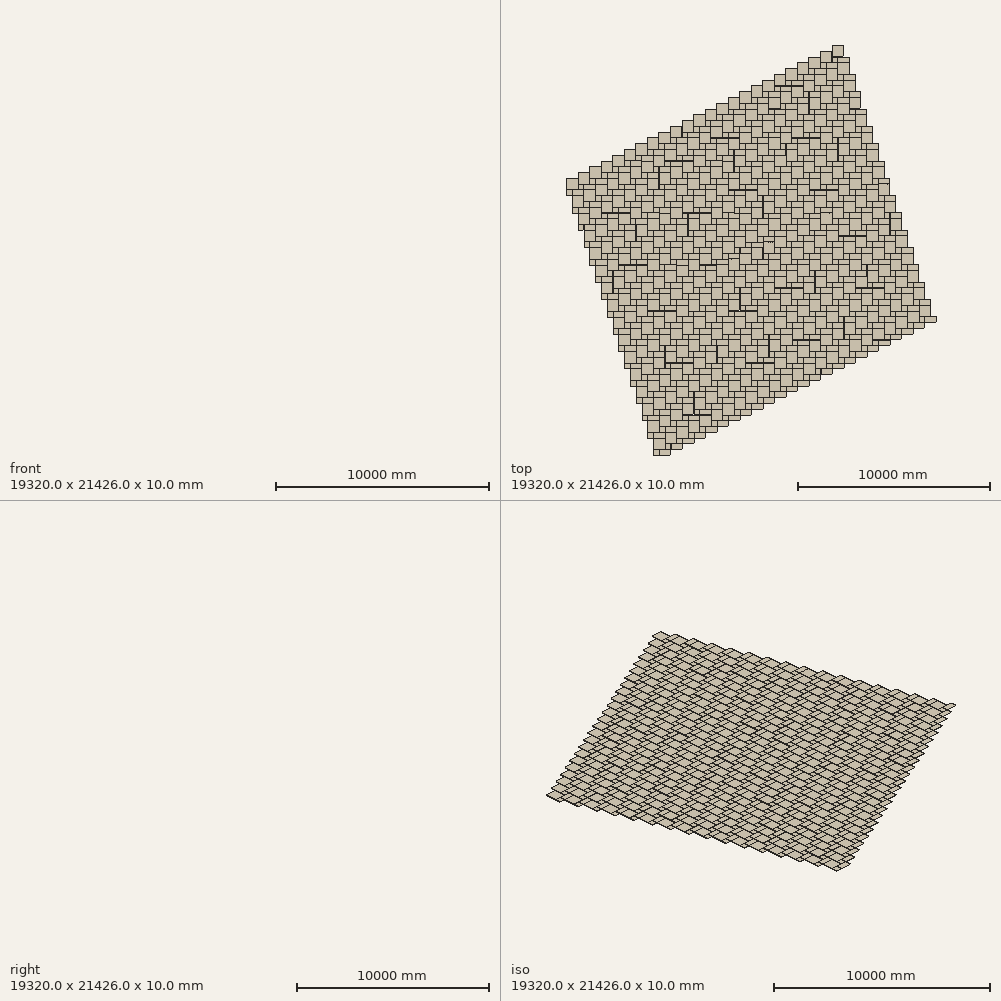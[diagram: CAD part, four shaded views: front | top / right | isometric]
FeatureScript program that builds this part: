
annotation { "Feature Type Name" : "Feature", "Feature Type Description" : "" }
export const myFeature = defineFeature(function(context is Context, id is Id, definition is map)
    precondition{}
    {
        {
            var Q0;
            Q0=qCreatedBy(makeId("Top.planeOp"),FACE);
            var sketch = newSketch(context, id + "F0", { "sketchPlane" : qUnion([Q0])});
            skLineSegment(sketch, "E0.bottom", {"start": v(-467.78, 21.53) * mm, "end": v(132.22, 21.53) * mm});
            skLineSegment(sketch, "E0.top", {"start": v(-467.78, 621.53) * mm, "end": v(132.22, 621.53) * mm});
            skLineSegment(sketch, "E0.left", {"start": v(-467.78, 21.53) * mm, "end": v(-467.78, 621.53) * mm});
            skLineSegment(sketch, "E0.right", {"start": v(132.22, 21.53) * mm, "end": v(132.22, 621.53) * mm});
            skLineSegment(sketch, "E1.bottom", {"start": v(-467.78, 18.53) * mm, "end": v(-167.78, 18.53) * mm});
            skLineSegment(sketch, "E1.top", {"start": v(-467.78, -281.47) * mm, "end": v(-167.78, -281.47) * mm});
            skLineSegment(sketch, "E1.left", {"start": v(-467.78, 18.53) * mm, "end": v(-467.78, -281.47) * mm});
            skLineSegment(sketch, "E1.right", {"start": v(-167.78, 18.53) * mm, "end": v(-167.78, -281.47) * mm});
            skLineSegment(sketch, "E2.bottom", {"start": v(-164.78, 18.53) * mm, "end": v(435.22, 18.53) * mm});
            skLineSegment(sketch, "E2.top", {"start": v(-164.78, -281.47) * mm, "end": v(435.22, -281.47) * mm});
            skLineSegment(sketch, "E2.left", {"start": v(-164.78, 18.53) * mm, "end": v(-164.78, -281.47) * mm});
            skLineSegment(sketch, "E2.right", {"start": v(435.22, 18.53) * mm, "end": v(435.22, -281.47) * mm});
            skSolve(sketch);
        }
        {
            var Q0;
            Q0 = qSketchRegion(id + "F0", true);
            extrude(context, id + "F1", {"entities" : qUnion([Q0]), "depth" : 10 * mm});
        }
        {
            var Q0;
            Q0=makeQuery(id+"F1.opExtrude","SWEPT_BODY",BODY,{"disambiguationData":[OSD([sQuery(id+"F0.wireOp",EDGE,"E0.bottom"),sQuery(id+"F0.wireOp",EDGE,"E0.top"),sQuery(id+"F0.wireOp",EDGE,"E0.left"),sQuery(id+"F0.wireOp",EDGE,"E0.right")])]});
            var Q1;
            Q1=makeQuery(id+"F1.opExtrude","SWEPT_BODY",BODY,{"disambiguationData":[OSD([sQuery(id+"F0.wireOp",EDGE,"E1.bottom"),sQuery(id+"F0.wireOp",EDGE,"E1.top"),sQuery(id+"F0.wireOp",EDGE,"E1.left"),sQuery(id+"F0.wireOp",EDGE,"E1.right")])]});
            var Q2;
            Q2=makeQuery(id+"F1.opExtrude","SWEPT_BODY",BODY,{"disambiguationData":[OSD([sQuery(id+"F0.wireOp",EDGE,"E2.bottom"),sQuery(id+"F0.wireOp",EDGE,"E2.top"),sQuery(id+"F0.wireOp",EDGE,"E2.left"),sQuery(id+"F0.wireOp",EDGE,"E2.right")])]});
            transform(context, id + "F2", {"entities" : qUnion([Q0, Q1, Q2]), "transformType" : TransformType.TRANSLATION_3D, "dx" : 603 * mm, "dy" : 303 * mm, "dz" : 0 * mm, "makeCopy" : true});
        }
        {
            var Q0;
            Q0=makeQuery(id+"F2.opPattern","COPY",BODY,{"derivedFrom":makeQuery(id+"F1.opExtrude","SWEPT_BODY",BODY,{"disambiguationData":[OSD([sQuery(id+"F0.wireOp",EDGE,"E0.bottom"),sQuery(id+"F0.wireOp",EDGE,"E0.top"),sQuery(id+"F0.wireOp",EDGE,"E0.left"),sQuery(id+"F0.wireOp",EDGE,"E0.right")])]}),"instanceName":"1"});
            var Q1;
            Q1=makeQuery(id+"F2.opPattern","COPY",BODY,{"derivedFrom":makeQuery(id+"F1.opExtrude","SWEPT_BODY",BODY,{"disambiguationData":[OSD([sQuery(id+"F0.wireOp",EDGE,"E1.bottom"),sQuery(id+"F0.wireOp",EDGE,"E1.top"),sQuery(id+"F0.wireOp",EDGE,"E1.left"),sQuery(id+"F0.wireOp",EDGE,"E1.right")])]}),"instanceName":"1"});
            var Q2;
            Q2=makeQuery(id+"F2.opPattern","COPY",BODY,{"derivedFrom":makeQuery(id+"F1.opExtrude","SWEPT_BODY",BODY,{"disambiguationData":[OSD([sQuery(id+"F0.wireOp",EDGE,"E2.bottom"),sQuery(id+"F0.wireOp",EDGE,"E2.top"),sQuery(id+"F0.wireOp",EDGE,"E2.left"),sQuery(id+"F0.wireOp",EDGE,"E2.right")])]}),"instanceName":"1"});
            transform(context, id + "F3", {"entities" : qUnion([Q0, Q1, Q2]), "transformType" : TransformType.TRANSLATION_3D, "dx" : 603 * mm, "dy" : 303 * mm, "dz" : 0 * mm, "makeCopy" : true});
        }
        {
            var Q0;
            Q0=makeQuery(id+"F3.opPattern","COPY",BODY,{"derivedFrom":makeQuery(id+"F2.opPattern","COPY",BODY,{"derivedFrom":makeQuery(id+"F1.opExtrude","SWEPT_BODY",BODY,{"disambiguationData":[OSD([sQuery(id+"F0.wireOp",EDGE,"E0.bottom"),sQuery(id+"F0.wireOp",EDGE,"E0.top"),sQuery(id+"F0.wireOp",EDGE,"E0.left"),sQuery(id+"F0.wireOp",EDGE,"E0.right")])]}),"instanceName":"1"}),"instanceName":"1"});
            var Q1;
            Q1=makeQuery(id+"F3.opPattern","COPY",BODY,{"derivedFrom":makeQuery(id+"F2.opPattern","COPY",BODY,{"derivedFrom":makeQuery(id+"F1.opExtrude","SWEPT_BODY",BODY,{"disambiguationData":[OSD([sQuery(id+"F0.wireOp",EDGE,"E1.bottom"),sQuery(id+"F0.wireOp",EDGE,"E1.top"),sQuery(id+"F0.wireOp",EDGE,"E1.left"),sQuery(id+"F0.wireOp",EDGE,"E1.right")])]}),"instanceName":"1"}),"instanceName":"1"});
            var Q2;
            Q2=makeQuery(id+"F3.opPattern","COPY",BODY,{"derivedFrom":makeQuery(id+"F2.opPattern","COPY",BODY,{"derivedFrom":makeQuery(id+"F1.opExtrude","SWEPT_BODY",BODY,{"disambiguationData":[OSD([sQuery(id+"F0.wireOp",EDGE,"E2.bottom"),sQuery(id+"F0.wireOp",EDGE,"E2.top"),sQuery(id+"F0.wireOp",EDGE,"E2.left"),sQuery(id+"F0.wireOp",EDGE,"E2.right")])]}),"instanceName":"1"}),"instanceName":"1"});
            transform(context, id + "F4", {"entities" : qUnion([Q0, Q1, Q2]), "transformType" : TransformType.TRANSLATION_3D, "dx" : 603 * mm, "dy" : 303 * mm, "dz" : 0 * mm, "makeCopy" : true});
        }
        {
            var Q0;
            Q0=makeQuery(id+"F4.opPattern","COPY",BODY,{"derivedFrom":makeQuery(id+"F3.opPattern","COPY",BODY,{"derivedFrom":makeQuery(id+"F2.opPattern","COPY",BODY,{"derivedFrom":makeQuery(id+"F1.opExtrude","SWEPT_BODY",BODY,{"disambiguationData":[OSD([sQuery(id+"F0.wireOp",EDGE,"E0.bottom"),sQuery(id+"F0.wireOp",EDGE,"E0.top"),sQuery(id+"F0.wireOp",EDGE,"E0.left"),sQuery(id+"F0.wireOp",EDGE,"E0.right")])]}),"instanceName":"1"}),"instanceName":"1"}),"instanceName":"1"});
            var Q1;
            Q1=makeQuery(id+"F4.opPattern","COPY",BODY,{"derivedFrom":makeQuery(id+"F3.opPattern","COPY",BODY,{"derivedFrom":makeQuery(id+"F2.opPattern","COPY",BODY,{"derivedFrom":makeQuery(id+"F1.opExtrude","SWEPT_BODY",BODY,{"disambiguationData":[OSD([sQuery(id+"F0.wireOp",EDGE,"E1.bottom"),sQuery(id+"F0.wireOp",EDGE,"E1.top"),sQuery(id+"F0.wireOp",EDGE,"E1.left"),sQuery(id+"F0.wireOp",EDGE,"E1.right")])]}),"instanceName":"1"}),"instanceName":"1"}),"instanceName":"1"});
            var Q2;
            Q2=makeQuery(id+"F4.opPattern","COPY",BODY,{"derivedFrom":makeQuery(id+"F3.opPattern","COPY",BODY,{"derivedFrom":makeQuery(id+"F2.opPattern","COPY",BODY,{"derivedFrom":makeQuery(id+"F1.opExtrude","SWEPT_BODY",BODY,{"disambiguationData":[OSD([sQuery(id+"F0.wireOp",EDGE,"E2.bottom"),sQuery(id+"F0.wireOp",EDGE,"E2.top"),sQuery(id+"F0.wireOp",EDGE,"E2.left"),sQuery(id+"F0.wireOp",EDGE,"E2.right")])]}),"instanceName":"1"}),"instanceName":"1"}),"instanceName":"1"});
            transform(context, id + "F5", {"entities" : qUnion([Q0, Q1, Q2]), "transformType" : TransformType.TRANSLATION_3D, "dx" : 603 * mm, "dy" : 303 * mm, "dz" : 0 * mm, "makeCopy" : true});
        }
        {
            var Q0;
            Q0=makeQuery(id+"F5.opPattern","COPY",BODY,{"derivedFrom":makeQuery(id+"F4.opPattern","COPY",BODY,{"derivedFrom":makeQuery(id+"F3.opPattern","COPY",BODY,{"derivedFrom":makeQuery(id+"F2.opPattern","COPY",BODY,{"derivedFrom":makeQuery(id+"F1.opExtrude","SWEPT_BODY",BODY,{"disambiguationData":[OSD([sQuery(id+"F0.wireOp",EDGE,"E0.bottom"),sQuery(id+"F0.wireOp",EDGE,"E0.top"),sQuery(id+"F0.wireOp",EDGE,"E0.left"),sQuery(id+"F0.wireOp",EDGE,"E0.right")])]}),"instanceName":"1"}),"instanceName":"1"}),"instanceName":"1"}),"instanceName":"1"});
            var Q1;
            Q1=makeQuery(id+"F5.opPattern","COPY",BODY,{"derivedFrom":makeQuery(id+"F4.opPattern","COPY",BODY,{"derivedFrom":makeQuery(id+"F3.opPattern","COPY",BODY,{"derivedFrom":makeQuery(id+"F2.opPattern","COPY",BODY,{"derivedFrom":makeQuery(id+"F1.opExtrude","SWEPT_BODY",BODY,{"disambiguationData":[OSD([sQuery(id+"F0.wireOp",EDGE,"E1.bottom"),sQuery(id+"F0.wireOp",EDGE,"E1.top"),sQuery(id+"F0.wireOp",EDGE,"E1.left"),sQuery(id+"F0.wireOp",EDGE,"E1.right")])]}),"instanceName":"1"}),"instanceName":"1"}),"instanceName":"1"}),"instanceName":"1"});
            var Q2;
            Q2=makeQuery(id+"F5.opPattern","COPY",BODY,{"derivedFrom":makeQuery(id+"F4.opPattern","COPY",BODY,{"derivedFrom":makeQuery(id+"F3.opPattern","COPY",BODY,{"derivedFrom":makeQuery(id+"F2.opPattern","COPY",BODY,{"derivedFrom":makeQuery(id+"F1.opExtrude","SWEPT_BODY",BODY,{"disambiguationData":[OSD([sQuery(id+"F0.wireOp",EDGE,"E2.bottom"),sQuery(id+"F0.wireOp",EDGE,"E2.top"),sQuery(id+"F0.wireOp",EDGE,"E2.left"),sQuery(id+"F0.wireOp",EDGE,"E2.right")])]}),"instanceName":"1"}),"instanceName":"1"}),"instanceName":"1"}),"instanceName":"1"});
            transform(context, id + "F6", {"entities" : qUnion([Q0, Q1, Q2]), "transformType" : TransformType.TRANSLATION_3D, "dx" : 603 * mm, "dy" : 303 * mm, "dz" : 0 * mm, "makeCopy" : true});
        }
        {
            var Q0;
            Q0=makeQuery(id+"F1.opExtrude","SWEPT_BODY",BODY,{"disambiguationData":[OSD([sQuery(id+"F0.wireOp",EDGE,"E1.bottom"),sQuery(id+"F0.wireOp",EDGE,"E1.top"),sQuery(id+"F0.wireOp",EDGE,"E1.left"),sQuery(id+"F0.wireOp",EDGE,"E1.right")])]});
            var Q1;
            Q1=makeQuery(id+"F1.opExtrude","SWEPT_BODY",BODY,{"disambiguationData":[OSD([sQuery(id+"F0.wireOp",EDGE,"E2.bottom"),sQuery(id+"F0.wireOp",EDGE,"E2.top"),sQuery(id+"F0.wireOp",EDGE,"E2.left"),sQuery(id+"F0.wireOp",EDGE,"E2.right")])]});
            var Q2;
            Q2=makeQuery(id+"F1.opExtrude","SWEPT_BODY",BODY,{"disambiguationData":[OSD([sQuery(id+"F0.wireOp",EDGE,"E0.bottom"),sQuery(id+"F0.wireOp",EDGE,"E0.top"),sQuery(id+"F0.wireOp",EDGE,"E0.left"),sQuery(id+"F0.wireOp",EDGE,"E0.right")])]});
            var Q3;
            Q3=makeQuery(id+"F2.opPattern","COPY",BODY,{"derivedFrom":makeQuery(id+"F1.opExtrude","SWEPT_BODY",BODY,{"disambiguationData":[OSD([sQuery(id+"F0.wireOp",EDGE,"E1.bottom"),sQuery(id+"F0.wireOp",EDGE,"E1.top"),sQuery(id+"F0.wireOp",EDGE,"E1.left"),sQuery(id+"F0.wireOp",EDGE,"E1.right")])]}),"instanceName":"1"});
            var Q4;
            Q4=makeQuery(id+"F2.opPattern","COPY",BODY,{"derivedFrom":makeQuery(id+"F1.opExtrude","SWEPT_BODY",BODY,{"disambiguationData":[OSD([sQuery(id+"F0.wireOp",EDGE,"E0.bottom"),sQuery(id+"F0.wireOp",EDGE,"E0.top"),sQuery(id+"F0.wireOp",EDGE,"E0.left"),sQuery(id+"F0.wireOp",EDGE,"E0.right")])]}),"instanceName":"1"});
            var Q5;
            Q5=makeQuery(id+"F2.opPattern","COPY",BODY,{"derivedFrom":makeQuery(id+"F1.opExtrude","SWEPT_BODY",BODY,{"disambiguationData":[OSD([sQuery(id+"F0.wireOp",EDGE,"E2.bottom"),sQuery(id+"F0.wireOp",EDGE,"E2.top"),sQuery(id+"F0.wireOp",EDGE,"E2.left"),sQuery(id+"F0.wireOp",EDGE,"E2.right")])]}),"instanceName":"1"});
            var Q6;
            Q6=makeQuery(id+"F3.opPattern","COPY",BODY,{"derivedFrom":makeQuery(id+"F2.opPattern","COPY",BODY,{"derivedFrom":makeQuery(id+"F1.opExtrude","SWEPT_BODY",BODY,{"disambiguationData":[OSD([sQuery(id+"F0.wireOp",EDGE,"E1.bottom"),sQuery(id+"F0.wireOp",EDGE,"E1.top"),sQuery(id+"F0.wireOp",EDGE,"E1.left"),sQuery(id+"F0.wireOp",EDGE,"E1.right")])]}),"instanceName":"1"}),"instanceName":"1"});
            var Q7;
            Q7=makeQuery(id+"F3.opPattern","COPY",BODY,{"derivedFrom":makeQuery(id+"F2.opPattern","COPY",BODY,{"derivedFrom":makeQuery(id+"F1.opExtrude","SWEPT_BODY",BODY,{"disambiguationData":[OSD([sQuery(id+"F0.wireOp",EDGE,"E2.bottom"),sQuery(id+"F0.wireOp",EDGE,"E2.top"),sQuery(id+"F0.wireOp",EDGE,"E2.left"),sQuery(id+"F0.wireOp",EDGE,"E2.right")])]}),"instanceName":"1"}),"instanceName":"1"});
            var Q8;
            Q8=makeQuery(id+"F3.opPattern","COPY",BODY,{"derivedFrom":makeQuery(id+"F2.opPattern","COPY",BODY,{"derivedFrom":makeQuery(id+"F1.opExtrude","SWEPT_BODY",BODY,{"disambiguationData":[OSD([sQuery(id+"F0.wireOp",EDGE,"E0.bottom"),sQuery(id+"F0.wireOp",EDGE,"E0.top"),sQuery(id+"F0.wireOp",EDGE,"E0.left"),sQuery(id+"F0.wireOp",EDGE,"E0.right")])]}),"instanceName":"1"}),"instanceName":"1"});
            var Q9;
            Q9=makeQuery(id+"F4.opPattern","COPY",BODY,{"derivedFrom":makeQuery(id+"F3.opPattern","COPY",BODY,{"derivedFrom":makeQuery(id+"F2.opPattern","COPY",BODY,{"derivedFrom":makeQuery(id+"F1.opExtrude","SWEPT_BODY",BODY,{"disambiguationData":[OSD([sQuery(id+"F0.wireOp",EDGE,"E1.bottom"),sQuery(id+"F0.wireOp",EDGE,"E1.top"),sQuery(id+"F0.wireOp",EDGE,"E1.left"),sQuery(id+"F0.wireOp",EDGE,"E1.right")])]}),"instanceName":"1"}),"instanceName":"1"}),"instanceName":"1"});
            var Q10;
            Q10=makeQuery(id+"F4.opPattern","COPY",BODY,{"derivedFrom":makeQuery(id+"F3.opPattern","COPY",BODY,{"derivedFrom":makeQuery(id+"F2.opPattern","COPY",BODY,{"derivedFrom":makeQuery(id+"F1.opExtrude","SWEPT_BODY",BODY,{"disambiguationData":[OSD([sQuery(id+"F0.wireOp",EDGE,"E2.bottom"),sQuery(id+"F0.wireOp",EDGE,"E2.top"),sQuery(id+"F0.wireOp",EDGE,"E2.left"),sQuery(id+"F0.wireOp",EDGE,"E2.right")])]}),"instanceName":"1"}),"instanceName":"1"}),"instanceName":"1"});
            var Q11;
            Q11=makeQuery(id+"F4.opPattern","COPY",BODY,{"derivedFrom":makeQuery(id+"F3.opPattern","COPY",BODY,{"derivedFrom":makeQuery(id+"F2.opPattern","COPY",BODY,{"derivedFrom":makeQuery(id+"F1.opExtrude","SWEPT_BODY",BODY,{"disambiguationData":[OSD([sQuery(id+"F0.wireOp",EDGE,"E0.bottom"),sQuery(id+"F0.wireOp",EDGE,"E0.top"),sQuery(id+"F0.wireOp",EDGE,"E0.left"),sQuery(id+"F0.wireOp",EDGE,"E0.right")])]}),"instanceName":"1"}),"instanceName":"1"}),"instanceName":"1"});
            var Q12;
            Q12=makeQuery(id+"F5.opPattern","COPY",BODY,{"derivedFrom":makeQuery(id+"F4.opPattern","COPY",BODY,{"derivedFrom":makeQuery(id+"F3.opPattern","COPY",BODY,{"derivedFrom":makeQuery(id+"F2.opPattern","COPY",BODY,{"derivedFrom":makeQuery(id+"F1.opExtrude","SWEPT_BODY",BODY,{"disambiguationData":[OSD([sQuery(id+"F0.wireOp",EDGE,"E1.bottom"),sQuery(id+"F0.wireOp",EDGE,"E1.top"),sQuery(id+"F0.wireOp",EDGE,"E1.left"),sQuery(id+"F0.wireOp",EDGE,"E1.right")])]}),"instanceName":"1"}),"instanceName":"1"}),"instanceName":"1"}),"instanceName":"1"});
            var Q13;
            Q13=makeQuery(id+"F5.opPattern","COPY",BODY,{"derivedFrom":makeQuery(id+"F4.opPattern","COPY",BODY,{"derivedFrom":makeQuery(id+"F3.opPattern","COPY",BODY,{"derivedFrom":makeQuery(id+"F2.opPattern","COPY",BODY,{"derivedFrom":makeQuery(id+"F1.opExtrude","SWEPT_BODY",BODY,{"disambiguationData":[OSD([sQuery(id+"F0.wireOp",EDGE,"E2.bottom"),sQuery(id+"F0.wireOp",EDGE,"E2.top"),sQuery(id+"F0.wireOp",EDGE,"E2.left"),sQuery(id+"F0.wireOp",EDGE,"E2.right")])]}),"instanceName":"1"}),"instanceName":"1"}),"instanceName":"1"}),"instanceName":"1"});
            var Q14;
            Q14=makeQuery(id+"F5.opPattern","COPY",BODY,{"derivedFrom":makeQuery(id+"F4.opPattern","COPY",BODY,{"derivedFrom":makeQuery(id+"F3.opPattern","COPY",BODY,{"derivedFrom":makeQuery(id+"F2.opPattern","COPY",BODY,{"derivedFrom":makeQuery(id+"F1.opExtrude","SWEPT_BODY",BODY,{"disambiguationData":[OSD([sQuery(id+"F0.wireOp",EDGE,"E0.bottom"),sQuery(id+"F0.wireOp",EDGE,"E0.top"),sQuery(id+"F0.wireOp",EDGE,"E0.left"),sQuery(id+"F0.wireOp",EDGE,"E0.right")])]}),"instanceName":"1"}),"instanceName":"1"}),"instanceName":"1"}),"instanceName":"1"});
            var Q15;
            Q15=makeQuery(id+"F6.opPattern","COPY",BODY,{"derivedFrom":makeQuery(id+"F5.opPattern","COPY",BODY,{"derivedFrom":makeQuery(id+"F4.opPattern","COPY",BODY,{"derivedFrom":makeQuery(id+"F3.opPattern","COPY",BODY,{"derivedFrom":makeQuery(id+"F2.opPattern","COPY",BODY,{"derivedFrom":makeQuery(id+"F1.opExtrude","SWEPT_BODY",BODY,{"disambiguationData":[OSD([sQuery(id+"F0.wireOp",EDGE,"E1.bottom"),sQuery(id+"F0.wireOp",EDGE,"E1.top"),sQuery(id+"F0.wireOp",EDGE,"E1.left"),sQuery(id+"F0.wireOp",EDGE,"E1.right")])]}),"instanceName":"1"}),"instanceName":"1"}),"instanceName":"1"}),"instanceName":"1"}),"instanceName":"1"});
            var Q16;
            Q16=makeQuery(id+"F6.opPattern","COPY",BODY,{"derivedFrom":makeQuery(id+"F5.opPattern","COPY",BODY,{"derivedFrom":makeQuery(id+"F4.opPattern","COPY",BODY,{"derivedFrom":makeQuery(id+"F3.opPattern","COPY",BODY,{"derivedFrom":makeQuery(id+"F2.opPattern","COPY",BODY,{"derivedFrom":makeQuery(id+"F1.opExtrude","SWEPT_BODY",BODY,{"disambiguationData":[OSD([sQuery(id+"F0.wireOp",EDGE,"E0.bottom"),sQuery(id+"F0.wireOp",EDGE,"E0.top"),sQuery(id+"F0.wireOp",EDGE,"E0.left"),sQuery(id+"F0.wireOp",EDGE,"E0.right")])]}),"instanceName":"1"}),"instanceName":"1"}),"instanceName":"1"}),"instanceName":"1"}),"instanceName":"1"});
            var Q17;
            Q17=makeQuery(id+"F6.opPattern","COPY",BODY,{"derivedFrom":makeQuery(id+"F5.opPattern","COPY",BODY,{"derivedFrom":makeQuery(id+"F4.opPattern","COPY",BODY,{"derivedFrom":makeQuery(id+"F3.opPattern","COPY",BODY,{"derivedFrom":makeQuery(id+"F2.opPattern","COPY",BODY,{"derivedFrom":makeQuery(id+"F1.opExtrude","SWEPT_BODY",BODY,{"disambiguationData":[OSD([sQuery(id+"F0.wireOp",EDGE,"E2.bottom"),sQuery(id+"F0.wireOp",EDGE,"E2.top"),sQuery(id+"F0.wireOp",EDGE,"E2.left"),sQuery(id+"F0.wireOp",EDGE,"E2.right")])]}),"instanceName":"1"}),"instanceName":"1"}),"instanceName":"1"}),"instanceName":"1"}),"instanceName":"1"});
            transform(context, id + "F7", {"entities" : qUnion([Q0, Q1, Q2, Q3, Q4, Q5, Q6, Q7, Q8, Q9, Q10, Q11, Q12, Q13, Q14, Q15, Q16, Q17]), "transformType" : TransformType.TRANSLATION_3D, "dx" : -303 * mm, "dy" : 906 * mm, "dz" : 0 * mm, "makeCopy" : true});
        }
        {
            var Q0;
            Q0=makeQuery(id+"F1.opExtrude","SWEPT_BODY",BODY,{"disambiguationData":[OSD([sQuery(id+"F0.wireOp",EDGE,"E1.bottom"),sQuery(id+"F0.wireOp",EDGE,"E1.top"),sQuery(id+"F0.wireOp",EDGE,"E1.left"),sQuery(id+"F0.wireOp",EDGE,"E1.right")])]});
            var Q1;
            Q1=makeQuery(id+"F1.opExtrude","SWEPT_BODY",BODY,{"disambiguationData":[OSD([sQuery(id+"F0.wireOp",EDGE,"E2.bottom"),sQuery(id+"F0.wireOp",EDGE,"E2.top"),sQuery(id+"F0.wireOp",EDGE,"E2.left"),sQuery(id+"F0.wireOp",EDGE,"E2.right")])]});
            var Q2;
            Q2=makeQuery(id+"F1.opExtrude","SWEPT_BODY",BODY,{"disambiguationData":[OSD([sQuery(id+"F0.wireOp",EDGE,"E0.bottom"),sQuery(id+"F0.wireOp",EDGE,"E0.top"),sQuery(id+"F0.wireOp",EDGE,"E0.left"),sQuery(id+"F0.wireOp",EDGE,"E0.right")])]});
            var Q3;
            Q3=makeQuery(id+"F2.opPattern","COPY",BODY,{"derivedFrom":makeQuery(id+"F1.opExtrude","SWEPT_BODY",BODY,{"disambiguationData":[OSD([sQuery(id+"F0.wireOp",EDGE,"E1.bottom"),sQuery(id+"F0.wireOp",EDGE,"E1.top"),sQuery(id+"F0.wireOp",EDGE,"E1.left"),sQuery(id+"F0.wireOp",EDGE,"E1.right")])]}),"instanceName":"1"});
            var Q4;
            Q4=makeQuery(id+"F2.opPattern","COPY",BODY,{"derivedFrom":makeQuery(id+"F1.opExtrude","SWEPT_BODY",BODY,{"disambiguationData":[OSD([sQuery(id+"F0.wireOp",EDGE,"E2.bottom"),sQuery(id+"F0.wireOp",EDGE,"E2.top"),sQuery(id+"F0.wireOp",EDGE,"E2.left"),sQuery(id+"F0.wireOp",EDGE,"E2.right")])]}),"instanceName":"1"});
            var Q5;
            Q5=makeQuery(id+"F2.opPattern","COPY",BODY,{"derivedFrom":makeQuery(id+"F1.opExtrude","SWEPT_BODY",BODY,{"disambiguationData":[OSD([sQuery(id+"F0.wireOp",EDGE,"E0.bottom"),sQuery(id+"F0.wireOp",EDGE,"E0.top"),sQuery(id+"F0.wireOp",EDGE,"E0.left"),sQuery(id+"F0.wireOp",EDGE,"E0.right")])]}),"instanceName":"1"});
            var Q6;
            Q6=makeQuery(id+"F3.opPattern","COPY",BODY,{"derivedFrom":makeQuery(id+"F2.opPattern","COPY",BODY,{"derivedFrom":makeQuery(id+"F1.opExtrude","SWEPT_BODY",BODY,{"disambiguationData":[OSD([sQuery(id+"F0.wireOp",EDGE,"E1.bottom"),sQuery(id+"F0.wireOp",EDGE,"E1.top"),sQuery(id+"F0.wireOp",EDGE,"E1.left"),sQuery(id+"F0.wireOp",EDGE,"E1.right")])]}),"instanceName":"1"}),"instanceName":"1"});
            var Q7;
            Q7=makeQuery(id+"F3.opPattern","COPY",BODY,{"derivedFrom":makeQuery(id+"F2.opPattern","COPY",BODY,{"derivedFrom":makeQuery(id+"F1.opExtrude","SWEPT_BODY",BODY,{"disambiguationData":[OSD([sQuery(id+"F0.wireOp",EDGE,"E2.bottom"),sQuery(id+"F0.wireOp",EDGE,"E2.top"),sQuery(id+"F0.wireOp",EDGE,"E2.left"),sQuery(id+"F0.wireOp",EDGE,"E2.right")])]}),"instanceName":"1"}),"instanceName":"1"});
            var Q8;
            Q8=makeQuery(id+"F3.opPattern","COPY",BODY,{"derivedFrom":makeQuery(id+"F2.opPattern","COPY",BODY,{"derivedFrom":makeQuery(id+"F1.opExtrude","SWEPT_BODY",BODY,{"disambiguationData":[OSD([sQuery(id+"F0.wireOp",EDGE,"E0.bottom"),sQuery(id+"F0.wireOp",EDGE,"E0.top"),sQuery(id+"F0.wireOp",EDGE,"E0.left"),sQuery(id+"F0.wireOp",EDGE,"E0.right")])]}),"instanceName":"1"}),"instanceName":"1"});
            var Q9;
            Q9=makeQuery(id+"F4.opPattern","COPY",BODY,{"derivedFrom":makeQuery(id+"F3.opPattern","COPY",BODY,{"derivedFrom":makeQuery(id+"F2.opPattern","COPY",BODY,{"derivedFrom":makeQuery(id+"F1.opExtrude","SWEPT_BODY",BODY,{"disambiguationData":[OSD([sQuery(id+"F0.wireOp",EDGE,"E1.bottom"),sQuery(id+"F0.wireOp",EDGE,"E1.top"),sQuery(id+"F0.wireOp",EDGE,"E1.left"),sQuery(id+"F0.wireOp",EDGE,"E1.right")])]}),"instanceName":"1"}),"instanceName":"1"}),"instanceName":"1"});
            var Q10;
            Q10=makeQuery(id+"F4.opPattern","COPY",BODY,{"derivedFrom":makeQuery(id+"F3.opPattern","COPY",BODY,{"derivedFrom":makeQuery(id+"F2.opPattern","COPY",BODY,{"derivedFrom":makeQuery(id+"F1.opExtrude","SWEPT_BODY",BODY,{"disambiguationData":[OSD([sQuery(id+"F0.wireOp",EDGE,"E2.bottom"),sQuery(id+"F0.wireOp",EDGE,"E2.top"),sQuery(id+"F0.wireOp",EDGE,"E2.left"),sQuery(id+"F0.wireOp",EDGE,"E2.right")])]}),"instanceName":"1"}),"instanceName":"1"}),"instanceName":"1"});
            var Q11;
            Q11=makeQuery(id+"F4.opPattern","COPY",BODY,{"derivedFrom":makeQuery(id+"F3.opPattern","COPY",BODY,{"derivedFrom":makeQuery(id+"F2.opPattern","COPY",BODY,{"derivedFrom":makeQuery(id+"F1.opExtrude","SWEPT_BODY",BODY,{"disambiguationData":[OSD([sQuery(id+"F0.wireOp",EDGE,"E0.bottom"),sQuery(id+"F0.wireOp",EDGE,"E0.top"),sQuery(id+"F0.wireOp",EDGE,"E0.left"),sQuery(id+"F0.wireOp",EDGE,"E0.right")])]}),"instanceName":"1"}),"instanceName":"1"}),"instanceName":"1"});
            var Q12;
            Q12=makeQuery(id+"F5.opPattern","COPY",BODY,{"derivedFrom":makeQuery(id+"F4.opPattern","COPY",BODY,{"derivedFrom":makeQuery(id+"F3.opPattern","COPY",BODY,{"derivedFrom":makeQuery(id+"F2.opPattern","COPY",BODY,{"derivedFrom":makeQuery(id+"F1.opExtrude","SWEPT_BODY",BODY,{"disambiguationData":[OSD([sQuery(id+"F0.wireOp",EDGE,"E1.bottom"),sQuery(id+"F0.wireOp",EDGE,"E1.top"),sQuery(id+"F0.wireOp",EDGE,"E1.left"),sQuery(id+"F0.wireOp",EDGE,"E1.right")])]}),"instanceName":"1"}),"instanceName":"1"}),"instanceName":"1"}),"instanceName":"1"});
            var Q13;
            Q13=makeQuery(id+"F5.opPattern","COPY",BODY,{"derivedFrom":makeQuery(id+"F4.opPattern","COPY",BODY,{"derivedFrom":makeQuery(id+"F3.opPattern","COPY",BODY,{"derivedFrom":makeQuery(id+"F2.opPattern","COPY",BODY,{"derivedFrom":makeQuery(id+"F1.opExtrude","SWEPT_BODY",BODY,{"disambiguationData":[OSD([sQuery(id+"F0.wireOp",EDGE,"E2.bottom"),sQuery(id+"F0.wireOp",EDGE,"E2.top"),sQuery(id+"F0.wireOp",EDGE,"E2.left"),sQuery(id+"F0.wireOp",EDGE,"E2.right")])]}),"instanceName":"1"}),"instanceName":"1"}),"instanceName":"1"}),"instanceName":"1"});
            var Q14;
            Q14=makeQuery(id+"F5.opPattern","COPY",BODY,{"derivedFrom":makeQuery(id+"F4.opPattern","COPY",BODY,{"derivedFrom":makeQuery(id+"F3.opPattern","COPY",BODY,{"derivedFrom":makeQuery(id+"F2.opPattern","COPY",BODY,{"derivedFrom":makeQuery(id+"F1.opExtrude","SWEPT_BODY",BODY,{"disambiguationData":[OSD([sQuery(id+"F0.wireOp",EDGE,"E0.bottom"),sQuery(id+"F0.wireOp",EDGE,"E0.top"),sQuery(id+"F0.wireOp",EDGE,"E0.left"),sQuery(id+"F0.wireOp",EDGE,"E0.right")])]}),"instanceName":"1"}),"instanceName":"1"}),"instanceName":"1"}),"instanceName":"1"});
            var Q15;
            Q15=makeQuery(id+"F6.opPattern","COPY",BODY,{"derivedFrom":makeQuery(id+"F5.opPattern","COPY",BODY,{"derivedFrom":makeQuery(id+"F4.opPattern","COPY",BODY,{"derivedFrom":makeQuery(id+"F3.opPattern","COPY",BODY,{"derivedFrom":makeQuery(id+"F2.opPattern","COPY",BODY,{"derivedFrom":makeQuery(id+"F1.opExtrude","SWEPT_BODY",BODY,{"disambiguationData":[OSD([sQuery(id+"F0.wireOp",EDGE,"E1.bottom"),sQuery(id+"F0.wireOp",EDGE,"E1.top"),sQuery(id+"F0.wireOp",EDGE,"E1.left"),sQuery(id+"F0.wireOp",EDGE,"E1.right")])]}),"instanceName":"1"}),"instanceName":"1"}),"instanceName":"1"}),"instanceName":"1"}),"instanceName":"1"});
            var Q16;
            Q16=makeQuery(id+"F6.opPattern","COPY",BODY,{"derivedFrom":makeQuery(id+"F5.opPattern","COPY",BODY,{"derivedFrom":makeQuery(id+"F4.opPattern","COPY",BODY,{"derivedFrom":makeQuery(id+"F3.opPattern","COPY",BODY,{"derivedFrom":makeQuery(id+"F2.opPattern","COPY",BODY,{"derivedFrom":makeQuery(id+"F1.opExtrude","SWEPT_BODY",BODY,{"disambiguationData":[OSD([sQuery(id+"F0.wireOp",EDGE,"E2.bottom"),sQuery(id+"F0.wireOp",EDGE,"E2.top"),sQuery(id+"F0.wireOp",EDGE,"E2.left"),sQuery(id+"F0.wireOp",EDGE,"E2.right")])]}),"instanceName":"1"}),"instanceName":"1"}),"instanceName":"1"}),"instanceName":"1"}),"instanceName":"1"});
            var Q17;
            Q17=makeQuery(id+"F6.opPattern","COPY",BODY,{"derivedFrom":makeQuery(id+"F5.opPattern","COPY",BODY,{"derivedFrom":makeQuery(id+"F4.opPattern","COPY",BODY,{"derivedFrom":makeQuery(id+"F3.opPattern","COPY",BODY,{"derivedFrom":makeQuery(id+"F2.opPattern","COPY",BODY,{"derivedFrom":makeQuery(id+"F1.opExtrude","SWEPT_BODY",BODY,{"disambiguationData":[OSD([sQuery(id+"F0.wireOp",EDGE,"E0.bottom"),sQuery(id+"F0.wireOp",EDGE,"E0.top"),sQuery(id+"F0.wireOp",EDGE,"E0.left"),sQuery(id+"F0.wireOp",EDGE,"E0.right")])]}),"instanceName":"1"}),"instanceName":"1"}),"instanceName":"1"}),"instanceName":"1"}),"instanceName":"1"});
            var Q18;
            Q18=makeQuery(id+"F7.opPattern","COPY",BODY,{"derivedFrom":makeQuery(id+"F6.opPattern","COPY",BODY,{"derivedFrom":makeQuery(id+"F5.opPattern","COPY",BODY,{"derivedFrom":makeQuery(id+"F4.opPattern","COPY",BODY,{"derivedFrom":makeQuery(id+"F3.opPattern","COPY",BODY,{"derivedFrom":makeQuery(id+"F2.opPattern","COPY",BODY,{"derivedFrom":makeQuery(id+"F1.opExtrude","SWEPT_BODY",BODY,{"disambiguationData":[OSD([sQuery(id+"F0.wireOp",EDGE,"E0.bottom"),sQuery(id+"F0.wireOp",EDGE,"E0.top"),sQuery(id+"F0.wireOp",EDGE,"E0.left"),sQuery(id+"F0.wireOp",EDGE,"E0.right")])]}),"instanceName":"1"}),"instanceName":"1"}),"instanceName":"1"}),"instanceName":"1"}),"instanceName":"1"}),"instanceName":"1"});
            var Q19;
            Q19=makeQuery(id+"F7.opPattern","COPY",BODY,{"derivedFrom":makeQuery(id+"F6.opPattern","COPY",BODY,{"derivedFrom":makeQuery(id+"F5.opPattern","COPY",BODY,{"derivedFrom":makeQuery(id+"F4.opPattern","COPY",BODY,{"derivedFrom":makeQuery(id+"F3.opPattern","COPY",BODY,{"derivedFrom":makeQuery(id+"F2.opPattern","COPY",BODY,{"derivedFrom":makeQuery(id+"F1.opExtrude","SWEPT_BODY",BODY,{"disambiguationData":[OSD([sQuery(id+"F0.wireOp",EDGE,"E1.bottom"),sQuery(id+"F0.wireOp",EDGE,"E1.top"),sQuery(id+"F0.wireOp",EDGE,"E1.left"),sQuery(id+"F0.wireOp",EDGE,"E1.right")])]}),"instanceName":"1"}),"instanceName":"1"}),"instanceName":"1"}),"instanceName":"1"}),"instanceName":"1"}),"instanceName":"1"});
            var Q20;
            Q20=makeQuery(id+"F7.opPattern","COPY",BODY,{"derivedFrom":makeQuery(id+"F5.opPattern","COPY",BODY,{"derivedFrom":makeQuery(id+"F4.opPattern","COPY",BODY,{"derivedFrom":makeQuery(id+"F3.opPattern","COPY",BODY,{"derivedFrom":makeQuery(id+"F2.opPattern","COPY",BODY,{"derivedFrom":makeQuery(id+"F1.opExtrude","SWEPT_BODY",BODY,{"disambiguationData":[OSD([sQuery(id+"F0.wireOp",EDGE,"E2.bottom"),sQuery(id+"F0.wireOp",EDGE,"E2.top"),sQuery(id+"F0.wireOp",EDGE,"E2.left"),sQuery(id+"F0.wireOp",EDGE,"E2.right")])]}),"instanceName":"1"}),"instanceName":"1"}),"instanceName":"1"}),"instanceName":"1"}),"instanceName":"1"});
            var Q21;
            Q21=makeQuery(id+"F7.opPattern","COPY",BODY,{"derivedFrom":makeQuery(id+"F5.opPattern","COPY",BODY,{"derivedFrom":makeQuery(id+"F4.opPattern","COPY",BODY,{"derivedFrom":makeQuery(id+"F3.opPattern","COPY",BODY,{"derivedFrom":makeQuery(id+"F2.opPattern","COPY",BODY,{"derivedFrom":makeQuery(id+"F1.opExtrude","SWEPT_BODY",BODY,{"disambiguationData":[OSD([sQuery(id+"F0.wireOp",EDGE,"E0.bottom"),sQuery(id+"F0.wireOp",EDGE,"E0.top"),sQuery(id+"F0.wireOp",EDGE,"E0.left"),sQuery(id+"F0.wireOp",EDGE,"E0.right")])]}),"instanceName":"1"}),"instanceName":"1"}),"instanceName":"1"}),"instanceName":"1"}),"instanceName":"1"});
            var Q22;
            Q22=makeQuery(id+"F7.opPattern","COPY",BODY,{"derivedFrom":makeQuery(id+"F5.opPattern","COPY",BODY,{"derivedFrom":makeQuery(id+"F4.opPattern","COPY",BODY,{"derivedFrom":makeQuery(id+"F3.opPattern","COPY",BODY,{"derivedFrom":makeQuery(id+"F2.opPattern","COPY",BODY,{"derivedFrom":makeQuery(id+"F1.opExtrude","SWEPT_BODY",BODY,{"disambiguationData":[OSD([sQuery(id+"F0.wireOp",EDGE,"E1.bottom"),sQuery(id+"F0.wireOp",EDGE,"E1.top"),sQuery(id+"F0.wireOp",EDGE,"E1.left"),sQuery(id+"F0.wireOp",EDGE,"E1.right")])]}),"instanceName":"1"}),"instanceName":"1"}),"instanceName":"1"}),"instanceName":"1"}),"instanceName":"1"});
            var Q23;
            Q23=makeQuery(id+"F7.opPattern","COPY",BODY,{"derivedFrom":makeQuery(id+"F4.opPattern","COPY",BODY,{"derivedFrom":makeQuery(id+"F3.opPattern","COPY",BODY,{"derivedFrom":makeQuery(id+"F2.opPattern","COPY",BODY,{"derivedFrom":makeQuery(id+"F1.opExtrude","SWEPT_BODY",BODY,{"disambiguationData":[OSD([sQuery(id+"F0.wireOp",EDGE,"E2.bottom"),sQuery(id+"F0.wireOp",EDGE,"E2.top"),sQuery(id+"F0.wireOp",EDGE,"E2.left"),sQuery(id+"F0.wireOp",EDGE,"E2.right")])]}),"instanceName":"1"}),"instanceName":"1"}),"instanceName":"1"}),"instanceName":"1"});
            var Q24;
            Q24=makeQuery(id+"F7.opPattern","COPY",BODY,{"derivedFrom":makeQuery(id+"F4.opPattern","COPY",BODY,{"derivedFrom":makeQuery(id+"F3.opPattern","COPY",BODY,{"derivedFrom":makeQuery(id+"F2.opPattern","COPY",BODY,{"derivedFrom":makeQuery(id+"F1.opExtrude","SWEPT_BODY",BODY,{"disambiguationData":[OSD([sQuery(id+"F0.wireOp",EDGE,"E0.bottom"),sQuery(id+"F0.wireOp",EDGE,"E0.top"),sQuery(id+"F0.wireOp",EDGE,"E0.left"),sQuery(id+"F0.wireOp",EDGE,"E0.right")])]}),"instanceName":"1"}),"instanceName":"1"}),"instanceName":"1"}),"instanceName":"1"});
            var Q25;
            Q25=makeQuery(id+"F7.opPattern","COPY",BODY,{"derivedFrom":makeQuery(id+"F4.opPattern","COPY",BODY,{"derivedFrom":makeQuery(id+"F3.opPattern","COPY",BODY,{"derivedFrom":makeQuery(id+"F2.opPattern","COPY",BODY,{"derivedFrom":makeQuery(id+"F1.opExtrude","SWEPT_BODY",BODY,{"disambiguationData":[OSD([sQuery(id+"F0.wireOp",EDGE,"E1.bottom"),sQuery(id+"F0.wireOp",EDGE,"E1.top"),sQuery(id+"F0.wireOp",EDGE,"E1.left"),sQuery(id+"F0.wireOp",EDGE,"E1.right")])]}),"instanceName":"1"}),"instanceName":"1"}),"instanceName":"1"}),"instanceName":"1"});
            var Q26;
            Q26=makeQuery(id+"F7.opPattern","COPY",BODY,{"derivedFrom":makeQuery(id+"F3.opPattern","COPY",BODY,{"derivedFrom":makeQuery(id+"F2.opPattern","COPY",BODY,{"derivedFrom":makeQuery(id+"F1.opExtrude","SWEPT_BODY",BODY,{"disambiguationData":[OSD([sQuery(id+"F0.wireOp",EDGE,"E2.bottom"),sQuery(id+"F0.wireOp",EDGE,"E2.top"),sQuery(id+"F0.wireOp",EDGE,"E2.left"),sQuery(id+"F0.wireOp",EDGE,"E2.right")])]}),"instanceName":"1"}),"instanceName":"1"}),"instanceName":"1"});
            var Q27;
            Q27=makeQuery(id+"F7.opPattern","COPY",BODY,{"derivedFrom":makeQuery(id+"F3.opPattern","COPY",BODY,{"derivedFrom":makeQuery(id+"F2.opPattern","COPY",BODY,{"derivedFrom":makeQuery(id+"F1.opExtrude","SWEPT_BODY",BODY,{"disambiguationData":[OSD([sQuery(id+"F0.wireOp",EDGE,"E1.bottom"),sQuery(id+"F0.wireOp",EDGE,"E1.top"),sQuery(id+"F0.wireOp",EDGE,"E1.left"),sQuery(id+"F0.wireOp",EDGE,"E1.right")])]}),"instanceName":"1"}),"instanceName":"1"}),"instanceName":"1"});
            var Q28;
            Q28=makeQuery(id+"F7.opPattern","COPY",BODY,{"derivedFrom":makeQuery(id+"F3.opPattern","COPY",BODY,{"derivedFrom":makeQuery(id+"F2.opPattern","COPY",BODY,{"derivedFrom":makeQuery(id+"F1.opExtrude","SWEPT_BODY",BODY,{"disambiguationData":[OSD([sQuery(id+"F0.wireOp",EDGE,"E0.bottom"),sQuery(id+"F0.wireOp",EDGE,"E0.top"),sQuery(id+"F0.wireOp",EDGE,"E0.left"),sQuery(id+"F0.wireOp",EDGE,"E0.right")])]}),"instanceName":"1"}),"instanceName":"1"}),"instanceName":"1"});
            var Q29;
            Q29=makeQuery(id+"F7.opPattern","COPY",BODY,{"derivedFrom":makeQuery(id+"F2.opPattern","COPY",BODY,{"derivedFrom":makeQuery(id+"F1.opExtrude","SWEPT_BODY",BODY,{"disambiguationData":[OSD([sQuery(id+"F0.wireOp",EDGE,"E0.bottom"),sQuery(id+"F0.wireOp",EDGE,"E0.top"),sQuery(id+"F0.wireOp",EDGE,"E0.left"),sQuery(id+"F0.wireOp",EDGE,"E0.right")])]}),"instanceName":"1"}),"instanceName":"1"});
            var Q30;
            Q30=makeQuery(id+"F7.opPattern","COPY",BODY,{"derivedFrom":makeQuery(id+"F2.opPattern","COPY",BODY,{"derivedFrom":makeQuery(id+"F1.opExtrude","SWEPT_BODY",BODY,{"disambiguationData":[OSD([sQuery(id+"F0.wireOp",EDGE,"E2.bottom"),sQuery(id+"F0.wireOp",EDGE,"E2.top"),sQuery(id+"F0.wireOp",EDGE,"E2.left"),sQuery(id+"F0.wireOp",EDGE,"E2.right")])]}),"instanceName":"1"}),"instanceName":"1"});
            var Q31;
            Q31=makeQuery(id+"F7.opPattern","COPY",BODY,{"derivedFrom":makeQuery(id+"F2.opPattern","COPY",BODY,{"derivedFrom":makeQuery(id+"F1.opExtrude","SWEPT_BODY",BODY,{"disambiguationData":[OSD([sQuery(id+"F0.wireOp",EDGE,"E1.bottom"),sQuery(id+"F0.wireOp",EDGE,"E1.top"),sQuery(id+"F0.wireOp",EDGE,"E1.left"),sQuery(id+"F0.wireOp",EDGE,"E1.right")])]}),"instanceName":"1"}),"instanceName":"1"});
            var Q32;
            Q32=makeQuery(id+"F7.opPattern","COPY",BODY,{"derivedFrom":makeQuery(id+"F1.opExtrude","SWEPT_BODY",BODY,{"disambiguationData":[OSD([sQuery(id+"F0.wireOp",EDGE,"E2.bottom"),sQuery(id+"F0.wireOp",EDGE,"E2.top"),sQuery(id+"F0.wireOp",EDGE,"E2.left"),sQuery(id+"F0.wireOp",EDGE,"E2.right")])]}),"instanceName":"1"});
            var Q33;
            Q33=makeQuery(id+"F7.opPattern","COPY",BODY,{"derivedFrom":makeQuery(id+"F1.opExtrude","SWEPT_BODY",BODY,{"disambiguationData":[OSD([sQuery(id+"F0.wireOp",EDGE,"E0.bottom"),sQuery(id+"F0.wireOp",EDGE,"E0.top"),sQuery(id+"F0.wireOp",EDGE,"E0.left"),sQuery(id+"F0.wireOp",EDGE,"E0.right")])]}),"instanceName":"1"});
            var Q34;
            Q34=makeQuery(id+"F7.opPattern","COPY",BODY,{"derivedFrom":makeQuery(id+"F1.opExtrude","SWEPT_BODY",BODY,{"disambiguationData":[OSD([sQuery(id+"F0.wireOp",EDGE,"E1.bottom"),sQuery(id+"F0.wireOp",EDGE,"E1.top"),sQuery(id+"F0.wireOp",EDGE,"E1.left"),sQuery(id+"F0.wireOp",EDGE,"E1.right")])]}),"instanceName":"1"});
            var Q35;
            Q35=makeQuery(id+"F7.opPattern","COPY",BODY,{"derivedFrom":makeQuery(id+"F6.opPattern","COPY",BODY,{"derivedFrom":makeQuery(id+"F5.opPattern","COPY",BODY,{"derivedFrom":makeQuery(id+"F4.opPattern","COPY",BODY,{"derivedFrom":makeQuery(id+"F3.opPattern","COPY",BODY,{"derivedFrom":makeQuery(id+"F2.opPattern","COPY",BODY,{"derivedFrom":makeQuery(id+"F1.opExtrude","SWEPT_BODY",BODY,{"disambiguationData":[OSD([sQuery(id+"F0.wireOp",EDGE,"E2.bottom"),sQuery(id+"F0.wireOp",EDGE,"E2.top"),sQuery(id+"F0.wireOp",EDGE,"E2.left"),sQuery(id+"F0.wireOp",EDGE,"E2.right")])]}),"instanceName":"1"}),"instanceName":"1"}),"instanceName":"1"}),"instanceName":"1"}),"instanceName":"1"}),"instanceName":"1"});
            transform(context, id + "F8", {"entities" : qUnion([Q0, Q1, Q2, Q3, Q4, Q5, Q6, Q7, Q8, Q9, Q10, Q11, Q12, Q13, Q14, Q15, Q16, Q17, Q18, Q19, Q20, Q21, Q22, Q23, Q24, Q25, Q26, Q27, Q28, Q29, Q30, Q31, Q32, Q33, Q34, Q35]), "transformType" : TransformType.TRANSLATION_3D, "dx" : -606 * mm, "dy" : 1812 * mm, "dz" : 0 * mm, "makeCopy" : true});
        }
        {
            var Q0;
            Q0=makeQuery(id+"F8.opPattern","COPY",BODY,{"derivedFrom":makeQuery(id+"F7.opPattern","COPY",BODY,{"derivedFrom":makeQuery(id+"F1.opExtrude","SWEPT_BODY",BODY,{"disambiguationData":[OSD([sQuery(id+"F0.wireOp",EDGE,"E0.bottom"),sQuery(id+"F0.wireOp",EDGE,"E0.top"),sQuery(id+"F0.wireOp",EDGE,"E0.left"),sQuery(id+"F0.wireOp",EDGE,"E0.right")])]}),"instanceName":"1"}),"instanceName":"1"});
            var Q1;
            Q1=makeQuery(id+"F8.opPattern","COPY",BODY,{"derivedFrom":makeQuery(id+"F7.opPattern","COPY",BODY,{"derivedFrom":makeQuery(id+"F1.opExtrude","SWEPT_BODY",BODY,{"disambiguationData":[OSD([sQuery(id+"F0.wireOp",EDGE,"E1.bottom"),sQuery(id+"F0.wireOp",EDGE,"E1.top"),sQuery(id+"F0.wireOp",EDGE,"E1.left"),sQuery(id+"F0.wireOp",EDGE,"E1.right")])]}),"instanceName":"1"}),"instanceName":"1"});
            var Q2;
            Q2=makeQuery(id+"F8.opPattern","COPY",BODY,{"derivedFrom":makeQuery(id+"F7.opPattern","COPY",BODY,{"derivedFrom":makeQuery(id+"F1.opExtrude","SWEPT_BODY",BODY,{"disambiguationData":[OSD([sQuery(id+"F0.wireOp",EDGE,"E2.bottom"),sQuery(id+"F0.wireOp",EDGE,"E2.top"),sQuery(id+"F0.wireOp",EDGE,"E2.left"),sQuery(id+"F0.wireOp",EDGE,"E2.right")])]}),"instanceName":"1"}),"instanceName":"1"});
            var Q3;
            Q3=makeQuery(id+"F8.opPattern","COPY",BODY,{"derivedFrom":makeQuery(id+"F7.opPattern","COPY",BODY,{"derivedFrom":makeQuery(id+"F2.opPattern","COPY",BODY,{"derivedFrom":makeQuery(id+"F1.opExtrude","SWEPT_BODY",BODY,{"disambiguationData":[OSD([sQuery(id+"F0.wireOp",EDGE,"E1.bottom"),sQuery(id+"F0.wireOp",EDGE,"E1.top"),sQuery(id+"F0.wireOp",EDGE,"E1.left"),sQuery(id+"F0.wireOp",EDGE,"E1.right")])]}),"instanceName":"1"}),"instanceName":"1"}),"instanceName":"1"});
            var Q4;
            Q4=makeQuery(id+"F8.opPattern","COPY",BODY,{"derivedFrom":makeQuery(id+"F7.opPattern","COPY",BODY,{"derivedFrom":makeQuery(id+"F2.opPattern","COPY",BODY,{"derivedFrom":makeQuery(id+"F1.opExtrude","SWEPT_BODY",BODY,{"disambiguationData":[OSD([sQuery(id+"F0.wireOp",EDGE,"E0.bottom"),sQuery(id+"F0.wireOp",EDGE,"E0.top"),sQuery(id+"F0.wireOp",EDGE,"E0.left"),sQuery(id+"F0.wireOp",EDGE,"E0.right")])]}),"instanceName":"1"}),"instanceName":"1"}),"instanceName":"1"});
            var Q5;
            Q5=makeQuery(id+"F8.opPattern","COPY",BODY,{"derivedFrom":makeQuery(id+"F7.opPattern","COPY",BODY,{"derivedFrom":makeQuery(id+"F2.opPattern","COPY",BODY,{"derivedFrom":makeQuery(id+"F1.opExtrude","SWEPT_BODY",BODY,{"disambiguationData":[OSD([sQuery(id+"F0.wireOp",EDGE,"E2.bottom"),sQuery(id+"F0.wireOp",EDGE,"E2.top"),sQuery(id+"F0.wireOp",EDGE,"E2.left"),sQuery(id+"F0.wireOp",EDGE,"E2.right")])]}),"instanceName":"1"}),"instanceName":"1"}),"instanceName":"1"});
            var Q6;
            Q6=makeQuery(id+"F8.opPattern","COPY",BODY,{"derivedFrom":makeQuery(id+"F7.opPattern","COPY",BODY,{"derivedFrom":makeQuery(id+"F3.opPattern","COPY",BODY,{"derivedFrom":makeQuery(id+"F2.opPattern","COPY",BODY,{"derivedFrom":makeQuery(id+"F1.opExtrude","SWEPT_BODY",BODY,{"disambiguationData":[OSD([sQuery(id+"F0.wireOp",EDGE,"E1.bottom"),sQuery(id+"F0.wireOp",EDGE,"E1.top"),sQuery(id+"F0.wireOp",EDGE,"E1.left"),sQuery(id+"F0.wireOp",EDGE,"E1.right")])]}),"instanceName":"1"}),"instanceName":"1"}),"instanceName":"1"}),"instanceName":"1"});
            var Q7;
            Q7=makeQuery(id+"F8.opPattern","COPY",BODY,{"derivedFrom":makeQuery(id+"F7.opPattern","COPY",BODY,{"derivedFrom":makeQuery(id+"F3.opPattern","COPY",BODY,{"derivedFrom":makeQuery(id+"F2.opPattern","COPY",BODY,{"derivedFrom":makeQuery(id+"F1.opExtrude","SWEPT_BODY",BODY,{"disambiguationData":[OSD([sQuery(id+"F0.wireOp",EDGE,"E0.bottom"),sQuery(id+"F0.wireOp",EDGE,"E0.top"),sQuery(id+"F0.wireOp",EDGE,"E0.left"),sQuery(id+"F0.wireOp",EDGE,"E0.right")])]}),"instanceName":"1"}),"instanceName":"1"}),"instanceName":"1"}),"instanceName":"1"});
            var Q8;
            Q8=makeQuery(id+"F8.opPattern","COPY",BODY,{"derivedFrom":makeQuery(id+"F7.opPattern","COPY",BODY,{"derivedFrom":makeQuery(id+"F3.opPattern","COPY",BODY,{"derivedFrom":makeQuery(id+"F2.opPattern","COPY",BODY,{"derivedFrom":makeQuery(id+"F1.opExtrude","SWEPT_BODY",BODY,{"disambiguationData":[OSD([sQuery(id+"F0.wireOp",EDGE,"E2.bottom"),sQuery(id+"F0.wireOp",EDGE,"E2.top"),sQuery(id+"F0.wireOp",EDGE,"E2.left"),sQuery(id+"F0.wireOp",EDGE,"E2.right")])]}),"instanceName":"1"}),"instanceName":"1"}),"instanceName":"1"}),"instanceName":"1"});
            var Q9;
            Q9=makeQuery(id+"F8.opPattern","COPY",BODY,{"derivedFrom":makeQuery(id+"F7.opPattern","COPY",BODY,{"derivedFrom":makeQuery(id+"F4.opPattern","COPY",BODY,{"derivedFrom":makeQuery(id+"F3.opPattern","COPY",BODY,{"derivedFrom":makeQuery(id+"F2.opPattern","COPY",BODY,{"derivedFrom":makeQuery(id+"F1.opExtrude","SWEPT_BODY",BODY,{"disambiguationData":[OSD([sQuery(id+"F0.wireOp",EDGE,"E1.bottom"),sQuery(id+"F0.wireOp",EDGE,"E1.top"),sQuery(id+"F0.wireOp",EDGE,"E1.left"),sQuery(id+"F0.wireOp",EDGE,"E1.right")])]}),"instanceName":"1"}),"instanceName":"1"}),"instanceName":"1"}),"instanceName":"1"}),"instanceName":"1"});
            var Q10;
            Q10=makeQuery(id+"F8.opPattern","COPY",BODY,{"derivedFrom":makeQuery(id+"F7.opPattern","COPY",BODY,{"derivedFrom":makeQuery(id+"F4.opPattern","COPY",BODY,{"derivedFrom":makeQuery(id+"F3.opPattern","COPY",BODY,{"derivedFrom":makeQuery(id+"F2.opPattern","COPY",BODY,{"derivedFrom":makeQuery(id+"F1.opExtrude","SWEPT_BODY",BODY,{"disambiguationData":[OSD([sQuery(id+"F0.wireOp",EDGE,"E0.bottom"),sQuery(id+"F0.wireOp",EDGE,"E0.top"),sQuery(id+"F0.wireOp",EDGE,"E0.left"),sQuery(id+"F0.wireOp",EDGE,"E0.right")])]}),"instanceName":"1"}),"instanceName":"1"}),"instanceName":"1"}),"instanceName":"1"}),"instanceName":"1"});
            var Q11;
            Q11=makeQuery(id+"F8.opPattern","COPY",BODY,{"derivedFrom":makeQuery(id+"F7.opPattern","COPY",BODY,{"derivedFrom":makeQuery(id+"F4.opPattern","COPY",BODY,{"derivedFrom":makeQuery(id+"F3.opPattern","COPY",BODY,{"derivedFrom":makeQuery(id+"F2.opPattern","COPY",BODY,{"derivedFrom":makeQuery(id+"F1.opExtrude","SWEPT_BODY",BODY,{"disambiguationData":[OSD([sQuery(id+"F0.wireOp",EDGE,"E2.bottom"),sQuery(id+"F0.wireOp",EDGE,"E2.top"),sQuery(id+"F0.wireOp",EDGE,"E2.left"),sQuery(id+"F0.wireOp",EDGE,"E2.right")])]}),"instanceName":"1"}),"instanceName":"1"}),"instanceName":"1"}),"instanceName":"1"}),"instanceName":"1"});
            var Q12;
            Q12=makeQuery(id+"F8.opPattern","COPY",BODY,{"derivedFrom":makeQuery(id+"F7.opPattern","COPY",BODY,{"derivedFrom":makeQuery(id+"F5.opPattern","COPY",BODY,{"derivedFrom":makeQuery(id+"F4.opPattern","COPY",BODY,{"derivedFrom":makeQuery(id+"F3.opPattern","COPY",BODY,{"derivedFrom":makeQuery(id+"F2.opPattern","COPY",BODY,{"derivedFrom":makeQuery(id+"F1.opExtrude","SWEPT_BODY",BODY,{"disambiguationData":[OSD([sQuery(id+"F0.wireOp",EDGE,"E1.bottom"),sQuery(id+"F0.wireOp",EDGE,"E1.top"),sQuery(id+"F0.wireOp",EDGE,"E1.left"),sQuery(id+"F0.wireOp",EDGE,"E1.right")])]}),"instanceName":"1"}),"instanceName":"1"}),"instanceName":"1"}),"instanceName":"1"}),"instanceName":"1"}),"instanceName":"1"});
            var Q13;
            Q13=makeQuery(id+"F8.opPattern","COPY",BODY,{"derivedFrom":makeQuery(id+"F7.opPattern","COPY",BODY,{"derivedFrom":makeQuery(id+"F5.opPattern","COPY",BODY,{"derivedFrom":makeQuery(id+"F4.opPattern","COPY",BODY,{"derivedFrom":makeQuery(id+"F3.opPattern","COPY",BODY,{"derivedFrom":makeQuery(id+"F2.opPattern","COPY",BODY,{"derivedFrom":makeQuery(id+"F1.opExtrude","SWEPT_BODY",BODY,{"disambiguationData":[OSD([sQuery(id+"F0.wireOp",EDGE,"E0.bottom"),sQuery(id+"F0.wireOp",EDGE,"E0.top"),sQuery(id+"F0.wireOp",EDGE,"E0.left"),sQuery(id+"F0.wireOp",EDGE,"E0.right")])]}),"instanceName":"1"}),"instanceName":"1"}),"instanceName":"1"}),"instanceName":"1"}),"instanceName":"1"}),"instanceName":"1"});
            var Q14;
            Q14=makeQuery(id+"F8.opPattern","COPY",BODY,{"derivedFrom":makeQuery(id+"F7.opPattern","COPY",BODY,{"derivedFrom":makeQuery(id+"F5.opPattern","COPY",BODY,{"derivedFrom":makeQuery(id+"F4.opPattern","COPY",BODY,{"derivedFrom":makeQuery(id+"F3.opPattern","COPY",BODY,{"derivedFrom":makeQuery(id+"F2.opPattern","COPY",BODY,{"derivedFrom":makeQuery(id+"F1.opExtrude","SWEPT_BODY",BODY,{"disambiguationData":[OSD([sQuery(id+"F0.wireOp",EDGE,"E2.bottom"),sQuery(id+"F0.wireOp",EDGE,"E2.top"),sQuery(id+"F0.wireOp",EDGE,"E2.left"),sQuery(id+"F0.wireOp",EDGE,"E2.right")])]}),"instanceName":"1"}),"instanceName":"1"}),"instanceName":"1"}),"instanceName":"1"}),"instanceName":"1"}),"instanceName":"1"});
            var Q15;
            Q15=makeQuery(id+"F8.opPattern","COPY",BODY,{"derivedFrom":makeQuery(id+"F7.opPattern","COPY",BODY,{"derivedFrom":makeQuery(id+"F6.opPattern","COPY",BODY,{"derivedFrom":makeQuery(id+"F5.opPattern","COPY",BODY,{"derivedFrom":makeQuery(id+"F4.opPattern","COPY",BODY,{"derivedFrom":makeQuery(id+"F3.opPattern","COPY",BODY,{"derivedFrom":makeQuery(id+"F2.opPattern","COPY",BODY,{"derivedFrom":makeQuery(id+"F1.opExtrude","SWEPT_BODY",BODY,{"disambiguationData":[OSD([sQuery(id+"F0.wireOp",EDGE,"E1.bottom"),sQuery(id+"F0.wireOp",EDGE,"E1.top"),sQuery(id+"F0.wireOp",EDGE,"E1.left"),sQuery(id+"F0.wireOp",EDGE,"E1.right")])]}),"instanceName":"1"}),"instanceName":"1"}),"instanceName":"1"}),"instanceName":"1"}),"instanceName":"1"}),"instanceName":"1"}),"instanceName":"1"});
            var Q16;
            Q16=makeQuery(id+"F8.opPattern","COPY",BODY,{"derivedFrom":makeQuery(id+"F7.opPattern","COPY",BODY,{"derivedFrom":makeQuery(id+"F6.opPattern","COPY",BODY,{"derivedFrom":makeQuery(id+"F5.opPattern","COPY",BODY,{"derivedFrom":makeQuery(id+"F4.opPattern","COPY",BODY,{"derivedFrom":makeQuery(id+"F3.opPattern","COPY",BODY,{"derivedFrom":makeQuery(id+"F2.opPattern","COPY",BODY,{"derivedFrom":makeQuery(id+"F1.opExtrude","SWEPT_BODY",BODY,{"disambiguationData":[OSD([sQuery(id+"F0.wireOp",EDGE,"E0.bottom"),sQuery(id+"F0.wireOp",EDGE,"E0.top"),sQuery(id+"F0.wireOp",EDGE,"E0.left"),sQuery(id+"F0.wireOp",EDGE,"E0.right")])]}),"instanceName":"1"}),"instanceName":"1"}),"instanceName":"1"}),"instanceName":"1"}),"instanceName":"1"}),"instanceName":"1"}),"instanceName":"1"});
            var Q17;
            Q17=makeQuery(id+"F8.opPattern","COPY",BODY,{"derivedFrom":makeQuery(id+"F7.opPattern","COPY",BODY,{"derivedFrom":makeQuery(id+"F6.opPattern","COPY",BODY,{"derivedFrom":makeQuery(id+"F5.opPattern","COPY",BODY,{"derivedFrom":makeQuery(id+"F4.opPattern","COPY",BODY,{"derivedFrom":makeQuery(id+"F3.opPattern","COPY",BODY,{"derivedFrom":makeQuery(id+"F2.opPattern","COPY",BODY,{"derivedFrom":makeQuery(id+"F1.opExtrude","SWEPT_BODY",BODY,{"disambiguationData":[OSD([sQuery(id+"F0.wireOp",EDGE,"E2.bottom"),sQuery(id+"F0.wireOp",EDGE,"E2.top"),sQuery(id+"F0.wireOp",EDGE,"E2.left"),sQuery(id+"F0.wireOp",EDGE,"E2.right")])]}),"instanceName":"1"}),"instanceName":"1"}),"instanceName":"1"}),"instanceName":"1"}),"instanceName":"1"}),"instanceName":"1"}),"instanceName":"1"});
            var Q18;
            Q18=makeQuery(id+"F8.opPattern","COPY",BODY,{"derivedFrom":makeQuery(id+"F6.opPattern","COPY",BODY,{"derivedFrom":makeQuery(id+"F5.opPattern","COPY",BODY,{"derivedFrom":makeQuery(id+"F4.opPattern","COPY",BODY,{"derivedFrom":makeQuery(id+"F3.opPattern","COPY",BODY,{"derivedFrom":makeQuery(id+"F2.opPattern","COPY",BODY,{"derivedFrom":makeQuery(id+"F1.opExtrude","SWEPT_BODY",BODY,{"disambiguationData":[OSD([sQuery(id+"F0.wireOp",EDGE,"E0.bottom"),sQuery(id+"F0.wireOp",EDGE,"E0.top"),sQuery(id+"F0.wireOp",EDGE,"E0.left"),sQuery(id+"F0.wireOp",EDGE,"E0.right")])]}),"instanceName":"1"}),"instanceName":"1"}),"instanceName":"1"}),"instanceName":"1"}),"instanceName":"1"}),"instanceName":"1"});
            var Q19;
            Q19=makeQuery(id+"F8.opPattern","COPY",BODY,{"derivedFrom":makeQuery(id+"F5.opPattern","COPY",BODY,{"derivedFrom":makeQuery(id+"F4.opPattern","COPY",BODY,{"derivedFrom":makeQuery(id+"F3.opPattern","COPY",BODY,{"derivedFrom":makeQuery(id+"F2.opPattern","COPY",BODY,{"derivedFrom":makeQuery(id+"F1.opExtrude","SWEPT_BODY",BODY,{"disambiguationData":[OSD([sQuery(id+"F0.wireOp",EDGE,"E0.bottom"),sQuery(id+"F0.wireOp",EDGE,"E0.top"),sQuery(id+"F0.wireOp",EDGE,"E0.left"),sQuery(id+"F0.wireOp",EDGE,"E0.right")])]}),"instanceName":"1"}),"instanceName":"1"}),"instanceName":"1"}),"instanceName":"1"}),"instanceName":"1"});
            var Q20;
            Q20=makeQuery(id+"F8.opPattern","COPY",BODY,{"derivedFrom":makeQuery(id+"F4.opPattern","COPY",BODY,{"derivedFrom":makeQuery(id+"F3.opPattern","COPY",BODY,{"derivedFrom":makeQuery(id+"F2.opPattern","COPY",BODY,{"derivedFrom":makeQuery(id+"F1.opExtrude","SWEPT_BODY",BODY,{"disambiguationData":[OSD([sQuery(id+"F0.wireOp",EDGE,"E0.bottom"),sQuery(id+"F0.wireOp",EDGE,"E0.top"),sQuery(id+"F0.wireOp",EDGE,"E0.left"),sQuery(id+"F0.wireOp",EDGE,"E0.right")])]}),"instanceName":"1"}),"instanceName":"1"}),"instanceName":"1"}),"instanceName":"1"});
            var Q21;
            Q21=makeQuery(id+"F8.opPattern","COPY",BODY,{"derivedFrom":makeQuery(id+"F3.opPattern","COPY",BODY,{"derivedFrom":makeQuery(id+"F2.opPattern","COPY",BODY,{"derivedFrom":makeQuery(id+"F1.opExtrude","SWEPT_BODY",BODY,{"disambiguationData":[OSD([sQuery(id+"F0.wireOp",EDGE,"E0.bottom"),sQuery(id+"F0.wireOp",EDGE,"E0.top"),sQuery(id+"F0.wireOp",EDGE,"E0.left"),sQuery(id+"F0.wireOp",EDGE,"E0.right")])]}),"instanceName":"1"}),"instanceName":"1"}),"instanceName":"1"});
            var Q22;
            Q22=makeQuery(id+"F8.opPattern","COPY",BODY,{"derivedFrom":makeQuery(id+"F2.opPattern","COPY",BODY,{"derivedFrom":makeQuery(id+"F1.opExtrude","SWEPT_BODY",BODY,{"disambiguationData":[OSD([sQuery(id+"F0.wireOp",EDGE,"E0.bottom"),sQuery(id+"F0.wireOp",EDGE,"E0.top"),sQuery(id+"F0.wireOp",EDGE,"E0.left"),sQuery(id+"F0.wireOp",EDGE,"E0.right")])]}),"instanceName":"1"}),"instanceName":"1"});
            var Q23;
            Q23=makeQuery(id+"F8.opPattern","COPY",BODY,{"derivedFrom":makeQuery(id+"F1.opExtrude","SWEPT_BODY",BODY,{"disambiguationData":[OSD([sQuery(id+"F0.wireOp",EDGE,"E0.bottom"),sQuery(id+"F0.wireOp",EDGE,"E0.top"),sQuery(id+"F0.wireOp",EDGE,"E0.left"),sQuery(id+"F0.wireOp",EDGE,"E0.right")])]}),"instanceName":"1"});
            var Q24;
            Q24=makeQuery(id+"F8.opPattern","COPY",BODY,{"derivedFrom":makeQuery(id+"F1.opExtrude","SWEPT_BODY",BODY,{"disambiguationData":[OSD([sQuery(id+"F0.wireOp",EDGE,"E1.bottom"),sQuery(id+"F0.wireOp",EDGE,"E1.top"),sQuery(id+"F0.wireOp",EDGE,"E1.left"),sQuery(id+"F0.wireOp",EDGE,"E1.right")])]}),"instanceName":"1"});
            var Q25;
            Q25=makeQuery(id+"F8.opPattern","COPY",BODY,{"derivedFrom":makeQuery(id+"F1.opExtrude","SWEPT_BODY",BODY,{"disambiguationData":[OSD([sQuery(id+"F0.wireOp",EDGE,"E2.bottom"),sQuery(id+"F0.wireOp",EDGE,"E2.top"),sQuery(id+"F0.wireOp",EDGE,"E2.left"),sQuery(id+"F0.wireOp",EDGE,"E2.right")])]}),"instanceName":"1"});
            var Q26;
            Q26=makeQuery(id+"F8.opPattern","COPY",BODY,{"derivedFrom":makeQuery(id+"F2.opPattern","COPY",BODY,{"derivedFrom":makeQuery(id+"F1.opExtrude","SWEPT_BODY",BODY,{"disambiguationData":[OSD([sQuery(id+"F0.wireOp",EDGE,"E1.bottom"),sQuery(id+"F0.wireOp",EDGE,"E1.top"),sQuery(id+"F0.wireOp",EDGE,"E1.left"),sQuery(id+"F0.wireOp",EDGE,"E1.right")])]}),"instanceName":"1"}),"instanceName":"1"});
            var Q27;
            Q27=makeQuery(id+"F8.opPattern","COPY",BODY,{"derivedFrom":makeQuery(id+"F2.opPattern","COPY",BODY,{"derivedFrom":makeQuery(id+"F1.opExtrude","SWEPT_BODY",BODY,{"disambiguationData":[OSD([sQuery(id+"F0.wireOp",EDGE,"E2.bottom"),sQuery(id+"F0.wireOp",EDGE,"E2.top"),sQuery(id+"F0.wireOp",EDGE,"E2.left"),sQuery(id+"F0.wireOp",EDGE,"E2.right")])]}),"instanceName":"1"}),"instanceName":"1"});
            var Q28;
            Q28=makeQuery(id+"F8.opPattern","COPY",BODY,{"derivedFrom":makeQuery(id+"F3.opPattern","COPY",BODY,{"derivedFrom":makeQuery(id+"F2.opPattern","COPY",BODY,{"derivedFrom":makeQuery(id+"F1.opExtrude","SWEPT_BODY",BODY,{"disambiguationData":[OSD([sQuery(id+"F0.wireOp",EDGE,"E1.bottom"),sQuery(id+"F0.wireOp",EDGE,"E1.top"),sQuery(id+"F0.wireOp",EDGE,"E1.left"),sQuery(id+"F0.wireOp",EDGE,"E1.right")])]}),"instanceName":"1"}),"instanceName":"1"}),"instanceName":"1"});
            var Q29;
            Q29=makeQuery(id+"F8.opPattern","COPY",BODY,{"derivedFrom":makeQuery(id+"F3.opPattern","COPY",BODY,{"derivedFrom":makeQuery(id+"F2.opPattern","COPY",BODY,{"derivedFrom":makeQuery(id+"F1.opExtrude","SWEPT_BODY",BODY,{"disambiguationData":[OSD([sQuery(id+"F0.wireOp",EDGE,"E2.bottom"),sQuery(id+"F0.wireOp",EDGE,"E2.top"),sQuery(id+"F0.wireOp",EDGE,"E2.left"),sQuery(id+"F0.wireOp",EDGE,"E2.right")])]}),"instanceName":"1"}),"instanceName":"1"}),"instanceName":"1"});
            var Q30;
            Q30=makeQuery(id+"F8.opPattern","COPY",BODY,{"derivedFrom":makeQuery(id+"F4.opPattern","COPY",BODY,{"derivedFrom":makeQuery(id+"F3.opPattern","COPY",BODY,{"derivedFrom":makeQuery(id+"F2.opPattern","COPY",BODY,{"derivedFrom":makeQuery(id+"F1.opExtrude","SWEPT_BODY",BODY,{"disambiguationData":[OSD([sQuery(id+"F0.wireOp",EDGE,"E1.bottom"),sQuery(id+"F0.wireOp",EDGE,"E1.top"),sQuery(id+"F0.wireOp",EDGE,"E1.left"),sQuery(id+"F0.wireOp",EDGE,"E1.right")])]}),"instanceName":"1"}),"instanceName":"1"}),"instanceName":"1"}),"instanceName":"1"});
            var Q31;
            Q31=makeQuery(id+"F8.opPattern","COPY",BODY,{"derivedFrom":makeQuery(id+"F4.opPattern","COPY",BODY,{"derivedFrom":makeQuery(id+"F3.opPattern","COPY",BODY,{"derivedFrom":makeQuery(id+"F2.opPattern","COPY",BODY,{"derivedFrom":makeQuery(id+"F1.opExtrude","SWEPT_BODY",BODY,{"disambiguationData":[OSD([sQuery(id+"F0.wireOp",EDGE,"E2.bottom"),sQuery(id+"F0.wireOp",EDGE,"E2.top"),sQuery(id+"F0.wireOp",EDGE,"E2.left"),sQuery(id+"F0.wireOp",EDGE,"E2.right")])]}),"instanceName":"1"}),"instanceName":"1"}),"instanceName":"1"}),"instanceName":"1"});
            var Q32;
            Q32=makeQuery(id+"F8.opPattern","COPY",BODY,{"derivedFrom":makeQuery(id+"F5.opPattern","COPY",BODY,{"derivedFrom":makeQuery(id+"F4.opPattern","COPY",BODY,{"derivedFrom":makeQuery(id+"F3.opPattern","COPY",BODY,{"derivedFrom":makeQuery(id+"F2.opPattern","COPY",BODY,{"derivedFrom":makeQuery(id+"F1.opExtrude","SWEPT_BODY",BODY,{"disambiguationData":[OSD([sQuery(id+"F0.wireOp",EDGE,"E1.bottom"),sQuery(id+"F0.wireOp",EDGE,"E1.top"),sQuery(id+"F0.wireOp",EDGE,"E1.left"),sQuery(id+"F0.wireOp",EDGE,"E1.right")])]}),"instanceName":"1"}),"instanceName":"1"}),"instanceName":"1"}),"instanceName":"1"}),"instanceName":"1"});
            var Q33;
            Q33=makeQuery(id+"F8.opPattern","COPY",BODY,{"derivedFrom":makeQuery(id+"F5.opPattern","COPY",BODY,{"derivedFrom":makeQuery(id+"F4.opPattern","COPY",BODY,{"derivedFrom":makeQuery(id+"F3.opPattern","COPY",BODY,{"derivedFrom":makeQuery(id+"F2.opPattern","COPY",BODY,{"derivedFrom":makeQuery(id+"F1.opExtrude","SWEPT_BODY",BODY,{"disambiguationData":[OSD([sQuery(id+"F0.wireOp",EDGE,"E2.bottom"),sQuery(id+"F0.wireOp",EDGE,"E2.top"),sQuery(id+"F0.wireOp",EDGE,"E2.left"),sQuery(id+"F0.wireOp",EDGE,"E2.right")])]}),"instanceName":"1"}),"instanceName":"1"}),"instanceName":"1"}),"instanceName":"1"}),"instanceName":"1"});
            var Q34;
            Q34=makeQuery(id+"F8.opPattern","COPY",BODY,{"derivedFrom":makeQuery(id+"F6.opPattern","COPY",BODY,{"derivedFrom":makeQuery(id+"F5.opPattern","COPY",BODY,{"derivedFrom":makeQuery(id+"F4.opPattern","COPY",BODY,{"derivedFrom":makeQuery(id+"F3.opPattern","COPY",BODY,{"derivedFrom":makeQuery(id+"F2.opPattern","COPY",BODY,{"derivedFrom":makeQuery(id+"F1.opExtrude","SWEPT_BODY",BODY,{"disambiguationData":[OSD([sQuery(id+"F0.wireOp",EDGE,"E1.bottom"),sQuery(id+"F0.wireOp",EDGE,"E1.top"),sQuery(id+"F0.wireOp",EDGE,"E1.left"),sQuery(id+"F0.wireOp",EDGE,"E1.right")])]}),"instanceName":"1"}),"instanceName":"1"}),"instanceName":"1"}),"instanceName":"1"}),"instanceName":"1"}),"instanceName":"1"});
            var Q35;
            Q35=makeQuery(id+"F8.opPattern","COPY",BODY,{"derivedFrom":makeQuery(id+"F6.opPattern","COPY",BODY,{"derivedFrom":makeQuery(id+"F5.opPattern","COPY",BODY,{"derivedFrom":makeQuery(id+"F4.opPattern","COPY",BODY,{"derivedFrom":makeQuery(id+"F3.opPattern","COPY",BODY,{"derivedFrom":makeQuery(id+"F2.opPattern","COPY",BODY,{"derivedFrom":makeQuery(id+"F1.opExtrude","SWEPT_BODY",BODY,{"disambiguationData":[OSD([sQuery(id+"F0.wireOp",EDGE,"E2.bottom"),sQuery(id+"F0.wireOp",EDGE,"E2.top"),sQuery(id+"F0.wireOp",EDGE,"E2.left"),sQuery(id+"F0.wireOp",EDGE,"E2.right")])]}),"instanceName":"1"}),"instanceName":"1"}),"instanceName":"1"}),"instanceName":"1"}),"instanceName":"1"}),"instanceName":"1"});
            var Q36;
            Q36=makeQuery(id+"F7.opPattern","COPY",BODY,{"derivedFrom":makeQuery(id+"F6.opPattern","COPY",BODY,{"derivedFrom":makeQuery(id+"F5.opPattern","COPY",BODY,{"derivedFrom":makeQuery(id+"F4.opPattern","COPY",BODY,{"derivedFrom":makeQuery(id+"F3.opPattern","COPY",BODY,{"derivedFrom":makeQuery(id+"F2.opPattern","COPY",BODY,{"derivedFrom":makeQuery(id+"F1.opExtrude","SWEPT_BODY",BODY,{"disambiguationData":[OSD([sQuery(id+"F0.wireOp",EDGE,"E0.bottom"),sQuery(id+"F0.wireOp",EDGE,"E0.top"),sQuery(id+"F0.wireOp",EDGE,"E0.left"),sQuery(id+"F0.wireOp",EDGE,"E0.right")])]}),"instanceName":"1"}),"instanceName":"1"}),"instanceName":"1"}),"instanceName":"1"}),"instanceName":"1"}),"instanceName":"1"});
            var Q37;
            Q37=makeQuery(id+"F7.opPattern","COPY",BODY,{"derivedFrom":makeQuery(id+"F5.opPattern","COPY",BODY,{"derivedFrom":makeQuery(id+"F4.opPattern","COPY",BODY,{"derivedFrom":makeQuery(id+"F3.opPattern","COPY",BODY,{"derivedFrom":makeQuery(id+"F2.opPattern","COPY",BODY,{"derivedFrom":makeQuery(id+"F1.opExtrude","SWEPT_BODY",BODY,{"disambiguationData":[OSD([sQuery(id+"F0.wireOp",EDGE,"E0.bottom"),sQuery(id+"F0.wireOp",EDGE,"E0.top"),sQuery(id+"F0.wireOp",EDGE,"E0.left"),sQuery(id+"F0.wireOp",EDGE,"E0.right")])]}),"instanceName":"1"}),"instanceName":"1"}),"instanceName":"1"}),"instanceName":"1"}),"instanceName":"1"});
            var Q38;
            Q38=makeQuery(id+"F7.opPattern","COPY",BODY,{"derivedFrom":makeQuery(id+"F4.opPattern","COPY",BODY,{"derivedFrom":makeQuery(id+"F3.opPattern","COPY",BODY,{"derivedFrom":makeQuery(id+"F2.opPattern","COPY",BODY,{"derivedFrom":makeQuery(id+"F1.opExtrude","SWEPT_BODY",BODY,{"disambiguationData":[OSD([sQuery(id+"F0.wireOp",EDGE,"E0.bottom"),sQuery(id+"F0.wireOp",EDGE,"E0.top"),sQuery(id+"F0.wireOp",EDGE,"E0.left"),sQuery(id+"F0.wireOp",EDGE,"E0.right")])]}),"instanceName":"1"}),"instanceName":"1"}),"instanceName":"1"}),"instanceName":"1"});
            var Q39;
            Q39=makeQuery(id+"F7.opPattern","COPY",BODY,{"derivedFrom":makeQuery(id+"F3.opPattern","COPY",BODY,{"derivedFrom":makeQuery(id+"F2.opPattern","COPY",BODY,{"derivedFrom":makeQuery(id+"F1.opExtrude","SWEPT_BODY",BODY,{"disambiguationData":[OSD([sQuery(id+"F0.wireOp",EDGE,"E0.bottom"),sQuery(id+"F0.wireOp",EDGE,"E0.top"),sQuery(id+"F0.wireOp",EDGE,"E0.left"),sQuery(id+"F0.wireOp",EDGE,"E0.right")])]}),"instanceName":"1"}),"instanceName":"1"}),"instanceName":"1"});
            var Q40;
            Q40=makeQuery(id+"F7.opPattern","COPY",BODY,{"derivedFrom":makeQuery(id+"F2.opPattern","COPY",BODY,{"derivedFrom":makeQuery(id+"F1.opExtrude","SWEPT_BODY",BODY,{"disambiguationData":[OSD([sQuery(id+"F0.wireOp",EDGE,"E0.bottom"),sQuery(id+"F0.wireOp",EDGE,"E0.top"),sQuery(id+"F0.wireOp",EDGE,"E0.left"),sQuery(id+"F0.wireOp",EDGE,"E0.right")])]}),"instanceName":"1"}),"instanceName":"1"});
            var Q41;
            Q41=makeQuery(id+"F7.opPattern","COPY",BODY,{"derivedFrom":makeQuery(id+"F1.opExtrude","SWEPT_BODY",BODY,{"disambiguationData":[OSD([sQuery(id+"F0.wireOp",EDGE,"E0.bottom"),sQuery(id+"F0.wireOp",EDGE,"E0.top"),sQuery(id+"F0.wireOp",EDGE,"E0.left"),sQuery(id+"F0.wireOp",EDGE,"E0.right")])]}),"instanceName":"1"});
            var Q42;
            Q42=makeQuery(id+"F7.opPattern","COPY",BODY,{"derivedFrom":makeQuery(id+"F1.opExtrude","SWEPT_BODY",BODY,{"disambiguationData":[OSD([sQuery(id+"F0.wireOp",EDGE,"E1.bottom"),sQuery(id+"F0.wireOp",EDGE,"E1.top"),sQuery(id+"F0.wireOp",EDGE,"E1.left"),sQuery(id+"F0.wireOp",EDGE,"E1.right")])]}),"instanceName":"1"});
            var Q43;
            Q43=makeQuery(id+"F7.opPattern","COPY",BODY,{"derivedFrom":makeQuery(id+"F1.opExtrude","SWEPT_BODY",BODY,{"disambiguationData":[OSD([sQuery(id+"F0.wireOp",EDGE,"E2.bottom"),sQuery(id+"F0.wireOp",EDGE,"E2.top"),sQuery(id+"F0.wireOp",EDGE,"E2.left"),sQuery(id+"F0.wireOp",EDGE,"E2.right")])]}),"instanceName":"1"});
            var Q44;
            Q44=makeQuery(id+"F7.opPattern","COPY",BODY,{"derivedFrom":makeQuery(id+"F2.opPattern","COPY",BODY,{"derivedFrom":makeQuery(id+"F1.opExtrude","SWEPT_BODY",BODY,{"disambiguationData":[OSD([sQuery(id+"F0.wireOp",EDGE,"E1.bottom"),sQuery(id+"F0.wireOp",EDGE,"E1.top"),sQuery(id+"F0.wireOp",EDGE,"E1.left"),sQuery(id+"F0.wireOp",EDGE,"E1.right")])]}),"instanceName":"1"}),"instanceName":"1"});
            var Q45;
            Q45=makeQuery(id+"F7.opPattern","COPY",BODY,{"derivedFrom":makeQuery(id+"F2.opPattern","COPY",BODY,{"derivedFrom":makeQuery(id+"F1.opExtrude","SWEPT_BODY",BODY,{"disambiguationData":[OSD([sQuery(id+"F0.wireOp",EDGE,"E2.bottom"),sQuery(id+"F0.wireOp",EDGE,"E2.top"),sQuery(id+"F0.wireOp",EDGE,"E2.left"),sQuery(id+"F0.wireOp",EDGE,"E2.right")])]}),"instanceName":"1"}),"instanceName":"1"});
            var Q46;
            Q46=makeQuery(id+"F7.opPattern","COPY",BODY,{"derivedFrom":makeQuery(id+"F3.opPattern","COPY",BODY,{"derivedFrom":makeQuery(id+"F2.opPattern","COPY",BODY,{"derivedFrom":makeQuery(id+"F1.opExtrude","SWEPT_BODY",BODY,{"disambiguationData":[OSD([sQuery(id+"F0.wireOp",EDGE,"E1.bottom"),sQuery(id+"F0.wireOp",EDGE,"E1.top"),sQuery(id+"F0.wireOp",EDGE,"E1.left"),sQuery(id+"F0.wireOp",EDGE,"E1.right")])]}),"instanceName":"1"}),"instanceName":"1"}),"instanceName":"1"});
            var Q47;
            Q47=makeQuery(id+"F7.opPattern","COPY",BODY,{"derivedFrom":makeQuery(id+"F3.opPattern","COPY",BODY,{"derivedFrom":makeQuery(id+"F2.opPattern","COPY",BODY,{"derivedFrom":makeQuery(id+"F1.opExtrude","SWEPT_BODY",BODY,{"disambiguationData":[OSD([sQuery(id+"F0.wireOp",EDGE,"E2.bottom"),sQuery(id+"F0.wireOp",EDGE,"E2.top"),sQuery(id+"F0.wireOp",EDGE,"E2.left"),sQuery(id+"F0.wireOp",EDGE,"E2.right")])]}),"instanceName":"1"}),"instanceName":"1"}),"instanceName":"1"});
            var Q48;
            Q48=makeQuery(id+"F7.opPattern","COPY",BODY,{"derivedFrom":makeQuery(id+"F4.opPattern","COPY",BODY,{"derivedFrom":makeQuery(id+"F3.opPattern","COPY",BODY,{"derivedFrom":makeQuery(id+"F2.opPattern","COPY",BODY,{"derivedFrom":makeQuery(id+"F1.opExtrude","SWEPT_BODY",BODY,{"disambiguationData":[OSD([sQuery(id+"F0.wireOp",EDGE,"E1.bottom"),sQuery(id+"F0.wireOp",EDGE,"E1.top"),sQuery(id+"F0.wireOp",EDGE,"E1.left"),sQuery(id+"F0.wireOp",EDGE,"E1.right")])]}),"instanceName":"1"}),"instanceName":"1"}),"instanceName":"1"}),"instanceName":"1"});
            var Q49;
            Q49=makeQuery(id+"F7.opPattern","COPY",BODY,{"derivedFrom":makeQuery(id+"F4.opPattern","COPY",BODY,{"derivedFrom":makeQuery(id+"F3.opPattern","COPY",BODY,{"derivedFrom":makeQuery(id+"F2.opPattern","COPY",BODY,{"derivedFrom":makeQuery(id+"F1.opExtrude","SWEPT_BODY",BODY,{"disambiguationData":[OSD([sQuery(id+"F0.wireOp",EDGE,"E2.bottom"),sQuery(id+"F0.wireOp",EDGE,"E2.top"),sQuery(id+"F0.wireOp",EDGE,"E2.left"),sQuery(id+"F0.wireOp",EDGE,"E2.right")])]}),"instanceName":"1"}),"instanceName":"1"}),"instanceName":"1"}),"instanceName":"1"});
            var Q50;
            Q50=makeQuery(id+"F7.opPattern","COPY",BODY,{"derivedFrom":makeQuery(id+"F5.opPattern","COPY",BODY,{"derivedFrom":makeQuery(id+"F4.opPattern","COPY",BODY,{"derivedFrom":makeQuery(id+"F3.opPattern","COPY",BODY,{"derivedFrom":makeQuery(id+"F2.opPattern","COPY",BODY,{"derivedFrom":makeQuery(id+"F1.opExtrude","SWEPT_BODY",BODY,{"disambiguationData":[OSD([sQuery(id+"F0.wireOp",EDGE,"E1.bottom"),sQuery(id+"F0.wireOp",EDGE,"E1.top"),sQuery(id+"F0.wireOp",EDGE,"E1.left"),sQuery(id+"F0.wireOp",EDGE,"E1.right")])]}),"instanceName":"1"}),"instanceName":"1"}),"instanceName":"1"}),"instanceName":"1"}),"instanceName":"1"});
            var Q51;
            Q51=makeQuery(id+"F7.opPattern","COPY",BODY,{"derivedFrom":makeQuery(id+"F5.opPattern","COPY",BODY,{"derivedFrom":makeQuery(id+"F4.opPattern","COPY",BODY,{"derivedFrom":makeQuery(id+"F3.opPattern","COPY",BODY,{"derivedFrom":makeQuery(id+"F2.opPattern","COPY",BODY,{"derivedFrom":makeQuery(id+"F1.opExtrude","SWEPT_BODY",BODY,{"disambiguationData":[OSD([sQuery(id+"F0.wireOp",EDGE,"E2.bottom"),sQuery(id+"F0.wireOp",EDGE,"E2.top"),sQuery(id+"F0.wireOp",EDGE,"E2.left"),sQuery(id+"F0.wireOp",EDGE,"E2.right")])]}),"instanceName":"1"}),"instanceName":"1"}),"instanceName":"1"}),"instanceName":"1"}),"instanceName":"1"});
            var Q52;
            Q52=makeQuery(id+"F7.opPattern","COPY",BODY,{"derivedFrom":makeQuery(id+"F6.opPattern","COPY",BODY,{"derivedFrom":makeQuery(id+"F5.opPattern","COPY",BODY,{"derivedFrom":makeQuery(id+"F4.opPattern","COPY",BODY,{"derivedFrom":makeQuery(id+"F3.opPattern","COPY",BODY,{"derivedFrom":makeQuery(id+"F2.opPattern","COPY",BODY,{"derivedFrom":makeQuery(id+"F1.opExtrude","SWEPT_BODY",BODY,{"disambiguationData":[OSD([sQuery(id+"F0.wireOp",EDGE,"E1.bottom"),sQuery(id+"F0.wireOp",EDGE,"E1.top"),sQuery(id+"F0.wireOp",EDGE,"E1.left"),sQuery(id+"F0.wireOp",EDGE,"E1.right")])]}),"instanceName":"1"}),"instanceName":"1"}),"instanceName":"1"}),"instanceName":"1"}),"instanceName":"1"}),"instanceName":"1"});
            var Q53;
            Q53=makeQuery(id+"F7.opPattern","COPY",BODY,{"derivedFrom":makeQuery(id+"F6.opPattern","COPY",BODY,{"derivedFrom":makeQuery(id+"F5.opPattern","COPY",BODY,{"derivedFrom":makeQuery(id+"F4.opPattern","COPY",BODY,{"derivedFrom":makeQuery(id+"F3.opPattern","COPY",BODY,{"derivedFrom":makeQuery(id+"F2.opPattern","COPY",BODY,{"derivedFrom":makeQuery(id+"F1.opExtrude","SWEPT_BODY",BODY,{"disambiguationData":[OSD([sQuery(id+"F0.wireOp",EDGE,"E2.bottom"),sQuery(id+"F0.wireOp",EDGE,"E2.top"),sQuery(id+"F0.wireOp",EDGE,"E2.left"),sQuery(id+"F0.wireOp",EDGE,"E2.right")])]}),"instanceName":"1"}),"instanceName":"1"}),"instanceName":"1"}),"instanceName":"1"}),"instanceName":"1"}),"instanceName":"1"});
            var Q54;
            Q54=makeQuery(id+"F6.opPattern","COPY",BODY,{"derivedFrom":makeQuery(id+"F5.opPattern","COPY",BODY,{"derivedFrom":makeQuery(id+"F4.opPattern","COPY",BODY,{"derivedFrom":makeQuery(id+"F3.opPattern","COPY",BODY,{"derivedFrom":makeQuery(id+"F2.opPattern","COPY",BODY,{"derivedFrom":makeQuery(id+"F1.opExtrude","SWEPT_BODY",BODY,{"disambiguationData":[OSD([sQuery(id+"F0.wireOp",EDGE,"E0.bottom"),sQuery(id+"F0.wireOp",EDGE,"E0.top"),sQuery(id+"F0.wireOp",EDGE,"E0.left"),sQuery(id+"F0.wireOp",EDGE,"E0.right")])]}),"instanceName":"1"}),"instanceName":"1"}),"instanceName":"1"}),"instanceName":"1"}),"instanceName":"1"});
            var Q55;
            Q55=makeQuery(id+"F5.opPattern","COPY",BODY,{"derivedFrom":makeQuery(id+"F4.opPattern","COPY",BODY,{"derivedFrom":makeQuery(id+"F3.opPattern","COPY",BODY,{"derivedFrom":makeQuery(id+"F2.opPattern","COPY",BODY,{"derivedFrom":makeQuery(id+"F1.opExtrude","SWEPT_BODY",BODY,{"disambiguationData":[OSD([sQuery(id+"F0.wireOp",EDGE,"E0.bottom"),sQuery(id+"F0.wireOp",EDGE,"E0.top"),sQuery(id+"F0.wireOp",EDGE,"E0.left"),sQuery(id+"F0.wireOp",EDGE,"E0.right")])]}),"instanceName":"1"}),"instanceName":"1"}),"instanceName":"1"}),"instanceName":"1"});
            var Q56;
            Q56=makeQuery(id+"F4.opPattern","COPY",BODY,{"derivedFrom":makeQuery(id+"F3.opPattern","COPY",BODY,{"derivedFrom":makeQuery(id+"F2.opPattern","COPY",BODY,{"derivedFrom":makeQuery(id+"F1.opExtrude","SWEPT_BODY",BODY,{"disambiguationData":[OSD([sQuery(id+"F0.wireOp",EDGE,"E0.bottom"),sQuery(id+"F0.wireOp",EDGE,"E0.top"),sQuery(id+"F0.wireOp",EDGE,"E0.left"),sQuery(id+"F0.wireOp",EDGE,"E0.right")])]}),"instanceName":"1"}),"instanceName":"1"}),"instanceName":"1"});
            var Q57;
            Q57=makeQuery(id+"F3.opPattern","COPY",BODY,{"derivedFrom":makeQuery(id+"F2.opPattern","COPY",BODY,{"derivedFrom":makeQuery(id+"F1.opExtrude","SWEPT_BODY",BODY,{"disambiguationData":[OSD([sQuery(id+"F0.wireOp",EDGE,"E0.bottom"),sQuery(id+"F0.wireOp",EDGE,"E0.top"),sQuery(id+"F0.wireOp",EDGE,"E0.left"),sQuery(id+"F0.wireOp",EDGE,"E0.right")])]}),"instanceName":"1"}),"instanceName":"1"});
            var Q58;
            Q58=makeQuery(id+"F2.opPattern","COPY",BODY,{"derivedFrom":makeQuery(id+"F1.opExtrude","SWEPT_BODY",BODY,{"disambiguationData":[OSD([sQuery(id+"F0.wireOp",EDGE,"E0.bottom"),sQuery(id+"F0.wireOp",EDGE,"E0.top"),sQuery(id+"F0.wireOp",EDGE,"E0.left"),sQuery(id+"F0.wireOp",EDGE,"E0.right")])]}),"instanceName":"1"});
            var Q59;
            Q59=makeQuery(id+"F1.opExtrude","SWEPT_BODY",BODY,{"disambiguationData":[OSD([sQuery(id+"F0.wireOp",EDGE,"E0.bottom"),sQuery(id+"F0.wireOp",EDGE,"E0.top"),sQuery(id+"F0.wireOp",EDGE,"E0.left"),sQuery(id+"F0.wireOp",EDGE,"E0.right")])]});
            var Q60;
            Q60=makeQuery(id+"F1.opExtrude","SWEPT_BODY",BODY,{"disambiguationData":[OSD([sQuery(id+"F0.wireOp",EDGE,"E1.bottom"),sQuery(id+"F0.wireOp",EDGE,"E1.top"),sQuery(id+"F0.wireOp",EDGE,"E1.left"),sQuery(id+"F0.wireOp",EDGE,"E1.right")])]});
            var Q61;
            Q61=makeQuery(id+"F1.opExtrude","SWEPT_BODY",BODY,{"disambiguationData":[OSD([sQuery(id+"F0.wireOp",EDGE,"E2.bottom"),sQuery(id+"F0.wireOp",EDGE,"E2.top"),sQuery(id+"F0.wireOp",EDGE,"E2.left"),sQuery(id+"F0.wireOp",EDGE,"E2.right")])]});
            var Q62;
            Q62=makeQuery(id+"F2.opPattern","COPY",BODY,{"derivedFrom":makeQuery(id+"F1.opExtrude","SWEPT_BODY",BODY,{"disambiguationData":[OSD([sQuery(id+"F0.wireOp",EDGE,"E1.bottom"),sQuery(id+"F0.wireOp",EDGE,"E1.top"),sQuery(id+"F0.wireOp",EDGE,"E1.left"),sQuery(id+"F0.wireOp",EDGE,"E1.right")])]}),"instanceName":"1"});
            var Q63;
            Q63=makeQuery(id+"F2.opPattern","COPY",BODY,{"derivedFrom":makeQuery(id+"F1.opExtrude","SWEPT_BODY",BODY,{"disambiguationData":[OSD([sQuery(id+"F0.wireOp",EDGE,"E2.bottom"),sQuery(id+"F0.wireOp",EDGE,"E2.top"),sQuery(id+"F0.wireOp",EDGE,"E2.left"),sQuery(id+"F0.wireOp",EDGE,"E2.right")])]}),"instanceName":"1"});
            var Q64;
            Q64=makeQuery(id+"F3.opPattern","COPY",BODY,{"derivedFrom":makeQuery(id+"F2.opPattern","COPY",BODY,{"derivedFrom":makeQuery(id+"F1.opExtrude","SWEPT_BODY",BODY,{"disambiguationData":[OSD([sQuery(id+"F0.wireOp",EDGE,"E1.bottom"),sQuery(id+"F0.wireOp",EDGE,"E1.top"),sQuery(id+"F0.wireOp",EDGE,"E1.left"),sQuery(id+"F0.wireOp",EDGE,"E1.right")])]}),"instanceName":"1"}),"instanceName":"1"});
            var Q65;
            Q65=makeQuery(id+"F3.opPattern","COPY",BODY,{"derivedFrom":makeQuery(id+"F2.opPattern","COPY",BODY,{"derivedFrom":makeQuery(id+"F1.opExtrude","SWEPT_BODY",BODY,{"disambiguationData":[OSD([sQuery(id+"F0.wireOp",EDGE,"E2.bottom"),sQuery(id+"F0.wireOp",EDGE,"E2.top"),sQuery(id+"F0.wireOp",EDGE,"E2.left"),sQuery(id+"F0.wireOp",EDGE,"E2.right")])]}),"instanceName":"1"}),"instanceName":"1"});
            var Q66;
            Q66=makeQuery(id+"F4.opPattern","COPY",BODY,{"derivedFrom":makeQuery(id+"F3.opPattern","COPY",BODY,{"derivedFrom":makeQuery(id+"F2.opPattern","COPY",BODY,{"derivedFrom":makeQuery(id+"F1.opExtrude","SWEPT_BODY",BODY,{"disambiguationData":[OSD([sQuery(id+"F0.wireOp",EDGE,"E1.bottom"),sQuery(id+"F0.wireOp",EDGE,"E1.top"),sQuery(id+"F0.wireOp",EDGE,"E1.left"),sQuery(id+"F0.wireOp",EDGE,"E1.right")])]}),"instanceName":"1"}),"instanceName":"1"}),"instanceName":"1"});
            var Q67;
            Q67=makeQuery(id+"F5.opPattern","COPY",BODY,{"derivedFrom":makeQuery(id+"F4.opPattern","COPY",BODY,{"derivedFrom":makeQuery(id+"F3.opPattern","COPY",BODY,{"derivedFrom":makeQuery(id+"F2.opPattern","COPY",BODY,{"derivedFrom":makeQuery(id+"F1.opExtrude","SWEPT_BODY",BODY,{"disambiguationData":[OSD([sQuery(id+"F0.wireOp",EDGE,"E2.bottom"),sQuery(id+"F0.wireOp",EDGE,"E2.top"),sQuery(id+"F0.wireOp",EDGE,"E2.left"),sQuery(id+"F0.wireOp",EDGE,"E2.right")])]}),"instanceName":"1"}),"instanceName":"1"}),"instanceName":"1"}),"instanceName":"1"});
            var Q68;
            Q68=makeQuery(id+"F5.opPattern","COPY",BODY,{"derivedFrom":makeQuery(id+"F4.opPattern","COPY",BODY,{"derivedFrom":makeQuery(id+"F3.opPattern","COPY",BODY,{"derivedFrom":makeQuery(id+"F2.opPattern","COPY",BODY,{"derivedFrom":makeQuery(id+"F1.opExtrude","SWEPT_BODY",BODY,{"disambiguationData":[OSD([sQuery(id+"F0.wireOp",EDGE,"E1.bottom"),sQuery(id+"F0.wireOp",EDGE,"E1.top"),sQuery(id+"F0.wireOp",EDGE,"E1.left"),sQuery(id+"F0.wireOp",EDGE,"E1.right")])]}),"instanceName":"1"}),"instanceName":"1"}),"instanceName":"1"}),"instanceName":"1"});
            var Q69;
            Q69=makeQuery(id+"F4.opPattern","COPY",BODY,{"derivedFrom":makeQuery(id+"F3.opPattern","COPY",BODY,{"derivedFrom":makeQuery(id+"F2.opPattern","COPY",BODY,{"derivedFrom":makeQuery(id+"F1.opExtrude","SWEPT_BODY",BODY,{"disambiguationData":[OSD([sQuery(id+"F0.wireOp",EDGE,"E2.bottom"),sQuery(id+"F0.wireOp",EDGE,"E2.top"),sQuery(id+"F0.wireOp",EDGE,"E2.left"),sQuery(id+"F0.wireOp",EDGE,"E2.right")])]}),"instanceName":"1"}),"instanceName":"1"}),"instanceName":"1"});
            var Q70;
            Q70=makeQuery(id+"F6.opPattern","COPY",BODY,{"derivedFrom":makeQuery(id+"F5.opPattern","COPY",BODY,{"derivedFrom":makeQuery(id+"F4.opPattern","COPY",BODY,{"derivedFrom":makeQuery(id+"F3.opPattern","COPY",BODY,{"derivedFrom":makeQuery(id+"F2.opPattern","COPY",BODY,{"derivedFrom":makeQuery(id+"F1.opExtrude","SWEPT_BODY",BODY,{"disambiguationData":[OSD([sQuery(id+"F0.wireOp",EDGE,"E1.bottom"),sQuery(id+"F0.wireOp",EDGE,"E1.top"),sQuery(id+"F0.wireOp",EDGE,"E1.left"),sQuery(id+"F0.wireOp",EDGE,"E1.right")])]}),"instanceName":"1"}),"instanceName":"1"}),"instanceName":"1"}),"instanceName":"1"}),"instanceName":"1"});
            var Q71;
            Q71=makeQuery(id+"F6.opPattern","COPY",BODY,{"derivedFrom":makeQuery(id+"F5.opPattern","COPY",BODY,{"derivedFrom":makeQuery(id+"F4.opPattern","COPY",BODY,{"derivedFrom":makeQuery(id+"F3.opPattern","COPY",BODY,{"derivedFrom":makeQuery(id+"F2.opPattern","COPY",BODY,{"derivedFrom":makeQuery(id+"F1.opExtrude","SWEPT_BODY",BODY,{"disambiguationData":[OSD([sQuery(id+"F0.wireOp",EDGE,"E2.bottom"),sQuery(id+"F0.wireOp",EDGE,"E2.top"),sQuery(id+"F0.wireOp",EDGE,"E2.left"),sQuery(id+"F0.wireOp",EDGE,"E2.right")])]}),"instanceName":"1"}),"instanceName":"1"}),"instanceName":"1"}),"instanceName":"1"}),"instanceName":"1"});
            transform(context, id + "F9", {"entities" : qUnion([Q0, Q1, Q2, Q3, Q4, Q5, Q6, Q7, Q8, Q9, Q10, Q11, Q12, Q13, Q14, Q15, Q16, Q17, Q18, Q19, Q20, Q21, Q22, Q23, Q24, Q25, Q26, Q27, Q28, Q29, Q30, Q31, Q32, Q33, Q34, Q35, Q36, Q37, Q38, Q39, Q40, Q41, Q42, Q43, Q44, Q45, Q46, Q47, Q48, Q49, Q50, Q51, Q52, Q53, Q54, Q55, Q56, Q57, Q58, Q59, Q60, Q61, Q62, Q63, Q64, Q65, Q66, Q67, Q68, Q69, Q70, Q71]), "transformType" : TransformType.TRANSLATION_3D, "dx" : 3618 * mm, "dy" : 90.6 * 20 * mm, "dz" : 0 * mm, "makeCopy" : true});
        }
        {
            var Q0;
            Q0=makeQuery(id+"F8.opPattern","COPY",BODY,{"derivedFrom":makeQuery(id+"F7.opPattern","COPY",BODY,{"derivedFrom":makeQuery(id+"F1.opExtrude","SWEPT_BODY",BODY,{"disambiguationData":[OSD([sQuery(id+"F0.wireOp",EDGE,"E0.bottom"),sQuery(id+"F0.wireOp",EDGE,"E0.top"),sQuery(id+"F0.wireOp",EDGE,"E0.left"),sQuery(id+"F0.wireOp",EDGE,"E0.right")])]}),"instanceName":"1"}),"instanceName":"1"});
            var Q1;
            Q1=makeQuery(id+"F8.opPattern","COPY",BODY,{"derivedFrom":makeQuery(id+"F7.opPattern","COPY",BODY,{"derivedFrom":makeQuery(id+"F2.opPattern","COPY",BODY,{"derivedFrom":makeQuery(id+"F1.opExtrude","SWEPT_BODY",BODY,{"disambiguationData":[OSD([sQuery(id+"F0.wireOp",EDGE,"E0.bottom"),sQuery(id+"F0.wireOp",EDGE,"E0.top"),sQuery(id+"F0.wireOp",EDGE,"E0.left"),sQuery(id+"F0.wireOp",EDGE,"E0.right")])]}),"instanceName":"1"}),"instanceName":"1"}),"instanceName":"1"});
            var Q2;
            Q2=makeQuery(id+"F8.opPattern","COPY",BODY,{"derivedFrom":makeQuery(id+"F7.opPattern","COPY",BODY,{"derivedFrom":makeQuery(id+"F3.opPattern","COPY",BODY,{"derivedFrom":makeQuery(id+"F2.opPattern","COPY",BODY,{"derivedFrom":makeQuery(id+"F1.opExtrude","SWEPT_BODY",BODY,{"disambiguationData":[OSD([sQuery(id+"F0.wireOp",EDGE,"E0.bottom"),sQuery(id+"F0.wireOp",EDGE,"E0.top"),sQuery(id+"F0.wireOp",EDGE,"E0.left"),sQuery(id+"F0.wireOp",EDGE,"E0.right")])]}),"instanceName":"1"}),"instanceName":"1"}),"instanceName":"1"}),"instanceName":"1"});
            var Q3;
            Q3=makeQuery(id+"F8.opPattern","COPY",BODY,{"derivedFrom":makeQuery(id+"F7.opPattern","COPY",BODY,{"derivedFrom":makeQuery(id+"F4.opPattern","COPY",BODY,{"derivedFrom":makeQuery(id+"F3.opPattern","COPY",BODY,{"derivedFrom":makeQuery(id+"F2.opPattern","COPY",BODY,{"derivedFrom":makeQuery(id+"F1.opExtrude","SWEPT_BODY",BODY,{"disambiguationData":[OSD([sQuery(id+"F0.wireOp",EDGE,"E0.bottom"),sQuery(id+"F0.wireOp",EDGE,"E0.top"),sQuery(id+"F0.wireOp",EDGE,"E0.left"),sQuery(id+"F0.wireOp",EDGE,"E0.right")])]}),"instanceName":"1"}),"instanceName":"1"}),"instanceName":"1"}),"instanceName":"1"}),"instanceName":"1"});
            var Q4;
            Q4=makeQuery(id+"F8.opPattern","COPY",BODY,{"derivedFrom":makeQuery(id+"F7.opPattern","COPY",BODY,{"derivedFrom":makeQuery(id+"F6.opPattern","COPY",BODY,{"derivedFrom":makeQuery(id+"F5.opPattern","COPY",BODY,{"derivedFrom":makeQuery(id+"F4.opPattern","COPY",BODY,{"derivedFrom":makeQuery(id+"F3.opPattern","COPY",BODY,{"derivedFrom":makeQuery(id+"F2.opPattern","COPY",BODY,{"derivedFrom":makeQuery(id+"F1.opExtrude","SWEPT_BODY",BODY,{"disambiguationData":[OSD([sQuery(id+"F0.wireOp",EDGE,"E2.bottom"),sQuery(id+"F0.wireOp",EDGE,"E2.top"),sQuery(id+"F0.wireOp",EDGE,"E2.left"),sQuery(id+"F0.wireOp",EDGE,"E2.right")])]}),"instanceName":"1"}),"instanceName":"1"}),"instanceName":"1"}),"instanceName":"1"}),"instanceName":"1"}),"instanceName":"1"}),"instanceName":"1"});
            var Q5;
            Q5=makeQuery(id+"F8.opPattern","COPY",BODY,{"derivedFrom":makeQuery(id+"F7.opPattern","COPY",BODY,{"derivedFrom":makeQuery(id+"F6.opPattern","COPY",BODY,{"derivedFrom":makeQuery(id+"F5.opPattern","COPY",BODY,{"derivedFrom":makeQuery(id+"F4.opPattern","COPY",BODY,{"derivedFrom":makeQuery(id+"F3.opPattern","COPY",BODY,{"derivedFrom":makeQuery(id+"F2.opPattern","COPY",BODY,{"derivedFrom":makeQuery(id+"F1.opExtrude","SWEPT_BODY",BODY,{"disambiguationData":[OSD([sQuery(id+"F0.wireOp",EDGE,"E1.bottom"),sQuery(id+"F0.wireOp",EDGE,"E1.top"),sQuery(id+"F0.wireOp",EDGE,"E1.left"),sQuery(id+"F0.wireOp",EDGE,"E1.right")])]}),"instanceName":"1"}),"instanceName":"1"}),"instanceName":"1"}),"instanceName":"1"}),"instanceName":"1"}),"instanceName":"1"}),"instanceName":"1"});
            var Q6;
            Q6=makeQuery(id+"F8.opPattern","COPY",BODY,{"derivedFrom":makeQuery(id+"F7.opPattern","COPY",BODY,{"derivedFrom":makeQuery(id+"F6.opPattern","COPY",BODY,{"derivedFrom":makeQuery(id+"F5.opPattern","COPY",BODY,{"derivedFrom":makeQuery(id+"F4.opPattern","COPY",BODY,{"derivedFrom":makeQuery(id+"F3.opPattern","COPY",BODY,{"derivedFrom":makeQuery(id+"F2.opPattern","COPY",BODY,{"derivedFrom":makeQuery(id+"F1.opExtrude","SWEPT_BODY",BODY,{"disambiguationData":[OSD([sQuery(id+"F0.wireOp",EDGE,"E0.bottom"),sQuery(id+"F0.wireOp",EDGE,"E0.top"),sQuery(id+"F0.wireOp",EDGE,"E0.left"),sQuery(id+"F0.wireOp",EDGE,"E0.right")])]}),"instanceName":"1"}),"instanceName":"1"}),"instanceName":"1"}),"instanceName":"1"}),"instanceName":"1"}),"instanceName":"1"}),"instanceName":"1"});
            var Q7;
            Q7=makeQuery(id+"F8.opPattern","COPY",BODY,{"derivedFrom":makeQuery(id+"F7.opPattern","COPY",BODY,{"derivedFrom":makeQuery(id+"F5.opPattern","COPY",BODY,{"derivedFrom":makeQuery(id+"F4.opPattern","COPY",BODY,{"derivedFrom":makeQuery(id+"F3.opPattern","COPY",BODY,{"derivedFrom":makeQuery(id+"F2.opPattern","COPY",BODY,{"derivedFrom":makeQuery(id+"F1.opExtrude","SWEPT_BODY",BODY,{"disambiguationData":[OSD([sQuery(id+"F0.wireOp",EDGE,"E2.bottom"),sQuery(id+"F0.wireOp",EDGE,"E2.top"),sQuery(id+"F0.wireOp",EDGE,"E2.left"),sQuery(id+"F0.wireOp",EDGE,"E2.right")])]}),"instanceName":"1"}),"instanceName":"1"}),"instanceName":"1"}),"instanceName":"1"}),"instanceName":"1"}),"instanceName":"1"});
            var Q8;
            Q8=makeQuery(id+"F8.opPattern","COPY",BODY,{"derivedFrom":makeQuery(id+"F7.opPattern","COPY",BODY,{"derivedFrom":makeQuery(id+"F5.opPattern","COPY",BODY,{"derivedFrom":makeQuery(id+"F4.opPattern","COPY",BODY,{"derivedFrom":makeQuery(id+"F3.opPattern","COPY",BODY,{"derivedFrom":makeQuery(id+"F2.opPattern","COPY",BODY,{"derivedFrom":makeQuery(id+"F1.opExtrude","SWEPT_BODY",BODY,{"disambiguationData":[OSD([sQuery(id+"F0.wireOp",EDGE,"E1.bottom"),sQuery(id+"F0.wireOp",EDGE,"E1.top"),sQuery(id+"F0.wireOp",EDGE,"E1.left"),sQuery(id+"F0.wireOp",EDGE,"E1.right")])]}),"instanceName":"1"}),"instanceName":"1"}),"instanceName":"1"}),"instanceName":"1"}),"instanceName":"1"}),"instanceName":"1"});
            var Q9;
            Q9=makeQuery(id+"F8.opPattern","COPY",BODY,{"derivedFrom":makeQuery(id+"F7.opPattern","COPY",BODY,{"derivedFrom":makeQuery(id+"F5.opPattern","COPY",BODY,{"derivedFrom":makeQuery(id+"F4.opPattern","COPY",BODY,{"derivedFrom":makeQuery(id+"F3.opPattern","COPY",BODY,{"derivedFrom":makeQuery(id+"F2.opPattern","COPY",BODY,{"derivedFrom":makeQuery(id+"F1.opExtrude","SWEPT_BODY",BODY,{"disambiguationData":[OSD([sQuery(id+"F0.wireOp",EDGE,"E0.bottom"),sQuery(id+"F0.wireOp",EDGE,"E0.top"),sQuery(id+"F0.wireOp",EDGE,"E0.left"),sQuery(id+"F0.wireOp",EDGE,"E0.right")])]}),"instanceName":"1"}),"instanceName":"1"}),"instanceName":"1"}),"instanceName":"1"}),"instanceName":"1"}),"instanceName":"1"});
            var Q10;
            Q10=makeQuery(id+"F8.opPattern","COPY",BODY,{"derivedFrom":makeQuery(id+"F7.opPattern","COPY",BODY,{"derivedFrom":makeQuery(id+"F4.opPattern","COPY",BODY,{"derivedFrom":makeQuery(id+"F3.opPattern","COPY",BODY,{"derivedFrom":makeQuery(id+"F2.opPattern","COPY",BODY,{"derivedFrom":makeQuery(id+"F1.opExtrude","SWEPT_BODY",BODY,{"disambiguationData":[OSD([sQuery(id+"F0.wireOp",EDGE,"E2.bottom"),sQuery(id+"F0.wireOp",EDGE,"E2.top"),sQuery(id+"F0.wireOp",EDGE,"E2.left"),sQuery(id+"F0.wireOp",EDGE,"E2.right")])]}),"instanceName":"1"}),"instanceName":"1"}),"instanceName":"1"}),"instanceName":"1"}),"instanceName":"1"});
            var Q11;
            Q11=makeQuery(id+"F8.opPattern","COPY",BODY,{"derivedFrom":makeQuery(id+"F7.opPattern","COPY",BODY,{"derivedFrom":makeQuery(id+"F4.opPattern","COPY",BODY,{"derivedFrom":makeQuery(id+"F3.opPattern","COPY",BODY,{"derivedFrom":makeQuery(id+"F2.opPattern","COPY",BODY,{"derivedFrom":makeQuery(id+"F1.opExtrude","SWEPT_BODY",BODY,{"disambiguationData":[OSD([sQuery(id+"F0.wireOp",EDGE,"E1.bottom"),sQuery(id+"F0.wireOp",EDGE,"E1.top"),sQuery(id+"F0.wireOp",EDGE,"E1.left"),sQuery(id+"F0.wireOp",EDGE,"E1.right")])]}),"instanceName":"1"}),"instanceName":"1"}),"instanceName":"1"}),"instanceName":"1"}),"instanceName":"1"});
            var Q12;
            Q12=makeQuery(id+"F8.opPattern","COPY",BODY,{"derivedFrom":makeQuery(id+"F7.opPattern","COPY",BODY,{"derivedFrom":makeQuery(id+"F3.opPattern","COPY",BODY,{"derivedFrom":makeQuery(id+"F2.opPattern","COPY",BODY,{"derivedFrom":makeQuery(id+"F1.opExtrude","SWEPT_BODY",BODY,{"disambiguationData":[OSD([sQuery(id+"F0.wireOp",EDGE,"E2.bottom"),sQuery(id+"F0.wireOp",EDGE,"E2.top"),sQuery(id+"F0.wireOp",EDGE,"E2.left"),sQuery(id+"F0.wireOp",EDGE,"E2.right")])]}),"instanceName":"1"}),"instanceName":"1"}),"instanceName":"1"}),"instanceName":"1"});
            var Q13;
            Q13=makeQuery(id+"F8.opPattern","COPY",BODY,{"derivedFrom":makeQuery(id+"F7.opPattern","COPY",BODY,{"derivedFrom":makeQuery(id+"F3.opPattern","COPY",BODY,{"derivedFrom":makeQuery(id+"F2.opPattern","COPY",BODY,{"derivedFrom":makeQuery(id+"F1.opExtrude","SWEPT_BODY",BODY,{"disambiguationData":[OSD([sQuery(id+"F0.wireOp",EDGE,"E1.bottom"),sQuery(id+"F0.wireOp",EDGE,"E1.top"),sQuery(id+"F0.wireOp",EDGE,"E1.left"),sQuery(id+"F0.wireOp",EDGE,"E1.right")])]}),"instanceName":"1"}),"instanceName":"1"}),"instanceName":"1"}),"instanceName":"1"});
            var Q14;
            Q14=makeQuery(id+"F8.opPattern","COPY",BODY,{"derivedFrom":makeQuery(id+"F7.opPattern","COPY",BODY,{"derivedFrom":makeQuery(id+"F2.opPattern","COPY",BODY,{"derivedFrom":makeQuery(id+"F1.opExtrude","SWEPT_BODY",BODY,{"disambiguationData":[OSD([sQuery(id+"F0.wireOp",EDGE,"E2.bottom"),sQuery(id+"F0.wireOp",EDGE,"E2.top"),sQuery(id+"F0.wireOp",EDGE,"E2.left"),sQuery(id+"F0.wireOp",EDGE,"E2.right")])]}),"instanceName":"1"}),"instanceName":"1"}),"instanceName":"1"});
            var Q15;
            Q15=makeQuery(id+"F8.opPattern","COPY",BODY,{"derivedFrom":makeQuery(id+"F7.opPattern","COPY",BODY,{"derivedFrom":makeQuery(id+"F2.opPattern","COPY",BODY,{"derivedFrom":makeQuery(id+"F1.opExtrude","SWEPT_BODY",BODY,{"disambiguationData":[OSD([sQuery(id+"F0.wireOp",EDGE,"E1.bottom"),sQuery(id+"F0.wireOp",EDGE,"E1.top"),sQuery(id+"F0.wireOp",EDGE,"E1.left"),sQuery(id+"F0.wireOp",EDGE,"E1.right")])]}),"instanceName":"1"}),"instanceName":"1"}),"instanceName":"1"});
            var Q16;
            Q16=makeQuery(id+"F8.opPattern","COPY",BODY,{"derivedFrom":makeQuery(id+"F7.opPattern","COPY",BODY,{"derivedFrom":makeQuery(id+"F1.opExtrude","SWEPT_BODY",BODY,{"disambiguationData":[OSD([sQuery(id+"F0.wireOp",EDGE,"E2.bottom"),sQuery(id+"F0.wireOp",EDGE,"E2.top"),sQuery(id+"F0.wireOp",EDGE,"E2.left"),sQuery(id+"F0.wireOp",EDGE,"E2.right")])]}),"instanceName":"1"}),"instanceName":"1"});
            var Q17;
            Q17=makeQuery(id+"F8.opPattern","COPY",BODY,{"derivedFrom":makeQuery(id+"F6.opPattern","COPY",BODY,{"derivedFrom":makeQuery(id+"F5.opPattern","COPY",BODY,{"derivedFrom":makeQuery(id+"F4.opPattern","COPY",BODY,{"derivedFrom":makeQuery(id+"F3.opPattern","COPY",BODY,{"derivedFrom":makeQuery(id+"F2.opPattern","COPY",BODY,{"derivedFrom":makeQuery(id+"F1.opExtrude","SWEPT_BODY",BODY,{"disambiguationData":[OSD([sQuery(id+"F0.wireOp",EDGE,"E2.bottom"),sQuery(id+"F0.wireOp",EDGE,"E2.top"),sQuery(id+"F0.wireOp",EDGE,"E2.left"),sQuery(id+"F0.wireOp",EDGE,"E2.right")])]}),"instanceName":"1"}),"instanceName":"1"}),"instanceName":"1"}),"instanceName":"1"}),"instanceName":"1"}),"instanceName":"1"});
            var Q18;
            Q18=makeQuery(id+"F8.opPattern","COPY",BODY,{"derivedFrom":makeQuery(id+"F6.opPattern","COPY",BODY,{"derivedFrom":makeQuery(id+"F5.opPattern","COPY",BODY,{"derivedFrom":makeQuery(id+"F4.opPattern","COPY",BODY,{"derivedFrom":makeQuery(id+"F3.opPattern","COPY",BODY,{"derivedFrom":makeQuery(id+"F2.opPattern","COPY",BODY,{"derivedFrom":makeQuery(id+"F1.opExtrude","SWEPT_BODY",BODY,{"disambiguationData":[OSD([sQuery(id+"F0.wireOp",EDGE,"E1.bottom"),sQuery(id+"F0.wireOp",EDGE,"E1.top"),sQuery(id+"F0.wireOp",EDGE,"E1.left"),sQuery(id+"F0.wireOp",EDGE,"E1.right")])]}),"instanceName":"1"}),"instanceName":"1"}),"instanceName":"1"}),"instanceName":"1"}),"instanceName":"1"}),"instanceName":"1"});
            var Q19;
            Q19=makeQuery(id+"F8.opPattern","COPY",BODY,{"derivedFrom":makeQuery(id+"F6.opPattern","COPY",BODY,{"derivedFrom":makeQuery(id+"F5.opPattern","COPY",BODY,{"derivedFrom":makeQuery(id+"F4.opPattern","COPY",BODY,{"derivedFrom":makeQuery(id+"F3.opPattern","COPY",BODY,{"derivedFrom":makeQuery(id+"F2.opPattern","COPY",BODY,{"derivedFrom":makeQuery(id+"F1.opExtrude","SWEPT_BODY",BODY,{"disambiguationData":[OSD([sQuery(id+"F0.wireOp",EDGE,"E0.bottom"),sQuery(id+"F0.wireOp",EDGE,"E0.top"),sQuery(id+"F0.wireOp",EDGE,"E0.left"),sQuery(id+"F0.wireOp",EDGE,"E0.right")])]}),"instanceName":"1"}),"instanceName":"1"}),"instanceName":"1"}),"instanceName":"1"}),"instanceName":"1"}),"instanceName":"1"});
            var Q20;
            Q20=makeQuery(id+"F8.opPattern","COPY",BODY,{"derivedFrom":makeQuery(id+"F5.opPattern","COPY",BODY,{"derivedFrom":makeQuery(id+"F4.opPattern","COPY",BODY,{"derivedFrom":makeQuery(id+"F3.opPattern","COPY",BODY,{"derivedFrom":makeQuery(id+"F2.opPattern","COPY",BODY,{"derivedFrom":makeQuery(id+"F1.opExtrude","SWEPT_BODY",BODY,{"disambiguationData":[OSD([sQuery(id+"F0.wireOp",EDGE,"E2.bottom"),sQuery(id+"F0.wireOp",EDGE,"E2.top"),sQuery(id+"F0.wireOp",EDGE,"E2.left"),sQuery(id+"F0.wireOp",EDGE,"E2.right")])]}),"instanceName":"1"}),"instanceName":"1"}),"instanceName":"1"}),"instanceName":"1"}),"instanceName":"1"});
            var Q21;
            Q21=makeQuery(id+"F8.opPattern","COPY",BODY,{"derivedFrom":makeQuery(id+"F5.opPattern","COPY",BODY,{"derivedFrom":makeQuery(id+"F4.opPattern","COPY",BODY,{"derivedFrom":makeQuery(id+"F3.opPattern","COPY",BODY,{"derivedFrom":makeQuery(id+"F2.opPattern","COPY",BODY,{"derivedFrom":makeQuery(id+"F1.opExtrude","SWEPT_BODY",BODY,{"disambiguationData":[OSD([sQuery(id+"F0.wireOp",EDGE,"E1.bottom"),sQuery(id+"F0.wireOp",EDGE,"E1.top"),sQuery(id+"F0.wireOp",EDGE,"E1.left"),sQuery(id+"F0.wireOp",EDGE,"E1.right")])]}),"instanceName":"1"}),"instanceName":"1"}),"instanceName":"1"}),"instanceName":"1"}),"instanceName":"1"});
            var Q22;
            Q22=makeQuery(id+"F8.opPattern","COPY",BODY,{"derivedFrom":makeQuery(id+"F5.opPattern","COPY",BODY,{"derivedFrom":makeQuery(id+"F4.opPattern","COPY",BODY,{"derivedFrom":makeQuery(id+"F3.opPattern","COPY",BODY,{"derivedFrom":makeQuery(id+"F2.opPattern","COPY",BODY,{"derivedFrom":makeQuery(id+"F1.opExtrude","SWEPT_BODY",BODY,{"disambiguationData":[OSD([sQuery(id+"F0.wireOp",EDGE,"E0.bottom"),sQuery(id+"F0.wireOp",EDGE,"E0.top"),sQuery(id+"F0.wireOp",EDGE,"E0.left"),sQuery(id+"F0.wireOp",EDGE,"E0.right")])]}),"instanceName":"1"}),"instanceName":"1"}),"instanceName":"1"}),"instanceName":"1"}),"instanceName":"1"});
            var Q23;
            Q23=makeQuery(id+"F8.opPattern","COPY",BODY,{"derivedFrom":makeQuery(id+"F4.opPattern","COPY",BODY,{"derivedFrom":makeQuery(id+"F3.opPattern","COPY",BODY,{"derivedFrom":makeQuery(id+"F2.opPattern","COPY",BODY,{"derivedFrom":makeQuery(id+"F1.opExtrude","SWEPT_BODY",BODY,{"disambiguationData":[OSD([sQuery(id+"F0.wireOp",EDGE,"E2.bottom"),sQuery(id+"F0.wireOp",EDGE,"E2.top"),sQuery(id+"F0.wireOp",EDGE,"E2.left"),sQuery(id+"F0.wireOp",EDGE,"E2.right")])]}),"instanceName":"1"}),"instanceName":"1"}),"instanceName":"1"}),"instanceName":"1"});
            var Q24;
            Q24=makeQuery(id+"F8.opPattern","COPY",BODY,{"derivedFrom":makeQuery(id+"F4.opPattern","COPY",BODY,{"derivedFrom":makeQuery(id+"F3.opPattern","COPY",BODY,{"derivedFrom":makeQuery(id+"F2.opPattern","COPY",BODY,{"derivedFrom":makeQuery(id+"F1.opExtrude","SWEPT_BODY",BODY,{"disambiguationData":[OSD([sQuery(id+"F0.wireOp",EDGE,"E1.bottom"),sQuery(id+"F0.wireOp",EDGE,"E1.top"),sQuery(id+"F0.wireOp",EDGE,"E1.left"),sQuery(id+"F0.wireOp",EDGE,"E1.right")])]}),"instanceName":"1"}),"instanceName":"1"}),"instanceName":"1"}),"instanceName":"1"});
            var Q25;
            Q25=makeQuery(id+"F8.opPattern","COPY",BODY,{"derivedFrom":makeQuery(id+"F4.opPattern","COPY",BODY,{"derivedFrom":makeQuery(id+"F3.opPattern","COPY",BODY,{"derivedFrom":makeQuery(id+"F2.opPattern","COPY",BODY,{"derivedFrom":makeQuery(id+"F1.opExtrude","SWEPT_BODY",BODY,{"disambiguationData":[OSD([sQuery(id+"F0.wireOp",EDGE,"E0.bottom"),sQuery(id+"F0.wireOp",EDGE,"E0.top"),sQuery(id+"F0.wireOp",EDGE,"E0.left"),sQuery(id+"F0.wireOp",EDGE,"E0.right")])]}),"instanceName":"1"}),"instanceName":"1"}),"instanceName":"1"}),"instanceName":"1"});
            var Q26;
            Q26=makeQuery(id+"F8.opPattern","COPY",BODY,{"derivedFrom":makeQuery(id+"F3.opPattern","COPY",BODY,{"derivedFrom":makeQuery(id+"F2.opPattern","COPY",BODY,{"derivedFrom":makeQuery(id+"F1.opExtrude","SWEPT_BODY",BODY,{"disambiguationData":[OSD([sQuery(id+"F0.wireOp",EDGE,"E2.bottom"),sQuery(id+"F0.wireOp",EDGE,"E2.top"),sQuery(id+"F0.wireOp",EDGE,"E2.left"),sQuery(id+"F0.wireOp",EDGE,"E2.right")])]}),"instanceName":"1"}),"instanceName":"1"}),"instanceName":"1"});
            var Q27;
            Q27=makeQuery(id+"F8.opPattern","COPY",BODY,{"derivedFrom":makeQuery(id+"F3.opPattern","COPY",BODY,{"derivedFrom":makeQuery(id+"F2.opPattern","COPY",BODY,{"derivedFrom":makeQuery(id+"F1.opExtrude","SWEPT_BODY",BODY,{"disambiguationData":[OSD([sQuery(id+"F0.wireOp",EDGE,"E1.bottom"),sQuery(id+"F0.wireOp",EDGE,"E1.top"),sQuery(id+"F0.wireOp",EDGE,"E1.left"),sQuery(id+"F0.wireOp",EDGE,"E1.right")])]}),"instanceName":"1"}),"instanceName":"1"}),"instanceName":"1"});
            var Q28;
            Q28=makeQuery(id+"F8.opPattern","COPY",BODY,{"derivedFrom":makeQuery(id+"F3.opPattern","COPY",BODY,{"derivedFrom":makeQuery(id+"F2.opPattern","COPY",BODY,{"derivedFrom":makeQuery(id+"F1.opExtrude","SWEPT_BODY",BODY,{"disambiguationData":[OSD([sQuery(id+"F0.wireOp",EDGE,"E0.bottom"),sQuery(id+"F0.wireOp",EDGE,"E0.top"),sQuery(id+"F0.wireOp",EDGE,"E0.left"),sQuery(id+"F0.wireOp",EDGE,"E0.right")])]}),"instanceName":"1"}),"instanceName":"1"}),"instanceName":"1"});
            var Q29;
            Q29=makeQuery(id+"F8.opPattern","COPY",BODY,{"derivedFrom":makeQuery(id+"F2.opPattern","COPY",BODY,{"derivedFrom":makeQuery(id+"F1.opExtrude","SWEPT_BODY",BODY,{"disambiguationData":[OSD([sQuery(id+"F0.wireOp",EDGE,"E2.bottom"),sQuery(id+"F0.wireOp",EDGE,"E2.top"),sQuery(id+"F0.wireOp",EDGE,"E2.left"),sQuery(id+"F0.wireOp",EDGE,"E2.right")])]}),"instanceName":"1"}),"instanceName":"1"});
            var Q30;
            Q30=makeQuery(id+"F8.opPattern","COPY",BODY,{"derivedFrom":makeQuery(id+"F2.opPattern","COPY",BODY,{"derivedFrom":makeQuery(id+"F1.opExtrude","SWEPT_BODY",BODY,{"disambiguationData":[OSD([sQuery(id+"F0.wireOp",EDGE,"E1.bottom"),sQuery(id+"F0.wireOp",EDGE,"E1.top"),sQuery(id+"F0.wireOp",EDGE,"E1.left"),sQuery(id+"F0.wireOp",EDGE,"E1.right")])]}),"instanceName":"1"}),"instanceName":"1"});
            var Q31;
            Q31=makeQuery(id+"F8.opPattern","COPY",BODY,{"derivedFrom":makeQuery(id+"F2.opPattern","COPY",BODY,{"derivedFrom":makeQuery(id+"F1.opExtrude","SWEPT_BODY",BODY,{"disambiguationData":[OSD([sQuery(id+"F0.wireOp",EDGE,"E0.bottom"),sQuery(id+"F0.wireOp",EDGE,"E0.top"),sQuery(id+"F0.wireOp",EDGE,"E0.left"),sQuery(id+"F0.wireOp",EDGE,"E0.right")])]}),"instanceName":"1"}),"instanceName":"1"});
            var Q32;
            Q32=makeQuery(id+"F8.opPattern","COPY",BODY,{"derivedFrom":makeQuery(id+"F1.opExtrude","SWEPT_BODY",BODY,{"disambiguationData":[OSD([sQuery(id+"F0.wireOp",EDGE,"E2.bottom"),sQuery(id+"F0.wireOp",EDGE,"E2.top"),sQuery(id+"F0.wireOp",EDGE,"E2.left"),sQuery(id+"F0.wireOp",EDGE,"E2.right")])]}),"instanceName":"1"});
            var Q33;
            Q33=makeQuery(id+"F7.opPattern","COPY",BODY,{"derivedFrom":makeQuery(id+"F6.opPattern","COPY",BODY,{"derivedFrom":makeQuery(id+"F5.opPattern","COPY",BODY,{"derivedFrom":makeQuery(id+"F4.opPattern","COPY",BODY,{"derivedFrom":makeQuery(id+"F3.opPattern","COPY",BODY,{"derivedFrom":makeQuery(id+"F2.opPattern","COPY",BODY,{"derivedFrom":makeQuery(id+"F1.opExtrude","SWEPT_BODY",BODY,{"disambiguationData":[OSD([sQuery(id+"F0.wireOp",EDGE,"E2.bottom"),sQuery(id+"F0.wireOp",EDGE,"E2.top"),sQuery(id+"F0.wireOp",EDGE,"E2.left"),sQuery(id+"F0.wireOp",EDGE,"E2.right")])]}),"instanceName":"1"}),"instanceName":"1"}),"instanceName":"1"}),"instanceName":"1"}),"instanceName":"1"}),"instanceName":"1"});
            var Q34;
            Q34=makeQuery(id+"F7.opPattern","COPY",BODY,{"derivedFrom":makeQuery(id+"F6.opPattern","COPY",BODY,{"derivedFrom":makeQuery(id+"F5.opPattern","COPY",BODY,{"derivedFrom":makeQuery(id+"F4.opPattern","COPY",BODY,{"derivedFrom":makeQuery(id+"F3.opPattern","COPY",BODY,{"derivedFrom":makeQuery(id+"F2.opPattern","COPY",BODY,{"derivedFrom":makeQuery(id+"F1.opExtrude","SWEPT_BODY",BODY,{"disambiguationData":[OSD([sQuery(id+"F0.wireOp",EDGE,"E1.bottom"),sQuery(id+"F0.wireOp",EDGE,"E1.top"),sQuery(id+"F0.wireOp",EDGE,"E1.left"),sQuery(id+"F0.wireOp",EDGE,"E1.right")])]}),"instanceName":"1"}),"instanceName":"1"}),"instanceName":"1"}),"instanceName":"1"}),"instanceName":"1"}),"instanceName":"1"});
            var Q35;
            Q35=makeQuery(id+"F7.opPattern","COPY",BODY,{"derivedFrom":makeQuery(id+"F6.opPattern","COPY",BODY,{"derivedFrom":makeQuery(id+"F5.opPattern","COPY",BODY,{"derivedFrom":makeQuery(id+"F4.opPattern","COPY",BODY,{"derivedFrom":makeQuery(id+"F3.opPattern","COPY",BODY,{"derivedFrom":makeQuery(id+"F2.opPattern","COPY",BODY,{"derivedFrom":makeQuery(id+"F1.opExtrude","SWEPT_BODY",BODY,{"disambiguationData":[OSD([sQuery(id+"F0.wireOp",EDGE,"E0.bottom"),sQuery(id+"F0.wireOp",EDGE,"E0.top"),sQuery(id+"F0.wireOp",EDGE,"E0.left"),sQuery(id+"F0.wireOp",EDGE,"E0.right")])]}),"instanceName":"1"}),"instanceName":"1"}),"instanceName":"1"}),"instanceName":"1"}),"instanceName":"1"}),"instanceName":"1"});
            var Q36;
            Q36=makeQuery(id+"F7.opPattern","COPY",BODY,{"derivedFrom":makeQuery(id+"F5.opPattern","COPY",BODY,{"derivedFrom":makeQuery(id+"F4.opPattern","COPY",BODY,{"derivedFrom":makeQuery(id+"F3.opPattern","COPY",BODY,{"derivedFrom":makeQuery(id+"F2.opPattern","COPY",BODY,{"derivedFrom":makeQuery(id+"F1.opExtrude","SWEPT_BODY",BODY,{"disambiguationData":[OSD([sQuery(id+"F0.wireOp",EDGE,"E2.bottom"),sQuery(id+"F0.wireOp",EDGE,"E2.top"),sQuery(id+"F0.wireOp",EDGE,"E2.left"),sQuery(id+"F0.wireOp",EDGE,"E2.right")])]}),"instanceName":"1"}),"instanceName":"1"}),"instanceName":"1"}),"instanceName":"1"}),"instanceName":"1"});
            var Q37;
            Q37=makeQuery(id+"F7.opPattern","COPY",BODY,{"derivedFrom":makeQuery(id+"F5.opPattern","COPY",BODY,{"derivedFrom":makeQuery(id+"F4.opPattern","COPY",BODY,{"derivedFrom":makeQuery(id+"F3.opPattern","COPY",BODY,{"derivedFrom":makeQuery(id+"F2.opPattern","COPY",BODY,{"derivedFrom":makeQuery(id+"F1.opExtrude","SWEPT_BODY",BODY,{"disambiguationData":[OSD([sQuery(id+"F0.wireOp",EDGE,"E1.bottom"),sQuery(id+"F0.wireOp",EDGE,"E1.top"),sQuery(id+"F0.wireOp",EDGE,"E1.left"),sQuery(id+"F0.wireOp",EDGE,"E1.right")])]}),"instanceName":"1"}),"instanceName":"1"}),"instanceName":"1"}),"instanceName":"1"}),"instanceName":"1"});
            var Q38;
            Q38=makeQuery(id+"F7.opPattern","COPY",BODY,{"derivedFrom":makeQuery(id+"F5.opPattern","COPY",BODY,{"derivedFrom":makeQuery(id+"F4.opPattern","COPY",BODY,{"derivedFrom":makeQuery(id+"F3.opPattern","COPY",BODY,{"derivedFrom":makeQuery(id+"F2.opPattern","COPY",BODY,{"derivedFrom":makeQuery(id+"F1.opExtrude","SWEPT_BODY",BODY,{"disambiguationData":[OSD([sQuery(id+"F0.wireOp",EDGE,"E0.bottom"),sQuery(id+"F0.wireOp",EDGE,"E0.top"),sQuery(id+"F0.wireOp",EDGE,"E0.left"),sQuery(id+"F0.wireOp",EDGE,"E0.right")])]}),"instanceName":"1"}),"instanceName":"1"}),"instanceName":"1"}),"instanceName":"1"}),"instanceName":"1"});
            var Q39;
            Q39=makeQuery(id+"F7.opPattern","COPY",BODY,{"derivedFrom":makeQuery(id+"F4.opPattern","COPY",BODY,{"derivedFrom":makeQuery(id+"F3.opPattern","COPY",BODY,{"derivedFrom":makeQuery(id+"F2.opPattern","COPY",BODY,{"derivedFrom":makeQuery(id+"F1.opExtrude","SWEPT_BODY",BODY,{"disambiguationData":[OSD([sQuery(id+"F0.wireOp",EDGE,"E2.bottom"),sQuery(id+"F0.wireOp",EDGE,"E2.top"),sQuery(id+"F0.wireOp",EDGE,"E2.left"),sQuery(id+"F0.wireOp",EDGE,"E2.right")])]}),"instanceName":"1"}),"instanceName":"1"}),"instanceName":"1"}),"instanceName":"1"});
            var Q40;
            Q40=makeQuery(id+"F7.opPattern","COPY",BODY,{"derivedFrom":makeQuery(id+"F4.opPattern","COPY",BODY,{"derivedFrom":makeQuery(id+"F3.opPattern","COPY",BODY,{"derivedFrom":makeQuery(id+"F2.opPattern","COPY",BODY,{"derivedFrom":makeQuery(id+"F1.opExtrude","SWEPT_BODY",BODY,{"disambiguationData":[OSD([sQuery(id+"F0.wireOp",EDGE,"E1.bottom"),sQuery(id+"F0.wireOp",EDGE,"E1.top"),sQuery(id+"F0.wireOp",EDGE,"E1.left"),sQuery(id+"F0.wireOp",EDGE,"E1.right")])]}),"instanceName":"1"}),"instanceName":"1"}),"instanceName":"1"}),"instanceName":"1"});
            var Q41;
            Q41=makeQuery(id+"F7.opPattern","COPY",BODY,{"derivedFrom":makeQuery(id+"F4.opPattern","COPY",BODY,{"derivedFrom":makeQuery(id+"F3.opPattern","COPY",BODY,{"derivedFrom":makeQuery(id+"F2.opPattern","COPY",BODY,{"derivedFrom":makeQuery(id+"F1.opExtrude","SWEPT_BODY",BODY,{"disambiguationData":[OSD([sQuery(id+"F0.wireOp",EDGE,"E0.bottom"),sQuery(id+"F0.wireOp",EDGE,"E0.top"),sQuery(id+"F0.wireOp",EDGE,"E0.left"),sQuery(id+"F0.wireOp",EDGE,"E0.right")])]}),"instanceName":"1"}),"instanceName":"1"}),"instanceName":"1"}),"instanceName":"1"});
            var Q42;
            Q42=makeQuery(id+"F7.opPattern","COPY",BODY,{"derivedFrom":makeQuery(id+"F3.opPattern","COPY",BODY,{"derivedFrom":makeQuery(id+"F2.opPattern","COPY",BODY,{"derivedFrom":makeQuery(id+"F1.opExtrude","SWEPT_BODY",BODY,{"disambiguationData":[OSD([sQuery(id+"F0.wireOp",EDGE,"E2.bottom"),sQuery(id+"F0.wireOp",EDGE,"E2.top"),sQuery(id+"F0.wireOp",EDGE,"E2.left"),sQuery(id+"F0.wireOp",EDGE,"E2.right")])]}),"instanceName":"1"}),"instanceName":"1"}),"instanceName":"1"});
            var Q43;
            Q43=makeQuery(id+"F7.opPattern","COPY",BODY,{"derivedFrom":makeQuery(id+"F3.opPattern","COPY",BODY,{"derivedFrom":makeQuery(id+"F2.opPattern","COPY",BODY,{"derivedFrom":makeQuery(id+"F1.opExtrude","SWEPT_BODY",BODY,{"disambiguationData":[OSD([sQuery(id+"F0.wireOp",EDGE,"E1.bottom"),sQuery(id+"F0.wireOp",EDGE,"E1.top"),sQuery(id+"F0.wireOp",EDGE,"E1.left"),sQuery(id+"F0.wireOp",EDGE,"E1.right")])]}),"instanceName":"1"}),"instanceName":"1"}),"instanceName":"1"});
            var Q44;
            Q44=makeQuery(id+"F7.opPattern","COPY",BODY,{"derivedFrom":makeQuery(id+"F3.opPattern","COPY",BODY,{"derivedFrom":makeQuery(id+"F2.opPattern","COPY",BODY,{"derivedFrom":makeQuery(id+"F1.opExtrude","SWEPT_BODY",BODY,{"disambiguationData":[OSD([sQuery(id+"F0.wireOp",EDGE,"E0.bottom"),sQuery(id+"F0.wireOp",EDGE,"E0.top"),sQuery(id+"F0.wireOp",EDGE,"E0.left"),sQuery(id+"F0.wireOp",EDGE,"E0.right")])]}),"instanceName":"1"}),"instanceName":"1"}),"instanceName":"1"});
            var Q45;
            Q45=makeQuery(id+"F7.opPattern","COPY",BODY,{"derivedFrom":makeQuery(id+"F2.opPattern","COPY",BODY,{"derivedFrom":makeQuery(id+"F1.opExtrude","SWEPT_BODY",BODY,{"disambiguationData":[OSD([sQuery(id+"F0.wireOp",EDGE,"E2.bottom"),sQuery(id+"F0.wireOp",EDGE,"E2.top"),sQuery(id+"F0.wireOp",EDGE,"E2.left"),sQuery(id+"F0.wireOp",EDGE,"E2.right")])]}),"instanceName":"1"}),"instanceName":"1"});
            var Q46;
            Q46=makeQuery(id+"F7.opPattern","COPY",BODY,{"derivedFrom":makeQuery(id+"F2.opPattern","COPY",BODY,{"derivedFrom":makeQuery(id+"F1.opExtrude","SWEPT_BODY",BODY,{"disambiguationData":[OSD([sQuery(id+"F0.wireOp",EDGE,"E1.bottom"),sQuery(id+"F0.wireOp",EDGE,"E1.top"),sQuery(id+"F0.wireOp",EDGE,"E1.left"),sQuery(id+"F0.wireOp",EDGE,"E1.right")])]}),"instanceName":"1"}),"instanceName":"1"});
            var Q47;
            Q47=makeQuery(id+"F7.opPattern","COPY",BODY,{"derivedFrom":makeQuery(id+"F2.opPattern","COPY",BODY,{"derivedFrom":makeQuery(id+"F1.opExtrude","SWEPT_BODY",BODY,{"disambiguationData":[OSD([sQuery(id+"F0.wireOp",EDGE,"E0.bottom"),sQuery(id+"F0.wireOp",EDGE,"E0.top"),sQuery(id+"F0.wireOp",EDGE,"E0.left"),sQuery(id+"F0.wireOp",EDGE,"E0.right")])]}),"instanceName":"1"}),"instanceName":"1"});
            var Q48;
            Q48=makeQuery(id+"F6.opPattern","COPY",BODY,{"derivedFrom":makeQuery(id+"F5.opPattern","COPY",BODY,{"derivedFrom":makeQuery(id+"F4.opPattern","COPY",BODY,{"derivedFrom":makeQuery(id+"F3.opPattern","COPY",BODY,{"derivedFrom":makeQuery(id+"F2.opPattern","COPY",BODY,{"derivedFrom":makeQuery(id+"F1.opExtrude","SWEPT_BODY",BODY,{"disambiguationData":[OSD([sQuery(id+"F0.wireOp",EDGE,"E2.bottom"),sQuery(id+"F0.wireOp",EDGE,"E2.top"),sQuery(id+"F0.wireOp",EDGE,"E2.left"),sQuery(id+"F0.wireOp",EDGE,"E2.right")])]}),"instanceName":"1"}),"instanceName":"1"}),"instanceName":"1"}),"instanceName":"1"}),"instanceName":"1"});
            var Q49;
            Q49=makeQuery(id+"F6.opPattern","COPY",BODY,{"derivedFrom":makeQuery(id+"F5.opPattern","COPY",BODY,{"derivedFrom":makeQuery(id+"F4.opPattern","COPY",BODY,{"derivedFrom":makeQuery(id+"F3.opPattern","COPY",BODY,{"derivedFrom":makeQuery(id+"F2.opPattern","COPY",BODY,{"derivedFrom":makeQuery(id+"F1.opExtrude","SWEPT_BODY",BODY,{"disambiguationData":[OSD([sQuery(id+"F0.wireOp",EDGE,"E1.bottom"),sQuery(id+"F0.wireOp",EDGE,"E1.top"),sQuery(id+"F0.wireOp",EDGE,"E1.left"),sQuery(id+"F0.wireOp",EDGE,"E1.right")])]}),"instanceName":"1"}),"instanceName":"1"}),"instanceName":"1"}),"instanceName":"1"}),"instanceName":"1"});
            var Q50;
            Q50=makeQuery(id+"F6.opPattern","COPY",BODY,{"derivedFrom":makeQuery(id+"F5.opPattern","COPY",BODY,{"derivedFrom":makeQuery(id+"F4.opPattern","COPY",BODY,{"derivedFrom":makeQuery(id+"F3.opPattern","COPY",BODY,{"derivedFrom":makeQuery(id+"F2.opPattern","COPY",BODY,{"derivedFrom":makeQuery(id+"F1.opExtrude","SWEPT_BODY",BODY,{"disambiguationData":[OSD([sQuery(id+"F0.wireOp",EDGE,"E0.bottom"),sQuery(id+"F0.wireOp",EDGE,"E0.top"),sQuery(id+"F0.wireOp",EDGE,"E0.left"),sQuery(id+"F0.wireOp",EDGE,"E0.right")])]}),"instanceName":"1"}),"instanceName":"1"}),"instanceName":"1"}),"instanceName":"1"}),"instanceName":"1"});
            var Q51;
            Q51=makeQuery(id+"F5.opPattern","COPY",BODY,{"derivedFrom":makeQuery(id+"F4.opPattern","COPY",BODY,{"derivedFrom":makeQuery(id+"F3.opPattern","COPY",BODY,{"derivedFrom":makeQuery(id+"F2.opPattern","COPY",BODY,{"derivedFrom":makeQuery(id+"F1.opExtrude","SWEPT_BODY",BODY,{"disambiguationData":[OSD([sQuery(id+"F0.wireOp",EDGE,"E2.bottom"),sQuery(id+"F0.wireOp",EDGE,"E2.top"),sQuery(id+"F0.wireOp",EDGE,"E2.left"),sQuery(id+"F0.wireOp",EDGE,"E2.right")])]}),"instanceName":"1"}),"instanceName":"1"}),"instanceName":"1"}),"instanceName":"1"});
            var Q52;
            Q52=makeQuery(id+"F5.opPattern","COPY",BODY,{"derivedFrom":makeQuery(id+"F4.opPattern","COPY",BODY,{"derivedFrom":makeQuery(id+"F3.opPattern","COPY",BODY,{"derivedFrom":makeQuery(id+"F2.opPattern","COPY",BODY,{"derivedFrom":makeQuery(id+"F1.opExtrude","SWEPT_BODY",BODY,{"disambiguationData":[OSD([sQuery(id+"F0.wireOp",EDGE,"E1.bottom"),sQuery(id+"F0.wireOp",EDGE,"E1.top"),sQuery(id+"F0.wireOp",EDGE,"E1.left"),sQuery(id+"F0.wireOp",EDGE,"E1.right")])]}),"instanceName":"1"}),"instanceName":"1"}),"instanceName":"1"}),"instanceName":"1"});
            var Q53;
            Q53=makeQuery(id+"F5.opPattern","COPY",BODY,{"derivedFrom":makeQuery(id+"F4.opPattern","COPY",BODY,{"derivedFrom":makeQuery(id+"F3.opPattern","COPY",BODY,{"derivedFrom":makeQuery(id+"F2.opPattern","COPY",BODY,{"derivedFrom":makeQuery(id+"F1.opExtrude","SWEPT_BODY",BODY,{"disambiguationData":[OSD([sQuery(id+"F0.wireOp",EDGE,"E0.bottom"),sQuery(id+"F0.wireOp",EDGE,"E0.top"),sQuery(id+"F0.wireOp",EDGE,"E0.left"),sQuery(id+"F0.wireOp",EDGE,"E0.right")])]}),"instanceName":"1"}),"instanceName":"1"}),"instanceName":"1"}),"instanceName":"1"});
            var Q54;
            Q54=makeQuery(id+"F4.opPattern","COPY",BODY,{"derivedFrom":makeQuery(id+"F3.opPattern","COPY",BODY,{"derivedFrom":makeQuery(id+"F2.opPattern","COPY",BODY,{"derivedFrom":makeQuery(id+"F1.opExtrude","SWEPT_BODY",BODY,{"disambiguationData":[OSD([sQuery(id+"F0.wireOp",EDGE,"E2.bottom"),sQuery(id+"F0.wireOp",EDGE,"E2.top"),sQuery(id+"F0.wireOp",EDGE,"E2.left"),sQuery(id+"F0.wireOp",EDGE,"E2.right")])]}),"instanceName":"1"}),"instanceName":"1"}),"instanceName":"1"});
            var Q55;
            Q55=makeQuery(id+"F4.opPattern","COPY",BODY,{"derivedFrom":makeQuery(id+"F3.opPattern","COPY",BODY,{"derivedFrom":makeQuery(id+"F2.opPattern","COPY",BODY,{"derivedFrom":makeQuery(id+"F1.opExtrude","SWEPT_BODY",BODY,{"disambiguationData":[OSD([sQuery(id+"F0.wireOp",EDGE,"E1.bottom"),sQuery(id+"F0.wireOp",EDGE,"E1.top"),sQuery(id+"F0.wireOp",EDGE,"E1.left"),sQuery(id+"F0.wireOp",EDGE,"E1.right")])]}),"instanceName":"1"}),"instanceName":"1"}),"instanceName":"1"});
            var Q56;
            Q56=makeQuery(id+"F4.opPattern","COPY",BODY,{"derivedFrom":makeQuery(id+"F3.opPattern","COPY",BODY,{"derivedFrom":makeQuery(id+"F2.opPattern","COPY",BODY,{"derivedFrom":makeQuery(id+"F1.opExtrude","SWEPT_BODY",BODY,{"disambiguationData":[OSD([sQuery(id+"F0.wireOp",EDGE,"E0.bottom"),sQuery(id+"F0.wireOp",EDGE,"E0.top"),sQuery(id+"F0.wireOp",EDGE,"E0.left"),sQuery(id+"F0.wireOp",EDGE,"E0.right")])]}),"instanceName":"1"}),"instanceName":"1"}),"instanceName":"1"});
            var Q57;
            Q57=makeQuery(id+"F3.opPattern","COPY",BODY,{"derivedFrom":makeQuery(id+"F2.opPattern","COPY",BODY,{"derivedFrom":makeQuery(id+"F1.opExtrude","SWEPT_BODY",BODY,{"disambiguationData":[OSD([sQuery(id+"F0.wireOp",EDGE,"E2.bottom"),sQuery(id+"F0.wireOp",EDGE,"E2.top"),sQuery(id+"F0.wireOp",EDGE,"E2.left"),sQuery(id+"F0.wireOp",EDGE,"E2.right")])]}),"instanceName":"1"}),"instanceName":"1"});
            var Q58;
            Q58=makeQuery(id+"F3.opPattern","COPY",BODY,{"derivedFrom":makeQuery(id+"F2.opPattern","COPY",BODY,{"derivedFrom":makeQuery(id+"F1.opExtrude","SWEPT_BODY",BODY,{"disambiguationData":[OSD([sQuery(id+"F0.wireOp",EDGE,"E1.bottom"),sQuery(id+"F0.wireOp",EDGE,"E1.top"),sQuery(id+"F0.wireOp",EDGE,"E1.left"),sQuery(id+"F0.wireOp",EDGE,"E1.right")])]}),"instanceName":"1"}),"instanceName":"1"});
            var Q59;
            Q59=makeQuery(id+"F3.opPattern","COPY",BODY,{"derivedFrom":makeQuery(id+"F2.opPattern","COPY",BODY,{"derivedFrom":makeQuery(id+"F1.opExtrude","SWEPT_BODY",BODY,{"disambiguationData":[OSD([sQuery(id+"F0.wireOp",EDGE,"E0.bottom"),sQuery(id+"F0.wireOp",EDGE,"E0.top"),sQuery(id+"F0.wireOp",EDGE,"E0.left"),sQuery(id+"F0.wireOp",EDGE,"E0.right")])]}),"instanceName":"1"}),"instanceName":"1"});
            var Q60;
            Q60=makeQuery(id+"F2.opPattern","COPY",BODY,{"derivedFrom":makeQuery(id+"F1.opExtrude","SWEPT_BODY",BODY,{"disambiguationData":[OSD([sQuery(id+"F0.wireOp",EDGE,"E2.bottom"),sQuery(id+"F0.wireOp",EDGE,"E2.top"),sQuery(id+"F0.wireOp",EDGE,"E2.left"),sQuery(id+"F0.wireOp",EDGE,"E2.right")])]}),"instanceName":"1"});
            var Q61;
            Q61=makeQuery(id+"F2.opPattern","COPY",BODY,{"derivedFrom":makeQuery(id+"F1.opExtrude","SWEPT_BODY",BODY,{"disambiguationData":[OSD([sQuery(id+"F0.wireOp",EDGE,"E1.bottom"),sQuery(id+"F0.wireOp",EDGE,"E1.top"),sQuery(id+"F0.wireOp",EDGE,"E1.left"),sQuery(id+"F0.wireOp",EDGE,"E1.right")])]}),"instanceName":"1"});
            var Q62;
            Q62=makeQuery(id+"F2.opPattern","COPY",BODY,{"derivedFrom":makeQuery(id+"F1.opExtrude","SWEPT_BODY",BODY,{"disambiguationData":[OSD([sQuery(id+"F0.wireOp",EDGE,"E0.bottom"),sQuery(id+"F0.wireOp",EDGE,"E0.top"),sQuery(id+"F0.wireOp",EDGE,"E0.left"),sQuery(id+"F0.wireOp",EDGE,"E0.right")])]}),"instanceName":"1"});
            var Q63;
            Q63=makeQuery(id+"F9.opPattern","COPY",BODY,{"derivedFrom":makeQuery(id+"F1.opExtrude","SWEPT_BODY",BODY,{"disambiguationData":[OSD([sQuery(id+"F0.wireOp",EDGE,"E0.bottom"),sQuery(id+"F0.wireOp",EDGE,"E0.top"),sQuery(id+"F0.wireOp",EDGE,"E0.left"),sQuery(id+"F0.wireOp",EDGE,"E0.right")])]}),"instanceName":"1"});
            var Q64;
            Q64=makeQuery(id+"F9.opPattern","COPY",BODY,{"derivedFrom":makeQuery(id+"F1.opExtrude","SWEPT_BODY",BODY,{"disambiguationData":[OSD([sQuery(id+"F0.wireOp",EDGE,"E1.bottom"),sQuery(id+"F0.wireOp",EDGE,"E1.top"),sQuery(id+"F0.wireOp",EDGE,"E1.left"),sQuery(id+"F0.wireOp",EDGE,"E1.right")])]}),"instanceName":"1"});
            var Q65;
            Q65=makeQuery(id+"F9.opPattern","COPY",BODY,{"derivedFrom":makeQuery(id+"F1.opExtrude","SWEPT_BODY",BODY,{"disambiguationData":[OSD([sQuery(id+"F0.wireOp",EDGE,"E2.bottom"),sQuery(id+"F0.wireOp",EDGE,"E2.top"),sQuery(id+"F0.wireOp",EDGE,"E2.left"),sQuery(id+"F0.wireOp",EDGE,"E2.right")])]}),"instanceName":"1"});
            var Q66;
            Q66=makeQuery(id+"F9.opPattern","COPY",BODY,{"derivedFrom":makeQuery(id+"F2.opPattern","COPY",BODY,{"derivedFrom":makeQuery(id+"F1.opExtrude","SWEPT_BODY",BODY,{"disambiguationData":[OSD([sQuery(id+"F0.wireOp",EDGE,"E0.bottom"),sQuery(id+"F0.wireOp",EDGE,"E0.top"),sQuery(id+"F0.wireOp",EDGE,"E0.left"),sQuery(id+"F0.wireOp",EDGE,"E0.right")])]}),"instanceName":"1"}),"instanceName":"1"});
            var Q67;
            Q67=makeQuery(id+"F9.opPattern","COPY",BODY,{"derivedFrom":makeQuery(id+"F2.opPattern","COPY",BODY,{"derivedFrom":makeQuery(id+"F1.opExtrude","SWEPT_BODY",BODY,{"disambiguationData":[OSD([sQuery(id+"F0.wireOp",EDGE,"E1.bottom"),sQuery(id+"F0.wireOp",EDGE,"E1.top"),sQuery(id+"F0.wireOp",EDGE,"E1.left"),sQuery(id+"F0.wireOp",EDGE,"E1.right")])]}),"instanceName":"1"}),"instanceName":"1"});
            var Q68;
            Q68=makeQuery(id+"F9.opPattern","COPY",BODY,{"derivedFrom":makeQuery(id+"F2.opPattern","COPY",BODY,{"derivedFrom":makeQuery(id+"F1.opExtrude","SWEPT_BODY",BODY,{"disambiguationData":[OSD([sQuery(id+"F0.wireOp",EDGE,"E2.bottom"),sQuery(id+"F0.wireOp",EDGE,"E2.top"),sQuery(id+"F0.wireOp",EDGE,"E2.left"),sQuery(id+"F0.wireOp",EDGE,"E2.right")])]}),"instanceName":"1"}),"instanceName":"1"});
            var Q69;
            Q69=makeQuery(id+"F9.opPattern","COPY",BODY,{"derivedFrom":makeQuery(id+"F3.opPattern","COPY",BODY,{"derivedFrom":makeQuery(id+"F2.opPattern","COPY",BODY,{"derivedFrom":makeQuery(id+"F1.opExtrude","SWEPT_BODY",BODY,{"disambiguationData":[OSD([sQuery(id+"F0.wireOp",EDGE,"E0.bottom"),sQuery(id+"F0.wireOp",EDGE,"E0.top"),sQuery(id+"F0.wireOp",EDGE,"E0.left"),sQuery(id+"F0.wireOp",EDGE,"E0.right")])]}),"instanceName":"1"}),"instanceName":"1"}),"instanceName":"1"});
            var Q70;
            Q70=makeQuery(id+"F9.opPattern","COPY",BODY,{"derivedFrom":makeQuery(id+"F3.opPattern","COPY",BODY,{"derivedFrom":makeQuery(id+"F2.opPattern","COPY",BODY,{"derivedFrom":makeQuery(id+"F1.opExtrude","SWEPT_BODY",BODY,{"disambiguationData":[OSD([sQuery(id+"F0.wireOp",EDGE,"E1.bottom"),sQuery(id+"F0.wireOp",EDGE,"E1.top"),sQuery(id+"F0.wireOp",EDGE,"E1.left"),sQuery(id+"F0.wireOp",EDGE,"E1.right")])]}),"instanceName":"1"}),"instanceName":"1"}),"instanceName":"1"});
            var Q71;
            Q71=makeQuery(id+"F9.opPattern","COPY",BODY,{"derivedFrom":makeQuery(id+"F3.opPattern","COPY",BODY,{"derivedFrom":makeQuery(id+"F2.opPattern","COPY",BODY,{"derivedFrom":makeQuery(id+"F1.opExtrude","SWEPT_BODY",BODY,{"disambiguationData":[OSD([sQuery(id+"F0.wireOp",EDGE,"E2.bottom"),sQuery(id+"F0.wireOp",EDGE,"E2.top"),sQuery(id+"F0.wireOp",EDGE,"E2.left"),sQuery(id+"F0.wireOp",EDGE,"E2.right")])]}),"instanceName":"1"}),"instanceName":"1"}),"instanceName":"1"});
            var Q72;
            Q72=makeQuery(id+"F9.opPattern","COPY",BODY,{"derivedFrom":makeQuery(id+"F4.opPattern","COPY",BODY,{"derivedFrom":makeQuery(id+"F3.opPattern","COPY",BODY,{"derivedFrom":makeQuery(id+"F2.opPattern","COPY",BODY,{"derivedFrom":makeQuery(id+"F1.opExtrude","SWEPT_BODY",BODY,{"disambiguationData":[OSD([sQuery(id+"F0.wireOp",EDGE,"E0.bottom"),sQuery(id+"F0.wireOp",EDGE,"E0.top"),sQuery(id+"F0.wireOp",EDGE,"E0.left"),sQuery(id+"F0.wireOp",EDGE,"E0.right")])]}),"instanceName":"1"}),"instanceName":"1"}),"instanceName":"1"}),"instanceName":"1"});
            var Q73;
            Q73=makeQuery(id+"F9.opPattern","COPY",BODY,{"derivedFrom":makeQuery(id+"F4.opPattern","COPY",BODY,{"derivedFrom":makeQuery(id+"F3.opPattern","COPY",BODY,{"derivedFrom":makeQuery(id+"F2.opPattern","COPY",BODY,{"derivedFrom":makeQuery(id+"F1.opExtrude","SWEPT_BODY",BODY,{"disambiguationData":[OSD([sQuery(id+"F0.wireOp",EDGE,"E1.bottom"),sQuery(id+"F0.wireOp",EDGE,"E1.top"),sQuery(id+"F0.wireOp",EDGE,"E1.left"),sQuery(id+"F0.wireOp",EDGE,"E1.right")])]}),"instanceName":"1"}),"instanceName":"1"}),"instanceName":"1"}),"instanceName":"1"});
            var Q74;
            Q74=makeQuery(id+"F9.opPattern","COPY",BODY,{"derivedFrom":makeQuery(id+"F4.opPattern","COPY",BODY,{"derivedFrom":makeQuery(id+"F3.opPattern","COPY",BODY,{"derivedFrom":makeQuery(id+"F2.opPattern","COPY",BODY,{"derivedFrom":makeQuery(id+"F1.opExtrude","SWEPT_BODY",BODY,{"disambiguationData":[OSD([sQuery(id+"F0.wireOp",EDGE,"E2.bottom"),sQuery(id+"F0.wireOp",EDGE,"E2.top"),sQuery(id+"F0.wireOp",EDGE,"E2.left"),sQuery(id+"F0.wireOp",EDGE,"E2.right")])]}),"instanceName":"1"}),"instanceName":"1"}),"instanceName":"1"}),"instanceName":"1"});
            var Q75;
            Q75=makeQuery(id+"F9.opPattern","COPY",BODY,{"derivedFrom":makeQuery(id+"F5.opPattern","COPY",BODY,{"derivedFrom":makeQuery(id+"F4.opPattern","COPY",BODY,{"derivedFrom":makeQuery(id+"F3.opPattern","COPY",BODY,{"derivedFrom":makeQuery(id+"F2.opPattern","COPY",BODY,{"derivedFrom":makeQuery(id+"F1.opExtrude","SWEPT_BODY",BODY,{"disambiguationData":[OSD([sQuery(id+"F0.wireOp",EDGE,"E0.bottom"),sQuery(id+"F0.wireOp",EDGE,"E0.top"),sQuery(id+"F0.wireOp",EDGE,"E0.left"),sQuery(id+"F0.wireOp",EDGE,"E0.right")])]}),"instanceName":"1"}),"instanceName":"1"}),"instanceName":"1"}),"instanceName":"1"}),"instanceName":"1"});
            var Q76;
            Q76=makeQuery(id+"F9.opPattern","COPY",BODY,{"derivedFrom":makeQuery(id+"F5.opPattern","COPY",BODY,{"derivedFrom":makeQuery(id+"F4.opPattern","COPY",BODY,{"derivedFrom":makeQuery(id+"F3.opPattern","COPY",BODY,{"derivedFrom":makeQuery(id+"F2.opPattern","COPY",BODY,{"derivedFrom":makeQuery(id+"F1.opExtrude","SWEPT_BODY",BODY,{"disambiguationData":[OSD([sQuery(id+"F0.wireOp",EDGE,"E1.bottom"),sQuery(id+"F0.wireOp",EDGE,"E1.top"),sQuery(id+"F0.wireOp",EDGE,"E1.left"),sQuery(id+"F0.wireOp",EDGE,"E1.right")])]}),"instanceName":"1"}),"instanceName":"1"}),"instanceName":"1"}),"instanceName":"1"}),"instanceName":"1"});
            var Q77;
            Q77=makeQuery(id+"F9.opPattern","COPY",BODY,{"derivedFrom":makeQuery(id+"F5.opPattern","COPY",BODY,{"derivedFrom":makeQuery(id+"F4.opPattern","COPY",BODY,{"derivedFrom":makeQuery(id+"F3.opPattern","COPY",BODY,{"derivedFrom":makeQuery(id+"F2.opPattern","COPY",BODY,{"derivedFrom":makeQuery(id+"F1.opExtrude","SWEPT_BODY",BODY,{"disambiguationData":[OSD([sQuery(id+"F0.wireOp",EDGE,"E2.bottom"),sQuery(id+"F0.wireOp",EDGE,"E2.top"),sQuery(id+"F0.wireOp",EDGE,"E2.left"),sQuery(id+"F0.wireOp",EDGE,"E2.right")])]}),"instanceName":"1"}),"instanceName":"1"}),"instanceName":"1"}),"instanceName":"1"}),"instanceName":"1"});
            var Q78;
            Q78=makeQuery(id+"F9.opPattern","COPY",BODY,{"derivedFrom":makeQuery(id+"F6.opPattern","COPY",BODY,{"derivedFrom":makeQuery(id+"F5.opPattern","COPY",BODY,{"derivedFrom":makeQuery(id+"F4.opPattern","COPY",BODY,{"derivedFrom":makeQuery(id+"F3.opPattern","COPY",BODY,{"derivedFrom":makeQuery(id+"F2.opPattern","COPY",BODY,{"derivedFrom":makeQuery(id+"F1.opExtrude","SWEPT_BODY",BODY,{"disambiguationData":[OSD([sQuery(id+"F0.wireOp",EDGE,"E0.bottom"),sQuery(id+"F0.wireOp",EDGE,"E0.top"),sQuery(id+"F0.wireOp",EDGE,"E0.left"),sQuery(id+"F0.wireOp",EDGE,"E0.right")])]}),"instanceName":"1"}),"instanceName":"1"}),"instanceName":"1"}),"instanceName":"1"}),"instanceName":"1"}),"instanceName":"1"});
            var Q79;
            Q79=makeQuery(id+"F9.opPattern","COPY",BODY,{"derivedFrom":makeQuery(id+"F6.opPattern","COPY",BODY,{"derivedFrom":makeQuery(id+"F5.opPattern","COPY",BODY,{"derivedFrom":makeQuery(id+"F4.opPattern","COPY",BODY,{"derivedFrom":makeQuery(id+"F3.opPattern","COPY",BODY,{"derivedFrom":makeQuery(id+"F2.opPattern","COPY",BODY,{"derivedFrom":makeQuery(id+"F1.opExtrude","SWEPT_BODY",BODY,{"disambiguationData":[OSD([sQuery(id+"F0.wireOp",EDGE,"E1.bottom"),sQuery(id+"F0.wireOp",EDGE,"E1.top"),sQuery(id+"F0.wireOp",EDGE,"E1.left"),sQuery(id+"F0.wireOp",EDGE,"E1.right")])]}),"instanceName":"1"}),"instanceName":"1"}),"instanceName":"1"}),"instanceName":"1"}),"instanceName":"1"}),"instanceName":"1"});
            var Q80;
            Q80=makeQuery(id+"F9.opPattern","COPY",BODY,{"derivedFrom":makeQuery(id+"F6.opPattern","COPY",BODY,{"derivedFrom":makeQuery(id+"F5.opPattern","COPY",BODY,{"derivedFrom":makeQuery(id+"F4.opPattern","COPY",BODY,{"derivedFrom":makeQuery(id+"F3.opPattern","COPY",BODY,{"derivedFrom":makeQuery(id+"F2.opPattern","COPY",BODY,{"derivedFrom":makeQuery(id+"F1.opExtrude","SWEPT_BODY",BODY,{"disambiguationData":[OSD([sQuery(id+"F0.wireOp",EDGE,"E2.bottom"),sQuery(id+"F0.wireOp",EDGE,"E2.top"),sQuery(id+"F0.wireOp",EDGE,"E2.left"),sQuery(id+"F0.wireOp",EDGE,"E2.right")])]}),"instanceName":"1"}),"instanceName":"1"}),"instanceName":"1"}),"instanceName":"1"}),"instanceName":"1"}),"instanceName":"1"});
            var Q81;
            Q81=makeQuery(id+"F9.opPattern","COPY",BODY,{"derivedFrom":makeQuery(id+"F7.opPattern","COPY",BODY,{"derivedFrom":makeQuery(id+"F1.opExtrude","SWEPT_BODY",BODY,{"disambiguationData":[OSD([sQuery(id+"F0.wireOp",EDGE,"E0.bottom"),sQuery(id+"F0.wireOp",EDGE,"E0.top"),sQuery(id+"F0.wireOp",EDGE,"E0.left"),sQuery(id+"F0.wireOp",EDGE,"E0.right")])]}),"instanceName":"1"}),"instanceName":"1"});
            var Q82;
            Q82=makeQuery(id+"F9.opPattern","COPY",BODY,{"derivedFrom":makeQuery(id+"F7.opPattern","COPY",BODY,{"derivedFrom":makeQuery(id+"F1.opExtrude","SWEPT_BODY",BODY,{"disambiguationData":[OSD([sQuery(id+"F0.wireOp",EDGE,"E1.bottom"),sQuery(id+"F0.wireOp",EDGE,"E1.top"),sQuery(id+"F0.wireOp",EDGE,"E1.left"),sQuery(id+"F0.wireOp",EDGE,"E1.right")])]}),"instanceName":"1"}),"instanceName":"1"});
            var Q83;
            Q83=makeQuery(id+"F9.opPattern","COPY",BODY,{"derivedFrom":makeQuery(id+"F7.opPattern","COPY",BODY,{"derivedFrom":makeQuery(id+"F1.opExtrude","SWEPT_BODY",BODY,{"disambiguationData":[OSD([sQuery(id+"F0.wireOp",EDGE,"E2.bottom"),sQuery(id+"F0.wireOp",EDGE,"E2.top"),sQuery(id+"F0.wireOp",EDGE,"E2.left"),sQuery(id+"F0.wireOp",EDGE,"E2.right")])]}),"instanceName":"1"}),"instanceName":"1"});
            var Q84;
            Q84=makeQuery(id+"F9.opPattern","COPY",BODY,{"derivedFrom":makeQuery(id+"F7.opPattern","COPY",BODY,{"derivedFrom":makeQuery(id+"F2.opPattern","COPY",BODY,{"derivedFrom":makeQuery(id+"F1.opExtrude","SWEPT_BODY",BODY,{"disambiguationData":[OSD([sQuery(id+"F0.wireOp",EDGE,"E0.bottom"),sQuery(id+"F0.wireOp",EDGE,"E0.top"),sQuery(id+"F0.wireOp",EDGE,"E0.left"),sQuery(id+"F0.wireOp",EDGE,"E0.right")])]}),"instanceName":"1"}),"instanceName":"1"}),"instanceName":"1"});
            var Q85;
            Q85=makeQuery(id+"F9.opPattern","COPY",BODY,{"derivedFrom":makeQuery(id+"F7.opPattern","COPY",BODY,{"derivedFrom":makeQuery(id+"F2.opPattern","COPY",BODY,{"derivedFrom":makeQuery(id+"F1.opExtrude","SWEPT_BODY",BODY,{"disambiguationData":[OSD([sQuery(id+"F0.wireOp",EDGE,"E1.bottom"),sQuery(id+"F0.wireOp",EDGE,"E1.top"),sQuery(id+"F0.wireOp",EDGE,"E1.left"),sQuery(id+"F0.wireOp",EDGE,"E1.right")])]}),"instanceName":"1"}),"instanceName":"1"}),"instanceName":"1"});
            var Q86;
            Q86=makeQuery(id+"F9.opPattern","COPY",BODY,{"derivedFrom":makeQuery(id+"F7.opPattern","COPY",BODY,{"derivedFrom":makeQuery(id+"F2.opPattern","COPY",BODY,{"derivedFrom":makeQuery(id+"F1.opExtrude","SWEPT_BODY",BODY,{"disambiguationData":[OSD([sQuery(id+"F0.wireOp",EDGE,"E2.bottom"),sQuery(id+"F0.wireOp",EDGE,"E2.top"),sQuery(id+"F0.wireOp",EDGE,"E2.left"),sQuery(id+"F0.wireOp",EDGE,"E2.right")])]}),"instanceName":"1"}),"instanceName":"1"}),"instanceName":"1"});
            var Q87;
            Q87=makeQuery(id+"F9.opPattern","COPY",BODY,{"derivedFrom":makeQuery(id+"F7.opPattern","COPY",BODY,{"derivedFrom":makeQuery(id+"F3.opPattern","COPY",BODY,{"derivedFrom":makeQuery(id+"F2.opPattern","COPY",BODY,{"derivedFrom":makeQuery(id+"F1.opExtrude","SWEPT_BODY",BODY,{"disambiguationData":[OSD([sQuery(id+"F0.wireOp",EDGE,"E0.bottom"),sQuery(id+"F0.wireOp",EDGE,"E0.top"),sQuery(id+"F0.wireOp",EDGE,"E0.left"),sQuery(id+"F0.wireOp",EDGE,"E0.right")])]}),"instanceName":"1"}),"instanceName":"1"}),"instanceName":"1"}),"instanceName":"1"});
            var Q88;
            Q88=makeQuery(id+"F9.opPattern","COPY",BODY,{"derivedFrom":makeQuery(id+"F7.opPattern","COPY",BODY,{"derivedFrom":makeQuery(id+"F3.opPattern","COPY",BODY,{"derivedFrom":makeQuery(id+"F2.opPattern","COPY",BODY,{"derivedFrom":makeQuery(id+"F1.opExtrude","SWEPT_BODY",BODY,{"disambiguationData":[OSD([sQuery(id+"F0.wireOp",EDGE,"E1.bottom"),sQuery(id+"F0.wireOp",EDGE,"E1.top"),sQuery(id+"F0.wireOp",EDGE,"E1.left"),sQuery(id+"F0.wireOp",EDGE,"E1.right")])]}),"instanceName":"1"}),"instanceName":"1"}),"instanceName":"1"}),"instanceName":"1"});
            var Q89;
            Q89=makeQuery(id+"F9.opPattern","COPY",BODY,{"derivedFrom":makeQuery(id+"F7.opPattern","COPY",BODY,{"derivedFrom":makeQuery(id+"F3.opPattern","COPY",BODY,{"derivedFrom":makeQuery(id+"F2.opPattern","COPY",BODY,{"derivedFrom":makeQuery(id+"F1.opExtrude","SWEPT_BODY",BODY,{"disambiguationData":[OSD([sQuery(id+"F0.wireOp",EDGE,"E2.bottom"),sQuery(id+"F0.wireOp",EDGE,"E2.top"),sQuery(id+"F0.wireOp",EDGE,"E2.left"),sQuery(id+"F0.wireOp",EDGE,"E2.right")])]}),"instanceName":"1"}),"instanceName":"1"}),"instanceName":"1"}),"instanceName":"1"});
            var Q90;
            Q90=makeQuery(id+"F9.opPattern","COPY",BODY,{"derivedFrom":makeQuery(id+"F7.opPattern","COPY",BODY,{"derivedFrom":makeQuery(id+"F4.opPattern","COPY",BODY,{"derivedFrom":makeQuery(id+"F3.opPattern","COPY",BODY,{"derivedFrom":makeQuery(id+"F2.opPattern","COPY",BODY,{"derivedFrom":makeQuery(id+"F1.opExtrude","SWEPT_BODY",BODY,{"disambiguationData":[OSD([sQuery(id+"F0.wireOp",EDGE,"E0.bottom"),sQuery(id+"F0.wireOp",EDGE,"E0.top"),sQuery(id+"F0.wireOp",EDGE,"E0.left"),sQuery(id+"F0.wireOp",EDGE,"E0.right")])]}),"instanceName":"1"}),"instanceName":"1"}),"instanceName":"1"}),"instanceName":"1"}),"instanceName":"1"});
            var Q91;
            Q91=makeQuery(id+"F9.opPattern","COPY",BODY,{"derivedFrom":makeQuery(id+"F7.opPattern","COPY",BODY,{"derivedFrom":makeQuery(id+"F4.opPattern","COPY",BODY,{"derivedFrom":makeQuery(id+"F3.opPattern","COPY",BODY,{"derivedFrom":makeQuery(id+"F2.opPattern","COPY",BODY,{"derivedFrom":makeQuery(id+"F1.opExtrude","SWEPT_BODY",BODY,{"disambiguationData":[OSD([sQuery(id+"F0.wireOp",EDGE,"E1.bottom"),sQuery(id+"F0.wireOp",EDGE,"E1.top"),sQuery(id+"F0.wireOp",EDGE,"E1.left"),sQuery(id+"F0.wireOp",EDGE,"E1.right")])]}),"instanceName":"1"}),"instanceName":"1"}),"instanceName":"1"}),"instanceName":"1"}),"instanceName":"1"});
            var Q92;
            Q92=makeQuery(id+"F9.opPattern","COPY",BODY,{"derivedFrom":makeQuery(id+"F7.opPattern","COPY",BODY,{"derivedFrom":makeQuery(id+"F4.opPattern","COPY",BODY,{"derivedFrom":makeQuery(id+"F3.opPattern","COPY",BODY,{"derivedFrom":makeQuery(id+"F2.opPattern","COPY",BODY,{"derivedFrom":makeQuery(id+"F1.opExtrude","SWEPT_BODY",BODY,{"disambiguationData":[OSD([sQuery(id+"F0.wireOp",EDGE,"E2.bottom"),sQuery(id+"F0.wireOp",EDGE,"E2.top"),sQuery(id+"F0.wireOp",EDGE,"E2.left"),sQuery(id+"F0.wireOp",EDGE,"E2.right")])]}),"instanceName":"1"}),"instanceName":"1"}),"instanceName":"1"}),"instanceName":"1"}),"instanceName":"1"});
            var Q93;
            Q93=makeQuery(id+"F9.opPattern","COPY",BODY,{"derivedFrom":makeQuery(id+"F7.opPattern","COPY",BODY,{"derivedFrom":makeQuery(id+"F5.opPattern","COPY",BODY,{"derivedFrom":makeQuery(id+"F4.opPattern","COPY",BODY,{"derivedFrom":makeQuery(id+"F3.opPattern","COPY",BODY,{"derivedFrom":makeQuery(id+"F2.opPattern","COPY",BODY,{"derivedFrom":makeQuery(id+"F1.opExtrude","SWEPT_BODY",BODY,{"disambiguationData":[OSD([sQuery(id+"F0.wireOp",EDGE,"E0.bottom"),sQuery(id+"F0.wireOp",EDGE,"E0.top"),sQuery(id+"F0.wireOp",EDGE,"E0.left"),sQuery(id+"F0.wireOp",EDGE,"E0.right")])]}),"instanceName":"1"}),"instanceName":"1"}),"instanceName":"1"}),"instanceName":"1"}),"instanceName":"1"}),"instanceName":"1"});
            var Q94;
            Q94=makeQuery(id+"F9.opPattern","COPY",BODY,{"derivedFrom":makeQuery(id+"F7.opPattern","COPY",BODY,{"derivedFrom":makeQuery(id+"F5.opPattern","COPY",BODY,{"derivedFrom":makeQuery(id+"F4.opPattern","COPY",BODY,{"derivedFrom":makeQuery(id+"F3.opPattern","COPY",BODY,{"derivedFrom":makeQuery(id+"F2.opPattern","COPY",BODY,{"derivedFrom":makeQuery(id+"F1.opExtrude","SWEPT_BODY",BODY,{"disambiguationData":[OSD([sQuery(id+"F0.wireOp",EDGE,"E1.bottom"),sQuery(id+"F0.wireOp",EDGE,"E1.top"),sQuery(id+"F0.wireOp",EDGE,"E1.left"),sQuery(id+"F0.wireOp",EDGE,"E1.right")])]}),"instanceName":"1"}),"instanceName":"1"}),"instanceName":"1"}),"instanceName":"1"}),"instanceName":"1"}),"instanceName":"1"});
            var Q95;
            Q95=makeQuery(id+"F9.opPattern","COPY",BODY,{"derivedFrom":makeQuery(id+"F7.opPattern","COPY",BODY,{"derivedFrom":makeQuery(id+"F5.opPattern","COPY",BODY,{"derivedFrom":makeQuery(id+"F4.opPattern","COPY",BODY,{"derivedFrom":makeQuery(id+"F3.opPattern","COPY",BODY,{"derivedFrom":makeQuery(id+"F2.opPattern","COPY",BODY,{"derivedFrom":makeQuery(id+"F1.opExtrude","SWEPT_BODY",BODY,{"disambiguationData":[OSD([sQuery(id+"F0.wireOp",EDGE,"E2.bottom"),sQuery(id+"F0.wireOp",EDGE,"E2.top"),sQuery(id+"F0.wireOp",EDGE,"E2.left"),sQuery(id+"F0.wireOp",EDGE,"E2.right")])]}),"instanceName":"1"}),"instanceName":"1"}),"instanceName":"1"}),"instanceName":"1"}),"instanceName":"1"}),"instanceName":"1"});
            var Q96;
            Q96=makeQuery(id+"F9.opPattern","COPY",BODY,{"derivedFrom":makeQuery(id+"F7.opPattern","COPY",BODY,{"derivedFrom":makeQuery(id+"F6.opPattern","COPY",BODY,{"derivedFrom":makeQuery(id+"F5.opPattern","COPY",BODY,{"derivedFrom":makeQuery(id+"F4.opPattern","COPY",BODY,{"derivedFrom":makeQuery(id+"F3.opPattern","COPY",BODY,{"derivedFrom":makeQuery(id+"F2.opPattern","COPY",BODY,{"derivedFrom":makeQuery(id+"F1.opExtrude","SWEPT_BODY",BODY,{"disambiguationData":[OSD([sQuery(id+"F0.wireOp",EDGE,"E0.bottom"),sQuery(id+"F0.wireOp",EDGE,"E0.top"),sQuery(id+"F0.wireOp",EDGE,"E0.left"),sQuery(id+"F0.wireOp",EDGE,"E0.right")])]}),"instanceName":"1"}),"instanceName":"1"}),"instanceName":"1"}),"instanceName":"1"}),"instanceName":"1"}),"instanceName":"1"}),"instanceName":"1"});
            var Q97;
            Q97=makeQuery(id+"F9.opPattern","COPY",BODY,{"derivedFrom":makeQuery(id+"F7.opPattern","COPY",BODY,{"derivedFrom":makeQuery(id+"F6.opPattern","COPY",BODY,{"derivedFrom":makeQuery(id+"F5.opPattern","COPY",BODY,{"derivedFrom":makeQuery(id+"F4.opPattern","COPY",BODY,{"derivedFrom":makeQuery(id+"F3.opPattern","COPY",BODY,{"derivedFrom":makeQuery(id+"F2.opPattern","COPY",BODY,{"derivedFrom":makeQuery(id+"F1.opExtrude","SWEPT_BODY",BODY,{"disambiguationData":[OSD([sQuery(id+"F0.wireOp",EDGE,"E1.bottom"),sQuery(id+"F0.wireOp",EDGE,"E1.top"),sQuery(id+"F0.wireOp",EDGE,"E1.left"),sQuery(id+"F0.wireOp",EDGE,"E1.right")])]}),"instanceName":"1"}),"instanceName":"1"}),"instanceName":"1"}),"instanceName":"1"}),"instanceName":"1"}),"instanceName":"1"}),"instanceName":"1"});
            var Q98;
            Q98=makeQuery(id+"F9.opPattern","COPY",BODY,{"derivedFrom":makeQuery(id+"F7.opPattern","COPY",BODY,{"derivedFrom":makeQuery(id+"F6.opPattern","COPY",BODY,{"derivedFrom":makeQuery(id+"F5.opPattern","COPY",BODY,{"derivedFrom":makeQuery(id+"F4.opPattern","COPY",BODY,{"derivedFrom":makeQuery(id+"F3.opPattern","COPY",BODY,{"derivedFrom":makeQuery(id+"F2.opPattern","COPY",BODY,{"derivedFrom":makeQuery(id+"F1.opExtrude","SWEPT_BODY",BODY,{"disambiguationData":[OSD([sQuery(id+"F0.wireOp",EDGE,"E2.bottom"),sQuery(id+"F0.wireOp",EDGE,"E2.top"),sQuery(id+"F0.wireOp",EDGE,"E2.left"),sQuery(id+"F0.wireOp",EDGE,"E2.right")])]}),"instanceName":"1"}),"instanceName":"1"}),"instanceName":"1"}),"instanceName":"1"}),"instanceName":"1"}),"instanceName":"1"}),"instanceName":"1"});
            var Q99;
            Q99=makeQuery(id+"F9.opPattern","COPY",BODY,{"derivedFrom":makeQuery(id+"F8.opPattern","COPY",BODY,{"derivedFrom":makeQuery(id+"F1.opExtrude","SWEPT_BODY",BODY,{"disambiguationData":[OSD([sQuery(id+"F0.wireOp",EDGE,"E0.bottom"),sQuery(id+"F0.wireOp",EDGE,"E0.top"),sQuery(id+"F0.wireOp",EDGE,"E0.left"),sQuery(id+"F0.wireOp",EDGE,"E0.right")])]}),"instanceName":"1"}),"instanceName":"1"});
            var Q100;
            Q100=makeQuery(id+"F9.opPattern","COPY",BODY,{"derivedFrom":makeQuery(id+"F8.opPattern","COPY",BODY,{"derivedFrom":makeQuery(id+"F1.opExtrude","SWEPT_BODY",BODY,{"disambiguationData":[OSD([sQuery(id+"F0.wireOp",EDGE,"E1.bottom"),sQuery(id+"F0.wireOp",EDGE,"E1.top"),sQuery(id+"F0.wireOp",EDGE,"E1.left"),sQuery(id+"F0.wireOp",EDGE,"E1.right")])]}),"instanceName":"1"}),"instanceName":"1"});
            var Q101;
            Q101=makeQuery(id+"F9.opPattern","COPY",BODY,{"derivedFrom":makeQuery(id+"F8.opPattern","COPY",BODY,{"derivedFrom":makeQuery(id+"F1.opExtrude","SWEPT_BODY",BODY,{"disambiguationData":[OSD([sQuery(id+"F0.wireOp",EDGE,"E2.bottom"),sQuery(id+"F0.wireOp",EDGE,"E2.top"),sQuery(id+"F0.wireOp",EDGE,"E2.left"),sQuery(id+"F0.wireOp",EDGE,"E2.right")])]}),"instanceName":"1"}),"instanceName":"1"});
            var Q102;
            Q102=makeQuery(id+"F9.opPattern","COPY",BODY,{"derivedFrom":makeQuery(id+"F8.opPattern","COPY",BODY,{"derivedFrom":makeQuery(id+"F2.opPattern","COPY",BODY,{"derivedFrom":makeQuery(id+"F1.opExtrude","SWEPT_BODY",BODY,{"disambiguationData":[OSD([sQuery(id+"F0.wireOp",EDGE,"E0.bottom"),sQuery(id+"F0.wireOp",EDGE,"E0.top"),sQuery(id+"F0.wireOp",EDGE,"E0.left"),sQuery(id+"F0.wireOp",EDGE,"E0.right")])]}),"instanceName":"1"}),"instanceName":"1"}),"instanceName":"1"});
            var Q103;
            Q103=makeQuery(id+"F9.opPattern","COPY",BODY,{"derivedFrom":makeQuery(id+"F8.opPattern","COPY",BODY,{"derivedFrom":makeQuery(id+"F2.opPattern","COPY",BODY,{"derivedFrom":makeQuery(id+"F1.opExtrude","SWEPT_BODY",BODY,{"disambiguationData":[OSD([sQuery(id+"F0.wireOp",EDGE,"E1.bottom"),sQuery(id+"F0.wireOp",EDGE,"E1.top"),sQuery(id+"F0.wireOp",EDGE,"E1.left"),sQuery(id+"F0.wireOp",EDGE,"E1.right")])]}),"instanceName":"1"}),"instanceName":"1"}),"instanceName":"1"});
            var Q104;
            Q104=makeQuery(id+"F9.opPattern","COPY",BODY,{"derivedFrom":makeQuery(id+"F8.opPattern","COPY",BODY,{"derivedFrom":makeQuery(id+"F2.opPattern","COPY",BODY,{"derivedFrom":makeQuery(id+"F1.opExtrude","SWEPT_BODY",BODY,{"disambiguationData":[OSD([sQuery(id+"F0.wireOp",EDGE,"E2.bottom"),sQuery(id+"F0.wireOp",EDGE,"E2.top"),sQuery(id+"F0.wireOp",EDGE,"E2.left"),sQuery(id+"F0.wireOp",EDGE,"E2.right")])]}),"instanceName":"1"}),"instanceName":"1"}),"instanceName":"1"});
            var Q105;
            Q105=makeQuery(id+"F9.opPattern","COPY",BODY,{"derivedFrom":makeQuery(id+"F8.opPattern","COPY",BODY,{"derivedFrom":makeQuery(id+"F3.opPattern","COPY",BODY,{"derivedFrom":makeQuery(id+"F2.opPattern","COPY",BODY,{"derivedFrom":makeQuery(id+"F1.opExtrude","SWEPT_BODY",BODY,{"disambiguationData":[OSD([sQuery(id+"F0.wireOp",EDGE,"E0.bottom"),sQuery(id+"F0.wireOp",EDGE,"E0.top"),sQuery(id+"F0.wireOp",EDGE,"E0.left"),sQuery(id+"F0.wireOp",EDGE,"E0.right")])]}),"instanceName":"1"}),"instanceName":"1"}),"instanceName":"1"}),"instanceName":"1"});
            var Q106;
            Q106=makeQuery(id+"F9.opPattern","COPY",BODY,{"derivedFrom":makeQuery(id+"F8.opPattern","COPY",BODY,{"derivedFrom":makeQuery(id+"F3.opPattern","COPY",BODY,{"derivedFrom":makeQuery(id+"F2.opPattern","COPY",BODY,{"derivedFrom":makeQuery(id+"F1.opExtrude","SWEPT_BODY",BODY,{"disambiguationData":[OSD([sQuery(id+"F0.wireOp",EDGE,"E1.bottom"),sQuery(id+"F0.wireOp",EDGE,"E1.top"),sQuery(id+"F0.wireOp",EDGE,"E1.left"),sQuery(id+"F0.wireOp",EDGE,"E1.right")])]}),"instanceName":"1"}),"instanceName":"1"}),"instanceName":"1"}),"instanceName":"1"});
            var Q107;
            Q107=makeQuery(id+"F9.opPattern","COPY",BODY,{"derivedFrom":makeQuery(id+"F8.opPattern","COPY",BODY,{"derivedFrom":makeQuery(id+"F3.opPattern","COPY",BODY,{"derivedFrom":makeQuery(id+"F2.opPattern","COPY",BODY,{"derivedFrom":makeQuery(id+"F1.opExtrude","SWEPT_BODY",BODY,{"disambiguationData":[OSD([sQuery(id+"F0.wireOp",EDGE,"E2.bottom"),sQuery(id+"F0.wireOp",EDGE,"E2.top"),sQuery(id+"F0.wireOp",EDGE,"E2.left"),sQuery(id+"F0.wireOp",EDGE,"E2.right")])]}),"instanceName":"1"}),"instanceName":"1"}),"instanceName":"1"}),"instanceName":"1"});
            var Q108;
            Q108=makeQuery(id+"F9.opPattern","COPY",BODY,{"derivedFrom":makeQuery(id+"F8.opPattern","COPY",BODY,{"derivedFrom":makeQuery(id+"F4.opPattern","COPY",BODY,{"derivedFrom":makeQuery(id+"F3.opPattern","COPY",BODY,{"derivedFrom":makeQuery(id+"F2.opPattern","COPY",BODY,{"derivedFrom":makeQuery(id+"F1.opExtrude","SWEPT_BODY",BODY,{"disambiguationData":[OSD([sQuery(id+"F0.wireOp",EDGE,"E0.bottom"),sQuery(id+"F0.wireOp",EDGE,"E0.top"),sQuery(id+"F0.wireOp",EDGE,"E0.left"),sQuery(id+"F0.wireOp",EDGE,"E0.right")])]}),"instanceName":"1"}),"instanceName":"1"}),"instanceName":"1"}),"instanceName":"1"}),"instanceName":"1"});
            var Q109;
            Q109=makeQuery(id+"F9.opPattern","COPY",BODY,{"derivedFrom":makeQuery(id+"F8.opPattern","COPY",BODY,{"derivedFrom":makeQuery(id+"F4.opPattern","COPY",BODY,{"derivedFrom":makeQuery(id+"F3.opPattern","COPY",BODY,{"derivedFrom":makeQuery(id+"F2.opPattern","COPY",BODY,{"derivedFrom":makeQuery(id+"F1.opExtrude","SWEPT_BODY",BODY,{"disambiguationData":[OSD([sQuery(id+"F0.wireOp",EDGE,"E1.bottom"),sQuery(id+"F0.wireOp",EDGE,"E1.top"),sQuery(id+"F0.wireOp",EDGE,"E1.left"),sQuery(id+"F0.wireOp",EDGE,"E1.right")])]}),"instanceName":"1"}),"instanceName":"1"}),"instanceName":"1"}),"instanceName":"1"}),"instanceName":"1"});
            var Q110;
            Q110=makeQuery(id+"F9.opPattern","COPY",BODY,{"derivedFrom":makeQuery(id+"F8.opPattern","COPY",BODY,{"derivedFrom":makeQuery(id+"F4.opPattern","COPY",BODY,{"derivedFrom":makeQuery(id+"F3.opPattern","COPY",BODY,{"derivedFrom":makeQuery(id+"F2.opPattern","COPY",BODY,{"derivedFrom":makeQuery(id+"F1.opExtrude","SWEPT_BODY",BODY,{"disambiguationData":[OSD([sQuery(id+"F0.wireOp",EDGE,"E2.bottom"),sQuery(id+"F0.wireOp",EDGE,"E2.top"),sQuery(id+"F0.wireOp",EDGE,"E2.left"),sQuery(id+"F0.wireOp",EDGE,"E2.right")])]}),"instanceName":"1"}),"instanceName":"1"}),"instanceName":"1"}),"instanceName":"1"}),"instanceName":"1"});
            var Q111;
            Q111=makeQuery(id+"F9.opPattern","COPY",BODY,{"derivedFrom":makeQuery(id+"F8.opPattern","COPY",BODY,{"derivedFrom":makeQuery(id+"F5.opPattern","COPY",BODY,{"derivedFrom":makeQuery(id+"F4.opPattern","COPY",BODY,{"derivedFrom":makeQuery(id+"F3.opPattern","COPY",BODY,{"derivedFrom":makeQuery(id+"F2.opPattern","COPY",BODY,{"derivedFrom":makeQuery(id+"F1.opExtrude","SWEPT_BODY",BODY,{"disambiguationData":[OSD([sQuery(id+"F0.wireOp",EDGE,"E0.bottom"),sQuery(id+"F0.wireOp",EDGE,"E0.top"),sQuery(id+"F0.wireOp",EDGE,"E0.left"),sQuery(id+"F0.wireOp",EDGE,"E0.right")])]}),"instanceName":"1"}),"instanceName":"1"}),"instanceName":"1"}),"instanceName":"1"}),"instanceName":"1"}),"instanceName":"1"});
            var Q112;
            Q112=makeQuery(id+"F9.opPattern","COPY",BODY,{"derivedFrom":makeQuery(id+"F8.opPattern","COPY",BODY,{"derivedFrom":makeQuery(id+"F5.opPattern","COPY",BODY,{"derivedFrom":makeQuery(id+"F4.opPattern","COPY",BODY,{"derivedFrom":makeQuery(id+"F3.opPattern","COPY",BODY,{"derivedFrom":makeQuery(id+"F2.opPattern","COPY",BODY,{"derivedFrom":makeQuery(id+"F1.opExtrude","SWEPT_BODY",BODY,{"disambiguationData":[OSD([sQuery(id+"F0.wireOp",EDGE,"E1.bottom"),sQuery(id+"F0.wireOp",EDGE,"E1.top"),sQuery(id+"F0.wireOp",EDGE,"E1.left"),sQuery(id+"F0.wireOp",EDGE,"E1.right")])]}),"instanceName":"1"}),"instanceName":"1"}),"instanceName":"1"}),"instanceName":"1"}),"instanceName":"1"}),"instanceName":"1"});
            var Q113;
            Q113=makeQuery(id+"F9.opPattern","COPY",BODY,{"derivedFrom":makeQuery(id+"F8.opPattern","COPY",BODY,{"derivedFrom":makeQuery(id+"F5.opPattern","COPY",BODY,{"derivedFrom":makeQuery(id+"F4.opPattern","COPY",BODY,{"derivedFrom":makeQuery(id+"F3.opPattern","COPY",BODY,{"derivedFrom":makeQuery(id+"F2.opPattern","COPY",BODY,{"derivedFrom":makeQuery(id+"F1.opExtrude","SWEPT_BODY",BODY,{"disambiguationData":[OSD([sQuery(id+"F0.wireOp",EDGE,"E2.bottom"),sQuery(id+"F0.wireOp",EDGE,"E2.top"),sQuery(id+"F0.wireOp",EDGE,"E2.left"),sQuery(id+"F0.wireOp",EDGE,"E2.right")])]}),"instanceName":"1"}),"instanceName":"1"}),"instanceName":"1"}),"instanceName":"1"}),"instanceName":"1"}),"instanceName":"1"});
            var Q114;
            Q114=makeQuery(id+"F9.opPattern","COPY",BODY,{"derivedFrom":makeQuery(id+"F8.opPattern","COPY",BODY,{"derivedFrom":makeQuery(id+"F6.opPattern","COPY",BODY,{"derivedFrom":makeQuery(id+"F5.opPattern","COPY",BODY,{"derivedFrom":makeQuery(id+"F4.opPattern","COPY",BODY,{"derivedFrom":makeQuery(id+"F3.opPattern","COPY",BODY,{"derivedFrom":makeQuery(id+"F2.opPattern","COPY",BODY,{"derivedFrom":makeQuery(id+"F1.opExtrude","SWEPT_BODY",BODY,{"disambiguationData":[OSD([sQuery(id+"F0.wireOp",EDGE,"E0.bottom"),sQuery(id+"F0.wireOp",EDGE,"E0.top"),sQuery(id+"F0.wireOp",EDGE,"E0.left"),sQuery(id+"F0.wireOp",EDGE,"E0.right")])]}),"instanceName":"1"}),"instanceName":"1"}),"instanceName":"1"}),"instanceName":"1"}),"instanceName":"1"}),"instanceName":"1"}),"instanceName":"1"});
            var Q115;
            Q115=makeQuery(id+"F9.opPattern","COPY",BODY,{"derivedFrom":makeQuery(id+"F8.opPattern","COPY",BODY,{"derivedFrom":makeQuery(id+"F6.opPattern","COPY",BODY,{"derivedFrom":makeQuery(id+"F5.opPattern","COPY",BODY,{"derivedFrom":makeQuery(id+"F4.opPattern","COPY",BODY,{"derivedFrom":makeQuery(id+"F3.opPattern","COPY",BODY,{"derivedFrom":makeQuery(id+"F2.opPattern","COPY",BODY,{"derivedFrom":makeQuery(id+"F1.opExtrude","SWEPT_BODY",BODY,{"disambiguationData":[OSD([sQuery(id+"F0.wireOp",EDGE,"E1.bottom"),sQuery(id+"F0.wireOp",EDGE,"E1.top"),sQuery(id+"F0.wireOp",EDGE,"E1.left"),sQuery(id+"F0.wireOp",EDGE,"E1.right")])]}),"instanceName":"1"}),"instanceName":"1"}),"instanceName":"1"}),"instanceName":"1"}),"instanceName":"1"}),"instanceName":"1"}),"instanceName":"1"});
            var Q116;
            Q116=makeQuery(id+"F9.opPattern","COPY",BODY,{"derivedFrom":makeQuery(id+"F8.opPattern","COPY",BODY,{"derivedFrom":makeQuery(id+"F6.opPattern","COPY",BODY,{"derivedFrom":makeQuery(id+"F5.opPattern","COPY",BODY,{"derivedFrom":makeQuery(id+"F4.opPattern","COPY",BODY,{"derivedFrom":makeQuery(id+"F3.opPattern","COPY",BODY,{"derivedFrom":makeQuery(id+"F2.opPattern","COPY",BODY,{"derivedFrom":makeQuery(id+"F1.opExtrude","SWEPT_BODY",BODY,{"disambiguationData":[OSD([sQuery(id+"F0.wireOp",EDGE,"E2.bottom"),sQuery(id+"F0.wireOp",EDGE,"E2.top"),sQuery(id+"F0.wireOp",EDGE,"E2.left"),sQuery(id+"F0.wireOp",EDGE,"E2.right")])]}),"instanceName":"1"}),"instanceName":"1"}),"instanceName":"1"}),"instanceName":"1"}),"instanceName":"1"}),"instanceName":"1"}),"instanceName":"1"});
            var Q117;
            Q117=makeQuery(id+"F9.opPattern","COPY",BODY,{"derivedFrom":makeQuery(id+"F8.opPattern","COPY",BODY,{"derivedFrom":makeQuery(id+"F7.opPattern","COPY",BODY,{"derivedFrom":makeQuery(id+"F1.opExtrude","SWEPT_BODY",BODY,{"disambiguationData":[OSD([sQuery(id+"F0.wireOp",EDGE,"E0.bottom"),sQuery(id+"F0.wireOp",EDGE,"E0.top"),sQuery(id+"F0.wireOp",EDGE,"E0.left"),sQuery(id+"F0.wireOp",EDGE,"E0.right")])]}),"instanceName":"1"}),"instanceName":"1"}),"instanceName":"1"});
            var Q118;
            Q118=makeQuery(id+"F9.opPattern","COPY",BODY,{"derivedFrom":makeQuery(id+"F8.opPattern","COPY",BODY,{"derivedFrom":makeQuery(id+"F7.opPattern","COPY",BODY,{"derivedFrom":makeQuery(id+"F1.opExtrude","SWEPT_BODY",BODY,{"disambiguationData":[OSD([sQuery(id+"F0.wireOp",EDGE,"E1.bottom"),sQuery(id+"F0.wireOp",EDGE,"E1.top"),sQuery(id+"F0.wireOp",EDGE,"E1.left"),sQuery(id+"F0.wireOp",EDGE,"E1.right")])]}),"instanceName":"1"}),"instanceName":"1"}),"instanceName":"1"});
            var Q119;
            Q119=makeQuery(id+"F9.opPattern","COPY",BODY,{"derivedFrom":makeQuery(id+"F8.opPattern","COPY",BODY,{"derivedFrom":makeQuery(id+"F7.opPattern","COPY",BODY,{"derivedFrom":makeQuery(id+"F1.opExtrude","SWEPT_BODY",BODY,{"disambiguationData":[OSD([sQuery(id+"F0.wireOp",EDGE,"E2.bottom"),sQuery(id+"F0.wireOp",EDGE,"E2.top"),sQuery(id+"F0.wireOp",EDGE,"E2.left"),sQuery(id+"F0.wireOp",EDGE,"E2.right")])]}),"instanceName":"1"}),"instanceName":"1"}),"instanceName":"1"});
            var Q120;
            Q120=makeQuery(id+"F9.opPattern","COPY",BODY,{"derivedFrom":makeQuery(id+"F8.opPattern","COPY",BODY,{"derivedFrom":makeQuery(id+"F7.opPattern","COPY",BODY,{"derivedFrom":makeQuery(id+"F2.opPattern","COPY",BODY,{"derivedFrom":makeQuery(id+"F1.opExtrude","SWEPT_BODY",BODY,{"disambiguationData":[OSD([sQuery(id+"F0.wireOp",EDGE,"E0.bottom"),sQuery(id+"F0.wireOp",EDGE,"E0.top"),sQuery(id+"F0.wireOp",EDGE,"E0.left"),sQuery(id+"F0.wireOp",EDGE,"E0.right")])]}),"instanceName":"1"}),"instanceName":"1"}),"instanceName":"1"}),"instanceName":"1"});
            var Q121;
            Q121=makeQuery(id+"F9.opPattern","COPY",BODY,{"derivedFrom":makeQuery(id+"F8.opPattern","COPY",BODY,{"derivedFrom":makeQuery(id+"F7.opPattern","COPY",BODY,{"derivedFrom":makeQuery(id+"F2.opPattern","COPY",BODY,{"derivedFrom":makeQuery(id+"F1.opExtrude","SWEPT_BODY",BODY,{"disambiguationData":[OSD([sQuery(id+"F0.wireOp",EDGE,"E1.bottom"),sQuery(id+"F0.wireOp",EDGE,"E1.top"),sQuery(id+"F0.wireOp",EDGE,"E1.left"),sQuery(id+"F0.wireOp",EDGE,"E1.right")])]}),"instanceName":"1"}),"instanceName":"1"}),"instanceName":"1"}),"instanceName":"1"});
            var Q122;
            Q122=makeQuery(id+"F9.opPattern","COPY",BODY,{"derivedFrom":makeQuery(id+"F8.opPattern","COPY",BODY,{"derivedFrom":makeQuery(id+"F7.opPattern","COPY",BODY,{"derivedFrom":makeQuery(id+"F2.opPattern","COPY",BODY,{"derivedFrom":makeQuery(id+"F1.opExtrude","SWEPT_BODY",BODY,{"disambiguationData":[OSD([sQuery(id+"F0.wireOp",EDGE,"E2.bottom"),sQuery(id+"F0.wireOp",EDGE,"E2.top"),sQuery(id+"F0.wireOp",EDGE,"E2.left"),sQuery(id+"F0.wireOp",EDGE,"E2.right")])]}),"instanceName":"1"}),"instanceName":"1"}),"instanceName":"1"}),"instanceName":"1"});
            var Q123;
            Q123=makeQuery(id+"F9.opPattern","COPY",BODY,{"derivedFrom":makeQuery(id+"F8.opPattern","COPY",BODY,{"derivedFrom":makeQuery(id+"F7.opPattern","COPY",BODY,{"derivedFrom":makeQuery(id+"F3.opPattern","COPY",BODY,{"derivedFrom":makeQuery(id+"F2.opPattern","COPY",BODY,{"derivedFrom":makeQuery(id+"F1.opExtrude","SWEPT_BODY",BODY,{"disambiguationData":[OSD([sQuery(id+"F0.wireOp",EDGE,"E0.bottom"),sQuery(id+"F0.wireOp",EDGE,"E0.top"),sQuery(id+"F0.wireOp",EDGE,"E0.left"),sQuery(id+"F0.wireOp",EDGE,"E0.right")])]}),"instanceName":"1"}),"instanceName":"1"}),"instanceName":"1"}),"instanceName":"1"}),"instanceName":"1"});
            var Q124;
            Q124=makeQuery(id+"F9.opPattern","COPY",BODY,{"derivedFrom":makeQuery(id+"F8.opPattern","COPY",BODY,{"derivedFrom":makeQuery(id+"F7.opPattern","COPY",BODY,{"derivedFrom":makeQuery(id+"F3.opPattern","COPY",BODY,{"derivedFrom":makeQuery(id+"F2.opPattern","COPY",BODY,{"derivedFrom":makeQuery(id+"F1.opExtrude","SWEPT_BODY",BODY,{"disambiguationData":[OSD([sQuery(id+"F0.wireOp",EDGE,"E1.bottom"),sQuery(id+"F0.wireOp",EDGE,"E1.top"),sQuery(id+"F0.wireOp",EDGE,"E1.left"),sQuery(id+"F0.wireOp",EDGE,"E1.right")])]}),"instanceName":"1"}),"instanceName":"1"}),"instanceName":"1"}),"instanceName":"1"}),"instanceName":"1"});
            var Q125;
            Q125=makeQuery(id+"F9.opPattern","COPY",BODY,{"derivedFrom":makeQuery(id+"F8.opPattern","COPY",BODY,{"derivedFrom":makeQuery(id+"F7.opPattern","COPY",BODY,{"derivedFrom":makeQuery(id+"F3.opPattern","COPY",BODY,{"derivedFrom":makeQuery(id+"F2.opPattern","COPY",BODY,{"derivedFrom":makeQuery(id+"F1.opExtrude","SWEPT_BODY",BODY,{"disambiguationData":[OSD([sQuery(id+"F0.wireOp",EDGE,"E2.bottom"),sQuery(id+"F0.wireOp",EDGE,"E2.top"),sQuery(id+"F0.wireOp",EDGE,"E2.left"),sQuery(id+"F0.wireOp",EDGE,"E2.right")])]}),"instanceName":"1"}),"instanceName":"1"}),"instanceName":"1"}),"instanceName":"1"}),"instanceName":"1"});
            var Q126;
            Q126=makeQuery(id+"F9.opPattern","COPY",BODY,{"derivedFrom":makeQuery(id+"F8.opPattern","COPY",BODY,{"derivedFrom":makeQuery(id+"F7.opPattern","COPY",BODY,{"derivedFrom":makeQuery(id+"F4.opPattern","COPY",BODY,{"derivedFrom":makeQuery(id+"F3.opPattern","COPY",BODY,{"derivedFrom":makeQuery(id+"F2.opPattern","COPY",BODY,{"derivedFrom":makeQuery(id+"F1.opExtrude","SWEPT_BODY",BODY,{"disambiguationData":[OSD([sQuery(id+"F0.wireOp",EDGE,"E0.bottom"),sQuery(id+"F0.wireOp",EDGE,"E0.top"),sQuery(id+"F0.wireOp",EDGE,"E0.left"),sQuery(id+"F0.wireOp",EDGE,"E0.right")])]}),"instanceName":"1"}),"instanceName":"1"}),"instanceName":"1"}),"instanceName":"1"}),"instanceName":"1"}),"instanceName":"1"});
            var Q127;
            Q127=makeQuery(id+"F9.opPattern","COPY",BODY,{"derivedFrom":makeQuery(id+"F8.opPattern","COPY",BODY,{"derivedFrom":makeQuery(id+"F7.opPattern","COPY",BODY,{"derivedFrom":makeQuery(id+"F4.opPattern","COPY",BODY,{"derivedFrom":makeQuery(id+"F3.opPattern","COPY",BODY,{"derivedFrom":makeQuery(id+"F2.opPattern","COPY",BODY,{"derivedFrom":makeQuery(id+"F1.opExtrude","SWEPT_BODY",BODY,{"disambiguationData":[OSD([sQuery(id+"F0.wireOp",EDGE,"E1.bottom"),sQuery(id+"F0.wireOp",EDGE,"E1.top"),sQuery(id+"F0.wireOp",EDGE,"E1.left"),sQuery(id+"F0.wireOp",EDGE,"E1.right")])]}),"instanceName":"1"}),"instanceName":"1"}),"instanceName":"1"}),"instanceName":"1"}),"instanceName":"1"}),"instanceName":"1"});
            var Q128;
            Q128=makeQuery(id+"F9.opPattern","COPY",BODY,{"derivedFrom":makeQuery(id+"F8.opPattern","COPY",BODY,{"derivedFrom":makeQuery(id+"F7.opPattern","COPY",BODY,{"derivedFrom":makeQuery(id+"F4.opPattern","COPY",BODY,{"derivedFrom":makeQuery(id+"F3.opPattern","COPY",BODY,{"derivedFrom":makeQuery(id+"F2.opPattern","COPY",BODY,{"derivedFrom":makeQuery(id+"F1.opExtrude","SWEPT_BODY",BODY,{"disambiguationData":[OSD([sQuery(id+"F0.wireOp",EDGE,"E2.bottom"),sQuery(id+"F0.wireOp",EDGE,"E2.top"),sQuery(id+"F0.wireOp",EDGE,"E2.left"),sQuery(id+"F0.wireOp",EDGE,"E2.right")])]}),"instanceName":"1"}),"instanceName":"1"}),"instanceName":"1"}),"instanceName":"1"}),"instanceName":"1"}),"instanceName":"1"});
            var Q129;
            Q129=makeQuery(id+"F9.opPattern","COPY",BODY,{"derivedFrom":makeQuery(id+"F8.opPattern","COPY",BODY,{"derivedFrom":makeQuery(id+"F7.opPattern","COPY",BODY,{"derivedFrom":makeQuery(id+"F5.opPattern","COPY",BODY,{"derivedFrom":makeQuery(id+"F4.opPattern","COPY",BODY,{"derivedFrom":makeQuery(id+"F3.opPattern","COPY",BODY,{"derivedFrom":makeQuery(id+"F2.opPattern","COPY",BODY,{"derivedFrom":makeQuery(id+"F1.opExtrude","SWEPT_BODY",BODY,{"disambiguationData":[OSD([sQuery(id+"F0.wireOp",EDGE,"E0.bottom"),sQuery(id+"F0.wireOp",EDGE,"E0.top"),sQuery(id+"F0.wireOp",EDGE,"E0.left"),sQuery(id+"F0.wireOp",EDGE,"E0.right")])]}),"instanceName":"1"}),"instanceName":"1"}),"instanceName":"1"}),"instanceName":"1"}),"instanceName":"1"}),"instanceName":"1"}),"instanceName":"1"});
            var Q130;
            Q130=makeQuery(id+"F9.opPattern","COPY",BODY,{"derivedFrom":makeQuery(id+"F8.opPattern","COPY",BODY,{"derivedFrom":makeQuery(id+"F7.opPattern","COPY",BODY,{"derivedFrom":makeQuery(id+"F5.opPattern","COPY",BODY,{"derivedFrom":makeQuery(id+"F4.opPattern","COPY",BODY,{"derivedFrom":makeQuery(id+"F3.opPattern","COPY",BODY,{"derivedFrom":makeQuery(id+"F2.opPattern","COPY",BODY,{"derivedFrom":makeQuery(id+"F1.opExtrude","SWEPT_BODY",BODY,{"disambiguationData":[OSD([sQuery(id+"F0.wireOp",EDGE,"E1.bottom"),sQuery(id+"F0.wireOp",EDGE,"E1.top"),sQuery(id+"F0.wireOp",EDGE,"E1.left"),sQuery(id+"F0.wireOp",EDGE,"E1.right")])]}),"instanceName":"1"}),"instanceName":"1"}),"instanceName":"1"}),"instanceName":"1"}),"instanceName":"1"}),"instanceName":"1"}),"instanceName":"1"});
            var Q131;
            Q131=makeQuery(id+"F9.opPattern","COPY",BODY,{"derivedFrom":makeQuery(id+"F8.opPattern","COPY",BODY,{"derivedFrom":makeQuery(id+"F7.opPattern","COPY",BODY,{"derivedFrom":makeQuery(id+"F5.opPattern","COPY",BODY,{"derivedFrom":makeQuery(id+"F4.opPattern","COPY",BODY,{"derivedFrom":makeQuery(id+"F3.opPattern","COPY",BODY,{"derivedFrom":makeQuery(id+"F2.opPattern","COPY",BODY,{"derivedFrom":makeQuery(id+"F1.opExtrude","SWEPT_BODY",BODY,{"disambiguationData":[OSD([sQuery(id+"F0.wireOp",EDGE,"E2.bottom"),sQuery(id+"F0.wireOp",EDGE,"E2.top"),sQuery(id+"F0.wireOp",EDGE,"E2.left"),sQuery(id+"F0.wireOp",EDGE,"E2.right")])]}),"instanceName":"1"}),"instanceName":"1"}),"instanceName":"1"}),"instanceName":"1"}),"instanceName":"1"}),"instanceName":"1"}),"instanceName":"1"});
            var Q132;
            Q132=makeQuery(id+"F9.opPattern","COPY",BODY,{"derivedFrom":makeQuery(id+"F8.opPattern","COPY",BODY,{"derivedFrom":makeQuery(id+"F7.opPattern","COPY",BODY,{"derivedFrom":makeQuery(id+"F6.opPattern","COPY",BODY,{"derivedFrom":makeQuery(id+"F5.opPattern","COPY",BODY,{"derivedFrom":makeQuery(id+"F4.opPattern","COPY",BODY,{"derivedFrom":makeQuery(id+"F3.opPattern","COPY",BODY,{"derivedFrom":makeQuery(id+"F2.opPattern","COPY",BODY,{"derivedFrom":makeQuery(id+"F1.opExtrude","SWEPT_BODY",BODY,{"disambiguationData":[OSD([sQuery(id+"F0.wireOp",EDGE,"E0.bottom"),sQuery(id+"F0.wireOp",EDGE,"E0.top"),sQuery(id+"F0.wireOp",EDGE,"E0.left"),sQuery(id+"F0.wireOp",EDGE,"E0.right")])]}),"instanceName":"1"}),"instanceName":"1"}),"instanceName":"1"}),"instanceName":"1"}),"instanceName":"1"}),"instanceName":"1"}),"instanceName":"1"}),"instanceName":"1"});
            var Q133;
            Q133=makeQuery(id+"F9.opPattern","COPY",BODY,{"derivedFrom":makeQuery(id+"F8.opPattern","COPY",BODY,{"derivedFrom":makeQuery(id+"F7.opPattern","COPY",BODY,{"derivedFrom":makeQuery(id+"F6.opPattern","COPY",BODY,{"derivedFrom":makeQuery(id+"F5.opPattern","COPY",BODY,{"derivedFrom":makeQuery(id+"F4.opPattern","COPY",BODY,{"derivedFrom":makeQuery(id+"F3.opPattern","COPY",BODY,{"derivedFrom":makeQuery(id+"F2.opPattern","COPY",BODY,{"derivedFrom":makeQuery(id+"F1.opExtrude","SWEPT_BODY",BODY,{"disambiguationData":[OSD([sQuery(id+"F0.wireOp",EDGE,"E1.bottom"),sQuery(id+"F0.wireOp",EDGE,"E1.top"),sQuery(id+"F0.wireOp",EDGE,"E1.left"),sQuery(id+"F0.wireOp",EDGE,"E1.right")])]}),"instanceName":"1"}),"instanceName":"1"}),"instanceName":"1"}),"instanceName":"1"}),"instanceName":"1"}),"instanceName":"1"}),"instanceName":"1"}),"instanceName":"1"});
            var Q134;
            Q134=makeQuery(id+"F9.opPattern","COPY",BODY,{"derivedFrom":makeQuery(id+"F8.opPattern","COPY",BODY,{"derivedFrom":makeQuery(id+"F7.opPattern","COPY",BODY,{"derivedFrom":makeQuery(id+"F6.opPattern","COPY",BODY,{"derivedFrom":makeQuery(id+"F5.opPattern","COPY",BODY,{"derivedFrom":makeQuery(id+"F4.opPattern","COPY",BODY,{"derivedFrom":makeQuery(id+"F3.opPattern","COPY",BODY,{"derivedFrom":makeQuery(id+"F2.opPattern","COPY",BODY,{"derivedFrom":makeQuery(id+"F1.opExtrude","SWEPT_BODY",BODY,{"disambiguationData":[OSD([sQuery(id+"F0.wireOp",EDGE,"E2.bottom"),sQuery(id+"F0.wireOp",EDGE,"E2.top"),sQuery(id+"F0.wireOp",EDGE,"E2.left"),sQuery(id+"F0.wireOp",EDGE,"E2.right")])]}),"instanceName":"1"}),"instanceName":"1"}),"instanceName":"1"}),"instanceName":"1"}),"instanceName":"1"}),"instanceName":"1"}),"instanceName":"1"}),"instanceName":"1"});
            var Q135;
            Q135=makeQuery(id+"F8.opPattern","COPY",BODY,{"derivedFrom":makeQuery(id+"F7.opPattern","COPY",BODY,{"derivedFrom":makeQuery(id+"F1.opExtrude","SWEPT_BODY",BODY,{"disambiguationData":[OSD([sQuery(id+"F0.wireOp",EDGE,"E1.bottom"),sQuery(id+"F0.wireOp",EDGE,"E1.top"),sQuery(id+"F0.wireOp",EDGE,"E1.left"),sQuery(id+"F0.wireOp",EDGE,"E1.right")])]}),"instanceName":"1"}),"instanceName":"1"});
            var Q136;
            Q136=makeQuery(id+"F8.opPattern","COPY",BODY,{"derivedFrom":makeQuery(id+"F1.opExtrude","SWEPT_BODY",BODY,{"disambiguationData":[OSD([sQuery(id+"F0.wireOp",EDGE,"E1.bottom"),sQuery(id+"F0.wireOp",EDGE,"E1.top"),sQuery(id+"F0.wireOp",EDGE,"E1.left"),sQuery(id+"F0.wireOp",EDGE,"E1.right")])]}),"instanceName":"1"});
            var Q137;
            Q137=makeQuery(id+"F8.opPattern","COPY",BODY,{"derivedFrom":makeQuery(id+"F1.opExtrude","SWEPT_BODY",BODY,{"disambiguationData":[OSD([sQuery(id+"F0.wireOp",EDGE,"E0.bottom"),sQuery(id+"F0.wireOp",EDGE,"E0.top"),sQuery(id+"F0.wireOp",EDGE,"E0.left"),sQuery(id+"F0.wireOp",EDGE,"E0.right")])]}),"instanceName":"1"});
            var Q138;
            Q138=makeQuery(id+"F7.opPattern","COPY",BODY,{"derivedFrom":makeQuery(id+"F1.opExtrude","SWEPT_BODY",BODY,{"disambiguationData":[OSD([sQuery(id+"F0.wireOp",EDGE,"E2.bottom"),sQuery(id+"F0.wireOp",EDGE,"E2.top"),sQuery(id+"F0.wireOp",EDGE,"E2.left"),sQuery(id+"F0.wireOp",EDGE,"E2.right")])]}),"instanceName":"1"});
            var Q139;
            Q139=makeQuery(id+"F7.opPattern","COPY",BODY,{"derivedFrom":makeQuery(id+"F1.opExtrude","SWEPT_BODY",BODY,{"disambiguationData":[OSD([sQuery(id+"F0.wireOp",EDGE,"E1.bottom"),sQuery(id+"F0.wireOp",EDGE,"E1.top"),sQuery(id+"F0.wireOp",EDGE,"E1.left"),sQuery(id+"F0.wireOp",EDGE,"E1.right")])]}),"instanceName":"1"});
            var Q140;
            Q140=makeQuery(id+"F7.opPattern","COPY",BODY,{"derivedFrom":makeQuery(id+"F1.opExtrude","SWEPT_BODY",BODY,{"disambiguationData":[OSD([sQuery(id+"F0.wireOp",EDGE,"E0.bottom"),sQuery(id+"F0.wireOp",EDGE,"E0.top"),sQuery(id+"F0.wireOp",EDGE,"E0.left"),sQuery(id+"F0.wireOp",EDGE,"E0.right")])]}),"instanceName":"1"});
            var Q141;
            Q141=makeQuery(id+"F1.opExtrude","SWEPT_BODY",BODY,{"disambiguationData":[OSD([sQuery(id+"F0.wireOp",EDGE,"E2.bottom"),sQuery(id+"F0.wireOp",EDGE,"E2.top"),sQuery(id+"F0.wireOp",EDGE,"E2.left"),sQuery(id+"F0.wireOp",EDGE,"E2.right")])]});
            var Q142;
            Q142=makeQuery(id+"F1.opExtrude","SWEPT_BODY",BODY,{"disambiguationData":[OSD([sQuery(id+"F0.wireOp",EDGE,"E1.bottom"),sQuery(id+"F0.wireOp",EDGE,"E1.top"),sQuery(id+"F0.wireOp",EDGE,"E1.left"),sQuery(id+"F0.wireOp",EDGE,"E1.right")])]});
            var Q143;
            Q143=makeQuery(id+"F1.opExtrude","SWEPT_BODY",BODY,{"disambiguationData":[OSD([sQuery(id+"F0.wireOp",EDGE,"E0.bottom"),sQuery(id+"F0.wireOp",EDGE,"E0.top"),sQuery(id+"F0.wireOp",EDGE,"E0.left"),sQuery(id+"F0.wireOp",EDGE,"E0.right")])]});
            transform(context, id + "F10", {"entities" : qUnion([Q0, Q1, Q2, Q3, Q4, Q5, Q6, Q7, Q8, Q9, Q10, Q11, Q12, Q13, Q14, Q15, Q16, Q17, Q18, Q19, Q20, Q21, Q22, Q23, Q24, Q25, Q26, Q27, Q28, Q29, Q30, Q31, Q32, Q33, Q34, Q35, Q36, Q37, Q38, Q39, Q40, Q41, Q42, Q43, Q44, Q45, Q46, Q47, Q48, Q49, Q50, Q51, Q52, Q53, Q54, Q55, Q56, Q57, Q58, Q59, Q60, Q61, Q62, Q63, Q64, Q65, Q66, Q67, Q68, Q69, Q70, Q71, Q72, Q73, Q74, Q75, Q76, Q77, Q78, Q79, Q80, Q81, Q82, Q83, Q84, Q85, Q86, Q87, Q88, Q89, Q90, Q91, Q92, Q93, Q94, Q95, Q96, Q97, Q98, Q99, Q100, Q101, Q102, Q103, Q104, Q105, Q106, Q107, Q108, Q109, Q110, Q111, Q112, Q113, Q114, Q115, Q116, Q117, Q118, Q119, Q120, Q121, Q122, Q123, Q124, Q125, Q126, Q127, Q128, Q129, Q130, Q131, Q132, Q133, Q134, Q135, Q136, Q137, Q138, Q139, Q140, Q141, Q142, Q143]), "transformType" : TransformType.TRANSLATION_3D, "dx" : -1215 * mm, "dy" : 3624 * mm, "dz" : 0 * mm, "makeCopy" : true});
        }
        {
            var Q0;
            Q0=makeQuery(id+"F1.opExtrude","SWEPT_BODY",BODY,{"disambiguationData":[OSD([sQuery(id+"F0.wireOp",EDGE,"E0.bottom"),sQuery(id+"F0.wireOp",EDGE,"E0.top"),sQuery(id+"F0.wireOp",EDGE,"E0.left"),sQuery(id+"F0.wireOp",EDGE,"E0.right")])]});
            var Q1;
            Q1=makeQuery(id+"F1.opExtrude","SWEPT_BODY",BODY,{"disambiguationData":[OSD([sQuery(id+"F0.wireOp",EDGE,"E1.bottom"),sQuery(id+"F0.wireOp",EDGE,"E1.top"),sQuery(id+"F0.wireOp",EDGE,"E1.left"),sQuery(id+"F0.wireOp",EDGE,"E1.right")])]});
            var Q2;
            Q2=makeQuery(id+"F1.opExtrude","SWEPT_BODY",BODY,{"disambiguationData":[OSD([sQuery(id+"F0.wireOp",EDGE,"E2.bottom"),sQuery(id+"F0.wireOp",EDGE,"E2.top"),sQuery(id+"F0.wireOp",EDGE,"E2.left"),sQuery(id+"F0.wireOp",EDGE,"E2.right")])]});
            var Q3;
            Q3=makeQuery(id+"F2.opPattern","COPY",BODY,{"derivedFrom":makeQuery(id+"F1.opExtrude","SWEPT_BODY",BODY,{"disambiguationData":[OSD([sQuery(id+"F0.wireOp",EDGE,"E0.bottom"),sQuery(id+"F0.wireOp",EDGE,"E0.top"),sQuery(id+"F0.wireOp",EDGE,"E0.left"),sQuery(id+"F0.wireOp",EDGE,"E0.right")])]}),"instanceName":"1"});
            var Q4;
            Q4=makeQuery(id+"F2.opPattern","COPY",BODY,{"derivedFrom":makeQuery(id+"F1.opExtrude","SWEPT_BODY",BODY,{"disambiguationData":[OSD([sQuery(id+"F0.wireOp",EDGE,"E1.bottom"),sQuery(id+"F0.wireOp",EDGE,"E1.top"),sQuery(id+"F0.wireOp",EDGE,"E1.left"),sQuery(id+"F0.wireOp",EDGE,"E1.right")])]}),"instanceName":"1"});
            var Q5;
            Q5=makeQuery(id+"F2.opPattern","COPY",BODY,{"derivedFrom":makeQuery(id+"F1.opExtrude","SWEPT_BODY",BODY,{"disambiguationData":[OSD([sQuery(id+"F0.wireOp",EDGE,"E2.bottom"),sQuery(id+"F0.wireOp",EDGE,"E2.top"),sQuery(id+"F0.wireOp",EDGE,"E2.left"),sQuery(id+"F0.wireOp",EDGE,"E2.right")])]}),"instanceName":"1"});
            var Q6;
            Q6=makeQuery(id+"F3.opPattern","COPY",BODY,{"derivedFrom":makeQuery(id+"F2.opPattern","COPY",BODY,{"derivedFrom":makeQuery(id+"F1.opExtrude","SWEPT_BODY",BODY,{"disambiguationData":[OSD([sQuery(id+"F0.wireOp",EDGE,"E0.bottom"),sQuery(id+"F0.wireOp",EDGE,"E0.top"),sQuery(id+"F0.wireOp",EDGE,"E0.left"),sQuery(id+"F0.wireOp",EDGE,"E0.right")])]}),"instanceName":"1"}),"instanceName":"1"});
            var Q7;
            Q7=makeQuery(id+"F3.opPattern","COPY",BODY,{"derivedFrom":makeQuery(id+"F2.opPattern","COPY",BODY,{"derivedFrom":makeQuery(id+"F1.opExtrude","SWEPT_BODY",BODY,{"disambiguationData":[OSD([sQuery(id+"F0.wireOp",EDGE,"E1.bottom"),sQuery(id+"F0.wireOp",EDGE,"E1.top"),sQuery(id+"F0.wireOp",EDGE,"E1.left"),sQuery(id+"F0.wireOp",EDGE,"E1.right")])]}),"instanceName":"1"}),"instanceName":"1"});
            var Q8;
            Q8=makeQuery(id+"F3.opPattern","COPY",BODY,{"derivedFrom":makeQuery(id+"F2.opPattern","COPY",BODY,{"derivedFrom":makeQuery(id+"F1.opExtrude","SWEPT_BODY",BODY,{"disambiguationData":[OSD([sQuery(id+"F0.wireOp",EDGE,"E2.bottom"),sQuery(id+"F0.wireOp",EDGE,"E2.top"),sQuery(id+"F0.wireOp",EDGE,"E2.left"),sQuery(id+"F0.wireOp",EDGE,"E2.right")])]}),"instanceName":"1"}),"instanceName":"1"});
            var Q9;
            Q9=makeQuery(id+"F4.opPattern","COPY",BODY,{"derivedFrom":makeQuery(id+"F3.opPattern","COPY",BODY,{"derivedFrom":makeQuery(id+"F2.opPattern","COPY",BODY,{"derivedFrom":makeQuery(id+"F1.opExtrude","SWEPT_BODY",BODY,{"disambiguationData":[OSD([sQuery(id+"F0.wireOp",EDGE,"E0.bottom"),sQuery(id+"F0.wireOp",EDGE,"E0.top"),sQuery(id+"F0.wireOp",EDGE,"E0.left"),sQuery(id+"F0.wireOp",EDGE,"E0.right")])]}),"instanceName":"1"}),"instanceName":"1"}),"instanceName":"1"});
            var Q10;
            Q10=makeQuery(id+"F4.opPattern","COPY",BODY,{"derivedFrom":makeQuery(id+"F3.opPattern","COPY",BODY,{"derivedFrom":makeQuery(id+"F2.opPattern","COPY",BODY,{"derivedFrom":makeQuery(id+"F1.opExtrude","SWEPT_BODY",BODY,{"disambiguationData":[OSD([sQuery(id+"F0.wireOp",EDGE,"E1.bottom"),sQuery(id+"F0.wireOp",EDGE,"E1.top"),sQuery(id+"F0.wireOp",EDGE,"E1.left"),sQuery(id+"F0.wireOp",EDGE,"E1.right")])]}),"instanceName":"1"}),"instanceName":"1"}),"instanceName":"1"});
            var Q11;
            Q11=makeQuery(id+"F4.opPattern","COPY",BODY,{"derivedFrom":makeQuery(id+"F3.opPattern","COPY",BODY,{"derivedFrom":makeQuery(id+"F2.opPattern","COPY",BODY,{"derivedFrom":makeQuery(id+"F1.opExtrude","SWEPT_BODY",BODY,{"disambiguationData":[OSD([sQuery(id+"F0.wireOp",EDGE,"E2.bottom"),sQuery(id+"F0.wireOp",EDGE,"E2.top"),sQuery(id+"F0.wireOp",EDGE,"E2.left"),sQuery(id+"F0.wireOp",EDGE,"E2.right")])]}),"instanceName":"1"}),"instanceName":"1"}),"instanceName":"1"});
            var Q12;
            Q12=makeQuery(id+"F5.opPattern","COPY",BODY,{"derivedFrom":makeQuery(id+"F4.opPattern","COPY",BODY,{"derivedFrom":makeQuery(id+"F3.opPattern","COPY",BODY,{"derivedFrom":makeQuery(id+"F2.opPattern","COPY",BODY,{"derivedFrom":makeQuery(id+"F1.opExtrude","SWEPT_BODY",BODY,{"disambiguationData":[OSD([sQuery(id+"F0.wireOp",EDGE,"E0.bottom"),sQuery(id+"F0.wireOp",EDGE,"E0.top"),sQuery(id+"F0.wireOp",EDGE,"E0.left"),sQuery(id+"F0.wireOp",EDGE,"E0.right")])]}),"instanceName":"1"}),"instanceName":"1"}),"instanceName":"1"}),"instanceName":"1"});
            var Q13;
            Q13=makeQuery(id+"F5.opPattern","COPY",BODY,{"derivedFrom":makeQuery(id+"F4.opPattern","COPY",BODY,{"derivedFrom":makeQuery(id+"F3.opPattern","COPY",BODY,{"derivedFrom":makeQuery(id+"F2.opPattern","COPY",BODY,{"derivedFrom":makeQuery(id+"F1.opExtrude","SWEPT_BODY",BODY,{"disambiguationData":[OSD([sQuery(id+"F0.wireOp",EDGE,"E1.bottom"),sQuery(id+"F0.wireOp",EDGE,"E1.top"),sQuery(id+"F0.wireOp",EDGE,"E1.left"),sQuery(id+"F0.wireOp",EDGE,"E1.right")])]}),"instanceName":"1"}),"instanceName":"1"}),"instanceName":"1"}),"instanceName":"1"});
            var Q14;
            Q14=makeQuery(id+"F5.opPattern","COPY",BODY,{"derivedFrom":makeQuery(id+"F4.opPattern","COPY",BODY,{"derivedFrom":makeQuery(id+"F3.opPattern","COPY",BODY,{"derivedFrom":makeQuery(id+"F2.opPattern","COPY",BODY,{"derivedFrom":makeQuery(id+"F1.opExtrude","SWEPT_BODY",BODY,{"disambiguationData":[OSD([sQuery(id+"F0.wireOp",EDGE,"E2.bottom"),sQuery(id+"F0.wireOp",EDGE,"E2.top"),sQuery(id+"F0.wireOp",EDGE,"E2.left"),sQuery(id+"F0.wireOp",EDGE,"E2.right")])]}),"instanceName":"1"}),"instanceName":"1"}),"instanceName":"1"}),"instanceName":"1"});
            var Q15;
            Q15=makeQuery(id+"F6.opPattern","COPY",BODY,{"derivedFrom":makeQuery(id+"F5.opPattern","COPY",BODY,{"derivedFrom":makeQuery(id+"F4.opPattern","COPY",BODY,{"derivedFrom":makeQuery(id+"F3.opPattern","COPY",BODY,{"derivedFrom":makeQuery(id+"F2.opPattern","COPY",BODY,{"derivedFrom":makeQuery(id+"F1.opExtrude","SWEPT_BODY",BODY,{"disambiguationData":[OSD([sQuery(id+"F0.wireOp",EDGE,"E0.bottom"),sQuery(id+"F0.wireOp",EDGE,"E0.top"),sQuery(id+"F0.wireOp",EDGE,"E0.left"),sQuery(id+"F0.wireOp",EDGE,"E0.right")])]}),"instanceName":"1"}),"instanceName":"1"}),"instanceName":"1"}),"instanceName":"1"}),"instanceName":"1"});
            var Q16;
            Q16=makeQuery(id+"F6.opPattern","COPY",BODY,{"derivedFrom":makeQuery(id+"F5.opPattern","COPY",BODY,{"derivedFrom":makeQuery(id+"F4.opPattern","COPY",BODY,{"derivedFrom":makeQuery(id+"F3.opPattern","COPY",BODY,{"derivedFrom":makeQuery(id+"F2.opPattern","COPY",BODY,{"derivedFrom":makeQuery(id+"F1.opExtrude","SWEPT_BODY",BODY,{"disambiguationData":[OSD([sQuery(id+"F0.wireOp",EDGE,"E1.bottom"),sQuery(id+"F0.wireOp",EDGE,"E1.top"),sQuery(id+"F0.wireOp",EDGE,"E1.left"),sQuery(id+"F0.wireOp",EDGE,"E1.right")])]}),"instanceName":"1"}),"instanceName":"1"}),"instanceName":"1"}),"instanceName":"1"}),"instanceName":"1"});
            var Q17;
            Q17=makeQuery(id+"F6.opPattern","COPY",BODY,{"derivedFrom":makeQuery(id+"F5.opPattern","COPY",BODY,{"derivedFrom":makeQuery(id+"F4.opPattern","COPY",BODY,{"derivedFrom":makeQuery(id+"F3.opPattern","COPY",BODY,{"derivedFrom":makeQuery(id+"F2.opPattern","COPY",BODY,{"derivedFrom":makeQuery(id+"F1.opExtrude","SWEPT_BODY",BODY,{"disambiguationData":[OSD([sQuery(id+"F0.wireOp",EDGE,"E2.bottom"),sQuery(id+"F0.wireOp",EDGE,"E2.top"),sQuery(id+"F0.wireOp",EDGE,"E2.left"),sQuery(id+"F0.wireOp",EDGE,"E2.right")])]}),"instanceName":"1"}),"instanceName":"1"}),"instanceName":"1"}),"instanceName":"1"}),"instanceName":"1"});
            var Q18;
            Q18=makeQuery(id+"F7.opPattern","COPY",BODY,{"derivedFrom":makeQuery(id+"F1.opExtrude","SWEPT_BODY",BODY,{"disambiguationData":[OSD([sQuery(id+"F0.wireOp",EDGE,"E0.bottom"),sQuery(id+"F0.wireOp",EDGE,"E0.top"),sQuery(id+"F0.wireOp",EDGE,"E0.left"),sQuery(id+"F0.wireOp",EDGE,"E0.right")])]}),"instanceName":"1"});
            var Q19;
            Q19=makeQuery(id+"F7.opPattern","COPY",BODY,{"derivedFrom":makeQuery(id+"F1.opExtrude","SWEPT_BODY",BODY,{"disambiguationData":[OSD([sQuery(id+"F0.wireOp",EDGE,"E1.bottom"),sQuery(id+"F0.wireOp",EDGE,"E1.top"),sQuery(id+"F0.wireOp",EDGE,"E1.left"),sQuery(id+"F0.wireOp",EDGE,"E1.right")])]}),"instanceName":"1"});
            var Q20;
            Q20=makeQuery(id+"F7.opPattern","COPY",BODY,{"derivedFrom":makeQuery(id+"F1.opExtrude","SWEPT_BODY",BODY,{"disambiguationData":[OSD([sQuery(id+"F0.wireOp",EDGE,"E2.bottom"),sQuery(id+"F0.wireOp",EDGE,"E2.top"),sQuery(id+"F0.wireOp",EDGE,"E2.left"),sQuery(id+"F0.wireOp",EDGE,"E2.right")])]}),"instanceName":"1"});
            var Q21;
            Q21=makeQuery(id+"F7.opPattern","COPY",BODY,{"derivedFrom":makeQuery(id+"F2.opPattern","COPY",BODY,{"derivedFrom":makeQuery(id+"F1.opExtrude","SWEPT_BODY",BODY,{"disambiguationData":[OSD([sQuery(id+"F0.wireOp",EDGE,"E0.bottom"),sQuery(id+"F0.wireOp",EDGE,"E0.top"),sQuery(id+"F0.wireOp",EDGE,"E0.left"),sQuery(id+"F0.wireOp",EDGE,"E0.right")])]}),"instanceName":"1"}),"instanceName":"1"});
            var Q22;
            Q22=makeQuery(id+"F7.opPattern","COPY",BODY,{"derivedFrom":makeQuery(id+"F2.opPattern","COPY",BODY,{"derivedFrom":makeQuery(id+"F1.opExtrude","SWEPT_BODY",BODY,{"disambiguationData":[OSD([sQuery(id+"F0.wireOp",EDGE,"E1.bottom"),sQuery(id+"F0.wireOp",EDGE,"E1.top"),sQuery(id+"F0.wireOp",EDGE,"E1.left"),sQuery(id+"F0.wireOp",EDGE,"E1.right")])]}),"instanceName":"1"}),"instanceName":"1"});
            var Q23;
            Q23=makeQuery(id+"F7.opPattern","COPY",BODY,{"derivedFrom":makeQuery(id+"F2.opPattern","COPY",BODY,{"derivedFrom":makeQuery(id+"F1.opExtrude","SWEPT_BODY",BODY,{"disambiguationData":[OSD([sQuery(id+"F0.wireOp",EDGE,"E2.bottom"),sQuery(id+"F0.wireOp",EDGE,"E2.top"),sQuery(id+"F0.wireOp",EDGE,"E2.left"),sQuery(id+"F0.wireOp",EDGE,"E2.right")])]}),"instanceName":"1"}),"instanceName":"1"});
            var Q24;
            Q24=makeQuery(id+"F7.opPattern","COPY",BODY,{"derivedFrom":makeQuery(id+"F3.opPattern","COPY",BODY,{"derivedFrom":makeQuery(id+"F2.opPattern","COPY",BODY,{"derivedFrom":makeQuery(id+"F1.opExtrude","SWEPT_BODY",BODY,{"disambiguationData":[OSD([sQuery(id+"F0.wireOp",EDGE,"E0.bottom"),sQuery(id+"F0.wireOp",EDGE,"E0.top"),sQuery(id+"F0.wireOp",EDGE,"E0.left"),sQuery(id+"F0.wireOp",EDGE,"E0.right")])]}),"instanceName":"1"}),"instanceName":"1"}),"instanceName":"1"});
            var Q25;
            Q25=makeQuery(id+"F7.opPattern","COPY",BODY,{"derivedFrom":makeQuery(id+"F3.opPattern","COPY",BODY,{"derivedFrom":makeQuery(id+"F2.opPattern","COPY",BODY,{"derivedFrom":makeQuery(id+"F1.opExtrude","SWEPT_BODY",BODY,{"disambiguationData":[OSD([sQuery(id+"F0.wireOp",EDGE,"E1.bottom"),sQuery(id+"F0.wireOp",EDGE,"E1.top"),sQuery(id+"F0.wireOp",EDGE,"E1.left"),sQuery(id+"F0.wireOp",EDGE,"E1.right")])]}),"instanceName":"1"}),"instanceName":"1"}),"instanceName":"1"});
            var Q26;
            Q26=makeQuery(id+"F7.opPattern","COPY",BODY,{"derivedFrom":makeQuery(id+"F3.opPattern","COPY",BODY,{"derivedFrom":makeQuery(id+"F2.opPattern","COPY",BODY,{"derivedFrom":makeQuery(id+"F1.opExtrude","SWEPT_BODY",BODY,{"disambiguationData":[OSD([sQuery(id+"F0.wireOp",EDGE,"E2.bottom"),sQuery(id+"F0.wireOp",EDGE,"E2.top"),sQuery(id+"F0.wireOp",EDGE,"E2.left"),sQuery(id+"F0.wireOp",EDGE,"E2.right")])]}),"instanceName":"1"}),"instanceName":"1"}),"instanceName":"1"});
            var Q27;
            Q27=makeQuery(id+"F7.opPattern","COPY",BODY,{"derivedFrom":makeQuery(id+"F4.opPattern","COPY",BODY,{"derivedFrom":makeQuery(id+"F3.opPattern","COPY",BODY,{"derivedFrom":makeQuery(id+"F2.opPattern","COPY",BODY,{"derivedFrom":makeQuery(id+"F1.opExtrude","SWEPT_BODY",BODY,{"disambiguationData":[OSD([sQuery(id+"F0.wireOp",EDGE,"E0.bottom"),sQuery(id+"F0.wireOp",EDGE,"E0.top"),sQuery(id+"F0.wireOp",EDGE,"E0.left"),sQuery(id+"F0.wireOp",EDGE,"E0.right")])]}),"instanceName":"1"}),"instanceName":"1"}),"instanceName":"1"}),"instanceName":"1"});
            var Q28;
            Q28=makeQuery(id+"F7.opPattern","COPY",BODY,{"derivedFrom":makeQuery(id+"F4.opPattern","COPY",BODY,{"derivedFrom":makeQuery(id+"F3.opPattern","COPY",BODY,{"derivedFrom":makeQuery(id+"F2.opPattern","COPY",BODY,{"derivedFrom":makeQuery(id+"F1.opExtrude","SWEPT_BODY",BODY,{"disambiguationData":[OSD([sQuery(id+"F0.wireOp",EDGE,"E1.bottom"),sQuery(id+"F0.wireOp",EDGE,"E1.top"),sQuery(id+"F0.wireOp",EDGE,"E1.left"),sQuery(id+"F0.wireOp",EDGE,"E1.right")])]}),"instanceName":"1"}),"instanceName":"1"}),"instanceName":"1"}),"instanceName":"1"});
            var Q29;
            Q29=makeQuery(id+"F7.opPattern","COPY",BODY,{"derivedFrom":makeQuery(id+"F4.opPattern","COPY",BODY,{"derivedFrom":makeQuery(id+"F3.opPattern","COPY",BODY,{"derivedFrom":makeQuery(id+"F2.opPattern","COPY",BODY,{"derivedFrom":makeQuery(id+"F1.opExtrude","SWEPT_BODY",BODY,{"disambiguationData":[OSD([sQuery(id+"F0.wireOp",EDGE,"E2.bottom"),sQuery(id+"F0.wireOp",EDGE,"E2.top"),sQuery(id+"F0.wireOp",EDGE,"E2.left"),sQuery(id+"F0.wireOp",EDGE,"E2.right")])]}),"instanceName":"1"}),"instanceName":"1"}),"instanceName":"1"}),"instanceName":"1"});
            var Q30;
            Q30=makeQuery(id+"F7.opPattern","COPY",BODY,{"derivedFrom":makeQuery(id+"F5.opPattern","COPY",BODY,{"derivedFrom":makeQuery(id+"F4.opPattern","COPY",BODY,{"derivedFrom":makeQuery(id+"F3.opPattern","COPY",BODY,{"derivedFrom":makeQuery(id+"F2.opPattern","COPY",BODY,{"derivedFrom":makeQuery(id+"F1.opExtrude","SWEPT_BODY",BODY,{"disambiguationData":[OSD([sQuery(id+"F0.wireOp",EDGE,"E0.bottom"),sQuery(id+"F0.wireOp",EDGE,"E0.top"),sQuery(id+"F0.wireOp",EDGE,"E0.left"),sQuery(id+"F0.wireOp",EDGE,"E0.right")])]}),"instanceName":"1"}),"instanceName":"1"}),"instanceName":"1"}),"instanceName":"1"}),"instanceName":"1"});
            var Q31;
            Q31=makeQuery(id+"F7.opPattern","COPY",BODY,{"derivedFrom":makeQuery(id+"F5.opPattern","COPY",BODY,{"derivedFrom":makeQuery(id+"F4.opPattern","COPY",BODY,{"derivedFrom":makeQuery(id+"F3.opPattern","COPY",BODY,{"derivedFrom":makeQuery(id+"F2.opPattern","COPY",BODY,{"derivedFrom":makeQuery(id+"F1.opExtrude","SWEPT_BODY",BODY,{"disambiguationData":[OSD([sQuery(id+"F0.wireOp",EDGE,"E1.bottom"),sQuery(id+"F0.wireOp",EDGE,"E1.top"),sQuery(id+"F0.wireOp",EDGE,"E1.left"),sQuery(id+"F0.wireOp",EDGE,"E1.right")])]}),"instanceName":"1"}),"instanceName":"1"}),"instanceName":"1"}),"instanceName":"1"}),"instanceName":"1"});
            var Q32;
            Q32=makeQuery(id+"F7.opPattern","COPY",BODY,{"derivedFrom":makeQuery(id+"F5.opPattern","COPY",BODY,{"derivedFrom":makeQuery(id+"F4.opPattern","COPY",BODY,{"derivedFrom":makeQuery(id+"F3.opPattern","COPY",BODY,{"derivedFrom":makeQuery(id+"F2.opPattern","COPY",BODY,{"derivedFrom":makeQuery(id+"F1.opExtrude","SWEPT_BODY",BODY,{"disambiguationData":[OSD([sQuery(id+"F0.wireOp",EDGE,"E2.bottom"),sQuery(id+"F0.wireOp",EDGE,"E2.top"),sQuery(id+"F0.wireOp",EDGE,"E2.left"),sQuery(id+"F0.wireOp",EDGE,"E2.right")])]}),"instanceName":"1"}),"instanceName":"1"}),"instanceName":"1"}),"instanceName":"1"}),"instanceName":"1"});
            var Q33;
            Q33=makeQuery(id+"F7.opPattern","COPY",BODY,{"derivedFrom":makeQuery(id+"F6.opPattern","COPY",BODY,{"derivedFrom":makeQuery(id+"F5.opPattern","COPY",BODY,{"derivedFrom":makeQuery(id+"F4.opPattern","COPY",BODY,{"derivedFrom":makeQuery(id+"F3.opPattern","COPY",BODY,{"derivedFrom":makeQuery(id+"F2.opPattern","COPY",BODY,{"derivedFrom":makeQuery(id+"F1.opExtrude","SWEPT_BODY",BODY,{"disambiguationData":[OSD([sQuery(id+"F0.wireOp",EDGE,"E0.bottom"),sQuery(id+"F0.wireOp",EDGE,"E0.top"),sQuery(id+"F0.wireOp",EDGE,"E0.left"),sQuery(id+"F0.wireOp",EDGE,"E0.right")])]}),"instanceName":"1"}),"instanceName":"1"}),"instanceName":"1"}),"instanceName":"1"}),"instanceName":"1"}),"instanceName":"1"});
            var Q34;
            Q34=makeQuery(id+"F7.opPattern","COPY",BODY,{"derivedFrom":makeQuery(id+"F6.opPattern","COPY",BODY,{"derivedFrom":makeQuery(id+"F5.opPattern","COPY",BODY,{"derivedFrom":makeQuery(id+"F4.opPattern","COPY",BODY,{"derivedFrom":makeQuery(id+"F3.opPattern","COPY",BODY,{"derivedFrom":makeQuery(id+"F2.opPattern","COPY",BODY,{"derivedFrom":makeQuery(id+"F1.opExtrude","SWEPT_BODY",BODY,{"disambiguationData":[OSD([sQuery(id+"F0.wireOp",EDGE,"E1.bottom"),sQuery(id+"F0.wireOp",EDGE,"E1.top"),sQuery(id+"F0.wireOp",EDGE,"E1.left"),sQuery(id+"F0.wireOp",EDGE,"E1.right")])]}),"instanceName":"1"}),"instanceName":"1"}),"instanceName":"1"}),"instanceName":"1"}),"instanceName":"1"}),"instanceName":"1"});
            var Q35;
            Q35=makeQuery(id+"F7.opPattern","COPY",BODY,{"derivedFrom":makeQuery(id+"F6.opPattern","COPY",BODY,{"derivedFrom":makeQuery(id+"F5.opPattern","COPY",BODY,{"derivedFrom":makeQuery(id+"F4.opPattern","COPY",BODY,{"derivedFrom":makeQuery(id+"F3.opPattern","COPY",BODY,{"derivedFrom":makeQuery(id+"F2.opPattern","COPY",BODY,{"derivedFrom":makeQuery(id+"F1.opExtrude","SWEPT_BODY",BODY,{"disambiguationData":[OSD([sQuery(id+"F0.wireOp",EDGE,"E2.bottom"),sQuery(id+"F0.wireOp",EDGE,"E2.top"),sQuery(id+"F0.wireOp",EDGE,"E2.left"),sQuery(id+"F0.wireOp",EDGE,"E2.right")])]}),"instanceName":"1"}),"instanceName":"1"}),"instanceName":"1"}),"instanceName":"1"}),"instanceName":"1"}),"instanceName":"1"});
            var Q36;
            Q36=makeQuery(id+"F8.opPattern","COPY",BODY,{"derivedFrom":makeQuery(id+"F1.opExtrude","SWEPT_BODY",BODY,{"disambiguationData":[OSD([sQuery(id+"F0.wireOp",EDGE,"E0.bottom"),sQuery(id+"F0.wireOp",EDGE,"E0.top"),sQuery(id+"F0.wireOp",EDGE,"E0.left"),sQuery(id+"F0.wireOp",EDGE,"E0.right")])]}),"instanceName":"1"});
            var Q37;
            Q37=makeQuery(id+"F8.opPattern","COPY",BODY,{"derivedFrom":makeQuery(id+"F1.opExtrude","SWEPT_BODY",BODY,{"disambiguationData":[OSD([sQuery(id+"F0.wireOp",EDGE,"E1.bottom"),sQuery(id+"F0.wireOp",EDGE,"E1.top"),sQuery(id+"F0.wireOp",EDGE,"E1.left"),sQuery(id+"F0.wireOp",EDGE,"E1.right")])]}),"instanceName":"1"});
            var Q38;
            Q38=makeQuery(id+"F8.opPattern","COPY",BODY,{"derivedFrom":makeQuery(id+"F1.opExtrude","SWEPT_BODY",BODY,{"disambiguationData":[OSD([sQuery(id+"F0.wireOp",EDGE,"E2.bottom"),sQuery(id+"F0.wireOp",EDGE,"E2.top"),sQuery(id+"F0.wireOp",EDGE,"E2.left"),sQuery(id+"F0.wireOp",EDGE,"E2.right")])]}),"instanceName":"1"});
            var Q39;
            Q39=makeQuery(id+"F8.opPattern","COPY",BODY,{"derivedFrom":makeQuery(id+"F2.opPattern","COPY",BODY,{"derivedFrom":makeQuery(id+"F1.opExtrude","SWEPT_BODY",BODY,{"disambiguationData":[OSD([sQuery(id+"F0.wireOp",EDGE,"E0.bottom"),sQuery(id+"F0.wireOp",EDGE,"E0.top"),sQuery(id+"F0.wireOp",EDGE,"E0.left"),sQuery(id+"F0.wireOp",EDGE,"E0.right")])]}),"instanceName":"1"}),"instanceName":"1"});
            var Q40;
            Q40=makeQuery(id+"F8.opPattern","COPY",BODY,{"derivedFrom":makeQuery(id+"F2.opPattern","COPY",BODY,{"derivedFrom":makeQuery(id+"F1.opExtrude","SWEPT_BODY",BODY,{"disambiguationData":[OSD([sQuery(id+"F0.wireOp",EDGE,"E1.bottom"),sQuery(id+"F0.wireOp",EDGE,"E1.top"),sQuery(id+"F0.wireOp",EDGE,"E1.left"),sQuery(id+"F0.wireOp",EDGE,"E1.right")])]}),"instanceName":"1"}),"instanceName":"1"});
            var Q41;
            Q41=makeQuery(id+"F8.opPattern","COPY",BODY,{"derivedFrom":makeQuery(id+"F2.opPattern","COPY",BODY,{"derivedFrom":makeQuery(id+"F1.opExtrude","SWEPT_BODY",BODY,{"disambiguationData":[OSD([sQuery(id+"F0.wireOp",EDGE,"E2.bottom"),sQuery(id+"F0.wireOp",EDGE,"E2.top"),sQuery(id+"F0.wireOp",EDGE,"E2.left"),sQuery(id+"F0.wireOp",EDGE,"E2.right")])]}),"instanceName":"1"}),"instanceName":"1"});
            var Q42;
            Q42=makeQuery(id+"F8.opPattern","COPY",BODY,{"derivedFrom":makeQuery(id+"F3.opPattern","COPY",BODY,{"derivedFrom":makeQuery(id+"F2.opPattern","COPY",BODY,{"derivedFrom":makeQuery(id+"F1.opExtrude","SWEPT_BODY",BODY,{"disambiguationData":[OSD([sQuery(id+"F0.wireOp",EDGE,"E0.bottom"),sQuery(id+"F0.wireOp",EDGE,"E0.top"),sQuery(id+"F0.wireOp",EDGE,"E0.left"),sQuery(id+"F0.wireOp",EDGE,"E0.right")])]}),"instanceName":"1"}),"instanceName":"1"}),"instanceName":"1"});
            var Q43;
            Q43=makeQuery(id+"F8.opPattern","COPY",BODY,{"derivedFrom":makeQuery(id+"F3.opPattern","COPY",BODY,{"derivedFrom":makeQuery(id+"F2.opPattern","COPY",BODY,{"derivedFrom":makeQuery(id+"F1.opExtrude","SWEPT_BODY",BODY,{"disambiguationData":[OSD([sQuery(id+"F0.wireOp",EDGE,"E1.bottom"),sQuery(id+"F0.wireOp",EDGE,"E1.top"),sQuery(id+"F0.wireOp",EDGE,"E1.left"),sQuery(id+"F0.wireOp",EDGE,"E1.right")])]}),"instanceName":"1"}),"instanceName":"1"}),"instanceName":"1"});
            var Q44;
            Q44=makeQuery(id+"F8.opPattern","COPY",BODY,{"derivedFrom":makeQuery(id+"F3.opPattern","COPY",BODY,{"derivedFrom":makeQuery(id+"F2.opPattern","COPY",BODY,{"derivedFrom":makeQuery(id+"F1.opExtrude","SWEPT_BODY",BODY,{"disambiguationData":[OSD([sQuery(id+"F0.wireOp",EDGE,"E2.bottom"),sQuery(id+"F0.wireOp",EDGE,"E2.top"),sQuery(id+"F0.wireOp",EDGE,"E2.left"),sQuery(id+"F0.wireOp",EDGE,"E2.right")])]}),"instanceName":"1"}),"instanceName":"1"}),"instanceName":"1"});
            var Q45;
            Q45=makeQuery(id+"F8.opPattern","COPY",BODY,{"derivedFrom":makeQuery(id+"F4.opPattern","COPY",BODY,{"derivedFrom":makeQuery(id+"F3.opPattern","COPY",BODY,{"derivedFrom":makeQuery(id+"F2.opPattern","COPY",BODY,{"derivedFrom":makeQuery(id+"F1.opExtrude","SWEPT_BODY",BODY,{"disambiguationData":[OSD([sQuery(id+"F0.wireOp",EDGE,"E0.bottom"),sQuery(id+"F0.wireOp",EDGE,"E0.top"),sQuery(id+"F0.wireOp",EDGE,"E0.left"),sQuery(id+"F0.wireOp",EDGE,"E0.right")])]}),"instanceName":"1"}),"instanceName":"1"}),"instanceName":"1"}),"instanceName":"1"});
            var Q46;
            Q46=makeQuery(id+"F8.opPattern","COPY",BODY,{"derivedFrom":makeQuery(id+"F4.opPattern","COPY",BODY,{"derivedFrom":makeQuery(id+"F3.opPattern","COPY",BODY,{"derivedFrom":makeQuery(id+"F2.opPattern","COPY",BODY,{"derivedFrom":makeQuery(id+"F1.opExtrude","SWEPT_BODY",BODY,{"disambiguationData":[OSD([sQuery(id+"F0.wireOp",EDGE,"E1.bottom"),sQuery(id+"F0.wireOp",EDGE,"E1.top"),sQuery(id+"F0.wireOp",EDGE,"E1.left"),sQuery(id+"F0.wireOp",EDGE,"E1.right")])]}),"instanceName":"1"}),"instanceName":"1"}),"instanceName":"1"}),"instanceName":"1"});
            var Q47;
            Q47=makeQuery(id+"F8.opPattern","COPY",BODY,{"derivedFrom":makeQuery(id+"F4.opPattern","COPY",BODY,{"derivedFrom":makeQuery(id+"F3.opPattern","COPY",BODY,{"derivedFrom":makeQuery(id+"F2.opPattern","COPY",BODY,{"derivedFrom":makeQuery(id+"F1.opExtrude","SWEPT_BODY",BODY,{"disambiguationData":[OSD([sQuery(id+"F0.wireOp",EDGE,"E2.bottom"),sQuery(id+"F0.wireOp",EDGE,"E2.top"),sQuery(id+"F0.wireOp",EDGE,"E2.left"),sQuery(id+"F0.wireOp",EDGE,"E2.right")])]}),"instanceName":"1"}),"instanceName":"1"}),"instanceName":"1"}),"instanceName":"1"});
            var Q48;
            Q48=makeQuery(id+"F8.opPattern","COPY",BODY,{"derivedFrom":makeQuery(id+"F5.opPattern","COPY",BODY,{"derivedFrom":makeQuery(id+"F4.opPattern","COPY",BODY,{"derivedFrom":makeQuery(id+"F3.opPattern","COPY",BODY,{"derivedFrom":makeQuery(id+"F2.opPattern","COPY",BODY,{"derivedFrom":makeQuery(id+"F1.opExtrude","SWEPT_BODY",BODY,{"disambiguationData":[OSD([sQuery(id+"F0.wireOp",EDGE,"E0.bottom"),sQuery(id+"F0.wireOp",EDGE,"E0.top"),sQuery(id+"F0.wireOp",EDGE,"E0.left"),sQuery(id+"F0.wireOp",EDGE,"E0.right")])]}),"instanceName":"1"}),"instanceName":"1"}),"instanceName":"1"}),"instanceName":"1"}),"instanceName":"1"});
            var Q49;
            Q49=makeQuery(id+"F8.opPattern","COPY",BODY,{"derivedFrom":makeQuery(id+"F5.opPattern","COPY",BODY,{"derivedFrom":makeQuery(id+"F4.opPattern","COPY",BODY,{"derivedFrom":makeQuery(id+"F3.opPattern","COPY",BODY,{"derivedFrom":makeQuery(id+"F2.opPattern","COPY",BODY,{"derivedFrom":makeQuery(id+"F1.opExtrude","SWEPT_BODY",BODY,{"disambiguationData":[OSD([sQuery(id+"F0.wireOp",EDGE,"E1.bottom"),sQuery(id+"F0.wireOp",EDGE,"E1.top"),sQuery(id+"F0.wireOp",EDGE,"E1.left"),sQuery(id+"F0.wireOp",EDGE,"E1.right")])]}),"instanceName":"1"}),"instanceName":"1"}),"instanceName":"1"}),"instanceName":"1"}),"instanceName":"1"});
            var Q50;
            Q50=makeQuery(id+"F8.opPattern","COPY",BODY,{"derivedFrom":makeQuery(id+"F5.opPattern","COPY",BODY,{"derivedFrom":makeQuery(id+"F4.opPattern","COPY",BODY,{"derivedFrom":makeQuery(id+"F3.opPattern","COPY",BODY,{"derivedFrom":makeQuery(id+"F2.opPattern","COPY",BODY,{"derivedFrom":makeQuery(id+"F1.opExtrude","SWEPT_BODY",BODY,{"disambiguationData":[OSD([sQuery(id+"F0.wireOp",EDGE,"E2.bottom"),sQuery(id+"F0.wireOp",EDGE,"E2.top"),sQuery(id+"F0.wireOp",EDGE,"E2.left"),sQuery(id+"F0.wireOp",EDGE,"E2.right")])]}),"instanceName":"1"}),"instanceName":"1"}),"instanceName":"1"}),"instanceName":"1"}),"instanceName":"1"});
            var Q51;
            Q51=makeQuery(id+"F8.opPattern","COPY",BODY,{"derivedFrom":makeQuery(id+"F6.opPattern","COPY",BODY,{"derivedFrom":makeQuery(id+"F5.opPattern","COPY",BODY,{"derivedFrom":makeQuery(id+"F4.opPattern","COPY",BODY,{"derivedFrom":makeQuery(id+"F3.opPattern","COPY",BODY,{"derivedFrom":makeQuery(id+"F2.opPattern","COPY",BODY,{"derivedFrom":makeQuery(id+"F1.opExtrude","SWEPT_BODY",BODY,{"disambiguationData":[OSD([sQuery(id+"F0.wireOp",EDGE,"E0.bottom"),sQuery(id+"F0.wireOp",EDGE,"E0.top"),sQuery(id+"F0.wireOp",EDGE,"E0.left"),sQuery(id+"F0.wireOp",EDGE,"E0.right")])]}),"instanceName":"1"}),"instanceName":"1"}),"instanceName":"1"}),"instanceName":"1"}),"instanceName":"1"}),"instanceName":"1"});
            var Q52;
            Q52=makeQuery(id+"F8.opPattern","COPY",BODY,{"derivedFrom":makeQuery(id+"F6.opPattern","COPY",BODY,{"derivedFrom":makeQuery(id+"F5.opPattern","COPY",BODY,{"derivedFrom":makeQuery(id+"F4.opPattern","COPY",BODY,{"derivedFrom":makeQuery(id+"F3.opPattern","COPY",BODY,{"derivedFrom":makeQuery(id+"F2.opPattern","COPY",BODY,{"derivedFrom":makeQuery(id+"F1.opExtrude","SWEPT_BODY",BODY,{"disambiguationData":[OSD([sQuery(id+"F0.wireOp",EDGE,"E1.bottom"),sQuery(id+"F0.wireOp",EDGE,"E1.top"),sQuery(id+"F0.wireOp",EDGE,"E1.left"),sQuery(id+"F0.wireOp",EDGE,"E1.right")])]}),"instanceName":"1"}),"instanceName":"1"}),"instanceName":"1"}),"instanceName":"1"}),"instanceName":"1"}),"instanceName":"1"});
            var Q53;
            Q53=makeQuery(id+"F8.opPattern","COPY",BODY,{"derivedFrom":makeQuery(id+"F6.opPattern","COPY",BODY,{"derivedFrom":makeQuery(id+"F5.opPattern","COPY",BODY,{"derivedFrom":makeQuery(id+"F4.opPattern","COPY",BODY,{"derivedFrom":makeQuery(id+"F3.opPattern","COPY",BODY,{"derivedFrom":makeQuery(id+"F2.opPattern","COPY",BODY,{"derivedFrom":makeQuery(id+"F1.opExtrude","SWEPT_BODY",BODY,{"disambiguationData":[OSD([sQuery(id+"F0.wireOp",EDGE,"E2.bottom"),sQuery(id+"F0.wireOp",EDGE,"E2.top"),sQuery(id+"F0.wireOp",EDGE,"E2.left"),sQuery(id+"F0.wireOp",EDGE,"E2.right")])]}),"instanceName":"1"}),"instanceName":"1"}),"instanceName":"1"}),"instanceName":"1"}),"instanceName":"1"}),"instanceName":"1"});
            var Q54;
            Q54=makeQuery(id+"F8.opPattern","COPY",BODY,{"derivedFrom":makeQuery(id+"F7.opPattern","COPY",BODY,{"derivedFrom":makeQuery(id+"F1.opExtrude","SWEPT_BODY",BODY,{"disambiguationData":[OSD([sQuery(id+"F0.wireOp",EDGE,"E0.bottom"),sQuery(id+"F0.wireOp",EDGE,"E0.top"),sQuery(id+"F0.wireOp",EDGE,"E0.left"),sQuery(id+"F0.wireOp",EDGE,"E0.right")])]}),"instanceName":"1"}),"instanceName":"1"});
            var Q55;
            Q55=makeQuery(id+"F8.opPattern","COPY",BODY,{"derivedFrom":makeQuery(id+"F7.opPattern","COPY",BODY,{"derivedFrom":makeQuery(id+"F1.opExtrude","SWEPT_BODY",BODY,{"disambiguationData":[OSD([sQuery(id+"F0.wireOp",EDGE,"E1.bottom"),sQuery(id+"F0.wireOp",EDGE,"E1.top"),sQuery(id+"F0.wireOp",EDGE,"E1.left"),sQuery(id+"F0.wireOp",EDGE,"E1.right")])]}),"instanceName":"1"}),"instanceName":"1"});
            var Q56;
            Q56=makeQuery(id+"F8.opPattern","COPY",BODY,{"derivedFrom":makeQuery(id+"F7.opPattern","COPY",BODY,{"derivedFrom":makeQuery(id+"F1.opExtrude","SWEPT_BODY",BODY,{"disambiguationData":[OSD([sQuery(id+"F0.wireOp",EDGE,"E2.bottom"),sQuery(id+"F0.wireOp",EDGE,"E2.top"),sQuery(id+"F0.wireOp",EDGE,"E2.left"),sQuery(id+"F0.wireOp",EDGE,"E2.right")])]}),"instanceName":"1"}),"instanceName":"1"});
            var Q57;
            Q57=makeQuery(id+"F8.opPattern","COPY",BODY,{"derivedFrom":makeQuery(id+"F7.opPattern","COPY",BODY,{"derivedFrom":makeQuery(id+"F2.opPattern","COPY",BODY,{"derivedFrom":makeQuery(id+"F1.opExtrude","SWEPT_BODY",BODY,{"disambiguationData":[OSD([sQuery(id+"F0.wireOp",EDGE,"E0.bottom"),sQuery(id+"F0.wireOp",EDGE,"E0.top"),sQuery(id+"F0.wireOp",EDGE,"E0.left"),sQuery(id+"F0.wireOp",EDGE,"E0.right")])]}),"instanceName":"1"}),"instanceName":"1"}),"instanceName":"1"});
            var Q58;
            Q58=makeQuery(id+"F8.opPattern","COPY",BODY,{"derivedFrom":makeQuery(id+"F7.opPattern","COPY",BODY,{"derivedFrom":makeQuery(id+"F2.opPattern","COPY",BODY,{"derivedFrom":makeQuery(id+"F1.opExtrude","SWEPT_BODY",BODY,{"disambiguationData":[OSD([sQuery(id+"F0.wireOp",EDGE,"E1.bottom"),sQuery(id+"F0.wireOp",EDGE,"E1.top"),sQuery(id+"F0.wireOp",EDGE,"E1.left"),sQuery(id+"F0.wireOp",EDGE,"E1.right")])]}),"instanceName":"1"}),"instanceName":"1"}),"instanceName":"1"});
            var Q59;
            Q59=makeQuery(id+"F8.opPattern","COPY",BODY,{"derivedFrom":makeQuery(id+"F7.opPattern","COPY",BODY,{"derivedFrom":makeQuery(id+"F2.opPattern","COPY",BODY,{"derivedFrom":makeQuery(id+"F1.opExtrude","SWEPT_BODY",BODY,{"disambiguationData":[OSD([sQuery(id+"F0.wireOp",EDGE,"E2.bottom"),sQuery(id+"F0.wireOp",EDGE,"E2.top"),sQuery(id+"F0.wireOp",EDGE,"E2.left"),sQuery(id+"F0.wireOp",EDGE,"E2.right")])]}),"instanceName":"1"}),"instanceName":"1"}),"instanceName":"1"});
            var Q60;
            Q60=makeQuery(id+"F8.opPattern","COPY",BODY,{"derivedFrom":makeQuery(id+"F7.opPattern","COPY",BODY,{"derivedFrom":makeQuery(id+"F3.opPattern","COPY",BODY,{"derivedFrom":makeQuery(id+"F2.opPattern","COPY",BODY,{"derivedFrom":makeQuery(id+"F1.opExtrude","SWEPT_BODY",BODY,{"disambiguationData":[OSD([sQuery(id+"F0.wireOp",EDGE,"E0.bottom"),sQuery(id+"F0.wireOp",EDGE,"E0.top"),sQuery(id+"F0.wireOp",EDGE,"E0.left"),sQuery(id+"F0.wireOp",EDGE,"E0.right")])]}),"instanceName":"1"}),"instanceName":"1"}),"instanceName":"1"}),"instanceName":"1"});
            var Q61;
            Q61=makeQuery(id+"F8.opPattern","COPY",BODY,{"derivedFrom":makeQuery(id+"F7.opPattern","COPY",BODY,{"derivedFrom":makeQuery(id+"F3.opPattern","COPY",BODY,{"derivedFrom":makeQuery(id+"F2.opPattern","COPY",BODY,{"derivedFrom":makeQuery(id+"F1.opExtrude","SWEPT_BODY",BODY,{"disambiguationData":[OSD([sQuery(id+"F0.wireOp",EDGE,"E1.bottom"),sQuery(id+"F0.wireOp",EDGE,"E1.top"),sQuery(id+"F0.wireOp",EDGE,"E1.left"),sQuery(id+"F0.wireOp",EDGE,"E1.right")])]}),"instanceName":"1"}),"instanceName":"1"}),"instanceName":"1"}),"instanceName":"1"});
            var Q62;
            Q62=makeQuery(id+"F8.opPattern","COPY",BODY,{"derivedFrom":makeQuery(id+"F7.opPattern","COPY",BODY,{"derivedFrom":makeQuery(id+"F3.opPattern","COPY",BODY,{"derivedFrom":makeQuery(id+"F2.opPattern","COPY",BODY,{"derivedFrom":makeQuery(id+"F1.opExtrude","SWEPT_BODY",BODY,{"disambiguationData":[OSD([sQuery(id+"F0.wireOp",EDGE,"E2.bottom"),sQuery(id+"F0.wireOp",EDGE,"E2.top"),sQuery(id+"F0.wireOp",EDGE,"E2.left"),sQuery(id+"F0.wireOp",EDGE,"E2.right")])]}),"instanceName":"1"}),"instanceName":"1"}),"instanceName":"1"}),"instanceName":"1"});
            var Q63;
            Q63=makeQuery(id+"F8.opPattern","COPY",BODY,{"derivedFrom":makeQuery(id+"F7.opPattern","COPY",BODY,{"derivedFrom":makeQuery(id+"F4.opPattern","COPY",BODY,{"derivedFrom":makeQuery(id+"F3.opPattern","COPY",BODY,{"derivedFrom":makeQuery(id+"F2.opPattern","COPY",BODY,{"derivedFrom":makeQuery(id+"F1.opExtrude","SWEPT_BODY",BODY,{"disambiguationData":[OSD([sQuery(id+"F0.wireOp",EDGE,"E0.bottom"),sQuery(id+"F0.wireOp",EDGE,"E0.top"),sQuery(id+"F0.wireOp",EDGE,"E0.left"),sQuery(id+"F0.wireOp",EDGE,"E0.right")])]}),"instanceName":"1"}),"instanceName":"1"}),"instanceName":"1"}),"instanceName":"1"}),"instanceName":"1"});
            var Q64;
            Q64=makeQuery(id+"F8.opPattern","COPY",BODY,{"derivedFrom":makeQuery(id+"F7.opPattern","COPY",BODY,{"derivedFrom":makeQuery(id+"F4.opPattern","COPY",BODY,{"derivedFrom":makeQuery(id+"F3.opPattern","COPY",BODY,{"derivedFrom":makeQuery(id+"F2.opPattern","COPY",BODY,{"derivedFrom":makeQuery(id+"F1.opExtrude","SWEPT_BODY",BODY,{"disambiguationData":[OSD([sQuery(id+"F0.wireOp",EDGE,"E1.bottom"),sQuery(id+"F0.wireOp",EDGE,"E1.top"),sQuery(id+"F0.wireOp",EDGE,"E1.left"),sQuery(id+"F0.wireOp",EDGE,"E1.right")])]}),"instanceName":"1"}),"instanceName":"1"}),"instanceName":"1"}),"instanceName":"1"}),"instanceName":"1"});
            var Q65;
            Q65=makeQuery(id+"F8.opPattern","COPY",BODY,{"derivedFrom":makeQuery(id+"F7.opPattern","COPY",BODY,{"derivedFrom":makeQuery(id+"F4.opPattern","COPY",BODY,{"derivedFrom":makeQuery(id+"F3.opPattern","COPY",BODY,{"derivedFrom":makeQuery(id+"F2.opPattern","COPY",BODY,{"derivedFrom":makeQuery(id+"F1.opExtrude","SWEPT_BODY",BODY,{"disambiguationData":[OSD([sQuery(id+"F0.wireOp",EDGE,"E2.bottom"),sQuery(id+"F0.wireOp",EDGE,"E2.top"),sQuery(id+"F0.wireOp",EDGE,"E2.left"),sQuery(id+"F0.wireOp",EDGE,"E2.right")])]}),"instanceName":"1"}),"instanceName":"1"}),"instanceName":"1"}),"instanceName":"1"}),"instanceName":"1"});
            var Q66;
            Q66=makeQuery(id+"F8.opPattern","COPY",BODY,{"derivedFrom":makeQuery(id+"F7.opPattern","COPY",BODY,{"derivedFrom":makeQuery(id+"F5.opPattern","COPY",BODY,{"derivedFrom":makeQuery(id+"F4.opPattern","COPY",BODY,{"derivedFrom":makeQuery(id+"F3.opPattern","COPY",BODY,{"derivedFrom":makeQuery(id+"F2.opPattern","COPY",BODY,{"derivedFrom":makeQuery(id+"F1.opExtrude","SWEPT_BODY",BODY,{"disambiguationData":[OSD([sQuery(id+"F0.wireOp",EDGE,"E0.bottom"),sQuery(id+"F0.wireOp",EDGE,"E0.top"),sQuery(id+"F0.wireOp",EDGE,"E0.left"),sQuery(id+"F0.wireOp",EDGE,"E0.right")])]}),"instanceName":"1"}),"instanceName":"1"}),"instanceName":"1"}),"instanceName":"1"}),"instanceName":"1"}),"instanceName":"1"});
            var Q67;
            Q67=makeQuery(id+"F8.opPattern","COPY",BODY,{"derivedFrom":makeQuery(id+"F7.opPattern","COPY",BODY,{"derivedFrom":makeQuery(id+"F5.opPattern","COPY",BODY,{"derivedFrom":makeQuery(id+"F4.opPattern","COPY",BODY,{"derivedFrom":makeQuery(id+"F3.opPattern","COPY",BODY,{"derivedFrom":makeQuery(id+"F2.opPattern","COPY",BODY,{"derivedFrom":makeQuery(id+"F1.opExtrude","SWEPT_BODY",BODY,{"disambiguationData":[OSD([sQuery(id+"F0.wireOp",EDGE,"E1.bottom"),sQuery(id+"F0.wireOp",EDGE,"E1.top"),sQuery(id+"F0.wireOp",EDGE,"E1.left"),sQuery(id+"F0.wireOp",EDGE,"E1.right")])]}),"instanceName":"1"}),"instanceName":"1"}),"instanceName":"1"}),"instanceName":"1"}),"instanceName":"1"}),"instanceName":"1"});
            var Q68;
            Q68=makeQuery(id+"F8.opPattern","COPY",BODY,{"derivedFrom":makeQuery(id+"F7.opPattern","COPY",BODY,{"derivedFrom":makeQuery(id+"F5.opPattern","COPY",BODY,{"derivedFrom":makeQuery(id+"F4.opPattern","COPY",BODY,{"derivedFrom":makeQuery(id+"F3.opPattern","COPY",BODY,{"derivedFrom":makeQuery(id+"F2.opPattern","COPY",BODY,{"derivedFrom":makeQuery(id+"F1.opExtrude","SWEPT_BODY",BODY,{"disambiguationData":[OSD([sQuery(id+"F0.wireOp",EDGE,"E2.bottom"),sQuery(id+"F0.wireOp",EDGE,"E2.top"),sQuery(id+"F0.wireOp",EDGE,"E2.left"),sQuery(id+"F0.wireOp",EDGE,"E2.right")])]}),"instanceName":"1"}),"instanceName":"1"}),"instanceName":"1"}),"instanceName":"1"}),"instanceName":"1"}),"instanceName":"1"});
            var Q69;
            Q69=makeQuery(id+"F8.opPattern","COPY",BODY,{"derivedFrom":makeQuery(id+"F7.opPattern","COPY",BODY,{"derivedFrom":makeQuery(id+"F6.opPattern","COPY",BODY,{"derivedFrom":makeQuery(id+"F5.opPattern","COPY",BODY,{"derivedFrom":makeQuery(id+"F4.opPattern","COPY",BODY,{"derivedFrom":makeQuery(id+"F3.opPattern","COPY",BODY,{"derivedFrom":makeQuery(id+"F2.opPattern","COPY",BODY,{"derivedFrom":makeQuery(id+"F1.opExtrude","SWEPT_BODY",BODY,{"disambiguationData":[OSD([sQuery(id+"F0.wireOp",EDGE,"E0.bottom"),sQuery(id+"F0.wireOp",EDGE,"E0.top"),sQuery(id+"F0.wireOp",EDGE,"E0.left"),sQuery(id+"F0.wireOp",EDGE,"E0.right")])]}),"instanceName":"1"}),"instanceName":"1"}),"instanceName":"1"}),"instanceName":"1"}),"instanceName":"1"}),"instanceName":"1"}),"instanceName":"1"});
            var Q70;
            Q70=makeQuery(id+"F8.opPattern","COPY",BODY,{"derivedFrom":makeQuery(id+"F7.opPattern","COPY",BODY,{"derivedFrom":makeQuery(id+"F6.opPattern","COPY",BODY,{"derivedFrom":makeQuery(id+"F5.opPattern","COPY",BODY,{"derivedFrom":makeQuery(id+"F4.opPattern","COPY",BODY,{"derivedFrom":makeQuery(id+"F3.opPattern","COPY",BODY,{"derivedFrom":makeQuery(id+"F2.opPattern","COPY",BODY,{"derivedFrom":makeQuery(id+"F1.opExtrude","SWEPT_BODY",BODY,{"disambiguationData":[OSD([sQuery(id+"F0.wireOp",EDGE,"E1.bottom"),sQuery(id+"F0.wireOp",EDGE,"E1.top"),sQuery(id+"F0.wireOp",EDGE,"E1.left"),sQuery(id+"F0.wireOp",EDGE,"E1.right")])]}),"instanceName":"1"}),"instanceName":"1"}),"instanceName":"1"}),"instanceName":"1"}),"instanceName":"1"}),"instanceName":"1"}),"instanceName":"1"});
            var Q71;
            Q71=makeQuery(id+"F8.opPattern","COPY",BODY,{"derivedFrom":makeQuery(id+"F7.opPattern","COPY",BODY,{"derivedFrom":makeQuery(id+"F6.opPattern","COPY",BODY,{"derivedFrom":makeQuery(id+"F5.opPattern","COPY",BODY,{"derivedFrom":makeQuery(id+"F4.opPattern","COPY",BODY,{"derivedFrom":makeQuery(id+"F3.opPattern","COPY",BODY,{"derivedFrom":makeQuery(id+"F2.opPattern","COPY",BODY,{"derivedFrom":makeQuery(id+"F1.opExtrude","SWEPT_BODY",BODY,{"disambiguationData":[OSD([sQuery(id+"F0.wireOp",EDGE,"E2.bottom"),sQuery(id+"F0.wireOp",EDGE,"E2.top"),sQuery(id+"F0.wireOp",EDGE,"E2.left"),sQuery(id+"F0.wireOp",EDGE,"E2.right")])]}),"instanceName":"1"}),"instanceName":"1"}),"instanceName":"1"}),"instanceName":"1"}),"instanceName":"1"}),"instanceName":"1"}),"instanceName":"1"});
            var Q72;
            Q72=makeQuery(id+"F9.opPattern","COPY",BODY,{"derivedFrom":makeQuery(id+"F1.opExtrude","SWEPT_BODY",BODY,{"disambiguationData":[OSD([sQuery(id+"F0.wireOp",EDGE,"E0.bottom"),sQuery(id+"F0.wireOp",EDGE,"E0.top"),sQuery(id+"F0.wireOp",EDGE,"E0.left"),sQuery(id+"F0.wireOp",EDGE,"E0.right")])]}),"instanceName":"1"});
            var Q73;
            Q73=makeQuery(id+"F9.opPattern","COPY",BODY,{"derivedFrom":makeQuery(id+"F1.opExtrude","SWEPT_BODY",BODY,{"disambiguationData":[OSD([sQuery(id+"F0.wireOp",EDGE,"E1.bottom"),sQuery(id+"F0.wireOp",EDGE,"E1.top"),sQuery(id+"F0.wireOp",EDGE,"E1.left"),sQuery(id+"F0.wireOp",EDGE,"E1.right")])]}),"instanceName":"1"});
            var Q74;
            Q74=makeQuery(id+"F9.opPattern","COPY",BODY,{"derivedFrom":makeQuery(id+"F1.opExtrude","SWEPT_BODY",BODY,{"disambiguationData":[OSD([sQuery(id+"F0.wireOp",EDGE,"E2.bottom"),sQuery(id+"F0.wireOp",EDGE,"E2.top"),sQuery(id+"F0.wireOp",EDGE,"E2.left"),sQuery(id+"F0.wireOp",EDGE,"E2.right")])]}),"instanceName":"1"});
            var Q75;
            Q75=makeQuery(id+"F9.opPattern","COPY",BODY,{"derivedFrom":makeQuery(id+"F2.opPattern","COPY",BODY,{"derivedFrom":makeQuery(id+"F1.opExtrude","SWEPT_BODY",BODY,{"disambiguationData":[OSD([sQuery(id+"F0.wireOp",EDGE,"E0.bottom"),sQuery(id+"F0.wireOp",EDGE,"E0.top"),sQuery(id+"F0.wireOp",EDGE,"E0.left"),sQuery(id+"F0.wireOp",EDGE,"E0.right")])]}),"instanceName":"1"}),"instanceName":"1"});
            var Q76;
            Q76=makeQuery(id+"F9.opPattern","COPY",BODY,{"derivedFrom":makeQuery(id+"F2.opPattern","COPY",BODY,{"derivedFrom":makeQuery(id+"F1.opExtrude","SWEPT_BODY",BODY,{"disambiguationData":[OSD([sQuery(id+"F0.wireOp",EDGE,"E1.bottom"),sQuery(id+"F0.wireOp",EDGE,"E1.top"),sQuery(id+"F0.wireOp",EDGE,"E1.left"),sQuery(id+"F0.wireOp",EDGE,"E1.right")])]}),"instanceName":"1"}),"instanceName":"1"});
            var Q77;
            Q77=makeQuery(id+"F9.opPattern","COPY",BODY,{"derivedFrom":makeQuery(id+"F2.opPattern","COPY",BODY,{"derivedFrom":makeQuery(id+"F1.opExtrude","SWEPT_BODY",BODY,{"disambiguationData":[OSD([sQuery(id+"F0.wireOp",EDGE,"E2.bottom"),sQuery(id+"F0.wireOp",EDGE,"E2.top"),sQuery(id+"F0.wireOp",EDGE,"E2.left"),sQuery(id+"F0.wireOp",EDGE,"E2.right")])]}),"instanceName":"1"}),"instanceName":"1"});
            var Q78;
            Q78=makeQuery(id+"F9.opPattern","COPY",BODY,{"derivedFrom":makeQuery(id+"F3.opPattern","COPY",BODY,{"derivedFrom":makeQuery(id+"F2.opPattern","COPY",BODY,{"derivedFrom":makeQuery(id+"F1.opExtrude","SWEPT_BODY",BODY,{"disambiguationData":[OSD([sQuery(id+"F0.wireOp",EDGE,"E0.bottom"),sQuery(id+"F0.wireOp",EDGE,"E0.top"),sQuery(id+"F0.wireOp",EDGE,"E0.left"),sQuery(id+"F0.wireOp",EDGE,"E0.right")])]}),"instanceName":"1"}),"instanceName":"1"}),"instanceName":"1"});
            var Q79;
            Q79=makeQuery(id+"F9.opPattern","COPY",BODY,{"derivedFrom":makeQuery(id+"F3.opPattern","COPY",BODY,{"derivedFrom":makeQuery(id+"F2.opPattern","COPY",BODY,{"derivedFrom":makeQuery(id+"F1.opExtrude","SWEPT_BODY",BODY,{"disambiguationData":[OSD([sQuery(id+"F0.wireOp",EDGE,"E1.bottom"),sQuery(id+"F0.wireOp",EDGE,"E1.top"),sQuery(id+"F0.wireOp",EDGE,"E1.left"),sQuery(id+"F0.wireOp",EDGE,"E1.right")])]}),"instanceName":"1"}),"instanceName":"1"}),"instanceName":"1"});
            var Q80;
            Q80=makeQuery(id+"F9.opPattern","COPY",BODY,{"derivedFrom":makeQuery(id+"F3.opPattern","COPY",BODY,{"derivedFrom":makeQuery(id+"F2.opPattern","COPY",BODY,{"derivedFrom":makeQuery(id+"F1.opExtrude","SWEPT_BODY",BODY,{"disambiguationData":[OSD([sQuery(id+"F0.wireOp",EDGE,"E2.bottom"),sQuery(id+"F0.wireOp",EDGE,"E2.top"),sQuery(id+"F0.wireOp",EDGE,"E2.left"),sQuery(id+"F0.wireOp",EDGE,"E2.right")])]}),"instanceName":"1"}),"instanceName":"1"}),"instanceName":"1"});
            var Q81;
            Q81=makeQuery(id+"F9.opPattern","COPY",BODY,{"derivedFrom":makeQuery(id+"F4.opPattern","COPY",BODY,{"derivedFrom":makeQuery(id+"F3.opPattern","COPY",BODY,{"derivedFrom":makeQuery(id+"F2.opPattern","COPY",BODY,{"derivedFrom":makeQuery(id+"F1.opExtrude","SWEPT_BODY",BODY,{"disambiguationData":[OSD([sQuery(id+"F0.wireOp",EDGE,"E0.bottom"),sQuery(id+"F0.wireOp",EDGE,"E0.top"),sQuery(id+"F0.wireOp",EDGE,"E0.left"),sQuery(id+"F0.wireOp",EDGE,"E0.right")])]}),"instanceName":"1"}),"instanceName":"1"}),"instanceName":"1"}),"instanceName":"1"});
            var Q82;
            Q82=makeQuery(id+"F9.opPattern","COPY",BODY,{"derivedFrom":makeQuery(id+"F4.opPattern","COPY",BODY,{"derivedFrom":makeQuery(id+"F3.opPattern","COPY",BODY,{"derivedFrom":makeQuery(id+"F2.opPattern","COPY",BODY,{"derivedFrom":makeQuery(id+"F1.opExtrude","SWEPT_BODY",BODY,{"disambiguationData":[OSD([sQuery(id+"F0.wireOp",EDGE,"E1.bottom"),sQuery(id+"F0.wireOp",EDGE,"E1.top"),sQuery(id+"F0.wireOp",EDGE,"E1.left"),sQuery(id+"F0.wireOp",EDGE,"E1.right")])]}),"instanceName":"1"}),"instanceName":"1"}),"instanceName":"1"}),"instanceName":"1"});
            var Q83;
            Q83=makeQuery(id+"F9.opPattern","COPY",BODY,{"derivedFrom":makeQuery(id+"F4.opPattern","COPY",BODY,{"derivedFrom":makeQuery(id+"F3.opPattern","COPY",BODY,{"derivedFrom":makeQuery(id+"F2.opPattern","COPY",BODY,{"derivedFrom":makeQuery(id+"F1.opExtrude","SWEPT_BODY",BODY,{"disambiguationData":[OSD([sQuery(id+"F0.wireOp",EDGE,"E2.bottom"),sQuery(id+"F0.wireOp",EDGE,"E2.top"),sQuery(id+"F0.wireOp",EDGE,"E2.left"),sQuery(id+"F0.wireOp",EDGE,"E2.right")])]}),"instanceName":"1"}),"instanceName":"1"}),"instanceName":"1"}),"instanceName":"1"});
            var Q84;
            Q84=makeQuery(id+"F9.opPattern","COPY",BODY,{"derivedFrom":makeQuery(id+"F5.opPattern","COPY",BODY,{"derivedFrom":makeQuery(id+"F4.opPattern","COPY",BODY,{"derivedFrom":makeQuery(id+"F3.opPattern","COPY",BODY,{"derivedFrom":makeQuery(id+"F2.opPattern","COPY",BODY,{"derivedFrom":makeQuery(id+"F1.opExtrude","SWEPT_BODY",BODY,{"disambiguationData":[OSD([sQuery(id+"F0.wireOp",EDGE,"E0.bottom"),sQuery(id+"F0.wireOp",EDGE,"E0.top"),sQuery(id+"F0.wireOp",EDGE,"E0.left"),sQuery(id+"F0.wireOp",EDGE,"E0.right")])]}),"instanceName":"1"}),"instanceName":"1"}),"instanceName":"1"}),"instanceName":"1"}),"instanceName":"1"});
            var Q85;
            Q85=makeQuery(id+"F9.opPattern","COPY",BODY,{"derivedFrom":makeQuery(id+"F5.opPattern","COPY",BODY,{"derivedFrom":makeQuery(id+"F4.opPattern","COPY",BODY,{"derivedFrom":makeQuery(id+"F3.opPattern","COPY",BODY,{"derivedFrom":makeQuery(id+"F2.opPattern","COPY",BODY,{"derivedFrom":makeQuery(id+"F1.opExtrude","SWEPT_BODY",BODY,{"disambiguationData":[OSD([sQuery(id+"F0.wireOp",EDGE,"E1.bottom"),sQuery(id+"F0.wireOp",EDGE,"E1.top"),sQuery(id+"F0.wireOp",EDGE,"E1.left"),sQuery(id+"F0.wireOp",EDGE,"E1.right")])]}),"instanceName":"1"}),"instanceName":"1"}),"instanceName":"1"}),"instanceName":"1"}),"instanceName":"1"});
            var Q86;
            Q86=makeQuery(id+"F9.opPattern","COPY",BODY,{"derivedFrom":makeQuery(id+"F5.opPattern","COPY",BODY,{"derivedFrom":makeQuery(id+"F4.opPattern","COPY",BODY,{"derivedFrom":makeQuery(id+"F3.opPattern","COPY",BODY,{"derivedFrom":makeQuery(id+"F2.opPattern","COPY",BODY,{"derivedFrom":makeQuery(id+"F1.opExtrude","SWEPT_BODY",BODY,{"disambiguationData":[OSD([sQuery(id+"F0.wireOp",EDGE,"E2.bottom"),sQuery(id+"F0.wireOp",EDGE,"E2.top"),sQuery(id+"F0.wireOp",EDGE,"E2.left"),sQuery(id+"F0.wireOp",EDGE,"E2.right")])]}),"instanceName":"1"}),"instanceName":"1"}),"instanceName":"1"}),"instanceName":"1"}),"instanceName":"1"});
            var Q87;
            Q87=makeQuery(id+"F9.opPattern","COPY",BODY,{"derivedFrom":makeQuery(id+"F6.opPattern","COPY",BODY,{"derivedFrom":makeQuery(id+"F5.opPattern","COPY",BODY,{"derivedFrom":makeQuery(id+"F4.opPattern","COPY",BODY,{"derivedFrom":makeQuery(id+"F3.opPattern","COPY",BODY,{"derivedFrom":makeQuery(id+"F2.opPattern","COPY",BODY,{"derivedFrom":makeQuery(id+"F1.opExtrude","SWEPT_BODY",BODY,{"disambiguationData":[OSD([sQuery(id+"F0.wireOp",EDGE,"E0.bottom"),sQuery(id+"F0.wireOp",EDGE,"E0.top"),sQuery(id+"F0.wireOp",EDGE,"E0.left"),sQuery(id+"F0.wireOp",EDGE,"E0.right")])]}),"instanceName":"1"}),"instanceName":"1"}),"instanceName":"1"}),"instanceName":"1"}),"instanceName":"1"}),"instanceName":"1"});
            var Q88;
            Q88=makeQuery(id+"F9.opPattern","COPY",BODY,{"derivedFrom":makeQuery(id+"F6.opPattern","COPY",BODY,{"derivedFrom":makeQuery(id+"F5.opPattern","COPY",BODY,{"derivedFrom":makeQuery(id+"F4.opPattern","COPY",BODY,{"derivedFrom":makeQuery(id+"F3.opPattern","COPY",BODY,{"derivedFrom":makeQuery(id+"F2.opPattern","COPY",BODY,{"derivedFrom":makeQuery(id+"F1.opExtrude","SWEPT_BODY",BODY,{"disambiguationData":[OSD([sQuery(id+"F0.wireOp",EDGE,"E1.bottom"),sQuery(id+"F0.wireOp",EDGE,"E1.top"),sQuery(id+"F0.wireOp",EDGE,"E1.left"),sQuery(id+"F0.wireOp",EDGE,"E1.right")])]}),"instanceName":"1"}),"instanceName":"1"}),"instanceName":"1"}),"instanceName":"1"}),"instanceName":"1"}),"instanceName":"1"});
            var Q89;
            Q89=makeQuery(id+"F9.opPattern","COPY",BODY,{"derivedFrom":makeQuery(id+"F6.opPattern","COPY",BODY,{"derivedFrom":makeQuery(id+"F5.opPattern","COPY",BODY,{"derivedFrom":makeQuery(id+"F4.opPattern","COPY",BODY,{"derivedFrom":makeQuery(id+"F3.opPattern","COPY",BODY,{"derivedFrom":makeQuery(id+"F2.opPattern","COPY",BODY,{"derivedFrom":makeQuery(id+"F1.opExtrude","SWEPT_BODY",BODY,{"disambiguationData":[OSD([sQuery(id+"F0.wireOp",EDGE,"E2.bottom"),sQuery(id+"F0.wireOp",EDGE,"E2.top"),sQuery(id+"F0.wireOp",EDGE,"E2.left"),sQuery(id+"F0.wireOp",EDGE,"E2.right")])]}),"instanceName":"1"}),"instanceName":"1"}),"instanceName":"1"}),"instanceName":"1"}),"instanceName":"1"}),"instanceName":"1"});
            var Q90;
            Q90=makeQuery(id+"F9.opPattern","COPY",BODY,{"derivedFrom":makeQuery(id+"F7.opPattern","COPY",BODY,{"derivedFrom":makeQuery(id+"F1.opExtrude","SWEPT_BODY",BODY,{"disambiguationData":[OSD([sQuery(id+"F0.wireOp",EDGE,"E0.bottom"),sQuery(id+"F0.wireOp",EDGE,"E0.top"),sQuery(id+"F0.wireOp",EDGE,"E0.left"),sQuery(id+"F0.wireOp",EDGE,"E0.right")])]}),"instanceName":"1"}),"instanceName":"1"});
            var Q91;
            Q91=makeQuery(id+"F9.opPattern","COPY",BODY,{"derivedFrom":makeQuery(id+"F7.opPattern","COPY",BODY,{"derivedFrom":makeQuery(id+"F1.opExtrude","SWEPT_BODY",BODY,{"disambiguationData":[OSD([sQuery(id+"F0.wireOp",EDGE,"E1.bottom"),sQuery(id+"F0.wireOp",EDGE,"E1.top"),sQuery(id+"F0.wireOp",EDGE,"E1.left"),sQuery(id+"F0.wireOp",EDGE,"E1.right")])]}),"instanceName":"1"}),"instanceName":"1"});
            var Q92;
            Q92=makeQuery(id+"F9.opPattern","COPY",BODY,{"derivedFrom":makeQuery(id+"F7.opPattern","COPY",BODY,{"derivedFrom":makeQuery(id+"F1.opExtrude","SWEPT_BODY",BODY,{"disambiguationData":[OSD([sQuery(id+"F0.wireOp",EDGE,"E2.bottom"),sQuery(id+"F0.wireOp",EDGE,"E2.top"),sQuery(id+"F0.wireOp",EDGE,"E2.left"),sQuery(id+"F0.wireOp",EDGE,"E2.right")])]}),"instanceName":"1"}),"instanceName":"1"});
            var Q93;
            Q93=makeQuery(id+"F9.opPattern","COPY",BODY,{"derivedFrom":makeQuery(id+"F7.opPattern","COPY",BODY,{"derivedFrom":makeQuery(id+"F2.opPattern","COPY",BODY,{"derivedFrom":makeQuery(id+"F1.opExtrude","SWEPT_BODY",BODY,{"disambiguationData":[OSD([sQuery(id+"F0.wireOp",EDGE,"E0.bottom"),sQuery(id+"F0.wireOp",EDGE,"E0.top"),sQuery(id+"F0.wireOp",EDGE,"E0.left"),sQuery(id+"F0.wireOp",EDGE,"E0.right")])]}),"instanceName":"1"}),"instanceName":"1"}),"instanceName":"1"});
            var Q94;
            Q94=makeQuery(id+"F9.opPattern","COPY",BODY,{"derivedFrom":makeQuery(id+"F7.opPattern","COPY",BODY,{"derivedFrom":makeQuery(id+"F2.opPattern","COPY",BODY,{"derivedFrom":makeQuery(id+"F1.opExtrude","SWEPT_BODY",BODY,{"disambiguationData":[OSD([sQuery(id+"F0.wireOp",EDGE,"E1.bottom"),sQuery(id+"F0.wireOp",EDGE,"E1.top"),sQuery(id+"F0.wireOp",EDGE,"E1.left"),sQuery(id+"F0.wireOp",EDGE,"E1.right")])]}),"instanceName":"1"}),"instanceName":"1"}),"instanceName":"1"});
            var Q95;
            Q95=makeQuery(id+"F9.opPattern","COPY",BODY,{"derivedFrom":makeQuery(id+"F7.opPattern","COPY",BODY,{"derivedFrom":makeQuery(id+"F2.opPattern","COPY",BODY,{"derivedFrom":makeQuery(id+"F1.opExtrude","SWEPT_BODY",BODY,{"disambiguationData":[OSD([sQuery(id+"F0.wireOp",EDGE,"E2.bottom"),sQuery(id+"F0.wireOp",EDGE,"E2.top"),sQuery(id+"F0.wireOp",EDGE,"E2.left"),sQuery(id+"F0.wireOp",EDGE,"E2.right")])]}),"instanceName":"1"}),"instanceName":"1"}),"instanceName":"1"});
            var Q96;
            Q96=makeQuery(id+"F9.opPattern","COPY",BODY,{"derivedFrom":makeQuery(id+"F7.opPattern","COPY",BODY,{"derivedFrom":makeQuery(id+"F3.opPattern","COPY",BODY,{"derivedFrom":makeQuery(id+"F2.opPattern","COPY",BODY,{"derivedFrom":makeQuery(id+"F1.opExtrude","SWEPT_BODY",BODY,{"disambiguationData":[OSD([sQuery(id+"F0.wireOp",EDGE,"E0.bottom"),sQuery(id+"F0.wireOp",EDGE,"E0.top"),sQuery(id+"F0.wireOp",EDGE,"E0.left"),sQuery(id+"F0.wireOp",EDGE,"E0.right")])]}),"instanceName":"1"}),"instanceName":"1"}),"instanceName":"1"}),"instanceName":"1"});
            var Q97;
            Q97=makeQuery(id+"F9.opPattern","COPY",BODY,{"derivedFrom":makeQuery(id+"F7.opPattern","COPY",BODY,{"derivedFrom":makeQuery(id+"F3.opPattern","COPY",BODY,{"derivedFrom":makeQuery(id+"F2.opPattern","COPY",BODY,{"derivedFrom":makeQuery(id+"F1.opExtrude","SWEPT_BODY",BODY,{"disambiguationData":[OSD([sQuery(id+"F0.wireOp",EDGE,"E1.bottom"),sQuery(id+"F0.wireOp",EDGE,"E1.top"),sQuery(id+"F0.wireOp",EDGE,"E1.left"),sQuery(id+"F0.wireOp",EDGE,"E1.right")])]}),"instanceName":"1"}),"instanceName":"1"}),"instanceName":"1"}),"instanceName":"1"});
            var Q98;
            Q98=makeQuery(id+"F9.opPattern","COPY",BODY,{"derivedFrom":makeQuery(id+"F7.opPattern","COPY",BODY,{"derivedFrom":makeQuery(id+"F3.opPattern","COPY",BODY,{"derivedFrom":makeQuery(id+"F2.opPattern","COPY",BODY,{"derivedFrom":makeQuery(id+"F1.opExtrude","SWEPT_BODY",BODY,{"disambiguationData":[OSD([sQuery(id+"F0.wireOp",EDGE,"E2.bottom"),sQuery(id+"F0.wireOp",EDGE,"E2.top"),sQuery(id+"F0.wireOp",EDGE,"E2.left"),sQuery(id+"F0.wireOp",EDGE,"E2.right")])]}),"instanceName":"1"}),"instanceName":"1"}),"instanceName":"1"}),"instanceName":"1"});
            var Q99;
            Q99=makeQuery(id+"F9.opPattern","COPY",BODY,{"derivedFrom":makeQuery(id+"F7.opPattern","COPY",BODY,{"derivedFrom":makeQuery(id+"F4.opPattern","COPY",BODY,{"derivedFrom":makeQuery(id+"F3.opPattern","COPY",BODY,{"derivedFrom":makeQuery(id+"F2.opPattern","COPY",BODY,{"derivedFrom":makeQuery(id+"F1.opExtrude","SWEPT_BODY",BODY,{"disambiguationData":[OSD([sQuery(id+"F0.wireOp",EDGE,"E0.bottom"),sQuery(id+"F0.wireOp",EDGE,"E0.top"),sQuery(id+"F0.wireOp",EDGE,"E0.left"),sQuery(id+"F0.wireOp",EDGE,"E0.right")])]}),"instanceName":"1"}),"instanceName":"1"}),"instanceName":"1"}),"instanceName":"1"}),"instanceName":"1"});
            var Q100;
            Q100=makeQuery(id+"F9.opPattern","COPY",BODY,{"derivedFrom":makeQuery(id+"F7.opPattern","COPY",BODY,{"derivedFrom":makeQuery(id+"F4.opPattern","COPY",BODY,{"derivedFrom":makeQuery(id+"F3.opPattern","COPY",BODY,{"derivedFrom":makeQuery(id+"F2.opPattern","COPY",BODY,{"derivedFrom":makeQuery(id+"F1.opExtrude","SWEPT_BODY",BODY,{"disambiguationData":[OSD([sQuery(id+"F0.wireOp",EDGE,"E1.bottom"),sQuery(id+"F0.wireOp",EDGE,"E1.top"),sQuery(id+"F0.wireOp",EDGE,"E1.left"),sQuery(id+"F0.wireOp",EDGE,"E1.right")])]}),"instanceName":"1"}),"instanceName":"1"}),"instanceName":"1"}),"instanceName":"1"}),"instanceName":"1"});
            var Q101;
            Q101=makeQuery(id+"F9.opPattern","COPY",BODY,{"derivedFrom":makeQuery(id+"F7.opPattern","COPY",BODY,{"derivedFrom":makeQuery(id+"F4.opPattern","COPY",BODY,{"derivedFrom":makeQuery(id+"F3.opPattern","COPY",BODY,{"derivedFrom":makeQuery(id+"F2.opPattern","COPY",BODY,{"derivedFrom":makeQuery(id+"F1.opExtrude","SWEPT_BODY",BODY,{"disambiguationData":[OSD([sQuery(id+"F0.wireOp",EDGE,"E2.bottom"),sQuery(id+"F0.wireOp",EDGE,"E2.top"),sQuery(id+"F0.wireOp",EDGE,"E2.left"),sQuery(id+"F0.wireOp",EDGE,"E2.right")])]}),"instanceName":"1"}),"instanceName":"1"}),"instanceName":"1"}),"instanceName":"1"}),"instanceName":"1"});
            var Q102;
            Q102=makeQuery(id+"F9.opPattern","COPY",BODY,{"derivedFrom":makeQuery(id+"F7.opPattern","COPY",BODY,{"derivedFrom":makeQuery(id+"F5.opPattern","COPY",BODY,{"derivedFrom":makeQuery(id+"F4.opPattern","COPY",BODY,{"derivedFrom":makeQuery(id+"F3.opPattern","COPY",BODY,{"derivedFrom":makeQuery(id+"F2.opPattern","COPY",BODY,{"derivedFrom":makeQuery(id+"F1.opExtrude","SWEPT_BODY",BODY,{"disambiguationData":[OSD([sQuery(id+"F0.wireOp",EDGE,"E0.bottom"),sQuery(id+"F0.wireOp",EDGE,"E0.top"),sQuery(id+"F0.wireOp",EDGE,"E0.left"),sQuery(id+"F0.wireOp",EDGE,"E0.right")])]}),"instanceName":"1"}),"instanceName":"1"}),"instanceName":"1"}),"instanceName":"1"}),"instanceName":"1"}),"instanceName":"1"});
            var Q103;
            Q103=makeQuery(id+"F9.opPattern","COPY",BODY,{"derivedFrom":makeQuery(id+"F7.opPattern","COPY",BODY,{"derivedFrom":makeQuery(id+"F5.opPattern","COPY",BODY,{"derivedFrom":makeQuery(id+"F4.opPattern","COPY",BODY,{"derivedFrom":makeQuery(id+"F3.opPattern","COPY",BODY,{"derivedFrom":makeQuery(id+"F2.opPattern","COPY",BODY,{"derivedFrom":makeQuery(id+"F1.opExtrude","SWEPT_BODY",BODY,{"disambiguationData":[OSD([sQuery(id+"F0.wireOp",EDGE,"E1.bottom"),sQuery(id+"F0.wireOp",EDGE,"E1.top"),sQuery(id+"F0.wireOp",EDGE,"E1.left"),sQuery(id+"F0.wireOp",EDGE,"E1.right")])]}),"instanceName":"1"}),"instanceName":"1"}),"instanceName":"1"}),"instanceName":"1"}),"instanceName":"1"}),"instanceName":"1"});
            var Q104;
            Q104=makeQuery(id+"F9.opPattern","COPY",BODY,{"derivedFrom":makeQuery(id+"F7.opPattern","COPY",BODY,{"derivedFrom":makeQuery(id+"F5.opPattern","COPY",BODY,{"derivedFrom":makeQuery(id+"F4.opPattern","COPY",BODY,{"derivedFrom":makeQuery(id+"F3.opPattern","COPY",BODY,{"derivedFrom":makeQuery(id+"F2.opPattern","COPY",BODY,{"derivedFrom":makeQuery(id+"F1.opExtrude","SWEPT_BODY",BODY,{"disambiguationData":[OSD([sQuery(id+"F0.wireOp",EDGE,"E2.bottom"),sQuery(id+"F0.wireOp",EDGE,"E2.top"),sQuery(id+"F0.wireOp",EDGE,"E2.left"),sQuery(id+"F0.wireOp",EDGE,"E2.right")])]}),"instanceName":"1"}),"instanceName":"1"}),"instanceName":"1"}),"instanceName":"1"}),"instanceName":"1"}),"instanceName":"1"});
            var Q105;
            Q105=makeQuery(id+"F9.opPattern","COPY",BODY,{"derivedFrom":makeQuery(id+"F7.opPattern","COPY",BODY,{"derivedFrom":makeQuery(id+"F6.opPattern","COPY",BODY,{"derivedFrom":makeQuery(id+"F5.opPattern","COPY",BODY,{"derivedFrom":makeQuery(id+"F4.opPattern","COPY",BODY,{"derivedFrom":makeQuery(id+"F3.opPattern","COPY",BODY,{"derivedFrom":makeQuery(id+"F2.opPattern","COPY",BODY,{"derivedFrom":makeQuery(id+"F1.opExtrude","SWEPT_BODY",BODY,{"disambiguationData":[OSD([sQuery(id+"F0.wireOp",EDGE,"E0.bottom"),sQuery(id+"F0.wireOp",EDGE,"E0.top"),sQuery(id+"F0.wireOp",EDGE,"E0.left"),sQuery(id+"F0.wireOp",EDGE,"E0.right")])]}),"instanceName":"1"}),"instanceName":"1"}),"instanceName":"1"}),"instanceName":"1"}),"instanceName":"1"}),"instanceName":"1"}),"instanceName":"1"});
            var Q106;
            Q106=makeQuery(id+"F9.opPattern","COPY",BODY,{"derivedFrom":makeQuery(id+"F7.opPattern","COPY",BODY,{"derivedFrom":makeQuery(id+"F6.opPattern","COPY",BODY,{"derivedFrom":makeQuery(id+"F5.opPattern","COPY",BODY,{"derivedFrom":makeQuery(id+"F4.opPattern","COPY",BODY,{"derivedFrom":makeQuery(id+"F3.opPattern","COPY",BODY,{"derivedFrom":makeQuery(id+"F2.opPattern","COPY",BODY,{"derivedFrom":makeQuery(id+"F1.opExtrude","SWEPT_BODY",BODY,{"disambiguationData":[OSD([sQuery(id+"F0.wireOp",EDGE,"E1.bottom"),sQuery(id+"F0.wireOp",EDGE,"E1.top"),sQuery(id+"F0.wireOp",EDGE,"E1.left"),sQuery(id+"F0.wireOp",EDGE,"E1.right")])]}),"instanceName":"1"}),"instanceName":"1"}),"instanceName":"1"}),"instanceName":"1"}),"instanceName":"1"}),"instanceName":"1"}),"instanceName":"1"});
            var Q107;
            Q107=makeQuery(id+"F9.opPattern","COPY",BODY,{"derivedFrom":makeQuery(id+"F7.opPattern","COPY",BODY,{"derivedFrom":makeQuery(id+"F6.opPattern","COPY",BODY,{"derivedFrom":makeQuery(id+"F5.opPattern","COPY",BODY,{"derivedFrom":makeQuery(id+"F4.opPattern","COPY",BODY,{"derivedFrom":makeQuery(id+"F3.opPattern","COPY",BODY,{"derivedFrom":makeQuery(id+"F2.opPattern","COPY",BODY,{"derivedFrom":makeQuery(id+"F1.opExtrude","SWEPT_BODY",BODY,{"disambiguationData":[OSD([sQuery(id+"F0.wireOp",EDGE,"E2.bottom"),sQuery(id+"F0.wireOp",EDGE,"E2.top"),sQuery(id+"F0.wireOp",EDGE,"E2.left"),sQuery(id+"F0.wireOp",EDGE,"E2.right")])]}),"instanceName":"1"}),"instanceName":"1"}),"instanceName":"1"}),"instanceName":"1"}),"instanceName":"1"}),"instanceName":"1"}),"instanceName":"1"});
            var Q108;
            Q108=makeQuery(id+"F9.opPattern","COPY",BODY,{"derivedFrom":makeQuery(id+"F8.opPattern","COPY",BODY,{"derivedFrom":makeQuery(id+"F1.opExtrude","SWEPT_BODY",BODY,{"disambiguationData":[OSD([sQuery(id+"F0.wireOp",EDGE,"E0.bottom"),sQuery(id+"F0.wireOp",EDGE,"E0.top"),sQuery(id+"F0.wireOp",EDGE,"E0.left"),sQuery(id+"F0.wireOp",EDGE,"E0.right")])]}),"instanceName":"1"}),"instanceName":"1"});
            var Q109;
            Q109=makeQuery(id+"F9.opPattern","COPY",BODY,{"derivedFrom":makeQuery(id+"F8.opPattern","COPY",BODY,{"derivedFrom":makeQuery(id+"F1.opExtrude","SWEPT_BODY",BODY,{"disambiguationData":[OSD([sQuery(id+"F0.wireOp",EDGE,"E1.bottom"),sQuery(id+"F0.wireOp",EDGE,"E1.top"),sQuery(id+"F0.wireOp",EDGE,"E1.left"),sQuery(id+"F0.wireOp",EDGE,"E1.right")])]}),"instanceName":"1"}),"instanceName":"1"});
            var Q110;
            Q110=makeQuery(id+"F9.opPattern","COPY",BODY,{"derivedFrom":makeQuery(id+"F8.opPattern","COPY",BODY,{"derivedFrom":makeQuery(id+"F1.opExtrude","SWEPT_BODY",BODY,{"disambiguationData":[OSD([sQuery(id+"F0.wireOp",EDGE,"E2.bottom"),sQuery(id+"F0.wireOp",EDGE,"E2.top"),sQuery(id+"F0.wireOp",EDGE,"E2.left"),sQuery(id+"F0.wireOp",EDGE,"E2.right")])]}),"instanceName":"1"}),"instanceName":"1"});
            var Q111;
            Q111=makeQuery(id+"F9.opPattern","COPY",BODY,{"derivedFrom":makeQuery(id+"F8.opPattern","COPY",BODY,{"derivedFrom":makeQuery(id+"F2.opPattern","COPY",BODY,{"derivedFrom":makeQuery(id+"F1.opExtrude","SWEPT_BODY",BODY,{"disambiguationData":[OSD([sQuery(id+"F0.wireOp",EDGE,"E0.bottom"),sQuery(id+"F0.wireOp",EDGE,"E0.top"),sQuery(id+"F0.wireOp",EDGE,"E0.left"),sQuery(id+"F0.wireOp",EDGE,"E0.right")])]}),"instanceName":"1"}),"instanceName":"1"}),"instanceName":"1"});
            var Q112;
            Q112=makeQuery(id+"F9.opPattern","COPY",BODY,{"derivedFrom":makeQuery(id+"F8.opPattern","COPY",BODY,{"derivedFrom":makeQuery(id+"F2.opPattern","COPY",BODY,{"derivedFrom":makeQuery(id+"F1.opExtrude","SWEPT_BODY",BODY,{"disambiguationData":[OSD([sQuery(id+"F0.wireOp",EDGE,"E1.bottom"),sQuery(id+"F0.wireOp",EDGE,"E1.top"),sQuery(id+"F0.wireOp",EDGE,"E1.left"),sQuery(id+"F0.wireOp",EDGE,"E1.right")])]}),"instanceName":"1"}),"instanceName":"1"}),"instanceName":"1"});
            var Q113;
            Q113=makeQuery(id+"F9.opPattern","COPY",BODY,{"derivedFrom":makeQuery(id+"F8.opPattern","COPY",BODY,{"derivedFrom":makeQuery(id+"F2.opPattern","COPY",BODY,{"derivedFrom":makeQuery(id+"F1.opExtrude","SWEPT_BODY",BODY,{"disambiguationData":[OSD([sQuery(id+"F0.wireOp",EDGE,"E2.bottom"),sQuery(id+"F0.wireOp",EDGE,"E2.top"),sQuery(id+"F0.wireOp",EDGE,"E2.left"),sQuery(id+"F0.wireOp",EDGE,"E2.right")])]}),"instanceName":"1"}),"instanceName":"1"}),"instanceName":"1"});
            var Q114;
            Q114=makeQuery(id+"F9.opPattern","COPY",BODY,{"derivedFrom":makeQuery(id+"F8.opPattern","COPY",BODY,{"derivedFrom":makeQuery(id+"F3.opPattern","COPY",BODY,{"derivedFrom":makeQuery(id+"F2.opPattern","COPY",BODY,{"derivedFrom":makeQuery(id+"F1.opExtrude","SWEPT_BODY",BODY,{"disambiguationData":[OSD([sQuery(id+"F0.wireOp",EDGE,"E0.bottom"),sQuery(id+"F0.wireOp",EDGE,"E0.top"),sQuery(id+"F0.wireOp",EDGE,"E0.left"),sQuery(id+"F0.wireOp",EDGE,"E0.right")])]}),"instanceName":"1"}),"instanceName":"1"}),"instanceName":"1"}),"instanceName":"1"});
            var Q115;
            Q115=makeQuery(id+"F9.opPattern","COPY",BODY,{"derivedFrom":makeQuery(id+"F8.opPattern","COPY",BODY,{"derivedFrom":makeQuery(id+"F3.opPattern","COPY",BODY,{"derivedFrom":makeQuery(id+"F2.opPattern","COPY",BODY,{"derivedFrom":makeQuery(id+"F1.opExtrude","SWEPT_BODY",BODY,{"disambiguationData":[OSD([sQuery(id+"F0.wireOp",EDGE,"E1.bottom"),sQuery(id+"F0.wireOp",EDGE,"E1.top"),sQuery(id+"F0.wireOp",EDGE,"E1.left"),sQuery(id+"F0.wireOp",EDGE,"E1.right")])]}),"instanceName":"1"}),"instanceName":"1"}),"instanceName":"1"}),"instanceName":"1"});
            var Q116;
            Q116=makeQuery(id+"F9.opPattern","COPY",BODY,{"derivedFrom":makeQuery(id+"F8.opPattern","COPY",BODY,{"derivedFrom":makeQuery(id+"F3.opPattern","COPY",BODY,{"derivedFrom":makeQuery(id+"F2.opPattern","COPY",BODY,{"derivedFrom":makeQuery(id+"F1.opExtrude","SWEPT_BODY",BODY,{"disambiguationData":[OSD([sQuery(id+"F0.wireOp",EDGE,"E2.bottom"),sQuery(id+"F0.wireOp",EDGE,"E2.top"),sQuery(id+"F0.wireOp",EDGE,"E2.left"),sQuery(id+"F0.wireOp",EDGE,"E2.right")])]}),"instanceName":"1"}),"instanceName":"1"}),"instanceName":"1"}),"instanceName":"1"});
            var Q117;
            Q117=makeQuery(id+"F9.opPattern","COPY",BODY,{"derivedFrom":makeQuery(id+"F8.opPattern","COPY",BODY,{"derivedFrom":makeQuery(id+"F4.opPattern","COPY",BODY,{"derivedFrom":makeQuery(id+"F3.opPattern","COPY",BODY,{"derivedFrom":makeQuery(id+"F2.opPattern","COPY",BODY,{"derivedFrom":makeQuery(id+"F1.opExtrude","SWEPT_BODY",BODY,{"disambiguationData":[OSD([sQuery(id+"F0.wireOp",EDGE,"E0.bottom"),sQuery(id+"F0.wireOp",EDGE,"E0.top"),sQuery(id+"F0.wireOp",EDGE,"E0.left"),sQuery(id+"F0.wireOp",EDGE,"E0.right")])]}),"instanceName":"1"}),"instanceName":"1"}),"instanceName":"1"}),"instanceName":"1"}),"instanceName":"1"});
            var Q118;
            Q118=makeQuery(id+"F9.opPattern","COPY",BODY,{"derivedFrom":makeQuery(id+"F8.opPattern","COPY",BODY,{"derivedFrom":makeQuery(id+"F4.opPattern","COPY",BODY,{"derivedFrom":makeQuery(id+"F3.opPattern","COPY",BODY,{"derivedFrom":makeQuery(id+"F2.opPattern","COPY",BODY,{"derivedFrom":makeQuery(id+"F1.opExtrude","SWEPT_BODY",BODY,{"disambiguationData":[OSD([sQuery(id+"F0.wireOp",EDGE,"E1.bottom"),sQuery(id+"F0.wireOp",EDGE,"E1.top"),sQuery(id+"F0.wireOp",EDGE,"E1.left"),sQuery(id+"F0.wireOp",EDGE,"E1.right")])]}),"instanceName":"1"}),"instanceName":"1"}),"instanceName":"1"}),"instanceName":"1"}),"instanceName":"1"});
            var Q119;
            Q119=makeQuery(id+"F9.opPattern","COPY",BODY,{"derivedFrom":makeQuery(id+"F8.opPattern","COPY",BODY,{"derivedFrom":makeQuery(id+"F4.opPattern","COPY",BODY,{"derivedFrom":makeQuery(id+"F3.opPattern","COPY",BODY,{"derivedFrom":makeQuery(id+"F2.opPattern","COPY",BODY,{"derivedFrom":makeQuery(id+"F1.opExtrude","SWEPT_BODY",BODY,{"disambiguationData":[OSD([sQuery(id+"F0.wireOp",EDGE,"E2.bottom"),sQuery(id+"F0.wireOp",EDGE,"E2.top"),sQuery(id+"F0.wireOp",EDGE,"E2.left"),sQuery(id+"F0.wireOp",EDGE,"E2.right")])]}),"instanceName":"1"}),"instanceName":"1"}),"instanceName":"1"}),"instanceName":"1"}),"instanceName":"1"});
            var Q120;
            Q120=makeQuery(id+"F9.opPattern","COPY",BODY,{"derivedFrom":makeQuery(id+"F8.opPattern","COPY",BODY,{"derivedFrom":makeQuery(id+"F5.opPattern","COPY",BODY,{"derivedFrom":makeQuery(id+"F4.opPattern","COPY",BODY,{"derivedFrom":makeQuery(id+"F3.opPattern","COPY",BODY,{"derivedFrom":makeQuery(id+"F2.opPattern","COPY",BODY,{"derivedFrom":makeQuery(id+"F1.opExtrude","SWEPT_BODY",BODY,{"disambiguationData":[OSD([sQuery(id+"F0.wireOp",EDGE,"E0.bottom"),sQuery(id+"F0.wireOp",EDGE,"E0.top"),sQuery(id+"F0.wireOp",EDGE,"E0.left"),sQuery(id+"F0.wireOp",EDGE,"E0.right")])]}),"instanceName":"1"}),"instanceName":"1"}),"instanceName":"1"}),"instanceName":"1"}),"instanceName":"1"}),"instanceName":"1"});
            var Q121;
            Q121=makeQuery(id+"F9.opPattern","COPY",BODY,{"derivedFrom":makeQuery(id+"F8.opPattern","COPY",BODY,{"derivedFrom":makeQuery(id+"F5.opPattern","COPY",BODY,{"derivedFrom":makeQuery(id+"F4.opPattern","COPY",BODY,{"derivedFrom":makeQuery(id+"F3.opPattern","COPY",BODY,{"derivedFrom":makeQuery(id+"F2.opPattern","COPY",BODY,{"derivedFrom":makeQuery(id+"F1.opExtrude","SWEPT_BODY",BODY,{"disambiguationData":[OSD([sQuery(id+"F0.wireOp",EDGE,"E1.bottom"),sQuery(id+"F0.wireOp",EDGE,"E1.top"),sQuery(id+"F0.wireOp",EDGE,"E1.left"),sQuery(id+"F0.wireOp",EDGE,"E1.right")])]}),"instanceName":"1"}),"instanceName":"1"}),"instanceName":"1"}),"instanceName":"1"}),"instanceName":"1"}),"instanceName":"1"});
            var Q122;
            Q122=makeQuery(id+"F9.opPattern","COPY",BODY,{"derivedFrom":makeQuery(id+"F8.opPattern","COPY",BODY,{"derivedFrom":makeQuery(id+"F5.opPattern","COPY",BODY,{"derivedFrom":makeQuery(id+"F4.opPattern","COPY",BODY,{"derivedFrom":makeQuery(id+"F3.opPattern","COPY",BODY,{"derivedFrom":makeQuery(id+"F2.opPattern","COPY",BODY,{"derivedFrom":makeQuery(id+"F1.opExtrude","SWEPT_BODY",BODY,{"disambiguationData":[OSD([sQuery(id+"F0.wireOp",EDGE,"E2.bottom"),sQuery(id+"F0.wireOp",EDGE,"E2.top"),sQuery(id+"F0.wireOp",EDGE,"E2.left"),sQuery(id+"F0.wireOp",EDGE,"E2.right")])]}),"instanceName":"1"}),"instanceName":"1"}),"instanceName":"1"}),"instanceName":"1"}),"instanceName":"1"}),"instanceName":"1"});
            var Q123;
            Q123=makeQuery(id+"F9.opPattern","COPY",BODY,{"derivedFrom":makeQuery(id+"F8.opPattern","COPY",BODY,{"derivedFrom":makeQuery(id+"F6.opPattern","COPY",BODY,{"derivedFrom":makeQuery(id+"F5.opPattern","COPY",BODY,{"derivedFrom":makeQuery(id+"F4.opPattern","COPY",BODY,{"derivedFrom":makeQuery(id+"F3.opPattern","COPY",BODY,{"derivedFrom":makeQuery(id+"F2.opPattern","COPY",BODY,{"derivedFrom":makeQuery(id+"F1.opExtrude","SWEPT_BODY",BODY,{"disambiguationData":[OSD([sQuery(id+"F0.wireOp",EDGE,"E0.bottom"),sQuery(id+"F0.wireOp",EDGE,"E0.top"),sQuery(id+"F0.wireOp",EDGE,"E0.left"),sQuery(id+"F0.wireOp",EDGE,"E0.right")])]}),"instanceName":"1"}),"instanceName":"1"}),"instanceName":"1"}),"instanceName":"1"}),"instanceName":"1"}),"instanceName":"1"}),"instanceName":"1"});
            var Q124;
            Q124=makeQuery(id+"F9.opPattern","COPY",BODY,{"derivedFrom":makeQuery(id+"F8.opPattern","COPY",BODY,{"derivedFrom":makeQuery(id+"F6.opPattern","COPY",BODY,{"derivedFrom":makeQuery(id+"F5.opPattern","COPY",BODY,{"derivedFrom":makeQuery(id+"F4.opPattern","COPY",BODY,{"derivedFrom":makeQuery(id+"F3.opPattern","COPY",BODY,{"derivedFrom":makeQuery(id+"F2.opPattern","COPY",BODY,{"derivedFrom":makeQuery(id+"F1.opExtrude","SWEPT_BODY",BODY,{"disambiguationData":[OSD([sQuery(id+"F0.wireOp",EDGE,"E1.bottom"),sQuery(id+"F0.wireOp",EDGE,"E1.top"),sQuery(id+"F0.wireOp",EDGE,"E1.left"),sQuery(id+"F0.wireOp",EDGE,"E1.right")])]}),"instanceName":"1"}),"instanceName":"1"}),"instanceName":"1"}),"instanceName":"1"}),"instanceName":"1"}),"instanceName":"1"}),"instanceName":"1"});
            var Q125;
            Q125=makeQuery(id+"F9.opPattern","COPY",BODY,{"derivedFrom":makeQuery(id+"F8.opPattern","COPY",BODY,{"derivedFrom":makeQuery(id+"F6.opPattern","COPY",BODY,{"derivedFrom":makeQuery(id+"F5.opPattern","COPY",BODY,{"derivedFrom":makeQuery(id+"F4.opPattern","COPY",BODY,{"derivedFrom":makeQuery(id+"F3.opPattern","COPY",BODY,{"derivedFrom":makeQuery(id+"F2.opPattern","COPY",BODY,{"derivedFrom":makeQuery(id+"F1.opExtrude","SWEPT_BODY",BODY,{"disambiguationData":[OSD([sQuery(id+"F0.wireOp",EDGE,"E2.bottom"),sQuery(id+"F0.wireOp",EDGE,"E2.top"),sQuery(id+"F0.wireOp",EDGE,"E2.left"),sQuery(id+"F0.wireOp",EDGE,"E2.right")])]}),"instanceName":"1"}),"instanceName":"1"}),"instanceName":"1"}),"instanceName":"1"}),"instanceName":"1"}),"instanceName":"1"}),"instanceName":"1"});
            var Q126;
            Q126=makeQuery(id+"F9.opPattern","COPY",BODY,{"derivedFrom":makeQuery(id+"F8.opPattern","COPY",BODY,{"derivedFrom":makeQuery(id+"F7.opPattern","COPY",BODY,{"derivedFrom":makeQuery(id+"F1.opExtrude","SWEPT_BODY",BODY,{"disambiguationData":[OSD([sQuery(id+"F0.wireOp",EDGE,"E0.bottom"),sQuery(id+"F0.wireOp",EDGE,"E0.top"),sQuery(id+"F0.wireOp",EDGE,"E0.left"),sQuery(id+"F0.wireOp",EDGE,"E0.right")])]}),"instanceName":"1"}),"instanceName":"1"}),"instanceName":"1"});
            var Q127;
            Q127=makeQuery(id+"F9.opPattern","COPY",BODY,{"derivedFrom":makeQuery(id+"F8.opPattern","COPY",BODY,{"derivedFrom":makeQuery(id+"F7.opPattern","COPY",BODY,{"derivedFrom":makeQuery(id+"F1.opExtrude","SWEPT_BODY",BODY,{"disambiguationData":[OSD([sQuery(id+"F0.wireOp",EDGE,"E1.bottom"),sQuery(id+"F0.wireOp",EDGE,"E1.top"),sQuery(id+"F0.wireOp",EDGE,"E1.left"),sQuery(id+"F0.wireOp",EDGE,"E1.right")])]}),"instanceName":"1"}),"instanceName":"1"}),"instanceName":"1"});
            var Q128;
            Q128=makeQuery(id+"F9.opPattern","COPY",BODY,{"derivedFrom":makeQuery(id+"F8.opPattern","COPY",BODY,{"derivedFrom":makeQuery(id+"F7.opPattern","COPY",BODY,{"derivedFrom":makeQuery(id+"F1.opExtrude","SWEPT_BODY",BODY,{"disambiguationData":[OSD([sQuery(id+"F0.wireOp",EDGE,"E2.bottom"),sQuery(id+"F0.wireOp",EDGE,"E2.top"),sQuery(id+"F0.wireOp",EDGE,"E2.left"),sQuery(id+"F0.wireOp",EDGE,"E2.right")])]}),"instanceName":"1"}),"instanceName":"1"}),"instanceName":"1"});
            var Q129;
            Q129=makeQuery(id+"F9.opPattern","COPY",BODY,{"derivedFrom":makeQuery(id+"F8.opPattern","COPY",BODY,{"derivedFrom":makeQuery(id+"F7.opPattern","COPY",BODY,{"derivedFrom":makeQuery(id+"F2.opPattern","COPY",BODY,{"derivedFrom":makeQuery(id+"F1.opExtrude","SWEPT_BODY",BODY,{"disambiguationData":[OSD([sQuery(id+"F0.wireOp",EDGE,"E0.bottom"),sQuery(id+"F0.wireOp",EDGE,"E0.top"),sQuery(id+"F0.wireOp",EDGE,"E0.left"),sQuery(id+"F0.wireOp",EDGE,"E0.right")])]}),"instanceName":"1"}),"instanceName":"1"}),"instanceName":"1"}),"instanceName":"1"});
            var Q130;
            Q130=makeQuery(id+"F9.opPattern","COPY",BODY,{"derivedFrom":makeQuery(id+"F8.opPattern","COPY",BODY,{"derivedFrom":makeQuery(id+"F7.opPattern","COPY",BODY,{"derivedFrom":makeQuery(id+"F2.opPattern","COPY",BODY,{"derivedFrom":makeQuery(id+"F1.opExtrude","SWEPT_BODY",BODY,{"disambiguationData":[OSD([sQuery(id+"F0.wireOp",EDGE,"E1.bottom"),sQuery(id+"F0.wireOp",EDGE,"E1.top"),sQuery(id+"F0.wireOp",EDGE,"E1.left"),sQuery(id+"F0.wireOp",EDGE,"E1.right")])]}),"instanceName":"1"}),"instanceName":"1"}),"instanceName":"1"}),"instanceName":"1"});
            var Q131;
            Q131=makeQuery(id+"F9.opPattern","COPY",BODY,{"derivedFrom":makeQuery(id+"F8.opPattern","COPY",BODY,{"derivedFrom":makeQuery(id+"F7.opPattern","COPY",BODY,{"derivedFrom":makeQuery(id+"F2.opPattern","COPY",BODY,{"derivedFrom":makeQuery(id+"F1.opExtrude","SWEPT_BODY",BODY,{"disambiguationData":[OSD([sQuery(id+"F0.wireOp",EDGE,"E2.bottom"),sQuery(id+"F0.wireOp",EDGE,"E2.top"),sQuery(id+"F0.wireOp",EDGE,"E2.left"),sQuery(id+"F0.wireOp",EDGE,"E2.right")])]}),"instanceName":"1"}),"instanceName":"1"}),"instanceName":"1"}),"instanceName":"1"});
            var Q132;
            Q132=makeQuery(id+"F9.opPattern","COPY",BODY,{"derivedFrom":makeQuery(id+"F8.opPattern","COPY",BODY,{"derivedFrom":makeQuery(id+"F7.opPattern","COPY",BODY,{"derivedFrom":makeQuery(id+"F3.opPattern","COPY",BODY,{"derivedFrom":makeQuery(id+"F2.opPattern","COPY",BODY,{"derivedFrom":makeQuery(id+"F1.opExtrude","SWEPT_BODY",BODY,{"disambiguationData":[OSD([sQuery(id+"F0.wireOp",EDGE,"E0.bottom"),sQuery(id+"F0.wireOp",EDGE,"E0.top"),sQuery(id+"F0.wireOp",EDGE,"E0.left"),sQuery(id+"F0.wireOp",EDGE,"E0.right")])]}),"instanceName":"1"}),"instanceName":"1"}),"instanceName":"1"}),"instanceName":"1"}),"instanceName":"1"});
            var Q133;
            Q133=makeQuery(id+"F9.opPattern","COPY",BODY,{"derivedFrom":makeQuery(id+"F8.opPattern","COPY",BODY,{"derivedFrom":makeQuery(id+"F7.opPattern","COPY",BODY,{"derivedFrom":makeQuery(id+"F3.opPattern","COPY",BODY,{"derivedFrom":makeQuery(id+"F2.opPattern","COPY",BODY,{"derivedFrom":makeQuery(id+"F1.opExtrude","SWEPT_BODY",BODY,{"disambiguationData":[OSD([sQuery(id+"F0.wireOp",EDGE,"E1.bottom"),sQuery(id+"F0.wireOp",EDGE,"E1.top"),sQuery(id+"F0.wireOp",EDGE,"E1.left"),sQuery(id+"F0.wireOp",EDGE,"E1.right")])]}),"instanceName":"1"}),"instanceName":"1"}),"instanceName":"1"}),"instanceName":"1"}),"instanceName":"1"});
            var Q134;
            Q134=makeQuery(id+"F9.opPattern","COPY",BODY,{"derivedFrom":makeQuery(id+"F8.opPattern","COPY",BODY,{"derivedFrom":makeQuery(id+"F7.opPattern","COPY",BODY,{"derivedFrom":makeQuery(id+"F3.opPattern","COPY",BODY,{"derivedFrom":makeQuery(id+"F2.opPattern","COPY",BODY,{"derivedFrom":makeQuery(id+"F1.opExtrude","SWEPT_BODY",BODY,{"disambiguationData":[OSD([sQuery(id+"F0.wireOp",EDGE,"E2.bottom"),sQuery(id+"F0.wireOp",EDGE,"E2.top"),sQuery(id+"F0.wireOp",EDGE,"E2.left"),sQuery(id+"F0.wireOp",EDGE,"E2.right")])]}),"instanceName":"1"}),"instanceName":"1"}),"instanceName":"1"}),"instanceName":"1"}),"instanceName":"1"});
            var Q135;
            Q135=makeQuery(id+"F9.opPattern","COPY",BODY,{"derivedFrom":makeQuery(id+"F8.opPattern","COPY",BODY,{"derivedFrom":makeQuery(id+"F7.opPattern","COPY",BODY,{"derivedFrom":makeQuery(id+"F4.opPattern","COPY",BODY,{"derivedFrom":makeQuery(id+"F3.opPattern","COPY",BODY,{"derivedFrom":makeQuery(id+"F2.opPattern","COPY",BODY,{"derivedFrom":makeQuery(id+"F1.opExtrude","SWEPT_BODY",BODY,{"disambiguationData":[OSD([sQuery(id+"F0.wireOp",EDGE,"E0.bottom"),sQuery(id+"F0.wireOp",EDGE,"E0.top"),sQuery(id+"F0.wireOp",EDGE,"E0.left"),sQuery(id+"F0.wireOp",EDGE,"E0.right")])]}),"instanceName":"1"}),"instanceName":"1"}),"instanceName":"1"}),"instanceName":"1"}),"instanceName":"1"}),"instanceName":"1"});
            var Q136;
            Q136=makeQuery(id+"F9.opPattern","COPY",BODY,{"derivedFrom":makeQuery(id+"F8.opPattern","COPY",BODY,{"derivedFrom":makeQuery(id+"F7.opPattern","COPY",BODY,{"derivedFrom":makeQuery(id+"F4.opPattern","COPY",BODY,{"derivedFrom":makeQuery(id+"F3.opPattern","COPY",BODY,{"derivedFrom":makeQuery(id+"F2.opPattern","COPY",BODY,{"derivedFrom":makeQuery(id+"F1.opExtrude","SWEPT_BODY",BODY,{"disambiguationData":[OSD([sQuery(id+"F0.wireOp",EDGE,"E1.bottom"),sQuery(id+"F0.wireOp",EDGE,"E1.top"),sQuery(id+"F0.wireOp",EDGE,"E1.left"),sQuery(id+"F0.wireOp",EDGE,"E1.right")])]}),"instanceName":"1"}),"instanceName":"1"}),"instanceName":"1"}),"instanceName":"1"}),"instanceName":"1"}),"instanceName":"1"});
            var Q137;
            Q137=makeQuery(id+"F9.opPattern","COPY",BODY,{"derivedFrom":makeQuery(id+"F8.opPattern","COPY",BODY,{"derivedFrom":makeQuery(id+"F7.opPattern","COPY",BODY,{"derivedFrom":makeQuery(id+"F4.opPattern","COPY",BODY,{"derivedFrom":makeQuery(id+"F3.opPattern","COPY",BODY,{"derivedFrom":makeQuery(id+"F2.opPattern","COPY",BODY,{"derivedFrom":makeQuery(id+"F1.opExtrude","SWEPT_BODY",BODY,{"disambiguationData":[OSD([sQuery(id+"F0.wireOp",EDGE,"E2.bottom"),sQuery(id+"F0.wireOp",EDGE,"E2.top"),sQuery(id+"F0.wireOp",EDGE,"E2.left"),sQuery(id+"F0.wireOp",EDGE,"E2.right")])]}),"instanceName":"1"}),"instanceName":"1"}),"instanceName":"1"}),"instanceName":"1"}),"instanceName":"1"}),"instanceName":"1"});
            var Q138;
            Q138=makeQuery(id+"F9.opPattern","COPY",BODY,{"derivedFrom":makeQuery(id+"F8.opPattern","COPY",BODY,{"derivedFrom":makeQuery(id+"F7.opPattern","COPY",BODY,{"derivedFrom":makeQuery(id+"F5.opPattern","COPY",BODY,{"derivedFrom":makeQuery(id+"F4.opPattern","COPY",BODY,{"derivedFrom":makeQuery(id+"F3.opPattern","COPY",BODY,{"derivedFrom":makeQuery(id+"F2.opPattern","COPY",BODY,{"derivedFrom":makeQuery(id+"F1.opExtrude","SWEPT_BODY",BODY,{"disambiguationData":[OSD([sQuery(id+"F0.wireOp",EDGE,"E0.bottom"),sQuery(id+"F0.wireOp",EDGE,"E0.top"),sQuery(id+"F0.wireOp",EDGE,"E0.left"),sQuery(id+"F0.wireOp",EDGE,"E0.right")])]}),"instanceName":"1"}),"instanceName":"1"}),"instanceName":"1"}),"instanceName":"1"}),"instanceName":"1"}),"instanceName":"1"}),"instanceName":"1"});
            var Q139;
            Q139=makeQuery(id+"F9.opPattern","COPY",BODY,{"derivedFrom":makeQuery(id+"F8.opPattern","COPY",BODY,{"derivedFrom":makeQuery(id+"F7.opPattern","COPY",BODY,{"derivedFrom":makeQuery(id+"F5.opPattern","COPY",BODY,{"derivedFrom":makeQuery(id+"F4.opPattern","COPY",BODY,{"derivedFrom":makeQuery(id+"F3.opPattern","COPY",BODY,{"derivedFrom":makeQuery(id+"F2.opPattern","COPY",BODY,{"derivedFrom":makeQuery(id+"F1.opExtrude","SWEPT_BODY",BODY,{"disambiguationData":[OSD([sQuery(id+"F0.wireOp",EDGE,"E1.bottom"),sQuery(id+"F0.wireOp",EDGE,"E1.top"),sQuery(id+"F0.wireOp",EDGE,"E1.left"),sQuery(id+"F0.wireOp",EDGE,"E1.right")])]}),"instanceName":"1"}),"instanceName":"1"}),"instanceName":"1"}),"instanceName":"1"}),"instanceName":"1"}),"instanceName":"1"}),"instanceName":"1"});
            var Q140;
            Q140=makeQuery(id+"F9.opPattern","COPY",BODY,{"derivedFrom":makeQuery(id+"F8.opPattern","COPY",BODY,{"derivedFrom":makeQuery(id+"F7.opPattern","COPY",BODY,{"derivedFrom":makeQuery(id+"F5.opPattern","COPY",BODY,{"derivedFrom":makeQuery(id+"F4.opPattern","COPY",BODY,{"derivedFrom":makeQuery(id+"F3.opPattern","COPY",BODY,{"derivedFrom":makeQuery(id+"F2.opPattern","COPY",BODY,{"derivedFrom":makeQuery(id+"F1.opExtrude","SWEPT_BODY",BODY,{"disambiguationData":[OSD([sQuery(id+"F0.wireOp",EDGE,"E2.bottom"),sQuery(id+"F0.wireOp",EDGE,"E2.top"),sQuery(id+"F0.wireOp",EDGE,"E2.left"),sQuery(id+"F0.wireOp",EDGE,"E2.right")])]}),"instanceName":"1"}),"instanceName":"1"}),"instanceName":"1"}),"instanceName":"1"}),"instanceName":"1"}),"instanceName":"1"}),"instanceName":"1"});
            var Q141;
            Q141=makeQuery(id+"F9.opPattern","COPY",BODY,{"derivedFrom":makeQuery(id+"F8.opPattern","COPY",BODY,{"derivedFrom":makeQuery(id+"F7.opPattern","COPY",BODY,{"derivedFrom":makeQuery(id+"F6.opPattern","COPY",BODY,{"derivedFrom":makeQuery(id+"F5.opPattern","COPY",BODY,{"derivedFrom":makeQuery(id+"F4.opPattern","COPY",BODY,{"derivedFrom":makeQuery(id+"F3.opPattern","COPY",BODY,{"derivedFrom":makeQuery(id+"F2.opPattern","COPY",BODY,{"derivedFrom":makeQuery(id+"F1.opExtrude","SWEPT_BODY",BODY,{"disambiguationData":[OSD([sQuery(id+"F0.wireOp",EDGE,"E0.bottom"),sQuery(id+"F0.wireOp",EDGE,"E0.top"),sQuery(id+"F0.wireOp",EDGE,"E0.left"),sQuery(id+"F0.wireOp",EDGE,"E0.right")])]}),"instanceName":"1"}),"instanceName":"1"}),"instanceName":"1"}),"instanceName":"1"}),"instanceName":"1"}),"instanceName":"1"}),"instanceName":"1"}),"instanceName":"1"});
            var Q142;
            Q142=makeQuery(id+"F9.opPattern","COPY",BODY,{"derivedFrom":makeQuery(id+"F8.opPattern","COPY",BODY,{"derivedFrom":makeQuery(id+"F7.opPattern","COPY",BODY,{"derivedFrom":makeQuery(id+"F6.opPattern","COPY",BODY,{"derivedFrom":makeQuery(id+"F5.opPattern","COPY",BODY,{"derivedFrom":makeQuery(id+"F4.opPattern","COPY",BODY,{"derivedFrom":makeQuery(id+"F3.opPattern","COPY",BODY,{"derivedFrom":makeQuery(id+"F2.opPattern","COPY",BODY,{"derivedFrom":makeQuery(id+"F1.opExtrude","SWEPT_BODY",BODY,{"disambiguationData":[OSD([sQuery(id+"F0.wireOp",EDGE,"E1.bottom"),sQuery(id+"F0.wireOp",EDGE,"E1.top"),sQuery(id+"F0.wireOp",EDGE,"E1.left"),sQuery(id+"F0.wireOp",EDGE,"E1.right")])]}),"instanceName":"1"}),"instanceName":"1"}),"instanceName":"1"}),"instanceName":"1"}),"instanceName":"1"}),"instanceName":"1"}),"instanceName":"1"}),"instanceName":"1"});
            var Q143;
            Q143=makeQuery(id+"F9.opPattern","COPY",BODY,{"derivedFrom":makeQuery(id+"F8.opPattern","COPY",BODY,{"derivedFrom":makeQuery(id+"F7.opPattern","COPY",BODY,{"derivedFrom":makeQuery(id+"F6.opPattern","COPY",BODY,{"derivedFrom":makeQuery(id+"F5.opPattern","COPY",BODY,{"derivedFrom":makeQuery(id+"F4.opPattern","COPY",BODY,{"derivedFrom":makeQuery(id+"F3.opPattern","COPY",BODY,{"derivedFrom":makeQuery(id+"F2.opPattern","COPY",BODY,{"derivedFrom":makeQuery(id+"F1.opExtrude","SWEPT_BODY",BODY,{"disambiguationData":[OSD([sQuery(id+"F0.wireOp",EDGE,"E2.bottom"),sQuery(id+"F0.wireOp",EDGE,"E2.top"),sQuery(id+"F0.wireOp",EDGE,"E2.left"),sQuery(id+"F0.wireOp",EDGE,"E2.right")])]}),"instanceName":"1"}),"instanceName":"1"}),"instanceName":"1"}),"instanceName":"1"}),"instanceName":"1"}),"instanceName":"1"}),"instanceName":"1"}),"instanceName":"1"});
            var Q144;
            Q144=makeQuery(id+"F10.opPattern","COPY",BODY,{"derivedFrom":makeQuery(id+"F1.opExtrude","SWEPT_BODY",BODY,{"disambiguationData":[OSD([sQuery(id+"F0.wireOp",EDGE,"E0.bottom"),sQuery(id+"F0.wireOp",EDGE,"E0.top"),sQuery(id+"F0.wireOp",EDGE,"E0.left"),sQuery(id+"F0.wireOp",EDGE,"E0.right")])]}),"instanceName":"1"});
            var Q145;
            Q145=makeQuery(id+"F10.opPattern","COPY",BODY,{"derivedFrom":makeQuery(id+"F1.opExtrude","SWEPT_BODY",BODY,{"disambiguationData":[OSD([sQuery(id+"F0.wireOp",EDGE,"E1.bottom"),sQuery(id+"F0.wireOp",EDGE,"E1.top"),sQuery(id+"F0.wireOp",EDGE,"E1.left"),sQuery(id+"F0.wireOp",EDGE,"E1.right")])]}),"instanceName":"1"});
            var Q146;
            Q146=makeQuery(id+"F10.opPattern","COPY",BODY,{"derivedFrom":makeQuery(id+"F1.opExtrude","SWEPT_BODY",BODY,{"disambiguationData":[OSD([sQuery(id+"F0.wireOp",EDGE,"E2.bottom"),sQuery(id+"F0.wireOp",EDGE,"E2.top"),sQuery(id+"F0.wireOp",EDGE,"E2.left"),sQuery(id+"F0.wireOp",EDGE,"E2.right")])]}),"instanceName":"1"});
            var Q147;
            Q147=makeQuery(id+"F10.opPattern","COPY",BODY,{"derivedFrom":makeQuery(id+"F2.opPattern","COPY",BODY,{"derivedFrom":makeQuery(id+"F1.opExtrude","SWEPT_BODY",BODY,{"disambiguationData":[OSD([sQuery(id+"F0.wireOp",EDGE,"E0.bottom"),sQuery(id+"F0.wireOp",EDGE,"E0.top"),sQuery(id+"F0.wireOp",EDGE,"E0.left"),sQuery(id+"F0.wireOp",EDGE,"E0.right")])]}),"instanceName":"1"}),"instanceName":"1"});
            var Q148;
            Q148=makeQuery(id+"F10.opPattern","COPY",BODY,{"derivedFrom":makeQuery(id+"F2.opPattern","COPY",BODY,{"derivedFrom":makeQuery(id+"F1.opExtrude","SWEPT_BODY",BODY,{"disambiguationData":[OSD([sQuery(id+"F0.wireOp",EDGE,"E1.bottom"),sQuery(id+"F0.wireOp",EDGE,"E1.top"),sQuery(id+"F0.wireOp",EDGE,"E1.left"),sQuery(id+"F0.wireOp",EDGE,"E1.right")])]}),"instanceName":"1"}),"instanceName":"1"});
            var Q149;
            Q149=makeQuery(id+"F10.opPattern","COPY",BODY,{"derivedFrom":makeQuery(id+"F2.opPattern","COPY",BODY,{"derivedFrom":makeQuery(id+"F1.opExtrude","SWEPT_BODY",BODY,{"disambiguationData":[OSD([sQuery(id+"F0.wireOp",EDGE,"E2.bottom"),sQuery(id+"F0.wireOp",EDGE,"E2.top"),sQuery(id+"F0.wireOp",EDGE,"E2.left"),sQuery(id+"F0.wireOp",EDGE,"E2.right")])]}),"instanceName":"1"}),"instanceName":"1"});
            var Q150;
            Q150=makeQuery(id+"F10.opPattern","COPY",BODY,{"derivedFrom":makeQuery(id+"F3.opPattern","COPY",BODY,{"derivedFrom":makeQuery(id+"F2.opPattern","COPY",BODY,{"derivedFrom":makeQuery(id+"F1.opExtrude","SWEPT_BODY",BODY,{"disambiguationData":[OSD([sQuery(id+"F0.wireOp",EDGE,"E0.bottom"),sQuery(id+"F0.wireOp",EDGE,"E0.top"),sQuery(id+"F0.wireOp",EDGE,"E0.left"),sQuery(id+"F0.wireOp",EDGE,"E0.right")])]}),"instanceName":"1"}),"instanceName":"1"}),"instanceName":"1"});
            var Q151;
            Q151=makeQuery(id+"F10.opPattern","COPY",BODY,{"derivedFrom":makeQuery(id+"F3.opPattern","COPY",BODY,{"derivedFrom":makeQuery(id+"F2.opPattern","COPY",BODY,{"derivedFrom":makeQuery(id+"F1.opExtrude","SWEPT_BODY",BODY,{"disambiguationData":[OSD([sQuery(id+"F0.wireOp",EDGE,"E1.bottom"),sQuery(id+"F0.wireOp",EDGE,"E1.top"),sQuery(id+"F0.wireOp",EDGE,"E1.left"),sQuery(id+"F0.wireOp",EDGE,"E1.right")])]}),"instanceName":"1"}),"instanceName":"1"}),"instanceName":"1"});
            var Q152;
            Q152=makeQuery(id+"F10.opPattern","COPY",BODY,{"derivedFrom":makeQuery(id+"F3.opPattern","COPY",BODY,{"derivedFrom":makeQuery(id+"F2.opPattern","COPY",BODY,{"derivedFrom":makeQuery(id+"F1.opExtrude","SWEPT_BODY",BODY,{"disambiguationData":[OSD([sQuery(id+"F0.wireOp",EDGE,"E2.bottom"),sQuery(id+"F0.wireOp",EDGE,"E2.top"),sQuery(id+"F0.wireOp",EDGE,"E2.left"),sQuery(id+"F0.wireOp",EDGE,"E2.right")])]}),"instanceName":"1"}),"instanceName":"1"}),"instanceName":"1"});
            var Q153;
            Q153=makeQuery(id+"F10.opPattern","COPY",BODY,{"derivedFrom":makeQuery(id+"F4.opPattern","COPY",BODY,{"derivedFrom":makeQuery(id+"F3.opPattern","COPY",BODY,{"derivedFrom":makeQuery(id+"F2.opPattern","COPY",BODY,{"derivedFrom":makeQuery(id+"F1.opExtrude","SWEPT_BODY",BODY,{"disambiguationData":[OSD([sQuery(id+"F0.wireOp",EDGE,"E0.bottom"),sQuery(id+"F0.wireOp",EDGE,"E0.top"),sQuery(id+"F0.wireOp",EDGE,"E0.left"),sQuery(id+"F0.wireOp",EDGE,"E0.right")])]}),"instanceName":"1"}),"instanceName":"1"}),"instanceName":"1"}),"instanceName":"1"});
            var Q154;
            Q154=makeQuery(id+"F10.opPattern","COPY",BODY,{"derivedFrom":makeQuery(id+"F4.opPattern","COPY",BODY,{"derivedFrom":makeQuery(id+"F3.opPattern","COPY",BODY,{"derivedFrom":makeQuery(id+"F2.opPattern","COPY",BODY,{"derivedFrom":makeQuery(id+"F1.opExtrude","SWEPT_BODY",BODY,{"disambiguationData":[OSD([sQuery(id+"F0.wireOp",EDGE,"E1.bottom"),sQuery(id+"F0.wireOp",EDGE,"E1.top"),sQuery(id+"F0.wireOp",EDGE,"E1.left"),sQuery(id+"F0.wireOp",EDGE,"E1.right")])]}),"instanceName":"1"}),"instanceName":"1"}),"instanceName":"1"}),"instanceName":"1"});
            var Q155;
            Q155=makeQuery(id+"F10.opPattern","COPY",BODY,{"derivedFrom":makeQuery(id+"F4.opPattern","COPY",BODY,{"derivedFrom":makeQuery(id+"F3.opPattern","COPY",BODY,{"derivedFrom":makeQuery(id+"F2.opPattern","COPY",BODY,{"derivedFrom":makeQuery(id+"F1.opExtrude","SWEPT_BODY",BODY,{"disambiguationData":[OSD([sQuery(id+"F0.wireOp",EDGE,"E2.bottom"),sQuery(id+"F0.wireOp",EDGE,"E2.top"),sQuery(id+"F0.wireOp",EDGE,"E2.left"),sQuery(id+"F0.wireOp",EDGE,"E2.right")])]}),"instanceName":"1"}),"instanceName":"1"}),"instanceName":"1"}),"instanceName":"1"});
            var Q156;
            Q156=makeQuery(id+"F10.opPattern","COPY",BODY,{"derivedFrom":makeQuery(id+"F5.opPattern","COPY",BODY,{"derivedFrom":makeQuery(id+"F4.opPattern","COPY",BODY,{"derivedFrom":makeQuery(id+"F3.opPattern","COPY",BODY,{"derivedFrom":makeQuery(id+"F2.opPattern","COPY",BODY,{"derivedFrom":makeQuery(id+"F1.opExtrude","SWEPT_BODY",BODY,{"disambiguationData":[OSD([sQuery(id+"F0.wireOp",EDGE,"E0.bottom"),sQuery(id+"F0.wireOp",EDGE,"E0.top"),sQuery(id+"F0.wireOp",EDGE,"E0.left"),sQuery(id+"F0.wireOp",EDGE,"E0.right")])]}),"instanceName":"1"}),"instanceName":"1"}),"instanceName":"1"}),"instanceName":"1"}),"instanceName":"1"});
            var Q157;
            Q157=makeQuery(id+"F10.opPattern","COPY",BODY,{"derivedFrom":makeQuery(id+"F5.opPattern","COPY",BODY,{"derivedFrom":makeQuery(id+"F4.opPattern","COPY",BODY,{"derivedFrom":makeQuery(id+"F3.opPattern","COPY",BODY,{"derivedFrom":makeQuery(id+"F2.opPattern","COPY",BODY,{"derivedFrom":makeQuery(id+"F1.opExtrude","SWEPT_BODY",BODY,{"disambiguationData":[OSD([sQuery(id+"F0.wireOp",EDGE,"E1.bottom"),sQuery(id+"F0.wireOp",EDGE,"E1.top"),sQuery(id+"F0.wireOp",EDGE,"E1.left"),sQuery(id+"F0.wireOp",EDGE,"E1.right")])]}),"instanceName":"1"}),"instanceName":"1"}),"instanceName":"1"}),"instanceName":"1"}),"instanceName":"1"});
            var Q158;
            Q158=makeQuery(id+"F10.opPattern","COPY",BODY,{"derivedFrom":makeQuery(id+"F5.opPattern","COPY",BODY,{"derivedFrom":makeQuery(id+"F4.opPattern","COPY",BODY,{"derivedFrom":makeQuery(id+"F3.opPattern","COPY",BODY,{"derivedFrom":makeQuery(id+"F2.opPattern","COPY",BODY,{"derivedFrom":makeQuery(id+"F1.opExtrude","SWEPT_BODY",BODY,{"disambiguationData":[OSD([sQuery(id+"F0.wireOp",EDGE,"E2.bottom"),sQuery(id+"F0.wireOp",EDGE,"E2.top"),sQuery(id+"F0.wireOp",EDGE,"E2.left"),sQuery(id+"F0.wireOp",EDGE,"E2.right")])]}),"instanceName":"1"}),"instanceName":"1"}),"instanceName":"1"}),"instanceName":"1"}),"instanceName":"1"});
            var Q159;
            Q159=makeQuery(id+"F10.opPattern","COPY",BODY,{"derivedFrom":makeQuery(id+"F6.opPattern","COPY",BODY,{"derivedFrom":makeQuery(id+"F5.opPattern","COPY",BODY,{"derivedFrom":makeQuery(id+"F4.opPattern","COPY",BODY,{"derivedFrom":makeQuery(id+"F3.opPattern","COPY",BODY,{"derivedFrom":makeQuery(id+"F2.opPattern","COPY",BODY,{"derivedFrom":makeQuery(id+"F1.opExtrude","SWEPT_BODY",BODY,{"disambiguationData":[OSD([sQuery(id+"F0.wireOp",EDGE,"E0.bottom"),sQuery(id+"F0.wireOp",EDGE,"E0.top"),sQuery(id+"F0.wireOp",EDGE,"E0.left"),sQuery(id+"F0.wireOp",EDGE,"E0.right")])]}),"instanceName":"1"}),"instanceName":"1"}),"instanceName":"1"}),"instanceName":"1"}),"instanceName":"1"}),"instanceName":"1"});
            var Q160;
            Q160=makeQuery(id+"F10.opPattern","COPY",BODY,{"derivedFrom":makeQuery(id+"F6.opPattern","COPY",BODY,{"derivedFrom":makeQuery(id+"F5.opPattern","COPY",BODY,{"derivedFrom":makeQuery(id+"F4.opPattern","COPY",BODY,{"derivedFrom":makeQuery(id+"F3.opPattern","COPY",BODY,{"derivedFrom":makeQuery(id+"F2.opPattern","COPY",BODY,{"derivedFrom":makeQuery(id+"F1.opExtrude","SWEPT_BODY",BODY,{"disambiguationData":[OSD([sQuery(id+"F0.wireOp",EDGE,"E1.bottom"),sQuery(id+"F0.wireOp",EDGE,"E1.top"),sQuery(id+"F0.wireOp",EDGE,"E1.left"),sQuery(id+"F0.wireOp",EDGE,"E1.right")])]}),"instanceName":"1"}),"instanceName":"1"}),"instanceName":"1"}),"instanceName":"1"}),"instanceName":"1"}),"instanceName":"1"});
            var Q161;
            Q161=makeQuery(id+"F10.opPattern","COPY",BODY,{"derivedFrom":makeQuery(id+"F6.opPattern","COPY",BODY,{"derivedFrom":makeQuery(id+"F5.opPattern","COPY",BODY,{"derivedFrom":makeQuery(id+"F4.opPattern","COPY",BODY,{"derivedFrom":makeQuery(id+"F3.opPattern","COPY",BODY,{"derivedFrom":makeQuery(id+"F2.opPattern","COPY",BODY,{"derivedFrom":makeQuery(id+"F1.opExtrude","SWEPT_BODY",BODY,{"disambiguationData":[OSD([sQuery(id+"F0.wireOp",EDGE,"E2.bottom"),sQuery(id+"F0.wireOp",EDGE,"E2.top"),sQuery(id+"F0.wireOp",EDGE,"E2.left"),sQuery(id+"F0.wireOp",EDGE,"E2.right")])]}),"instanceName":"1"}),"instanceName":"1"}),"instanceName":"1"}),"instanceName":"1"}),"instanceName":"1"}),"instanceName":"1"});
            var Q162;
            Q162=makeQuery(id+"F10.opPattern","COPY",BODY,{"derivedFrom":makeQuery(id+"F7.opPattern","COPY",BODY,{"derivedFrom":makeQuery(id+"F1.opExtrude","SWEPT_BODY",BODY,{"disambiguationData":[OSD([sQuery(id+"F0.wireOp",EDGE,"E0.bottom"),sQuery(id+"F0.wireOp",EDGE,"E0.top"),sQuery(id+"F0.wireOp",EDGE,"E0.left"),sQuery(id+"F0.wireOp",EDGE,"E0.right")])]}),"instanceName":"1"}),"instanceName":"1"});
            var Q163;
            Q163=makeQuery(id+"F10.opPattern","COPY",BODY,{"derivedFrom":makeQuery(id+"F7.opPattern","COPY",BODY,{"derivedFrom":makeQuery(id+"F1.opExtrude","SWEPT_BODY",BODY,{"disambiguationData":[OSD([sQuery(id+"F0.wireOp",EDGE,"E1.bottom"),sQuery(id+"F0.wireOp",EDGE,"E1.top"),sQuery(id+"F0.wireOp",EDGE,"E1.left"),sQuery(id+"F0.wireOp",EDGE,"E1.right")])]}),"instanceName":"1"}),"instanceName":"1"});
            var Q164;
            Q164=makeQuery(id+"F10.opPattern","COPY",BODY,{"derivedFrom":makeQuery(id+"F7.opPattern","COPY",BODY,{"derivedFrom":makeQuery(id+"F1.opExtrude","SWEPT_BODY",BODY,{"disambiguationData":[OSD([sQuery(id+"F0.wireOp",EDGE,"E2.bottom"),sQuery(id+"F0.wireOp",EDGE,"E2.top"),sQuery(id+"F0.wireOp",EDGE,"E2.left"),sQuery(id+"F0.wireOp",EDGE,"E2.right")])]}),"instanceName":"1"}),"instanceName":"1"});
            var Q165;
            Q165=makeQuery(id+"F10.opPattern","COPY",BODY,{"derivedFrom":makeQuery(id+"F7.opPattern","COPY",BODY,{"derivedFrom":makeQuery(id+"F2.opPattern","COPY",BODY,{"derivedFrom":makeQuery(id+"F1.opExtrude","SWEPT_BODY",BODY,{"disambiguationData":[OSD([sQuery(id+"F0.wireOp",EDGE,"E0.bottom"),sQuery(id+"F0.wireOp",EDGE,"E0.top"),sQuery(id+"F0.wireOp",EDGE,"E0.left"),sQuery(id+"F0.wireOp",EDGE,"E0.right")])]}),"instanceName":"1"}),"instanceName":"1"}),"instanceName":"1"});
            var Q166;
            Q166=makeQuery(id+"F10.opPattern","COPY",BODY,{"derivedFrom":makeQuery(id+"F7.opPattern","COPY",BODY,{"derivedFrom":makeQuery(id+"F2.opPattern","COPY",BODY,{"derivedFrom":makeQuery(id+"F1.opExtrude","SWEPT_BODY",BODY,{"disambiguationData":[OSD([sQuery(id+"F0.wireOp",EDGE,"E1.bottom"),sQuery(id+"F0.wireOp",EDGE,"E1.top"),sQuery(id+"F0.wireOp",EDGE,"E1.left"),sQuery(id+"F0.wireOp",EDGE,"E1.right")])]}),"instanceName":"1"}),"instanceName":"1"}),"instanceName":"1"});
            var Q167;
            Q167=makeQuery(id+"F10.opPattern","COPY",BODY,{"derivedFrom":makeQuery(id+"F7.opPattern","COPY",BODY,{"derivedFrom":makeQuery(id+"F2.opPattern","COPY",BODY,{"derivedFrom":makeQuery(id+"F1.opExtrude","SWEPT_BODY",BODY,{"disambiguationData":[OSD([sQuery(id+"F0.wireOp",EDGE,"E2.bottom"),sQuery(id+"F0.wireOp",EDGE,"E2.top"),sQuery(id+"F0.wireOp",EDGE,"E2.left"),sQuery(id+"F0.wireOp",EDGE,"E2.right")])]}),"instanceName":"1"}),"instanceName":"1"}),"instanceName":"1"});
            var Q168;
            Q168=makeQuery(id+"F10.opPattern","COPY",BODY,{"derivedFrom":makeQuery(id+"F7.opPattern","COPY",BODY,{"derivedFrom":makeQuery(id+"F3.opPattern","COPY",BODY,{"derivedFrom":makeQuery(id+"F2.opPattern","COPY",BODY,{"derivedFrom":makeQuery(id+"F1.opExtrude","SWEPT_BODY",BODY,{"disambiguationData":[OSD([sQuery(id+"F0.wireOp",EDGE,"E0.bottom"),sQuery(id+"F0.wireOp",EDGE,"E0.top"),sQuery(id+"F0.wireOp",EDGE,"E0.left"),sQuery(id+"F0.wireOp",EDGE,"E0.right")])]}),"instanceName":"1"}),"instanceName":"1"}),"instanceName":"1"}),"instanceName":"1"});
            var Q169;
            Q169=makeQuery(id+"F10.opPattern","COPY",BODY,{"derivedFrom":makeQuery(id+"F7.opPattern","COPY",BODY,{"derivedFrom":makeQuery(id+"F3.opPattern","COPY",BODY,{"derivedFrom":makeQuery(id+"F2.opPattern","COPY",BODY,{"derivedFrom":makeQuery(id+"F1.opExtrude","SWEPT_BODY",BODY,{"disambiguationData":[OSD([sQuery(id+"F0.wireOp",EDGE,"E1.bottom"),sQuery(id+"F0.wireOp",EDGE,"E1.top"),sQuery(id+"F0.wireOp",EDGE,"E1.left"),sQuery(id+"F0.wireOp",EDGE,"E1.right")])]}),"instanceName":"1"}),"instanceName":"1"}),"instanceName":"1"}),"instanceName":"1"});
            var Q170;
            Q170=makeQuery(id+"F10.opPattern","COPY",BODY,{"derivedFrom":makeQuery(id+"F7.opPattern","COPY",BODY,{"derivedFrom":makeQuery(id+"F3.opPattern","COPY",BODY,{"derivedFrom":makeQuery(id+"F2.opPattern","COPY",BODY,{"derivedFrom":makeQuery(id+"F1.opExtrude","SWEPT_BODY",BODY,{"disambiguationData":[OSD([sQuery(id+"F0.wireOp",EDGE,"E2.bottom"),sQuery(id+"F0.wireOp",EDGE,"E2.top"),sQuery(id+"F0.wireOp",EDGE,"E2.left"),sQuery(id+"F0.wireOp",EDGE,"E2.right")])]}),"instanceName":"1"}),"instanceName":"1"}),"instanceName":"1"}),"instanceName":"1"});
            var Q171;
            Q171=makeQuery(id+"F10.opPattern","COPY",BODY,{"derivedFrom":makeQuery(id+"F7.opPattern","COPY",BODY,{"derivedFrom":makeQuery(id+"F4.opPattern","COPY",BODY,{"derivedFrom":makeQuery(id+"F3.opPattern","COPY",BODY,{"derivedFrom":makeQuery(id+"F2.opPattern","COPY",BODY,{"derivedFrom":makeQuery(id+"F1.opExtrude","SWEPT_BODY",BODY,{"disambiguationData":[OSD([sQuery(id+"F0.wireOp",EDGE,"E0.bottom"),sQuery(id+"F0.wireOp",EDGE,"E0.top"),sQuery(id+"F0.wireOp",EDGE,"E0.left"),sQuery(id+"F0.wireOp",EDGE,"E0.right")])]}),"instanceName":"1"}),"instanceName":"1"}),"instanceName":"1"}),"instanceName":"1"}),"instanceName":"1"});
            var Q172;
            Q172=makeQuery(id+"F10.opPattern","COPY",BODY,{"derivedFrom":makeQuery(id+"F7.opPattern","COPY",BODY,{"derivedFrom":makeQuery(id+"F4.opPattern","COPY",BODY,{"derivedFrom":makeQuery(id+"F3.opPattern","COPY",BODY,{"derivedFrom":makeQuery(id+"F2.opPattern","COPY",BODY,{"derivedFrom":makeQuery(id+"F1.opExtrude","SWEPT_BODY",BODY,{"disambiguationData":[OSD([sQuery(id+"F0.wireOp",EDGE,"E1.bottom"),sQuery(id+"F0.wireOp",EDGE,"E1.top"),sQuery(id+"F0.wireOp",EDGE,"E1.left"),sQuery(id+"F0.wireOp",EDGE,"E1.right")])]}),"instanceName":"1"}),"instanceName":"1"}),"instanceName":"1"}),"instanceName":"1"}),"instanceName":"1"});
            var Q173;
            Q173=makeQuery(id+"F10.opPattern","COPY",BODY,{"derivedFrom":makeQuery(id+"F7.opPattern","COPY",BODY,{"derivedFrom":makeQuery(id+"F4.opPattern","COPY",BODY,{"derivedFrom":makeQuery(id+"F3.opPattern","COPY",BODY,{"derivedFrom":makeQuery(id+"F2.opPattern","COPY",BODY,{"derivedFrom":makeQuery(id+"F1.opExtrude","SWEPT_BODY",BODY,{"disambiguationData":[OSD([sQuery(id+"F0.wireOp",EDGE,"E2.bottom"),sQuery(id+"F0.wireOp",EDGE,"E2.top"),sQuery(id+"F0.wireOp",EDGE,"E2.left"),sQuery(id+"F0.wireOp",EDGE,"E2.right")])]}),"instanceName":"1"}),"instanceName":"1"}),"instanceName":"1"}),"instanceName":"1"}),"instanceName":"1"});
            var Q174;
            Q174=makeQuery(id+"F10.opPattern","COPY",BODY,{"derivedFrom":makeQuery(id+"F7.opPattern","COPY",BODY,{"derivedFrom":makeQuery(id+"F5.opPattern","COPY",BODY,{"derivedFrom":makeQuery(id+"F4.opPattern","COPY",BODY,{"derivedFrom":makeQuery(id+"F3.opPattern","COPY",BODY,{"derivedFrom":makeQuery(id+"F2.opPattern","COPY",BODY,{"derivedFrom":makeQuery(id+"F1.opExtrude","SWEPT_BODY",BODY,{"disambiguationData":[OSD([sQuery(id+"F0.wireOp",EDGE,"E0.bottom"),sQuery(id+"F0.wireOp",EDGE,"E0.top"),sQuery(id+"F0.wireOp",EDGE,"E0.left"),sQuery(id+"F0.wireOp",EDGE,"E0.right")])]}),"instanceName":"1"}),"instanceName":"1"}),"instanceName":"1"}),"instanceName":"1"}),"instanceName":"1"}),"instanceName":"1"});
            var Q175;
            Q175=makeQuery(id+"F10.opPattern","COPY",BODY,{"derivedFrom":makeQuery(id+"F7.opPattern","COPY",BODY,{"derivedFrom":makeQuery(id+"F5.opPattern","COPY",BODY,{"derivedFrom":makeQuery(id+"F4.opPattern","COPY",BODY,{"derivedFrom":makeQuery(id+"F3.opPattern","COPY",BODY,{"derivedFrom":makeQuery(id+"F2.opPattern","COPY",BODY,{"derivedFrom":makeQuery(id+"F1.opExtrude","SWEPT_BODY",BODY,{"disambiguationData":[OSD([sQuery(id+"F0.wireOp",EDGE,"E1.bottom"),sQuery(id+"F0.wireOp",EDGE,"E1.top"),sQuery(id+"F0.wireOp",EDGE,"E1.left"),sQuery(id+"F0.wireOp",EDGE,"E1.right")])]}),"instanceName":"1"}),"instanceName":"1"}),"instanceName":"1"}),"instanceName":"1"}),"instanceName":"1"}),"instanceName":"1"});
            var Q176;
            Q176=makeQuery(id+"F10.opPattern","COPY",BODY,{"derivedFrom":makeQuery(id+"F7.opPattern","COPY",BODY,{"derivedFrom":makeQuery(id+"F5.opPattern","COPY",BODY,{"derivedFrom":makeQuery(id+"F4.opPattern","COPY",BODY,{"derivedFrom":makeQuery(id+"F3.opPattern","COPY",BODY,{"derivedFrom":makeQuery(id+"F2.opPattern","COPY",BODY,{"derivedFrom":makeQuery(id+"F1.opExtrude","SWEPT_BODY",BODY,{"disambiguationData":[OSD([sQuery(id+"F0.wireOp",EDGE,"E2.bottom"),sQuery(id+"F0.wireOp",EDGE,"E2.top"),sQuery(id+"F0.wireOp",EDGE,"E2.left"),sQuery(id+"F0.wireOp",EDGE,"E2.right")])]}),"instanceName":"1"}),"instanceName":"1"}),"instanceName":"1"}),"instanceName":"1"}),"instanceName":"1"}),"instanceName":"1"});
            var Q177;
            Q177=makeQuery(id+"F10.opPattern","COPY",BODY,{"derivedFrom":makeQuery(id+"F7.opPattern","COPY",BODY,{"derivedFrom":makeQuery(id+"F6.opPattern","COPY",BODY,{"derivedFrom":makeQuery(id+"F5.opPattern","COPY",BODY,{"derivedFrom":makeQuery(id+"F4.opPattern","COPY",BODY,{"derivedFrom":makeQuery(id+"F3.opPattern","COPY",BODY,{"derivedFrom":makeQuery(id+"F2.opPattern","COPY",BODY,{"derivedFrom":makeQuery(id+"F1.opExtrude","SWEPT_BODY",BODY,{"disambiguationData":[OSD([sQuery(id+"F0.wireOp",EDGE,"E0.bottom"),sQuery(id+"F0.wireOp",EDGE,"E0.top"),sQuery(id+"F0.wireOp",EDGE,"E0.left"),sQuery(id+"F0.wireOp",EDGE,"E0.right")])]}),"instanceName":"1"}),"instanceName":"1"}),"instanceName":"1"}),"instanceName":"1"}),"instanceName":"1"}),"instanceName":"1"}),"instanceName":"1"});
            var Q178;
            Q178=makeQuery(id+"F10.opPattern","COPY",BODY,{"derivedFrom":makeQuery(id+"F7.opPattern","COPY",BODY,{"derivedFrom":makeQuery(id+"F6.opPattern","COPY",BODY,{"derivedFrom":makeQuery(id+"F5.opPattern","COPY",BODY,{"derivedFrom":makeQuery(id+"F4.opPattern","COPY",BODY,{"derivedFrom":makeQuery(id+"F3.opPattern","COPY",BODY,{"derivedFrom":makeQuery(id+"F2.opPattern","COPY",BODY,{"derivedFrom":makeQuery(id+"F1.opExtrude","SWEPT_BODY",BODY,{"disambiguationData":[OSD([sQuery(id+"F0.wireOp",EDGE,"E1.bottom"),sQuery(id+"F0.wireOp",EDGE,"E1.top"),sQuery(id+"F0.wireOp",EDGE,"E1.left"),sQuery(id+"F0.wireOp",EDGE,"E1.right")])]}),"instanceName":"1"}),"instanceName":"1"}),"instanceName":"1"}),"instanceName":"1"}),"instanceName":"1"}),"instanceName":"1"}),"instanceName":"1"});
            var Q179;
            Q179=makeQuery(id+"F10.opPattern","COPY",BODY,{"derivedFrom":makeQuery(id+"F7.opPattern","COPY",BODY,{"derivedFrom":makeQuery(id+"F6.opPattern","COPY",BODY,{"derivedFrom":makeQuery(id+"F5.opPattern","COPY",BODY,{"derivedFrom":makeQuery(id+"F4.opPattern","COPY",BODY,{"derivedFrom":makeQuery(id+"F3.opPattern","COPY",BODY,{"derivedFrom":makeQuery(id+"F2.opPattern","COPY",BODY,{"derivedFrom":makeQuery(id+"F1.opExtrude","SWEPT_BODY",BODY,{"disambiguationData":[OSD([sQuery(id+"F0.wireOp",EDGE,"E2.bottom"),sQuery(id+"F0.wireOp",EDGE,"E2.top"),sQuery(id+"F0.wireOp",EDGE,"E2.left"),sQuery(id+"F0.wireOp",EDGE,"E2.right")])]}),"instanceName":"1"}),"instanceName":"1"}),"instanceName":"1"}),"instanceName":"1"}),"instanceName":"1"}),"instanceName":"1"}),"instanceName":"1"});
            var Q180;
            Q180=makeQuery(id+"F10.opPattern","COPY",BODY,{"derivedFrom":makeQuery(id+"F8.opPattern","COPY",BODY,{"derivedFrom":makeQuery(id+"F1.opExtrude","SWEPT_BODY",BODY,{"disambiguationData":[OSD([sQuery(id+"F0.wireOp",EDGE,"E0.bottom"),sQuery(id+"F0.wireOp",EDGE,"E0.top"),sQuery(id+"F0.wireOp",EDGE,"E0.left"),sQuery(id+"F0.wireOp",EDGE,"E0.right")])]}),"instanceName":"1"}),"instanceName":"1"});
            var Q181;
            Q181=makeQuery(id+"F10.opPattern","COPY",BODY,{"derivedFrom":makeQuery(id+"F8.opPattern","COPY",BODY,{"derivedFrom":makeQuery(id+"F1.opExtrude","SWEPT_BODY",BODY,{"disambiguationData":[OSD([sQuery(id+"F0.wireOp",EDGE,"E1.bottom"),sQuery(id+"F0.wireOp",EDGE,"E1.top"),sQuery(id+"F0.wireOp",EDGE,"E1.left"),sQuery(id+"F0.wireOp",EDGE,"E1.right")])]}),"instanceName":"1"}),"instanceName":"1"});
            var Q182;
            Q182=makeQuery(id+"F10.opPattern","COPY",BODY,{"derivedFrom":makeQuery(id+"F8.opPattern","COPY",BODY,{"derivedFrom":makeQuery(id+"F1.opExtrude","SWEPT_BODY",BODY,{"disambiguationData":[OSD([sQuery(id+"F0.wireOp",EDGE,"E2.bottom"),sQuery(id+"F0.wireOp",EDGE,"E2.top"),sQuery(id+"F0.wireOp",EDGE,"E2.left"),sQuery(id+"F0.wireOp",EDGE,"E2.right")])]}),"instanceName":"1"}),"instanceName":"1"});
            var Q183;
            Q183=makeQuery(id+"F10.opPattern","COPY",BODY,{"derivedFrom":makeQuery(id+"F8.opPattern","COPY",BODY,{"derivedFrom":makeQuery(id+"F2.opPattern","COPY",BODY,{"derivedFrom":makeQuery(id+"F1.opExtrude","SWEPT_BODY",BODY,{"disambiguationData":[OSD([sQuery(id+"F0.wireOp",EDGE,"E0.bottom"),sQuery(id+"F0.wireOp",EDGE,"E0.top"),sQuery(id+"F0.wireOp",EDGE,"E0.left"),sQuery(id+"F0.wireOp",EDGE,"E0.right")])]}),"instanceName":"1"}),"instanceName":"1"}),"instanceName":"1"});
            var Q184;
            Q184=makeQuery(id+"F10.opPattern","COPY",BODY,{"derivedFrom":makeQuery(id+"F8.opPattern","COPY",BODY,{"derivedFrom":makeQuery(id+"F2.opPattern","COPY",BODY,{"derivedFrom":makeQuery(id+"F1.opExtrude","SWEPT_BODY",BODY,{"disambiguationData":[OSD([sQuery(id+"F0.wireOp",EDGE,"E1.bottom"),sQuery(id+"F0.wireOp",EDGE,"E1.top"),sQuery(id+"F0.wireOp",EDGE,"E1.left"),sQuery(id+"F0.wireOp",EDGE,"E1.right")])]}),"instanceName":"1"}),"instanceName":"1"}),"instanceName":"1"});
            var Q185;
            Q185=makeQuery(id+"F10.opPattern","COPY",BODY,{"derivedFrom":makeQuery(id+"F8.opPattern","COPY",BODY,{"derivedFrom":makeQuery(id+"F2.opPattern","COPY",BODY,{"derivedFrom":makeQuery(id+"F1.opExtrude","SWEPT_BODY",BODY,{"disambiguationData":[OSD([sQuery(id+"F0.wireOp",EDGE,"E2.bottom"),sQuery(id+"F0.wireOp",EDGE,"E2.top"),sQuery(id+"F0.wireOp",EDGE,"E2.left"),sQuery(id+"F0.wireOp",EDGE,"E2.right")])]}),"instanceName":"1"}),"instanceName":"1"}),"instanceName":"1"});
            var Q186;
            Q186=makeQuery(id+"F10.opPattern","COPY",BODY,{"derivedFrom":makeQuery(id+"F8.opPattern","COPY",BODY,{"derivedFrom":makeQuery(id+"F3.opPattern","COPY",BODY,{"derivedFrom":makeQuery(id+"F2.opPattern","COPY",BODY,{"derivedFrom":makeQuery(id+"F1.opExtrude","SWEPT_BODY",BODY,{"disambiguationData":[OSD([sQuery(id+"F0.wireOp",EDGE,"E0.bottom"),sQuery(id+"F0.wireOp",EDGE,"E0.top"),sQuery(id+"F0.wireOp",EDGE,"E0.left"),sQuery(id+"F0.wireOp",EDGE,"E0.right")])]}),"instanceName":"1"}),"instanceName":"1"}),"instanceName":"1"}),"instanceName":"1"});
            var Q187;
            Q187=makeQuery(id+"F10.opPattern","COPY",BODY,{"derivedFrom":makeQuery(id+"F8.opPattern","COPY",BODY,{"derivedFrom":makeQuery(id+"F3.opPattern","COPY",BODY,{"derivedFrom":makeQuery(id+"F2.opPattern","COPY",BODY,{"derivedFrom":makeQuery(id+"F1.opExtrude","SWEPT_BODY",BODY,{"disambiguationData":[OSD([sQuery(id+"F0.wireOp",EDGE,"E1.bottom"),sQuery(id+"F0.wireOp",EDGE,"E1.top"),sQuery(id+"F0.wireOp",EDGE,"E1.left"),sQuery(id+"F0.wireOp",EDGE,"E1.right")])]}),"instanceName":"1"}),"instanceName":"1"}),"instanceName":"1"}),"instanceName":"1"});
            var Q188;
            Q188=makeQuery(id+"F10.opPattern","COPY",BODY,{"derivedFrom":makeQuery(id+"F8.opPattern","COPY",BODY,{"derivedFrom":makeQuery(id+"F3.opPattern","COPY",BODY,{"derivedFrom":makeQuery(id+"F2.opPattern","COPY",BODY,{"derivedFrom":makeQuery(id+"F1.opExtrude","SWEPT_BODY",BODY,{"disambiguationData":[OSD([sQuery(id+"F0.wireOp",EDGE,"E2.bottom"),sQuery(id+"F0.wireOp",EDGE,"E2.top"),sQuery(id+"F0.wireOp",EDGE,"E2.left"),sQuery(id+"F0.wireOp",EDGE,"E2.right")])]}),"instanceName":"1"}),"instanceName":"1"}),"instanceName":"1"}),"instanceName":"1"});
            var Q189;
            Q189=makeQuery(id+"F10.opPattern","COPY",BODY,{"derivedFrom":makeQuery(id+"F8.opPattern","COPY",BODY,{"derivedFrom":makeQuery(id+"F4.opPattern","COPY",BODY,{"derivedFrom":makeQuery(id+"F3.opPattern","COPY",BODY,{"derivedFrom":makeQuery(id+"F2.opPattern","COPY",BODY,{"derivedFrom":makeQuery(id+"F1.opExtrude","SWEPT_BODY",BODY,{"disambiguationData":[OSD([sQuery(id+"F0.wireOp",EDGE,"E0.bottom"),sQuery(id+"F0.wireOp",EDGE,"E0.top"),sQuery(id+"F0.wireOp",EDGE,"E0.left"),sQuery(id+"F0.wireOp",EDGE,"E0.right")])]}),"instanceName":"1"}),"instanceName":"1"}),"instanceName":"1"}),"instanceName":"1"}),"instanceName":"1"});
            var Q190;
            Q190=makeQuery(id+"F10.opPattern","COPY",BODY,{"derivedFrom":makeQuery(id+"F8.opPattern","COPY",BODY,{"derivedFrom":makeQuery(id+"F4.opPattern","COPY",BODY,{"derivedFrom":makeQuery(id+"F3.opPattern","COPY",BODY,{"derivedFrom":makeQuery(id+"F2.opPattern","COPY",BODY,{"derivedFrom":makeQuery(id+"F1.opExtrude","SWEPT_BODY",BODY,{"disambiguationData":[OSD([sQuery(id+"F0.wireOp",EDGE,"E1.bottom"),sQuery(id+"F0.wireOp",EDGE,"E1.top"),sQuery(id+"F0.wireOp",EDGE,"E1.left"),sQuery(id+"F0.wireOp",EDGE,"E1.right")])]}),"instanceName":"1"}),"instanceName":"1"}),"instanceName":"1"}),"instanceName":"1"}),"instanceName":"1"});
            var Q191;
            Q191=makeQuery(id+"F10.opPattern","COPY",BODY,{"derivedFrom":makeQuery(id+"F8.opPattern","COPY",BODY,{"derivedFrom":makeQuery(id+"F4.opPattern","COPY",BODY,{"derivedFrom":makeQuery(id+"F3.opPattern","COPY",BODY,{"derivedFrom":makeQuery(id+"F2.opPattern","COPY",BODY,{"derivedFrom":makeQuery(id+"F1.opExtrude","SWEPT_BODY",BODY,{"disambiguationData":[OSD([sQuery(id+"F0.wireOp",EDGE,"E2.bottom"),sQuery(id+"F0.wireOp",EDGE,"E2.top"),sQuery(id+"F0.wireOp",EDGE,"E2.left"),sQuery(id+"F0.wireOp",EDGE,"E2.right")])]}),"instanceName":"1"}),"instanceName":"1"}),"instanceName":"1"}),"instanceName":"1"}),"instanceName":"1"});
            var Q192;
            Q192=makeQuery(id+"F10.opPattern","COPY",BODY,{"derivedFrom":makeQuery(id+"F8.opPattern","COPY",BODY,{"derivedFrom":makeQuery(id+"F5.opPattern","COPY",BODY,{"derivedFrom":makeQuery(id+"F4.opPattern","COPY",BODY,{"derivedFrom":makeQuery(id+"F3.opPattern","COPY",BODY,{"derivedFrom":makeQuery(id+"F2.opPattern","COPY",BODY,{"derivedFrom":makeQuery(id+"F1.opExtrude","SWEPT_BODY",BODY,{"disambiguationData":[OSD([sQuery(id+"F0.wireOp",EDGE,"E0.bottom"),sQuery(id+"F0.wireOp",EDGE,"E0.top"),sQuery(id+"F0.wireOp",EDGE,"E0.left"),sQuery(id+"F0.wireOp",EDGE,"E0.right")])]}),"instanceName":"1"}),"instanceName":"1"}),"instanceName":"1"}),"instanceName":"1"}),"instanceName":"1"}),"instanceName":"1"});
            var Q193;
            Q193=makeQuery(id+"F10.opPattern","COPY",BODY,{"derivedFrom":makeQuery(id+"F8.opPattern","COPY",BODY,{"derivedFrom":makeQuery(id+"F5.opPattern","COPY",BODY,{"derivedFrom":makeQuery(id+"F4.opPattern","COPY",BODY,{"derivedFrom":makeQuery(id+"F3.opPattern","COPY",BODY,{"derivedFrom":makeQuery(id+"F2.opPattern","COPY",BODY,{"derivedFrom":makeQuery(id+"F1.opExtrude","SWEPT_BODY",BODY,{"disambiguationData":[OSD([sQuery(id+"F0.wireOp",EDGE,"E1.bottom"),sQuery(id+"F0.wireOp",EDGE,"E1.top"),sQuery(id+"F0.wireOp",EDGE,"E1.left"),sQuery(id+"F0.wireOp",EDGE,"E1.right")])]}),"instanceName":"1"}),"instanceName":"1"}),"instanceName":"1"}),"instanceName":"1"}),"instanceName":"1"}),"instanceName":"1"});
            var Q194;
            Q194=makeQuery(id+"F10.opPattern","COPY",BODY,{"derivedFrom":makeQuery(id+"F8.opPattern","COPY",BODY,{"derivedFrom":makeQuery(id+"F5.opPattern","COPY",BODY,{"derivedFrom":makeQuery(id+"F4.opPattern","COPY",BODY,{"derivedFrom":makeQuery(id+"F3.opPattern","COPY",BODY,{"derivedFrom":makeQuery(id+"F2.opPattern","COPY",BODY,{"derivedFrom":makeQuery(id+"F1.opExtrude","SWEPT_BODY",BODY,{"disambiguationData":[OSD([sQuery(id+"F0.wireOp",EDGE,"E2.bottom"),sQuery(id+"F0.wireOp",EDGE,"E2.top"),sQuery(id+"F0.wireOp",EDGE,"E2.left"),sQuery(id+"F0.wireOp",EDGE,"E2.right")])]}),"instanceName":"1"}),"instanceName":"1"}),"instanceName":"1"}),"instanceName":"1"}),"instanceName":"1"}),"instanceName":"1"});
            var Q195;
            Q195=makeQuery(id+"F10.opPattern","COPY",BODY,{"derivedFrom":makeQuery(id+"F8.opPattern","COPY",BODY,{"derivedFrom":makeQuery(id+"F6.opPattern","COPY",BODY,{"derivedFrom":makeQuery(id+"F5.opPattern","COPY",BODY,{"derivedFrom":makeQuery(id+"F4.opPattern","COPY",BODY,{"derivedFrom":makeQuery(id+"F3.opPattern","COPY",BODY,{"derivedFrom":makeQuery(id+"F2.opPattern","COPY",BODY,{"derivedFrom":makeQuery(id+"F1.opExtrude","SWEPT_BODY",BODY,{"disambiguationData":[OSD([sQuery(id+"F0.wireOp",EDGE,"E0.bottom"),sQuery(id+"F0.wireOp",EDGE,"E0.top"),sQuery(id+"F0.wireOp",EDGE,"E0.left"),sQuery(id+"F0.wireOp",EDGE,"E0.right")])]}),"instanceName":"1"}),"instanceName":"1"}),"instanceName":"1"}),"instanceName":"1"}),"instanceName":"1"}),"instanceName":"1"}),"instanceName":"1"});
            var Q196;
            Q196=makeQuery(id+"F10.opPattern","COPY",BODY,{"derivedFrom":makeQuery(id+"F8.opPattern","COPY",BODY,{"derivedFrom":makeQuery(id+"F6.opPattern","COPY",BODY,{"derivedFrom":makeQuery(id+"F5.opPattern","COPY",BODY,{"derivedFrom":makeQuery(id+"F4.opPattern","COPY",BODY,{"derivedFrom":makeQuery(id+"F3.opPattern","COPY",BODY,{"derivedFrom":makeQuery(id+"F2.opPattern","COPY",BODY,{"derivedFrom":makeQuery(id+"F1.opExtrude","SWEPT_BODY",BODY,{"disambiguationData":[OSD([sQuery(id+"F0.wireOp",EDGE,"E1.bottom"),sQuery(id+"F0.wireOp",EDGE,"E1.top"),sQuery(id+"F0.wireOp",EDGE,"E1.left"),sQuery(id+"F0.wireOp",EDGE,"E1.right")])]}),"instanceName":"1"}),"instanceName":"1"}),"instanceName":"1"}),"instanceName":"1"}),"instanceName":"1"}),"instanceName":"1"}),"instanceName":"1"});
            var Q197;
            Q197=makeQuery(id+"F10.opPattern","COPY",BODY,{"derivedFrom":makeQuery(id+"F8.opPattern","COPY",BODY,{"derivedFrom":makeQuery(id+"F6.opPattern","COPY",BODY,{"derivedFrom":makeQuery(id+"F5.opPattern","COPY",BODY,{"derivedFrom":makeQuery(id+"F4.opPattern","COPY",BODY,{"derivedFrom":makeQuery(id+"F3.opPattern","COPY",BODY,{"derivedFrom":makeQuery(id+"F2.opPattern","COPY",BODY,{"derivedFrom":makeQuery(id+"F1.opExtrude","SWEPT_BODY",BODY,{"disambiguationData":[OSD([sQuery(id+"F0.wireOp",EDGE,"E2.bottom"),sQuery(id+"F0.wireOp",EDGE,"E2.top"),sQuery(id+"F0.wireOp",EDGE,"E2.left"),sQuery(id+"F0.wireOp",EDGE,"E2.right")])]}),"instanceName":"1"}),"instanceName":"1"}),"instanceName":"1"}),"instanceName":"1"}),"instanceName":"1"}),"instanceName":"1"}),"instanceName":"1"});
            var Q198;
            Q198=makeQuery(id+"F10.opPattern","COPY",BODY,{"derivedFrom":makeQuery(id+"F8.opPattern","COPY",BODY,{"derivedFrom":makeQuery(id+"F7.opPattern","COPY",BODY,{"derivedFrom":makeQuery(id+"F1.opExtrude","SWEPT_BODY",BODY,{"disambiguationData":[OSD([sQuery(id+"F0.wireOp",EDGE,"E0.bottom"),sQuery(id+"F0.wireOp",EDGE,"E0.top"),sQuery(id+"F0.wireOp",EDGE,"E0.left"),sQuery(id+"F0.wireOp",EDGE,"E0.right")])]}),"instanceName":"1"}),"instanceName":"1"}),"instanceName":"1"});
            var Q199;
            Q199=makeQuery(id+"F10.opPattern","COPY",BODY,{"derivedFrom":makeQuery(id+"F8.opPattern","COPY",BODY,{"derivedFrom":makeQuery(id+"F7.opPattern","COPY",BODY,{"derivedFrom":makeQuery(id+"F1.opExtrude","SWEPT_BODY",BODY,{"disambiguationData":[OSD([sQuery(id+"F0.wireOp",EDGE,"E1.bottom"),sQuery(id+"F0.wireOp",EDGE,"E1.top"),sQuery(id+"F0.wireOp",EDGE,"E1.left"),sQuery(id+"F0.wireOp",EDGE,"E1.right")])]}),"instanceName":"1"}),"instanceName":"1"}),"instanceName":"1"});
            var Q200;
            Q200=makeQuery(id+"F10.opPattern","COPY",BODY,{"derivedFrom":makeQuery(id+"F8.opPattern","COPY",BODY,{"derivedFrom":makeQuery(id+"F7.opPattern","COPY",BODY,{"derivedFrom":makeQuery(id+"F1.opExtrude","SWEPT_BODY",BODY,{"disambiguationData":[OSD([sQuery(id+"F0.wireOp",EDGE,"E2.bottom"),sQuery(id+"F0.wireOp",EDGE,"E2.top"),sQuery(id+"F0.wireOp",EDGE,"E2.left"),sQuery(id+"F0.wireOp",EDGE,"E2.right")])]}),"instanceName":"1"}),"instanceName":"1"}),"instanceName":"1"});
            var Q201;
            Q201=makeQuery(id+"F10.opPattern","COPY",BODY,{"derivedFrom":makeQuery(id+"F8.opPattern","COPY",BODY,{"derivedFrom":makeQuery(id+"F7.opPattern","COPY",BODY,{"derivedFrom":makeQuery(id+"F2.opPattern","COPY",BODY,{"derivedFrom":makeQuery(id+"F1.opExtrude","SWEPT_BODY",BODY,{"disambiguationData":[OSD([sQuery(id+"F0.wireOp",EDGE,"E0.bottom"),sQuery(id+"F0.wireOp",EDGE,"E0.top"),sQuery(id+"F0.wireOp",EDGE,"E0.left"),sQuery(id+"F0.wireOp",EDGE,"E0.right")])]}),"instanceName":"1"}),"instanceName":"1"}),"instanceName":"1"}),"instanceName":"1"});
            var Q202;
            Q202=makeQuery(id+"F10.opPattern","COPY",BODY,{"derivedFrom":makeQuery(id+"F8.opPattern","COPY",BODY,{"derivedFrom":makeQuery(id+"F7.opPattern","COPY",BODY,{"derivedFrom":makeQuery(id+"F2.opPattern","COPY",BODY,{"derivedFrom":makeQuery(id+"F1.opExtrude","SWEPT_BODY",BODY,{"disambiguationData":[OSD([sQuery(id+"F0.wireOp",EDGE,"E1.bottom"),sQuery(id+"F0.wireOp",EDGE,"E1.top"),sQuery(id+"F0.wireOp",EDGE,"E1.left"),sQuery(id+"F0.wireOp",EDGE,"E1.right")])]}),"instanceName":"1"}),"instanceName":"1"}),"instanceName":"1"}),"instanceName":"1"});
            var Q203;
            Q203=makeQuery(id+"F10.opPattern","COPY",BODY,{"derivedFrom":makeQuery(id+"F8.opPattern","COPY",BODY,{"derivedFrom":makeQuery(id+"F7.opPattern","COPY",BODY,{"derivedFrom":makeQuery(id+"F2.opPattern","COPY",BODY,{"derivedFrom":makeQuery(id+"F1.opExtrude","SWEPT_BODY",BODY,{"disambiguationData":[OSD([sQuery(id+"F0.wireOp",EDGE,"E2.bottom"),sQuery(id+"F0.wireOp",EDGE,"E2.top"),sQuery(id+"F0.wireOp",EDGE,"E2.left"),sQuery(id+"F0.wireOp",EDGE,"E2.right")])]}),"instanceName":"1"}),"instanceName":"1"}),"instanceName":"1"}),"instanceName":"1"});
            var Q204;
            Q204=makeQuery(id+"F10.opPattern","COPY",BODY,{"derivedFrom":makeQuery(id+"F8.opPattern","COPY",BODY,{"derivedFrom":makeQuery(id+"F7.opPattern","COPY",BODY,{"derivedFrom":makeQuery(id+"F3.opPattern","COPY",BODY,{"derivedFrom":makeQuery(id+"F2.opPattern","COPY",BODY,{"derivedFrom":makeQuery(id+"F1.opExtrude","SWEPT_BODY",BODY,{"disambiguationData":[OSD([sQuery(id+"F0.wireOp",EDGE,"E0.bottom"),sQuery(id+"F0.wireOp",EDGE,"E0.top"),sQuery(id+"F0.wireOp",EDGE,"E0.left"),sQuery(id+"F0.wireOp",EDGE,"E0.right")])]}),"instanceName":"1"}),"instanceName":"1"}),"instanceName":"1"}),"instanceName":"1"}),"instanceName":"1"});
            var Q205;
            Q205=makeQuery(id+"F10.opPattern","COPY",BODY,{"derivedFrom":makeQuery(id+"F8.opPattern","COPY",BODY,{"derivedFrom":makeQuery(id+"F7.opPattern","COPY",BODY,{"derivedFrom":makeQuery(id+"F3.opPattern","COPY",BODY,{"derivedFrom":makeQuery(id+"F2.opPattern","COPY",BODY,{"derivedFrom":makeQuery(id+"F1.opExtrude","SWEPT_BODY",BODY,{"disambiguationData":[OSD([sQuery(id+"F0.wireOp",EDGE,"E1.bottom"),sQuery(id+"F0.wireOp",EDGE,"E1.top"),sQuery(id+"F0.wireOp",EDGE,"E1.left"),sQuery(id+"F0.wireOp",EDGE,"E1.right")])]}),"instanceName":"1"}),"instanceName":"1"}),"instanceName":"1"}),"instanceName":"1"}),"instanceName":"1"});
            var Q206;
            Q206=makeQuery(id+"F10.opPattern","COPY",BODY,{"derivedFrom":makeQuery(id+"F8.opPattern","COPY",BODY,{"derivedFrom":makeQuery(id+"F7.opPattern","COPY",BODY,{"derivedFrom":makeQuery(id+"F3.opPattern","COPY",BODY,{"derivedFrom":makeQuery(id+"F2.opPattern","COPY",BODY,{"derivedFrom":makeQuery(id+"F1.opExtrude","SWEPT_BODY",BODY,{"disambiguationData":[OSD([sQuery(id+"F0.wireOp",EDGE,"E2.bottom"),sQuery(id+"F0.wireOp",EDGE,"E2.top"),sQuery(id+"F0.wireOp",EDGE,"E2.left"),sQuery(id+"F0.wireOp",EDGE,"E2.right")])]}),"instanceName":"1"}),"instanceName":"1"}),"instanceName":"1"}),"instanceName":"1"}),"instanceName":"1"});
            var Q207;
            Q207=makeQuery(id+"F10.opPattern","COPY",BODY,{"derivedFrom":makeQuery(id+"F8.opPattern","COPY",BODY,{"derivedFrom":makeQuery(id+"F7.opPattern","COPY",BODY,{"derivedFrom":makeQuery(id+"F4.opPattern","COPY",BODY,{"derivedFrom":makeQuery(id+"F3.opPattern","COPY",BODY,{"derivedFrom":makeQuery(id+"F2.opPattern","COPY",BODY,{"derivedFrom":makeQuery(id+"F1.opExtrude","SWEPT_BODY",BODY,{"disambiguationData":[OSD([sQuery(id+"F0.wireOp",EDGE,"E0.bottom"),sQuery(id+"F0.wireOp",EDGE,"E0.top"),sQuery(id+"F0.wireOp",EDGE,"E0.left"),sQuery(id+"F0.wireOp",EDGE,"E0.right")])]}),"instanceName":"1"}),"instanceName":"1"}),"instanceName":"1"}),"instanceName":"1"}),"instanceName":"1"}),"instanceName":"1"});
            var Q208;
            Q208=makeQuery(id+"F10.opPattern","COPY",BODY,{"derivedFrom":makeQuery(id+"F8.opPattern","COPY",BODY,{"derivedFrom":makeQuery(id+"F7.opPattern","COPY",BODY,{"derivedFrom":makeQuery(id+"F4.opPattern","COPY",BODY,{"derivedFrom":makeQuery(id+"F3.opPattern","COPY",BODY,{"derivedFrom":makeQuery(id+"F2.opPattern","COPY",BODY,{"derivedFrom":makeQuery(id+"F1.opExtrude","SWEPT_BODY",BODY,{"disambiguationData":[OSD([sQuery(id+"F0.wireOp",EDGE,"E1.bottom"),sQuery(id+"F0.wireOp",EDGE,"E1.top"),sQuery(id+"F0.wireOp",EDGE,"E1.left"),sQuery(id+"F0.wireOp",EDGE,"E1.right")])]}),"instanceName":"1"}),"instanceName":"1"}),"instanceName":"1"}),"instanceName":"1"}),"instanceName":"1"}),"instanceName":"1"});
            var Q209;
            Q209=makeQuery(id+"F10.opPattern","COPY",BODY,{"derivedFrom":makeQuery(id+"F8.opPattern","COPY",BODY,{"derivedFrom":makeQuery(id+"F7.opPattern","COPY",BODY,{"derivedFrom":makeQuery(id+"F4.opPattern","COPY",BODY,{"derivedFrom":makeQuery(id+"F3.opPattern","COPY",BODY,{"derivedFrom":makeQuery(id+"F2.opPattern","COPY",BODY,{"derivedFrom":makeQuery(id+"F1.opExtrude","SWEPT_BODY",BODY,{"disambiguationData":[OSD([sQuery(id+"F0.wireOp",EDGE,"E2.bottom"),sQuery(id+"F0.wireOp",EDGE,"E2.top"),sQuery(id+"F0.wireOp",EDGE,"E2.left"),sQuery(id+"F0.wireOp",EDGE,"E2.right")])]}),"instanceName":"1"}),"instanceName":"1"}),"instanceName":"1"}),"instanceName":"1"}),"instanceName":"1"}),"instanceName":"1"});
            var Q210;
            Q210=makeQuery(id+"F10.opPattern","COPY",BODY,{"derivedFrom":makeQuery(id+"F8.opPattern","COPY",BODY,{"derivedFrom":makeQuery(id+"F7.opPattern","COPY",BODY,{"derivedFrom":makeQuery(id+"F5.opPattern","COPY",BODY,{"derivedFrom":makeQuery(id+"F4.opPattern","COPY",BODY,{"derivedFrom":makeQuery(id+"F3.opPattern","COPY",BODY,{"derivedFrom":makeQuery(id+"F2.opPattern","COPY",BODY,{"derivedFrom":makeQuery(id+"F1.opExtrude","SWEPT_BODY",BODY,{"disambiguationData":[OSD([sQuery(id+"F0.wireOp",EDGE,"E0.bottom"),sQuery(id+"F0.wireOp",EDGE,"E0.top"),sQuery(id+"F0.wireOp",EDGE,"E0.left"),sQuery(id+"F0.wireOp",EDGE,"E0.right")])]}),"instanceName":"1"}),"instanceName":"1"}),"instanceName":"1"}),"instanceName":"1"}),"instanceName":"1"}),"instanceName":"1"}),"instanceName":"1"});
            var Q211;
            Q211=makeQuery(id+"F10.opPattern","COPY",BODY,{"derivedFrom":makeQuery(id+"F8.opPattern","COPY",BODY,{"derivedFrom":makeQuery(id+"F7.opPattern","COPY",BODY,{"derivedFrom":makeQuery(id+"F5.opPattern","COPY",BODY,{"derivedFrom":makeQuery(id+"F4.opPattern","COPY",BODY,{"derivedFrom":makeQuery(id+"F3.opPattern","COPY",BODY,{"derivedFrom":makeQuery(id+"F2.opPattern","COPY",BODY,{"derivedFrom":makeQuery(id+"F1.opExtrude","SWEPT_BODY",BODY,{"disambiguationData":[OSD([sQuery(id+"F0.wireOp",EDGE,"E1.bottom"),sQuery(id+"F0.wireOp",EDGE,"E1.top"),sQuery(id+"F0.wireOp",EDGE,"E1.left"),sQuery(id+"F0.wireOp",EDGE,"E1.right")])]}),"instanceName":"1"}),"instanceName":"1"}),"instanceName":"1"}),"instanceName":"1"}),"instanceName":"1"}),"instanceName":"1"}),"instanceName":"1"});
            var Q212;
            Q212=makeQuery(id+"F10.opPattern","COPY",BODY,{"derivedFrom":makeQuery(id+"F8.opPattern","COPY",BODY,{"derivedFrom":makeQuery(id+"F7.opPattern","COPY",BODY,{"derivedFrom":makeQuery(id+"F5.opPattern","COPY",BODY,{"derivedFrom":makeQuery(id+"F4.opPattern","COPY",BODY,{"derivedFrom":makeQuery(id+"F3.opPattern","COPY",BODY,{"derivedFrom":makeQuery(id+"F2.opPattern","COPY",BODY,{"derivedFrom":makeQuery(id+"F1.opExtrude","SWEPT_BODY",BODY,{"disambiguationData":[OSD([sQuery(id+"F0.wireOp",EDGE,"E2.bottom"),sQuery(id+"F0.wireOp",EDGE,"E2.top"),sQuery(id+"F0.wireOp",EDGE,"E2.left"),sQuery(id+"F0.wireOp",EDGE,"E2.right")])]}),"instanceName":"1"}),"instanceName":"1"}),"instanceName":"1"}),"instanceName":"1"}),"instanceName":"1"}),"instanceName":"1"}),"instanceName":"1"});
            var Q213;
            Q213=makeQuery(id+"F10.opPattern","COPY",BODY,{"derivedFrom":makeQuery(id+"F8.opPattern","COPY",BODY,{"derivedFrom":makeQuery(id+"F7.opPattern","COPY",BODY,{"derivedFrom":makeQuery(id+"F6.opPattern","COPY",BODY,{"derivedFrom":makeQuery(id+"F5.opPattern","COPY",BODY,{"derivedFrom":makeQuery(id+"F4.opPattern","COPY",BODY,{"derivedFrom":makeQuery(id+"F3.opPattern","COPY",BODY,{"derivedFrom":makeQuery(id+"F2.opPattern","COPY",BODY,{"derivedFrom":makeQuery(id+"F1.opExtrude","SWEPT_BODY",BODY,{"disambiguationData":[OSD([sQuery(id+"F0.wireOp",EDGE,"E0.bottom"),sQuery(id+"F0.wireOp",EDGE,"E0.top"),sQuery(id+"F0.wireOp",EDGE,"E0.left"),sQuery(id+"F0.wireOp",EDGE,"E0.right")])]}),"instanceName":"1"}),"instanceName":"1"}),"instanceName":"1"}),"instanceName":"1"}),"instanceName":"1"}),"instanceName":"1"}),"instanceName":"1"}),"instanceName":"1"});
            var Q214;
            Q214=makeQuery(id+"F10.opPattern","COPY",BODY,{"derivedFrom":makeQuery(id+"F8.opPattern","COPY",BODY,{"derivedFrom":makeQuery(id+"F7.opPattern","COPY",BODY,{"derivedFrom":makeQuery(id+"F6.opPattern","COPY",BODY,{"derivedFrom":makeQuery(id+"F5.opPattern","COPY",BODY,{"derivedFrom":makeQuery(id+"F4.opPattern","COPY",BODY,{"derivedFrom":makeQuery(id+"F3.opPattern","COPY",BODY,{"derivedFrom":makeQuery(id+"F2.opPattern","COPY",BODY,{"derivedFrom":makeQuery(id+"F1.opExtrude","SWEPT_BODY",BODY,{"disambiguationData":[OSD([sQuery(id+"F0.wireOp",EDGE,"E1.bottom"),sQuery(id+"F0.wireOp",EDGE,"E1.top"),sQuery(id+"F0.wireOp",EDGE,"E1.left"),sQuery(id+"F0.wireOp",EDGE,"E1.right")])]}),"instanceName":"1"}),"instanceName":"1"}),"instanceName":"1"}),"instanceName":"1"}),"instanceName":"1"}),"instanceName":"1"}),"instanceName":"1"}),"instanceName":"1"});
            var Q215;
            Q215=makeQuery(id+"F10.opPattern","COPY",BODY,{"derivedFrom":makeQuery(id+"F8.opPattern","COPY",BODY,{"derivedFrom":makeQuery(id+"F7.opPattern","COPY",BODY,{"derivedFrom":makeQuery(id+"F6.opPattern","COPY",BODY,{"derivedFrom":makeQuery(id+"F5.opPattern","COPY",BODY,{"derivedFrom":makeQuery(id+"F4.opPattern","COPY",BODY,{"derivedFrom":makeQuery(id+"F3.opPattern","COPY",BODY,{"derivedFrom":makeQuery(id+"F2.opPattern","COPY",BODY,{"derivedFrom":makeQuery(id+"F1.opExtrude","SWEPT_BODY",BODY,{"disambiguationData":[OSD([sQuery(id+"F0.wireOp",EDGE,"E2.bottom"),sQuery(id+"F0.wireOp",EDGE,"E2.top"),sQuery(id+"F0.wireOp",EDGE,"E2.left"),sQuery(id+"F0.wireOp",EDGE,"E2.right")])]}),"instanceName":"1"}),"instanceName":"1"}),"instanceName":"1"}),"instanceName":"1"}),"instanceName":"1"}),"instanceName":"1"}),"instanceName":"1"}),"instanceName":"1"});
            var Q216;
            Q216=makeQuery(id+"F10.opPattern","COPY",BODY,{"derivedFrom":makeQuery(id+"F9.opPattern","COPY",BODY,{"derivedFrom":makeQuery(id+"F1.opExtrude","SWEPT_BODY",BODY,{"disambiguationData":[OSD([sQuery(id+"F0.wireOp",EDGE,"E0.bottom"),sQuery(id+"F0.wireOp",EDGE,"E0.top"),sQuery(id+"F0.wireOp",EDGE,"E0.left"),sQuery(id+"F0.wireOp",EDGE,"E0.right")])]}),"instanceName":"1"}),"instanceName":"1"});
            var Q217;
            Q217=makeQuery(id+"F10.opPattern","COPY",BODY,{"derivedFrom":makeQuery(id+"F9.opPattern","COPY",BODY,{"derivedFrom":makeQuery(id+"F1.opExtrude","SWEPT_BODY",BODY,{"disambiguationData":[OSD([sQuery(id+"F0.wireOp",EDGE,"E1.bottom"),sQuery(id+"F0.wireOp",EDGE,"E1.top"),sQuery(id+"F0.wireOp",EDGE,"E1.left"),sQuery(id+"F0.wireOp",EDGE,"E1.right")])]}),"instanceName":"1"}),"instanceName":"1"});
            var Q218;
            Q218=makeQuery(id+"F10.opPattern","COPY",BODY,{"derivedFrom":makeQuery(id+"F9.opPattern","COPY",BODY,{"derivedFrom":makeQuery(id+"F1.opExtrude","SWEPT_BODY",BODY,{"disambiguationData":[OSD([sQuery(id+"F0.wireOp",EDGE,"E2.bottom"),sQuery(id+"F0.wireOp",EDGE,"E2.top"),sQuery(id+"F0.wireOp",EDGE,"E2.left"),sQuery(id+"F0.wireOp",EDGE,"E2.right")])]}),"instanceName":"1"}),"instanceName":"1"});
            var Q219;
            Q219=makeQuery(id+"F10.opPattern","COPY",BODY,{"derivedFrom":makeQuery(id+"F9.opPattern","COPY",BODY,{"derivedFrom":makeQuery(id+"F2.opPattern","COPY",BODY,{"derivedFrom":makeQuery(id+"F1.opExtrude","SWEPT_BODY",BODY,{"disambiguationData":[OSD([sQuery(id+"F0.wireOp",EDGE,"E0.bottom"),sQuery(id+"F0.wireOp",EDGE,"E0.top"),sQuery(id+"F0.wireOp",EDGE,"E0.left"),sQuery(id+"F0.wireOp",EDGE,"E0.right")])]}),"instanceName":"1"}),"instanceName":"1"}),"instanceName":"1"});
            var Q220;
            Q220=makeQuery(id+"F10.opPattern","COPY",BODY,{"derivedFrom":makeQuery(id+"F9.opPattern","COPY",BODY,{"derivedFrom":makeQuery(id+"F2.opPattern","COPY",BODY,{"derivedFrom":makeQuery(id+"F1.opExtrude","SWEPT_BODY",BODY,{"disambiguationData":[OSD([sQuery(id+"F0.wireOp",EDGE,"E1.bottom"),sQuery(id+"F0.wireOp",EDGE,"E1.top"),sQuery(id+"F0.wireOp",EDGE,"E1.left"),sQuery(id+"F0.wireOp",EDGE,"E1.right")])]}),"instanceName":"1"}),"instanceName":"1"}),"instanceName":"1"});
            var Q221;
            Q221=makeQuery(id+"F10.opPattern","COPY",BODY,{"derivedFrom":makeQuery(id+"F9.opPattern","COPY",BODY,{"derivedFrom":makeQuery(id+"F2.opPattern","COPY",BODY,{"derivedFrom":makeQuery(id+"F1.opExtrude","SWEPT_BODY",BODY,{"disambiguationData":[OSD([sQuery(id+"F0.wireOp",EDGE,"E2.bottom"),sQuery(id+"F0.wireOp",EDGE,"E2.top"),sQuery(id+"F0.wireOp",EDGE,"E2.left"),sQuery(id+"F0.wireOp",EDGE,"E2.right")])]}),"instanceName":"1"}),"instanceName":"1"}),"instanceName":"1"});
            var Q222;
            Q222=makeQuery(id+"F10.opPattern","COPY",BODY,{"derivedFrom":makeQuery(id+"F9.opPattern","COPY",BODY,{"derivedFrom":makeQuery(id+"F3.opPattern","COPY",BODY,{"derivedFrom":makeQuery(id+"F2.opPattern","COPY",BODY,{"derivedFrom":makeQuery(id+"F1.opExtrude","SWEPT_BODY",BODY,{"disambiguationData":[OSD([sQuery(id+"F0.wireOp",EDGE,"E0.bottom"),sQuery(id+"F0.wireOp",EDGE,"E0.top"),sQuery(id+"F0.wireOp",EDGE,"E0.left"),sQuery(id+"F0.wireOp",EDGE,"E0.right")])]}),"instanceName":"1"}),"instanceName":"1"}),"instanceName":"1"}),"instanceName":"1"});
            var Q223;
            Q223=makeQuery(id+"F10.opPattern","COPY",BODY,{"derivedFrom":makeQuery(id+"F9.opPattern","COPY",BODY,{"derivedFrom":makeQuery(id+"F3.opPattern","COPY",BODY,{"derivedFrom":makeQuery(id+"F2.opPattern","COPY",BODY,{"derivedFrom":makeQuery(id+"F1.opExtrude","SWEPT_BODY",BODY,{"disambiguationData":[OSD([sQuery(id+"F0.wireOp",EDGE,"E1.bottom"),sQuery(id+"F0.wireOp",EDGE,"E1.top"),sQuery(id+"F0.wireOp",EDGE,"E1.left"),sQuery(id+"F0.wireOp",EDGE,"E1.right")])]}),"instanceName":"1"}),"instanceName":"1"}),"instanceName":"1"}),"instanceName":"1"});
            var Q224;
            Q224=makeQuery(id+"F10.opPattern","COPY",BODY,{"derivedFrom":makeQuery(id+"F9.opPattern","COPY",BODY,{"derivedFrom":makeQuery(id+"F3.opPattern","COPY",BODY,{"derivedFrom":makeQuery(id+"F2.opPattern","COPY",BODY,{"derivedFrom":makeQuery(id+"F1.opExtrude","SWEPT_BODY",BODY,{"disambiguationData":[OSD([sQuery(id+"F0.wireOp",EDGE,"E2.bottom"),sQuery(id+"F0.wireOp",EDGE,"E2.top"),sQuery(id+"F0.wireOp",EDGE,"E2.left"),sQuery(id+"F0.wireOp",EDGE,"E2.right")])]}),"instanceName":"1"}),"instanceName":"1"}),"instanceName":"1"}),"instanceName":"1"});
            var Q225;
            Q225=makeQuery(id+"F10.opPattern","COPY",BODY,{"derivedFrom":makeQuery(id+"F9.opPattern","COPY",BODY,{"derivedFrom":makeQuery(id+"F4.opPattern","COPY",BODY,{"derivedFrom":makeQuery(id+"F3.opPattern","COPY",BODY,{"derivedFrom":makeQuery(id+"F2.opPattern","COPY",BODY,{"derivedFrom":makeQuery(id+"F1.opExtrude","SWEPT_BODY",BODY,{"disambiguationData":[OSD([sQuery(id+"F0.wireOp",EDGE,"E0.bottom"),sQuery(id+"F0.wireOp",EDGE,"E0.top"),sQuery(id+"F0.wireOp",EDGE,"E0.left"),sQuery(id+"F0.wireOp",EDGE,"E0.right")])]}),"instanceName":"1"}),"instanceName":"1"}),"instanceName":"1"}),"instanceName":"1"}),"instanceName":"1"});
            var Q226;
            Q226=makeQuery(id+"F10.opPattern","COPY",BODY,{"derivedFrom":makeQuery(id+"F9.opPattern","COPY",BODY,{"derivedFrom":makeQuery(id+"F4.opPattern","COPY",BODY,{"derivedFrom":makeQuery(id+"F3.opPattern","COPY",BODY,{"derivedFrom":makeQuery(id+"F2.opPattern","COPY",BODY,{"derivedFrom":makeQuery(id+"F1.opExtrude","SWEPT_BODY",BODY,{"disambiguationData":[OSD([sQuery(id+"F0.wireOp",EDGE,"E1.bottom"),sQuery(id+"F0.wireOp",EDGE,"E1.top"),sQuery(id+"F0.wireOp",EDGE,"E1.left"),sQuery(id+"F0.wireOp",EDGE,"E1.right")])]}),"instanceName":"1"}),"instanceName":"1"}),"instanceName":"1"}),"instanceName":"1"}),"instanceName":"1"});
            var Q227;
            Q227=makeQuery(id+"F10.opPattern","COPY",BODY,{"derivedFrom":makeQuery(id+"F9.opPattern","COPY",BODY,{"derivedFrom":makeQuery(id+"F4.opPattern","COPY",BODY,{"derivedFrom":makeQuery(id+"F3.opPattern","COPY",BODY,{"derivedFrom":makeQuery(id+"F2.opPattern","COPY",BODY,{"derivedFrom":makeQuery(id+"F1.opExtrude","SWEPT_BODY",BODY,{"disambiguationData":[OSD([sQuery(id+"F0.wireOp",EDGE,"E2.bottom"),sQuery(id+"F0.wireOp",EDGE,"E2.top"),sQuery(id+"F0.wireOp",EDGE,"E2.left"),sQuery(id+"F0.wireOp",EDGE,"E2.right")])]}),"instanceName":"1"}),"instanceName":"1"}),"instanceName":"1"}),"instanceName":"1"}),"instanceName":"1"});
            var Q228;
            Q228=makeQuery(id+"F10.opPattern","COPY",BODY,{"derivedFrom":makeQuery(id+"F9.opPattern","COPY",BODY,{"derivedFrom":makeQuery(id+"F5.opPattern","COPY",BODY,{"derivedFrom":makeQuery(id+"F4.opPattern","COPY",BODY,{"derivedFrom":makeQuery(id+"F3.opPattern","COPY",BODY,{"derivedFrom":makeQuery(id+"F2.opPattern","COPY",BODY,{"derivedFrom":makeQuery(id+"F1.opExtrude","SWEPT_BODY",BODY,{"disambiguationData":[OSD([sQuery(id+"F0.wireOp",EDGE,"E0.bottom"),sQuery(id+"F0.wireOp",EDGE,"E0.top"),sQuery(id+"F0.wireOp",EDGE,"E0.left"),sQuery(id+"F0.wireOp",EDGE,"E0.right")])]}),"instanceName":"1"}),"instanceName":"1"}),"instanceName":"1"}),"instanceName":"1"}),"instanceName":"1"}),"instanceName":"1"});
            var Q229;
            Q229=makeQuery(id+"F10.opPattern","COPY",BODY,{"derivedFrom":makeQuery(id+"F9.opPattern","COPY",BODY,{"derivedFrom":makeQuery(id+"F5.opPattern","COPY",BODY,{"derivedFrom":makeQuery(id+"F4.opPattern","COPY",BODY,{"derivedFrom":makeQuery(id+"F3.opPattern","COPY",BODY,{"derivedFrom":makeQuery(id+"F2.opPattern","COPY",BODY,{"derivedFrom":makeQuery(id+"F1.opExtrude","SWEPT_BODY",BODY,{"disambiguationData":[OSD([sQuery(id+"F0.wireOp",EDGE,"E1.bottom"),sQuery(id+"F0.wireOp",EDGE,"E1.top"),sQuery(id+"F0.wireOp",EDGE,"E1.left"),sQuery(id+"F0.wireOp",EDGE,"E1.right")])]}),"instanceName":"1"}),"instanceName":"1"}),"instanceName":"1"}),"instanceName":"1"}),"instanceName":"1"}),"instanceName":"1"});
            var Q230;
            Q230=makeQuery(id+"F10.opPattern","COPY",BODY,{"derivedFrom":makeQuery(id+"F9.opPattern","COPY",BODY,{"derivedFrom":makeQuery(id+"F5.opPattern","COPY",BODY,{"derivedFrom":makeQuery(id+"F4.opPattern","COPY",BODY,{"derivedFrom":makeQuery(id+"F3.opPattern","COPY",BODY,{"derivedFrom":makeQuery(id+"F2.opPattern","COPY",BODY,{"derivedFrom":makeQuery(id+"F1.opExtrude","SWEPT_BODY",BODY,{"disambiguationData":[OSD([sQuery(id+"F0.wireOp",EDGE,"E2.bottom"),sQuery(id+"F0.wireOp",EDGE,"E2.top"),sQuery(id+"F0.wireOp",EDGE,"E2.left"),sQuery(id+"F0.wireOp",EDGE,"E2.right")])]}),"instanceName":"1"}),"instanceName":"1"}),"instanceName":"1"}),"instanceName":"1"}),"instanceName":"1"}),"instanceName":"1"});
            var Q231;
            Q231=makeQuery(id+"F10.opPattern","COPY",BODY,{"derivedFrom":makeQuery(id+"F9.opPattern","COPY",BODY,{"derivedFrom":makeQuery(id+"F6.opPattern","COPY",BODY,{"derivedFrom":makeQuery(id+"F5.opPattern","COPY",BODY,{"derivedFrom":makeQuery(id+"F4.opPattern","COPY",BODY,{"derivedFrom":makeQuery(id+"F3.opPattern","COPY",BODY,{"derivedFrom":makeQuery(id+"F2.opPattern","COPY",BODY,{"derivedFrom":makeQuery(id+"F1.opExtrude","SWEPT_BODY",BODY,{"disambiguationData":[OSD([sQuery(id+"F0.wireOp",EDGE,"E0.bottom"),sQuery(id+"F0.wireOp",EDGE,"E0.top"),sQuery(id+"F0.wireOp",EDGE,"E0.left"),sQuery(id+"F0.wireOp",EDGE,"E0.right")])]}),"instanceName":"1"}),"instanceName":"1"}),"instanceName":"1"}),"instanceName":"1"}),"instanceName":"1"}),"instanceName":"1"}),"instanceName":"1"});
            var Q232;
            Q232=makeQuery(id+"F10.opPattern","COPY",BODY,{"derivedFrom":makeQuery(id+"F9.opPattern","COPY",BODY,{"derivedFrom":makeQuery(id+"F6.opPattern","COPY",BODY,{"derivedFrom":makeQuery(id+"F5.opPattern","COPY",BODY,{"derivedFrom":makeQuery(id+"F4.opPattern","COPY",BODY,{"derivedFrom":makeQuery(id+"F3.opPattern","COPY",BODY,{"derivedFrom":makeQuery(id+"F2.opPattern","COPY",BODY,{"derivedFrom":makeQuery(id+"F1.opExtrude","SWEPT_BODY",BODY,{"disambiguationData":[OSD([sQuery(id+"F0.wireOp",EDGE,"E1.bottom"),sQuery(id+"F0.wireOp",EDGE,"E1.top"),sQuery(id+"F0.wireOp",EDGE,"E1.left"),sQuery(id+"F0.wireOp",EDGE,"E1.right")])]}),"instanceName":"1"}),"instanceName":"1"}),"instanceName":"1"}),"instanceName":"1"}),"instanceName":"1"}),"instanceName":"1"}),"instanceName":"1"});
            var Q233;
            Q233=makeQuery(id+"F10.opPattern","COPY",BODY,{"derivedFrom":makeQuery(id+"F9.opPattern","COPY",BODY,{"derivedFrom":makeQuery(id+"F6.opPattern","COPY",BODY,{"derivedFrom":makeQuery(id+"F5.opPattern","COPY",BODY,{"derivedFrom":makeQuery(id+"F4.opPattern","COPY",BODY,{"derivedFrom":makeQuery(id+"F3.opPattern","COPY",BODY,{"derivedFrom":makeQuery(id+"F2.opPattern","COPY",BODY,{"derivedFrom":makeQuery(id+"F1.opExtrude","SWEPT_BODY",BODY,{"disambiguationData":[OSD([sQuery(id+"F0.wireOp",EDGE,"E2.bottom"),sQuery(id+"F0.wireOp",EDGE,"E2.top"),sQuery(id+"F0.wireOp",EDGE,"E2.left"),sQuery(id+"F0.wireOp",EDGE,"E2.right")])]}),"instanceName":"1"}),"instanceName":"1"}),"instanceName":"1"}),"instanceName":"1"}),"instanceName":"1"}),"instanceName":"1"}),"instanceName":"1"});
            var Q234;
            Q234=makeQuery(id+"F10.opPattern","COPY",BODY,{"derivedFrom":makeQuery(id+"F9.opPattern","COPY",BODY,{"derivedFrom":makeQuery(id+"F7.opPattern","COPY",BODY,{"derivedFrom":makeQuery(id+"F1.opExtrude","SWEPT_BODY",BODY,{"disambiguationData":[OSD([sQuery(id+"F0.wireOp",EDGE,"E0.bottom"),sQuery(id+"F0.wireOp",EDGE,"E0.top"),sQuery(id+"F0.wireOp",EDGE,"E0.left"),sQuery(id+"F0.wireOp",EDGE,"E0.right")])]}),"instanceName":"1"}),"instanceName":"1"}),"instanceName":"1"});
            var Q235;
            Q235=makeQuery(id+"F10.opPattern","COPY",BODY,{"derivedFrom":makeQuery(id+"F9.opPattern","COPY",BODY,{"derivedFrom":makeQuery(id+"F7.opPattern","COPY",BODY,{"derivedFrom":makeQuery(id+"F1.opExtrude","SWEPT_BODY",BODY,{"disambiguationData":[OSD([sQuery(id+"F0.wireOp",EDGE,"E1.bottom"),sQuery(id+"F0.wireOp",EDGE,"E1.top"),sQuery(id+"F0.wireOp",EDGE,"E1.left"),sQuery(id+"F0.wireOp",EDGE,"E1.right")])]}),"instanceName":"1"}),"instanceName":"1"}),"instanceName":"1"});
            var Q236;
            Q236=makeQuery(id+"F10.opPattern","COPY",BODY,{"derivedFrom":makeQuery(id+"F9.opPattern","COPY",BODY,{"derivedFrom":makeQuery(id+"F7.opPattern","COPY",BODY,{"derivedFrom":makeQuery(id+"F1.opExtrude","SWEPT_BODY",BODY,{"disambiguationData":[OSD([sQuery(id+"F0.wireOp",EDGE,"E2.bottom"),sQuery(id+"F0.wireOp",EDGE,"E2.top"),sQuery(id+"F0.wireOp",EDGE,"E2.left"),sQuery(id+"F0.wireOp",EDGE,"E2.right")])]}),"instanceName":"1"}),"instanceName":"1"}),"instanceName":"1"});
            var Q237;
            Q237=makeQuery(id+"F10.opPattern","COPY",BODY,{"derivedFrom":makeQuery(id+"F9.opPattern","COPY",BODY,{"derivedFrom":makeQuery(id+"F7.opPattern","COPY",BODY,{"derivedFrom":makeQuery(id+"F2.opPattern","COPY",BODY,{"derivedFrom":makeQuery(id+"F1.opExtrude","SWEPT_BODY",BODY,{"disambiguationData":[OSD([sQuery(id+"F0.wireOp",EDGE,"E0.bottom"),sQuery(id+"F0.wireOp",EDGE,"E0.top"),sQuery(id+"F0.wireOp",EDGE,"E0.left"),sQuery(id+"F0.wireOp",EDGE,"E0.right")])]}),"instanceName":"1"}),"instanceName":"1"}),"instanceName":"1"}),"instanceName":"1"});
            var Q238;
            Q238=makeQuery(id+"F10.opPattern","COPY",BODY,{"derivedFrom":makeQuery(id+"F9.opPattern","COPY",BODY,{"derivedFrom":makeQuery(id+"F7.opPattern","COPY",BODY,{"derivedFrom":makeQuery(id+"F2.opPattern","COPY",BODY,{"derivedFrom":makeQuery(id+"F1.opExtrude","SWEPT_BODY",BODY,{"disambiguationData":[OSD([sQuery(id+"F0.wireOp",EDGE,"E1.bottom"),sQuery(id+"F0.wireOp",EDGE,"E1.top"),sQuery(id+"F0.wireOp",EDGE,"E1.left"),sQuery(id+"F0.wireOp",EDGE,"E1.right")])]}),"instanceName":"1"}),"instanceName":"1"}),"instanceName":"1"}),"instanceName":"1"});
            var Q239;
            Q239=makeQuery(id+"F10.opPattern","COPY",BODY,{"derivedFrom":makeQuery(id+"F9.opPattern","COPY",BODY,{"derivedFrom":makeQuery(id+"F7.opPattern","COPY",BODY,{"derivedFrom":makeQuery(id+"F2.opPattern","COPY",BODY,{"derivedFrom":makeQuery(id+"F1.opExtrude","SWEPT_BODY",BODY,{"disambiguationData":[OSD([sQuery(id+"F0.wireOp",EDGE,"E2.bottom"),sQuery(id+"F0.wireOp",EDGE,"E2.top"),sQuery(id+"F0.wireOp",EDGE,"E2.left"),sQuery(id+"F0.wireOp",EDGE,"E2.right")])]}),"instanceName":"1"}),"instanceName":"1"}),"instanceName":"1"}),"instanceName":"1"});
            var Q240;
            Q240=makeQuery(id+"F10.opPattern","COPY",BODY,{"derivedFrom":makeQuery(id+"F9.opPattern","COPY",BODY,{"derivedFrom":makeQuery(id+"F7.opPattern","COPY",BODY,{"derivedFrom":makeQuery(id+"F3.opPattern","COPY",BODY,{"derivedFrom":makeQuery(id+"F2.opPattern","COPY",BODY,{"derivedFrom":makeQuery(id+"F1.opExtrude","SWEPT_BODY",BODY,{"disambiguationData":[OSD([sQuery(id+"F0.wireOp",EDGE,"E0.bottom"),sQuery(id+"F0.wireOp",EDGE,"E0.top"),sQuery(id+"F0.wireOp",EDGE,"E0.left"),sQuery(id+"F0.wireOp",EDGE,"E0.right")])]}),"instanceName":"1"}),"instanceName":"1"}),"instanceName":"1"}),"instanceName":"1"}),"instanceName":"1"});
            var Q241;
            Q241=makeQuery(id+"F10.opPattern","COPY",BODY,{"derivedFrom":makeQuery(id+"F9.opPattern","COPY",BODY,{"derivedFrom":makeQuery(id+"F7.opPattern","COPY",BODY,{"derivedFrom":makeQuery(id+"F3.opPattern","COPY",BODY,{"derivedFrom":makeQuery(id+"F2.opPattern","COPY",BODY,{"derivedFrom":makeQuery(id+"F1.opExtrude","SWEPT_BODY",BODY,{"disambiguationData":[OSD([sQuery(id+"F0.wireOp",EDGE,"E1.bottom"),sQuery(id+"F0.wireOp",EDGE,"E1.top"),sQuery(id+"F0.wireOp",EDGE,"E1.left"),sQuery(id+"F0.wireOp",EDGE,"E1.right")])]}),"instanceName":"1"}),"instanceName":"1"}),"instanceName":"1"}),"instanceName":"1"}),"instanceName":"1"});
            var Q242;
            Q242=makeQuery(id+"F10.opPattern","COPY",BODY,{"derivedFrom":makeQuery(id+"F9.opPattern","COPY",BODY,{"derivedFrom":makeQuery(id+"F7.opPattern","COPY",BODY,{"derivedFrom":makeQuery(id+"F3.opPattern","COPY",BODY,{"derivedFrom":makeQuery(id+"F2.opPattern","COPY",BODY,{"derivedFrom":makeQuery(id+"F1.opExtrude","SWEPT_BODY",BODY,{"disambiguationData":[OSD([sQuery(id+"F0.wireOp",EDGE,"E2.bottom"),sQuery(id+"F0.wireOp",EDGE,"E2.top"),sQuery(id+"F0.wireOp",EDGE,"E2.left"),sQuery(id+"F0.wireOp",EDGE,"E2.right")])]}),"instanceName":"1"}),"instanceName":"1"}),"instanceName":"1"}),"instanceName":"1"}),"instanceName":"1"});
            var Q243;
            Q243=makeQuery(id+"F10.opPattern","COPY",BODY,{"derivedFrom":makeQuery(id+"F9.opPattern","COPY",BODY,{"derivedFrom":makeQuery(id+"F7.opPattern","COPY",BODY,{"derivedFrom":makeQuery(id+"F4.opPattern","COPY",BODY,{"derivedFrom":makeQuery(id+"F3.opPattern","COPY",BODY,{"derivedFrom":makeQuery(id+"F2.opPattern","COPY",BODY,{"derivedFrom":makeQuery(id+"F1.opExtrude","SWEPT_BODY",BODY,{"disambiguationData":[OSD([sQuery(id+"F0.wireOp",EDGE,"E0.bottom"),sQuery(id+"F0.wireOp",EDGE,"E0.top"),sQuery(id+"F0.wireOp",EDGE,"E0.left"),sQuery(id+"F0.wireOp",EDGE,"E0.right")])]}),"instanceName":"1"}),"instanceName":"1"}),"instanceName":"1"}),"instanceName":"1"}),"instanceName":"1"}),"instanceName":"1"});
            var Q244;
            Q244=makeQuery(id+"F10.opPattern","COPY",BODY,{"derivedFrom":makeQuery(id+"F9.opPattern","COPY",BODY,{"derivedFrom":makeQuery(id+"F7.opPattern","COPY",BODY,{"derivedFrom":makeQuery(id+"F4.opPattern","COPY",BODY,{"derivedFrom":makeQuery(id+"F3.opPattern","COPY",BODY,{"derivedFrom":makeQuery(id+"F2.opPattern","COPY",BODY,{"derivedFrom":makeQuery(id+"F1.opExtrude","SWEPT_BODY",BODY,{"disambiguationData":[OSD([sQuery(id+"F0.wireOp",EDGE,"E1.bottom"),sQuery(id+"F0.wireOp",EDGE,"E1.top"),sQuery(id+"F0.wireOp",EDGE,"E1.left"),sQuery(id+"F0.wireOp",EDGE,"E1.right")])]}),"instanceName":"1"}),"instanceName":"1"}),"instanceName":"1"}),"instanceName":"1"}),"instanceName":"1"}),"instanceName":"1"});
            var Q245;
            Q245=makeQuery(id+"F10.opPattern","COPY",BODY,{"derivedFrom":makeQuery(id+"F9.opPattern","COPY",BODY,{"derivedFrom":makeQuery(id+"F7.opPattern","COPY",BODY,{"derivedFrom":makeQuery(id+"F4.opPattern","COPY",BODY,{"derivedFrom":makeQuery(id+"F3.opPattern","COPY",BODY,{"derivedFrom":makeQuery(id+"F2.opPattern","COPY",BODY,{"derivedFrom":makeQuery(id+"F1.opExtrude","SWEPT_BODY",BODY,{"disambiguationData":[OSD([sQuery(id+"F0.wireOp",EDGE,"E2.bottom"),sQuery(id+"F0.wireOp",EDGE,"E2.top"),sQuery(id+"F0.wireOp",EDGE,"E2.left"),sQuery(id+"F0.wireOp",EDGE,"E2.right")])]}),"instanceName":"1"}),"instanceName":"1"}),"instanceName":"1"}),"instanceName":"1"}),"instanceName":"1"}),"instanceName":"1"});
            var Q246;
            Q246=makeQuery(id+"F10.opPattern","COPY",BODY,{"derivedFrom":makeQuery(id+"F9.opPattern","COPY",BODY,{"derivedFrom":makeQuery(id+"F7.opPattern","COPY",BODY,{"derivedFrom":makeQuery(id+"F5.opPattern","COPY",BODY,{"derivedFrom":makeQuery(id+"F4.opPattern","COPY",BODY,{"derivedFrom":makeQuery(id+"F3.opPattern","COPY",BODY,{"derivedFrom":makeQuery(id+"F2.opPattern","COPY",BODY,{"derivedFrom":makeQuery(id+"F1.opExtrude","SWEPT_BODY",BODY,{"disambiguationData":[OSD([sQuery(id+"F0.wireOp",EDGE,"E0.bottom"),sQuery(id+"F0.wireOp",EDGE,"E0.top"),sQuery(id+"F0.wireOp",EDGE,"E0.left"),sQuery(id+"F0.wireOp",EDGE,"E0.right")])]}),"instanceName":"1"}),"instanceName":"1"}),"instanceName":"1"}),"instanceName":"1"}),"instanceName":"1"}),"instanceName":"1"}),"instanceName":"1"});
            var Q247;
            Q247=makeQuery(id+"F10.opPattern","COPY",BODY,{"derivedFrom":makeQuery(id+"F9.opPattern","COPY",BODY,{"derivedFrom":makeQuery(id+"F7.opPattern","COPY",BODY,{"derivedFrom":makeQuery(id+"F5.opPattern","COPY",BODY,{"derivedFrom":makeQuery(id+"F4.opPattern","COPY",BODY,{"derivedFrom":makeQuery(id+"F3.opPattern","COPY",BODY,{"derivedFrom":makeQuery(id+"F2.opPattern","COPY",BODY,{"derivedFrom":makeQuery(id+"F1.opExtrude","SWEPT_BODY",BODY,{"disambiguationData":[OSD([sQuery(id+"F0.wireOp",EDGE,"E1.bottom"),sQuery(id+"F0.wireOp",EDGE,"E1.top"),sQuery(id+"F0.wireOp",EDGE,"E1.left"),sQuery(id+"F0.wireOp",EDGE,"E1.right")])]}),"instanceName":"1"}),"instanceName":"1"}),"instanceName":"1"}),"instanceName":"1"}),"instanceName":"1"}),"instanceName":"1"}),"instanceName":"1"});
            var Q248;
            Q248=makeQuery(id+"F10.opPattern","COPY",BODY,{"derivedFrom":makeQuery(id+"F9.opPattern","COPY",BODY,{"derivedFrom":makeQuery(id+"F7.opPattern","COPY",BODY,{"derivedFrom":makeQuery(id+"F5.opPattern","COPY",BODY,{"derivedFrom":makeQuery(id+"F4.opPattern","COPY",BODY,{"derivedFrom":makeQuery(id+"F3.opPattern","COPY",BODY,{"derivedFrom":makeQuery(id+"F2.opPattern","COPY",BODY,{"derivedFrom":makeQuery(id+"F1.opExtrude","SWEPT_BODY",BODY,{"disambiguationData":[OSD([sQuery(id+"F0.wireOp",EDGE,"E2.bottom"),sQuery(id+"F0.wireOp",EDGE,"E2.top"),sQuery(id+"F0.wireOp",EDGE,"E2.left"),sQuery(id+"F0.wireOp",EDGE,"E2.right")])]}),"instanceName":"1"}),"instanceName":"1"}),"instanceName":"1"}),"instanceName":"1"}),"instanceName":"1"}),"instanceName":"1"}),"instanceName":"1"});
            var Q249;
            Q249=makeQuery(id+"F10.opPattern","COPY",BODY,{"derivedFrom":makeQuery(id+"F9.opPattern","COPY",BODY,{"derivedFrom":makeQuery(id+"F7.opPattern","COPY",BODY,{"derivedFrom":makeQuery(id+"F6.opPattern","COPY",BODY,{"derivedFrom":makeQuery(id+"F5.opPattern","COPY",BODY,{"derivedFrom":makeQuery(id+"F4.opPattern","COPY",BODY,{"derivedFrom":makeQuery(id+"F3.opPattern","COPY",BODY,{"derivedFrom":makeQuery(id+"F2.opPattern","COPY",BODY,{"derivedFrom":makeQuery(id+"F1.opExtrude","SWEPT_BODY",BODY,{"disambiguationData":[OSD([sQuery(id+"F0.wireOp",EDGE,"E0.bottom"),sQuery(id+"F0.wireOp",EDGE,"E0.top"),sQuery(id+"F0.wireOp",EDGE,"E0.left"),sQuery(id+"F0.wireOp",EDGE,"E0.right")])]}),"instanceName":"1"}),"instanceName":"1"}),"instanceName":"1"}),"instanceName":"1"}),"instanceName":"1"}),"instanceName":"1"}),"instanceName":"1"}),"instanceName":"1"});
            var Q250;
            Q250=makeQuery(id+"F10.opPattern","COPY",BODY,{"derivedFrom":makeQuery(id+"F9.opPattern","COPY",BODY,{"derivedFrom":makeQuery(id+"F7.opPattern","COPY",BODY,{"derivedFrom":makeQuery(id+"F6.opPattern","COPY",BODY,{"derivedFrom":makeQuery(id+"F5.opPattern","COPY",BODY,{"derivedFrom":makeQuery(id+"F4.opPattern","COPY",BODY,{"derivedFrom":makeQuery(id+"F3.opPattern","COPY",BODY,{"derivedFrom":makeQuery(id+"F2.opPattern","COPY",BODY,{"derivedFrom":makeQuery(id+"F1.opExtrude","SWEPT_BODY",BODY,{"disambiguationData":[OSD([sQuery(id+"F0.wireOp",EDGE,"E1.bottom"),sQuery(id+"F0.wireOp",EDGE,"E1.top"),sQuery(id+"F0.wireOp",EDGE,"E1.left"),sQuery(id+"F0.wireOp",EDGE,"E1.right")])]}),"instanceName":"1"}),"instanceName":"1"}),"instanceName":"1"}),"instanceName":"1"}),"instanceName":"1"}),"instanceName":"1"}),"instanceName":"1"}),"instanceName":"1"});
            var Q251;
            Q251=makeQuery(id+"F10.opPattern","COPY",BODY,{"derivedFrom":makeQuery(id+"F9.opPattern","COPY",BODY,{"derivedFrom":makeQuery(id+"F7.opPattern","COPY",BODY,{"derivedFrom":makeQuery(id+"F6.opPattern","COPY",BODY,{"derivedFrom":makeQuery(id+"F5.opPattern","COPY",BODY,{"derivedFrom":makeQuery(id+"F4.opPattern","COPY",BODY,{"derivedFrom":makeQuery(id+"F3.opPattern","COPY",BODY,{"derivedFrom":makeQuery(id+"F2.opPattern","COPY",BODY,{"derivedFrom":makeQuery(id+"F1.opExtrude","SWEPT_BODY",BODY,{"disambiguationData":[OSD([sQuery(id+"F0.wireOp",EDGE,"E2.bottom"),sQuery(id+"F0.wireOp",EDGE,"E2.top"),sQuery(id+"F0.wireOp",EDGE,"E2.left"),sQuery(id+"F0.wireOp",EDGE,"E2.right")])]}),"instanceName":"1"}),"instanceName":"1"}),"instanceName":"1"}),"instanceName":"1"}),"instanceName":"1"}),"instanceName":"1"}),"instanceName":"1"}),"instanceName":"1"});
            var Q252;
            Q252=makeQuery(id+"F10.opPattern","COPY",BODY,{"derivedFrom":makeQuery(id+"F9.opPattern","COPY",BODY,{"derivedFrom":makeQuery(id+"F8.opPattern","COPY",BODY,{"derivedFrom":makeQuery(id+"F1.opExtrude","SWEPT_BODY",BODY,{"disambiguationData":[OSD([sQuery(id+"F0.wireOp",EDGE,"E0.bottom"),sQuery(id+"F0.wireOp",EDGE,"E0.top"),sQuery(id+"F0.wireOp",EDGE,"E0.left"),sQuery(id+"F0.wireOp",EDGE,"E0.right")])]}),"instanceName":"1"}),"instanceName":"1"}),"instanceName":"1"});
            var Q253;
            Q253=makeQuery(id+"F10.opPattern","COPY",BODY,{"derivedFrom":makeQuery(id+"F9.opPattern","COPY",BODY,{"derivedFrom":makeQuery(id+"F8.opPattern","COPY",BODY,{"derivedFrom":makeQuery(id+"F1.opExtrude","SWEPT_BODY",BODY,{"disambiguationData":[OSD([sQuery(id+"F0.wireOp",EDGE,"E1.bottom"),sQuery(id+"F0.wireOp",EDGE,"E1.top"),sQuery(id+"F0.wireOp",EDGE,"E1.left"),sQuery(id+"F0.wireOp",EDGE,"E1.right")])]}),"instanceName":"1"}),"instanceName":"1"}),"instanceName":"1"});
            var Q254;
            Q254=makeQuery(id+"F10.opPattern","COPY",BODY,{"derivedFrom":makeQuery(id+"F9.opPattern","COPY",BODY,{"derivedFrom":makeQuery(id+"F8.opPattern","COPY",BODY,{"derivedFrom":makeQuery(id+"F1.opExtrude","SWEPT_BODY",BODY,{"disambiguationData":[OSD([sQuery(id+"F0.wireOp",EDGE,"E2.bottom"),sQuery(id+"F0.wireOp",EDGE,"E2.top"),sQuery(id+"F0.wireOp",EDGE,"E2.left"),sQuery(id+"F0.wireOp",EDGE,"E2.right")])]}),"instanceName":"1"}),"instanceName":"1"}),"instanceName":"1"});
            var Q255;
            Q255=makeQuery(id+"F10.opPattern","COPY",BODY,{"derivedFrom":makeQuery(id+"F9.opPattern","COPY",BODY,{"derivedFrom":makeQuery(id+"F8.opPattern","COPY",BODY,{"derivedFrom":makeQuery(id+"F2.opPattern","COPY",BODY,{"derivedFrom":makeQuery(id+"F1.opExtrude","SWEPT_BODY",BODY,{"disambiguationData":[OSD([sQuery(id+"F0.wireOp",EDGE,"E0.bottom"),sQuery(id+"F0.wireOp",EDGE,"E0.top"),sQuery(id+"F0.wireOp",EDGE,"E0.left"),sQuery(id+"F0.wireOp",EDGE,"E0.right")])]}),"instanceName":"1"}),"instanceName":"1"}),"instanceName":"1"}),"instanceName":"1"});
            var Q256;
            Q256=makeQuery(id+"F10.opPattern","COPY",BODY,{"derivedFrom":makeQuery(id+"F9.opPattern","COPY",BODY,{"derivedFrom":makeQuery(id+"F8.opPattern","COPY",BODY,{"derivedFrom":makeQuery(id+"F2.opPattern","COPY",BODY,{"derivedFrom":makeQuery(id+"F1.opExtrude","SWEPT_BODY",BODY,{"disambiguationData":[OSD([sQuery(id+"F0.wireOp",EDGE,"E1.bottom"),sQuery(id+"F0.wireOp",EDGE,"E1.top"),sQuery(id+"F0.wireOp",EDGE,"E1.left"),sQuery(id+"F0.wireOp",EDGE,"E1.right")])]}),"instanceName":"1"}),"instanceName":"1"}),"instanceName":"1"}),"instanceName":"1"});
            var Q257;
            Q257=makeQuery(id+"F10.opPattern","COPY",BODY,{"derivedFrom":makeQuery(id+"F9.opPattern","COPY",BODY,{"derivedFrom":makeQuery(id+"F8.opPattern","COPY",BODY,{"derivedFrom":makeQuery(id+"F2.opPattern","COPY",BODY,{"derivedFrom":makeQuery(id+"F1.opExtrude","SWEPT_BODY",BODY,{"disambiguationData":[OSD([sQuery(id+"F0.wireOp",EDGE,"E2.bottom"),sQuery(id+"F0.wireOp",EDGE,"E2.top"),sQuery(id+"F0.wireOp",EDGE,"E2.left"),sQuery(id+"F0.wireOp",EDGE,"E2.right")])]}),"instanceName":"1"}),"instanceName":"1"}),"instanceName":"1"}),"instanceName":"1"});
            var Q258;
            Q258=makeQuery(id+"F10.opPattern","COPY",BODY,{"derivedFrom":makeQuery(id+"F9.opPattern","COPY",BODY,{"derivedFrom":makeQuery(id+"F8.opPattern","COPY",BODY,{"derivedFrom":makeQuery(id+"F3.opPattern","COPY",BODY,{"derivedFrom":makeQuery(id+"F2.opPattern","COPY",BODY,{"derivedFrom":makeQuery(id+"F1.opExtrude","SWEPT_BODY",BODY,{"disambiguationData":[OSD([sQuery(id+"F0.wireOp",EDGE,"E0.bottom"),sQuery(id+"F0.wireOp",EDGE,"E0.top"),sQuery(id+"F0.wireOp",EDGE,"E0.left"),sQuery(id+"F0.wireOp",EDGE,"E0.right")])]}),"instanceName":"1"}),"instanceName":"1"}),"instanceName":"1"}),"instanceName":"1"}),"instanceName":"1"});
            var Q259;
            Q259=makeQuery(id+"F10.opPattern","COPY",BODY,{"derivedFrom":makeQuery(id+"F9.opPattern","COPY",BODY,{"derivedFrom":makeQuery(id+"F8.opPattern","COPY",BODY,{"derivedFrom":makeQuery(id+"F3.opPattern","COPY",BODY,{"derivedFrom":makeQuery(id+"F2.opPattern","COPY",BODY,{"derivedFrom":makeQuery(id+"F1.opExtrude","SWEPT_BODY",BODY,{"disambiguationData":[OSD([sQuery(id+"F0.wireOp",EDGE,"E1.bottom"),sQuery(id+"F0.wireOp",EDGE,"E1.top"),sQuery(id+"F0.wireOp",EDGE,"E1.left"),sQuery(id+"F0.wireOp",EDGE,"E1.right")])]}),"instanceName":"1"}),"instanceName":"1"}),"instanceName":"1"}),"instanceName":"1"}),"instanceName":"1"});
            var Q260;
            Q260=makeQuery(id+"F10.opPattern","COPY",BODY,{"derivedFrom":makeQuery(id+"F9.opPattern","COPY",BODY,{"derivedFrom":makeQuery(id+"F8.opPattern","COPY",BODY,{"derivedFrom":makeQuery(id+"F3.opPattern","COPY",BODY,{"derivedFrom":makeQuery(id+"F2.opPattern","COPY",BODY,{"derivedFrom":makeQuery(id+"F1.opExtrude","SWEPT_BODY",BODY,{"disambiguationData":[OSD([sQuery(id+"F0.wireOp",EDGE,"E2.bottom"),sQuery(id+"F0.wireOp",EDGE,"E2.top"),sQuery(id+"F0.wireOp",EDGE,"E2.left"),sQuery(id+"F0.wireOp",EDGE,"E2.right")])]}),"instanceName":"1"}),"instanceName":"1"}),"instanceName":"1"}),"instanceName":"1"}),"instanceName":"1"});
            var Q261;
            Q261=makeQuery(id+"F10.opPattern","COPY",BODY,{"derivedFrom":makeQuery(id+"F9.opPattern","COPY",BODY,{"derivedFrom":makeQuery(id+"F8.opPattern","COPY",BODY,{"derivedFrom":makeQuery(id+"F4.opPattern","COPY",BODY,{"derivedFrom":makeQuery(id+"F3.opPattern","COPY",BODY,{"derivedFrom":makeQuery(id+"F2.opPattern","COPY",BODY,{"derivedFrom":makeQuery(id+"F1.opExtrude","SWEPT_BODY",BODY,{"disambiguationData":[OSD([sQuery(id+"F0.wireOp",EDGE,"E0.bottom"),sQuery(id+"F0.wireOp",EDGE,"E0.top"),sQuery(id+"F0.wireOp",EDGE,"E0.left"),sQuery(id+"F0.wireOp",EDGE,"E0.right")])]}),"instanceName":"1"}),"instanceName":"1"}),"instanceName":"1"}),"instanceName":"1"}),"instanceName":"1"}),"instanceName":"1"});
            var Q262;
            Q262=makeQuery(id+"F10.opPattern","COPY",BODY,{"derivedFrom":makeQuery(id+"F9.opPattern","COPY",BODY,{"derivedFrom":makeQuery(id+"F8.opPattern","COPY",BODY,{"derivedFrom":makeQuery(id+"F4.opPattern","COPY",BODY,{"derivedFrom":makeQuery(id+"F3.opPattern","COPY",BODY,{"derivedFrom":makeQuery(id+"F2.opPattern","COPY",BODY,{"derivedFrom":makeQuery(id+"F1.opExtrude","SWEPT_BODY",BODY,{"disambiguationData":[OSD([sQuery(id+"F0.wireOp",EDGE,"E1.bottom"),sQuery(id+"F0.wireOp",EDGE,"E1.top"),sQuery(id+"F0.wireOp",EDGE,"E1.left"),sQuery(id+"F0.wireOp",EDGE,"E1.right")])]}),"instanceName":"1"}),"instanceName":"1"}),"instanceName":"1"}),"instanceName":"1"}),"instanceName":"1"}),"instanceName":"1"});
            var Q263;
            Q263=makeQuery(id+"F10.opPattern","COPY",BODY,{"derivedFrom":makeQuery(id+"F9.opPattern","COPY",BODY,{"derivedFrom":makeQuery(id+"F8.opPattern","COPY",BODY,{"derivedFrom":makeQuery(id+"F4.opPattern","COPY",BODY,{"derivedFrom":makeQuery(id+"F3.opPattern","COPY",BODY,{"derivedFrom":makeQuery(id+"F2.opPattern","COPY",BODY,{"derivedFrom":makeQuery(id+"F1.opExtrude","SWEPT_BODY",BODY,{"disambiguationData":[OSD([sQuery(id+"F0.wireOp",EDGE,"E2.bottom"),sQuery(id+"F0.wireOp",EDGE,"E2.top"),sQuery(id+"F0.wireOp",EDGE,"E2.left"),sQuery(id+"F0.wireOp",EDGE,"E2.right")])]}),"instanceName":"1"}),"instanceName":"1"}),"instanceName":"1"}),"instanceName":"1"}),"instanceName":"1"}),"instanceName":"1"});
            var Q264;
            Q264=makeQuery(id+"F10.opPattern","COPY",BODY,{"derivedFrom":makeQuery(id+"F9.opPattern","COPY",BODY,{"derivedFrom":makeQuery(id+"F8.opPattern","COPY",BODY,{"derivedFrom":makeQuery(id+"F5.opPattern","COPY",BODY,{"derivedFrom":makeQuery(id+"F4.opPattern","COPY",BODY,{"derivedFrom":makeQuery(id+"F3.opPattern","COPY",BODY,{"derivedFrom":makeQuery(id+"F2.opPattern","COPY",BODY,{"derivedFrom":makeQuery(id+"F1.opExtrude","SWEPT_BODY",BODY,{"disambiguationData":[OSD([sQuery(id+"F0.wireOp",EDGE,"E0.bottom"),sQuery(id+"F0.wireOp",EDGE,"E0.top"),sQuery(id+"F0.wireOp",EDGE,"E0.left"),sQuery(id+"F0.wireOp",EDGE,"E0.right")])]}),"instanceName":"1"}),"instanceName":"1"}),"instanceName":"1"}),"instanceName":"1"}),"instanceName":"1"}),"instanceName":"1"}),"instanceName":"1"});
            var Q265;
            Q265=makeQuery(id+"F10.opPattern","COPY",BODY,{"derivedFrom":makeQuery(id+"F9.opPattern","COPY",BODY,{"derivedFrom":makeQuery(id+"F8.opPattern","COPY",BODY,{"derivedFrom":makeQuery(id+"F5.opPattern","COPY",BODY,{"derivedFrom":makeQuery(id+"F4.opPattern","COPY",BODY,{"derivedFrom":makeQuery(id+"F3.opPattern","COPY",BODY,{"derivedFrom":makeQuery(id+"F2.opPattern","COPY",BODY,{"derivedFrom":makeQuery(id+"F1.opExtrude","SWEPT_BODY",BODY,{"disambiguationData":[OSD([sQuery(id+"F0.wireOp",EDGE,"E1.bottom"),sQuery(id+"F0.wireOp",EDGE,"E1.top"),sQuery(id+"F0.wireOp",EDGE,"E1.left"),sQuery(id+"F0.wireOp",EDGE,"E1.right")])]}),"instanceName":"1"}),"instanceName":"1"}),"instanceName":"1"}),"instanceName":"1"}),"instanceName":"1"}),"instanceName":"1"}),"instanceName":"1"});
            var Q266;
            Q266=makeQuery(id+"F10.opPattern","COPY",BODY,{"derivedFrom":makeQuery(id+"F9.opPattern","COPY",BODY,{"derivedFrom":makeQuery(id+"F8.opPattern","COPY",BODY,{"derivedFrom":makeQuery(id+"F5.opPattern","COPY",BODY,{"derivedFrom":makeQuery(id+"F4.opPattern","COPY",BODY,{"derivedFrom":makeQuery(id+"F3.opPattern","COPY",BODY,{"derivedFrom":makeQuery(id+"F2.opPattern","COPY",BODY,{"derivedFrom":makeQuery(id+"F1.opExtrude","SWEPT_BODY",BODY,{"disambiguationData":[OSD([sQuery(id+"F0.wireOp",EDGE,"E2.bottom"),sQuery(id+"F0.wireOp",EDGE,"E2.top"),sQuery(id+"F0.wireOp",EDGE,"E2.left"),sQuery(id+"F0.wireOp",EDGE,"E2.right")])]}),"instanceName":"1"}),"instanceName":"1"}),"instanceName":"1"}),"instanceName":"1"}),"instanceName":"1"}),"instanceName":"1"}),"instanceName":"1"});
            var Q267;
            Q267=makeQuery(id+"F10.opPattern","COPY",BODY,{"derivedFrom":makeQuery(id+"F9.opPattern","COPY",BODY,{"derivedFrom":makeQuery(id+"F8.opPattern","COPY",BODY,{"derivedFrom":makeQuery(id+"F6.opPattern","COPY",BODY,{"derivedFrom":makeQuery(id+"F5.opPattern","COPY",BODY,{"derivedFrom":makeQuery(id+"F4.opPattern","COPY",BODY,{"derivedFrom":makeQuery(id+"F3.opPattern","COPY",BODY,{"derivedFrom":makeQuery(id+"F2.opPattern","COPY",BODY,{"derivedFrom":makeQuery(id+"F1.opExtrude","SWEPT_BODY",BODY,{"disambiguationData":[OSD([sQuery(id+"F0.wireOp",EDGE,"E0.bottom"),sQuery(id+"F0.wireOp",EDGE,"E0.top"),sQuery(id+"F0.wireOp",EDGE,"E0.left"),sQuery(id+"F0.wireOp",EDGE,"E0.right")])]}),"instanceName":"1"}),"instanceName":"1"}),"instanceName":"1"}),"instanceName":"1"}),"instanceName":"1"}),"instanceName":"1"}),"instanceName":"1"}),"instanceName":"1"});
            var Q268;
            Q268=makeQuery(id+"F10.opPattern","COPY",BODY,{"derivedFrom":makeQuery(id+"F9.opPattern","COPY",BODY,{"derivedFrom":makeQuery(id+"F8.opPattern","COPY",BODY,{"derivedFrom":makeQuery(id+"F6.opPattern","COPY",BODY,{"derivedFrom":makeQuery(id+"F5.opPattern","COPY",BODY,{"derivedFrom":makeQuery(id+"F4.opPattern","COPY",BODY,{"derivedFrom":makeQuery(id+"F3.opPattern","COPY",BODY,{"derivedFrom":makeQuery(id+"F2.opPattern","COPY",BODY,{"derivedFrom":makeQuery(id+"F1.opExtrude","SWEPT_BODY",BODY,{"disambiguationData":[OSD([sQuery(id+"F0.wireOp",EDGE,"E1.bottom"),sQuery(id+"F0.wireOp",EDGE,"E1.top"),sQuery(id+"F0.wireOp",EDGE,"E1.left"),sQuery(id+"F0.wireOp",EDGE,"E1.right")])]}),"instanceName":"1"}),"instanceName":"1"}),"instanceName":"1"}),"instanceName":"1"}),"instanceName":"1"}),"instanceName":"1"}),"instanceName":"1"}),"instanceName":"1"});
            var Q269;
            Q269=makeQuery(id+"F10.opPattern","COPY",BODY,{"derivedFrom":makeQuery(id+"F9.opPattern","COPY",BODY,{"derivedFrom":makeQuery(id+"F8.opPattern","COPY",BODY,{"derivedFrom":makeQuery(id+"F6.opPattern","COPY",BODY,{"derivedFrom":makeQuery(id+"F5.opPattern","COPY",BODY,{"derivedFrom":makeQuery(id+"F4.opPattern","COPY",BODY,{"derivedFrom":makeQuery(id+"F3.opPattern","COPY",BODY,{"derivedFrom":makeQuery(id+"F2.opPattern","COPY",BODY,{"derivedFrom":makeQuery(id+"F1.opExtrude","SWEPT_BODY",BODY,{"disambiguationData":[OSD([sQuery(id+"F0.wireOp",EDGE,"E2.bottom"),sQuery(id+"F0.wireOp",EDGE,"E2.top"),sQuery(id+"F0.wireOp",EDGE,"E2.left"),sQuery(id+"F0.wireOp",EDGE,"E2.right")])]}),"instanceName":"1"}),"instanceName":"1"}),"instanceName":"1"}),"instanceName":"1"}),"instanceName":"1"}),"instanceName":"1"}),"instanceName":"1"}),"instanceName":"1"});
            var Q270;
            Q270=makeQuery(id+"F10.opPattern","COPY",BODY,{"derivedFrom":makeQuery(id+"F9.opPattern","COPY",BODY,{"derivedFrom":makeQuery(id+"F8.opPattern","COPY",BODY,{"derivedFrom":makeQuery(id+"F7.opPattern","COPY",BODY,{"derivedFrom":makeQuery(id+"F1.opExtrude","SWEPT_BODY",BODY,{"disambiguationData":[OSD([sQuery(id+"F0.wireOp",EDGE,"E0.bottom"),sQuery(id+"F0.wireOp",EDGE,"E0.top"),sQuery(id+"F0.wireOp",EDGE,"E0.left"),sQuery(id+"F0.wireOp",EDGE,"E0.right")])]}),"instanceName":"1"}),"instanceName":"1"}),"instanceName":"1"}),"instanceName":"1"});
            var Q271;
            Q271=makeQuery(id+"F10.opPattern","COPY",BODY,{"derivedFrom":makeQuery(id+"F9.opPattern","COPY",BODY,{"derivedFrom":makeQuery(id+"F8.opPattern","COPY",BODY,{"derivedFrom":makeQuery(id+"F7.opPattern","COPY",BODY,{"derivedFrom":makeQuery(id+"F1.opExtrude","SWEPT_BODY",BODY,{"disambiguationData":[OSD([sQuery(id+"F0.wireOp",EDGE,"E1.bottom"),sQuery(id+"F0.wireOp",EDGE,"E1.top"),sQuery(id+"F0.wireOp",EDGE,"E1.left"),sQuery(id+"F0.wireOp",EDGE,"E1.right")])]}),"instanceName":"1"}),"instanceName":"1"}),"instanceName":"1"}),"instanceName":"1"});
            var Q272;
            Q272=makeQuery(id+"F10.opPattern","COPY",BODY,{"derivedFrom":makeQuery(id+"F9.opPattern","COPY",BODY,{"derivedFrom":makeQuery(id+"F8.opPattern","COPY",BODY,{"derivedFrom":makeQuery(id+"F7.opPattern","COPY",BODY,{"derivedFrom":makeQuery(id+"F1.opExtrude","SWEPT_BODY",BODY,{"disambiguationData":[OSD([sQuery(id+"F0.wireOp",EDGE,"E2.bottom"),sQuery(id+"F0.wireOp",EDGE,"E2.top"),sQuery(id+"F0.wireOp",EDGE,"E2.left"),sQuery(id+"F0.wireOp",EDGE,"E2.right")])]}),"instanceName":"1"}),"instanceName":"1"}),"instanceName":"1"}),"instanceName":"1"});
            var Q273;
            Q273=makeQuery(id+"F10.opPattern","COPY",BODY,{"derivedFrom":makeQuery(id+"F9.opPattern","COPY",BODY,{"derivedFrom":makeQuery(id+"F8.opPattern","COPY",BODY,{"derivedFrom":makeQuery(id+"F7.opPattern","COPY",BODY,{"derivedFrom":makeQuery(id+"F2.opPattern","COPY",BODY,{"derivedFrom":makeQuery(id+"F1.opExtrude","SWEPT_BODY",BODY,{"disambiguationData":[OSD([sQuery(id+"F0.wireOp",EDGE,"E0.bottom"),sQuery(id+"F0.wireOp",EDGE,"E0.top"),sQuery(id+"F0.wireOp",EDGE,"E0.left"),sQuery(id+"F0.wireOp",EDGE,"E0.right")])]}),"instanceName":"1"}),"instanceName":"1"}),"instanceName":"1"}),"instanceName":"1"}),"instanceName":"1"});
            var Q274;
            Q274=makeQuery(id+"F10.opPattern","COPY",BODY,{"derivedFrom":makeQuery(id+"F9.opPattern","COPY",BODY,{"derivedFrom":makeQuery(id+"F8.opPattern","COPY",BODY,{"derivedFrom":makeQuery(id+"F7.opPattern","COPY",BODY,{"derivedFrom":makeQuery(id+"F2.opPattern","COPY",BODY,{"derivedFrom":makeQuery(id+"F1.opExtrude","SWEPT_BODY",BODY,{"disambiguationData":[OSD([sQuery(id+"F0.wireOp",EDGE,"E1.bottom"),sQuery(id+"F0.wireOp",EDGE,"E1.top"),sQuery(id+"F0.wireOp",EDGE,"E1.left"),sQuery(id+"F0.wireOp",EDGE,"E1.right")])]}),"instanceName":"1"}),"instanceName":"1"}),"instanceName":"1"}),"instanceName":"1"}),"instanceName":"1"});
            var Q275;
            Q275=makeQuery(id+"F10.opPattern","COPY",BODY,{"derivedFrom":makeQuery(id+"F9.opPattern","COPY",BODY,{"derivedFrom":makeQuery(id+"F8.opPattern","COPY",BODY,{"derivedFrom":makeQuery(id+"F7.opPattern","COPY",BODY,{"derivedFrom":makeQuery(id+"F2.opPattern","COPY",BODY,{"derivedFrom":makeQuery(id+"F1.opExtrude","SWEPT_BODY",BODY,{"disambiguationData":[OSD([sQuery(id+"F0.wireOp",EDGE,"E2.bottom"),sQuery(id+"F0.wireOp",EDGE,"E2.top"),sQuery(id+"F0.wireOp",EDGE,"E2.left"),sQuery(id+"F0.wireOp",EDGE,"E2.right")])]}),"instanceName":"1"}),"instanceName":"1"}),"instanceName":"1"}),"instanceName":"1"}),"instanceName":"1"});
            var Q276;
            Q276=makeQuery(id+"F10.opPattern","COPY",BODY,{"derivedFrom":makeQuery(id+"F9.opPattern","COPY",BODY,{"derivedFrom":makeQuery(id+"F8.opPattern","COPY",BODY,{"derivedFrom":makeQuery(id+"F7.opPattern","COPY",BODY,{"derivedFrom":makeQuery(id+"F3.opPattern","COPY",BODY,{"derivedFrom":makeQuery(id+"F2.opPattern","COPY",BODY,{"derivedFrom":makeQuery(id+"F1.opExtrude","SWEPT_BODY",BODY,{"disambiguationData":[OSD([sQuery(id+"F0.wireOp",EDGE,"E0.bottom"),sQuery(id+"F0.wireOp",EDGE,"E0.top"),sQuery(id+"F0.wireOp",EDGE,"E0.left"),sQuery(id+"F0.wireOp",EDGE,"E0.right")])]}),"instanceName":"1"}),"instanceName":"1"}),"instanceName":"1"}),"instanceName":"1"}),"instanceName":"1"}),"instanceName":"1"});
            var Q277;
            Q277=makeQuery(id+"F10.opPattern","COPY",BODY,{"derivedFrom":makeQuery(id+"F9.opPattern","COPY",BODY,{"derivedFrom":makeQuery(id+"F8.opPattern","COPY",BODY,{"derivedFrom":makeQuery(id+"F7.opPattern","COPY",BODY,{"derivedFrom":makeQuery(id+"F3.opPattern","COPY",BODY,{"derivedFrom":makeQuery(id+"F2.opPattern","COPY",BODY,{"derivedFrom":makeQuery(id+"F1.opExtrude","SWEPT_BODY",BODY,{"disambiguationData":[OSD([sQuery(id+"F0.wireOp",EDGE,"E1.bottom"),sQuery(id+"F0.wireOp",EDGE,"E1.top"),sQuery(id+"F0.wireOp",EDGE,"E1.left"),sQuery(id+"F0.wireOp",EDGE,"E1.right")])]}),"instanceName":"1"}),"instanceName":"1"}),"instanceName":"1"}),"instanceName":"1"}),"instanceName":"1"}),"instanceName":"1"});
            var Q278;
            Q278=makeQuery(id+"F10.opPattern","COPY",BODY,{"derivedFrom":makeQuery(id+"F9.opPattern","COPY",BODY,{"derivedFrom":makeQuery(id+"F8.opPattern","COPY",BODY,{"derivedFrom":makeQuery(id+"F7.opPattern","COPY",BODY,{"derivedFrom":makeQuery(id+"F3.opPattern","COPY",BODY,{"derivedFrom":makeQuery(id+"F2.opPattern","COPY",BODY,{"derivedFrom":makeQuery(id+"F1.opExtrude","SWEPT_BODY",BODY,{"disambiguationData":[OSD([sQuery(id+"F0.wireOp",EDGE,"E2.bottom"),sQuery(id+"F0.wireOp",EDGE,"E2.top"),sQuery(id+"F0.wireOp",EDGE,"E2.left"),sQuery(id+"F0.wireOp",EDGE,"E2.right")])]}),"instanceName":"1"}),"instanceName":"1"}),"instanceName":"1"}),"instanceName":"1"}),"instanceName":"1"}),"instanceName":"1"});
            var Q279;
            Q279=makeQuery(id+"F10.opPattern","COPY",BODY,{"derivedFrom":makeQuery(id+"F9.opPattern","COPY",BODY,{"derivedFrom":makeQuery(id+"F8.opPattern","COPY",BODY,{"derivedFrom":makeQuery(id+"F7.opPattern","COPY",BODY,{"derivedFrom":makeQuery(id+"F4.opPattern","COPY",BODY,{"derivedFrom":makeQuery(id+"F3.opPattern","COPY",BODY,{"derivedFrom":makeQuery(id+"F2.opPattern","COPY",BODY,{"derivedFrom":makeQuery(id+"F1.opExtrude","SWEPT_BODY",BODY,{"disambiguationData":[OSD([sQuery(id+"F0.wireOp",EDGE,"E0.bottom"),sQuery(id+"F0.wireOp",EDGE,"E0.top"),sQuery(id+"F0.wireOp",EDGE,"E0.left"),sQuery(id+"F0.wireOp",EDGE,"E0.right")])]}),"instanceName":"1"}),"instanceName":"1"}),"instanceName":"1"}),"instanceName":"1"}),"instanceName":"1"}),"instanceName":"1"}),"instanceName":"1"});
            var Q280;
            Q280=makeQuery(id+"F10.opPattern","COPY",BODY,{"derivedFrom":makeQuery(id+"F9.opPattern","COPY",BODY,{"derivedFrom":makeQuery(id+"F8.opPattern","COPY",BODY,{"derivedFrom":makeQuery(id+"F7.opPattern","COPY",BODY,{"derivedFrom":makeQuery(id+"F4.opPattern","COPY",BODY,{"derivedFrom":makeQuery(id+"F3.opPattern","COPY",BODY,{"derivedFrom":makeQuery(id+"F2.opPattern","COPY",BODY,{"derivedFrom":makeQuery(id+"F1.opExtrude","SWEPT_BODY",BODY,{"disambiguationData":[OSD([sQuery(id+"F0.wireOp",EDGE,"E1.bottom"),sQuery(id+"F0.wireOp",EDGE,"E1.top"),sQuery(id+"F0.wireOp",EDGE,"E1.left"),sQuery(id+"F0.wireOp",EDGE,"E1.right")])]}),"instanceName":"1"}),"instanceName":"1"}),"instanceName":"1"}),"instanceName":"1"}),"instanceName":"1"}),"instanceName":"1"}),"instanceName":"1"});
            var Q281;
            Q281=makeQuery(id+"F10.opPattern","COPY",BODY,{"derivedFrom":makeQuery(id+"F9.opPattern","COPY",BODY,{"derivedFrom":makeQuery(id+"F8.opPattern","COPY",BODY,{"derivedFrom":makeQuery(id+"F7.opPattern","COPY",BODY,{"derivedFrom":makeQuery(id+"F4.opPattern","COPY",BODY,{"derivedFrom":makeQuery(id+"F3.opPattern","COPY",BODY,{"derivedFrom":makeQuery(id+"F2.opPattern","COPY",BODY,{"derivedFrom":makeQuery(id+"F1.opExtrude","SWEPT_BODY",BODY,{"disambiguationData":[OSD([sQuery(id+"F0.wireOp",EDGE,"E2.bottom"),sQuery(id+"F0.wireOp",EDGE,"E2.top"),sQuery(id+"F0.wireOp",EDGE,"E2.left"),sQuery(id+"F0.wireOp",EDGE,"E2.right")])]}),"instanceName":"1"}),"instanceName":"1"}),"instanceName":"1"}),"instanceName":"1"}),"instanceName":"1"}),"instanceName":"1"}),"instanceName":"1"});
            var Q282;
            Q282=makeQuery(id+"F10.opPattern","COPY",BODY,{"derivedFrom":makeQuery(id+"F9.opPattern","COPY",BODY,{"derivedFrom":makeQuery(id+"F8.opPattern","COPY",BODY,{"derivedFrom":makeQuery(id+"F7.opPattern","COPY",BODY,{"derivedFrom":makeQuery(id+"F5.opPattern","COPY",BODY,{"derivedFrom":makeQuery(id+"F4.opPattern","COPY",BODY,{"derivedFrom":makeQuery(id+"F3.opPattern","COPY",BODY,{"derivedFrom":makeQuery(id+"F2.opPattern","COPY",BODY,{"derivedFrom":makeQuery(id+"F1.opExtrude","SWEPT_BODY",BODY,{"disambiguationData":[OSD([sQuery(id+"F0.wireOp",EDGE,"E0.bottom"),sQuery(id+"F0.wireOp",EDGE,"E0.top"),sQuery(id+"F0.wireOp",EDGE,"E0.left"),sQuery(id+"F0.wireOp",EDGE,"E0.right")])]}),"instanceName":"1"}),"instanceName":"1"}),"instanceName":"1"}),"instanceName":"1"}),"instanceName":"1"}),"instanceName":"1"}),"instanceName":"1"}),"instanceName":"1"});
            var Q283;
            Q283=makeQuery(id+"F10.opPattern","COPY",BODY,{"derivedFrom":makeQuery(id+"F9.opPattern","COPY",BODY,{"derivedFrom":makeQuery(id+"F8.opPattern","COPY",BODY,{"derivedFrom":makeQuery(id+"F7.opPattern","COPY",BODY,{"derivedFrom":makeQuery(id+"F5.opPattern","COPY",BODY,{"derivedFrom":makeQuery(id+"F4.opPattern","COPY",BODY,{"derivedFrom":makeQuery(id+"F3.opPattern","COPY",BODY,{"derivedFrom":makeQuery(id+"F2.opPattern","COPY",BODY,{"derivedFrom":makeQuery(id+"F1.opExtrude","SWEPT_BODY",BODY,{"disambiguationData":[OSD([sQuery(id+"F0.wireOp",EDGE,"E1.bottom"),sQuery(id+"F0.wireOp",EDGE,"E1.top"),sQuery(id+"F0.wireOp",EDGE,"E1.left"),sQuery(id+"F0.wireOp",EDGE,"E1.right")])]}),"instanceName":"1"}),"instanceName":"1"}),"instanceName":"1"}),"instanceName":"1"}),"instanceName":"1"}),"instanceName":"1"}),"instanceName":"1"}),"instanceName":"1"});
            var Q284;
            Q284=makeQuery(id+"F10.opPattern","COPY",BODY,{"derivedFrom":makeQuery(id+"F9.opPattern","COPY",BODY,{"derivedFrom":makeQuery(id+"F8.opPattern","COPY",BODY,{"derivedFrom":makeQuery(id+"F7.opPattern","COPY",BODY,{"derivedFrom":makeQuery(id+"F5.opPattern","COPY",BODY,{"derivedFrom":makeQuery(id+"F4.opPattern","COPY",BODY,{"derivedFrom":makeQuery(id+"F3.opPattern","COPY",BODY,{"derivedFrom":makeQuery(id+"F2.opPattern","COPY",BODY,{"derivedFrom":makeQuery(id+"F1.opExtrude","SWEPT_BODY",BODY,{"disambiguationData":[OSD([sQuery(id+"F0.wireOp",EDGE,"E2.bottom"),sQuery(id+"F0.wireOp",EDGE,"E2.top"),sQuery(id+"F0.wireOp",EDGE,"E2.left"),sQuery(id+"F0.wireOp",EDGE,"E2.right")])]}),"instanceName":"1"}),"instanceName":"1"}),"instanceName":"1"}),"instanceName":"1"}),"instanceName":"1"}),"instanceName":"1"}),"instanceName":"1"}),"instanceName":"1"});
            var Q285;
            Q285=makeQuery(id+"F10.opPattern","COPY",BODY,{"derivedFrom":makeQuery(id+"F9.opPattern","COPY",BODY,{"derivedFrom":makeQuery(id+"F8.opPattern","COPY",BODY,{"derivedFrom":makeQuery(id+"F7.opPattern","COPY",BODY,{"derivedFrom":makeQuery(id+"F6.opPattern","COPY",BODY,{"derivedFrom":makeQuery(id+"F5.opPattern","COPY",BODY,{"derivedFrom":makeQuery(id+"F4.opPattern","COPY",BODY,{"derivedFrom":makeQuery(id+"F3.opPattern","COPY",BODY,{"derivedFrom":makeQuery(id+"F2.opPattern","COPY",BODY,{"derivedFrom":makeQuery(id+"F1.opExtrude","SWEPT_BODY",BODY,{"disambiguationData":[OSD([sQuery(id+"F0.wireOp",EDGE,"E0.bottom"),sQuery(id+"F0.wireOp",EDGE,"E0.top"),sQuery(id+"F0.wireOp",EDGE,"E0.left"),sQuery(id+"F0.wireOp",EDGE,"E0.right")])]}),"instanceName":"1"}),"instanceName":"1"}),"instanceName":"1"}),"instanceName":"1"}),"instanceName":"1"}),"instanceName":"1"}),"instanceName":"1"}),"instanceName":"1"}),"instanceName":"1"});
            var Q286;
            Q286=makeQuery(id+"F10.opPattern","COPY",BODY,{"derivedFrom":makeQuery(id+"F9.opPattern","COPY",BODY,{"derivedFrom":makeQuery(id+"F8.opPattern","COPY",BODY,{"derivedFrom":makeQuery(id+"F7.opPattern","COPY",BODY,{"derivedFrom":makeQuery(id+"F6.opPattern","COPY",BODY,{"derivedFrom":makeQuery(id+"F5.opPattern","COPY",BODY,{"derivedFrom":makeQuery(id+"F4.opPattern","COPY",BODY,{"derivedFrom":makeQuery(id+"F3.opPattern","COPY",BODY,{"derivedFrom":makeQuery(id+"F2.opPattern","COPY",BODY,{"derivedFrom":makeQuery(id+"F1.opExtrude","SWEPT_BODY",BODY,{"disambiguationData":[OSD([sQuery(id+"F0.wireOp",EDGE,"E1.bottom"),sQuery(id+"F0.wireOp",EDGE,"E1.top"),sQuery(id+"F0.wireOp",EDGE,"E1.left"),sQuery(id+"F0.wireOp",EDGE,"E1.right")])]}),"instanceName":"1"}),"instanceName":"1"}),"instanceName":"1"}),"instanceName":"1"}),"instanceName":"1"}),"instanceName":"1"}),"instanceName":"1"}),"instanceName":"1"}),"instanceName":"1"});
            var Q287;
            Q287=makeQuery(id+"F10.opPattern","COPY",BODY,{"derivedFrom":makeQuery(id+"F9.opPattern","COPY",BODY,{"derivedFrom":makeQuery(id+"F8.opPattern","COPY",BODY,{"derivedFrom":makeQuery(id+"F7.opPattern","COPY",BODY,{"derivedFrom":makeQuery(id+"F6.opPattern","COPY",BODY,{"derivedFrom":makeQuery(id+"F5.opPattern","COPY",BODY,{"derivedFrom":makeQuery(id+"F4.opPattern","COPY",BODY,{"derivedFrom":makeQuery(id+"F3.opPattern","COPY",BODY,{"derivedFrom":makeQuery(id+"F2.opPattern","COPY",BODY,{"derivedFrom":makeQuery(id+"F1.opExtrude","SWEPT_BODY",BODY,{"disambiguationData":[OSD([sQuery(id+"F0.wireOp",EDGE,"E2.bottom"),sQuery(id+"F0.wireOp",EDGE,"E2.top"),sQuery(id+"F0.wireOp",EDGE,"E2.left"),sQuery(id+"F0.wireOp",EDGE,"E2.right")])]}),"instanceName":"1"}),"instanceName":"1"}),"instanceName":"1"}),"instanceName":"1"}),"instanceName":"1"}),"instanceName":"1"}),"instanceName":"1"}),"instanceName":"1"}),"instanceName":"1"});
            transform(context, id + "F11", {"entities" : qUnion([Q0, Q1, Q2, Q3, Q4, Q5, Q6, Q7, Q8, Q9, Q10, Q11, Q12, Q13, Q14, Q15, Q16, Q17, Q18, Q19, Q20, Q21, Q22, Q23, Q24, Q25, Q26, Q27, Q28, Q29, Q30, Q31, Q32, Q33, Q34, Q35, Q36, Q37, Q38, Q39, Q40, Q41, Q42, Q43, Q44, Q45, Q46, Q47, Q48, Q49, Q50, Q51, Q52, Q53, Q54, Q55, Q56, Q57, Q58, Q59, Q60, Q61, Q62, Q63, Q64, Q65, Q66, Q67, Q68, Q69, Q70, Q71, Q72, Q73, Q74, Q75, Q76, Q77, Q78, Q79, Q80, Q81, Q82, Q83, Q84, Q85, Q86, Q87, Q88, Q89, Q90, Q91, Q92, Q93, Q94, Q95, Q96, Q97, Q98, Q99, Q100, Q101, Q102, Q103, Q104, Q105, Q106, Q107, Q108, Q109, Q110, Q111, Q112, Q113, Q114, Q115, Q116, Q117, Q118, Q119, Q120, Q121, Q122, Q123, Q124, Q125, Q126, Q127, Q128, Q129, Q130, Q131, Q132, Q133, Q134, Q135, Q136, Q137, Q138, Q139, Q140, Q141, Q142, Q143, Q144, Q145, Q146, Q147, Q148, Q149, Q150, Q151, Q152, Q153, Q154, Q155, Q156, Q157, Q158, Q159, Q160, Q161, Q162, Q163, Q164, Q165, Q166, Q167, Q168, Q169, Q170, Q171, Q172, Q173, Q174, Q175, Q176, Q177, Q178, Q179, Q180, Q181, Q182, Q183, Q184, Q185, Q186, Q187, Q188, Q189, Q190, Q191, Q192, Q193, Q194, Q195, Q196, Q197, Q198, Q199, Q200, Q201, Q202, Q203, Q204, Q205, Q206, Q207, Q208, Q209, Q210, Q211, Q212, Q213, Q214, Q215, Q216, Q217, Q218, Q219, Q220, Q221, Q222, Q223, Q224, Q225, Q226, Q227, Q228, Q229, Q230, Q231, Q232, Q233, Q234, Q235, Q236, Q237, Q238, Q239, Q240, Q241, Q242, Q243, Q244, Q245, Q246, Q247, Q248, Q249, Q250, Q251, Q252, Q253, Q254, Q255, Q256, Q257, Q258, Q259, Q260, Q261, Q262, Q263, Q264, Q265, Q266, Q267, Q268, Q269, Q270, Q271, Q272, Q273, Q274, Q275, Q276, Q277, Q278, Q279, Q280, Q281, Q282, Q283, Q284, Q285, Q286, Q287]), "transformType" : TransformType.TRANSLATION_3D, "dx" : -2424 * mm, "dy" : 7236 * mm, "dz" : 0 * mm, "makeCopy" : true});
        }
        {
            var Q0;
            Q0=makeQuery(id+"F1.opExtrude","SWEPT_BODY",BODY,{"disambiguationData":[OSD([sQuery(id+"F0.wireOp",EDGE,"E0.bottom"),sQuery(id+"F0.wireOp",EDGE,"E0.top"),sQuery(id+"F0.wireOp",EDGE,"E0.left"),sQuery(id+"F0.wireOp",EDGE,"E0.right")])]});
            var Q1;
            Q1=makeQuery(id+"F1.opExtrude","SWEPT_BODY",BODY,{"disambiguationData":[OSD([sQuery(id+"F0.wireOp",EDGE,"E1.bottom"),sQuery(id+"F0.wireOp",EDGE,"E1.top"),sQuery(id+"F0.wireOp",EDGE,"E1.left"),sQuery(id+"F0.wireOp",EDGE,"E1.right")])]});
            var Q2;
            Q2=makeQuery(id+"F2.opPattern","COPY",BODY,{"derivedFrom":makeQuery(id+"F1.opExtrude","SWEPT_BODY",BODY,{"disambiguationData":[OSD([sQuery(id+"F0.wireOp",EDGE,"E0.bottom"),sQuery(id+"F0.wireOp",EDGE,"E0.top"),sQuery(id+"F0.wireOp",EDGE,"E0.left"),sQuery(id+"F0.wireOp",EDGE,"E0.right")])]}),"instanceName":"1"});
            var Q3;
            Q3=makeQuery(id+"F2.opPattern","COPY",BODY,{"derivedFrom":makeQuery(id+"F1.opExtrude","SWEPT_BODY",BODY,{"disambiguationData":[OSD([sQuery(id+"F0.wireOp",EDGE,"E1.bottom"),sQuery(id+"F0.wireOp",EDGE,"E1.top"),sQuery(id+"F0.wireOp",EDGE,"E1.left"),sQuery(id+"F0.wireOp",EDGE,"E1.right")])]}),"instanceName":"1"});
            var Q4;
            Q4=makeQuery(id+"F2.opPattern","COPY",BODY,{"derivedFrom":makeQuery(id+"F1.opExtrude","SWEPT_BODY",BODY,{"disambiguationData":[OSD([sQuery(id+"F0.wireOp",EDGE,"E2.bottom"),sQuery(id+"F0.wireOp",EDGE,"E2.top"),sQuery(id+"F0.wireOp",EDGE,"E2.left"),sQuery(id+"F0.wireOp",EDGE,"E2.right")])]}),"instanceName":"1"});
            var Q5;
            Q5=makeQuery(id+"F3.opPattern","COPY",BODY,{"derivedFrom":makeQuery(id+"F2.opPattern","COPY",BODY,{"derivedFrom":makeQuery(id+"F1.opExtrude","SWEPT_BODY",BODY,{"disambiguationData":[OSD([sQuery(id+"F0.wireOp",EDGE,"E0.bottom"),sQuery(id+"F0.wireOp",EDGE,"E0.top"),sQuery(id+"F0.wireOp",EDGE,"E0.left"),sQuery(id+"F0.wireOp",EDGE,"E0.right")])]}),"instanceName":"1"}),"instanceName":"1"});
            var Q6;
            Q6=makeQuery(id+"F3.opPattern","COPY",BODY,{"derivedFrom":makeQuery(id+"F2.opPattern","COPY",BODY,{"derivedFrom":makeQuery(id+"F1.opExtrude","SWEPT_BODY",BODY,{"disambiguationData":[OSD([sQuery(id+"F0.wireOp",EDGE,"E1.bottom"),sQuery(id+"F0.wireOp",EDGE,"E1.top"),sQuery(id+"F0.wireOp",EDGE,"E1.left"),sQuery(id+"F0.wireOp",EDGE,"E1.right")])]}),"instanceName":"1"}),"instanceName":"1"});
            var Q7;
            Q7=makeQuery(id+"F3.opPattern","COPY",BODY,{"derivedFrom":makeQuery(id+"F2.opPattern","COPY",BODY,{"derivedFrom":makeQuery(id+"F1.opExtrude","SWEPT_BODY",BODY,{"disambiguationData":[OSD([sQuery(id+"F0.wireOp",EDGE,"E2.bottom"),sQuery(id+"F0.wireOp",EDGE,"E2.top"),sQuery(id+"F0.wireOp",EDGE,"E2.left"),sQuery(id+"F0.wireOp",EDGE,"E2.right")])]}),"instanceName":"1"}),"instanceName":"1"});
            var Q8;
            Q8=makeQuery(id+"F4.opPattern","COPY",BODY,{"derivedFrom":makeQuery(id+"F3.opPattern","COPY",BODY,{"derivedFrom":makeQuery(id+"F2.opPattern","COPY",BODY,{"derivedFrom":makeQuery(id+"F1.opExtrude","SWEPT_BODY",BODY,{"disambiguationData":[OSD([sQuery(id+"F0.wireOp",EDGE,"E0.bottom"),sQuery(id+"F0.wireOp",EDGE,"E0.top"),sQuery(id+"F0.wireOp",EDGE,"E0.left"),sQuery(id+"F0.wireOp",EDGE,"E0.right")])]}),"instanceName":"1"}),"instanceName":"1"}),"instanceName":"1"});
            var Q9;
            Q9=makeQuery(id+"F4.opPattern","COPY",BODY,{"derivedFrom":makeQuery(id+"F3.opPattern","COPY",BODY,{"derivedFrom":makeQuery(id+"F2.opPattern","COPY",BODY,{"derivedFrom":makeQuery(id+"F1.opExtrude","SWEPT_BODY",BODY,{"disambiguationData":[OSD([sQuery(id+"F0.wireOp",EDGE,"E1.bottom"),sQuery(id+"F0.wireOp",EDGE,"E1.top"),sQuery(id+"F0.wireOp",EDGE,"E1.left"),sQuery(id+"F0.wireOp",EDGE,"E1.right")])]}),"instanceName":"1"}),"instanceName":"1"}),"instanceName":"1"});
            var Q10;
            Q10=makeQuery(id+"F4.opPattern","COPY",BODY,{"derivedFrom":makeQuery(id+"F3.opPattern","COPY",BODY,{"derivedFrom":makeQuery(id+"F2.opPattern","COPY",BODY,{"derivedFrom":makeQuery(id+"F1.opExtrude","SWEPT_BODY",BODY,{"disambiguationData":[OSD([sQuery(id+"F0.wireOp",EDGE,"E2.bottom"),sQuery(id+"F0.wireOp",EDGE,"E2.top"),sQuery(id+"F0.wireOp",EDGE,"E2.left"),sQuery(id+"F0.wireOp",EDGE,"E2.right")])]}),"instanceName":"1"}),"instanceName":"1"}),"instanceName":"1"});
            var Q11;
            Q11=makeQuery(id+"F5.opPattern","COPY",BODY,{"derivedFrom":makeQuery(id+"F4.opPattern","COPY",BODY,{"derivedFrom":makeQuery(id+"F3.opPattern","COPY",BODY,{"derivedFrom":makeQuery(id+"F2.opPattern","COPY",BODY,{"derivedFrom":makeQuery(id+"F1.opExtrude","SWEPT_BODY",BODY,{"disambiguationData":[OSD([sQuery(id+"F0.wireOp",EDGE,"E0.bottom"),sQuery(id+"F0.wireOp",EDGE,"E0.top"),sQuery(id+"F0.wireOp",EDGE,"E0.left"),sQuery(id+"F0.wireOp",EDGE,"E0.right")])]}),"instanceName":"1"}),"instanceName":"1"}),"instanceName":"1"}),"instanceName":"1"});
            var Q12;
            Q12=makeQuery(id+"F5.opPattern","COPY",BODY,{"derivedFrom":makeQuery(id+"F4.opPattern","COPY",BODY,{"derivedFrom":makeQuery(id+"F3.opPattern","COPY",BODY,{"derivedFrom":makeQuery(id+"F2.opPattern","COPY",BODY,{"derivedFrom":makeQuery(id+"F1.opExtrude","SWEPT_BODY",BODY,{"disambiguationData":[OSD([sQuery(id+"F0.wireOp",EDGE,"E1.bottom"),sQuery(id+"F0.wireOp",EDGE,"E1.top"),sQuery(id+"F0.wireOp",EDGE,"E1.left"),sQuery(id+"F0.wireOp",EDGE,"E1.right")])]}),"instanceName":"1"}),"instanceName":"1"}),"instanceName":"1"}),"instanceName":"1"});
            var Q13;
            Q13=makeQuery(id+"F5.opPattern","COPY",BODY,{"derivedFrom":makeQuery(id+"F4.opPattern","COPY",BODY,{"derivedFrom":makeQuery(id+"F3.opPattern","COPY",BODY,{"derivedFrom":makeQuery(id+"F2.opPattern","COPY",BODY,{"derivedFrom":makeQuery(id+"F1.opExtrude","SWEPT_BODY",BODY,{"disambiguationData":[OSD([sQuery(id+"F0.wireOp",EDGE,"E2.bottom"),sQuery(id+"F0.wireOp",EDGE,"E2.top"),sQuery(id+"F0.wireOp",EDGE,"E2.left"),sQuery(id+"F0.wireOp",EDGE,"E2.right")])]}),"instanceName":"1"}),"instanceName":"1"}),"instanceName":"1"}),"instanceName":"1"});
            var Q14;
            Q14=makeQuery(id+"F6.opPattern","COPY",BODY,{"derivedFrom":makeQuery(id+"F5.opPattern","COPY",BODY,{"derivedFrom":makeQuery(id+"F4.opPattern","COPY",BODY,{"derivedFrom":makeQuery(id+"F3.opPattern","COPY",BODY,{"derivedFrom":makeQuery(id+"F2.opPattern","COPY",BODY,{"derivedFrom":makeQuery(id+"F1.opExtrude","SWEPT_BODY",BODY,{"disambiguationData":[OSD([sQuery(id+"F0.wireOp",EDGE,"E0.bottom"),sQuery(id+"F0.wireOp",EDGE,"E0.top"),sQuery(id+"F0.wireOp",EDGE,"E0.left"),sQuery(id+"F0.wireOp",EDGE,"E0.right")])]}),"instanceName":"1"}),"instanceName":"1"}),"instanceName":"1"}),"instanceName":"1"}),"instanceName":"1"});
            var Q15;
            Q15=makeQuery(id+"F6.opPattern","COPY",BODY,{"derivedFrom":makeQuery(id+"F5.opPattern","COPY",BODY,{"derivedFrom":makeQuery(id+"F4.opPattern","COPY",BODY,{"derivedFrom":makeQuery(id+"F3.opPattern","COPY",BODY,{"derivedFrom":makeQuery(id+"F2.opPattern","COPY",BODY,{"derivedFrom":makeQuery(id+"F1.opExtrude","SWEPT_BODY",BODY,{"disambiguationData":[OSD([sQuery(id+"F0.wireOp",EDGE,"E1.bottom"),sQuery(id+"F0.wireOp",EDGE,"E1.top"),sQuery(id+"F0.wireOp",EDGE,"E1.left"),sQuery(id+"F0.wireOp",EDGE,"E1.right")])]}),"instanceName":"1"}),"instanceName":"1"}),"instanceName":"1"}),"instanceName":"1"}),"instanceName":"1"});
            var Q16;
            Q16=makeQuery(id+"F6.opPattern","COPY",BODY,{"derivedFrom":makeQuery(id+"F5.opPattern","COPY",BODY,{"derivedFrom":makeQuery(id+"F4.opPattern","COPY",BODY,{"derivedFrom":makeQuery(id+"F3.opPattern","COPY",BODY,{"derivedFrom":makeQuery(id+"F2.opPattern","COPY",BODY,{"derivedFrom":makeQuery(id+"F1.opExtrude","SWEPT_BODY",BODY,{"disambiguationData":[OSD([sQuery(id+"F0.wireOp",EDGE,"E2.bottom"),sQuery(id+"F0.wireOp",EDGE,"E2.top"),sQuery(id+"F0.wireOp",EDGE,"E2.left"),sQuery(id+"F0.wireOp",EDGE,"E2.right")])]}),"instanceName":"1"}),"instanceName":"1"}),"instanceName":"1"}),"instanceName":"1"}),"instanceName":"1"});
            var Q17;
            Q17=makeQuery(id+"F7.opPattern","COPY",BODY,{"derivedFrom":makeQuery(id+"F1.opExtrude","SWEPT_BODY",BODY,{"disambiguationData":[OSD([sQuery(id+"F0.wireOp",EDGE,"E0.bottom"),sQuery(id+"F0.wireOp",EDGE,"E0.top"),sQuery(id+"F0.wireOp",EDGE,"E0.left"),sQuery(id+"F0.wireOp",EDGE,"E0.right")])]}),"instanceName":"1"});
            var Q18;
            Q18=makeQuery(id+"F7.opPattern","COPY",BODY,{"derivedFrom":makeQuery(id+"F1.opExtrude","SWEPT_BODY",BODY,{"disambiguationData":[OSD([sQuery(id+"F0.wireOp",EDGE,"E1.bottom"),sQuery(id+"F0.wireOp",EDGE,"E1.top"),sQuery(id+"F0.wireOp",EDGE,"E1.left"),sQuery(id+"F0.wireOp",EDGE,"E1.right")])]}),"instanceName":"1"});
            var Q19;
            Q19=makeQuery(id+"F7.opPattern","COPY",BODY,{"derivedFrom":makeQuery(id+"F1.opExtrude","SWEPT_BODY",BODY,{"disambiguationData":[OSD([sQuery(id+"F0.wireOp",EDGE,"E2.bottom"),sQuery(id+"F0.wireOp",EDGE,"E2.top"),sQuery(id+"F0.wireOp",EDGE,"E2.left"),sQuery(id+"F0.wireOp",EDGE,"E2.right")])]}),"instanceName":"1"});
            var Q20;
            Q20=makeQuery(id+"F7.opPattern","COPY",BODY,{"derivedFrom":makeQuery(id+"F2.opPattern","COPY",BODY,{"derivedFrom":makeQuery(id+"F1.opExtrude","SWEPT_BODY",BODY,{"disambiguationData":[OSD([sQuery(id+"F0.wireOp",EDGE,"E0.bottom"),sQuery(id+"F0.wireOp",EDGE,"E0.top"),sQuery(id+"F0.wireOp",EDGE,"E0.left"),sQuery(id+"F0.wireOp",EDGE,"E0.right")])]}),"instanceName":"1"}),"instanceName":"1"});
            var Q21;
            Q21=makeQuery(id+"F7.opPattern","COPY",BODY,{"derivedFrom":makeQuery(id+"F2.opPattern","COPY",BODY,{"derivedFrom":makeQuery(id+"F1.opExtrude","SWEPT_BODY",BODY,{"disambiguationData":[OSD([sQuery(id+"F0.wireOp",EDGE,"E1.bottom"),sQuery(id+"F0.wireOp",EDGE,"E1.top"),sQuery(id+"F0.wireOp",EDGE,"E1.left"),sQuery(id+"F0.wireOp",EDGE,"E1.right")])]}),"instanceName":"1"}),"instanceName":"1"});
            var Q22;
            Q22=makeQuery(id+"F7.opPattern","COPY",BODY,{"derivedFrom":makeQuery(id+"F2.opPattern","COPY",BODY,{"derivedFrom":makeQuery(id+"F1.opExtrude","SWEPT_BODY",BODY,{"disambiguationData":[OSD([sQuery(id+"F0.wireOp",EDGE,"E2.bottom"),sQuery(id+"F0.wireOp",EDGE,"E2.top"),sQuery(id+"F0.wireOp",EDGE,"E2.left"),sQuery(id+"F0.wireOp",EDGE,"E2.right")])]}),"instanceName":"1"}),"instanceName":"1"});
            var Q23;
            Q23=makeQuery(id+"F7.opPattern","COPY",BODY,{"derivedFrom":makeQuery(id+"F3.opPattern","COPY",BODY,{"derivedFrom":makeQuery(id+"F2.opPattern","COPY",BODY,{"derivedFrom":makeQuery(id+"F1.opExtrude","SWEPT_BODY",BODY,{"disambiguationData":[OSD([sQuery(id+"F0.wireOp",EDGE,"E0.bottom"),sQuery(id+"F0.wireOp",EDGE,"E0.top"),sQuery(id+"F0.wireOp",EDGE,"E0.left"),sQuery(id+"F0.wireOp",EDGE,"E0.right")])]}),"instanceName":"1"}),"instanceName":"1"}),"instanceName":"1"});
            var Q24;
            Q24=makeQuery(id+"F7.opPattern","COPY",BODY,{"derivedFrom":makeQuery(id+"F3.opPattern","COPY",BODY,{"derivedFrom":makeQuery(id+"F2.opPattern","COPY",BODY,{"derivedFrom":makeQuery(id+"F1.opExtrude","SWEPT_BODY",BODY,{"disambiguationData":[OSD([sQuery(id+"F0.wireOp",EDGE,"E1.bottom"),sQuery(id+"F0.wireOp",EDGE,"E1.top"),sQuery(id+"F0.wireOp",EDGE,"E1.left"),sQuery(id+"F0.wireOp",EDGE,"E1.right")])]}),"instanceName":"1"}),"instanceName":"1"}),"instanceName":"1"});
            var Q25;
            Q25=makeQuery(id+"F7.opPattern","COPY",BODY,{"derivedFrom":makeQuery(id+"F3.opPattern","COPY",BODY,{"derivedFrom":makeQuery(id+"F2.opPattern","COPY",BODY,{"derivedFrom":makeQuery(id+"F1.opExtrude","SWEPT_BODY",BODY,{"disambiguationData":[OSD([sQuery(id+"F0.wireOp",EDGE,"E2.bottom"),sQuery(id+"F0.wireOp",EDGE,"E2.top"),sQuery(id+"F0.wireOp",EDGE,"E2.left"),sQuery(id+"F0.wireOp",EDGE,"E2.right")])]}),"instanceName":"1"}),"instanceName":"1"}),"instanceName":"1"});
            var Q26;
            Q26=makeQuery(id+"F7.opPattern","COPY",BODY,{"derivedFrom":makeQuery(id+"F4.opPattern","COPY",BODY,{"derivedFrom":makeQuery(id+"F3.opPattern","COPY",BODY,{"derivedFrom":makeQuery(id+"F2.opPattern","COPY",BODY,{"derivedFrom":makeQuery(id+"F1.opExtrude","SWEPT_BODY",BODY,{"disambiguationData":[OSD([sQuery(id+"F0.wireOp",EDGE,"E0.bottom"),sQuery(id+"F0.wireOp",EDGE,"E0.top"),sQuery(id+"F0.wireOp",EDGE,"E0.left"),sQuery(id+"F0.wireOp",EDGE,"E0.right")])]}),"instanceName":"1"}),"instanceName":"1"}),"instanceName":"1"}),"instanceName":"1"});
            var Q27;
            Q27=makeQuery(id+"F7.opPattern","COPY",BODY,{"derivedFrom":makeQuery(id+"F4.opPattern","COPY",BODY,{"derivedFrom":makeQuery(id+"F3.opPattern","COPY",BODY,{"derivedFrom":makeQuery(id+"F2.opPattern","COPY",BODY,{"derivedFrom":makeQuery(id+"F1.opExtrude","SWEPT_BODY",BODY,{"disambiguationData":[OSD([sQuery(id+"F0.wireOp",EDGE,"E1.bottom"),sQuery(id+"F0.wireOp",EDGE,"E1.top"),sQuery(id+"F0.wireOp",EDGE,"E1.left"),sQuery(id+"F0.wireOp",EDGE,"E1.right")])]}),"instanceName":"1"}),"instanceName":"1"}),"instanceName":"1"}),"instanceName":"1"});
            var Q28;
            Q28=makeQuery(id+"F7.opPattern","COPY",BODY,{"derivedFrom":makeQuery(id+"F4.opPattern","COPY",BODY,{"derivedFrom":makeQuery(id+"F3.opPattern","COPY",BODY,{"derivedFrom":makeQuery(id+"F2.opPattern","COPY",BODY,{"derivedFrom":makeQuery(id+"F1.opExtrude","SWEPT_BODY",BODY,{"disambiguationData":[OSD([sQuery(id+"F0.wireOp",EDGE,"E2.bottom"),sQuery(id+"F0.wireOp",EDGE,"E2.top"),sQuery(id+"F0.wireOp",EDGE,"E2.left"),sQuery(id+"F0.wireOp",EDGE,"E2.right")])]}),"instanceName":"1"}),"instanceName":"1"}),"instanceName":"1"}),"instanceName":"1"});
            var Q29;
            Q29=makeQuery(id+"F7.opPattern","COPY",BODY,{"derivedFrom":makeQuery(id+"F5.opPattern","COPY",BODY,{"derivedFrom":makeQuery(id+"F4.opPattern","COPY",BODY,{"derivedFrom":makeQuery(id+"F3.opPattern","COPY",BODY,{"derivedFrom":makeQuery(id+"F2.opPattern","COPY",BODY,{"derivedFrom":makeQuery(id+"F1.opExtrude","SWEPT_BODY",BODY,{"disambiguationData":[OSD([sQuery(id+"F0.wireOp",EDGE,"E0.bottom"),sQuery(id+"F0.wireOp",EDGE,"E0.top"),sQuery(id+"F0.wireOp",EDGE,"E0.left"),sQuery(id+"F0.wireOp",EDGE,"E0.right")])]}),"instanceName":"1"}),"instanceName":"1"}),"instanceName":"1"}),"instanceName":"1"}),"instanceName":"1"});
            var Q30;
            Q30=makeQuery(id+"F7.opPattern","COPY",BODY,{"derivedFrom":makeQuery(id+"F5.opPattern","COPY",BODY,{"derivedFrom":makeQuery(id+"F4.opPattern","COPY",BODY,{"derivedFrom":makeQuery(id+"F3.opPattern","COPY",BODY,{"derivedFrom":makeQuery(id+"F2.opPattern","COPY",BODY,{"derivedFrom":makeQuery(id+"F1.opExtrude","SWEPT_BODY",BODY,{"disambiguationData":[OSD([sQuery(id+"F0.wireOp",EDGE,"E1.bottom"),sQuery(id+"F0.wireOp",EDGE,"E1.top"),sQuery(id+"F0.wireOp",EDGE,"E1.left"),sQuery(id+"F0.wireOp",EDGE,"E1.right")])]}),"instanceName":"1"}),"instanceName":"1"}),"instanceName":"1"}),"instanceName":"1"}),"instanceName":"1"});
            var Q31;
            Q31=makeQuery(id+"F7.opPattern","COPY",BODY,{"derivedFrom":makeQuery(id+"F5.opPattern","COPY",BODY,{"derivedFrom":makeQuery(id+"F4.opPattern","COPY",BODY,{"derivedFrom":makeQuery(id+"F3.opPattern","COPY",BODY,{"derivedFrom":makeQuery(id+"F2.opPattern","COPY",BODY,{"derivedFrom":makeQuery(id+"F1.opExtrude","SWEPT_BODY",BODY,{"disambiguationData":[OSD([sQuery(id+"F0.wireOp",EDGE,"E2.bottom"),sQuery(id+"F0.wireOp",EDGE,"E2.top"),sQuery(id+"F0.wireOp",EDGE,"E2.left"),sQuery(id+"F0.wireOp",EDGE,"E2.right")])]}),"instanceName":"1"}),"instanceName":"1"}),"instanceName":"1"}),"instanceName":"1"}),"instanceName":"1"});
            var Q32;
            Q32=makeQuery(id+"F7.opPattern","COPY",BODY,{"derivedFrom":makeQuery(id+"F6.opPattern","COPY",BODY,{"derivedFrom":makeQuery(id+"F5.opPattern","COPY",BODY,{"derivedFrom":makeQuery(id+"F4.opPattern","COPY",BODY,{"derivedFrom":makeQuery(id+"F3.opPattern","COPY",BODY,{"derivedFrom":makeQuery(id+"F2.opPattern","COPY",BODY,{"derivedFrom":makeQuery(id+"F1.opExtrude","SWEPT_BODY",BODY,{"disambiguationData":[OSD([sQuery(id+"F0.wireOp",EDGE,"E0.bottom"),sQuery(id+"F0.wireOp",EDGE,"E0.top"),sQuery(id+"F0.wireOp",EDGE,"E0.left"),sQuery(id+"F0.wireOp",EDGE,"E0.right")])]}),"instanceName":"1"}),"instanceName":"1"}),"instanceName":"1"}),"instanceName":"1"}),"instanceName":"1"}),"instanceName":"1"});
            var Q33;
            Q33=makeQuery(id+"F7.opPattern","COPY",BODY,{"derivedFrom":makeQuery(id+"F6.opPattern","COPY",BODY,{"derivedFrom":makeQuery(id+"F5.opPattern","COPY",BODY,{"derivedFrom":makeQuery(id+"F4.opPattern","COPY",BODY,{"derivedFrom":makeQuery(id+"F3.opPattern","COPY",BODY,{"derivedFrom":makeQuery(id+"F2.opPattern","COPY",BODY,{"derivedFrom":makeQuery(id+"F1.opExtrude","SWEPT_BODY",BODY,{"disambiguationData":[OSD([sQuery(id+"F0.wireOp",EDGE,"E1.bottom"),sQuery(id+"F0.wireOp",EDGE,"E1.top"),sQuery(id+"F0.wireOp",EDGE,"E1.left"),sQuery(id+"F0.wireOp",EDGE,"E1.right")])]}),"instanceName":"1"}),"instanceName":"1"}),"instanceName":"1"}),"instanceName":"1"}),"instanceName":"1"}),"instanceName":"1"});
            var Q34;
            Q34=makeQuery(id+"F7.opPattern","COPY",BODY,{"derivedFrom":makeQuery(id+"F6.opPattern","COPY",BODY,{"derivedFrom":makeQuery(id+"F5.opPattern","COPY",BODY,{"derivedFrom":makeQuery(id+"F4.opPattern","COPY",BODY,{"derivedFrom":makeQuery(id+"F3.opPattern","COPY",BODY,{"derivedFrom":makeQuery(id+"F2.opPattern","COPY",BODY,{"derivedFrom":makeQuery(id+"F1.opExtrude","SWEPT_BODY",BODY,{"disambiguationData":[OSD([sQuery(id+"F0.wireOp",EDGE,"E2.bottom"),sQuery(id+"F0.wireOp",EDGE,"E2.top"),sQuery(id+"F0.wireOp",EDGE,"E2.left"),sQuery(id+"F0.wireOp",EDGE,"E2.right")])]}),"instanceName":"1"}),"instanceName":"1"}),"instanceName":"1"}),"instanceName":"1"}),"instanceName":"1"}),"instanceName":"1"});
            var Q35;
            Q35=makeQuery(id+"F8.opPattern","COPY",BODY,{"derivedFrom":makeQuery(id+"F1.opExtrude","SWEPT_BODY",BODY,{"disambiguationData":[OSD([sQuery(id+"F0.wireOp",EDGE,"E0.bottom"),sQuery(id+"F0.wireOp",EDGE,"E0.top"),sQuery(id+"F0.wireOp",EDGE,"E0.left"),sQuery(id+"F0.wireOp",EDGE,"E0.right")])]}),"instanceName":"1"});
            var Q36;
            Q36=makeQuery(id+"F8.opPattern","COPY",BODY,{"derivedFrom":makeQuery(id+"F1.opExtrude","SWEPT_BODY",BODY,{"disambiguationData":[OSD([sQuery(id+"F0.wireOp",EDGE,"E1.bottom"),sQuery(id+"F0.wireOp",EDGE,"E1.top"),sQuery(id+"F0.wireOp",EDGE,"E1.left"),sQuery(id+"F0.wireOp",EDGE,"E1.right")])]}),"instanceName":"1"});
            var Q37;
            Q37=makeQuery(id+"F8.opPattern","COPY",BODY,{"derivedFrom":makeQuery(id+"F1.opExtrude","SWEPT_BODY",BODY,{"disambiguationData":[OSD([sQuery(id+"F0.wireOp",EDGE,"E2.bottom"),sQuery(id+"F0.wireOp",EDGE,"E2.top"),sQuery(id+"F0.wireOp",EDGE,"E2.left"),sQuery(id+"F0.wireOp",EDGE,"E2.right")])]}),"instanceName":"1"});
            var Q38;
            Q38=makeQuery(id+"F8.opPattern","COPY",BODY,{"derivedFrom":makeQuery(id+"F2.opPattern","COPY",BODY,{"derivedFrom":makeQuery(id+"F1.opExtrude","SWEPT_BODY",BODY,{"disambiguationData":[OSD([sQuery(id+"F0.wireOp",EDGE,"E0.bottom"),sQuery(id+"F0.wireOp",EDGE,"E0.top"),sQuery(id+"F0.wireOp",EDGE,"E0.left"),sQuery(id+"F0.wireOp",EDGE,"E0.right")])]}),"instanceName":"1"}),"instanceName":"1"});
            var Q39;
            Q39=makeQuery(id+"F8.opPattern","COPY",BODY,{"derivedFrom":makeQuery(id+"F2.opPattern","COPY",BODY,{"derivedFrom":makeQuery(id+"F1.opExtrude","SWEPT_BODY",BODY,{"disambiguationData":[OSD([sQuery(id+"F0.wireOp",EDGE,"E1.bottom"),sQuery(id+"F0.wireOp",EDGE,"E1.top"),sQuery(id+"F0.wireOp",EDGE,"E1.left"),sQuery(id+"F0.wireOp",EDGE,"E1.right")])]}),"instanceName":"1"}),"instanceName":"1"});
            var Q40;
            Q40=makeQuery(id+"F8.opPattern","COPY",BODY,{"derivedFrom":makeQuery(id+"F2.opPattern","COPY",BODY,{"derivedFrom":makeQuery(id+"F1.opExtrude","SWEPT_BODY",BODY,{"disambiguationData":[OSD([sQuery(id+"F0.wireOp",EDGE,"E2.bottom"),sQuery(id+"F0.wireOp",EDGE,"E2.top"),sQuery(id+"F0.wireOp",EDGE,"E2.left"),sQuery(id+"F0.wireOp",EDGE,"E2.right")])]}),"instanceName":"1"}),"instanceName":"1"});
            var Q41;
            Q41=makeQuery(id+"F8.opPattern","COPY",BODY,{"derivedFrom":makeQuery(id+"F3.opPattern","COPY",BODY,{"derivedFrom":makeQuery(id+"F2.opPattern","COPY",BODY,{"derivedFrom":makeQuery(id+"F1.opExtrude","SWEPT_BODY",BODY,{"disambiguationData":[OSD([sQuery(id+"F0.wireOp",EDGE,"E0.bottom"),sQuery(id+"F0.wireOp",EDGE,"E0.top"),sQuery(id+"F0.wireOp",EDGE,"E0.left"),sQuery(id+"F0.wireOp",EDGE,"E0.right")])]}),"instanceName":"1"}),"instanceName":"1"}),"instanceName":"1"});
            var Q42;
            Q42=makeQuery(id+"F8.opPattern","COPY",BODY,{"derivedFrom":makeQuery(id+"F3.opPattern","COPY",BODY,{"derivedFrom":makeQuery(id+"F2.opPattern","COPY",BODY,{"derivedFrom":makeQuery(id+"F1.opExtrude","SWEPT_BODY",BODY,{"disambiguationData":[OSD([sQuery(id+"F0.wireOp",EDGE,"E1.bottom"),sQuery(id+"F0.wireOp",EDGE,"E1.top"),sQuery(id+"F0.wireOp",EDGE,"E1.left"),sQuery(id+"F0.wireOp",EDGE,"E1.right")])]}),"instanceName":"1"}),"instanceName":"1"}),"instanceName":"1"});
            var Q43;
            Q43=makeQuery(id+"F8.opPattern","COPY",BODY,{"derivedFrom":makeQuery(id+"F3.opPattern","COPY",BODY,{"derivedFrom":makeQuery(id+"F2.opPattern","COPY",BODY,{"derivedFrom":makeQuery(id+"F1.opExtrude","SWEPT_BODY",BODY,{"disambiguationData":[OSD([sQuery(id+"F0.wireOp",EDGE,"E2.bottom"),sQuery(id+"F0.wireOp",EDGE,"E2.top"),sQuery(id+"F0.wireOp",EDGE,"E2.left"),sQuery(id+"F0.wireOp",EDGE,"E2.right")])]}),"instanceName":"1"}),"instanceName":"1"}),"instanceName":"1"});
            var Q44;
            Q44=makeQuery(id+"F8.opPattern","COPY",BODY,{"derivedFrom":makeQuery(id+"F4.opPattern","COPY",BODY,{"derivedFrom":makeQuery(id+"F3.opPattern","COPY",BODY,{"derivedFrom":makeQuery(id+"F2.opPattern","COPY",BODY,{"derivedFrom":makeQuery(id+"F1.opExtrude","SWEPT_BODY",BODY,{"disambiguationData":[OSD([sQuery(id+"F0.wireOp",EDGE,"E0.bottom"),sQuery(id+"F0.wireOp",EDGE,"E0.top"),sQuery(id+"F0.wireOp",EDGE,"E0.left"),sQuery(id+"F0.wireOp",EDGE,"E0.right")])]}),"instanceName":"1"}),"instanceName":"1"}),"instanceName":"1"}),"instanceName":"1"});
            var Q45;
            Q45=makeQuery(id+"F8.opPattern","COPY",BODY,{"derivedFrom":makeQuery(id+"F4.opPattern","COPY",BODY,{"derivedFrom":makeQuery(id+"F3.opPattern","COPY",BODY,{"derivedFrom":makeQuery(id+"F2.opPattern","COPY",BODY,{"derivedFrom":makeQuery(id+"F1.opExtrude","SWEPT_BODY",BODY,{"disambiguationData":[OSD([sQuery(id+"F0.wireOp",EDGE,"E1.bottom"),sQuery(id+"F0.wireOp",EDGE,"E1.top"),sQuery(id+"F0.wireOp",EDGE,"E1.left"),sQuery(id+"F0.wireOp",EDGE,"E1.right")])]}),"instanceName":"1"}),"instanceName":"1"}),"instanceName":"1"}),"instanceName":"1"});
            var Q46;
            Q46=makeQuery(id+"F8.opPattern","COPY",BODY,{"derivedFrom":makeQuery(id+"F4.opPattern","COPY",BODY,{"derivedFrom":makeQuery(id+"F3.opPattern","COPY",BODY,{"derivedFrom":makeQuery(id+"F2.opPattern","COPY",BODY,{"derivedFrom":makeQuery(id+"F1.opExtrude","SWEPT_BODY",BODY,{"disambiguationData":[OSD([sQuery(id+"F0.wireOp",EDGE,"E2.bottom"),sQuery(id+"F0.wireOp",EDGE,"E2.top"),sQuery(id+"F0.wireOp",EDGE,"E2.left"),sQuery(id+"F0.wireOp",EDGE,"E2.right")])]}),"instanceName":"1"}),"instanceName":"1"}),"instanceName":"1"}),"instanceName":"1"});
            var Q47;
            Q47=makeQuery(id+"F8.opPattern","COPY",BODY,{"derivedFrom":makeQuery(id+"F5.opPattern","COPY",BODY,{"derivedFrom":makeQuery(id+"F4.opPattern","COPY",BODY,{"derivedFrom":makeQuery(id+"F3.opPattern","COPY",BODY,{"derivedFrom":makeQuery(id+"F2.opPattern","COPY",BODY,{"derivedFrom":makeQuery(id+"F1.opExtrude","SWEPT_BODY",BODY,{"disambiguationData":[OSD([sQuery(id+"F0.wireOp",EDGE,"E0.bottom"),sQuery(id+"F0.wireOp",EDGE,"E0.top"),sQuery(id+"F0.wireOp",EDGE,"E0.left"),sQuery(id+"F0.wireOp",EDGE,"E0.right")])]}),"instanceName":"1"}),"instanceName":"1"}),"instanceName":"1"}),"instanceName":"1"}),"instanceName":"1"});
            var Q48;
            Q48=makeQuery(id+"F8.opPattern","COPY",BODY,{"derivedFrom":makeQuery(id+"F5.opPattern","COPY",BODY,{"derivedFrom":makeQuery(id+"F4.opPattern","COPY",BODY,{"derivedFrom":makeQuery(id+"F3.opPattern","COPY",BODY,{"derivedFrom":makeQuery(id+"F2.opPattern","COPY",BODY,{"derivedFrom":makeQuery(id+"F1.opExtrude","SWEPT_BODY",BODY,{"disambiguationData":[OSD([sQuery(id+"F0.wireOp",EDGE,"E1.bottom"),sQuery(id+"F0.wireOp",EDGE,"E1.top"),sQuery(id+"F0.wireOp",EDGE,"E1.left"),sQuery(id+"F0.wireOp",EDGE,"E1.right")])]}),"instanceName":"1"}),"instanceName":"1"}),"instanceName":"1"}),"instanceName":"1"}),"instanceName":"1"});
            var Q49;
            Q49=makeQuery(id+"F8.opPattern","COPY",BODY,{"derivedFrom":makeQuery(id+"F5.opPattern","COPY",BODY,{"derivedFrom":makeQuery(id+"F4.opPattern","COPY",BODY,{"derivedFrom":makeQuery(id+"F3.opPattern","COPY",BODY,{"derivedFrom":makeQuery(id+"F2.opPattern","COPY",BODY,{"derivedFrom":makeQuery(id+"F1.opExtrude","SWEPT_BODY",BODY,{"disambiguationData":[OSD([sQuery(id+"F0.wireOp",EDGE,"E2.bottom"),sQuery(id+"F0.wireOp",EDGE,"E2.top"),sQuery(id+"F0.wireOp",EDGE,"E2.left"),sQuery(id+"F0.wireOp",EDGE,"E2.right")])]}),"instanceName":"1"}),"instanceName":"1"}),"instanceName":"1"}),"instanceName":"1"}),"instanceName":"1"});
            var Q50;
            Q50=makeQuery(id+"F8.opPattern","COPY",BODY,{"derivedFrom":makeQuery(id+"F6.opPattern","COPY",BODY,{"derivedFrom":makeQuery(id+"F5.opPattern","COPY",BODY,{"derivedFrom":makeQuery(id+"F4.opPattern","COPY",BODY,{"derivedFrom":makeQuery(id+"F3.opPattern","COPY",BODY,{"derivedFrom":makeQuery(id+"F2.opPattern","COPY",BODY,{"derivedFrom":makeQuery(id+"F1.opExtrude","SWEPT_BODY",BODY,{"disambiguationData":[OSD([sQuery(id+"F0.wireOp",EDGE,"E0.bottom"),sQuery(id+"F0.wireOp",EDGE,"E0.top"),sQuery(id+"F0.wireOp",EDGE,"E0.left"),sQuery(id+"F0.wireOp",EDGE,"E0.right")])]}),"instanceName":"1"}),"instanceName":"1"}),"instanceName":"1"}),"instanceName":"1"}),"instanceName":"1"}),"instanceName":"1"});
            var Q51;
            Q51=makeQuery(id+"F8.opPattern","COPY",BODY,{"derivedFrom":makeQuery(id+"F6.opPattern","COPY",BODY,{"derivedFrom":makeQuery(id+"F5.opPattern","COPY",BODY,{"derivedFrom":makeQuery(id+"F4.opPattern","COPY",BODY,{"derivedFrom":makeQuery(id+"F3.opPattern","COPY",BODY,{"derivedFrom":makeQuery(id+"F2.opPattern","COPY",BODY,{"derivedFrom":makeQuery(id+"F1.opExtrude","SWEPT_BODY",BODY,{"disambiguationData":[OSD([sQuery(id+"F0.wireOp",EDGE,"E1.bottom"),sQuery(id+"F0.wireOp",EDGE,"E1.top"),sQuery(id+"F0.wireOp",EDGE,"E1.left"),sQuery(id+"F0.wireOp",EDGE,"E1.right")])]}),"instanceName":"1"}),"instanceName":"1"}),"instanceName":"1"}),"instanceName":"1"}),"instanceName":"1"}),"instanceName":"1"});
            var Q52;
            Q52=makeQuery(id+"F8.opPattern","COPY",BODY,{"derivedFrom":makeQuery(id+"F6.opPattern","COPY",BODY,{"derivedFrom":makeQuery(id+"F5.opPattern","COPY",BODY,{"derivedFrom":makeQuery(id+"F4.opPattern","COPY",BODY,{"derivedFrom":makeQuery(id+"F3.opPattern","COPY",BODY,{"derivedFrom":makeQuery(id+"F2.opPattern","COPY",BODY,{"derivedFrom":makeQuery(id+"F1.opExtrude","SWEPT_BODY",BODY,{"disambiguationData":[OSD([sQuery(id+"F0.wireOp",EDGE,"E2.bottom"),sQuery(id+"F0.wireOp",EDGE,"E2.top"),sQuery(id+"F0.wireOp",EDGE,"E2.left"),sQuery(id+"F0.wireOp",EDGE,"E2.right")])]}),"instanceName":"1"}),"instanceName":"1"}),"instanceName":"1"}),"instanceName":"1"}),"instanceName":"1"}),"instanceName":"1"});
            var Q53;
            Q53=makeQuery(id+"F8.opPattern","COPY",BODY,{"derivedFrom":makeQuery(id+"F7.opPattern","COPY",BODY,{"derivedFrom":makeQuery(id+"F1.opExtrude","SWEPT_BODY",BODY,{"disambiguationData":[OSD([sQuery(id+"F0.wireOp",EDGE,"E0.bottom"),sQuery(id+"F0.wireOp",EDGE,"E0.top"),sQuery(id+"F0.wireOp",EDGE,"E0.left"),sQuery(id+"F0.wireOp",EDGE,"E0.right")])]}),"instanceName":"1"}),"instanceName":"1"});
            var Q54;
            Q54=makeQuery(id+"F8.opPattern","COPY",BODY,{"derivedFrom":makeQuery(id+"F7.opPattern","COPY",BODY,{"derivedFrom":makeQuery(id+"F1.opExtrude","SWEPT_BODY",BODY,{"disambiguationData":[OSD([sQuery(id+"F0.wireOp",EDGE,"E1.bottom"),sQuery(id+"F0.wireOp",EDGE,"E1.top"),sQuery(id+"F0.wireOp",EDGE,"E1.left"),sQuery(id+"F0.wireOp",EDGE,"E1.right")])]}),"instanceName":"1"}),"instanceName":"1"});
            var Q55;
            Q55=makeQuery(id+"F8.opPattern","COPY",BODY,{"derivedFrom":makeQuery(id+"F7.opPattern","COPY",BODY,{"derivedFrom":makeQuery(id+"F1.opExtrude","SWEPT_BODY",BODY,{"disambiguationData":[OSD([sQuery(id+"F0.wireOp",EDGE,"E2.bottom"),sQuery(id+"F0.wireOp",EDGE,"E2.top"),sQuery(id+"F0.wireOp",EDGE,"E2.left"),sQuery(id+"F0.wireOp",EDGE,"E2.right")])]}),"instanceName":"1"}),"instanceName":"1"});
            var Q56;
            Q56=makeQuery(id+"F8.opPattern","COPY",BODY,{"derivedFrom":makeQuery(id+"F7.opPattern","COPY",BODY,{"derivedFrom":makeQuery(id+"F2.opPattern","COPY",BODY,{"derivedFrom":makeQuery(id+"F1.opExtrude","SWEPT_BODY",BODY,{"disambiguationData":[OSD([sQuery(id+"F0.wireOp",EDGE,"E0.bottom"),sQuery(id+"F0.wireOp",EDGE,"E0.top"),sQuery(id+"F0.wireOp",EDGE,"E0.left"),sQuery(id+"F0.wireOp",EDGE,"E0.right")])]}),"instanceName":"1"}),"instanceName":"1"}),"instanceName":"1"});
            var Q57;
            Q57=makeQuery(id+"F8.opPattern","COPY",BODY,{"derivedFrom":makeQuery(id+"F7.opPattern","COPY",BODY,{"derivedFrom":makeQuery(id+"F2.opPattern","COPY",BODY,{"derivedFrom":makeQuery(id+"F1.opExtrude","SWEPT_BODY",BODY,{"disambiguationData":[OSD([sQuery(id+"F0.wireOp",EDGE,"E1.bottom"),sQuery(id+"F0.wireOp",EDGE,"E1.top"),sQuery(id+"F0.wireOp",EDGE,"E1.left"),sQuery(id+"F0.wireOp",EDGE,"E1.right")])]}),"instanceName":"1"}),"instanceName":"1"}),"instanceName":"1"});
            var Q58;
            Q58=makeQuery(id+"F8.opPattern","COPY",BODY,{"derivedFrom":makeQuery(id+"F7.opPattern","COPY",BODY,{"derivedFrom":makeQuery(id+"F2.opPattern","COPY",BODY,{"derivedFrom":makeQuery(id+"F1.opExtrude","SWEPT_BODY",BODY,{"disambiguationData":[OSD([sQuery(id+"F0.wireOp",EDGE,"E2.bottom"),sQuery(id+"F0.wireOp",EDGE,"E2.top"),sQuery(id+"F0.wireOp",EDGE,"E2.left"),sQuery(id+"F0.wireOp",EDGE,"E2.right")])]}),"instanceName":"1"}),"instanceName":"1"}),"instanceName":"1"});
            var Q59;
            Q59=makeQuery(id+"F8.opPattern","COPY",BODY,{"derivedFrom":makeQuery(id+"F7.opPattern","COPY",BODY,{"derivedFrom":makeQuery(id+"F3.opPattern","COPY",BODY,{"derivedFrom":makeQuery(id+"F2.opPattern","COPY",BODY,{"derivedFrom":makeQuery(id+"F1.opExtrude","SWEPT_BODY",BODY,{"disambiguationData":[OSD([sQuery(id+"F0.wireOp",EDGE,"E0.bottom"),sQuery(id+"F0.wireOp",EDGE,"E0.top"),sQuery(id+"F0.wireOp",EDGE,"E0.left"),sQuery(id+"F0.wireOp",EDGE,"E0.right")])]}),"instanceName":"1"}),"instanceName":"1"}),"instanceName":"1"}),"instanceName":"1"});
            var Q60;
            Q60=makeQuery(id+"F8.opPattern","COPY",BODY,{"derivedFrom":makeQuery(id+"F7.opPattern","COPY",BODY,{"derivedFrom":makeQuery(id+"F3.opPattern","COPY",BODY,{"derivedFrom":makeQuery(id+"F2.opPattern","COPY",BODY,{"derivedFrom":makeQuery(id+"F1.opExtrude","SWEPT_BODY",BODY,{"disambiguationData":[OSD([sQuery(id+"F0.wireOp",EDGE,"E1.bottom"),sQuery(id+"F0.wireOp",EDGE,"E1.top"),sQuery(id+"F0.wireOp",EDGE,"E1.left"),sQuery(id+"F0.wireOp",EDGE,"E1.right")])]}),"instanceName":"1"}),"instanceName":"1"}),"instanceName":"1"}),"instanceName":"1"});
            var Q61;
            Q61=makeQuery(id+"F8.opPattern","COPY",BODY,{"derivedFrom":makeQuery(id+"F7.opPattern","COPY",BODY,{"derivedFrom":makeQuery(id+"F3.opPattern","COPY",BODY,{"derivedFrom":makeQuery(id+"F2.opPattern","COPY",BODY,{"derivedFrom":makeQuery(id+"F1.opExtrude","SWEPT_BODY",BODY,{"disambiguationData":[OSD([sQuery(id+"F0.wireOp",EDGE,"E2.bottom"),sQuery(id+"F0.wireOp",EDGE,"E2.top"),sQuery(id+"F0.wireOp",EDGE,"E2.left"),sQuery(id+"F0.wireOp",EDGE,"E2.right")])]}),"instanceName":"1"}),"instanceName":"1"}),"instanceName":"1"}),"instanceName":"1"});
            var Q62;
            Q62=makeQuery(id+"F8.opPattern","COPY",BODY,{"derivedFrom":makeQuery(id+"F7.opPattern","COPY",BODY,{"derivedFrom":makeQuery(id+"F4.opPattern","COPY",BODY,{"derivedFrom":makeQuery(id+"F3.opPattern","COPY",BODY,{"derivedFrom":makeQuery(id+"F2.opPattern","COPY",BODY,{"derivedFrom":makeQuery(id+"F1.opExtrude","SWEPT_BODY",BODY,{"disambiguationData":[OSD([sQuery(id+"F0.wireOp",EDGE,"E0.bottom"),sQuery(id+"F0.wireOp",EDGE,"E0.top"),sQuery(id+"F0.wireOp",EDGE,"E0.left"),sQuery(id+"F0.wireOp",EDGE,"E0.right")])]}),"instanceName":"1"}),"instanceName":"1"}),"instanceName":"1"}),"instanceName":"1"}),"instanceName":"1"});
            var Q63;
            Q63=makeQuery(id+"F8.opPattern","COPY",BODY,{"derivedFrom":makeQuery(id+"F7.opPattern","COPY",BODY,{"derivedFrom":makeQuery(id+"F4.opPattern","COPY",BODY,{"derivedFrom":makeQuery(id+"F3.opPattern","COPY",BODY,{"derivedFrom":makeQuery(id+"F2.opPattern","COPY",BODY,{"derivedFrom":makeQuery(id+"F1.opExtrude","SWEPT_BODY",BODY,{"disambiguationData":[OSD([sQuery(id+"F0.wireOp",EDGE,"E1.bottom"),sQuery(id+"F0.wireOp",EDGE,"E1.top"),sQuery(id+"F0.wireOp",EDGE,"E1.left"),sQuery(id+"F0.wireOp",EDGE,"E1.right")])]}),"instanceName":"1"}),"instanceName":"1"}),"instanceName":"1"}),"instanceName":"1"}),"instanceName":"1"});
            var Q64;
            Q64=makeQuery(id+"F8.opPattern","COPY",BODY,{"derivedFrom":makeQuery(id+"F7.opPattern","COPY",BODY,{"derivedFrom":makeQuery(id+"F4.opPattern","COPY",BODY,{"derivedFrom":makeQuery(id+"F3.opPattern","COPY",BODY,{"derivedFrom":makeQuery(id+"F2.opPattern","COPY",BODY,{"derivedFrom":makeQuery(id+"F1.opExtrude","SWEPT_BODY",BODY,{"disambiguationData":[OSD([sQuery(id+"F0.wireOp",EDGE,"E2.bottom"),sQuery(id+"F0.wireOp",EDGE,"E2.top"),sQuery(id+"F0.wireOp",EDGE,"E2.left"),sQuery(id+"F0.wireOp",EDGE,"E2.right")])]}),"instanceName":"1"}),"instanceName":"1"}),"instanceName":"1"}),"instanceName":"1"}),"instanceName":"1"});
            var Q65;
            Q65=makeQuery(id+"F8.opPattern","COPY",BODY,{"derivedFrom":makeQuery(id+"F7.opPattern","COPY",BODY,{"derivedFrom":makeQuery(id+"F5.opPattern","COPY",BODY,{"derivedFrom":makeQuery(id+"F4.opPattern","COPY",BODY,{"derivedFrom":makeQuery(id+"F3.opPattern","COPY",BODY,{"derivedFrom":makeQuery(id+"F2.opPattern","COPY",BODY,{"derivedFrom":makeQuery(id+"F1.opExtrude","SWEPT_BODY",BODY,{"disambiguationData":[OSD([sQuery(id+"F0.wireOp",EDGE,"E0.bottom"),sQuery(id+"F0.wireOp",EDGE,"E0.top"),sQuery(id+"F0.wireOp",EDGE,"E0.left"),sQuery(id+"F0.wireOp",EDGE,"E0.right")])]}),"instanceName":"1"}),"instanceName":"1"}),"instanceName":"1"}),"instanceName":"1"}),"instanceName":"1"}),"instanceName":"1"});
            var Q66;
            Q66=makeQuery(id+"F8.opPattern","COPY",BODY,{"derivedFrom":makeQuery(id+"F7.opPattern","COPY",BODY,{"derivedFrom":makeQuery(id+"F5.opPattern","COPY",BODY,{"derivedFrom":makeQuery(id+"F4.opPattern","COPY",BODY,{"derivedFrom":makeQuery(id+"F3.opPattern","COPY",BODY,{"derivedFrom":makeQuery(id+"F2.opPattern","COPY",BODY,{"derivedFrom":makeQuery(id+"F1.opExtrude","SWEPT_BODY",BODY,{"disambiguationData":[OSD([sQuery(id+"F0.wireOp",EDGE,"E1.bottom"),sQuery(id+"F0.wireOp",EDGE,"E1.top"),sQuery(id+"F0.wireOp",EDGE,"E1.left"),sQuery(id+"F0.wireOp",EDGE,"E1.right")])]}),"instanceName":"1"}),"instanceName":"1"}),"instanceName":"1"}),"instanceName":"1"}),"instanceName":"1"}),"instanceName":"1"});
            var Q67;
            Q67=makeQuery(id+"F8.opPattern","COPY",BODY,{"derivedFrom":makeQuery(id+"F7.opPattern","COPY",BODY,{"derivedFrom":makeQuery(id+"F5.opPattern","COPY",BODY,{"derivedFrom":makeQuery(id+"F4.opPattern","COPY",BODY,{"derivedFrom":makeQuery(id+"F3.opPattern","COPY",BODY,{"derivedFrom":makeQuery(id+"F2.opPattern","COPY",BODY,{"derivedFrom":makeQuery(id+"F1.opExtrude","SWEPT_BODY",BODY,{"disambiguationData":[OSD([sQuery(id+"F0.wireOp",EDGE,"E2.bottom"),sQuery(id+"F0.wireOp",EDGE,"E2.top"),sQuery(id+"F0.wireOp",EDGE,"E2.left"),sQuery(id+"F0.wireOp",EDGE,"E2.right")])]}),"instanceName":"1"}),"instanceName":"1"}),"instanceName":"1"}),"instanceName":"1"}),"instanceName":"1"}),"instanceName":"1"});
            var Q68;
            Q68=makeQuery(id+"F8.opPattern","COPY",BODY,{"derivedFrom":makeQuery(id+"F7.opPattern","COPY",BODY,{"derivedFrom":makeQuery(id+"F6.opPattern","COPY",BODY,{"derivedFrom":makeQuery(id+"F5.opPattern","COPY",BODY,{"derivedFrom":makeQuery(id+"F4.opPattern","COPY",BODY,{"derivedFrom":makeQuery(id+"F3.opPattern","COPY",BODY,{"derivedFrom":makeQuery(id+"F2.opPattern","COPY",BODY,{"derivedFrom":makeQuery(id+"F1.opExtrude","SWEPT_BODY",BODY,{"disambiguationData":[OSD([sQuery(id+"F0.wireOp",EDGE,"E0.bottom"),sQuery(id+"F0.wireOp",EDGE,"E0.top"),sQuery(id+"F0.wireOp",EDGE,"E0.left"),sQuery(id+"F0.wireOp",EDGE,"E0.right")])]}),"instanceName":"1"}),"instanceName":"1"}),"instanceName":"1"}),"instanceName":"1"}),"instanceName":"1"}),"instanceName":"1"}),"instanceName":"1"});
            var Q69;
            Q69=makeQuery(id+"F8.opPattern","COPY",BODY,{"derivedFrom":makeQuery(id+"F7.opPattern","COPY",BODY,{"derivedFrom":makeQuery(id+"F6.opPattern","COPY",BODY,{"derivedFrom":makeQuery(id+"F5.opPattern","COPY",BODY,{"derivedFrom":makeQuery(id+"F4.opPattern","COPY",BODY,{"derivedFrom":makeQuery(id+"F3.opPattern","COPY",BODY,{"derivedFrom":makeQuery(id+"F2.opPattern","COPY",BODY,{"derivedFrom":makeQuery(id+"F1.opExtrude","SWEPT_BODY",BODY,{"disambiguationData":[OSD([sQuery(id+"F0.wireOp",EDGE,"E1.bottom"),sQuery(id+"F0.wireOp",EDGE,"E1.top"),sQuery(id+"F0.wireOp",EDGE,"E1.left"),sQuery(id+"F0.wireOp",EDGE,"E1.right")])]}),"instanceName":"1"}),"instanceName":"1"}),"instanceName":"1"}),"instanceName":"1"}),"instanceName":"1"}),"instanceName":"1"}),"instanceName":"1"});
            var Q70;
            Q70=makeQuery(id+"F8.opPattern","COPY",BODY,{"derivedFrom":makeQuery(id+"F7.opPattern","COPY",BODY,{"derivedFrom":makeQuery(id+"F6.opPattern","COPY",BODY,{"derivedFrom":makeQuery(id+"F5.opPattern","COPY",BODY,{"derivedFrom":makeQuery(id+"F4.opPattern","COPY",BODY,{"derivedFrom":makeQuery(id+"F3.opPattern","COPY",BODY,{"derivedFrom":makeQuery(id+"F2.opPattern","COPY",BODY,{"derivedFrom":makeQuery(id+"F1.opExtrude","SWEPT_BODY",BODY,{"disambiguationData":[OSD([sQuery(id+"F0.wireOp",EDGE,"E2.bottom"),sQuery(id+"F0.wireOp",EDGE,"E2.top"),sQuery(id+"F0.wireOp",EDGE,"E2.left"),sQuery(id+"F0.wireOp",EDGE,"E2.right")])]}),"instanceName":"1"}),"instanceName":"1"}),"instanceName":"1"}),"instanceName":"1"}),"instanceName":"1"}),"instanceName":"1"}),"instanceName":"1"});
            var Q71;
            Q71=makeQuery(id+"F9.opPattern","COPY",BODY,{"derivedFrom":makeQuery(id+"F1.opExtrude","SWEPT_BODY",BODY,{"disambiguationData":[OSD([sQuery(id+"F0.wireOp",EDGE,"E0.bottom"),sQuery(id+"F0.wireOp",EDGE,"E0.top"),sQuery(id+"F0.wireOp",EDGE,"E0.left"),sQuery(id+"F0.wireOp",EDGE,"E0.right")])]}),"instanceName":"1"});
            var Q72;
            Q72=makeQuery(id+"F9.opPattern","COPY",BODY,{"derivedFrom":makeQuery(id+"F1.opExtrude","SWEPT_BODY",BODY,{"disambiguationData":[OSD([sQuery(id+"F0.wireOp",EDGE,"E1.bottom"),sQuery(id+"F0.wireOp",EDGE,"E1.top"),sQuery(id+"F0.wireOp",EDGE,"E1.left"),sQuery(id+"F0.wireOp",EDGE,"E1.right")])]}),"instanceName":"1"});
            var Q73;
            Q73=makeQuery(id+"F9.opPattern","COPY",BODY,{"derivedFrom":makeQuery(id+"F1.opExtrude","SWEPT_BODY",BODY,{"disambiguationData":[OSD([sQuery(id+"F0.wireOp",EDGE,"E2.bottom"),sQuery(id+"F0.wireOp",EDGE,"E2.top"),sQuery(id+"F0.wireOp",EDGE,"E2.left"),sQuery(id+"F0.wireOp",EDGE,"E2.right")])]}),"instanceName":"1"});
            var Q74;
            Q74=makeQuery(id+"F9.opPattern","COPY",BODY,{"derivedFrom":makeQuery(id+"F2.opPattern","COPY",BODY,{"derivedFrom":makeQuery(id+"F1.opExtrude","SWEPT_BODY",BODY,{"disambiguationData":[OSD([sQuery(id+"F0.wireOp",EDGE,"E0.bottom"),sQuery(id+"F0.wireOp",EDGE,"E0.top"),sQuery(id+"F0.wireOp",EDGE,"E0.left"),sQuery(id+"F0.wireOp",EDGE,"E0.right")])]}),"instanceName":"1"}),"instanceName":"1"});
            var Q75;
            Q75=makeQuery(id+"F9.opPattern","COPY",BODY,{"derivedFrom":makeQuery(id+"F2.opPattern","COPY",BODY,{"derivedFrom":makeQuery(id+"F1.opExtrude","SWEPT_BODY",BODY,{"disambiguationData":[OSD([sQuery(id+"F0.wireOp",EDGE,"E1.bottom"),sQuery(id+"F0.wireOp",EDGE,"E1.top"),sQuery(id+"F0.wireOp",EDGE,"E1.left"),sQuery(id+"F0.wireOp",EDGE,"E1.right")])]}),"instanceName":"1"}),"instanceName":"1"});
            var Q76;
            Q76=makeQuery(id+"F9.opPattern","COPY",BODY,{"derivedFrom":makeQuery(id+"F2.opPattern","COPY",BODY,{"derivedFrom":makeQuery(id+"F1.opExtrude","SWEPT_BODY",BODY,{"disambiguationData":[OSD([sQuery(id+"F0.wireOp",EDGE,"E2.bottom"),sQuery(id+"F0.wireOp",EDGE,"E2.top"),sQuery(id+"F0.wireOp",EDGE,"E2.left"),sQuery(id+"F0.wireOp",EDGE,"E2.right")])]}),"instanceName":"1"}),"instanceName":"1"});
            var Q77;
            Q77=makeQuery(id+"F9.opPattern","COPY",BODY,{"derivedFrom":makeQuery(id+"F3.opPattern","COPY",BODY,{"derivedFrom":makeQuery(id+"F2.opPattern","COPY",BODY,{"derivedFrom":makeQuery(id+"F1.opExtrude","SWEPT_BODY",BODY,{"disambiguationData":[OSD([sQuery(id+"F0.wireOp",EDGE,"E0.bottom"),sQuery(id+"F0.wireOp",EDGE,"E0.top"),sQuery(id+"F0.wireOp",EDGE,"E0.left"),sQuery(id+"F0.wireOp",EDGE,"E0.right")])]}),"instanceName":"1"}),"instanceName":"1"}),"instanceName":"1"});
            var Q78;
            Q78=makeQuery(id+"F9.opPattern","COPY",BODY,{"derivedFrom":makeQuery(id+"F3.opPattern","COPY",BODY,{"derivedFrom":makeQuery(id+"F2.opPattern","COPY",BODY,{"derivedFrom":makeQuery(id+"F1.opExtrude","SWEPT_BODY",BODY,{"disambiguationData":[OSD([sQuery(id+"F0.wireOp",EDGE,"E1.bottom"),sQuery(id+"F0.wireOp",EDGE,"E1.top"),sQuery(id+"F0.wireOp",EDGE,"E1.left"),sQuery(id+"F0.wireOp",EDGE,"E1.right")])]}),"instanceName":"1"}),"instanceName":"1"}),"instanceName":"1"});
            var Q79;
            Q79=makeQuery(id+"F9.opPattern","COPY",BODY,{"derivedFrom":makeQuery(id+"F3.opPattern","COPY",BODY,{"derivedFrom":makeQuery(id+"F2.opPattern","COPY",BODY,{"derivedFrom":makeQuery(id+"F1.opExtrude","SWEPT_BODY",BODY,{"disambiguationData":[OSD([sQuery(id+"F0.wireOp",EDGE,"E2.bottom"),sQuery(id+"F0.wireOp",EDGE,"E2.top"),sQuery(id+"F0.wireOp",EDGE,"E2.left"),sQuery(id+"F0.wireOp",EDGE,"E2.right")])]}),"instanceName":"1"}),"instanceName":"1"}),"instanceName":"1"});
            var Q80;
            Q80=makeQuery(id+"F9.opPattern","COPY",BODY,{"derivedFrom":makeQuery(id+"F4.opPattern","COPY",BODY,{"derivedFrom":makeQuery(id+"F3.opPattern","COPY",BODY,{"derivedFrom":makeQuery(id+"F2.opPattern","COPY",BODY,{"derivedFrom":makeQuery(id+"F1.opExtrude","SWEPT_BODY",BODY,{"disambiguationData":[OSD([sQuery(id+"F0.wireOp",EDGE,"E0.bottom"),sQuery(id+"F0.wireOp",EDGE,"E0.top"),sQuery(id+"F0.wireOp",EDGE,"E0.left"),sQuery(id+"F0.wireOp",EDGE,"E0.right")])]}),"instanceName":"1"}),"instanceName":"1"}),"instanceName":"1"}),"instanceName":"1"});
            var Q81;
            Q81=makeQuery(id+"F9.opPattern","COPY",BODY,{"derivedFrom":makeQuery(id+"F4.opPattern","COPY",BODY,{"derivedFrom":makeQuery(id+"F3.opPattern","COPY",BODY,{"derivedFrom":makeQuery(id+"F2.opPattern","COPY",BODY,{"derivedFrom":makeQuery(id+"F1.opExtrude","SWEPT_BODY",BODY,{"disambiguationData":[OSD([sQuery(id+"F0.wireOp",EDGE,"E1.bottom"),sQuery(id+"F0.wireOp",EDGE,"E1.top"),sQuery(id+"F0.wireOp",EDGE,"E1.left"),sQuery(id+"F0.wireOp",EDGE,"E1.right")])]}),"instanceName":"1"}),"instanceName":"1"}),"instanceName":"1"}),"instanceName":"1"});
            var Q82;
            Q82=makeQuery(id+"F9.opPattern","COPY",BODY,{"derivedFrom":makeQuery(id+"F4.opPattern","COPY",BODY,{"derivedFrom":makeQuery(id+"F3.opPattern","COPY",BODY,{"derivedFrom":makeQuery(id+"F2.opPattern","COPY",BODY,{"derivedFrom":makeQuery(id+"F1.opExtrude","SWEPT_BODY",BODY,{"disambiguationData":[OSD([sQuery(id+"F0.wireOp",EDGE,"E2.bottom"),sQuery(id+"F0.wireOp",EDGE,"E2.top"),sQuery(id+"F0.wireOp",EDGE,"E2.left"),sQuery(id+"F0.wireOp",EDGE,"E2.right")])]}),"instanceName":"1"}),"instanceName":"1"}),"instanceName":"1"}),"instanceName":"1"});
            var Q83;
            Q83=makeQuery(id+"F9.opPattern","COPY",BODY,{"derivedFrom":makeQuery(id+"F5.opPattern","COPY",BODY,{"derivedFrom":makeQuery(id+"F4.opPattern","COPY",BODY,{"derivedFrom":makeQuery(id+"F3.opPattern","COPY",BODY,{"derivedFrom":makeQuery(id+"F2.opPattern","COPY",BODY,{"derivedFrom":makeQuery(id+"F1.opExtrude","SWEPT_BODY",BODY,{"disambiguationData":[OSD([sQuery(id+"F0.wireOp",EDGE,"E0.bottom"),sQuery(id+"F0.wireOp",EDGE,"E0.top"),sQuery(id+"F0.wireOp",EDGE,"E0.left"),sQuery(id+"F0.wireOp",EDGE,"E0.right")])]}),"instanceName":"1"}),"instanceName":"1"}),"instanceName":"1"}),"instanceName":"1"}),"instanceName":"1"});
            var Q84;
            Q84=makeQuery(id+"F9.opPattern","COPY",BODY,{"derivedFrom":makeQuery(id+"F5.opPattern","COPY",BODY,{"derivedFrom":makeQuery(id+"F4.opPattern","COPY",BODY,{"derivedFrom":makeQuery(id+"F3.opPattern","COPY",BODY,{"derivedFrom":makeQuery(id+"F2.opPattern","COPY",BODY,{"derivedFrom":makeQuery(id+"F1.opExtrude","SWEPT_BODY",BODY,{"disambiguationData":[OSD([sQuery(id+"F0.wireOp",EDGE,"E1.bottom"),sQuery(id+"F0.wireOp",EDGE,"E1.top"),sQuery(id+"F0.wireOp",EDGE,"E1.left"),sQuery(id+"F0.wireOp",EDGE,"E1.right")])]}),"instanceName":"1"}),"instanceName":"1"}),"instanceName":"1"}),"instanceName":"1"}),"instanceName":"1"});
            var Q85;
            Q85=makeQuery(id+"F9.opPattern","COPY",BODY,{"derivedFrom":makeQuery(id+"F5.opPattern","COPY",BODY,{"derivedFrom":makeQuery(id+"F4.opPattern","COPY",BODY,{"derivedFrom":makeQuery(id+"F3.opPattern","COPY",BODY,{"derivedFrom":makeQuery(id+"F2.opPattern","COPY",BODY,{"derivedFrom":makeQuery(id+"F1.opExtrude","SWEPT_BODY",BODY,{"disambiguationData":[OSD([sQuery(id+"F0.wireOp",EDGE,"E2.bottom"),sQuery(id+"F0.wireOp",EDGE,"E2.top"),sQuery(id+"F0.wireOp",EDGE,"E2.left"),sQuery(id+"F0.wireOp",EDGE,"E2.right")])]}),"instanceName":"1"}),"instanceName":"1"}),"instanceName":"1"}),"instanceName":"1"}),"instanceName":"1"});
            var Q86;
            Q86=makeQuery(id+"F9.opPattern","COPY",BODY,{"derivedFrom":makeQuery(id+"F6.opPattern","COPY",BODY,{"derivedFrom":makeQuery(id+"F5.opPattern","COPY",BODY,{"derivedFrom":makeQuery(id+"F4.opPattern","COPY",BODY,{"derivedFrom":makeQuery(id+"F3.opPattern","COPY",BODY,{"derivedFrom":makeQuery(id+"F2.opPattern","COPY",BODY,{"derivedFrom":makeQuery(id+"F1.opExtrude","SWEPT_BODY",BODY,{"disambiguationData":[OSD([sQuery(id+"F0.wireOp",EDGE,"E0.bottom"),sQuery(id+"F0.wireOp",EDGE,"E0.top"),sQuery(id+"F0.wireOp",EDGE,"E0.left"),sQuery(id+"F0.wireOp",EDGE,"E0.right")])]}),"instanceName":"1"}),"instanceName":"1"}),"instanceName":"1"}),"instanceName":"1"}),"instanceName":"1"}),"instanceName":"1"});
            var Q87;
            Q87=makeQuery(id+"F9.opPattern","COPY",BODY,{"derivedFrom":makeQuery(id+"F6.opPattern","COPY",BODY,{"derivedFrom":makeQuery(id+"F5.opPattern","COPY",BODY,{"derivedFrom":makeQuery(id+"F4.opPattern","COPY",BODY,{"derivedFrom":makeQuery(id+"F3.opPattern","COPY",BODY,{"derivedFrom":makeQuery(id+"F2.opPattern","COPY",BODY,{"derivedFrom":makeQuery(id+"F1.opExtrude","SWEPT_BODY",BODY,{"disambiguationData":[OSD([sQuery(id+"F0.wireOp",EDGE,"E1.bottom"),sQuery(id+"F0.wireOp",EDGE,"E1.top"),sQuery(id+"F0.wireOp",EDGE,"E1.left"),sQuery(id+"F0.wireOp",EDGE,"E1.right")])]}),"instanceName":"1"}),"instanceName":"1"}),"instanceName":"1"}),"instanceName":"1"}),"instanceName":"1"}),"instanceName":"1"});
            var Q88;
            Q88=makeQuery(id+"F9.opPattern","COPY",BODY,{"derivedFrom":makeQuery(id+"F6.opPattern","COPY",BODY,{"derivedFrom":makeQuery(id+"F5.opPattern","COPY",BODY,{"derivedFrom":makeQuery(id+"F4.opPattern","COPY",BODY,{"derivedFrom":makeQuery(id+"F3.opPattern","COPY",BODY,{"derivedFrom":makeQuery(id+"F2.opPattern","COPY",BODY,{"derivedFrom":makeQuery(id+"F1.opExtrude","SWEPT_BODY",BODY,{"disambiguationData":[OSD([sQuery(id+"F0.wireOp",EDGE,"E2.bottom"),sQuery(id+"F0.wireOp",EDGE,"E2.top"),sQuery(id+"F0.wireOp",EDGE,"E2.left"),sQuery(id+"F0.wireOp",EDGE,"E2.right")])]}),"instanceName":"1"}),"instanceName":"1"}),"instanceName":"1"}),"instanceName":"1"}),"instanceName":"1"}),"instanceName":"1"});
            var Q89;
            Q89=makeQuery(id+"F9.opPattern","COPY",BODY,{"derivedFrom":makeQuery(id+"F7.opPattern","COPY",BODY,{"derivedFrom":makeQuery(id+"F1.opExtrude","SWEPT_BODY",BODY,{"disambiguationData":[OSD([sQuery(id+"F0.wireOp",EDGE,"E0.bottom"),sQuery(id+"F0.wireOp",EDGE,"E0.top"),sQuery(id+"F0.wireOp",EDGE,"E0.left"),sQuery(id+"F0.wireOp",EDGE,"E0.right")])]}),"instanceName":"1"}),"instanceName":"1"});
            var Q90;
            Q90=makeQuery(id+"F9.opPattern","COPY",BODY,{"derivedFrom":makeQuery(id+"F7.opPattern","COPY",BODY,{"derivedFrom":makeQuery(id+"F1.opExtrude","SWEPT_BODY",BODY,{"disambiguationData":[OSD([sQuery(id+"F0.wireOp",EDGE,"E1.bottom"),sQuery(id+"F0.wireOp",EDGE,"E1.top"),sQuery(id+"F0.wireOp",EDGE,"E1.left"),sQuery(id+"F0.wireOp",EDGE,"E1.right")])]}),"instanceName":"1"}),"instanceName":"1"});
            var Q91;
            Q91=makeQuery(id+"F9.opPattern","COPY",BODY,{"derivedFrom":makeQuery(id+"F7.opPattern","COPY",BODY,{"derivedFrom":makeQuery(id+"F1.opExtrude","SWEPT_BODY",BODY,{"disambiguationData":[OSD([sQuery(id+"F0.wireOp",EDGE,"E2.bottom"),sQuery(id+"F0.wireOp",EDGE,"E2.top"),sQuery(id+"F0.wireOp",EDGE,"E2.left"),sQuery(id+"F0.wireOp",EDGE,"E2.right")])]}),"instanceName":"1"}),"instanceName":"1"});
            var Q92;
            Q92=makeQuery(id+"F9.opPattern","COPY",BODY,{"derivedFrom":makeQuery(id+"F7.opPattern","COPY",BODY,{"derivedFrom":makeQuery(id+"F2.opPattern","COPY",BODY,{"derivedFrom":makeQuery(id+"F1.opExtrude","SWEPT_BODY",BODY,{"disambiguationData":[OSD([sQuery(id+"F0.wireOp",EDGE,"E0.bottom"),sQuery(id+"F0.wireOp",EDGE,"E0.top"),sQuery(id+"F0.wireOp",EDGE,"E0.left"),sQuery(id+"F0.wireOp",EDGE,"E0.right")])]}),"instanceName":"1"}),"instanceName":"1"}),"instanceName":"1"});
            var Q93;
            Q93=makeQuery(id+"F9.opPattern","COPY",BODY,{"derivedFrom":makeQuery(id+"F7.opPattern","COPY",BODY,{"derivedFrom":makeQuery(id+"F2.opPattern","COPY",BODY,{"derivedFrom":makeQuery(id+"F1.opExtrude","SWEPT_BODY",BODY,{"disambiguationData":[OSD([sQuery(id+"F0.wireOp",EDGE,"E1.bottom"),sQuery(id+"F0.wireOp",EDGE,"E1.top"),sQuery(id+"F0.wireOp",EDGE,"E1.left"),sQuery(id+"F0.wireOp",EDGE,"E1.right")])]}),"instanceName":"1"}),"instanceName":"1"}),"instanceName":"1"});
            var Q94;
            Q94=makeQuery(id+"F9.opPattern","COPY",BODY,{"derivedFrom":makeQuery(id+"F7.opPattern","COPY",BODY,{"derivedFrom":makeQuery(id+"F2.opPattern","COPY",BODY,{"derivedFrom":makeQuery(id+"F1.opExtrude","SWEPT_BODY",BODY,{"disambiguationData":[OSD([sQuery(id+"F0.wireOp",EDGE,"E2.bottom"),sQuery(id+"F0.wireOp",EDGE,"E2.top"),sQuery(id+"F0.wireOp",EDGE,"E2.left"),sQuery(id+"F0.wireOp",EDGE,"E2.right")])]}),"instanceName":"1"}),"instanceName":"1"}),"instanceName":"1"});
            var Q95;
            Q95=makeQuery(id+"F9.opPattern","COPY",BODY,{"derivedFrom":makeQuery(id+"F7.opPattern","COPY",BODY,{"derivedFrom":makeQuery(id+"F3.opPattern","COPY",BODY,{"derivedFrom":makeQuery(id+"F2.opPattern","COPY",BODY,{"derivedFrom":makeQuery(id+"F1.opExtrude","SWEPT_BODY",BODY,{"disambiguationData":[OSD([sQuery(id+"F0.wireOp",EDGE,"E0.bottom"),sQuery(id+"F0.wireOp",EDGE,"E0.top"),sQuery(id+"F0.wireOp",EDGE,"E0.left"),sQuery(id+"F0.wireOp",EDGE,"E0.right")])]}),"instanceName":"1"}),"instanceName":"1"}),"instanceName":"1"}),"instanceName":"1"});
            var Q96;
            Q96=makeQuery(id+"F9.opPattern","COPY",BODY,{"derivedFrom":makeQuery(id+"F7.opPattern","COPY",BODY,{"derivedFrom":makeQuery(id+"F3.opPattern","COPY",BODY,{"derivedFrom":makeQuery(id+"F2.opPattern","COPY",BODY,{"derivedFrom":makeQuery(id+"F1.opExtrude","SWEPT_BODY",BODY,{"disambiguationData":[OSD([sQuery(id+"F0.wireOp",EDGE,"E1.bottom"),sQuery(id+"F0.wireOp",EDGE,"E1.top"),sQuery(id+"F0.wireOp",EDGE,"E1.left"),sQuery(id+"F0.wireOp",EDGE,"E1.right")])]}),"instanceName":"1"}),"instanceName":"1"}),"instanceName":"1"}),"instanceName":"1"});
            var Q97;
            Q97=makeQuery(id+"F9.opPattern","COPY",BODY,{"derivedFrom":makeQuery(id+"F7.opPattern","COPY",BODY,{"derivedFrom":makeQuery(id+"F3.opPattern","COPY",BODY,{"derivedFrom":makeQuery(id+"F2.opPattern","COPY",BODY,{"derivedFrom":makeQuery(id+"F1.opExtrude","SWEPT_BODY",BODY,{"disambiguationData":[OSD([sQuery(id+"F0.wireOp",EDGE,"E2.bottom"),sQuery(id+"F0.wireOp",EDGE,"E2.top"),sQuery(id+"F0.wireOp",EDGE,"E2.left"),sQuery(id+"F0.wireOp",EDGE,"E2.right")])]}),"instanceName":"1"}),"instanceName":"1"}),"instanceName":"1"}),"instanceName":"1"});
            var Q98;
            Q98=makeQuery(id+"F9.opPattern","COPY",BODY,{"derivedFrom":makeQuery(id+"F7.opPattern","COPY",BODY,{"derivedFrom":makeQuery(id+"F4.opPattern","COPY",BODY,{"derivedFrom":makeQuery(id+"F3.opPattern","COPY",BODY,{"derivedFrom":makeQuery(id+"F2.opPattern","COPY",BODY,{"derivedFrom":makeQuery(id+"F1.opExtrude","SWEPT_BODY",BODY,{"disambiguationData":[OSD([sQuery(id+"F0.wireOp",EDGE,"E0.bottom"),sQuery(id+"F0.wireOp",EDGE,"E0.top"),sQuery(id+"F0.wireOp",EDGE,"E0.left"),sQuery(id+"F0.wireOp",EDGE,"E0.right")])]}),"instanceName":"1"}),"instanceName":"1"}),"instanceName":"1"}),"instanceName":"1"}),"instanceName":"1"});
            var Q99;
            Q99=makeQuery(id+"F9.opPattern","COPY",BODY,{"derivedFrom":makeQuery(id+"F7.opPattern","COPY",BODY,{"derivedFrom":makeQuery(id+"F4.opPattern","COPY",BODY,{"derivedFrom":makeQuery(id+"F3.opPattern","COPY",BODY,{"derivedFrom":makeQuery(id+"F2.opPattern","COPY",BODY,{"derivedFrom":makeQuery(id+"F1.opExtrude","SWEPT_BODY",BODY,{"disambiguationData":[OSD([sQuery(id+"F0.wireOp",EDGE,"E1.bottom"),sQuery(id+"F0.wireOp",EDGE,"E1.top"),sQuery(id+"F0.wireOp",EDGE,"E1.left"),sQuery(id+"F0.wireOp",EDGE,"E1.right")])]}),"instanceName":"1"}),"instanceName":"1"}),"instanceName":"1"}),"instanceName":"1"}),"instanceName":"1"});
            var Q100;
            Q100=makeQuery(id+"F9.opPattern","COPY",BODY,{"derivedFrom":makeQuery(id+"F7.opPattern","COPY",BODY,{"derivedFrom":makeQuery(id+"F4.opPattern","COPY",BODY,{"derivedFrom":makeQuery(id+"F3.opPattern","COPY",BODY,{"derivedFrom":makeQuery(id+"F2.opPattern","COPY",BODY,{"derivedFrom":makeQuery(id+"F1.opExtrude","SWEPT_BODY",BODY,{"disambiguationData":[OSD([sQuery(id+"F0.wireOp",EDGE,"E2.bottom"),sQuery(id+"F0.wireOp",EDGE,"E2.top"),sQuery(id+"F0.wireOp",EDGE,"E2.left"),sQuery(id+"F0.wireOp",EDGE,"E2.right")])]}),"instanceName":"1"}),"instanceName":"1"}),"instanceName":"1"}),"instanceName":"1"}),"instanceName":"1"});
            var Q101;
            Q101=makeQuery(id+"F9.opPattern","COPY",BODY,{"derivedFrom":makeQuery(id+"F7.opPattern","COPY",BODY,{"derivedFrom":makeQuery(id+"F5.opPattern","COPY",BODY,{"derivedFrom":makeQuery(id+"F4.opPattern","COPY",BODY,{"derivedFrom":makeQuery(id+"F3.opPattern","COPY",BODY,{"derivedFrom":makeQuery(id+"F2.opPattern","COPY",BODY,{"derivedFrom":makeQuery(id+"F1.opExtrude","SWEPT_BODY",BODY,{"disambiguationData":[OSD([sQuery(id+"F0.wireOp",EDGE,"E0.bottom"),sQuery(id+"F0.wireOp",EDGE,"E0.top"),sQuery(id+"F0.wireOp",EDGE,"E0.left"),sQuery(id+"F0.wireOp",EDGE,"E0.right")])]}),"instanceName":"1"}),"instanceName":"1"}),"instanceName":"1"}),"instanceName":"1"}),"instanceName":"1"}),"instanceName":"1"});
            var Q102;
            Q102=makeQuery(id+"F9.opPattern","COPY",BODY,{"derivedFrom":makeQuery(id+"F7.opPattern","COPY",BODY,{"derivedFrom":makeQuery(id+"F5.opPattern","COPY",BODY,{"derivedFrom":makeQuery(id+"F4.opPattern","COPY",BODY,{"derivedFrom":makeQuery(id+"F3.opPattern","COPY",BODY,{"derivedFrom":makeQuery(id+"F2.opPattern","COPY",BODY,{"derivedFrom":makeQuery(id+"F1.opExtrude","SWEPT_BODY",BODY,{"disambiguationData":[OSD([sQuery(id+"F0.wireOp",EDGE,"E1.bottom"),sQuery(id+"F0.wireOp",EDGE,"E1.top"),sQuery(id+"F0.wireOp",EDGE,"E1.left"),sQuery(id+"F0.wireOp",EDGE,"E1.right")])]}),"instanceName":"1"}),"instanceName":"1"}),"instanceName":"1"}),"instanceName":"1"}),"instanceName":"1"}),"instanceName":"1"});
            var Q103;
            Q103=makeQuery(id+"F9.opPattern","COPY",BODY,{"derivedFrom":makeQuery(id+"F7.opPattern","COPY",BODY,{"derivedFrom":makeQuery(id+"F5.opPattern","COPY",BODY,{"derivedFrom":makeQuery(id+"F4.opPattern","COPY",BODY,{"derivedFrom":makeQuery(id+"F3.opPattern","COPY",BODY,{"derivedFrom":makeQuery(id+"F2.opPattern","COPY",BODY,{"derivedFrom":makeQuery(id+"F1.opExtrude","SWEPT_BODY",BODY,{"disambiguationData":[OSD([sQuery(id+"F0.wireOp",EDGE,"E2.bottom"),sQuery(id+"F0.wireOp",EDGE,"E2.top"),sQuery(id+"F0.wireOp",EDGE,"E2.left"),sQuery(id+"F0.wireOp",EDGE,"E2.right")])]}),"instanceName":"1"}),"instanceName":"1"}),"instanceName":"1"}),"instanceName":"1"}),"instanceName":"1"}),"instanceName":"1"});
            var Q104;
            Q104=makeQuery(id+"F9.opPattern","COPY",BODY,{"derivedFrom":makeQuery(id+"F7.opPattern","COPY",BODY,{"derivedFrom":makeQuery(id+"F6.opPattern","COPY",BODY,{"derivedFrom":makeQuery(id+"F5.opPattern","COPY",BODY,{"derivedFrom":makeQuery(id+"F4.opPattern","COPY",BODY,{"derivedFrom":makeQuery(id+"F3.opPattern","COPY",BODY,{"derivedFrom":makeQuery(id+"F2.opPattern","COPY",BODY,{"derivedFrom":makeQuery(id+"F1.opExtrude","SWEPT_BODY",BODY,{"disambiguationData":[OSD([sQuery(id+"F0.wireOp",EDGE,"E0.bottom"),sQuery(id+"F0.wireOp",EDGE,"E0.top"),sQuery(id+"F0.wireOp",EDGE,"E0.left"),sQuery(id+"F0.wireOp",EDGE,"E0.right")])]}),"instanceName":"1"}),"instanceName":"1"}),"instanceName":"1"}),"instanceName":"1"}),"instanceName":"1"}),"instanceName":"1"}),"instanceName":"1"});
            var Q105;
            Q105=makeQuery(id+"F9.opPattern","COPY",BODY,{"derivedFrom":makeQuery(id+"F7.opPattern","COPY",BODY,{"derivedFrom":makeQuery(id+"F6.opPattern","COPY",BODY,{"derivedFrom":makeQuery(id+"F5.opPattern","COPY",BODY,{"derivedFrom":makeQuery(id+"F4.opPattern","COPY",BODY,{"derivedFrom":makeQuery(id+"F3.opPattern","COPY",BODY,{"derivedFrom":makeQuery(id+"F2.opPattern","COPY",BODY,{"derivedFrom":makeQuery(id+"F1.opExtrude","SWEPT_BODY",BODY,{"disambiguationData":[OSD([sQuery(id+"F0.wireOp",EDGE,"E1.bottom"),sQuery(id+"F0.wireOp",EDGE,"E1.top"),sQuery(id+"F0.wireOp",EDGE,"E1.left"),sQuery(id+"F0.wireOp",EDGE,"E1.right")])]}),"instanceName":"1"}),"instanceName":"1"}),"instanceName":"1"}),"instanceName":"1"}),"instanceName":"1"}),"instanceName":"1"}),"instanceName":"1"});
            var Q106;
            Q106=makeQuery(id+"F9.opPattern","COPY",BODY,{"derivedFrom":makeQuery(id+"F7.opPattern","COPY",BODY,{"derivedFrom":makeQuery(id+"F6.opPattern","COPY",BODY,{"derivedFrom":makeQuery(id+"F5.opPattern","COPY",BODY,{"derivedFrom":makeQuery(id+"F4.opPattern","COPY",BODY,{"derivedFrom":makeQuery(id+"F3.opPattern","COPY",BODY,{"derivedFrom":makeQuery(id+"F2.opPattern","COPY",BODY,{"derivedFrom":makeQuery(id+"F1.opExtrude","SWEPT_BODY",BODY,{"disambiguationData":[OSD([sQuery(id+"F0.wireOp",EDGE,"E2.bottom"),sQuery(id+"F0.wireOp",EDGE,"E2.top"),sQuery(id+"F0.wireOp",EDGE,"E2.left"),sQuery(id+"F0.wireOp",EDGE,"E2.right")])]}),"instanceName":"1"}),"instanceName":"1"}),"instanceName":"1"}),"instanceName":"1"}),"instanceName":"1"}),"instanceName":"1"}),"instanceName":"1"});
            var Q107;
            Q107=makeQuery(id+"F9.opPattern","COPY",BODY,{"derivedFrom":makeQuery(id+"F8.opPattern","COPY",BODY,{"derivedFrom":makeQuery(id+"F1.opExtrude","SWEPT_BODY",BODY,{"disambiguationData":[OSD([sQuery(id+"F0.wireOp",EDGE,"E0.bottom"),sQuery(id+"F0.wireOp",EDGE,"E0.top"),sQuery(id+"F0.wireOp",EDGE,"E0.left"),sQuery(id+"F0.wireOp",EDGE,"E0.right")])]}),"instanceName":"1"}),"instanceName":"1"});
            var Q108;
            Q108=makeQuery(id+"F9.opPattern","COPY",BODY,{"derivedFrom":makeQuery(id+"F8.opPattern","COPY",BODY,{"derivedFrom":makeQuery(id+"F1.opExtrude","SWEPT_BODY",BODY,{"disambiguationData":[OSD([sQuery(id+"F0.wireOp",EDGE,"E1.bottom"),sQuery(id+"F0.wireOp",EDGE,"E1.top"),sQuery(id+"F0.wireOp",EDGE,"E1.left"),sQuery(id+"F0.wireOp",EDGE,"E1.right")])]}),"instanceName":"1"}),"instanceName":"1"});
            var Q109;
            Q109=makeQuery(id+"F9.opPattern","COPY",BODY,{"derivedFrom":makeQuery(id+"F8.opPattern","COPY",BODY,{"derivedFrom":makeQuery(id+"F1.opExtrude","SWEPT_BODY",BODY,{"disambiguationData":[OSD([sQuery(id+"F0.wireOp",EDGE,"E2.bottom"),sQuery(id+"F0.wireOp",EDGE,"E2.top"),sQuery(id+"F0.wireOp",EDGE,"E2.left"),sQuery(id+"F0.wireOp",EDGE,"E2.right")])]}),"instanceName":"1"}),"instanceName":"1"});
            var Q110;
            Q110=makeQuery(id+"F9.opPattern","COPY",BODY,{"derivedFrom":makeQuery(id+"F8.opPattern","COPY",BODY,{"derivedFrom":makeQuery(id+"F2.opPattern","COPY",BODY,{"derivedFrom":makeQuery(id+"F1.opExtrude","SWEPT_BODY",BODY,{"disambiguationData":[OSD([sQuery(id+"F0.wireOp",EDGE,"E0.bottom"),sQuery(id+"F0.wireOp",EDGE,"E0.top"),sQuery(id+"F0.wireOp",EDGE,"E0.left"),sQuery(id+"F0.wireOp",EDGE,"E0.right")])]}),"instanceName":"1"}),"instanceName":"1"}),"instanceName":"1"});
            var Q111;
            Q111=makeQuery(id+"F9.opPattern","COPY",BODY,{"derivedFrom":makeQuery(id+"F8.opPattern","COPY",BODY,{"derivedFrom":makeQuery(id+"F2.opPattern","COPY",BODY,{"derivedFrom":makeQuery(id+"F1.opExtrude","SWEPT_BODY",BODY,{"disambiguationData":[OSD([sQuery(id+"F0.wireOp",EDGE,"E1.bottom"),sQuery(id+"F0.wireOp",EDGE,"E1.top"),sQuery(id+"F0.wireOp",EDGE,"E1.left"),sQuery(id+"F0.wireOp",EDGE,"E1.right")])]}),"instanceName":"1"}),"instanceName":"1"}),"instanceName":"1"});
            var Q112;
            Q112=makeQuery(id+"F9.opPattern","COPY",BODY,{"derivedFrom":makeQuery(id+"F8.opPattern","COPY",BODY,{"derivedFrom":makeQuery(id+"F2.opPattern","COPY",BODY,{"derivedFrom":makeQuery(id+"F1.opExtrude","SWEPT_BODY",BODY,{"disambiguationData":[OSD([sQuery(id+"F0.wireOp",EDGE,"E2.bottom"),sQuery(id+"F0.wireOp",EDGE,"E2.top"),sQuery(id+"F0.wireOp",EDGE,"E2.left"),sQuery(id+"F0.wireOp",EDGE,"E2.right")])]}),"instanceName":"1"}),"instanceName":"1"}),"instanceName":"1"});
            var Q113;
            Q113=makeQuery(id+"F9.opPattern","COPY",BODY,{"derivedFrom":makeQuery(id+"F8.opPattern","COPY",BODY,{"derivedFrom":makeQuery(id+"F3.opPattern","COPY",BODY,{"derivedFrom":makeQuery(id+"F2.opPattern","COPY",BODY,{"derivedFrom":makeQuery(id+"F1.opExtrude","SWEPT_BODY",BODY,{"disambiguationData":[OSD([sQuery(id+"F0.wireOp",EDGE,"E0.bottom"),sQuery(id+"F0.wireOp",EDGE,"E0.top"),sQuery(id+"F0.wireOp",EDGE,"E0.left"),sQuery(id+"F0.wireOp",EDGE,"E0.right")])]}),"instanceName":"1"}),"instanceName":"1"}),"instanceName":"1"}),"instanceName":"1"});
            var Q114;
            Q114=makeQuery(id+"F9.opPattern","COPY",BODY,{"derivedFrom":makeQuery(id+"F8.opPattern","COPY",BODY,{"derivedFrom":makeQuery(id+"F3.opPattern","COPY",BODY,{"derivedFrom":makeQuery(id+"F2.opPattern","COPY",BODY,{"derivedFrom":makeQuery(id+"F1.opExtrude","SWEPT_BODY",BODY,{"disambiguationData":[OSD([sQuery(id+"F0.wireOp",EDGE,"E1.bottom"),sQuery(id+"F0.wireOp",EDGE,"E1.top"),sQuery(id+"F0.wireOp",EDGE,"E1.left"),sQuery(id+"F0.wireOp",EDGE,"E1.right")])]}),"instanceName":"1"}),"instanceName":"1"}),"instanceName":"1"}),"instanceName":"1"});
            var Q115;
            Q115=makeQuery(id+"F9.opPattern","COPY",BODY,{"derivedFrom":makeQuery(id+"F8.opPattern","COPY",BODY,{"derivedFrom":makeQuery(id+"F3.opPattern","COPY",BODY,{"derivedFrom":makeQuery(id+"F2.opPattern","COPY",BODY,{"derivedFrom":makeQuery(id+"F1.opExtrude","SWEPT_BODY",BODY,{"disambiguationData":[OSD([sQuery(id+"F0.wireOp",EDGE,"E2.bottom"),sQuery(id+"F0.wireOp",EDGE,"E2.top"),sQuery(id+"F0.wireOp",EDGE,"E2.left"),sQuery(id+"F0.wireOp",EDGE,"E2.right")])]}),"instanceName":"1"}),"instanceName":"1"}),"instanceName":"1"}),"instanceName":"1"});
            var Q116;
            Q116=makeQuery(id+"F9.opPattern","COPY",BODY,{"derivedFrom":makeQuery(id+"F8.opPattern","COPY",BODY,{"derivedFrom":makeQuery(id+"F4.opPattern","COPY",BODY,{"derivedFrom":makeQuery(id+"F3.opPattern","COPY",BODY,{"derivedFrom":makeQuery(id+"F2.opPattern","COPY",BODY,{"derivedFrom":makeQuery(id+"F1.opExtrude","SWEPT_BODY",BODY,{"disambiguationData":[OSD([sQuery(id+"F0.wireOp",EDGE,"E0.bottom"),sQuery(id+"F0.wireOp",EDGE,"E0.top"),sQuery(id+"F0.wireOp",EDGE,"E0.left"),sQuery(id+"F0.wireOp",EDGE,"E0.right")])]}),"instanceName":"1"}),"instanceName":"1"}),"instanceName":"1"}),"instanceName":"1"}),"instanceName":"1"});
            var Q117;
            Q117=makeQuery(id+"F9.opPattern","COPY",BODY,{"derivedFrom":makeQuery(id+"F8.opPattern","COPY",BODY,{"derivedFrom":makeQuery(id+"F4.opPattern","COPY",BODY,{"derivedFrom":makeQuery(id+"F3.opPattern","COPY",BODY,{"derivedFrom":makeQuery(id+"F2.opPattern","COPY",BODY,{"derivedFrom":makeQuery(id+"F1.opExtrude","SWEPT_BODY",BODY,{"disambiguationData":[OSD([sQuery(id+"F0.wireOp",EDGE,"E1.bottom"),sQuery(id+"F0.wireOp",EDGE,"E1.top"),sQuery(id+"F0.wireOp",EDGE,"E1.left"),sQuery(id+"F0.wireOp",EDGE,"E1.right")])]}),"instanceName":"1"}),"instanceName":"1"}),"instanceName":"1"}),"instanceName":"1"}),"instanceName":"1"});
            var Q118;
            Q118=makeQuery(id+"F9.opPattern","COPY",BODY,{"derivedFrom":makeQuery(id+"F8.opPattern","COPY",BODY,{"derivedFrom":makeQuery(id+"F4.opPattern","COPY",BODY,{"derivedFrom":makeQuery(id+"F3.opPattern","COPY",BODY,{"derivedFrom":makeQuery(id+"F2.opPattern","COPY",BODY,{"derivedFrom":makeQuery(id+"F1.opExtrude","SWEPT_BODY",BODY,{"disambiguationData":[OSD([sQuery(id+"F0.wireOp",EDGE,"E2.bottom"),sQuery(id+"F0.wireOp",EDGE,"E2.top"),sQuery(id+"F0.wireOp",EDGE,"E2.left"),sQuery(id+"F0.wireOp",EDGE,"E2.right")])]}),"instanceName":"1"}),"instanceName":"1"}),"instanceName":"1"}),"instanceName":"1"}),"instanceName":"1"});
            var Q119;
            Q119=makeQuery(id+"F9.opPattern","COPY",BODY,{"derivedFrom":makeQuery(id+"F8.opPattern","COPY",BODY,{"derivedFrom":makeQuery(id+"F5.opPattern","COPY",BODY,{"derivedFrom":makeQuery(id+"F4.opPattern","COPY",BODY,{"derivedFrom":makeQuery(id+"F3.opPattern","COPY",BODY,{"derivedFrom":makeQuery(id+"F2.opPattern","COPY",BODY,{"derivedFrom":makeQuery(id+"F1.opExtrude","SWEPT_BODY",BODY,{"disambiguationData":[OSD([sQuery(id+"F0.wireOp",EDGE,"E0.bottom"),sQuery(id+"F0.wireOp",EDGE,"E0.top"),sQuery(id+"F0.wireOp",EDGE,"E0.left"),sQuery(id+"F0.wireOp",EDGE,"E0.right")])]}),"instanceName":"1"}),"instanceName":"1"}),"instanceName":"1"}),"instanceName":"1"}),"instanceName":"1"}),"instanceName":"1"});
            var Q120;
            Q120=makeQuery(id+"F9.opPattern","COPY",BODY,{"derivedFrom":makeQuery(id+"F8.opPattern","COPY",BODY,{"derivedFrom":makeQuery(id+"F5.opPattern","COPY",BODY,{"derivedFrom":makeQuery(id+"F4.opPattern","COPY",BODY,{"derivedFrom":makeQuery(id+"F3.opPattern","COPY",BODY,{"derivedFrom":makeQuery(id+"F2.opPattern","COPY",BODY,{"derivedFrom":makeQuery(id+"F1.opExtrude","SWEPT_BODY",BODY,{"disambiguationData":[OSD([sQuery(id+"F0.wireOp",EDGE,"E1.bottom"),sQuery(id+"F0.wireOp",EDGE,"E1.top"),sQuery(id+"F0.wireOp",EDGE,"E1.left"),sQuery(id+"F0.wireOp",EDGE,"E1.right")])]}),"instanceName":"1"}),"instanceName":"1"}),"instanceName":"1"}),"instanceName":"1"}),"instanceName":"1"}),"instanceName":"1"});
            var Q121;
            Q121=makeQuery(id+"F9.opPattern","COPY",BODY,{"derivedFrom":makeQuery(id+"F8.opPattern","COPY",BODY,{"derivedFrom":makeQuery(id+"F5.opPattern","COPY",BODY,{"derivedFrom":makeQuery(id+"F4.opPattern","COPY",BODY,{"derivedFrom":makeQuery(id+"F3.opPattern","COPY",BODY,{"derivedFrom":makeQuery(id+"F2.opPattern","COPY",BODY,{"derivedFrom":makeQuery(id+"F1.opExtrude","SWEPT_BODY",BODY,{"disambiguationData":[OSD([sQuery(id+"F0.wireOp",EDGE,"E2.bottom"),sQuery(id+"F0.wireOp",EDGE,"E2.top"),sQuery(id+"F0.wireOp",EDGE,"E2.left"),sQuery(id+"F0.wireOp",EDGE,"E2.right")])]}),"instanceName":"1"}),"instanceName":"1"}),"instanceName":"1"}),"instanceName":"1"}),"instanceName":"1"}),"instanceName":"1"});
            var Q122;
            Q122=makeQuery(id+"F9.opPattern","COPY",BODY,{"derivedFrom":makeQuery(id+"F8.opPattern","COPY",BODY,{"derivedFrom":makeQuery(id+"F6.opPattern","COPY",BODY,{"derivedFrom":makeQuery(id+"F5.opPattern","COPY",BODY,{"derivedFrom":makeQuery(id+"F4.opPattern","COPY",BODY,{"derivedFrom":makeQuery(id+"F3.opPattern","COPY",BODY,{"derivedFrom":makeQuery(id+"F2.opPattern","COPY",BODY,{"derivedFrom":makeQuery(id+"F1.opExtrude","SWEPT_BODY",BODY,{"disambiguationData":[OSD([sQuery(id+"F0.wireOp",EDGE,"E0.bottom"),sQuery(id+"F0.wireOp",EDGE,"E0.top"),sQuery(id+"F0.wireOp",EDGE,"E0.left"),sQuery(id+"F0.wireOp",EDGE,"E0.right")])]}),"instanceName":"1"}),"instanceName":"1"}),"instanceName":"1"}),"instanceName":"1"}),"instanceName":"1"}),"instanceName":"1"}),"instanceName":"1"});
            var Q123;
            Q123=makeQuery(id+"F9.opPattern","COPY",BODY,{"derivedFrom":makeQuery(id+"F8.opPattern","COPY",BODY,{"derivedFrom":makeQuery(id+"F6.opPattern","COPY",BODY,{"derivedFrom":makeQuery(id+"F5.opPattern","COPY",BODY,{"derivedFrom":makeQuery(id+"F4.opPattern","COPY",BODY,{"derivedFrom":makeQuery(id+"F3.opPattern","COPY",BODY,{"derivedFrom":makeQuery(id+"F2.opPattern","COPY",BODY,{"derivedFrom":makeQuery(id+"F1.opExtrude","SWEPT_BODY",BODY,{"disambiguationData":[OSD([sQuery(id+"F0.wireOp",EDGE,"E1.bottom"),sQuery(id+"F0.wireOp",EDGE,"E1.top"),sQuery(id+"F0.wireOp",EDGE,"E1.left"),sQuery(id+"F0.wireOp",EDGE,"E1.right")])]}),"instanceName":"1"}),"instanceName":"1"}),"instanceName":"1"}),"instanceName":"1"}),"instanceName":"1"}),"instanceName":"1"}),"instanceName":"1"});
            var Q124;
            Q124=makeQuery(id+"F9.opPattern","COPY",BODY,{"derivedFrom":makeQuery(id+"F8.opPattern","COPY",BODY,{"derivedFrom":makeQuery(id+"F6.opPattern","COPY",BODY,{"derivedFrom":makeQuery(id+"F5.opPattern","COPY",BODY,{"derivedFrom":makeQuery(id+"F4.opPattern","COPY",BODY,{"derivedFrom":makeQuery(id+"F3.opPattern","COPY",BODY,{"derivedFrom":makeQuery(id+"F2.opPattern","COPY",BODY,{"derivedFrom":makeQuery(id+"F1.opExtrude","SWEPT_BODY",BODY,{"disambiguationData":[OSD([sQuery(id+"F0.wireOp",EDGE,"E2.bottom"),sQuery(id+"F0.wireOp",EDGE,"E2.top"),sQuery(id+"F0.wireOp",EDGE,"E2.left"),sQuery(id+"F0.wireOp",EDGE,"E2.right")])]}),"instanceName":"1"}),"instanceName":"1"}),"instanceName":"1"}),"instanceName":"1"}),"instanceName":"1"}),"instanceName":"1"}),"instanceName":"1"});
            var Q125;
            Q125=makeQuery(id+"F9.opPattern","COPY",BODY,{"derivedFrom":makeQuery(id+"F8.opPattern","COPY",BODY,{"derivedFrom":makeQuery(id+"F7.opPattern","COPY",BODY,{"derivedFrom":makeQuery(id+"F1.opExtrude","SWEPT_BODY",BODY,{"disambiguationData":[OSD([sQuery(id+"F0.wireOp",EDGE,"E0.bottom"),sQuery(id+"F0.wireOp",EDGE,"E0.top"),sQuery(id+"F0.wireOp",EDGE,"E0.left"),sQuery(id+"F0.wireOp",EDGE,"E0.right")])]}),"instanceName":"1"}),"instanceName":"1"}),"instanceName":"1"});
            var Q126;
            Q126=makeQuery(id+"F9.opPattern","COPY",BODY,{"derivedFrom":makeQuery(id+"F8.opPattern","COPY",BODY,{"derivedFrom":makeQuery(id+"F7.opPattern","COPY",BODY,{"derivedFrom":makeQuery(id+"F1.opExtrude","SWEPT_BODY",BODY,{"disambiguationData":[OSD([sQuery(id+"F0.wireOp",EDGE,"E1.bottom"),sQuery(id+"F0.wireOp",EDGE,"E1.top"),sQuery(id+"F0.wireOp",EDGE,"E1.left"),sQuery(id+"F0.wireOp",EDGE,"E1.right")])]}),"instanceName":"1"}),"instanceName":"1"}),"instanceName":"1"});
            var Q127;
            Q127=makeQuery(id+"F9.opPattern","COPY",BODY,{"derivedFrom":makeQuery(id+"F8.opPattern","COPY",BODY,{"derivedFrom":makeQuery(id+"F7.opPattern","COPY",BODY,{"derivedFrom":makeQuery(id+"F1.opExtrude","SWEPT_BODY",BODY,{"disambiguationData":[OSD([sQuery(id+"F0.wireOp",EDGE,"E2.bottom"),sQuery(id+"F0.wireOp",EDGE,"E2.top"),sQuery(id+"F0.wireOp",EDGE,"E2.left"),sQuery(id+"F0.wireOp",EDGE,"E2.right")])]}),"instanceName":"1"}),"instanceName":"1"}),"instanceName":"1"});
            var Q128;
            Q128=makeQuery(id+"F9.opPattern","COPY",BODY,{"derivedFrom":makeQuery(id+"F8.opPattern","COPY",BODY,{"derivedFrom":makeQuery(id+"F7.opPattern","COPY",BODY,{"derivedFrom":makeQuery(id+"F2.opPattern","COPY",BODY,{"derivedFrom":makeQuery(id+"F1.opExtrude","SWEPT_BODY",BODY,{"disambiguationData":[OSD([sQuery(id+"F0.wireOp",EDGE,"E0.bottom"),sQuery(id+"F0.wireOp",EDGE,"E0.top"),sQuery(id+"F0.wireOp",EDGE,"E0.left"),sQuery(id+"F0.wireOp",EDGE,"E0.right")])]}),"instanceName":"1"}),"instanceName":"1"}),"instanceName":"1"}),"instanceName":"1"});
            var Q129;
            Q129=makeQuery(id+"F9.opPattern","COPY",BODY,{"derivedFrom":makeQuery(id+"F8.opPattern","COPY",BODY,{"derivedFrom":makeQuery(id+"F7.opPattern","COPY",BODY,{"derivedFrom":makeQuery(id+"F2.opPattern","COPY",BODY,{"derivedFrom":makeQuery(id+"F1.opExtrude","SWEPT_BODY",BODY,{"disambiguationData":[OSD([sQuery(id+"F0.wireOp",EDGE,"E1.bottom"),sQuery(id+"F0.wireOp",EDGE,"E1.top"),sQuery(id+"F0.wireOp",EDGE,"E1.left"),sQuery(id+"F0.wireOp",EDGE,"E1.right")])]}),"instanceName":"1"}),"instanceName":"1"}),"instanceName":"1"}),"instanceName":"1"});
            var Q130;
            Q130=makeQuery(id+"F9.opPattern","COPY",BODY,{"derivedFrom":makeQuery(id+"F8.opPattern","COPY",BODY,{"derivedFrom":makeQuery(id+"F7.opPattern","COPY",BODY,{"derivedFrom":makeQuery(id+"F2.opPattern","COPY",BODY,{"derivedFrom":makeQuery(id+"F1.opExtrude","SWEPT_BODY",BODY,{"disambiguationData":[OSD([sQuery(id+"F0.wireOp",EDGE,"E2.bottom"),sQuery(id+"F0.wireOp",EDGE,"E2.top"),sQuery(id+"F0.wireOp",EDGE,"E2.left"),sQuery(id+"F0.wireOp",EDGE,"E2.right")])]}),"instanceName":"1"}),"instanceName":"1"}),"instanceName":"1"}),"instanceName":"1"});
            var Q131;
            Q131=makeQuery(id+"F9.opPattern","COPY",BODY,{"derivedFrom":makeQuery(id+"F8.opPattern","COPY",BODY,{"derivedFrom":makeQuery(id+"F7.opPattern","COPY",BODY,{"derivedFrom":makeQuery(id+"F3.opPattern","COPY",BODY,{"derivedFrom":makeQuery(id+"F2.opPattern","COPY",BODY,{"derivedFrom":makeQuery(id+"F1.opExtrude","SWEPT_BODY",BODY,{"disambiguationData":[OSD([sQuery(id+"F0.wireOp",EDGE,"E0.bottom"),sQuery(id+"F0.wireOp",EDGE,"E0.top"),sQuery(id+"F0.wireOp",EDGE,"E0.left"),sQuery(id+"F0.wireOp",EDGE,"E0.right")])]}),"instanceName":"1"}),"instanceName":"1"}),"instanceName":"1"}),"instanceName":"1"}),"instanceName":"1"});
            var Q132;
            Q132=makeQuery(id+"F9.opPattern","COPY",BODY,{"derivedFrom":makeQuery(id+"F8.opPattern","COPY",BODY,{"derivedFrom":makeQuery(id+"F7.opPattern","COPY",BODY,{"derivedFrom":makeQuery(id+"F3.opPattern","COPY",BODY,{"derivedFrom":makeQuery(id+"F2.opPattern","COPY",BODY,{"derivedFrom":makeQuery(id+"F1.opExtrude","SWEPT_BODY",BODY,{"disambiguationData":[OSD([sQuery(id+"F0.wireOp",EDGE,"E1.bottom"),sQuery(id+"F0.wireOp",EDGE,"E1.top"),sQuery(id+"F0.wireOp",EDGE,"E1.left"),sQuery(id+"F0.wireOp",EDGE,"E1.right")])]}),"instanceName":"1"}),"instanceName":"1"}),"instanceName":"1"}),"instanceName":"1"}),"instanceName":"1"});
            var Q133;
            Q133=makeQuery(id+"F9.opPattern","COPY",BODY,{"derivedFrom":makeQuery(id+"F8.opPattern","COPY",BODY,{"derivedFrom":makeQuery(id+"F7.opPattern","COPY",BODY,{"derivedFrom":makeQuery(id+"F3.opPattern","COPY",BODY,{"derivedFrom":makeQuery(id+"F2.opPattern","COPY",BODY,{"derivedFrom":makeQuery(id+"F1.opExtrude","SWEPT_BODY",BODY,{"disambiguationData":[OSD([sQuery(id+"F0.wireOp",EDGE,"E2.bottom"),sQuery(id+"F0.wireOp",EDGE,"E2.top"),sQuery(id+"F0.wireOp",EDGE,"E2.left"),sQuery(id+"F0.wireOp",EDGE,"E2.right")])]}),"instanceName":"1"}),"instanceName":"1"}),"instanceName":"1"}),"instanceName":"1"}),"instanceName":"1"});
            var Q134;
            Q134=makeQuery(id+"F9.opPattern","COPY",BODY,{"derivedFrom":makeQuery(id+"F8.opPattern","COPY",BODY,{"derivedFrom":makeQuery(id+"F7.opPattern","COPY",BODY,{"derivedFrom":makeQuery(id+"F4.opPattern","COPY",BODY,{"derivedFrom":makeQuery(id+"F3.opPattern","COPY",BODY,{"derivedFrom":makeQuery(id+"F2.opPattern","COPY",BODY,{"derivedFrom":makeQuery(id+"F1.opExtrude","SWEPT_BODY",BODY,{"disambiguationData":[OSD([sQuery(id+"F0.wireOp",EDGE,"E0.bottom"),sQuery(id+"F0.wireOp",EDGE,"E0.top"),sQuery(id+"F0.wireOp",EDGE,"E0.left"),sQuery(id+"F0.wireOp",EDGE,"E0.right")])]}),"instanceName":"1"}),"instanceName":"1"}),"instanceName":"1"}),"instanceName":"1"}),"instanceName":"1"}),"instanceName":"1"});
            var Q135;
            Q135=makeQuery(id+"F9.opPattern","COPY",BODY,{"derivedFrom":makeQuery(id+"F8.opPattern","COPY",BODY,{"derivedFrom":makeQuery(id+"F7.opPattern","COPY",BODY,{"derivedFrom":makeQuery(id+"F4.opPattern","COPY",BODY,{"derivedFrom":makeQuery(id+"F3.opPattern","COPY",BODY,{"derivedFrom":makeQuery(id+"F2.opPattern","COPY",BODY,{"derivedFrom":makeQuery(id+"F1.opExtrude","SWEPT_BODY",BODY,{"disambiguationData":[OSD([sQuery(id+"F0.wireOp",EDGE,"E1.bottom"),sQuery(id+"F0.wireOp",EDGE,"E1.top"),sQuery(id+"F0.wireOp",EDGE,"E1.left"),sQuery(id+"F0.wireOp",EDGE,"E1.right")])]}),"instanceName":"1"}),"instanceName":"1"}),"instanceName":"1"}),"instanceName":"1"}),"instanceName":"1"}),"instanceName":"1"});
            var Q136;
            Q136=makeQuery(id+"F9.opPattern","COPY",BODY,{"derivedFrom":makeQuery(id+"F8.opPattern","COPY",BODY,{"derivedFrom":makeQuery(id+"F7.opPattern","COPY",BODY,{"derivedFrom":makeQuery(id+"F4.opPattern","COPY",BODY,{"derivedFrom":makeQuery(id+"F3.opPattern","COPY",BODY,{"derivedFrom":makeQuery(id+"F2.opPattern","COPY",BODY,{"derivedFrom":makeQuery(id+"F1.opExtrude","SWEPT_BODY",BODY,{"disambiguationData":[OSD([sQuery(id+"F0.wireOp",EDGE,"E2.bottom"),sQuery(id+"F0.wireOp",EDGE,"E2.top"),sQuery(id+"F0.wireOp",EDGE,"E2.left"),sQuery(id+"F0.wireOp",EDGE,"E2.right")])]}),"instanceName":"1"}),"instanceName":"1"}),"instanceName":"1"}),"instanceName":"1"}),"instanceName":"1"}),"instanceName":"1"});
            var Q137;
            Q137=makeQuery(id+"F9.opPattern","COPY",BODY,{"derivedFrom":makeQuery(id+"F8.opPattern","COPY",BODY,{"derivedFrom":makeQuery(id+"F7.opPattern","COPY",BODY,{"derivedFrom":makeQuery(id+"F5.opPattern","COPY",BODY,{"derivedFrom":makeQuery(id+"F4.opPattern","COPY",BODY,{"derivedFrom":makeQuery(id+"F3.opPattern","COPY",BODY,{"derivedFrom":makeQuery(id+"F2.opPattern","COPY",BODY,{"derivedFrom":makeQuery(id+"F1.opExtrude","SWEPT_BODY",BODY,{"disambiguationData":[OSD([sQuery(id+"F0.wireOp",EDGE,"E0.bottom"),sQuery(id+"F0.wireOp",EDGE,"E0.top"),sQuery(id+"F0.wireOp",EDGE,"E0.left"),sQuery(id+"F0.wireOp",EDGE,"E0.right")])]}),"instanceName":"1"}),"instanceName":"1"}),"instanceName":"1"}),"instanceName":"1"}),"instanceName":"1"}),"instanceName":"1"}),"instanceName":"1"});
            var Q138;
            Q138=makeQuery(id+"F9.opPattern","COPY",BODY,{"derivedFrom":makeQuery(id+"F8.opPattern","COPY",BODY,{"derivedFrom":makeQuery(id+"F7.opPattern","COPY",BODY,{"derivedFrom":makeQuery(id+"F5.opPattern","COPY",BODY,{"derivedFrom":makeQuery(id+"F4.opPattern","COPY",BODY,{"derivedFrom":makeQuery(id+"F3.opPattern","COPY",BODY,{"derivedFrom":makeQuery(id+"F2.opPattern","COPY",BODY,{"derivedFrom":makeQuery(id+"F1.opExtrude","SWEPT_BODY",BODY,{"disambiguationData":[OSD([sQuery(id+"F0.wireOp",EDGE,"E1.bottom"),sQuery(id+"F0.wireOp",EDGE,"E1.top"),sQuery(id+"F0.wireOp",EDGE,"E1.left"),sQuery(id+"F0.wireOp",EDGE,"E1.right")])]}),"instanceName":"1"}),"instanceName":"1"}),"instanceName":"1"}),"instanceName":"1"}),"instanceName":"1"}),"instanceName":"1"}),"instanceName":"1"});
            var Q139;
            Q139=makeQuery(id+"F9.opPattern","COPY",BODY,{"derivedFrom":makeQuery(id+"F8.opPattern","COPY",BODY,{"derivedFrom":makeQuery(id+"F7.opPattern","COPY",BODY,{"derivedFrom":makeQuery(id+"F5.opPattern","COPY",BODY,{"derivedFrom":makeQuery(id+"F4.opPattern","COPY",BODY,{"derivedFrom":makeQuery(id+"F3.opPattern","COPY",BODY,{"derivedFrom":makeQuery(id+"F2.opPattern","COPY",BODY,{"derivedFrom":makeQuery(id+"F1.opExtrude","SWEPT_BODY",BODY,{"disambiguationData":[OSD([sQuery(id+"F0.wireOp",EDGE,"E2.bottom"),sQuery(id+"F0.wireOp",EDGE,"E2.top"),sQuery(id+"F0.wireOp",EDGE,"E2.left"),sQuery(id+"F0.wireOp",EDGE,"E2.right")])]}),"instanceName":"1"}),"instanceName":"1"}),"instanceName":"1"}),"instanceName":"1"}),"instanceName":"1"}),"instanceName":"1"}),"instanceName":"1"});
            var Q140;
            Q140=makeQuery(id+"F9.opPattern","COPY",BODY,{"derivedFrom":makeQuery(id+"F8.opPattern","COPY",BODY,{"derivedFrom":makeQuery(id+"F7.opPattern","COPY",BODY,{"derivedFrom":makeQuery(id+"F6.opPattern","COPY",BODY,{"derivedFrom":makeQuery(id+"F5.opPattern","COPY",BODY,{"derivedFrom":makeQuery(id+"F4.opPattern","COPY",BODY,{"derivedFrom":makeQuery(id+"F3.opPattern","COPY",BODY,{"derivedFrom":makeQuery(id+"F2.opPattern","COPY",BODY,{"derivedFrom":makeQuery(id+"F1.opExtrude","SWEPT_BODY",BODY,{"disambiguationData":[OSD([sQuery(id+"F0.wireOp",EDGE,"E0.bottom"),sQuery(id+"F0.wireOp",EDGE,"E0.top"),sQuery(id+"F0.wireOp",EDGE,"E0.left"),sQuery(id+"F0.wireOp",EDGE,"E0.right")])]}),"instanceName":"1"}),"instanceName":"1"}),"instanceName":"1"}),"instanceName":"1"}),"instanceName":"1"}),"instanceName":"1"}),"instanceName":"1"}),"instanceName":"1"});
            var Q141;
            Q141=makeQuery(id+"F9.opPattern","COPY",BODY,{"derivedFrom":makeQuery(id+"F8.opPattern","COPY",BODY,{"derivedFrom":makeQuery(id+"F7.opPattern","COPY",BODY,{"derivedFrom":makeQuery(id+"F6.opPattern","COPY",BODY,{"derivedFrom":makeQuery(id+"F5.opPattern","COPY",BODY,{"derivedFrom":makeQuery(id+"F4.opPattern","COPY",BODY,{"derivedFrom":makeQuery(id+"F3.opPattern","COPY",BODY,{"derivedFrom":makeQuery(id+"F2.opPattern","COPY",BODY,{"derivedFrom":makeQuery(id+"F1.opExtrude","SWEPT_BODY",BODY,{"disambiguationData":[OSD([sQuery(id+"F0.wireOp",EDGE,"E1.bottom"),sQuery(id+"F0.wireOp",EDGE,"E1.top"),sQuery(id+"F0.wireOp",EDGE,"E1.left"),sQuery(id+"F0.wireOp",EDGE,"E1.right")])]}),"instanceName":"1"}),"instanceName":"1"}),"instanceName":"1"}),"instanceName":"1"}),"instanceName":"1"}),"instanceName":"1"}),"instanceName":"1"}),"instanceName":"1"});
            var Q142;
            Q142=makeQuery(id+"F9.opPattern","COPY",BODY,{"derivedFrom":makeQuery(id+"F8.opPattern","COPY",BODY,{"derivedFrom":makeQuery(id+"F7.opPattern","COPY",BODY,{"derivedFrom":makeQuery(id+"F6.opPattern","COPY",BODY,{"derivedFrom":makeQuery(id+"F5.opPattern","COPY",BODY,{"derivedFrom":makeQuery(id+"F4.opPattern","COPY",BODY,{"derivedFrom":makeQuery(id+"F3.opPattern","COPY",BODY,{"derivedFrom":makeQuery(id+"F2.opPattern","COPY",BODY,{"derivedFrom":makeQuery(id+"F1.opExtrude","SWEPT_BODY",BODY,{"disambiguationData":[OSD([sQuery(id+"F0.wireOp",EDGE,"E2.bottom"),sQuery(id+"F0.wireOp",EDGE,"E2.top"),sQuery(id+"F0.wireOp",EDGE,"E2.left"),sQuery(id+"F0.wireOp",EDGE,"E2.right")])]}),"instanceName":"1"}),"instanceName":"1"}),"instanceName":"1"}),"instanceName":"1"}),"instanceName":"1"}),"instanceName":"1"}),"instanceName":"1"}),"instanceName":"1"});
            var Q143;
            Q143=makeQuery(id+"F10.opPattern","COPY",BODY,{"derivedFrom":makeQuery(id+"F1.opExtrude","SWEPT_BODY",BODY,{"disambiguationData":[OSD([sQuery(id+"F0.wireOp",EDGE,"E0.bottom"),sQuery(id+"F0.wireOp",EDGE,"E0.top"),sQuery(id+"F0.wireOp",EDGE,"E0.left"),sQuery(id+"F0.wireOp",EDGE,"E0.right")])]}),"instanceName":"1"});
            var Q144;
            Q144=makeQuery(id+"F10.opPattern","COPY",BODY,{"derivedFrom":makeQuery(id+"F1.opExtrude","SWEPT_BODY",BODY,{"disambiguationData":[OSD([sQuery(id+"F0.wireOp",EDGE,"E1.bottom"),sQuery(id+"F0.wireOp",EDGE,"E1.top"),sQuery(id+"F0.wireOp",EDGE,"E1.left"),sQuery(id+"F0.wireOp",EDGE,"E1.right")])]}),"instanceName":"1"});
            var Q145;
            Q145=makeQuery(id+"F10.opPattern","COPY",BODY,{"derivedFrom":makeQuery(id+"F1.opExtrude","SWEPT_BODY",BODY,{"disambiguationData":[OSD([sQuery(id+"F0.wireOp",EDGE,"E2.bottom"),sQuery(id+"F0.wireOp",EDGE,"E2.top"),sQuery(id+"F0.wireOp",EDGE,"E2.left"),sQuery(id+"F0.wireOp",EDGE,"E2.right")])]}),"instanceName":"1"});
            var Q146;
            Q146=makeQuery(id+"F10.opPattern","COPY",BODY,{"derivedFrom":makeQuery(id+"F2.opPattern","COPY",BODY,{"derivedFrom":makeQuery(id+"F1.opExtrude","SWEPT_BODY",BODY,{"disambiguationData":[OSD([sQuery(id+"F0.wireOp",EDGE,"E0.bottom"),sQuery(id+"F0.wireOp",EDGE,"E0.top"),sQuery(id+"F0.wireOp",EDGE,"E0.left"),sQuery(id+"F0.wireOp",EDGE,"E0.right")])]}),"instanceName":"1"}),"instanceName":"1"});
            var Q147;
            Q147=makeQuery(id+"F10.opPattern","COPY",BODY,{"derivedFrom":makeQuery(id+"F2.opPattern","COPY",BODY,{"derivedFrom":makeQuery(id+"F1.opExtrude","SWEPT_BODY",BODY,{"disambiguationData":[OSD([sQuery(id+"F0.wireOp",EDGE,"E1.bottom"),sQuery(id+"F0.wireOp",EDGE,"E1.top"),sQuery(id+"F0.wireOp",EDGE,"E1.left"),sQuery(id+"F0.wireOp",EDGE,"E1.right")])]}),"instanceName":"1"}),"instanceName":"1"});
            var Q148;
            Q148=makeQuery(id+"F10.opPattern","COPY",BODY,{"derivedFrom":makeQuery(id+"F2.opPattern","COPY",BODY,{"derivedFrom":makeQuery(id+"F1.opExtrude","SWEPT_BODY",BODY,{"disambiguationData":[OSD([sQuery(id+"F0.wireOp",EDGE,"E2.bottom"),sQuery(id+"F0.wireOp",EDGE,"E2.top"),sQuery(id+"F0.wireOp",EDGE,"E2.left"),sQuery(id+"F0.wireOp",EDGE,"E2.right")])]}),"instanceName":"1"}),"instanceName":"1"});
            var Q149;
            Q149=makeQuery(id+"F10.opPattern","COPY",BODY,{"derivedFrom":makeQuery(id+"F3.opPattern","COPY",BODY,{"derivedFrom":makeQuery(id+"F2.opPattern","COPY",BODY,{"derivedFrom":makeQuery(id+"F1.opExtrude","SWEPT_BODY",BODY,{"disambiguationData":[OSD([sQuery(id+"F0.wireOp",EDGE,"E0.bottom"),sQuery(id+"F0.wireOp",EDGE,"E0.top"),sQuery(id+"F0.wireOp",EDGE,"E0.left"),sQuery(id+"F0.wireOp",EDGE,"E0.right")])]}),"instanceName":"1"}),"instanceName":"1"}),"instanceName":"1"});
            var Q150;
            Q150=makeQuery(id+"F10.opPattern","COPY",BODY,{"derivedFrom":makeQuery(id+"F3.opPattern","COPY",BODY,{"derivedFrom":makeQuery(id+"F2.opPattern","COPY",BODY,{"derivedFrom":makeQuery(id+"F1.opExtrude","SWEPT_BODY",BODY,{"disambiguationData":[OSD([sQuery(id+"F0.wireOp",EDGE,"E1.bottom"),sQuery(id+"F0.wireOp",EDGE,"E1.top"),sQuery(id+"F0.wireOp",EDGE,"E1.left"),sQuery(id+"F0.wireOp",EDGE,"E1.right")])]}),"instanceName":"1"}),"instanceName":"1"}),"instanceName":"1"});
            var Q151;
            Q151=makeQuery(id+"F10.opPattern","COPY",BODY,{"derivedFrom":makeQuery(id+"F3.opPattern","COPY",BODY,{"derivedFrom":makeQuery(id+"F2.opPattern","COPY",BODY,{"derivedFrom":makeQuery(id+"F1.opExtrude","SWEPT_BODY",BODY,{"disambiguationData":[OSD([sQuery(id+"F0.wireOp",EDGE,"E2.bottom"),sQuery(id+"F0.wireOp",EDGE,"E2.top"),sQuery(id+"F0.wireOp",EDGE,"E2.left"),sQuery(id+"F0.wireOp",EDGE,"E2.right")])]}),"instanceName":"1"}),"instanceName":"1"}),"instanceName":"1"});
            var Q152;
            Q152=makeQuery(id+"F10.opPattern","COPY",BODY,{"derivedFrom":makeQuery(id+"F4.opPattern","COPY",BODY,{"derivedFrom":makeQuery(id+"F3.opPattern","COPY",BODY,{"derivedFrom":makeQuery(id+"F2.opPattern","COPY",BODY,{"derivedFrom":makeQuery(id+"F1.opExtrude","SWEPT_BODY",BODY,{"disambiguationData":[OSD([sQuery(id+"F0.wireOp",EDGE,"E0.bottom"),sQuery(id+"F0.wireOp",EDGE,"E0.top"),sQuery(id+"F0.wireOp",EDGE,"E0.left"),sQuery(id+"F0.wireOp",EDGE,"E0.right")])]}),"instanceName":"1"}),"instanceName":"1"}),"instanceName":"1"}),"instanceName":"1"});
            var Q153;
            Q153=makeQuery(id+"F10.opPattern","COPY",BODY,{"derivedFrom":makeQuery(id+"F4.opPattern","COPY",BODY,{"derivedFrom":makeQuery(id+"F3.opPattern","COPY",BODY,{"derivedFrom":makeQuery(id+"F2.opPattern","COPY",BODY,{"derivedFrom":makeQuery(id+"F1.opExtrude","SWEPT_BODY",BODY,{"disambiguationData":[OSD([sQuery(id+"F0.wireOp",EDGE,"E1.bottom"),sQuery(id+"F0.wireOp",EDGE,"E1.top"),sQuery(id+"F0.wireOp",EDGE,"E1.left"),sQuery(id+"F0.wireOp",EDGE,"E1.right")])]}),"instanceName":"1"}),"instanceName":"1"}),"instanceName":"1"}),"instanceName":"1"});
            var Q154;
            Q154=makeQuery(id+"F10.opPattern","COPY",BODY,{"derivedFrom":makeQuery(id+"F4.opPattern","COPY",BODY,{"derivedFrom":makeQuery(id+"F3.opPattern","COPY",BODY,{"derivedFrom":makeQuery(id+"F2.opPattern","COPY",BODY,{"derivedFrom":makeQuery(id+"F1.opExtrude","SWEPT_BODY",BODY,{"disambiguationData":[OSD([sQuery(id+"F0.wireOp",EDGE,"E2.bottom"),sQuery(id+"F0.wireOp",EDGE,"E2.top"),sQuery(id+"F0.wireOp",EDGE,"E2.left"),sQuery(id+"F0.wireOp",EDGE,"E2.right")])]}),"instanceName":"1"}),"instanceName":"1"}),"instanceName":"1"}),"instanceName":"1"});
            var Q155;
            Q155=makeQuery(id+"F10.opPattern","COPY",BODY,{"derivedFrom":makeQuery(id+"F5.opPattern","COPY",BODY,{"derivedFrom":makeQuery(id+"F4.opPattern","COPY",BODY,{"derivedFrom":makeQuery(id+"F3.opPattern","COPY",BODY,{"derivedFrom":makeQuery(id+"F2.opPattern","COPY",BODY,{"derivedFrom":makeQuery(id+"F1.opExtrude","SWEPT_BODY",BODY,{"disambiguationData":[OSD([sQuery(id+"F0.wireOp",EDGE,"E0.bottom"),sQuery(id+"F0.wireOp",EDGE,"E0.top"),sQuery(id+"F0.wireOp",EDGE,"E0.left"),sQuery(id+"F0.wireOp",EDGE,"E0.right")])]}),"instanceName":"1"}),"instanceName":"1"}),"instanceName":"1"}),"instanceName":"1"}),"instanceName":"1"});
            var Q156;
            Q156=makeQuery(id+"F10.opPattern","COPY",BODY,{"derivedFrom":makeQuery(id+"F5.opPattern","COPY",BODY,{"derivedFrom":makeQuery(id+"F4.opPattern","COPY",BODY,{"derivedFrom":makeQuery(id+"F3.opPattern","COPY",BODY,{"derivedFrom":makeQuery(id+"F2.opPattern","COPY",BODY,{"derivedFrom":makeQuery(id+"F1.opExtrude","SWEPT_BODY",BODY,{"disambiguationData":[OSD([sQuery(id+"F0.wireOp",EDGE,"E1.bottom"),sQuery(id+"F0.wireOp",EDGE,"E1.top"),sQuery(id+"F0.wireOp",EDGE,"E1.left"),sQuery(id+"F0.wireOp",EDGE,"E1.right")])]}),"instanceName":"1"}),"instanceName":"1"}),"instanceName":"1"}),"instanceName":"1"}),"instanceName":"1"});
            var Q157;
            Q157=makeQuery(id+"F10.opPattern","COPY",BODY,{"derivedFrom":makeQuery(id+"F5.opPattern","COPY",BODY,{"derivedFrom":makeQuery(id+"F4.opPattern","COPY",BODY,{"derivedFrom":makeQuery(id+"F3.opPattern","COPY",BODY,{"derivedFrom":makeQuery(id+"F2.opPattern","COPY",BODY,{"derivedFrom":makeQuery(id+"F1.opExtrude","SWEPT_BODY",BODY,{"disambiguationData":[OSD([sQuery(id+"F0.wireOp",EDGE,"E2.bottom"),sQuery(id+"F0.wireOp",EDGE,"E2.top"),sQuery(id+"F0.wireOp",EDGE,"E2.left"),sQuery(id+"F0.wireOp",EDGE,"E2.right")])]}),"instanceName":"1"}),"instanceName":"1"}),"instanceName":"1"}),"instanceName":"1"}),"instanceName":"1"});
            var Q158;
            Q158=makeQuery(id+"F10.opPattern","COPY",BODY,{"derivedFrom":makeQuery(id+"F6.opPattern","COPY",BODY,{"derivedFrom":makeQuery(id+"F5.opPattern","COPY",BODY,{"derivedFrom":makeQuery(id+"F4.opPattern","COPY",BODY,{"derivedFrom":makeQuery(id+"F3.opPattern","COPY",BODY,{"derivedFrom":makeQuery(id+"F2.opPattern","COPY",BODY,{"derivedFrom":makeQuery(id+"F1.opExtrude","SWEPT_BODY",BODY,{"disambiguationData":[OSD([sQuery(id+"F0.wireOp",EDGE,"E0.bottom"),sQuery(id+"F0.wireOp",EDGE,"E0.top"),sQuery(id+"F0.wireOp",EDGE,"E0.left"),sQuery(id+"F0.wireOp",EDGE,"E0.right")])]}),"instanceName":"1"}),"instanceName":"1"}),"instanceName":"1"}),"instanceName":"1"}),"instanceName":"1"}),"instanceName":"1"});
            var Q159;
            Q159=makeQuery(id+"F10.opPattern","COPY",BODY,{"derivedFrom":makeQuery(id+"F6.opPattern","COPY",BODY,{"derivedFrom":makeQuery(id+"F5.opPattern","COPY",BODY,{"derivedFrom":makeQuery(id+"F4.opPattern","COPY",BODY,{"derivedFrom":makeQuery(id+"F3.opPattern","COPY",BODY,{"derivedFrom":makeQuery(id+"F2.opPattern","COPY",BODY,{"derivedFrom":makeQuery(id+"F1.opExtrude","SWEPT_BODY",BODY,{"disambiguationData":[OSD([sQuery(id+"F0.wireOp",EDGE,"E1.bottom"),sQuery(id+"F0.wireOp",EDGE,"E1.top"),sQuery(id+"F0.wireOp",EDGE,"E1.left"),sQuery(id+"F0.wireOp",EDGE,"E1.right")])]}),"instanceName":"1"}),"instanceName":"1"}),"instanceName":"1"}),"instanceName":"1"}),"instanceName":"1"}),"instanceName":"1"});
            var Q160;
            Q160=makeQuery(id+"F10.opPattern","COPY",BODY,{"derivedFrom":makeQuery(id+"F6.opPattern","COPY",BODY,{"derivedFrom":makeQuery(id+"F5.opPattern","COPY",BODY,{"derivedFrom":makeQuery(id+"F4.opPattern","COPY",BODY,{"derivedFrom":makeQuery(id+"F3.opPattern","COPY",BODY,{"derivedFrom":makeQuery(id+"F2.opPattern","COPY",BODY,{"derivedFrom":makeQuery(id+"F1.opExtrude","SWEPT_BODY",BODY,{"disambiguationData":[OSD([sQuery(id+"F0.wireOp",EDGE,"E2.bottom"),sQuery(id+"F0.wireOp",EDGE,"E2.top"),sQuery(id+"F0.wireOp",EDGE,"E2.left"),sQuery(id+"F0.wireOp",EDGE,"E2.right")])]}),"instanceName":"1"}),"instanceName":"1"}),"instanceName":"1"}),"instanceName":"1"}),"instanceName":"1"}),"instanceName":"1"});
            var Q161;
            Q161=makeQuery(id+"F10.opPattern","COPY",BODY,{"derivedFrom":makeQuery(id+"F7.opPattern","COPY",BODY,{"derivedFrom":makeQuery(id+"F1.opExtrude","SWEPT_BODY",BODY,{"disambiguationData":[OSD([sQuery(id+"F0.wireOp",EDGE,"E0.bottom"),sQuery(id+"F0.wireOp",EDGE,"E0.top"),sQuery(id+"F0.wireOp",EDGE,"E0.left"),sQuery(id+"F0.wireOp",EDGE,"E0.right")])]}),"instanceName":"1"}),"instanceName":"1"});
            var Q162;
            Q162=makeQuery(id+"F10.opPattern","COPY",BODY,{"derivedFrom":makeQuery(id+"F7.opPattern","COPY",BODY,{"derivedFrom":makeQuery(id+"F1.opExtrude","SWEPT_BODY",BODY,{"disambiguationData":[OSD([sQuery(id+"F0.wireOp",EDGE,"E1.bottom"),sQuery(id+"F0.wireOp",EDGE,"E1.top"),sQuery(id+"F0.wireOp",EDGE,"E1.left"),sQuery(id+"F0.wireOp",EDGE,"E1.right")])]}),"instanceName":"1"}),"instanceName":"1"});
            var Q163;
            Q163=makeQuery(id+"F10.opPattern","COPY",BODY,{"derivedFrom":makeQuery(id+"F7.opPattern","COPY",BODY,{"derivedFrom":makeQuery(id+"F1.opExtrude","SWEPT_BODY",BODY,{"disambiguationData":[OSD([sQuery(id+"F0.wireOp",EDGE,"E2.bottom"),sQuery(id+"F0.wireOp",EDGE,"E2.top"),sQuery(id+"F0.wireOp",EDGE,"E2.left"),sQuery(id+"F0.wireOp",EDGE,"E2.right")])]}),"instanceName":"1"}),"instanceName":"1"});
            var Q164;
            Q164=makeQuery(id+"F10.opPattern","COPY",BODY,{"derivedFrom":makeQuery(id+"F7.opPattern","COPY",BODY,{"derivedFrom":makeQuery(id+"F2.opPattern","COPY",BODY,{"derivedFrom":makeQuery(id+"F1.opExtrude","SWEPT_BODY",BODY,{"disambiguationData":[OSD([sQuery(id+"F0.wireOp",EDGE,"E0.bottom"),sQuery(id+"F0.wireOp",EDGE,"E0.top"),sQuery(id+"F0.wireOp",EDGE,"E0.left"),sQuery(id+"F0.wireOp",EDGE,"E0.right")])]}),"instanceName":"1"}),"instanceName":"1"}),"instanceName":"1"});
            var Q165;
            Q165=makeQuery(id+"F10.opPattern","COPY",BODY,{"derivedFrom":makeQuery(id+"F7.opPattern","COPY",BODY,{"derivedFrom":makeQuery(id+"F2.opPattern","COPY",BODY,{"derivedFrom":makeQuery(id+"F1.opExtrude","SWEPT_BODY",BODY,{"disambiguationData":[OSD([sQuery(id+"F0.wireOp",EDGE,"E1.bottom"),sQuery(id+"F0.wireOp",EDGE,"E1.top"),sQuery(id+"F0.wireOp",EDGE,"E1.left"),sQuery(id+"F0.wireOp",EDGE,"E1.right")])]}),"instanceName":"1"}),"instanceName":"1"}),"instanceName":"1"});
            var Q166;
            Q166=makeQuery(id+"F10.opPattern","COPY",BODY,{"derivedFrom":makeQuery(id+"F7.opPattern","COPY",BODY,{"derivedFrom":makeQuery(id+"F2.opPattern","COPY",BODY,{"derivedFrom":makeQuery(id+"F1.opExtrude","SWEPT_BODY",BODY,{"disambiguationData":[OSD([sQuery(id+"F0.wireOp",EDGE,"E2.bottom"),sQuery(id+"F0.wireOp",EDGE,"E2.top"),sQuery(id+"F0.wireOp",EDGE,"E2.left"),sQuery(id+"F0.wireOp",EDGE,"E2.right")])]}),"instanceName":"1"}),"instanceName":"1"}),"instanceName":"1"});
            var Q167;
            Q167=makeQuery(id+"F10.opPattern","COPY",BODY,{"derivedFrom":makeQuery(id+"F7.opPattern","COPY",BODY,{"derivedFrom":makeQuery(id+"F3.opPattern","COPY",BODY,{"derivedFrom":makeQuery(id+"F2.opPattern","COPY",BODY,{"derivedFrom":makeQuery(id+"F1.opExtrude","SWEPT_BODY",BODY,{"disambiguationData":[OSD([sQuery(id+"F0.wireOp",EDGE,"E0.bottom"),sQuery(id+"F0.wireOp",EDGE,"E0.top"),sQuery(id+"F0.wireOp",EDGE,"E0.left"),sQuery(id+"F0.wireOp",EDGE,"E0.right")])]}),"instanceName":"1"}),"instanceName":"1"}),"instanceName":"1"}),"instanceName":"1"});
            var Q168;
            Q168=makeQuery(id+"F10.opPattern","COPY",BODY,{"derivedFrom":makeQuery(id+"F7.opPattern","COPY",BODY,{"derivedFrom":makeQuery(id+"F3.opPattern","COPY",BODY,{"derivedFrom":makeQuery(id+"F2.opPattern","COPY",BODY,{"derivedFrom":makeQuery(id+"F1.opExtrude","SWEPT_BODY",BODY,{"disambiguationData":[OSD([sQuery(id+"F0.wireOp",EDGE,"E1.bottom"),sQuery(id+"F0.wireOp",EDGE,"E1.top"),sQuery(id+"F0.wireOp",EDGE,"E1.left"),sQuery(id+"F0.wireOp",EDGE,"E1.right")])]}),"instanceName":"1"}),"instanceName":"1"}),"instanceName":"1"}),"instanceName":"1"});
            var Q169;
            Q169=makeQuery(id+"F10.opPattern","COPY",BODY,{"derivedFrom":makeQuery(id+"F7.opPattern","COPY",BODY,{"derivedFrom":makeQuery(id+"F3.opPattern","COPY",BODY,{"derivedFrom":makeQuery(id+"F2.opPattern","COPY",BODY,{"derivedFrom":makeQuery(id+"F1.opExtrude","SWEPT_BODY",BODY,{"disambiguationData":[OSD([sQuery(id+"F0.wireOp",EDGE,"E2.bottom"),sQuery(id+"F0.wireOp",EDGE,"E2.top"),sQuery(id+"F0.wireOp",EDGE,"E2.left"),sQuery(id+"F0.wireOp",EDGE,"E2.right")])]}),"instanceName":"1"}),"instanceName":"1"}),"instanceName":"1"}),"instanceName":"1"});
            var Q170;
            Q170=makeQuery(id+"F10.opPattern","COPY",BODY,{"derivedFrom":makeQuery(id+"F7.opPattern","COPY",BODY,{"derivedFrom":makeQuery(id+"F4.opPattern","COPY",BODY,{"derivedFrom":makeQuery(id+"F3.opPattern","COPY",BODY,{"derivedFrom":makeQuery(id+"F2.opPattern","COPY",BODY,{"derivedFrom":makeQuery(id+"F1.opExtrude","SWEPT_BODY",BODY,{"disambiguationData":[OSD([sQuery(id+"F0.wireOp",EDGE,"E0.bottom"),sQuery(id+"F0.wireOp",EDGE,"E0.top"),sQuery(id+"F0.wireOp",EDGE,"E0.left"),sQuery(id+"F0.wireOp",EDGE,"E0.right")])]}),"instanceName":"1"}),"instanceName":"1"}),"instanceName":"1"}),"instanceName":"1"}),"instanceName":"1"});
            var Q171;
            Q171=makeQuery(id+"F10.opPattern","COPY",BODY,{"derivedFrom":makeQuery(id+"F7.opPattern","COPY",BODY,{"derivedFrom":makeQuery(id+"F4.opPattern","COPY",BODY,{"derivedFrom":makeQuery(id+"F3.opPattern","COPY",BODY,{"derivedFrom":makeQuery(id+"F2.opPattern","COPY",BODY,{"derivedFrom":makeQuery(id+"F1.opExtrude","SWEPT_BODY",BODY,{"disambiguationData":[OSD([sQuery(id+"F0.wireOp",EDGE,"E1.bottom"),sQuery(id+"F0.wireOp",EDGE,"E1.top"),sQuery(id+"F0.wireOp",EDGE,"E1.left"),sQuery(id+"F0.wireOp",EDGE,"E1.right")])]}),"instanceName":"1"}),"instanceName":"1"}),"instanceName":"1"}),"instanceName":"1"}),"instanceName":"1"});
            var Q172;
            Q172=makeQuery(id+"F10.opPattern","COPY",BODY,{"derivedFrom":makeQuery(id+"F7.opPattern","COPY",BODY,{"derivedFrom":makeQuery(id+"F4.opPattern","COPY",BODY,{"derivedFrom":makeQuery(id+"F3.opPattern","COPY",BODY,{"derivedFrom":makeQuery(id+"F2.opPattern","COPY",BODY,{"derivedFrom":makeQuery(id+"F1.opExtrude","SWEPT_BODY",BODY,{"disambiguationData":[OSD([sQuery(id+"F0.wireOp",EDGE,"E2.bottom"),sQuery(id+"F0.wireOp",EDGE,"E2.top"),sQuery(id+"F0.wireOp",EDGE,"E2.left"),sQuery(id+"F0.wireOp",EDGE,"E2.right")])]}),"instanceName":"1"}),"instanceName":"1"}),"instanceName":"1"}),"instanceName":"1"}),"instanceName":"1"});
            var Q173;
            Q173=makeQuery(id+"F10.opPattern","COPY",BODY,{"derivedFrom":makeQuery(id+"F7.opPattern","COPY",BODY,{"derivedFrom":makeQuery(id+"F5.opPattern","COPY",BODY,{"derivedFrom":makeQuery(id+"F4.opPattern","COPY",BODY,{"derivedFrom":makeQuery(id+"F3.opPattern","COPY",BODY,{"derivedFrom":makeQuery(id+"F2.opPattern","COPY",BODY,{"derivedFrom":makeQuery(id+"F1.opExtrude","SWEPT_BODY",BODY,{"disambiguationData":[OSD([sQuery(id+"F0.wireOp",EDGE,"E0.bottom"),sQuery(id+"F0.wireOp",EDGE,"E0.top"),sQuery(id+"F0.wireOp",EDGE,"E0.left"),sQuery(id+"F0.wireOp",EDGE,"E0.right")])]}),"instanceName":"1"}),"instanceName":"1"}),"instanceName":"1"}),"instanceName":"1"}),"instanceName":"1"}),"instanceName":"1"});
            var Q174;
            Q174=makeQuery(id+"F10.opPattern","COPY",BODY,{"derivedFrom":makeQuery(id+"F7.opPattern","COPY",BODY,{"derivedFrom":makeQuery(id+"F5.opPattern","COPY",BODY,{"derivedFrom":makeQuery(id+"F4.opPattern","COPY",BODY,{"derivedFrom":makeQuery(id+"F3.opPattern","COPY",BODY,{"derivedFrom":makeQuery(id+"F2.opPattern","COPY",BODY,{"derivedFrom":makeQuery(id+"F1.opExtrude","SWEPT_BODY",BODY,{"disambiguationData":[OSD([sQuery(id+"F0.wireOp",EDGE,"E1.bottom"),sQuery(id+"F0.wireOp",EDGE,"E1.top"),sQuery(id+"F0.wireOp",EDGE,"E1.left"),sQuery(id+"F0.wireOp",EDGE,"E1.right")])]}),"instanceName":"1"}),"instanceName":"1"}),"instanceName":"1"}),"instanceName":"1"}),"instanceName":"1"}),"instanceName":"1"});
            var Q175;
            Q175=makeQuery(id+"F10.opPattern","COPY",BODY,{"derivedFrom":makeQuery(id+"F7.opPattern","COPY",BODY,{"derivedFrom":makeQuery(id+"F5.opPattern","COPY",BODY,{"derivedFrom":makeQuery(id+"F4.opPattern","COPY",BODY,{"derivedFrom":makeQuery(id+"F3.opPattern","COPY",BODY,{"derivedFrom":makeQuery(id+"F2.opPattern","COPY",BODY,{"derivedFrom":makeQuery(id+"F1.opExtrude","SWEPT_BODY",BODY,{"disambiguationData":[OSD([sQuery(id+"F0.wireOp",EDGE,"E2.bottom"),sQuery(id+"F0.wireOp",EDGE,"E2.top"),sQuery(id+"F0.wireOp",EDGE,"E2.left"),sQuery(id+"F0.wireOp",EDGE,"E2.right")])]}),"instanceName":"1"}),"instanceName":"1"}),"instanceName":"1"}),"instanceName":"1"}),"instanceName":"1"}),"instanceName":"1"});
            var Q176;
            Q176=makeQuery(id+"F10.opPattern","COPY",BODY,{"derivedFrom":makeQuery(id+"F7.opPattern","COPY",BODY,{"derivedFrom":makeQuery(id+"F6.opPattern","COPY",BODY,{"derivedFrom":makeQuery(id+"F5.opPattern","COPY",BODY,{"derivedFrom":makeQuery(id+"F4.opPattern","COPY",BODY,{"derivedFrom":makeQuery(id+"F3.opPattern","COPY",BODY,{"derivedFrom":makeQuery(id+"F2.opPattern","COPY",BODY,{"derivedFrom":makeQuery(id+"F1.opExtrude","SWEPT_BODY",BODY,{"disambiguationData":[OSD([sQuery(id+"F0.wireOp",EDGE,"E0.bottom"),sQuery(id+"F0.wireOp",EDGE,"E0.top"),sQuery(id+"F0.wireOp",EDGE,"E0.left"),sQuery(id+"F0.wireOp",EDGE,"E0.right")])]}),"instanceName":"1"}),"instanceName":"1"}),"instanceName":"1"}),"instanceName":"1"}),"instanceName":"1"}),"instanceName":"1"}),"instanceName":"1"});
            var Q177;
            Q177=makeQuery(id+"F10.opPattern","COPY",BODY,{"derivedFrom":makeQuery(id+"F7.opPattern","COPY",BODY,{"derivedFrom":makeQuery(id+"F6.opPattern","COPY",BODY,{"derivedFrom":makeQuery(id+"F5.opPattern","COPY",BODY,{"derivedFrom":makeQuery(id+"F4.opPattern","COPY",BODY,{"derivedFrom":makeQuery(id+"F3.opPattern","COPY",BODY,{"derivedFrom":makeQuery(id+"F2.opPattern","COPY",BODY,{"derivedFrom":makeQuery(id+"F1.opExtrude","SWEPT_BODY",BODY,{"disambiguationData":[OSD([sQuery(id+"F0.wireOp",EDGE,"E1.bottom"),sQuery(id+"F0.wireOp",EDGE,"E1.top"),sQuery(id+"F0.wireOp",EDGE,"E1.left"),sQuery(id+"F0.wireOp",EDGE,"E1.right")])]}),"instanceName":"1"}),"instanceName":"1"}),"instanceName":"1"}),"instanceName":"1"}),"instanceName":"1"}),"instanceName":"1"}),"instanceName":"1"});
            var Q178;
            Q178=makeQuery(id+"F10.opPattern","COPY",BODY,{"derivedFrom":makeQuery(id+"F7.opPattern","COPY",BODY,{"derivedFrom":makeQuery(id+"F6.opPattern","COPY",BODY,{"derivedFrom":makeQuery(id+"F5.opPattern","COPY",BODY,{"derivedFrom":makeQuery(id+"F4.opPattern","COPY",BODY,{"derivedFrom":makeQuery(id+"F3.opPattern","COPY",BODY,{"derivedFrom":makeQuery(id+"F2.opPattern","COPY",BODY,{"derivedFrom":makeQuery(id+"F1.opExtrude","SWEPT_BODY",BODY,{"disambiguationData":[OSD([sQuery(id+"F0.wireOp",EDGE,"E2.bottom"),sQuery(id+"F0.wireOp",EDGE,"E2.top"),sQuery(id+"F0.wireOp",EDGE,"E2.left"),sQuery(id+"F0.wireOp",EDGE,"E2.right")])]}),"instanceName":"1"}),"instanceName":"1"}),"instanceName":"1"}),"instanceName":"1"}),"instanceName":"1"}),"instanceName":"1"}),"instanceName":"1"});
            var Q179;
            Q179=makeQuery(id+"F10.opPattern","COPY",BODY,{"derivedFrom":makeQuery(id+"F8.opPattern","COPY",BODY,{"derivedFrom":makeQuery(id+"F1.opExtrude","SWEPT_BODY",BODY,{"disambiguationData":[OSD([sQuery(id+"F0.wireOp",EDGE,"E0.bottom"),sQuery(id+"F0.wireOp",EDGE,"E0.top"),sQuery(id+"F0.wireOp",EDGE,"E0.left"),sQuery(id+"F0.wireOp",EDGE,"E0.right")])]}),"instanceName":"1"}),"instanceName":"1"});
            var Q180;
            Q180=makeQuery(id+"F10.opPattern","COPY",BODY,{"derivedFrom":makeQuery(id+"F8.opPattern","COPY",BODY,{"derivedFrom":makeQuery(id+"F1.opExtrude","SWEPT_BODY",BODY,{"disambiguationData":[OSD([sQuery(id+"F0.wireOp",EDGE,"E1.bottom"),sQuery(id+"F0.wireOp",EDGE,"E1.top"),sQuery(id+"F0.wireOp",EDGE,"E1.left"),sQuery(id+"F0.wireOp",EDGE,"E1.right")])]}),"instanceName":"1"}),"instanceName":"1"});
            var Q181;
            Q181=makeQuery(id+"F10.opPattern","COPY",BODY,{"derivedFrom":makeQuery(id+"F8.opPattern","COPY",BODY,{"derivedFrom":makeQuery(id+"F1.opExtrude","SWEPT_BODY",BODY,{"disambiguationData":[OSD([sQuery(id+"F0.wireOp",EDGE,"E2.bottom"),sQuery(id+"F0.wireOp",EDGE,"E2.top"),sQuery(id+"F0.wireOp",EDGE,"E2.left"),sQuery(id+"F0.wireOp",EDGE,"E2.right")])]}),"instanceName":"1"}),"instanceName":"1"});
            var Q182;
            Q182=makeQuery(id+"F10.opPattern","COPY",BODY,{"derivedFrom":makeQuery(id+"F8.opPattern","COPY",BODY,{"derivedFrom":makeQuery(id+"F2.opPattern","COPY",BODY,{"derivedFrom":makeQuery(id+"F1.opExtrude","SWEPT_BODY",BODY,{"disambiguationData":[OSD([sQuery(id+"F0.wireOp",EDGE,"E0.bottom"),sQuery(id+"F0.wireOp",EDGE,"E0.top"),sQuery(id+"F0.wireOp",EDGE,"E0.left"),sQuery(id+"F0.wireOp",EDGE,"E0.right")])]}),"instanceName":"1"}),"instanceName":"1"}),"instanceName":"1"});
            var Q183;
            Q183=makeQuery(id+"F10.opPattern","COPY",BODY,{"derivedFrom":makeQuery(id+"F8.opPattern","COPY",BODY,{"derivedFrom":makeQuery(id+"F2.opPattern","COPY",BODY,{"derivedFrom":makeQuery(id+"F1.opExtrude","SWEPT_BODY",BODY,{"disambiguationData":[OSD([sQuery(id+"F0.wireOp",EDGE,"E1.bottom"),sQuery(id+"F0.wireOp",EDGE,"E1.top"),sQuery(id+"F0.wireOp",EDGE,"E1.left"),sQuery(id+"F0.wireOp",EDGE,"E1.right")])]}),"instanceName":"1"}),"instanceName":"1"}),"instanceName":"1"});
            var Q184;
            Q184=makeQuery(id+"F10.opPattern","COPY",BODY,{"derivedFrom":makeQuery(id+"F8.opPattern","COPY",BODY,{"derivedFrom":makeQuery(id+"F2.opPattern","COPY",BODY,{"derivedFrom":makeQuery(id+"F1.opExtrude","SWEPT_BODY",BODY,{"disambiguationData":[OSD([sQuery(id+"F0.wireOp",EDGE,"E2.bottom"),sQuery(id+"F0.wireOp",EDGE,"E2.top"),sQuery(id+"F0.wireOp",EDGE,"E2.left"),sQuery(id+"F0.wireOp",EDGE,"E2.right")])]}),"instanceName":"1"}),"instanceName":"1"}),"instanceName":"1"});
            var Q185;
            Q185=makeQuery(id+"F10.opPattern","COPY",BODY,{"derivedFrom":makeQuery(id+"F8.opPattern","COPY",BODY,{"derivedFrom":makeQuery(id+"F3.opPattern","COPY",BODY,{"derivedFrom":makeQuery(id+"F2.opPattern","COPY",BODY,{"derivedFrom":makeQuery(id+"F1.opExtrude","SWEPT_BODY",BODY,{"disambiguationData":[OSD([sQuery(id+"F0.wireOp",EDGE,"E0.bottom"),sQuery(id+"F0.wireOp",EDGE,"E0.top"),sQuery(id+"F0.wireOp",EDGE,"E0.left"),sQuery(id+"F0.wireOp",EDGE,"E0.right")])]}),"instanceName":"1"}),"instanceName":"1"}),"instanceName":"1"}),"instanceName":"1"});
            var Q186;
            Q186=makeQuery(id+"F10.opPattern","COPY",BODY,{"derivedFrom":makeQuery(id+"F8.opPattern","COPY",BODY,{"derivedFrom":makeQuery(id+"F3.opPattern","COPY",BODY,{"derivedFrom":makeQuery(id+"F2.opPattern","COPY",BODY,{"derivedFrom":makeQuery(id+"F1.opExtrude","SWEPT_BODY",BODY,{"disambiguationData":[OSD([sQuery(id+"F0.wireOp",EDGE,"E1.bottom"),sQuery(id+"F0.wireOp",EDGE,"E1.top"),sQuery(id+"F0.wireOp",EDGE,"E1.left"),sQuery(id+"F0.wireOp",EDGE,"E1.right")])]}),"instanceName":"1"}),"instanceName":"1"}),"instanceName":"1"}),"instanceName":"1"});
            var Q187;
            Q187=makeQuery(id+"F10.opPattern","COPY",BODY,{"derivedFrom":makeQuery(id+"F8.opPattern","COPY",BODY,{"derivedFrom":makeQuery(id+"F3.opPattern","COPY",BODY,{"derivedFrom":makeQuery(id+"F2.opPattern","COPY",BODY,{"derivedFrom":makeQuery(id+"F1.opExtrude","SWEPT_BODY",BODY,{"disambiguationData":[OSD([sQuery(id+"F0.wireOp",EDGE,"E2.bottom"),sQuery(id+"F0.wireOp",EDGE,"E2.top"),sQuery(id+"F0.wireOp",EDGE,"E2.left"),sQuery(id+"F0.wireOp",EDGE,"E2.right")])]}),"instanceName":"1"}),"instanceName":"1"}),"instanceName":"1"}),"instanceName":"1"});
            var Q188;
            Q188=makeQuery(id+"F10.opPattern","COPY",BODY,{"derivedFrom":makeQuery(id+"F8.opPattern","COPY",BODY,{"derivedFrom":makeQuery(id+"F4.opPattern","COPY",BODY,{"derivedFrom":makeQuery(id+"F3.opPattern","COPY",BODY,{"derivedFrom":makeQuery(id+"F2.opPattern","COPY",BODY,{"derivedFrom":makeQuery(id+"F1.opExtrude","SWEPT_BODY",BODY,{"disambiguationData":[OSD([sQuery(id+"F0.wireOp",EDGE,"E0.bottom"),sQuery(id+"F0.wireOp",EDGE,"E0.top"),sQuery(id+"F0.wireOp",EDGE,"E0.left"),sQuery(id+"F0.wireOp",EDGE,"E0.right")])]}),"instanceName":"1"}),"instanceName":"1"}),"instanceName":"1"}),"instanceName":"1"}),"instanceName":"1"});
            var Q189;
            Q189=makeQuery(id+"F10.opPattern","COPY",BODY,{"derivedFrom":makeQuery(id+"F8.opPattern","COPY",BODY,{"derivedFrom":makeQuery(id+"F4.opPattern","COPY",BODY,{"derivedFrom":makeQuery(id+"F3.opPattern","COPY",BODY,{"derivedFrom":makeQuery(id+"F2.opPattern","COPY",BODY,{"derivedFrom":makeQuery(id+"F1.opExtrude","SWEPT_BODY",BODY,{"disambiguationData":[OSD([sQuery(id+"F0.wireOp",EDGE,"E1.bottom"),sQuery(id+"F0.wireOp",EDGE,"E1.top"),sQuery(id+"F0.wireOp",EDGE,"E1.left"),sQuery(id+"F0.wireOp",EDGE,"E1.right")])]}),"instanceName":"1"}),"instanceName":"1"}),"instanceName":"1"}),"instanceName":"1"}),"instanceName":"1"});
            var Q190;
            Q190=makeQuery(id+"F10.opPattern","COPY",BODY,{"derivedFrom":makeQuery(id+"F8.opPattern","COPY",BODY,{"derivedFrom":makeQuery(id+"F4.opPattern","COPY",BODY,{"derivedFrom":makeQuery(id+"F3.opPattern","COPY",BODY,{"derivedFrom":makeQuery(id+"F2.opPattern","COPY",BODY,{"derivedFrom":makeQuery(id+"F1.opExtrude","SWEPT_BODY",BODY,{"disambiguationData":[OSD([sQuery(id+"F0.wireOp",EDGE,"E2.bottom"),sQuery(id+"F0.wireOp",EDGE,"E2.top"),sQuery(id+"F0.wireOp",EDGE,"E2.left"),sQuery(id+"F0.wireOp",EDGE,"E2.right")])]}),"instanceName":"1"}),"instanceName":"1"}),"instanceName":"1"}),"instanceName":"1"}),"instanceName":"1"});
            var Q191;
            Q191=makeQuery(id+"F10.opPattern","COPY",BODY,{"derivedFrom":makeQuery(id+"F8.opPattern","COPY",BODY,{"derivedFrom":makeQuery(id+"F5.opPattern","COPY",BODY,{"derivedFrom":makeQuery(id+"F4.opPattern","COPY",BODY,{"derivedFrom":makeQuery(id+"F3.opPattern","COPY",BODY,{"derivedFrom":makeQuery(id+"F2.opPattern","COPY",BODY,{"derivedFrom":makeQuery(id+"F1.opExtrude","SWEPT_BODY",BODY,{"disambiguationData":[OSD([sQuery(id+"F0.wireOp",EDGE,"E0.bottom"),sQuery(id+"F0.wireOp",EDGE,"E0.top"),sQuery(id+"F0.wireOp",EDGE,"E0.left"),sQuery(id+"F0.wireOp",EDGE,"E0.right")])]}),"instanceName":"1"}),"instanceName":"1"}),"instanceName":"1"}),"instanceName":"1"}),"instanceName":"1"}),"instanceName":"1"});
            var Q192;
            Q192=makeQuery(id+"F10.opPattern","COPY",BODY,{"derivedFrom":makeQuery(id+"F8.opPattern","COPY",BODY,{"derivedFrom":makeQuery(id+"F5.opPattern","COPY",BODY,{"derivedFrom":makeQuery(id+"F4.opPattern","COPY",BODY,{"derivedFrom":makeQuery(id+"F3.opPattern","COPY",BODY,{"derivedFrom":makeQuery(id+"F2.opPattern","COPY",BODY,{"derivedFrom":makeQuery(id+"F1.opExtrude","SWEPT_BODY",BODY,{"disambiguationData":[OSD([sQuery(id+"F0.wireOp",EDGE,"E1.bottom"),sQuery(id+"F0.wireOp",EDGE,"E1.top"),sQuery(id+"F0.wireOp",EDGE,"E1.left"),sQuery(id+"F0.wireOp",EDGE,"E1.right")])]}),"instanceName":"1"}),"instanceName":"1"}),"instanceName":"1"}),"instanceName":"1"}),"instanceName":"1"}),"instanceName":"1"});
            var Q193;
            Q193=makeQuery(id+"F10.opPattern","COPY",BODY,{"derivedFrom":makeQuery(id+"F8.opPattern","COPY",BODY,{"derivedFrom":makeQuery(id+"F5.opPattern","COPY",BODY,{"derivedFrom":makeQuery(id+"F4.opPattern","COPY",BODY,{"derivedFrom":makeQuery(id+"F3.opPattern","COPY",BODY,{"derivedFrom":makeQuery(id+"F2.opPattern","COPY",BODY,{"derivedFrom":makeQuery(id+"F1.opExtrude","SWEPT_BODY",BODY,{"disambiguationData":[OSD([sQuery(id+"F0.wireOp",EDGE,"E2.bottom"),sQuery(id+"F0.wireOp",EDGE,"E2.top"),sQuery(id+"F0.wireOp",EDGE,"E2.left"),sQuery(id+"F0.wireOp",EDGE,"E2.right")])]}),"instanceName":"1"}),"instanceName":"1"}),"instanceName":"1"}),"instanceName":"1"}),"instanceName":"1"}),"instanceName":"1"});
            var Q194;
            Q194=makeQuery(id+"F10.opPattern","COPY",BODY,{"derivedFrom":makeQuery(id+"F8.opPattern","COPY",BODY,{"derivedFrom":makeQuery(id+"F6.opPattern","COPY",BODY,{"derivedFrom":makeQuery(id+"F5.opPattern","COPY",BODY,{"derivedFrom":makeQuery(id+"F4.opPattern","COPY",BODY,{"derivedFrom":makeQuery(id+"F3.opPattern","COPY",BODY,{"derivedFrom":makeQuery(id+"F2.opPattern","COPY",BODY,{"derivedFrom":makeQuery(id+"F1.opExtrude","SWEPT_BODY",BODY,{"disambiguationData":[OSD([sQuery(id+"F0.wireOp",EDGE,"E0.bottom"),sQuery(id+"F0.wireOp",EDGE,"E0.top"),sQuery(id+"F0.wireOp",EDGE,"E0.left"),sQuery(id+"F0.wireOp",EDGE,"E0.right")])]}),"instanceName":"1"}),"instanceName":"1"}),"instanceName":"1"}),"instanceName":"1"}),"instanceName":"1"}),"instanceName":"1"}),"instanceName":"1"});
            var Q195;
            Q195=makeQuery(id+"F10.opPattern","COPY",BODY,{"derivedFrom":makeQuery(id+"F8.opPattern","COPY",BODY,{"derivedFrom":makeQuery(id+"F6.opPattern","COPY",BODY,{"derivedFrom":makeQuery(id+"F5.opPattern","COPY",BODY,{"derivedFrom":makeQuery(id+"F4.opPattern","COPY",BODY,{"derivedFrom":makeQuery(id+"F3.opPattern","COPY",BODY,{"derivedFrom":makeQuery(id+"F2.opPattern","COPY",BODY,{"derivedFrom":makeQuery(id+"F1.opExtrude","SWEPT_BODY",BODY,{"disambiguationData":[OSD([sQuery(id+"F0.wireOp",EDGE,"E1.bottom"),sQuery(id+"F0.wireOp",EDGE,"E1.top"),sQuery(id+"F0.wireOp",EDGE,"E1.left"),sQuery(id+"F0.wireOp",EDGE,"E1.right")])]}),"instanceName":"1"}),"instanceName":"1"}),"instanceName":"1"}),"instanceName":"1"}),"instanceName":"1"}),"instanceName":"1"}),"instanceName":"1"});
            var Q196;
            Q196=makeQuery(id+"F10.opPattern","COPY",BODY,{"derivedFrom":makeQuery(id+"F8.opPattern","COPY",BODY,{"derivedFrom":makeQuery(id+"F6.opPattern","COPY",BODY,{"derivedFrom":makeQuery(id+"F5.opPattern","COPY",BODY,{"derivedFrom":makeQuery(id+"F4.opPattern","COPY",BODY,{"derivedFrom":makeQuery(id+"F3.opPattern","COPY",BODY,{"derivedFrom":makeQuery(id+"F2.opPattern","COPY",BODY,{"derivedFrom":makeQuery(id+"F1.opExtrude","SWEPT_BODY",BODY,{"disambiguationData":[OSD([sQuery(id+"F0.wireOp",EDGE,"E2.bottom"),sQuery(id+"F0.wireOp",EDGE,"E2.top"),sQuery(id+"F0.wireOp",EDGE,"E2.left"),sQuery(id+"F0.wireOp",EDGE,"E2.right")])]}),"instanceName":"1"}),"instanceName":"1"}),"instanceName":"1"}),"instanceName":"1"}),"instanceName":"1"}),"instanceName":"1"}),"instanceName":"1"});
            var Q197;
            Q197=makeQuery(id+"F10.opPattern","COPY",BODY,{"derivedFrom":makeQuery(id+"F8.opPattern","COPY",BODY,{"derivedFrom":makeQuery(id+"F7.opPattern","COPY",BODY,{"derivedFrom":makeQuery(id+"F1.opExtrude","SWEPT_BODY",BODY,{"disambiguationData":[OSD([sQuery(id+"F0.wireOp",EDGE,"E0.bottom"),sQuery(id+"F0.wireOp",EDGE,"E0.top"),sQuery(id+"F0.wireOp",EDGE,"E0.left"),sQuery(id+"F0.wireOp",EDGE,"E0.right")])]}),"instanceName":"1"}),"instanceName":"1"}),"instanceName":"1"});
            var Q198;
            Q198=makeQuery(id+"F10.opPattern","COPY",BODY,{"derivedFrom":makeQuery(id+"F8.opPattern","COPY",BODY,{"derivedFrom":makeQuery(id+"F7.opPattern","COPY",BODY,{"derivedFrom":makeQuery(id+"F1.opExtrude","SWEPT_BODY",BODY,{"disambiguationData":[OSD([sQuery(id+"F0.wireOp",EDGE,"E1.bottom"),sQuery(id+"F0.wireOp",EDGE,"E1.top"),sQuery(id+"F0.wireOp",EDGE,"E1.left"),sQuery(id+"F0.wireOp",EDGE,"E1.right")])]}),"instanceName":"1"}),"instanceName":"1"}),"instanceName":"1"});
            var Q199;
            Q199=makeQuery(id+"F10.opPattern","COPY",BODY,{"derivedFrom":makeQuery(id+"F8.opPattern","COPY",BODY,{"derivedFrom":makeQuery(id+"F7.opPattern","COPY",BODY,{"derivedFrom":makeQuery(id+"F1.opExtrude","SWEPT_BODY",BODY,{"disambiguationData":[OSD([sQuery(id+"F0.wireOp",EDGE,"E2.bottom"),sQuery(id+"F0.wireOp",EDGE,"E2.top"),sQuery(id+"F0.wireOp",EDGE,"E2.left"),sQuery(id+"F0.wireOp",EDGE,"E2.right")])]}),"instanceName":"1"}),"instanceName":"1"}),"instanceName":"1"});
            var Q200;
            Q200=makeQuery(id+"F10.opPattern","COPY",BODY,{"derivedFrom":makeQuery(id+"F8.opPattern","COPY",BODY,{"derivedFrom":makeQuery(id+"F7.opPattern","COPY",BODY,{"derivedFrom":makeQuery(id+"F2.opPattern","COPY",BODY,{"derivedFrom":makeQuery(id+"F1.opExtrude","SWEPT_BODY",BODY,{"disambiguationData":[OSD([sQuery(id+"F0.wireOp",EDGE,"E0.bottom"),sQuery(id+"F0.wireOp",EDGE,"E0.top"),sQuery(id+"F0.wireOp",EDGE,"E0.left"),sQuery(id+"F0.wireOp",EDGE,"E0.right")])]}),"instanceName":"1"}),"instanceName":"1"}),"instanceName":"1"}),"instanceName":"1"});
            var Q201;
            Q201=makeQuery(id+"F10.opPattern","COPY",BODY,{"derivedFrom":makeQuery(id+"F8.opPattern","COPY",BODY,{"derivedFrom":makeQuery(id+"F7.opPattern","COPY",BODY,{"derivedFrom":makeQuery(id+"F2.opPattern","COPY",BODY,{"derivedFrom":makeQuery(id+"F1.opExtrude","SWEPT_BODY",BODY,{"disambiguationData":[OSD([sQuery(id+"F0.wireOp",EDGE,"E1.bottom"),sQuery(id+"F0.wireOp",EDGE,"E1.top"),sQuery(id+"F0.wireOp",EDGE,"E1.left"),sQuery(id+"F0.wireOp",EDGE,"E1.right")])]}),"instanceName":"1"}),"instanceName":"1"}),"instanceName":"1"}),"instanceName":"1"});
            var Q202;
            Q202=makeQuery(id+"F10.opPattern","COPY",BODY,{"derivedFrom":makeQuery(id+"F8.opPattern","COPY",BODY,{"derivedFrom":makeQuery(id+"F7.opPattern","COPY",BODY,{"derivedFrom":makeQuery(id+"F2.opPattern","COPY",BODY,{"derivedFrom":makeQuery(id+"F1.opExtrude","SWEPT_BODY",BODY,{"disambiguationData":[OSD([sQuery(id+"F0.wireOp",EDGE,"E2.bottom"),sQuery(id+"F0.wireOp",EDGE,"E2.top"),sQuery(id+"F0.wireOp",EDGE,"E2.left"),sQuery(id+"F0.wireOp",EDGE,"E2.right")])]}),"instanceName":"1"}),"instanceName":"1"}),"instanceName":"1"}),"instanceName":"1"});
            var Q203;
            Q203=makeQuery(id+"F10.opPattern","COPY",BODY,{"derivedFrom":makeQuery(id+"F8.opPattern","COPY",BODY,{"derivedFrom":makeQuery(id+"F7.opPattern","COPY",BODY,{"derivedFrom":makeQuery(id+"F3.opPattern","COPY",BODY,{"derivedFrom":makeQuery(id+"F2.opPattern","COPY",BODY,{"derivedFrom":makeQuery(id+"F1.opExtrude","SWEPT_BODY",BODY,{"disambiguationData":[OSD([sQuery(id+"F0.wireOp",EDGE,"E0.bottom"),sQuery(id+"F0.wireOp",EDGE,"E0.top"),sQuery(id+"F0.wireOp",EDGE,"E0.left"),sQuery(id+"F0.wireOp",EDGE,"E0.right")])]}),"instanceName":"1"}),"instanceName":"1"}),"instanceName":"1"}),"instanceName":"1"}),"instanceName":"1"});
            var Q204;
            Q204=makeQuery(id+"F10.opPattern","COPY",BODY,{"derivedFrom":makeQuery(id+"F8.opPattern","COPY",BODY,{"derivedFrom":makeQuery(id+"F7.opPattern","COPY",BODY,{"derivedFrom":makeQuery(id+"F3.opPattern","COPY",BODY,{"derivedFrom":makeQuery(id+"F2.opPattern","COPY",BODY,{"derivedFrom":makeQuery(id+"F1.opExtrude","SWEPT_BODY",BODY,{"disambiguationData":[OSD([sQuery(id+"F0.wireOp",EDGE,"E1.bottom"),sQuery(id+"F0.wireOp",EDGE,"E1.top"),sQuery(id+"F0.wireOp",EDGE,"E1.left"),sQuery(id+"F0.wireOp",EDGE,"E1.right")])]}),"instanceName":"1"}),"instanceName":"1"}),"instanceName":"1"}),"instanceName":"1"}),"instanceName":"1"});
            var Q205;
            Q205=makeQuery(id+"F10.opPattern","COPY",BODY,{"derivedFrom":makeQuery(id+"F8.opPattern","COPY",BODY,{"derivedFrom":makeQuery(id+"F7.opPattern","COPY",BODY,{"derivedFrom":makeQuery(id+"F3.opPattern","COPY",BODY,{"derivedFrom":makeQuery(id+"F2.opPattern","COPY",BODY,{"derivedFrom":makeQuery(id+"F1.opExtrude","SWEPT_BODY",BODY,{"disambiguationData":[OSD([sQuery(id+"F0.wireOp",EDGE,"E2.bottom"),sQuery(id+"F0.wireOp",EDGE,"E2.top"),sQuery(id+"F0.wireOp",EDGE,"E2.left"),sQuery(id+"F0.wireOp",EDGE,"E2.right")])]}),"instanceName":"1"}),"instanceName":"1"}),"instanceName":"1"}),"instanceName":"1"}),"instanceName":"1"});
            var Q206;
            Q206=makeQuery(id+"F10.opPattern","COPY",BODY,{"derivedFrom":makeQuery(id+"F8.opPattern","COPY",BODY,{"derivedFrom":makeQuery(id+"F7.opPattern","COPY",BODY,{"derivedFrom":makeQuery(id+"F4.opPattern","COPY",BODY,{"derivedFrom":makeQuery(id+"F3.opPattern","COPY",BODY,{"derivedFrom":makeQuery(id+"F2.opPattern","COPY",BODY,{"derivedFrom":makeQuery(id+"F1.opExtrude","SWEPT_BODY",BODY,{"disambiguationData":[OSD([sQuery(id+"F0.wireOp",EDGE,"E0.bottom"),sQuery(id+"F0.wireOp",EDGE,"E0.top"),sQuery(id+"F0.wireOp",EDGE,"E0.left"),sQuery(id+"F0.wireOp",EDGE,"E0.right")])]}),"instanceName":"1"}),"instanceName":"1"}),"instanceName":"1"}),"instanceName":"1"}),"instanceName":"1"}),"instanceName":"1"});
            var Q207;
            Q207=makeQuery(id+"F10.opPattern","COPY",BODY,{"derivedFrom":makeQuery(id+"F8.opPattern","COPY",BODY,{"derivedFrom":makeQuery(id+"F7.opPattern","COPY",BODY,{"derivedFrom":makeQuery(id+"F4.opPattern","COPY",BODY,{"derivedFrom":makeQuery(id+"F3.opPattern","COPY",BODY,{"derivedFrom":makeQuery(id+"F2.opPattern","COPY",BODY,{"derivedFrom":makeQuery(id+"F1.opExtrude","SWEPT_BODY",BODY,{"disambiguationData":[OSD([sQuery(id+"F0.wireOp",EDGE,"E1.bottom"),sQuery(id+"F0.wireOp",EDGE,"E1.top"),sQuery(id+"F0.wireOp",EDGE,"E1.left"),sQuery(id+"F0.wireOp",EDGE,"E1.right")])]}),"instanceName":"1"}),"instanceName":"1"}),"instanceName":"1"}),"instanceName":"1"}),"instanceName":"1"}),"instanceName":"1"});
            var Q208;
            Q208=makeQuery(id+"F10.opPattern","COPY",BODY,{"derivedFrom":makeQuery(id+"F8.opPattern","COPY",BODY,{"derivedFrom":makeQuery(id+"F7.opPattern","COPY",BODY,{"derivedFrom":makeQuery(id+"F4.opPattern","COPY",BODY,{"derivedFrom":makeQuery(id+"F3.opPattern","COPY",BODY,{"derivedFrom":makeQuery(id+"F2.opPattern","COPY",BODY,{"derivedFrom":makeQuery(id+"F1.opExtrude","SWEPT_BODY",BODY,{"disambiguationData":[OSD([sQuery(id+"F0.wireOp",EDGE,"E2.bottom"),sQuery(id+"F0.wireOp",EDGE,"E2.top"),sQuery(id+"F0.wireOp",EDGE,"E2.left"),sQuery(id+"F0.wireOp",EDGE,"E2.right")])]}),"instanceName":"1"}),"instanceName":"1"}),"instanceName":"1"}),"instanceName":"1"}),"instanceName":"1"}),"instanceName":"1"});
            var Q209;
            Q209=makeQuery(id+"F10.opPattern","COPY",BODY,{"derivedFrom":makeQuery(id+"F8.opPattern","COPY",BODY,{"derivedFrom":makeQuery(id+"F7.opPattern","COPY",BODY,{"derivedFrom":makeQuery(id+"F5.opPattern","COPY",BODY,{"derivedFrom":makeQuery(id+"F4.opPattern","COPY",BODY,{"derivedFrom":makeQuery(id+"F3.opPattern","COPY",BODY,{"derivedFrom":makeQuery(id+"F2.opPattern","COPY",BODY,{"derivedFrom":makeQuery(id+"F1.opExtrude","SWEPT_BODY",BODY,{"disambiguationData":[OSD([sQuery(id+"F0.wireOp",EDGE,"E0.bottom"),sQuery(id+"F0.wireOp",EDGE,"E0.top"),sQuery(id+"F0.wireOp",EDGE,"E0.left"),sQuery(id+"F0.wireOp",EDGE,"E0.right")])]}),"instanceName":"1"}),"instanceName":"1"}),"instanceName":"1"}),"instanceName":"1"}),"instanceName":"1"}),"instanceName":"1"}),"instanceName":"1"});
            var Q210;
            Q210=makeQuery(id+"F10.opPattern","COPY",BODY,{"derivedFrom":makeQuery(id+"F8.opPattern","COPY",BODY,{"derivedFrom":makeQuery(id+"F7.opPattern","COPY",BODY,{"derivedFrom":makeQuery(id+"F5.opPattern","COPY",BODY,{"derivedFrom":makeQuery(id+"F4.opPattern","COPY",BODY,{"derivedFrom":makeQuery(id+"F3.opPattern","COPY",BODY,{"derivedFrom":makeQuery(id+"F2.opPattern","COPY",BODY,{"derivedFrom":makeQuery(id+"F1.opExtrude","SWEPT_BODY",BODY,{"disambiguationData":[OSD([sQuery(id+"F0.wireOp",EDGE,"E1.bottom"),sQuery(id+"F0.wireOp",EDGE,"E1.top"),sQuery(id+"F0.wireOp",EDGE,"E1.left"),sQuery(id+"F0.wireOp",EDGE,"E1.right")])]}),"instanceName":"1"}),"instanceName":"1"}),"instanceName":"1"}),"instanceName":"1"}),"instanceName":"1"}),"instanceName":"1"}),"instanceName":"1"});
            var Q211;
            Q211=makeQuery(id+"F10.opPattern","COPY",BODY,{"derivedFrom":makeQuery(id+"F8.opPattern","COPY",BODY,{"derivedFrom":makeQuery(id+"F7.opPattern","COPY",BODY,{"derivedFrom":makeQuery(id+"F5.opPattern","COPY",BODY,{"derivedFrom":makeQuery(id+"F4.opPattern","COPY",BODY,{"derivedFrom":makeQuery(id+"F3.opPattern","COPY",BODY,{"derivedFrom":makeQuery(id+"F2.opPattern","COPY",BODY,{"derivedFrom":makeQuery(id+"F1.opExtrude","SWEPT_BODY",BODY,{"disambiguationData":[OSD([sQuery(id+"F0.wireOp",EDGE,"E2.bottom"),sQuery(id+"F0.wireOp",EDGE,"E2.top"),sQuery(id+"F0.wireOp",EDGE,"E2.left"),sQuery(id+"F0.wireOp",EDGE,"E2.right")])]}),"instanceName":"1"}),"instanceName":"1"}),"instanceName":"1"}),"instanceName":"1"}),"instanceName":"1"}),"instanceName":"1"}),"instanceName":"1"});
            var Q212;
            Q212=makeQuery(id+"F10.opPattern","COPY",BODY,{"derivedFrom":makeQuery(id+"F8.opPattern","COPY",BODY,{"derivedFrom":makeQuery(id+"F7.opPattern","COPY",BODY,{"derivedFrom":makeQuery(id+"F6.opPattern","COPY",BODY,{"derivedFrom":makeQuery(id+"F5.opPattern","COPY",BODY,{"derivedFrom":makeQuery(id+"F4.opPattern","COPY",BODY,{"derivedFrom":makeQuery(id+"F3.opPattern","COPY",BODY,{"derivedFrom":makeQuery(id+"F2.opPattern","COPY",BODY,{"derivedFrom":makeQuery(id+"F1.opExtrude","SWEPT_BODY",BODY,{"disambiguationData":[OSD([sQuery(id+"F0.wireOp",EDGE,"E0.bottom"),sQuery(id+"F0.wireOp",EDGE,"E0.top"),sQuery(id+"F0.wireOp",EDGE,"E0.left"),sQuery(id+"F0.wireOp",EDGE,"E0.right")])]}),"instanceName":"1"}),"instanceName":"1"}),"instanceName":"1"}),"instanceName":"1"}),"instanceName":"1"}),"instanceName":"1"}),"instanceName":"1"}),"instanceName":"1"});
            var Q213;
            Q213=makeQuery(id+"F10.opPattern","COPY",BODY,{"derivedFrom":makeQuery(id+"F8.opPattern","COPY",BODY,{"derivedFrom":makeQuery(id+"F7.opPattern","COPY",BODY,{"derivedFrom":makeQuery(id+"F6.opPattern","COPY",BODY,{"derivedFrom":makeQuery(id+"F5.opPattern","COPY",BODY,{"derivedFrom":makeQuery(id+"F4.opPattern","COPY",BODY,{"derivedFrom":makeQuery(id+"F3.opPattern","COPY",BODY,{"derivedFrom":makeQuery(id+"F2.opPattern","COPY",BODY,{"derivedFrom":makeQuery(id+"F1.opExtrude","SWEPT_BODY",BODY,{"disambiguationData":[OSD([sQuery(id+"F0.wireOp",EDGE,"E1.bottom"),sQuery(id+"F0.wireOp",EDGE,"E1.top"),sQuery(id+"F0.wireOp",EDGE,"E1.left"),sQuery(id+"F0.wireOp",EDGE,"E1.right")])]}),"instanceName":"1"}),"instanceName":"1"}),"instanceName":"1"}),"instanceName":"1"}),"instanceName":"1"}),"instanceName":"1"}),"instanceName":"1"}),"instanceName":"1"});
            var Q214;
            Q214=makeQuery(id+"F10.opPattern","COPY",BODY,{"derivedFrom":makeQuery(id+"F8.opPattern","COPY",BODY,{"derivedFrom":makeQuery(id+"F7.opPattern","COPY",BODY,{"derivedFrom":makeQuery(id+"F6.opPattern","COPY",BODY,{"derivedFrom":makeQuery(id+"F5.opPattern","COPY",BODY,{"derivedFrom":makeQuery(id+"F4.opPattern","COPY",BODY,{"derivedFrom":makeQuery(id+"F3.opPattern","COPY",BODY,{"derivedFrom":makeQuery(id+"F2.opPattern","COPY",BODY,{"derivedFrom":makeQuery(id+"F1.opExtrude","SWEPT_BODY",BODY,{"disambiguationData":[OSD([sQuery(id+"F0.wireOp",EDGE,"E2.bottom"),sQuery(id+"F0.wireOp",EDGE,"E2.top"),sQuery(id+"F0.wireOp",EDGE,"E2.left"),sQuery(id+"F0.wireOp",EDGE,"E2.right")])]}),"instanceName":"1"}),"instanceName":"1"}),"instanceName":"1"}),"instanceName":"1"}),"instanceName":"1"}),"instanceName":"1"}),"instanceName":"1"}),"instanceName":"1"});
            var Q215;
            Q215=makeQuery(id+"F10.opPattern","COPY",BODY,{"derivedFrom":makeQuery(id+"F9.opPattern","COPY",BODY,{"derivedFrom":makeQuery(id+"F1.opExtrude","SWEPT_BODY",BODY,{"disambiguationData":[OSD([sQuery(id+"F0.wireOp",EDGE,"E0.bottom"),sQuery(id+"F0.wireOp",EDGE,"E0.top"),sQuery(id+"F0.wireOp",EDGE,"E0.left"),sQuery(id+"F0.wireOp",EDGE,"E0.right")])]}),"instanceName":"1"}),"instanceName":"1"});
            var Q216;
            Q216=makeQuery(id+"F10.opPattern","COPY",BODY,{"derivedFrom":makeQuery(id+"F9.opPattern","COPY",BODY,{"derivedFrom":makeQuery(id+"F1.opExtrude","SWEPT_BODY",BODY,{"disambiguationData":[OSD([sQuery(id+"F0.wireOp",EDGE,"E1.bottom"),sQuery(id+"F0.wireOp",EDGE,"E1.top"),sQuery(id+"F0.wireOp",EDGE,"E1.left"),sQuery(id+"F0.wireOp",EDGE,"E1.right")])]}),"instanceName":"1"}),"instanceName":"1"});
            var Q217;
            Q217=makeQuery(id+"F10.opPattern","COPY",BODY,{"derivedFrom":makeQuery(id+"F9.opPattern","COPY",BODY,{"derivedFrom":makeQuery(id+"F1.opExtrude","SWEPT_BODY",BODY,{"disambiguationData":[OSD([sQuery(id+"F0.wireOp",EDGE,"E2.bottom"),sQuery(id+"F0.wireOp",EDGE,"E2.top"),sQuery(id+"F0.wireOp",EDGE,"E2.left"),sQuery(id+"F0.wireOp",EDGE,"E2.right")])]}),"instanceName":"1"}),"instanceName":"1"});
            var Q218;
            Q218=makeQuery(id+"F10.opPattern","COPY",BODY,{"derivedFrom":makeQuery(id+"F9.opPattern","COPY",BODY,{"derivedFrom":makeQuery(id+"F2.opPattern","COPY",BODY,{"derivedFrom":makeQuery(id+"F1.opExtrude","SWEPT_BODY",BODY,{"disambiguationData":[OSD([sQuery(id+"F0.wireOp",EDGE,"E0.bottom"),sQuery(id+"F0.wireOp",EDGE,"E0.top"),sQuery(id+"F0.wireOp",EDGE,"E0.left"),sQuery(id+"F0.wireOp",EDGE,"E0.right")])]}),"instanceName":"1"}),"instanceName":"1"}),"instanceName":"1"});
            var Q219;
            Q219=makeQuery(id+"F10.opPattern","COPY",BODY,{"derivedFrom":makeQuery(id+"F9.opPattern","COPY",BODY,{"derivedFrom":makeQuery(id+"F2.opPattern","COPY",BODY,{"derivedFrom":makeQuery(id+"F1.opExtrude","SWEPT_BODY",BODY,{"disambiguationData":[OSD([sQuery(id+"F0.wireOp",EDGE,"E1.bottom"),sQuery(id+"F0.wireOp",EDGE,"E1.top"),sQuery(id+"F0.wireOp",EDGE,"E1.left"),sQuery(id+"F0.wireOp",EDGE,"E1.right")])]}),"instanceName":"1"}),"instanceName":"1"}),"instanceName":"1"});
            var Q220;
            Q220=makeQuery(id+"F10.opPattern","COPY",BODY,{"derivedFrom":makeQuery(id+"F9.opPattern","COPY",BODY,{"derivedFrom":makeQuery(id+"F2.opPattern","COPY",BODY,{"derivedFrom":makeQuery(id+"F1.opExtrude","SWEPT_BODY",BODY,{"disambiguationData":[OSD([sQuery(id+"F0.wireOp",EDGE,"E2.bottom"),sQuery(id+"F0.wireOp",EDGE,"E2.top"),sQuery(id+"F0.wireOp",EDGE,"E2.left"),sQuery(id+"F0.wireOp",EDGE,"E2.right")])]}),"instanceName":"1"}),"instanceName":"1"}),"instanceName":"1"});
            var Q221;
            Q221=makeQuery(id+"F10.opPattern","COPY",BODY,{"derivedFrom":makeQuery(id+"F9.opPattern","COPY",BODY,{"derivedFrom":makeQuery(id+"F3.opPattern","COPY",BODY,{"derivedFrom":makeQuery(id+"F2.opPattern","COPY",BODY,{"derivedFrom":makeQuery(id+"F1.opExtrude","SWEPT_BODY",BODY,{"disambiguationData":[OSD([sQuery(id+"F0.wireOp",EDGE,"E0.bottom"),sQuery(id+"F0.wireOp",EDGE,"E0.top"),sQuery(id+"F0.wireOp",EDGE,"E0.left"),sQuery(id+"F0.wireOp",EDGE,"E0.right")])]}),"instanceName":"1"}),"instanceName":"1"}),"instanceName":"1"}),"instanceName":"1"});
            var Q222;
            Q222=makeQuery(id+"F10.opPattern","COPY",BODY,{"derivedFrom":makeQuery(id+"F9.opPattern","COPY",BODY,{"derivedFrom":makeQuery(id+"F3.opPattern","COPY",BODY,{"derivedFrom":makeQuery(id+"F2.opPattern","COPY",BODY,{"derivedFrom":makeQuery(id+"F1.opExtrude","SWEPT_BODY",BODY,{"disambiguationData":[OSD([sQuery(id+"F0.wireOp",EDGE,"E1.bottom"),sQuery(id+"F0.wireOp",EDGE,"E1.top"),sQuery(id+"F0.wireOp",EDGE,"E1.left"),sQuery(id+"F0.wireOp",EDGE,"E1.right")])]}),"instanceName":"1"}),"instanceName":"1"}),"instanceName":"1"}),"instanceName":"1"});
            var Q223;
            Q223=makeQuery(id+"F10.opPattern","COPY",BODY,{"derivedFrom":makeQuery(id+"F9.opPattern","COPY",BODY,{"derivedFrom":makeQuery(id+"F3.opPattern","COPY",BODY,{"derivedFrom":makeQuery(id+"F2.opPattern","COPY",BODY,{"derivedFrom":makeQuery(id+"F1.opExtrude","SWEPT_BODY",BODY,{"disambiguationData":[OSD([sQuery(id+"F0.wireOp",EDGE,"E2.bottom"),sQuery(id+"F0.wireOp",EDGE,"E2.top"),sQuery(id+"F0.wireOp",EDGE,"E2.left"),sQuery(id+"F0.wireOp",EDGE,"E2.right")])]}),"instanceName":"1"}),"instanceName":"1"}),"instanceName":"1"}),"instanceName":"1"});
            var Q224;
            Q224=makeQuery(id+"F10.opPattern","COPY",BODY,{"derivedFrom":makeQuery(id+"F9.opPattern","COPY",BODY,{"derivedFrom":makeQuery(id+"F4.opPattern","COPY",BODY,{"derivedFrom":makeQuery(id+"F3.opPattern","COPY",BODY,{"derivedFrom":makeQuery(id+"F2.opPattern","COPY",BODY,{"derivedFrom":makeQuery(id+"F1.opExtrude","SWEPT_BODY",BODY,{"disambiguationData":[OSD([sQuery(id+"F0.wireOp",EDGE,"E0.bottom"),sQuery(id+"F0.wireOp",EDGE,"E0.top"),sQuery(id+"F0.wireOp",EDGE,"E0.left"),sQuery(id+"F0.wireOp",EDGE,"E0.right")])]}),"instanceName":"1"}),"instanceName":"1"}),"instanceName":"1"}),"instanceName":"1"}),"instanceName":"1"});
            var Q225;
            Q225=makeQuery(id+"F10.opPattern","COPY",BODY,{"derivedFrom":makeQuery(id+"F9.opPattern","COPY",BODY,{"derivedFrom":makeQuery(id+"F4.opPattern","COPY",BODY,{"derivedFrom":makeQuery(id+"F3.opPattern","COPY",BODY,{"derivedFrom":makeQuery(id+"F2.opPattern","COPY",BODY,{"derivedFrom":makeQuery(id+"F1.opExtrude","SWEPT_BODY",BODY,{"disambiguationData":[OSD([sQuery(id+"F0.wireOp",EDGE,"E1.bottom"),sQuery(id+"F0.wireOp",EDGE,"E1.top"),sQuery(id+"F0.wireOp",EDGE,"E1.left"),sQuery(id+"F0.wireOp",EDGE,"E1.right")])]}),"instanceName":"1"}),"instanceName":"1"}),"instanceName":"1"}),"instanceName":"1"}),"instanceName":"1"});
            var Q226;
            Q226=makeQuery(id+"F10.opPattern","COPY",BODY,{"derivedFrom":makeQuery(id+"F9.opPattern","COPY",BODY,{"derivedFrom":makeQuery(id+"F4.opPattern","COPY",BODY,{"derivedFrom":makeQuery(id+"F3.opPattern","COPY",BODY,{"derivedFrom":makeQuery(id+"F2.opPattern","COPY",BODY,{"derivedFrom":makeQuery(id+"F1.opExtrude","SWEPT_BODY",BODY,{"disambiguationData":[OSD([sQuery(id+"F0.wireOp",EDGE,"E2.bottom"),sQuery(id+"F0.wireOp",EDGE,"E2.top"),sQuery(id+"F0.wireOp",EDGE,"E2.left"),sQuery(id+"F0.wireOp",EDGE,"E2.right")])]}),"instanceName":"1"}),"instanceName":"1"}),"instanceName":"1"}),"instanceName":"1"}),"instanceName":"1"});
            var Q227;
            Q227=makeQuery(id+"F10.opPattern","COPY",BODY,{"derivedFrom":makeQuery(id+"F9.opPattern","COPY",BODY,{"derivedFrom":makeQuery(id+"F5.opPattern","COPY",BODY,{"derivedFrom":makeQuery(id+"F4.opPattern","COPY",BODY,{"derivedFrom":makeQuery(id+"F3.opPattern","COPY",BODY,{"derivedFrom":makeQuery(id+"F2.opPattern","COPY",BODY,{"derivedFrom":makeQuery(id+"F1.opExtrude","SWEPT_BODY",BODY,{"disambiguationData":[OSD([sQuery(id+"F0.wireOp",EDGE,"E0.bottom"),sQuery(id+"F0.wireOp",EDGE,"E0.top"),sQuery(id+"F0.wireOp",EDGE,"E0.left"),sQuery(id+"F0.wireOp",EDGE,"E0.right")])]}),"instanceName":"1"}),"instanceName":"1"}),"instanceName":"1"}),"instanceName":"1"}),"instanceName":"1"}),"instanceName":"1"});
            var Q228;
            Q228=makeQuery(id+"F10.opPattern","COPY",BODY,{"derivedFrom":makeQuery(id+"F9.opPattern","COPY",BODY,{"derivedFrom":makeQuery(id+"F5.opPattern","COPY",BODY,{"derivedFrom":makeQuery(id+"F4.opPattern","COPY",BODY,{"derivedFrom":makeQuery(id+"F3.opPattern","COPY",BODY,{"derivedFrom":makeQuery(id+"F2.opPattern","COPY",BODY,{"derivedFrom":makeQuery(id+"F1.opExtrude","SWEPT_BODY",BODY,{"disambiguationData":[OSD([sQuery(id+"F0.wireOp",EDGE,"E1.bottom"),sQuery(id+"F0.wireOp",EDGE,"E1.top"),sQuery(id+"F0.wireOp",EDGE,"E1.left"),sQuery(id+"F0.wireOp",EDGE,"E1.right")])]}),"instanceName":"1"}),"instanceName":"1"}),"instanceName":"1"}),"instanceName":"1"}),"instanceName":"1"}),"instanceName":"1"});
            var Q229;
            Q229=makeQuery(id+"F10.opPattern","COPY",BODY,{"derivedFrom":makeQuery(id+"F9.opPattern","COPY",BODY,{"derivedFrom":makeQuery(id+"F5.opPattern","COPY",BODY,{"derivedFrom":makeQuery(id+"F4.opPattern","COPY",BODY,{"derivedFrom":makeQuery(id+"F3.opPattern","COPY",BODY,{"derivedFrom":makeQuery(id+"F2.opPattern","COPY",BODY,{"derivedFrom":makeQuery(id+"F1.opExtrude","SWEPT_BODY",BODY,{"disambiguationData":[OSD([sQuery(id+"F0.wireOp",EDGE,"E2.bottom"),sQuery(id+"F0.wireOp",EDGE,"E2.top"),sQuery(id+"F0.wireOp",EDGE,"E2.left"),sQuery(id+"F0.wireOp",EDGE,"E2.right")])]}),"instanceName":"1"}),"instanceName":"1"}),"instanceName":"1"}),"instanceName":"1"}),"instanceName":"1"}),"instanceName":"1"});
            var Q230;
            Q230=makeQuery(id+"F10.opPattern","COPY",BODY,{"derivedFrom":makeQuery(id+"F9.opPattern","COPY",BODY,{"derivedFrom":makeQuery(id+"F6.opPattern","COPY",BODY,{"derivedFrom":makeQuery(id+"F5.opPattern","COPY",BODY,{"derivedFrom":makeQuery(id+"F4.opPattern","COPY",BODY,{"derivedFrom":makeQuery(id+"F3.opPattern","COPY",BODY,{"derivedFrom":makeQuery(id+"F2.opPattern","COPY",BODY,{"derivedFrom":makeQuery(id+"F1.opExtrude","SWEPT_BODY",BODY,{"disambiguationData":[OSD([sQuery(id+"F0.wireOp",EDGE,"E0.bottom"),sQuery(id+"F0.wireOp",EDGE,"E0.top"),sQuery(id+"F0.wireOp",EDGE,"E0.left"),sQuery(id+"F0.wireOp",EDGE,"E0.right")])]}),"instanceName":"1"}),"instanceName":"1"}),"instanceName":"1"}),"instanceName":"1"}),"instanceName":"1"}),"instanceName":"1"}),"instanceName":"1"});
            var Q231;
            Q231=makeQuery(id+"F10.opPattern","COPY",BODY,{"derivedFrom":makeQuery(id+"F9.opPattern","COPY",BODY,{"derivedFrom":makeQuery(id+"F6.opPattern","COPY",BODY,{"derivedFrom":makeQuery(id+"F5.opPattern","COPY",BODY,{"derivedFrom":makeQuery(id+"F4.opPattern","COPY",BODY,{"derivedFrom":makeQuery(id+"F3.opPattern","COPY",BODY,{"derivedFrom":makeQuery(id+"F2.opPattern","COPY",BODY,{"derivedFrom":makeQuery(id+"F1.opExtrude","SWEPT_BODY",BODY,{"disambiguationData":[OSD([sQuery(id+"F0.wireOp",EDGE,"E1.bottom"),sQuery(id+"F0.wireOp",EDGE,"E1.top"),sQuery(id+"F0.wireOp",EDGE,"E1.left"),sQuery(id+"F0.wireOp",EDGE,"E1.right")])]}),"instanceName":"1"}),"instanceName":"1"}),"instanceName":"1"}),"instanceName":"1"}),"instanceName":"1"}),"instanceName":"1"}),"instanceName":"1"});
            var Q232;
            Q232=makeQuery(id+"F10.opPattern","COPY",BODY,{"derivedFrom":makeQuery(id+"F9.opPattern","COPY",BODY,{"derivedFrom":makeQuery(id+"F6.opPattern","COPY",BODY,{"derivedFrom":makeQuery(id+"F5.opPattern","COPY",BODY,{"derivedFrom":makeQuery(id+"F4.opPattern","COPY",BODY,{"derivedFrom":makeQuery(id+"F3.opPattern","COPY",BODY,{"derivedFrom":makeQuery(id+"F2.opPattern","COPY",BODY,{"derivedFrom":makeQuery(id+"F1.opExtrude","SWEPT_BODY",BODY,{"disambiguationData":[OSD([sQuery(id+"F0.wireOp",EDGE,"E2.bottom"),sQuery(id+"F0.wireOp",EDGE,"E2.top"),sQuery(id+"F0.wireOp",EDGE,"E2.left"),sQuery(id+"F0.wireOp",EDGE,"E2.right")])]}),"instanceName":"1"}),"instanceName":"1"}),"instanceName":"1"}),"instanceName":"1"}),"instanceName":"1"}),"instanceName":"1"}),"instanceName":"1"});
            var Q233;
            Q233=makeQuery(id+"F10.opPattern","COPY",BODY,{"derivedFrom":makeQuery(id+"F9.opPattern","COPY",BODY,{"derivedFrom":makeQuery(id+"F7.opPattern","COPY",BODY,{"derivedFrom":makeQuery(id+"F1.opExtrude","SWEPT_BODY",BODY,{"disambiguationData":[OSD([sQuery(id+"F0.wireOp",EDGE,"E0.bottom"),sQuery(id+"F0.wireOp",EDGE,"E0.top"),sQuery(id+"F0.wireOp",EDGE,"E0.left"),sQuery(id+"F0.wireOp",EDGE,"E0.right")])]}),"instanceName":"1"}),"instanceName":"1"}),"instanceName":"1"});
            var Q234;
            Q234=makeQuery(id+"F10.opPattern","COPY",BODY,{"derivedFrom":makeQuery(id+"F9.opPattern","COPY",BODY,{"derivedFrom":makeQuery(id+"F7.opPattern","COPY",BODY,{"derivedFrom":makeQuery(id+"F1.opExtrude","SWEPT_BODY",BODY,{"disambiguationData":[OSD([sQuery(id+"F0.wireOp",EDGE,"E1.bottom"),sQuery(id+"F0.wireOp",EDGE,"E1.top"),sQuery(id+"F0.wireOp",EDGE,"E1.left"),sQuery(id+"F0.wireOp",EDGE,"E1.right")])]}),"instanceName":"1"}),"instanceName":"1"}),"instanceName":"1"});
            var Q235;
            Q235=makeQuery(id+"F10.opPattern","COPY",BODY,{"derivedFrom":makeQuery(id+"F9.opPattern","COPY",BODY,{"derivedFrom":makeQuery(id+"F7.opPattern","COPY",BODY,{"derivedFrom":makeQuery(id+"F1.opExtrude","SWEPT_BODY",BODY,{"disambiguationData":[OSD([sQuery(id+"F0.wireOp",EDGE,"E2.bottom"),sQuery(id+"F0.wireOp",EDGE,"E2.top"),sQuery(id+"F0.wireOp",EDGE,"E2.left"),sQuery(id+"F0.wireOp",EDGE,"E2.right")])]}),"instanceName":"1"}),"instanceName":"1"}),"instanceName":"1"});
            var Q236;
            Q236=makeQuery(id+"F10.opPattern","COPY",BODY,{"derivedFrom":makeQuery(id+"F9.opPattern","COPY",BODY,{"derivedFrom":makeQuery(id+"F7.opPattern","COPY",BODY,{"derivedFrom":makeQuery(id+"F2.opPattern","COPY",BODY,{"derivedFrom":makeQuery(id+"F1.opExtrude","SWEPT_BODY",BODY,{"disambiguationData":[OSD([sQuery(id+"F0.wireOp",EDGE,"E0.bottom"),sQuery(id+"F0.wireOp",EDGE,"E0.top"),sQuery(id+"F0.wireOp",EDGE,"E0.left"),sQuery(id+"F0.wireOp",EDGE,"E0.right")])]}),"instanceName":"1"}),"instanceName":"1"}),"instanceName":"1"}),"instanceName":"1"});
            var Q237;
            Q237=makeQuery(id+"F10.opPattern","COPY",BODY,{"derivedFrom":makeQuery(id+"F9.opPattern","COPY",BODY,{"derivedFrom":makeQuery(id+"F7.opPattern","COPY",BODY,{"derivedFrom":makeQuery(id+"F2.opPattern","COPY",BODY,{"derivedFrom":makeQuery(id+"F1.opExtrude","SWEPT_BODY",BODY,{"disambiguationData":[OSD([sQuery(id+"F0.wireOp",EDGE,"E1.bottom"),sQuery(id+"F0.wireOp",EDGE,"E1.top"),sQuery(id+"F0.wireOp",EDGE,"E1.left"),sQuery(id+"F0.wireOp",EDGE,"E1.right")])]}),"instanceName":"1"}),"instanceName":"1"}),"instanceName":"1"}),"instanceName":"1"});
            var Q238;
            Q238=makeQuery(id+"F10.opPattern","COPY",BODY,{"derivedFrom":makeQuery(id+"F9.opPattern","COPY",BODY,{"derivedFrom":makeQuery(id+"F7.opPattern","COPY",BODY,{"derivedFrom":makeQuery(id+"F2.opPattern","COPY",BODY,{"derivedFrom":makeQuery(id+"F1.opExtrude","SWEPT_BODY",BODY,{"disambiguationData":[OSD([sQuery(id+"F0.wireOp",EDGE,"E2.bottom"),sQuery(id+"F0.wireOp",EDGE,"E2.top"),sQuery(id+"F0.wireOp",EDGE,"E2.left"),sQuery(id+"F0.wireOp",EDGE,"E2.right")])]}),"instanceName":"1"}),"instanceName":"1"}),"instanceName":"1"}),"instanceName":"1"});
            var Q239;
            Q239=makeQuery(id+"F10.opPattern","COPY",BODY,{"derivedFrom":makeQuery(id+"F9.opPattern","COPY",BODY,{"derivedFrom":makeQuery(id+"F7.opPattern","COPY",BODY,{"derivedFrom":makeQuery(id+"F3.opPattern","COPY",BODY,{"derivedFrom":makeQuery(id+"F2.opPattern","COPY",BODY,{"derivedFrom":makeQuery(id+"F1.opExtrude","SWEPT_BODY",BODY,{"disambiguationData":[OSD([sQuery(id+"F0.wireOp",EDGE,"E0.bottom"),sQuery(id+"F0.wireOp",EDGE,"E0.top"),sQuery(id+"F0.wireOp",EDGE,"E0.left"),sQuery(id+"F0.wireOp",EDGE,"E0.right")])]}),"instanceName":"1"}),"instanceName":"1"}),"instanceName":"1"}),"instanceName":"1"}),"instanceName":"1"});
            var Q240;
            Q240=makeQuery(id+"F10.opPattern","COPY",BODY,{"derivedFrom":makeQuery(id+"F9.opPattern","COPY",BODY,{"derivedFrom":makeQuery(id+"F7.opPattern","COPY",BODY,{"derivedFrom":makeQuery(id+"F3.opPattern","COPY",BODY,{"derivedFrom":makeQuery(id+"F2.opPattern","COPY",BODY,{"derivedFrom":makeQuery(id+"F1.opExtrude","SWEPT_BODY",BODY,{"disambiguationData":[OSD([sQuery(id+"F0.wireOp",EDGE,"E1.bottom"),sQuery(id+"F0.wireOp",EDGE,"E1.top"),sQuery(id+"F0.wireOp",EDGE,"E1.left"),sQuery(id+"F0.wireOp",EDGE,"E1.right")])]}),"instanceName":"1"}),"instanceName":"1"}),"instanceName":"1"}),"instanceName":"1"}),"instanceName":"1"});
            var Q241;
            Q241=makeQuery(id+"F10.opPattern","COPY",BODY,{"derivedFrom":makeQuery(id+"F9.opPattern","COPY",BODY,{"derivedFrom":makeQuery(id+"F7.opPattern","COPY",BODY,{"derivedFrom":makeQuery(id+"F3.opPattern","COPY",BODY,{"derivedFrom":makeQuery(id+"F2.opPattern","COPY",BODY,{"derivedFrom":makeQuery(id+"F1.opExtrude","SWEPT_BODY",BODY,{"disambiguationData":[OSD([sQuery(id+"F0.wireOp",EDGE,"E2.bottom"),sQuery(id+"F0.wireOp",EDGE,"E2.top"),sQuery(id+"F0.wireOp",EDGE,"E2.left"),sQuery(id+"F0.wireOp",EDGE,"E2.right")])]}),"instanceName":"1"}),"instanceName":"1"}),"instanceName":"1"}),"instanceName":"1"}),"instanceName":"1"});
            var Q242;
            Q242=makeQuery(id+"F10.opPattern","COPY",BODY,{"derivedFrom":makeQuery(id+"F9.opPattern","COPY",BODY,{"derivedFrom":makeQuery(id+"F7.opPattern","COPY",BODY,{"derivedFrom":makeQuery(id+"F4.opPattern","COPY",BODY,{"derivedFrom":makeQuery(id+"F3.opPattern","COPY",BODY,{"derivedFrom":makeQuery(id+"F2.opPattern","COPY",BODY,{"derivedFrom":makeQuery(id+"F1.opExtrude","SWEPT_BODY",BODY,{"disambiguationData":[OSD([sQuery(id+"F0.wireOp",EDGE,"E0.bottom"),sQuery(id+"F0.wireOp",EDGE,"E0.top"),sQuery(id+"F0.wireOp",EDGE,"E0.left"),sQuery(id+"F0.wireOp",EDGE,"E0.right")])]}),"instanceName":"1"}),"instanceName":"1"}),"instanceName":"1"}),"instanceName":"1"}),"instanceName":"1"}),"instanceName":"1"});
            var Q243;
            Q243=makeQuery(id+"F10.opPattern","COPY",BODY,{"derivedFrom":makeQuery(id+"F9.opPattern","COPY",BODY,{"derivedFrom":makeQuery(id+"F7.opPattern","COPY",BODY,{"derivedFrom":makeQuery(id+"F4.opPattern","COPY",BODY,{"derivedFrom":makeQuery(id+"F3.opPattern","COPY",BODY,{"derivedFrom":makeQuery(id+"F2.opPattern","COPY",BODY,{"derivedFrom":makeQuery(id+"F1.opExtrude","SWEPT_BODY",BODY,{"disambiguationData":[OSD([sQuery(id+"F0.wireOp",EDGE,"E1.bottom"),sQuery(id+"F0.wireOp",EDGE,"E1.top"),sQuery(id+"F0.wireOp",EDGE,"E1.left"),sQuery(id+"F0.wireOp",EDGE,"E1.right")])]}),"instanceName":"1"}),"instanceName":"1"}),"instanceName":"1"}),"instanceName":"1"}),"instanceName":"1"}),"instanceName":"1"});
            var Q244;
            Q244=makeQuery(id+"F10.opPattern","COPY",BODY,{"derivedFrom":makeQuery(id+"F9.opPattern","COPY",BODY,{"derivedFrom":makeQuery(id+"F7.opPattern","COPY",BODY,{"derivedFrom":makeQuery(id+"F4.opPattern","COPY",BODY,{"derivedFrom":makeQuery(id+"F3.opPattern","COPY",BODY,{"derivedFrom":makeQuery(id+"F2.opPattern","COPY",BODY,{"derivedFrom":makeQuery(id+"F1.opExtrude","SWEPT_BODY",BODY,{"disambiguationData":[OSD([sQuery(id+"F0.wireOp",EDGE,"E2.bottom"),sQuery(id+"F0.wireOp",EDGE,"E2.top"),sQuery(id+"F0.wireOp",EDGE,"E2.left"),sQuery(id+"F0.wireOp",EDGE,"E2.right")])]}),"instanceName":"1"}),"instanceName":"1"}),"instanceName":"1"}),"instanceName":"1"}),"instanceName":"1"}),"instanceName":"1"});
            var Q245;
            Q245=makeQuery(id+"F10.opPattern","COPY",BODY,{"derivedFrom":makeQuery(id+"F9.opPattern","COPY",BODY,{"derivedFrom":makeQuery(id+"F7.opPattern","COPY",BODY,{"derivedFrom":makeQuery(id+"F5.opPattern","COPY",BODY,{"derivedFrom":makeQuery(id+"F4.opPattern","COPY",BODY,{"derivedFrom":makeQuery(id+"F3.opPattern","COPY",BODY,{"derivedFrom":makeQuery(id+"F2.opPattern","COPY",BODY,{"derivedFrom":makeQuery(id+"F1.opExtrude","SWEPT_BODY",BODY,{"disambiguationData":[OSD([sQuery(id+"F0.wireOp",EDGE,"E0.bottom"),sQuery(id+"F0.wireOp",EDGE,"E0.top"),sQuery(id+"F0.wireOp",EDGE,"E0.left"),sQuery(id+"F0.wireOp",EDGE,"E0.right")])]}),"instanceName":"1"}),"instanceName":"1"}),"instanceName":"1"}),"instanceName":"1"}),"instanceName":"1"}),"instanceName":"1"}),"instanceName":"1"});
            var Q246;
            Q246=makeQuery(id+"F10.opPattern","COPY",BODY,{"derivedFrom":makeQuery(id+"F9.opPattern","COPY",BODY,{"derivedFrom":makeQuery(id+"F7.opPattern","COPY",BODY,{"derivedFrom":makeQuery(id+"F5.opPattern","COPY",BODY,{"derivedFrom":makeQuery(id+"F4.opPattern","COPY",BODY,{"derivedFrom":makeQuery(id+"F3.opPattern","COPY",BODY,{"derivedFrom":makeQuery(id+"F2.opPattern","COPY",BODY,{"derivedFrom":makeQuery(id+"F1.opExtrude","SWEPT_BODY",BODY,{"disambiguationData":[OSD([sQuery(id+"F0.wireOp",EDGE,"E1.bottom"),sQuery(id+"F0.wireOp",EDGE,"E1.top"),sQuery(id+"F0.wireOp",EDGE,"E1.left"),sQuery(id+"F0.wireOp",EDGE,"E1.right")])]}),"instanceName":"1"}),"instanceName":"1"}),"instanceName":"1"}),"instanceName":"1"}),"instanceName":"1"}),"instanceName":"1"}),"instanceName":"1"});
            var Q247;
            Q247=makeQuery(id+"F10.opPattern","COPY",BODY,{"derivedFrom":makeQuery(id+"F9.opPattern","COPY",BODY,{"derivedFrom":makeQuery(id+"F7.opPattern","COPY",BODY,{"derivedFrom":makeQuery(id+"F5.opPattern","COPY",BODY,{"derivedFrom":makeQuery(id+"F4.opPattern","COPY",BODY,{"derivedFrom":makeQuery(id+"F3.opPattern","COPY",BODY,{"derivedFrom":makeQuery(id+"F2.opPattern","COPY",BODY,{"derivedFrom":makeQuery(id+"F1.opExtrude","SWEPT_BODY",BODY,{"disambiguationData":[OSD([sQuery(id+"F0.wireOp",EDGE,"E2.bottom"),sQuery(id+"F0.wireOp",EDGE,"E2.top"),sQuery(id+"F0.wireOp",EDGE,"E2.left"),sQuery(id+"F0.wireOp",EDGE,"E2.right")])]}),"instanceName":"1"}),"instanceName":"1"}),"instanceName":"1"}),"instanceName":"1"}),"instanceName":"1"}),"instanceName":"1"}),"instanceName":"1"});
            var Q248;
            Q248=makeQuery(id+"F10.opPattern","COPY",BODY,{"derivedFrom":makeQuery(id+"F9.opPattern","COPY",BODY,{"derivedFrom":makeQuery(id+"F7.opPattern","COPY",BODY,{"derivedFrom":makeQuery(id+"F6.opPattern","COPY",BODY,{"derivedFrom":makeQuery(id+"F5.opPattern","COPY",BODY,{"derivedFrom":makeQuery(id+"F4.opPattern","COPY",BODY,{"derivedFrom":makeQuery(id+"F3.opPattern","COPY",BODY,{"derivedFrom":makeQuery(id+"F2.opPattern","COPY",BODY,{"derivedFrom":makeQuery(id+"F1.opExtrude","SWEPT_BODY",BODY,{"disambiguationData":[OSD([sQuery(id+"F0.wireOp",EDGE,"E0.bottom"),sQuery(id+"F0.wireOp",EDGE,"E0.top"),sQuery(id+"F0.wireOp",EDGE,"E0.left"),sQuery(id+"F0.wireOp",EDGE,"E0.right")])]}),"instanceName":"1"}),"instanceName":"1"}),"instanceName":"1"}),"instanceName":"1"}),"instanceName":"1"}),"instanceName":"1"}),"instanceName":"1"}),"instanceName":"1"});
            var Q249;
            Q249=makeQuery(id+"F10.opPattern","COPY",BODY,{"derivedFrom":makeQuery(id+"F9.opPattern","COPY",BODY,{"derivedFrom":makeQuery(id+"F7.opPattern","COPY",BODY,{"derivedFrom":makeQuery(id+"F6.opPattern","COPY",BODY,{"derivedFrom":makeQuery(id+"F5.opPattern","COPY",BODY,{"derivedFrom":makeQuery(id+"F4.opPattern","COPY",BODY,{"derivedFrom":makeQuery(id+"F3.opPattern","COPY",BODY,{"derivedFrom":makeQuery(id+"F2.opPattern","COPY",BODY,{"derivedFrom":makeQuery(id+"F1.opExtrude","SWEPT_BODY",BODY,{"disambiguationData":[OSD([sQuery(id+"F0.wireOp",EDGE,"E1.bottom"),sQuery(id+"F0.wireOp",EDGE,"E1.top"),sQuery(id+"F0.wireOp",EDGE,"E1.left"),sQuery(id+"F0.wireOp",EDGE,"E1.right")])]}),"instanceName":"1"}),"instanceName":"1"}),"instanceName":"1"}),"instanceName":"1"}),"instanceName":"1"}),"instanceName":"1"}),"instanceName":"1"}),"instanceName":"1"});
            var Q250;
            Q250=makeQuery(id+"F10.opPattern","COPY",BODY,{"derivedFrom":makeQuery(id+"F9.opPattern","COPY",BODY,{"derivedFrom":makeQuery(id+"F7.opPattern","COPY",BODY,{"derivedFrom":makeQuery(id+"F6.opPattern","COPY",BODY,{"derivedFrom":makeQuery(id+"F5.opPattern","COPY",BODY,{"derivedFrom":makeQuery(id+"F4.opPattern","COPY",BODY,{"derivedFrom":makeQuery(id+"F3.opPattern","COPY",BODY,{"derivedFrom":makeQuery(id+"F2.opPattern","COPY",BODY,{"derivedFrom":makeQuery(id+"F1.opExtrude","SWEPT_BODY",BODY,{"disambiguationData":[OSD([sQuery(id+"F0.wireOp",EDGE,"E2.bottom"),sQuery(id+"F0.wireOp",EDGE,"E2.top"),sQuery(id+"F0.wireOp",EDGE,"E2.left"),sQuery(id+"F0.wireOp",EDGE,"E2.right")])]}),"instanceName":"1"}),"instanceName":"1"}),"instanceName":"1"}),"instanceName":"1"}),"instanceName":"1"}),"instanceName":"1"}),"instanceName":"1"}),"instanceName":"1"});
            var Q251;
            Q251=makeQuery(id+"F10.opPattern","COPY",BODY,{"derivedFrom":makeQuery(id+"F9.opPattern","COPY",BODY,{"derivedFrom":makeQuery(id+"F8.opPattern","COPY",BODY,{"derivedFrom":makeQuery(id+"F1.opExtrude","SWEPT_BODY",BODY,{"disambiguationData":[OSD([sQuery(id+"F0.wireOp",EDGE,"E0.bottom"),sQuery(id+"F0.wireOp",EDGE,"E0.top"),sQuery(id+"F0.wireOp",EDGE,"E0.left"),sQuery(id+"F0.wireOp",EDGE,"E0.right")])]}),"instanceName":"1"}),"instanceName":"1"}),"instanceName":"1"});
            var Q252;
            Q252=makeQuery(id+"F10.opPattern","COPY",BODY,{"derivedFrom":makeQuery(id+"F9.opPattern","COPY",BODY,{"derivedFrom":makeQuery(id+"F8.opPattern","COPY",BODY,{"derivedFrom":makeQuery(id+"F1.opExtrude","SWEPT_BODY",BODY,{"disambiguationData":[OSD([sQuery(id+"F0.wireOp",EDGE,"E1.bottom"),sQuery(id+"F0.wireOp",EDGE,"E1.top"),sQuery(id+"F0.wireOp",EDGE,"E1.left"),sQuery(id+"F0.wireOp",EDGE,"E1.right")])]}),"instanceName":"1"}),"instanceName":"1"}),"instanceName":"1"});
            var Q253;
            Q253=makeQuery(id+"F10.opPattern","COPY",BODY,{"derivedFrom":makeQuery(id+"F9.opPattern","COPY",BODY,{"derivedFrom":makeQuery(id+"F8.opPattern","COPY",BODY,{"derivedFrom":makeQuery(id+"F1.opExtrude","SWEPT_BODY",BODY,{"disambiguationData":[OSD([sQuery(id+"F0.wireOp",EDGE,"E2.bottom"),sQuery(id+"F0.wireOp",EDGE,"E2.top"),sQuery(id+"F0.wireOp",EDGE,"E2.left"),sQuery(id+"F0.wireOp",EDGE,"E2.right")])]}),"instanceName":"1"}),"instanceName":"1"}),"instanceName":"1"});
            var Q254;
            Q254=makeQuery(id+"F10.opPattern","COPY",BODY,{"derivedFrom":makeQuery(id+"F9.opPattern","COPY",BODY,{"derivedFrom":makeQuery(id+"F8.opPattern","COPY",BODY,{"derivedFrom":makeQuery(id+"F2.opPattern","COPY",BODY,{"derivedFrom":makeQuery(id+"F1.opExtrude","SWEPT_BODY",BODY,{"disambiguationData":[OSD([sQuery(id+"F0.wireOp",EDGE,"E0.bottom"),sQuery(id+"F0.wireOp",EDGE,"E0.top"),sQuery(id+"F0.wireOp",EDGE,"E0.left"),sQuery(id+"F0.wireOp",EDGE,"E0.right")])]}),"instanceName":"1"}),"instanceName":"1"}),"instanceName":"1"}),"instanceName":"1"});
            var Q255;
            Q255=makeQuery(id+"F10.opPattern","COPY",BODY,{"derivedFrom":makeQuery(id+"F9.opPattern","COPY",BODY,{"derivedFrom":makeQuery(id+"F8.opPattern","COPY",BODY,{"derivedFrom":makeQuery(id+"F2.opPattern","COPY",BODY,{"derivedFrom":makeQuery(id+"F1.opExtrude","SWEPT_BODY",BODY,{"disambiguationData":[OSD([sQuery(id+"F0.wireOp",EDGE,"E1.bottom"),sQuery(id+"F0.wireOp",EDGE,"E1.top"),sQuery(id+"F0.wireOp",EDGE,"E1.left"),sQuery(id+"F0.wireOp",EDGE,"E1.right")])]}),"instanceName":"1"}),"instanceName":"1"}),"instanceName":"1"}),"instanceName":"1"});
            var Q256;
            Q256=makeQuery(id+"F10.opPattern","COPY",BODY,{"derivedFrom":makeQuery(id+"F9.opPattern","COPY",BODY,{"derivedFrom":makeQuery(id+"F8.opPattern","COPY",BODY,{"derivedFrom":makeQuery(id+"F2.opPattern","COPY",BODY,{"derivedFrom":makeQuery(id+"F1.opExtrude","SWEPT_BODY",BODY,{"disambiguationData":[OSD([sQuery(id+"F0.wireOp",EDGE,"E2.bottom"),sQuery(id+"F0.wireOp",EDGE,"E2.top"),sQuery(id+"F0.wireOp",EDGE,"E2.left"),sQuery(id+"F0.wireOp",EDGE,"E2.right")])]}),"instanceName":"1"}),"instanceName":"1"}),"instanceName":"1"}),"instanceName":"1"});
            var Q257;
            Q257=makeQuery(id+"F10.opPattern","COPY",BODY,{"derivedFrom":makeQuery(id+"F9.opPattern","COPY",BODY,{"derivedFrom":makeQuery(id+"F8.opPattern","COPY",BODY,{"derivedFrom":makeQuery(id+"F3.opPattern","COPY",BODY,{"derivedFrom":makeQuery(id+"F2.opPattern","COPY",BODY,{"derivedFrom":makeQuery(id+"F1.opExtrude","SWEPT_BODY",BODY,{"disambiguationData":[OSD([sQuery(id+"F0.wireOp",EDGE,"E0.bottom"),sQuery(id+"F0.wireOp",EDGE,"E0.top"),sQuery(id+"F0.wireOp",EDGE,"E0.left"),sQuery(id+"F0.wireOp",EDGE,"E0.right")])]}),"instanceName":"1"}),"instanceName":"1"}),"instanceName":"1"}),"instanceName":"1"}),"instanceName":"1"});
            var Q258;
            Q258=makeQuery(id+"F10.opPattern","COPY",BODY,{"derivedFrom":makeQuery(id+"F9.opPattern","COPY",BODY,{"derivedFrom":makeQuery(id+"F8.opPattern","COPY",BODY,{"derivedFrom":makeQuery(id+"F3.opPattern","COPY",BODY,{"derivedFrom":makeQuery(id+"F2.opPattern","COPY",BODY,{"derivedFrom":makeQuery(id+"F1.opExtrude","SWEPT_BODY",BODY,{"disambiguationData":[OSD([sQuery(id+"F0.wireOp",EDGE,"E1.bottom"),sQuery(id+"F0.wireOp",EDGE,"E1.top"),sQuery(id+"F0.wireOp",EDGE,"E1.left"),sQuery(id+"F0.wireOp",EDGE,"E1.right")])]}),"instanceName":"1"}),"instanceName":"1"}),"instanceName":"1"}),"instanceName":"1"}),"instanceName":"1"});
            var Q259;
            Q259=makeQuery(id+"F10.opPattern","COPY",BODY,{"derivedFrom":makeQuery(id+"F9.opPattern","COPY",BODY,{"derivedFrom":makeQuery(id+"F8.opPattern","COPY",BODY,{"derivedFrom":makeQuery(id+"F3.opPattern","COPY",BODY,{"derivedFrom":makeQuery(id+"F2.opPattern","COPY",BODY,{"derivedFrom":makeQuery(id+"F1.opExtrude","SWEPT_BODY",BODY,{"disambiguationData":[OSD([sQuery(id+"F0.wireOp",EDGE,"E2.bottom"),sQuery(id+"F0.wireOp",EDGE,"E2.top"),sQuery(id+"F0.wireOp",EDGE,"E2.left"),sQuery(id+"F0.wireOp",EDGE,"E2.right")])]}),"instanceName":"1"}),"instanceName":"1"}),"instanceName":"1"}),"instanceName":"1"}),"instanceName":"1"});
            var Q260;
            Q260=makeQuery(id+"F10.opPattern","COPY",BODY,{"derivedFrom":makeQuery(id+"F9.opPattern","COPY",BODY,{"derivedFrom":makeQuery(id+"F8.opPattern","COPY",BODY,{"derivedFrom":makeQuery(id+"F4.opPattern","COPY",BODY,{"derivedFrom":makeQuery(id+"F3.opPattern","COPY",BODY,{"derivedFrom":makeQuery(id+"F2.opPattern","COPY",BODY,{"derivedFrom":makeQuery(id+"F1.opExtrude","SWEPT_BODY",BODY,{"disambiguationData":[OSD([sQuery(id+"F0.wireOp",EDGE,"E0.bottom"),sQuery(id+"F0.wireOp",EDGE,"E0.top"),sQuery(id+"F0.wireOp",EDGE,"E0.left"),sQuery(id+"F0.wireOp",EDGE,"E0.right")])]}),"instanceName":"1"}),"instanceName":"1"}),"instanceName":"1"}),"instanceName":"1"}),"instanceName":"1"}),"instanceName":"1"});
            var Q261;
            Q261=makeQuery(id+"F10.opPattern","COPY",BODY,{"derivedFrom":makeQuery(id+"F9.opPattern","COPY",BODY,{"derivedFrom":makeQuery(id+"F8.opPattern","COPY",BODY,{"derivedFrom":makeQuery(id+"F4.opPattern","COPY",BODY,{"derivedFrom":makeQuery(id+"F3.opPattern","COPY",BODY,{"derivedFrom":makeQuery(id+"F2.opPattern","COPY",BODY,{"derivedFrom":makeQuery(id+"F1.opExtrude","SWEPT_BODY",BODY,{"disambiguationData":[OSD([sQuery(id+"F0.wireOp",EDGE,"E1.bottom"),sQuery(id+"F0.wireOp",EDGE,"E1.top"),sQuery(id+"F0.wireOp",EDGE,"E1.left"),sQuery(id+"F0.wireOp",EDGE,"E1.right")])]}),"instanceName":"1"}),"instanceName":"1"}),"instanceName":"1"}),"instanceName":"1"}),"instanceName":"1"}),"instanceName":"1"});
            var Q262;
            Q262=makeQuery(id+"F10.opPattern","COPY",BODY,{"derivedFrom":makeQuery(id+"F9.opPattern","COPY",BODY,{"derivedFrom":makeQuery(id+"F8.opPattern","COPY",BODY,{"derivedFrom":makeQuery(id+"F4.opPattern","COPY",BODY,{"derivedFrom":makeQuery(id+"F3.opPattern","COPY",BODY,{"derivedFrom":makeQuery(id+"F2.opPattern","COPY",BODY,{"derivedFrom":makeQuery(id+"F1.opExtrude","SWEPT_BODY",BODY,{"disambiguationData":[OSD([sQuery(id+"F0.wireOp",EDGE,"E2.bottom"),sQuery(id+"F0.wireOp",EDGE,"E2.top"),sQuery(id+"F0.wireOp",EDGE,"E2.left"),sQuery(id+"F0.wireOp",EDGE,"E2.right")])]}),"instanceName":"1"}),"instanceName":"1"}),"instanceName":"1"}),"instanceName":"1"}),"instanceName":"1"}),"instanceName":"1"});
            var Q263;
            Q263=makeQuery(id+"F10.opPattern","COPY",BODY,{"derivedFrom":makeQuery(id+"F9.opPattern","COPY",BODY,{"derivedFrom":makeQuery(id+"F8.opPattern","COPY",BODY,{"derivedFrom":makeQuery(id+"F5.opPattern","COPY",BODY,{"derivedFrom":makeQuery(id+"F4.opPattern","COPY",BODY,{"derivedFrom":makeQuery(id+"F3.opPattern","COPY",BODY,{"derivedFrom":makeQuery(id+"F2.opPattern","COPY",BODY,{"derivedFrom":makeQuery(id+"F1.opExtrude","SWEPT_BODY",BODY,{"disambiguationData":[OSD([sQuery(id+"F0.wireOp",EDGE,"E0.bottom"),sQuery(id+"F0.wireOp",EDGE,"E0.top"),sQuery(id+"F0.wireOp",EDGE,"E0.left"),sQuery(id+"F0.wireOp",EDGE,"E0.right")])]}),"instanceName":"1"}),"instanceName":"1"}),"instanceName":"1"}),"instanceName":"1"}),"instanceName":"1"}),"instanceName":"1"}),"instanceName":"1"});
            var Q264;
            Q264=makeQuery(id+"F10.opPattern","COPY",BODY,{"derivedFrom":makeQuery(id+"F9.opPattern","COPY",BODY,{"derivedFrom":makeQuery(id+"F8.opPattern","COPY",BODY,{"derivedFrom":makeQuery(id+"F5.opPattern","COPY",BODY,{"derivedFrom":makeQuery(id+"F4.opPattern","COPY",BODY,{"derivedFrom":makeQuery(id+"F3.opPattern","COPY",BODY,{"derivedFrom":makeQuery(id+"F2.opPattern","COPY",BODY,{"derivedFrom":makeQuery(id+"F1.opExtrude","SWEPT_BODY",BODY,{"disambiguationData":[OSD([sQuery(id+"F0.wireOp",EDGE,"E1.bottom"),sQuery(id+"F0.wireOp",EDGE,"E1.top"),sQuery(id+"F0.wireOp",EDGE,"E1.left"),sQuery(id+"F0.wireOp",EDGE,"E1.right")])]}),"instanceName":"1"}),"instanceName":"1"}),"instanceName":"1"}),"instanceName":"1"}),"instanceName":"1"}),"instanceName":"1"}),"instanceName":"1"});
            var Q265;
            Q265=makeQuery(id+"F10.opPattern","COPY",BODY,{"derivedFrom":makeQuery(id+"F9.opPattern","COPY",BODY,{"derivedFrom":makeQuery(id+"F8.opPattern","COPY",BODY,{"derivedFrom":makeQuery(id+"F5.opPattern","COPY",BODY,{"derivedFrom":makeQuery(id+"F4.opPattern","COPY",BODY,{"derivedFrom":makeQuery(id+"F3.opPattern","COPY",BODY,{"derivedFrom":makeQuery(id+"F2.opPattern","COPY",BODY,{"derivedFrom":makeQuery(id+"F1.opExtrude","SWEPT_BODY",BODY,{"disambiguationData":[OSD([sQuery(id+"F0.wireOp",EDGE,"E2.bottom"),sQuery(id+"F0.wireOp",EDGE,"E2.top"),sQuery(id+"F0.wireOp",EDGE,"E2.left"),sQuery(id+"F0.wireOp",EDGE,"E2.right")])]}),"instanceName":"1"}),"instanceName":"1"}),"instanceName":"1"}),"instanceName":"1"}),"instanceName":"1"}),"instanceName":"1"}),"instanceName":"1"});
            var Q266;
            Q266=makeQuery(id+"F10.opPattern","COPY",BODY,{"derivedFrom":makeQuery(id+"F9.opPattern","COPY",BODY,{"derivedFrom":makeQuery(id+"F8.opPattern","COPY",BODY,{"derivedFrom":makeQuery(id+"F6.opPattern","COPY",BODY,{"derivedFrom":makeQuery(id+"F5.opPattern","COPY",BODY,{"derivedFrom":makeQuery(id+"F4.opPattern","COPY",BODY,{"derivedFrom":makeQuery(id+"F3.opPattern","COPY",BODY,{"derivedFrom":makeQuery(id+"F2.opPattern","COPY",BODY,{"derivedFrom":makeQuery(id+"F1.opExtrude","SWEPT_BODY",BODY,{"disambiguationData":[OSD([sQuery(id+"F0.wireOp",EDGE,"E0.bottom"),sQuery(id+"F0.wireOp",EDGE,"E0.top"),sQuery(id+"F0.wireOp",EDGE,"E0.left"),sQuery(id+"F0.wireOp",EDGE,"E0.right")])]}),"instanceName":"1"}),"instanceName":"1"}),"instanceName":"1"}),"instanceName":"1"}),"instanceName":"1"}),"instanceName":"1"}),"instanceName":"1"}),"instanceName":"1"});
            var Q267;
            Q267=makeQuery(id+"F10.opPattern","COPY",BODY,{"derivedFrom":makeQuery(id+"F9.opPattern","COPY",BODY,{"derivedFrom":makeQuery(id+"F8.opPattern","COPY",BODY,{"derivedFrom":makeQuery(id+"F6.opPattern","COPY",BODY,{"derivedFrom":makeQuery(id+"F5.opPattern","COPY",BODY,{"derivedFrom":makeQuery(id+"F4.opPattern","COPY",BODY,{"derivedFrom":makeQuery(id+"F3.opPattern","COPY",BODY,{"derivedFrom":makeQuery(id+"F2.opPattern","COPY",BODY,{"derivedFrom":makeQuery(id+"F1.opExtrude","SWEPT_BODY",BODY,{"disambiguationData":[OSD([sQuery(id+"F0.wireOp",EDGE,"E1.bottom"),sQuery(id+"F0.wireOp",EDGE,"E1.top"),sQuery(id+"F0.wireOp",EDGE,"E1.left"),sQuery(id+"F0.wireOp",EDGE,"E1.right")])]}),"instanceName":"1"}),"instanceName":"1"}),"instanceName":"1"}),"instanceName":"1"}),"instanceName":"1"}),"instanceName":"1"}),"instanceName":"1"}),"instanceName":"1"});
            var Q268;
            Q268=makeQuery(id+"F10.opPattern","COPY",BODY,{"derivedFrom":makeQuery(id+"F9.opPattern","COPY",BODY,{"derivedFrom":makeQuery(id+"F8.opPattern","COPY",BODY,{"derivedFrom":makeQuery(id+"F6.opPattern","COPY",BODY,{"derivedFrom":makeQuery(id+"F5.opPattern","COPY",BODY,{"derivedFrom":makeQuery(id+"F4.opPattern","COPY",BODY,{"derivedFrom":makeQuery(id+"F3.opPattern","COPY",BODY,{"derivedFrom":makeQuery(id+"F2.opPattern","COPY",BODY,{"derivedFrom":makeQuery(id+"F1.opExtrude","SWEPT_BODY",BODY,{"disambiguationData":[OSD([sQuery(id+"F0.wireOp",EDGE,"E2.bottom"),sQuery(id+"F0.wireOp",EDGE,"E2.top"),sQuery(id+"F0.wireOp",EDGE,"E2.left"),sQuery(id+"F0.wireOp",EDGE,"E2.right")])]}),"instanceName":"1"}),"instanceName":"1"}),"instanceName":"1"}),"instanceName":"1"}),"instanceName":"1"}),"instanceName":"1"}),"instanceName":"1"}),"instanceName":"1"});
            var Q269;
            Q269=makeQuery(id+"F10.opPattern","COPY",BODY,{"derivedFrom":makeQuery(id+"F9.opPattern","COPY",BODY,{"derivedFrom":makeQuery(id+"F8.opPattern","COPY",BODY,{"derivedFrom":makeQuery(id+"F7.opPattern","COPY",BODY,{"derivedFrom":makeQuery(id+"F1.opExtrude","SWEPT_BODY",BODY,{"disambiguationData":[OSD([sQuery(id+"F0.wireOp",EDGE,"E0.bottom"),sQuery(id+"F0.wireOp",EDGE,"E0.top"),sQuery(id+"F0.wireOp",EDGE,"E0.left"),sQuery(id+"F0.wireOp",EDGE,"E0.right")])]}),"instanceName":"1"}),"instanceName":"1"}),"instanceName":"1"}),"instanceName":"1"});
            var Q270;
            Q270=makeQuery(id+"F10.opPattern","COPY",BODY,{"derivedFrom":makeQuery(id+"F9.opPattern","COPY",BODY,{"derivedFrom":makeQuery(id+"F8.opPattern","COPY",BODY,{"derivedFrom":makeQuery(id+"F7.opPattern","COPY",BODY,{"derivedFrom":makeQuery(id+"F1.opExtrude","SWEPT_BODY",BODY,{"disambiguationData":[OSD([sQuery(id+"F0.wireOp",EDGE,"E1.bottom"),sQuery(id+"F0.wireOp",EDGE,"E1.top"),sQuery(id+"F0.wireOp",EDGE,"E1.left"),sQuery(id+"F0.wireOp",EDGE,"E1.right")])]}),"instanceName":"1"}),"instanceName":"1"}),"instanceName":"1"}),"instanceName":"1"});
            var Q271;
            Q271=makeQuery(id+"F10.opPattern","COPY",BODY,{"derivedFrom":makeQuery(id+"F9.opPattern","COPY",BODY,{"derivedFrom":makeQuery(id+"F8.opPattern","COPY",BODY,{"derivedFrom":makeQuery(id+"F7.opPattern","COPY",BODY,{"derivedFrom":makeQuery(id+"F1.opExtrude","SWEPT_BODY",BODY,{"disambiguationData":[OSD([sQuery(id+"F0.wireOp",EDGE,"E2.bottom"),sQuery(id+"F0.wireOp",EDGE,"E2.top"),sQuery(id+"F0.wireOp",EDGE,"E2.left"),sQuery(id+"F0.wireOp",EDGE,"E2.right")])]}),"instanceName":"1"}),"instanceName":"1"}),"instanceName":"1"}),"instanceName":"1"});
            var Q272;
            Q272=makeQuery(id+"F10.opPattern","COPY",BODY,{"derivedFrom":makeQuery(id+"F9.opPattern","COPY",BODY,{"derivedFrom":makeQuery(id+"F8.opPattern","COPY",BODY,{"derivedFrom":makeQuery(id+"F7.opPattern","COPY",BODY,{"derivedFrom":makeQuery(id+"F2.opPattern","COPY",BODY,{"derivedFrom":makeQuery(id+"F1.opExtrude","SWEPT_BODY",BODY,{"disambiguationData":[OSD([sQuery(id+"F0.wireOp",EDGE,"E0.bottom"),sQuery(id+"F0.wireOp",EDGE,"E0.top"),sQuery(id+"F0.wireOp",EDGE,"E0.left"),sQuery(id+"F0.wireOp",EDGE,"E0.right")])]}),"instanceName":"1"}),"instanceName":"1"}),"instanceName":"1"}),"instanceName":"1"}),"instanceName":"1"});
            var Q273;
            Q273=makeQuery(id+"F10.opPattern","COPY",BODY,{"derivedFrom":makeQuery(id+"F9.opPattern","COPY",BODY,{"derivedFrom":makeQuery(id+"F8.opPattern","COPY",BODY,{"derivedFrom":makeQuery(id+"F7.opPattern","COPY",BODY,{"derivedFrom":makeQuery(id+"F2.opPattern","COPY",BODY,{"derivedFrom":makeQuery(id+"F1.opExtrude","SWEPT_BODY",BODY,{"disambiguationData":[OSD([sQuery(id+"F0.wireOp",EDGE,"E1.bottom"),sQuery(id+"F0.wireOp",EDGE,"E1.top"),sQuery(id+"F0.wireOp",EDGE,"E1.left"),sQuery(id+"F0.wireOp",EDGE,"E1.right")])]}),"instanceName":"1"}),"instanceName":"1"}),"instanceName":"1"}),"instanceName":"1"}),"instanceName":"1"});
            var Q274;
            Q274=makeQuery(id+"F10.opPattern","COPY",BODY,{"derivedFrom":makeQuery(id+"F9.opPattern","COPY",BODY,{"derivedFrom":makeQuery(id+"F8.opPattern","COPY",BODY,{"derivedFrom":makeQuery(id+"F7.opPattern","COPY",BODY,{"derivedFrom":makeQuery(id+"F2.opPattern","COPY",BODY,{"derivedFrom":makeQuery(id+"F1.opExtrude","SWEPT_BODY",BODY,{"disambiguationData":[OSD([sQuery(id+"F0.wireOp",EDGE,"E2.bottom"),sQuery(id+"F0.wireOp",EDGE,"E2.top"),sQuery(id+"F0.wireOp",EDGE,"E2.left"),sQuery(id+"F0.wireOp",EDGE,"E2.right")])]}),"instanceName":"1"}),"instanceName":"1"}),"instanceName":"1"}),"instanceName":"1"}),"instanceName":"1"});
            var Q275;
            Q275=makeQuery(id+"F10.opPattern","COPY",BODY,{"derivedFrom":makeQuery(id+"F9.opPattern","COPY",BODY,{"derivedFrom":makeQuery(id+"F8.opPattern","COPY",BODY,{"derivedFrom":makeQuery(id+"F7.opPattern","COPY",BODY,{"derivedFrom":makeQuery(id+"F3.opPattern","COPY",BODY,{"derivedFrom":makeQuery(id+"F2.opPattern","COPY",BODY,{"derivedFrom":makeQuery(id+"F1.opExtrude","SWEPT_BODY",BODY,{"disambiguationData":[OSD([sQuery(id+"F0.wireOp",EDGE,"E0.bottom"),sQuery(id+"F0.wireOp",EDGE,"E0.top"),sQuery(id+"F0.wireOp",EDGE,"E0.left"),sQuery(id+"F0.wireOp",EDGE,"E0.right")])]}),"instanceName":"1"}),"instanceName":"1"}),"instanceName":"1"}),"instanceName":"1"}),"instanceName":"1"}),"instanceName":"1"});
            var Q276;
            Q276=makeQuery(id+"F10.opPattern","COPY",BODY,{"derivedFrom":makeQuery(id+"F9.opPattern","COPY",BODY,{"derivedFrom":makeQuery(id+"F8.opPattern","COPY",BODY,{"derivedFrom":makeQuery(id+"F7.opPattern","COPY",BODY,{"derivedFrom":makeQuery(id+"F3.opPattern","COPY",BODY,{"derivedFrom":makeQuery(id+"F2.opPattern","COPY",BODY,{"derivedFrom":makeQuery(id+"F1.opExtrude","SWEPT_BODY",BODY,{"disambiguationData":[OSD([sQuery(id+"F0.wireOp",EDGE,"E1.bottom"),sQuery(id+"F0.wireOp",EDGE,"E1.top"),sQuery(id+"F0.wireOp",EDGE,"E1.left"),sQuery(id+"F0.wireOp",EDGE,"E1.right")])]}),"instanceName":"1"}),"instanceName":"1"}),"instanceName":"1"}),"instanceName":"1"}),"instanceName":"1"}),"instanceName":"1"});
            var Q277;
            Q277=makeQuery(id+"F10.opPattern","COPY",BODY,{"derivedFrom":makeQuery(id+"F9.opPattern","COPY",BODY,{"derivedFrom":makeQuery(id+"F8.opPattern","COPY",BODY,{"derivedFrom":makeQuery(id+"F7.opPattern","COPY",BODY,{"derivedFrom":makeQuery(id+"F3.opPattern","COPY",BODY,{"derivedFrom":makeQuery(id+"F2.opPattern","COPY",BODY,{"derivedFrom":makeQuery(id+"F1.opExtrude","SWEPT_BODY",BODY,{"disambiguationData":[OSD([sQuery(id+"F0.wireOp",EDGE,"E2.bottom"),sQuery(id+"F0.wireOp",EDGE,"E2.top"),sQuery(id+"F0.wireOp",EDGE,"E2.left"),sQuery(id+"F0.wireOp",EDGE,"E2.right")])]}),"instanceName":"1"}),"instanceName":"1"}),"instanceName":"1"}),"instanceName":"1"}),"instanceName":"1"}),"instanceName":"1"});
            var Q278;
            Q278=makeQuery(id+"F10.opPattern","COPY",BODY,{"derivedFrom":makeQuery(id+"F9.opPattern","COPY",BODY,{"derivedFrom":makeQuery(id+"F8.opPattern","COPY",BODY,{"derivedFrom":makeQuery(id+"F7.opPattern","COPY",BODY,{"derivedFrom":makeQuery(id+"F4.opPattern","COPY",BODY,{"derivedFrom":makeQuery(id+"F3.opPattern","COPY",BODY,{"derivedFrom":makeQuery(id+"F2.opPattern","COPY",BODY,{"derivedFrom":makeQuery(id+"F1.opExtrude","SWEPT_BODY",BODY,{"disambiguationData":[OSD([sQuery(id+"F0.wireOp",EDGE,"E0.bottom"),sQuery(id+"F0.wireOp",EDGE,"E0.top"),sQuery(id+"F0.wireOp",EDGE,"E0.left"),sQuery(id+"F0.wireOp",EDGE,"E0.right")])]}),"instanceName":"1"}),"instanceName":"1"}),"instanceName":"1"}),"instanceName":"1"}),"instanceName":"1"}),"instanceName":"1"}),"instanceName":"1"});
            var Q279;
            Q279=makeQuery(id+"F10.opPattern","COPY",BODY,{"derivedFrom":makeQuery(id+"F9.opPattern","COPY",BODY,{"derivedFrom":makeQuery(id+"F8.opPattern","COPY",BODY,{"derivedFrom":makeQuery(id+"F7.opPattern","COPY",BODY,{"derivedFrom":makeQuery(id+"F4.opPattern","COPY",BODY,{"derivedFrom":makeQuery(id+"F3.opPattern","COPY",BODY,{"derivedFrom":makeQuery(id+"F2.opPattern","COPY",BODY,{"derivedFrom":makeQuery(id+"F1.opExtrude","SWEPT_BODY",BODY,{"disambiguationData":[OSD([sQuery(id+"F0.wireOp",EDGE,"E1.bottom"),sQuery(id+"F0.wireOp",EDGE,"E1.top"),sQuery(id+"F0.wireOp",EDGE,"E1.left"),sQuery(id+"F0.wireOp",EDGE,"E1.right")])]}),"instanceName":"1"}),"instanceName":"1"}),"instanceName":"1"}),"instanceName":"1"}),"instanceName":"1"}),"instanceName":"1"}),"instanceName":"1"});
            var Q280;
            Q280=makeQuery(id+"F10.opPattern","COPY",BODY,{"derivedFrom":makeQuery(id+"F9.opPattern","COPY",BODY,{"derivedFrom":makeQuery(id+"F8.opPattern","COPY",BODY,{"derivedFrom":makeQuery(id+"F7.opPattern","COPY",BODY,{"derivedFrom":makeQuery(id+"F4.opPattern","COPY",BODY,{"derivedFrom":makeQuery(id+"F3.opPattern","COPY",BODY,{"derivedFrom":makeQuery(id+"F2.opPattern","COPY",BODY,{"derivedFrom":makeQuery(id+"F1.opExtrude","SWEPT_BODY",BODY,{"disambiguationData":[OSD([sQuery(id+"F0.wireOp",EDGE,"E2.bottom"),sQuery(id+"F0.wireOp",EDGE,"E2.top"),sQuery(id+"F0.wireOp",EDGE,"E2.left"),sQuery(id+"F0.wireOp",EDGE,"E2.right")])]}),"instanceName":"1"}),"instanceName":"1"}),"instanceName":"1"}),"instanceName":"1"}),"instanceName":"1"}),"instanceName":"1"}),"instanceName":"1"});
            var Q281;
            Q281=makeQuery(id+"F10.opPattern","COPY",BODY,{"derivedFrom":makeQuery(id+"F9.opPattern","COPY",BODY,{"derivedFrom":makeQuery(id+"F8.opPattern","COPY",BODY,{"derivedFrom":makeQuery(id+"F7.opPattern","COPY",BODY,{"derivedFrom":makeQuery(id+"F5.opPattern","COPY",BODY,{"derivedFrom":makeQuery(id+"F4.opPattern","COPY",BODY,{"derivedFrom":makeQuery(id+"F3.opPattern","COPY",BODY,{"derivedFrom":makeQuery(id+"F2.opPattern","COPY",BODY,{"derivedFrom":makeQuery(id+"F1.opExtrude","SWEPT_BODY",BODY,{"disambiguationData":[OSD([sQuery(id+"F0.wireOp",EDGE,"E0.bottom"),sQuery(id+"F0.wireOp",EDGE,"E0.top"),sQuery(id+"F0.wireOp",EDGE,"E0.left"),sQuery(id+"F0.wireOp",EDGE,"E0.right")])]}),"instanceName":"1"}),"instanceName":"1"}),"instanceName":"1"}),"instanceName":"1"}),"instanceName":"1"}),"instanceName":"1"}),"instanceName":"1"}),"instanceName":"1"});
            var Q282;
            Q282=makeQuery(id+"F10.opPattern","COPY",BODY,{"derivedFrom":makeQuery(id+"F9.opPattern","COPY",BODY,{"derivedFrom":makeQuery(id+"F8.opPattern","COPY",BODY,{"derivedFrom":makeQuery(id+"F7.opPattern","COPY",BODY,{"derivedFrom":makeQuery(id+"F5.opPattern","COPY",BODY,{"derivedFrom":makeQuery(id+"F4.opPattern","COPY",BODY,{"derivedFrom":makeQuery(id+"F3.opPattern","COPY",BODY,{"derivedFrom":makeQuery(id+"F2.opPattern","COPY",BODY,{"derivedFrom":makeQuery(id+"F1.opExtrude","SWEPT_BODY",BODY,{"disambiguationData":[OSD([sQuery(id+"F0.wireOp",EDGE,"E1.bottom"),sQuery(id+"F0.wireOp",EDGE,"E1.top"),sQuery(id+"F0.wireOp",EDGE,"E1.left"),sQuery(id+"F0.wireOp",EDGE,"E1.right")])]}),"instanceName":"1"}),"instanceName":"1"}),"instanceName":"1"}),"instanceName":"1"}),"instanceName":"1"}),"instanceName":"1"}),"instanceName":"1"}),"instanceName":"1"});
            var Q283;
            Q283=makeQuery(id+"F10.opPattern","COPY",BODY,{"derivedFrom":makeQuery(id+"F9.opPattern","COPY",BODY,{"derivedFrom":makeQuery(id+"F8.opPattern","COPY",BODY,{"derivedFrom":makeQuery(id+"F7.opPattern","COPY",BODY,{"derivedFrom":makeQuery(id+"F5.opPattern","COPY",BODY,{"derivedFrom":makeQuery(id+"F4.opPattern","COPY",BODY,{"derivedFrom":makeQuery(id+"F3.opPattern","COPY",BODY,{"derivedFrom":makeQuery(id+"F2.opPattern","COPY",BODY,{"derivedFrom":makeQuery(id+"F1.opExtrude","SWEPT_BODY",BODY,{"disambiguationData":[OSD([sQuery(id+"F0.wireOp",EDGE,"E2.bottom"),sQuery(id+"F0.wireOp",EDGE,"E2.top"),sQuery(id+"F0.wireOp",EDGE,"E2.left"),sQuery(id+"F0.wireOp",EDGE,"E2.right")])]}),"instanceName":"1"}),"instanceName":"1"}),"instanceName":"1"}),"instanceName":"1"}),"instanceName":"1"}),"instanceName":"1"}),"instanceName":"1"}),"instanceName":"1"});
            var Q284;
            Q284=makeQuery(id+"F10.opPattern","COPY",BODY,{"derivedFrom":makeQuery(id+"F9.opPattern","COPY",BODY,{"derivedFrom":makeQuery(id+"F8.opPattern","COPY",BODY,{"derivedFrom":makeQuery(id+"F7.opPattern","COPY",BODY,{"derivedFrom":makeQuery(id+"F6.opPattern","COPY",BODY,{"derivedFrom":makeQuery(id+"F5.opPattern","COPY",BODY,{"derivedFrom":makeQuery(id+"F4.opPattern","COPY",BODY,{"derivedFrom":makeQuery(id+"F3.opPattern","COPY",BODY,{"derivedFrom":makeQuery(id+"F2.opPattern","COPY",BODY,{"derivedFrom":makeQuery(id+"F1.opExtrude","SWEPT_BODY",BODY,{"disambiguationData":[OSD([sQuery(id+"F0.wireOp",EDGE,"E0.bottom"),sQuery(id+"F0.wireOp",EDGE,"E0.top"),sQuery(id+"F0.wireOp",EDGE,"E0.left"),sQuery(id+"F0.wireOp",EDGE,"E0.right")])]}),"instanceName":"1"}),"instanceName":"1"}),"instanceName":"1"}),"instanceName":"1"}),"instanceName":"1"}),"instanceName":"1"}),"instanceName":"1"}),"instanceName":"1"}),"instanceName":"1"});
            var Q285;
            Q285=makeQuery(id+"F10.opPattern","COPY",BODY,{"derivedFrom":makeQuery(id+"F9.opPattern","COPY",BODY,{"derivedFrom":makeQuery(id+"F8.opPattern","COPY",BODY,{"derivedFrom":makeQuery(id+"F7.opPattern","COPY",BODY,{"derivedFrom":makeQuery(id+"F6.opPattern","COPY",BODY,{"derivedFrom":makeQuery(id+"F5.opPattern","COPY",BODY,{"derivedFrom":makeQuery(id+"F4.opPattern","COPY",BODY,{"derivedFrom":makeQuery(id+"F3.opPattern","COPY",BODY,{"derivedFrom":makeQuery(id+"F2.opPattern","COPY",BODY,{"derivedFrom":makeQuery(id+"F1.opExtrude","SWEPT_BODY",BODY,{"disambiguationData":[OSD([sQuery(id+"F0.wireOp",EDGE,"E1.bottom"),sQuery(id+"F0.wireOp",EDGE,"E1.top"),sQuery(id+"F0.wireOp",EDGE,"E1.left"),sQuery(id+"F0.wireOp",EDGE,"E1.right")])]}),"instanceName":"1"}),"instanceName":"1"}),"instanceName":"1"}),"instanceName":"1"}),"instanceName":"1"}),"instanceName":"1"}),"instanceName":"1"}),"instanceName":"1"}),"instanceName":"1"});
            var Q286;
            Q286=makeQuery(id+"F10.opPattern","COPY",BODY,{"derivedFrom":makeQuery(id+"F9.opPattern","COPY",BODY,{"derivedFrom":makeQuery(id+"F8.opPattern","COPY",BODY,{"derivedFrom":makeQuery(id+"F7.opPattern","COPY",BODY,{"derivedFrom":makeQuery(id+"F6.opPattern","COPY",BODY,{"derivedFrom":makeQuery(id+"F5.opPattern","COPY",BODY,{"derivedFrom":makeQuery(id+"F4.opPattern","COPY",BODY,{"derivedFrom":makeQuery(id+"F3.opPattern","COPY",BODY,{"derivedFrom":makeQuery(id+"F2.opPattern","COPY",BODY,{"derivedFrom":makeQuery(id+"F1.opExtrude","SWEPT_BODY",BODY,{"disambiguationData":[OSD([sQuery(id+"F0.wireOp",EDGE,"E2.bottom"),sQuery(id+"F0.wireOp",EDGE,"E2.top"),sQuery(id+"F0.wireOp",EDGE,"E2.left"),sQuery(id+"F0.wireOp",EDGE,"E2.right")])]}),"instanceName":"1"}),"instanceName":"1"}),"instanceName":"1"}),"instanceName":"1"}),"instanceName":"1"}),"instanceName":"1"}),"instanceName":"1"}),"instanceName":"1"}),"instanceName":"1"});
            var Q287;
            Q287=makeQuery(id+"F11.opPattern","COPY",BODY,{"derivedFrom":makeQuery(id+"F1.opExtrude","SWEPT_BODY",BODY,{"disambiguationData":[OSD([sQuery(id+"F0.wireOp",EDGE,"E0.bottom"),sQuery(id+"F0.wireOp",EDGE,"E0.top"),sQuery(id+"F0.wireOp",EDGE,"E0.left"),sQuery(id+"F0.wireOp",EDGE,"E0.right")])]}),"instanceName":"1"});
            var Q288;
            Q288=makeQuery(id+"F11.opPattern","COPY",BODY,{"derivedFrom":makeQuery(id+"F1.opExtrude","SWEPT_BODY",BODY,{"disambiguationData":[OSD([sQuery(id+"F0.wireOp",EDGE,"E1.bottom"),sQuery(id+"F0.wireOp",EDGE,"E1.top"),sQuery(id+"F0.wireOp",EDGE,"E1.left"),sQuery(id+"F0.wireOp",EDGE,"E1.right")])]}),"instanceName":"1"});
            var Q289;
            Q289=makeQuery(id+"F11.opPattern","COPY",BODY,{"derivedFrom":makeQuery(id+"F1.opExtrude","SWEPT_BODY",BODY,{"disambiguationData":[OSD([sQuery(id+"F0.wireOp",EDGE,"E2.bottom"),sQuery(id+"F0.wireOp",EDGE,"E2.top"),sQuery(id+"F0.wireOp",EDGE,"E2.left"),sQuery(id+"F0.wireOp",EDGE,"E2.right")])]}),"instanceName":"1"});
            var Q290;
            Q290=makeQuery(id+"F11.opPattern","COPY",BODY,{"derivedFrom":makeQuery(id+"F2.opPattern","COPY",BODY,{"derivedFrom":makeQuery(id+"F1.opExtrude","SWEPT_BODY",BODY,{"disambiguationData":[OSD([sQuery(id+"F0.wireOp",EDGE,"E0.bottom"),sQuery(id+"F0.wireOp",EDGE,"E0.top"),sQuery(id+"F0.wireOp",EDGE,"E0.left"),sQuery(id+"F0.wireOp",EDGE,"E0.right")])]}),"instanceName":"1"}),"instanceName":"1"});
            var Q291;
            Q291=makeQuery(id+"F11.opPattern","COPY",BODY,{"derivedFrom":makeQuery(id+"F2.opPattern","COPY",BODY,{"derivedFrom":makeQuery(id+"F1.opExtrude","SWEPT_BODY",BODY,{"disambiguationData":[OSD([sQuery(id+"F0.wireOp",EDGE,"E1.bottom"),sQuery(id+"F0.wireOp",EDGE,"E1.top"),sQuery(id+"F0.wireOp",EDGE,"E1.left"),sQuery(id+"F0.wireOp",EDGE,"E1.right")])]}),"instanceName":"1"}),"instanceName":"1"});
            var Q292;
            Q292=makeQuery(id+"F11.opPattern","COPY",BODY,{"derivedFrom":makeQuery(id+"F2.opPattern","COPY",BODY,{"derivedFrom":makeQuery(id+"F1.opExtrude","SWEPT_BODY",BODY,{"disambiguationData":[OSD([sQuery(id+"F0.wireOp",EDGE,"E2.bottom"),sQuery(id+"F0.wireOp",EDGE,"E2.top"),sQuery(id+"F0.wireOp",EDGE,"E2.left"),sQuery(id+"F0.wireOp",EDGE,"E2.right")])]}),"instanceName":"1"}),"instanceName":"1"});
            var Q293;
            Q293=makeQuery(id+"F11.opPattern","COPY",BODY,{"derivedFrom":makeQuery(id+"F3.opPattern","COPY",BODY,{"derivedFrom":makeQuery(id+"F2.opPattern","COPY",BODY,{"derivedFrom":makeQuery(id+"F1.opExtrude","SWEPT_BODY",BODY,{"disambiguationData":[OSD([sQuery(id+"F0.wireOp",EDGE,"E0.bottom"),sQuery(id+"F0.wireOp",EDGE,"E0.top"),sQuery(id+"F0.wireOp",EDGE,"E0.left"),sQuery(id+"F0.wireOp",EDGE,"E0.right")])]}),"instanceName":"1"}),"instanceName":"1"}),"instanceName":"1"});
            var Q294;
            Q294=makeQuery(id+"F11.opPattern","COPY",BODY,{"derivedFrom":makeQuery(id+"F3.opPattern","COPY",BODY,{"derivedFrom":makeQuery(id+"F2.opPattern","COPY",BODY,{"derivedFrom":makeQuery(id+"F1.opExtrude","SWEPT_BODY",BODY,{"disambiguationData":[OSD([sQuery(id+"F0.wireOp",EDGE,"E1.bottom"),sQuery(id+"F0.wireOp",EDGE,"E1.top"),sQuery(id+"F0.wireOp",EDGE,"E1.left"),sQuery(id+"F0.wireOp",EDGE,"E1.right")])]}),"instanceName":"1"}),"instanceName":"1"}),"instanceName":"1"});
            var Q295;
            Q295=makeQuery(id+"F11.opPattern","COPY",BODY,{"derivedFrom":makeQuery(id+"F3.opPattern","COPY",BODY,{"derivedFrom":makeQuery(id+"F2.opPattern","COPY",BODY,{"derivedFrom":makeQuery(id+"F1.opExtrude","SWEPT_BODY",BODY,{"disambiguationData":[OSD([sQuery(id+"F0.wireOp",EDGE,"E2.bottom"),sQuery(id+"F0.wireOp",EDGE,"E2.top"),sQuery(id+"F0.wireOp",EDGE,"E2.left"),sQuery(id+"F0.wireOp",EDGE,"E2.right")])]}),"instanceName":"1"}),"instanceName":"1"}),"instanceName":"1"});
            var Q296;
            Q296=makeQuery(id+"F11.opPattern","COPY",BODY,{"derivedFrom":makeQuery(id+"F4.opPattern","COPY",BODY,{"derivedFrom":makeQuery(id+"F3.opPattern","COPY",BODY,{"derivedFrom":makeQuery(id+"F2.opPattern","COPY",BODY,{"derivedFrom":makeQuery(id+"F1.opExtrude","SWEPT_BODY",BODY,{"disambiguationData":[OSD([sQuery(id+"F0.wireOp",EDGE,"E0.bottom"),sQuery(id+"F0.wireOp",EDGE,"E0.top"),sQuery(id+"F0.wireOp",EDGE,"E0.left"),sQuery(id+"F0.wireOp",EDGE,"E0.right")])]}),"instanceName":"1"}),"instanceName":"1"}),"instanceName":"1"}),"instanceName":"1"});
            var Q297;
            Q297=makeQuery(id+"F11.opPattern","COPY",BODY,{"derivedFrom":makeQuery(id+"F4.opPattern","COPY",BODY,{"derivedFrom":makeQuery(id+"F3.opPattern","COPY",BODY,{"derivedFrom":makeQuery(id+"F2.opPattern","COPY",BODY,{"derivedFrom":makeQuery(id+"F1.opExtrude","SWEPT_BODY",BODY,{"disambiguationData":[OSD([sQuery(id+"F0.wireOp",EDGE,"E1.bottom"),sQuery(id+"F0.wireOp",EDGE,"E1.top"),sQuery(id+"F0.wireOp",EDGE,"E1.left"),sQuery(id+"F0.wireOp",EDGE,"E1.right")])]}),"instanceName":"1"}),"instanceName":"1"}),"instanceName":"1"}),"instanceName":"1"});
            var Q298;
            Q298=makeQuery(id+"F11.opPattern","COPY",BODY,{"derivedFrom":makeQuery(id+"F4.opPattern","COPY",BODY,{"derivedFrom":makeQuery(id+"F3.opPattern","COPY",BODY,{"derivedFrom":makeQuery(id+"F2.opPattern","COPY",BODY,{"derivedFrom":makeQuery(id+"F1.opExtrude","SWEPT_BODY",BODY,{"disambiguationData":[OSD([sQuery(id+"F0.wireOp",EDGE,"E2.bottom"),sQuery(id+"F0.wireOp",EDGE,"E2.top"),sQuery(id+"F0.wireOp",EDGE,"E2.left"),sQuery(id+"F0.wireOp",EDGE,"E2.right")])]}),"instanceName":"1"}),"instanceName":"1"}),"instanceName":"1"}),"instanceName":"1"});
            var Q299;
            Q299=makeQuery(id+"F11.opPattern","COPY",BODY,{"derivedFrom":makeQuery(id+"F5.opPattern","COPY",BODY,{"derivedFrom":makeQuery(id+"F4.opPattern","COPY",BODY,{"derivedFrom":makeQuery(id+"F3.opPattern","COPY",BODY,{"derivedFrom":makeQuery(id+"F2.opPattern","COPY",BODY,{"derivedFrom":makeQuery(id+"F1.opExtrude","SWEPT_BODY",BODY,{"disambiguationData":[OSD([sQuery(id+"F0.wireOp",EDGE,"E0.bottom"),sQuery(id+"F0.wireOp",EDGE,"E0.top"),sQuery(id+"F0.wireOp",EDGE,"E0.left"),sQuery(id+"F0.wireOp",EDGE,"E0.right")])]}),"instanceName":"1"}),"instanceName":"1"}),"instanceName":"1"}),"instanceName":"1"}),"instanceName":"1"});
            var Q300;
            Q300=makeQuery(id+"F11.opPattern","COPY",BODY,{"derivedFrom":makeQuery(id+"F5.opPattern","COPY",BODY,{"derivedFrom":makeQuery(id+"F4.opPattern","COPY",BODY,{"derivedFrom":makeQuery(id+"F3.opPattern","COPY",BODY,{"derivedFrom":makeQuery(id+"F2.opPattern","COPY",BODY,{"derivedFrom":makeQuery(id+"F1.opExtrude","SWEPT_BODY",BODY,{"disambiguationData":[OSD([sQuery(id+"F0.wireOp",EDGE,"E1.bottom"),sQuery(id+"F0.wireOp",EDGE,"E1.top"),sQuery(id+"F0.wireOp",EDGE,"E1.left"),sQuery(id+"F0.wireOp",EDGE,"E1.right")])]}),"instanceName":"1"}),"instanceName":"1"}),"instanceName":"1"}),"instanceName":"1"}),"instanceName":"1"});
            var Q301;
            Q301=makeQuery(id+"F11.opPattern","COPY",BODY,{"derivedFrom":makeQuery(id+"F5.opPattern","COPY",BODY,{"derivedFrom":makeQuery(id+"F4.opPattern","COPY",BODY,{"derivedFrom":makeQuery(id+"F3.opPattern","COPY",BODY,{"derivedFrom":makeQuery(id+"F2.opPattern","COPY",BODY,{"derivedFrom":makeQuery(id+"F1.opExtrude","SWEPT_BODY",BODY,{"disambiguationData":[OSD([sQuery(id+"F0.wireOp",EDGE,"E2.bottom"),sQuery(id+"F0.wireOp",EDGE,"E2.top"),sQuery(id+"F0.wireOp",EDGE,"E2.left"),sQuery(id+"F0.wireOp",EDGE,"E2.right")])]}),"instanceName":"1"}),"instanceName":"1"}),"instanceName":"1"}),"instanceName":"1"}),"instanceName":"1"});
            var Q302;
            Q302=makeQuery(id+"F11.opPattern","COPY",BODY,{"derivedFrom":makeQuery(id+"F6.opPattern","COPY",BODY,{"derivedFrom":makeQuery(id+"F5.opPattern","COPY",BODY,{"derivedFrom":makeQuery(id+"F4.opPattern","COPY",BODY,{"derivedFrom":makeQuery(id+"F3.opPattern","COPY",BODY,{"derivedFrom":makeQuery(id+"F2.opPattern","COPY",BODY,{"derivedFrom":makeQuery(id+"F1.opExtrude","SWEPT_BODY",BODY,{"disambiguationData":[OSD([sQuery(id+"F0.wireOp",EDGE,"E0.bottom"),sQuery(id+"F0.wireOp",EDGE,"E0.top"),sQuery(id+"F0.wireOp",EDGE,"E0.left"),sQuery(id+"F0.wireOp",EDGE,"E0.right")])]}),"instanceName":"1"}),"instanceName":"1"}),"instanceName":"1"}),"instanceName":"1"}),"instanceName":"1"}),"instanceName":"1"});
            var Q303;
            Q303=makeQuery(id+"F11.opPattern","COPY",BODY,{"derivedFrom":makeQuery(id+"F6.opPattern","COPY",BODY,{"derivedFrom":makeQuery(id+"F5.opPattern","COPY",BODY,{"derivedFrom":makeQuery(id+"F4.opPattern","COPY",BODY,{"derivedFrom":makeQuery(id+"F3.opPattern","COPY",BODY,{"derivedFrom":makeQuery(id+"F2.opPattern","COPY",BODY,{"derivedFrom":makeQuery(id+"F1.opExtrude","SWEPT_BODY",BODY,{"disambiguationData":[OSD([sQuery(id+"F0.wireOp",EDGE,"E1.bottom"),sQuery(id+"F0.wireOp",EDGE,"E1.top"),sQuery(id+"F0.wireOp",EDGE,"E1.left"),sQuery(id+"F0.wireOp",EDGE,"E1.right")])]}),"instanceName":"1"}),"instanceName":"1"}),"instanceName":"1"}),"instanceName":"1"}),"instanceName":"1"}),"instanceName":"1"});
            var Q304;
            Q304=makeQuery(id+"F11.opPattern","COPY",BODY,{"derivedFrom":makeQuery(id+"F6.opPattern","COPY",BODY,{"derivedFrom":makeQuery(id+"F5.opPattern","COPY",BODY,{"derivedFrom":makeQuery(id+"F4.opPattern","COPY",BODY,{"derivedFrom":makeQuery(id+"F3.opPattern","COPY",BODY,{"derivedFrom":makeQuery(id+"F2.opPattern","COPY",BODY,{"derivedFrom":makeQuery(id+"F1.opExtrude","SWEPT_BODY",BODY,{"disambiguationData":[OSD([sQuery(id+"F0.wireOp",EDGE,"E2.bottom"),sQuery(id+"F0.wireOp",EDGE,"E2.top"),sQuery(id+"F0.wireOp",EDGE,"E2.left"),sQuery(id+"F0.wireOp",EDGE,"E2.right")])]}),"instanceName":"1"}),"instanceName":"1"}),"instanceName":"1"}),"instanceName":"1"}),"instanceName":"1"}),"instanceName":"1"});
            var Q305;
            Q305=makeQuery(id+"F11.opPattern","COPY",BODY,{"derivedFrom":makeQuery(id+"F7.opPattern","COPY",BODY,{"derivedFrom":makeQuery(id+"F1.opExtrude","SWEPT_BODY",BODY,{"disambiguationData":[OSD([sQuery(id+"F0.wireOp",EDGE,"E0.bottom"),sQuery(id+"F0.wireOp",EDGE,"E0.top"),sQuery(id+"F0.wireOp",EDGE,"E0.left"),sQuery(id+"F0.wireOp",EDGE,"E0.right")])]}),"instanceName":"1"}),"instanceName":"1"});
            var Q306;
            Q306=makeQuery(id+"F11.opPattern","COPY",BODY,{"derivedFrom":makeQuery(id+"F7.opPattern","COPY",BODY,{"derivedFrom":makeQuery(id+"F1.opExtrude","SWEPT_BODY",BODY,{"disambiguationData":[OSD([sQuery(id+"F0.wireOp",EDGE,"E1.bottom"),sQuery(id+"F0.wireOp",EDGE,"E1.top"),sQuery(id+"F0.wireOp",EDGE,"E1.left"),sQuery(id+"F0.wireOp",EDGE,"E1.right")])]}),"instanceName":"1"}),"instanceName":"1"});
            var Q307;
            Q307=makeQuery(id+"F11.opPattern","COPY",BODY,{"derivedFrom":makeQuery(id+"F7.opPattern","COPY",BODY,{"derivedFrom":makeQuery(id+"F1.opExtrude","SWEPT_BODY",BODY,{"disambiguationData":[OSD([sQuery(id+"F0.wireOp",EDGE,"E2.bottom"),sQuery(id+"F0.wireOp",EDGE,"E2.top"),sQuery(id+"F0.wireOp",EDGE,"E2.left"),sQuery(id+"F0.wireOp",EDGE,"E2.right")])]}),"instanceName":"1"}),"instanceName":"1"});
            var Q308;
            Q308=makeQuery(id+"F11.opPattern","COPY",BODY,{"derivedFrom":makeQuery(id+"F7.opPattern","COPY",BODY,{"derivedFrom":makeQuery(id+"F2.opPattern","COPY",BODY,{"derivedFrom":makeQuery(id+"F1.opExtrude","SWEPT_BODY",BODY,{"disambiguationData":[OSD([sQuery(id+"F0.wireOp",EDGE,"E0.bottom"),sQuery(id+"F0.wireOp",EDGE,"E0.top"),sQuery(id+"F0.wireOp",EDGE,"E0.left"),sQuery(id+"F0.wireOp",EDGE,"E0.right")])]}),"instanceName":"1"}),"instanceName":"1"}),"instanceName":"1"});
            var Q309;
            Q309=makeQuery(id+"F11.opPattern","COPY",BODY,{"derivedFrom":makeQuery(id+"F7.opPattern","COPY",BODY,{"derivedFrom":makeQuery(id+"F2.opPattern","COPY",BODY,{"derivedFrom":makeQuery(id+"F1.opExtrude","SWEPT_BODY",BODY,{"disambiguationData":[OSD([sQuery(id+"F0.wireOp",EDGE,"E1.bottom"),sQuery(id+"F0.wireOp",EDGE,"E1.top"),sQuery(id+"F0.wireOp",EDGE,"E1.left"),sQuery(id+"F0.wireOp",EDGE,"E1.right")])]}),"instanceName":"1"}),"instanceName":"1"}),"instanceName":"1"});
            var Q310;
            Q310=makeQuery(id+"F11.opPattern","COPY",BODY,{"derivedFrom":makeQuery(id+"F7.opPattern","COPY",BODY,{"derivedFrom":makeQuery(id+"F2.opPattern","COPY",BODY,{"derivedFrom":makeQuery(id+"F1.opExtrude","SWEPT_BODY",BODY,{"disambiguationData":[OSD([sQuery(id+"F0.wireOp",EDGE,"E2.bottom"),sQuery(id+"F0.wireOp",EDGE,"E2.top"),sQuery(id+"F0.wireOp",EDGE,"E2.left"),sQuery(id+"F0.wireOp",EDGE,"E2.right")])]}),"instanceName":"1"}),"instanceName":"1"}),"instanceName":"1"});
            var Q311;
            Q311=makeQuery(id+"F11.opPattern","COPY",BODY,{"derivedFrom":makeQuery(id+"F7.opPattern","COPY",BODY,{"derivedFrom":makeQuery(id+"F3.opPattern","COPY",BODY,{"derivedFrom":makeQuery(id+"F2.opPattern","COPY",BODY,{"derivedFrom":makeQuery(id+"F1.opExtrude","SWEPT_BODY",BODY,{"disambiguationData":[OSD([sQuery(id+"F0.wireOp",EDGE,"E0.bottom"),sQuery(id+"F0.wireOp",EDGE,"E0.top"),sQuery(id+"F0.wireOp",EDGE,"E0.left"),sQuery(id+"F0.wireOp",EDGE,"E0.right")])]}),"instanceName":"1"}),"instanceName":"1"}),"instanceName":"1"}),"instanceName":"1"});
            var Q312;
            Q312=makeQuery(id+"F11.opPattern","COPY",BODY,{"derivedFrom":makeQuery(id+"F7.opPattern","COPY",BODY,{"derivedFrom":makeQuery(id+"F3.opPattern","COPY",BODY,{"derivedFrom":makeQuery(id+"F2.opPattern","COPY",BODY,{"derivedFrom":makeQuery(id+"F1.opExtrude","SWEPT_BODY",BODY,{"disambiguationData":[OSD([sQuery(id+"F0.wireOp",EDGE,"E1.bottom"),sQuery(id+"F0.wireOp",EDGE,"E1.top"),sQuery(id+"F0.wireOp",EDGE,"E1.left"),sQuery(id+"F0.wireOp",EDGE,"E1.right")])]}),"instanceName":"1"}),"instanceName":"1"}),"instanceName":"1"}),"instanceName":"1"});
            var Q313;
            Q313=makeQuery(id+"F11.opPattern","COPY",BODY,{"derivedFrom":makeQuery(id+"F7.opPattern","COPY",BODY,{"derivedFrom":makeQuery(id+"F3.opPattern","COPY",BODY,{"derivedFrom":makeQuery(id+"F2.opPattern","COPY",BODY,{"derivedFrom":makeQuery(id+"F1.opExtrude","SWEPT_BODY",BODY,{"disambiguationData":[OSD([sQuery(id+"F0.wireOp",EDGE,"E2.bottom"),sQuery(id+"F0.wireOp",EDGE,"E2.top"),sQuery(id+"F0.wireOp",EDGE,"E2.left"),sQuery(id+"F0.wireOp",EDGE,"E2.right")])]}),"instanceName":"1"}),"instanceName":"1"}),"instanceName":"1"}),"instanceName":"1"});
            var Q314;
            Q314=makeQuery(id+"F11.opPattern","COPY",BODY,{"derivedFrom":makeQuery(id+"F7.opPattern","COPY",BODY,{"derivedFrom":makeQuery(id+"F4.opPattern","COPY",BODY,{"derivedFrom":makeQuery(id+"F3.opPattern","COPY",BODY,{"derivedFrom":makeQuery(id+"F2.opPattern","COPY",BODY,{"derivedFrom":makeQuery(id+"F1.opExtrude","SWEPT_BODY",BODY,{"disambiguationData":[OSD([sQuery(id+"F0.wireOp",EDGE,"E0.bottom"),sQuery(id+"F0.wireOp",EDGE,"E0.top"),sQuery(id+"F0.wireOp",EDGE,"E0.left"),sQuery(id+"F0.wireOp",EDGE,"E0.right")])]}),"instanceName":"1"}),"instanceName":"1"}),"instanceName":"1"}),"instanceName":"1"}),"instanceName":"1"});
            var Q315;
            Q315=makeQuery(id+"F11.opPattern","COPY",BODY,{"derivedFrom":makeQuery(id+"F7.opPattern","COPY",BODY,{"derivedFrom":makeQuery(id+"F4.opPattern","COPY",BODY,{"derivedFrom":makeQuery(id+"F3.opPattern","COPY",BODY,{"derivedFrom":makeQuery(id+"F2.opPattern","COPY",BODY,{"derivedFrom":makeQuery(id+"F1.opExtrude","SWEPT_BODY",BODY,{"disambiguationData":[OSD([sQuery(id+"F0.wireOp",EDGE,"E1.bottom"),sQuery(id+"F0.wireOp",EDGE,"E1.top"),sQuery(id+"F0.wireOp",EDGE,"E1.left"),sQuery(id+"F0.wireOp",EDGE,"E1.right")])]}),"instanceName":"1"}),"instanceName":"1"}),"instanceName":"1"}),"instanceName":"1"}),"instanceName":"1"});
            var Q316;
            Q316=makeQuery(id+"F11.opPattern","COPY",BODY,{"derivedFrom":makeQuery(id+"F7.opPattern","COPY",BODY,{"derivedFrom":makeQuery(id+"F4.opPattern","COPY",BODY,{"derivedFrom":makeQuery(id+"F3.opPattern","COPY",BODY,{"derivedFrom":makeQuery(id+"F2.opPattern","COPY",BODY,{"derivedFrom":makeQuery(id+"F1.opExtrude","SWEPT_BODY",BODY,{"disambiguationData":[OSD([sQuery(id+"F0.wireOp",EDGE,"E2.bottom"),sQuery(id+"F0.wireOp",EDGE,"E2.top"),sQuery(id+"F0.wireOp",EDGE,"E2.left"),sQuery(id+"F0.wireOp",EDGE,"E2.right")])]}),"instanceName":"1"}),"instanceName":"1"}),"instanceName":"1"}),"instanceName":"1"}),"instanceName":"1"});
            var Q317;
            Q317=makeQuery(id+"F11.opPattern","COPY",BODY,{"derivedFrom":makeQuery(id+"F7.opPattern","COPY",BODY,{"derivedFrom":makeQuery(id+"F5.opPattern","COPY",BODY,{"derivedFrom":makeQuery(id+"F4.opPattern","COPY",BODY,{"derivedFrom":makeQuery(id+"F3.opPattern","COPY",BODY,{"derivedFrom":makeQuery(id+"F2.opPattern","COPY",BODY,{"derivedFrom":makeQuery(id+"F1.opExtrude","SWEPT_BODY",BODY,{"disambiguationData":[OSD([sQuery(id+"F0.wireOp",EDGE,"E0.bottom"),sQuery(id+"F0.wireOp",EDGE,"E0.top"),sQuery(id+"F0.wireOp",EDGE,"E0.left"),sQuery(id+"F0.wireOp",EDGE,"E0.right")])]}),"instanceName":"1"}),"instanceName":"1"}),"instanceName":"1"}),"instanceName":"1"}),"instanceName":"1"}),"instanceName":"1"});
            var Q318;
            Q318=makeQuery(id+"F11.opPattern","COPY",BODY,{"derivedFrom":makeQuery(id+"F7.opPattern","COPY",BODY,{"derivedFrom":makeQuery(id+"F5.opPattern","COPY",BODY,{"derivedFrom":makeQuery(id+"F4.opPattern","COPY",BODY,{"derivedFrom":makeQuery(id+"F3.opPattern","COPY",BODY,{"derivedFrom":makeQuery(id+"F2.opPattern","COPY",BODY,{"derivedFrom":makeQuery(id+"F1.opExtrude","SWEPT_BODY",BODY,{"disambiguationData":[OSD([sQuery(id+"F0.wireOp",EDGE,"E1.bottom"),sQuery(id+"F0.wireOp",EDGE,"E1.top"),sQuery(id+"F0.wireOp",EDGE,"E1.left"),sQuery(id+"F0.wireOp",EDGE,"E1.right")])]}),"instanceName":"1"}),"instanceName":"1"}),"instanceName":"1"}),"instanceName":"1"}),"instanceName":"1"}),"instanceName":"1"});
            var Q319;
            Q319=makeQuery(id+"F11.opPattern","COPY",BODY,{"derivedFrom":makeQuery(id+"F7.opPattern","COPY",BODY,{"derivedFrom":makeQuery(id+"F5.opPattern","COPY",BODY,{"derivedFrom":makeQuery(id+"F4.opPattern","COPY",BODY,{"derivedFrom":makeQuery(id+"F3.opPattern","COPY",BODY,{"derivedFrom":makeQuery(id+"F2.opPattern","COPY",BODY,{"derivedFrom":makeQuery(id+"F1.opExtrude","SWEPT_BODY",BODY,{"disambiguationData":[OSD([sQuery(id+"F0.wireOp",EDGE,"E2.bottom"),sQuery(id+"F0.wireOp",EDGE,"E2.top"),sQuery(id+"F0.wireOp",EDGE,"E2.left"),sQuery(id+"F0.wireOp",EDGE,"E2.right")])]}),"instanceName":"1"}),"instanceName":"1"}),"instanceName":"1"}),"instanceName":"1"}),"instanceName":"1"}),"instanceName":"1"});
            var Q320;
            Q320=makeQuery(id+"F11.opPattern","COPY",BODY,{"derivedFrom":makeQuery(id+"F7.opPattern","COPY",BODY,{"derivedFrom":makeQuery(id+"F6.opPattern","COPY",BODY,{"derivedFrom":makeQuery(id+"F5.opPattern","COPY",BODY,{"derivedFrom":makeQuery(id+"F4.opPattern","COPY",BODY,{"derivedFrom":makeQuery(id+"F3.opPattern","COPY",BODY,{"derivedFrom":makeQuery(id+"F2.opPattern","COPY",BODY,{"derivedFrom":makeQuery(id+"F1.opExtrude","SWEPT_BODY",BODY,{"disambiguationData":[OSD([sQuery(id+"F0.wireOp",EDGE,"E0.bottom"),sQuery(id+"F0.wireOp",EDGE,"E0.top"),sQuery(id+"F0.wireOp",EDGE,"E0.left"),sQuery(id+"F0.wireOp",EDGE,"E0.right")])]}),"instanceName":"1"}),"instanceName":"1"}),"instanceName":"1"}),"instanceName":"1"}),"instanceName":"1"}),"instanceName":"1"}),"instanceName":"1"});
            var Q321;
            Q321=makeQuery(id+"F11.opPattern","COPY",BODY,{"derivedFrom":makeQuery(id+"F7.opPattern","COPY",BODY,{"derivedFrom":makeQuery(id+"F6.opPattern","COPY",BODY,{"derivedFrom":makeQuery(id+"F5.opPattern","COPY",BODY,{"derivedFrom":makeQuery(id+"F4.opPattern","COPY",BODY,{"derivedFrom":makeQuery(id+"F3.opPattern","COPY",BODY,{"derivedFrom":makeQuery(id+"F2.opPattern","COPY",BODY,{"derivedFrom":makeQuery(id+"F1.opExtrude","SWEPT_BODY",BODY,{"disambiguationData":[OSD([sQuery(id+"F0.wireOp",EDGE,"E1.bottom"),sQuery(id+"F0.wireOp",EDGE,"E1.top"),sQuery(id+"F0.wireOp",EDGE,"E1.left"),sQuery(id+"F0.wireOp",EDGE,"E1.right")])]}),"instanceName":"1"}),"instanceName":"1"}),"instanceName":"1"}),"instanceName":"1"}),"instanceName":"1"}),"instanceName":"1"}),"instanceName":"1"});
            var Q322;
            Q322=makeQuery(id+"F11.opPattern","COPY",BODY,{"derivedFrom":makeQuery(id+"F7.opPattern","COPY",BODY,{"derivedFrom":makeQuery(id+"F6.opPattern","COPY",BODY,{"derivedFrom":makeQuery(id+"F5.opPattern","COPY",BODY,{"derivedFrom":makeQuery(id+"F4.opPattern","COPY",BODY,{"derivedFrom":makeQuery(id+"F3.opPattern","COPY",BODY,{"derivedFrom":makeQuery(id+"F2.opPattern","COPY",BODY,{"derivedFrom":makeQuery(id+"F1.opExtrude","SWEPT_BODY",BODY,{"disambiguationData":[OSD([sQuery(id+"F0.wireOp",EDGE,"E2.bottom"),sQuery(id+"F0.wireOp",EDGE,"E2.top"),sQuery(id+"F0.wireOp",EDGE,"E2.left"),sQuery(id+"F0.wireOp",EDGE,"E2.right")])]}),"instanceName":"1"}),"instanceName":"1"}),"instanceName":"1"}),"instanceName":"1"}),"instanceName":"1"}),"instanceName":"1"}),"instanceName":"1"});
            var Q323;
            Q323=makeQuery(id+"F11.opPattern","COPY",BODY,{"derivedFrom":makeQuery(id+"F8.opPattern","COPY",BODY,{"derivedFrom":makeQuery(id+"F1.opExtrude","SWEPT_BODY",BODY,{"disambiguationData":[OSD([sQuery(id+"F0.wireOp",EDGE,"E0.bottom"),sQuery(id+"F0.wireOp",EDGE,"E0.top"),sQuery(id+"F0.wireOp",EDGE,"E0.left"),sQuery(id+"F0.wireOp",EDGE,"E0.right")])]}),"instanceName":"1"}),"instanceName":"1"});
            var Q324;
            Q324=makeQuery(id+"F11.opPattern","COPY",BODY,{"derivedFrom":makeQuery(id+"F8.opPattern","COPY",BODY,{"derivedFrom":makeQuery(id+"F1.opExtrude","SWEPT_BODY",BODY,{"disambiguationData":[OSD([sQuery(id+"F0.wireOp",EDGE,"E1.bottom"),sQuery(id+"F0.wireOp",EDGE,"E1.top"),sQuery(id+"F0.wireOp",EDGE,"E1.left"),sQuery(id+"F0.wireOp",EDGE,"E1.right")])]}),"instanceName":"1"}),"instanceName":"1"});
            var Q325;
            Q325=makeQuery(id+"F11.opPattern","COPY",BODY,{"derivedFrom":makeQuery(id+"F8.opPattern","COPY",BODY,{"derivedFrom":makeQuery(id+"F1.opExtrude","SWEPT_BODY",BODY,{"disambiguationData":[OSD([sQuery(id+"F0.wireOp",EDGE,"E2.bottom"),sQuery(id+"F0.wireOp",EDGE,"E2.top"),sQuery(id+"F0.wireOp",EDGE,"E2.left"),sQuery(id+"F0.wireOp",EDGE,"E2.right")])]}),"instanceName":"1"}),"instanceName":"1"});
            var Q326;
            Q326=makeQuery(id+"F11.opPattern","COPY",BODY,{"derivedFrom":makeQuery(id+"F8.opPattern","COPY",BODY,{"derivedFrom":makeQuery(id+"F2.opPattern","COPY",BODY,{"derivedFrom":makeQuery(id+"F1.opExtrude","SWEPT_BODY",BODY,{"disambiguationData":[OSD([sQuery(id+"F0.wireOp",EDGE,"E0.bottom"),sQuery(id+"F0.wireOp",EDGE,"E0.top"),sQuery(id+"F0.wireOp",EDGE,"E0.left"),sQuery(id+"F0.wireOp",EDGE,"E0.right")])]}),"instanceName":"1"}),"instanceName":"1"}),"instanceName":"1"});
            var Q327;
            Q327=makeQuery(id+"F11.opPattern","COPY",BODY,{"derivedFrom":makeQuery(id+"F8.opPattern","COPY",BODY,{"derivedFrom":makeQuery(id+"F2.opPattern","COPY",BODY,{"derivedFrom":makeQuery(id+"F1.opExtrude","SWEPT_BODY",BODY,{"disambiguationData":[OSD([sQuery(id+"F0.wireOp",EDGE,"E1.bottom"),sQuery(id+"F0.wireOp",EDGE,"E1.top"),sQuery(id+"F0.wireOp",EDGE,"E1.left"),sQuery(id+"F0.wireOp",EDGE,"E1.right")])]}),"instanceName":"1"}),"instanceName":"1"}),"instanceName":"1"});
            var Q328;
            Q328=makeQuery(id+"F11.opPattern","COPY",BODY,{"derivedFrom":makeQuery(id+"F8.opPattern","COPY",BODY,{"derivedFrom":makeQuery(id+"F2.opPattern","COPY",BODY,{"derivedFrom":makeQuery(id+"F1.opExtrude","SWEPT_BODY",BODY,{"disambiguationData":[OSD([sQuery(id+"F0.wireOp",EDGE,"E2.bottom"),sQuery(id+"F0.wireOp",EDGE,"E2.top"),sQuery(id+"F0.wireOp",EDGE,"E2.left"),sQuery(id+"F0.wireOp",EDGE,"E2.right")])]}),"instanceName":"1"}),"instanceName":"1"}),"instanceName":"1"});
            var Q329;
            Q329=makeQuery(id+"F11.opPattern","COPY",BODY,{"derivedFrom":makeQuery(id+"F8.opPattern","COPY",BODY,{"derivedFrom":makeQuery(id+"F3.opPattern","COPY",BODY,{"derivedFrom":makeQuery(id+"F2.opPattern","COPY",BODY,{"derivedFrom":makeQuery(id+"F1.opExtrude","SWEPT_BODY",BODY,{"disambiguationData":[OSD([sQuery(id+"F0.wireOp",EDGE,"E0.bottom"),sQuery(id+"F0.wireOp",EDGE,"E0.top"),sQuery(id+"F0.wireOp",EDGE,"E0.left"),sQuery(id+"F0.wireOp",EDGE,"E0.right")])]}),"instanceName":"1"}),"instanceName":"1"}),"instanceName":"1"}),"instanceName":"1"});
            var Q330;
            Q330=makeQuery(id+"F11.opPattern","COPY",BODY,{"derivedFrom":makeQuery(id+"F8.opPattern","COPY",BODY,{"derivedFrom":makeQuery(id+"F3.opPattern","COPY",BODY,{"derivedFrom":makeQuery(id+"F2.opPattern","COPY",BODY,{"derivedFrom":makeQuery(id+"F1.opExtrude","SWEPT_BODY",BODY,{"disambiguationData":[OSD([sQuery(id+"F0.wireOp",EDGE,"E1.bottom"),sQuery(id+"F0.wireOp",EDGE,"E1.top"),sQuery(id+"F0.wireOp",EDGE,"E1.left"),sQuery(id+"F0.wireOp",EDGE,"E1.right")])]}),"instanceName":"1"}),"instanceName":"1"}),"instanceName":"1"}),"instanceName":"1"});
            var Q331;
            Q331=makeQuery(id+"F11.opPattern","COPY",BODY,{"derivedFrom":makeQuery(id+"F8.opPattern","COPY",BODY,{"derivedFrom":makeQuery(id+"F3.opPattern","COPY",BODY,{"derivedFrom":makeQuery(id+"F2.opPattern","COPY",BODY,{"derivedFrom":makeQuery(id+"F1.opExtrude","SWEPT_BODY",BODY,{"disambiguationData":[OSD([sQuery(id+"F0.wireOp",EDGE,"E2.bottom"),sQuery(id+"F0.wireOp",EDGE,"E2.top"),sQuery(id+"F0.wireOp",EDGE,"E2.left"),sQuery(id+"F0.wireOp",EDGE,"E2.right")])]}),"instanceName":"1"}),"instanceName":"1"}),"instanceName":"1"}),"instanceName":"1"});
            var Q332;
            Q332=makeQuery(id+"F11.opPattern","COPY",BODY,{"derivedFrom":makeQuery(id+"F8.opPattern","COPY",BODY,{"derivedFrom":makeQuery(id+"F4.opPattern","COPY",BODY,{"derivedFrom":makeQuery(id+"F3.opPattern","COPY",BODY,{"derivedFrom":makeQuery(id+"F2.opPattern","COPY",BODY,{"derivedFrom":makeQuery(id+"F1.opExtrude","SWEPT_BODY",BODY,{"disambiguationData":[OSD([sQuery(id+"F0.wireOp",EDGE,"E0.bottom"),sQuery(id+"F0.wireOp",EDGE,"E0.top"),sQuery(id+"F0.wireOp",EDGE,"E0.left"),sQuery(id+"F0.wireOp",EDGE,"E0.right")])]}),"instanceName":"1"}),"instanceName":"1"}),"instanceName":"1"}),"instanceName":"1"}),"instanceName":"1"});
            var Q333;
            Q333=makeQuery(id+"F11.opPattern","COPY",BODY,{"derivedFrom":makeQuery(id+"F8.opPattern","COPY",BODY,{"derivedFrom":makeQuery(id+"F4.opPattern","COPY",BODY,{"derivedFrom":makeQuery(id+"F3.opPattern","COPY",BODY,{"derivedFrom":makeQuery(id+"F2.opPattern","COPY",BODY,{"derivedFrom":makeQuery(id+"F1.opExtrude","SWEPT_BODY",BODY,{"disambiguationData":[OSD([sQuery(id+"F0.wireOp",EDGE,"E1.bottom"),sQuery(id+"F0.wireOp",EDGE,"E1.top"),sQuery(id+"F0.wireOp",EDGE,"E1.left"),sQuery(id+"F0.wireOp",EDGE,"E1.right")])]}),"instanceName":"1"}),"instanceName":"1"}),"instanceName":"1"}),"instanceName":"1"}),"instanceName":"1"});
            var Q334;
            Q334=makeQuery(id+"F11.opPattern","COPY",BODY,{"derivedFrom":makeQuery(id+"F8.opPattern","COPY",BODY,{"derivedFrom":makeQuery(id+"F4.opPattern","COPY",BODY,{"derivedFrom":makeQuery(id+"F3.opPattern","COPY",BODY,{"derivedFrom":makeQuery(id+"F2.opPattern","COPY",BODY,{"derivedFrom":makeQuery(id+"F1.opExtrude","SWEPT_BODY",BODY,{"disambiguationData":[OSD([sQuery(id+"F0.wireOp",EDGE,"E2.bottom"),sQuery(id+"F0.wireOp",EDGE,"E2.top"),sQuery(id+"F0.wireOp",EDGE,"E2.left"),sQuery(id+"F0.wireOp",EDGE,"E2.right")])]}),"instanceName":"1"}),"instanceName":"1"}),"instanceName":"1"}),"instanceName":"1"}),"instanceName":"1"});
            var Q335;
            Q335=makeQuery(id+"F11.opPattern","COPY",BODY,{"derivedFrom":makeQuery(id+"F8.opPattern","COPY",BODY,{"derivedFrom":makeQuery(id+"F5.opPattern","COPY",BODY,{"derivedFrom":makeQuery(id+"F4.opPattern","COPY",BODY,{"derivedFrom":makeQuery(id+"F3.opPattern","COPY",BODY,{"derivedFrom":makeQuery(id+"F2.opPattern","COPY",BODY,{"derivedFrom":makeQuery(id+"F1.opExtrude","SWEPT_BODY",BODY,{"disambiguationData":[OSD([sQuery(id+"F0.wireOp",EDGE,"E0.bottom"),sQuery(id+"F0.wireOp",EDGE,"E0.top"),sQuery(id+"F0.wireOp",EDGE,"E0.left"),sQuery(id+"F0.wireOp",EDGE,"E0.right")])]}),"instanceName":"1"}),"instanceName":"1"}),"instanceName":"1"}),"instanceName":"1"}),"instanceName":"1"}),"instanceName":"1"});
            var Q336;
            Q336=makeQuery(id+"F11.opPattern","COPY",BODY,{"derivedFrom":makeQuery(id+"F8.opPattern","COPY",BODY,{"derivedFrom":makeQuery(id+"F5.opPattern","COPY",BODY,{"derivedFrom":makeQuery(id+"F4.opPattern","COPY",BODY,{"derivedFrom":makeQuery(id+"F3.opPattern","COPY",BODY,{"derivedFrom":makeQuery(id+"F2.opPattern","COPY",BODY,{"derivedFrom":makeQuery(id+"F1.opExtrude","SWEPT_BODY",BODY,{"disambiguationData":[OSD([sQuery(id+"F0.wireOp",EDGE,"E1.bottom"),sQuery(id+"F0.wireOp",EDGE,"E1.top"),sQuery(id+"F0.wireOp",EDGE,"E1.left"),sQuery(id+"F0.wireOp",EDGE,"E1.right")])]}),"instanceName":"1"}),"instanceName":"1"}),"instanceName":"1"}),"instanceName":"1"}),"instanceName":"1"}),"instanceName":"1"});
            var Q337;
            Q337=makeQuery(id+"F11.opPattern","COPY",BODY,{"derivedFrom":makeQuery(id+"F8.opPattern","COPY",BODY,{"derivedFrom":makeQuery(id+"F5.opPattern","COPY",BODY,{"derivedFrom":makeQuery(id+"F4.opPattern","COPY",BODY,{"derivedFrom":makeQuery(id+"F3.opPattern","COPY",BODY,{"derivedFrom":makeQuery(id+"F2.opPattern","COPY",BODY,{"derivedFrom":makeQuery(id+"F1.opExtrude","SWEPT_BODY",BODY,{"disambiguationData":[OSD([sQuery(id+"F0.wireOp",EDGE,"E2.bottom"),sQuery(id+"F0.wireOp",EDGE,"E2.top"),sQuery(id+"F0.wireOp",EDGE,"E2.left"),sQuery(id+"F0.wireOp",EDGE,"E2.right")])]}),"instanceName":"1"}),"instanceName":"1"}),"instanceName":"1"}),"instanceName":"1"}),"instanceName":"1"}),"instanceName":"1"});
            var Q338;
            Q338=makeQuery(id+"F11.opPattern","COPY",BODY,{"derivedFrom":makeQuery(id+"F8.opPattern","COPY",BODY,{"derivedFrom":makeQuery(id+"F6.opPattern","COPY",BODY,{"derivedFrom":makeQuery(id+"F5.opPattern","COPY",BODY,{"derivedFrom":makeQuery(id+"F4.opPattern","COPY",BODY,{"derivedFrom":makeQuery(id+"F3.opPattern","COPY",BODY,{"derivedFrom":makeQuery(id+"F2.opPattern","COPY",BODY,{"derivedFrom":makeQuery(id+"F1.opExtrude","SWEPT_BODY",BODY,{"disambiguationData":[OSD([sQuery(id+"F0.wireOp",EDGE,"E0.bottom"),sQuery(id+"F0.wireOp",EDGE,"E0.top"),sQuery(id+"F0.wireOp",EDGE,"E0.left"),sQuery(id+"F0.wireOp",EDGE,"E0.right")])]}),"instanceName":"1"}),"instanceName":"1"}),"instanceName":"1"}),"instanceName":"1"}),"instanceName":"1"}),"instanceName":"1"}),"instanceName":"1"});
            var Q339;
            Q339=makeQuery(id+"F11.opPattern","COPY",BODY,{"derivedFrom":makeQuery(id+"F8.opPattern","COPY",BODY,{"derivedFrom":makeQuery(id+"F6.opPattern","COPY",BODY,{"derivedFrom":makeQuery(id+"F5.opPattern","COPY",BODY,{"derivedFrom":makeQuery(id+"F4.opPattern","COPY",BODY,{"derivedFrom":makeQuery(id+"F3.opPattern","COPY",BODY,{"derivedFrom":makeQuery(id+"F2.opPattern","COPY",BODY,{"derivedFrom":makeQuery(id+"F1.opExtrude","SWEPT_BODY",BODY,{"disambiguationData":[OSD([sQuery(id+"F0.wireOp",EDGE,"E1.bottom"),sQuery(id+"F0.wireOp",EDGE,"E1.top"),sQuery(id+"F0.wireOp",EDGE,"E1.left"),sQuery(id+"F0.wireOp",EDGE,"E1.right")])]}),"instanceName":"1"}),"instanceName":"1"}),"instanceName":"1"}),"instanceName":"1"}),"instanceName":"1"}),"instanceName":"1"}),"instanceName":"1"});
            var Q340;
            Q340=makeQuery(id+"F11.opPattern","COPY",BODY,{"derivedFrom":makeQuery(id+"F8.opPattern","COPY",BODY,{"derivedFrom":makeQuery(id+"F6.opPattern","COPY",BODY,{"derivedFrom":makeQuery(id+"F5.opPattern","COPY",BODY,{"derivedFrom":makeQuery(id+"F4.opPattern","COPY",BODY,{"derivedFrom":makeQuery(id+"F3.opPattern","COPY",BODY,{"derivedFrom":makeQuery(id+"F2.opPattern","COPY",BODY,{"derivedFrom":makeQuery(id+"F1.opExtrude","SWEPT_BODY",BODY,{"disambiguationData":[OSD([sQuery(id+"F0.wireOp",EDGE,"E2.bottom"),sQuery(id+"F0.wireOp",EDGE,"E2.top"),sQuery(id+"F0.wireOp",EDGE,"E2.left"),sQuery(id+"F0.wireOp",EDGE,"E2.right")])]}),"instanceName":"1"}),"instanceName":"1"}),"instanceName":"1"}),"instanceName":"1"}),"instanceName":"1"}),"instanceName":"1"}),"instanceName":"1"});
            var Q341;
            Q341=makeQuery(id+"F11.opPattern","COPY",BODY,{"derivedFrom":makeQuery(id+"F8.opPattern","COPY",BODY,{"derivedFrom":makeQuery(id+"F7.opPattern","COPY",BODY,{"derivedFrom":makeQuery(id+"F1.opExtrude","SWEPT_BODY",BODY,{"disambiguationData":[OSD([sQuery(id+"F0.wireOp",EDGE,"E0.bottom"),sQuery(id+"F0.wireOp",EDGE,"E0.top"),sQuery(id+"F0.wireOp",EDGE,"E0.left"),sQuery(id+"F0.wireOp",EDGE,"E0.right")])]}),"instanceName":"1"}),"instanceName":"1"}),"instanceName":"1"});
            var Q342;
            Q342=makeQuery(id+"F11.opPattern","COPY",BODY,{"derivedFrom":makeQuery(id+"F8.opPattern","COPY",BODY,{"derivedFrom":makeQuery(id+"F7.opPattern","COPY",BODY,{"derivedFrom":makeQuery(id+"F1.opExtrude","SWEPT_BODY",BODY,{"disambiguationData":[OSD([sQuery(id+"F0.wireOp",EDGE,"E1.bottom"),sQuery(id+"F0.wireOp",EDGE,"E1.top"),sQuery(id+"F0.wireOp",EDGE,"E1.left"),sQuery(id+"F0.wireOp",EDGE,"E1.right")])]}),"instanceName":"1"}),"instanceName":"1"}),"instanceName":"1"});
            var Q343;
            Q343=makeQuery(id+"F11.opPattern","COPY",BODY,{"derivedFrom":makeQuery(id+"F8.opPattern","COPY",BODY,{"derivedFrom":makeQuery(id+"F7.opPattern","COPY",BODY,{"derivedFrom":makeQuery(id+"F1.opExtrude","SWEPT_BODY",BODY,{"disambiguationData":[OSD([sQuery(id+"F0.wireOp",EDGE,"E2.bottom"),sQuery(id+"F0.wireOp",EDGE,"E2.top"),sQuery(id+"F0.wireOp",EDGE,"E2.left"),sQuery(id+"F0.wireOp",EDGE,"E2.right")])]}),"instanceName":"1"}),"instanceName":"1"}),"instanceName":"1"});
            var Q344;
            Q344=makeQuery(id+"F11.opPattern","COPY",BODY,{"derivedFrom":makeQuery(id+"F8.opPattern","COPY",BODY,{"derivedFrom":makeQuery(id+"F7.opPattern","COPY",BODY,{"derivedFrom":makeQuery(id+"F2.opPattern","COPY",BODY,{"derivedFrom":makeQuery(id+"F1.opExtrude","SWEPT_BODY",BODY,{"disambiguationData":[OSD([sQuery(id+"F0.wireOp",EDGE,"E0.bottom"),sQuery(id+"F0.wireOp",EDGE,"E0.top"),sQuery(id+"F0.wireOp",EDGE,"E0.left"),sQuery(id+"F0.wireOp",EDGE,"E0.right")])]}),"instanceName":"1"}),"instanceName":"1"}),"instanceName":"1"}),"instanceName":"1"});
            var Q345;
            Q345=makeQuery(id+"F11.opPattern","COPY",BODY,{"derivedFrom":makeQuery(id+"F8.opPattern","COPY",BODY,{"derivedFrom":makeQuery(id+"F7.opPattern","COPY",BODY,{"derivedFrom":makeQuery(id+"F2.opPattern","COPY",BODY,{"derivedFrom":makeQuery(id+"F1.opExtrude","SWEPT_BODY",BODY,{"disambiguationData":[OSD([sQuery(id+"F0.wireOp",EDGE,"E1.bottom"),sQuery(id+"F0.wireOp",EDGE,"E1.top"),sQuery(id+"F0.wireOp",EDGE,"E1.left"),sQuery(id+"F0.wireOp",EDGE,"E1.right")])]}),"instanceName":"1"}),"instanceName":"1"}),"instanceName":"1"}),"instanceName":"1"});
            var Q346;
            Q346=makeQuery(id+"F11.opPattern","COPY",BODY,{"derivedFrom":makeQuery(id+"F8.opPattern","COPY",BODY,{"derivedFrom":makeQuery(id+"F7.opPattern","COPY",BODY,{"derivedFrom":makeQuery(id+"F2.opPattern","COPY",BODY,{"derivedFrom":makeQuery(id+"F1.opExtrude","SWEPT_BODY",BODY,{"disambiguationData":[OSD([sQuery(id+"F0.wireOp",EDGE,"E2.bottom"),sQuery(id+"F0.wireOp",EDGE,"E2.top"),sQuery(id+"F0.wireOp",EDGE,"E2.left"),sQuery(id+"F0.wireOp",EDGE,"E2.right")])]}),"instanceName":"1"}),"instanceName":"1"}),"instanceName":"1"}),"instanceName":"1"});
            var Q347;
            Q347=makeQuery(id+"F11.opPattern","COPY",BODY,{"derivedFrom":makeQuery(id+"F8.opPattern","COPY",BODY,{"derivedFrom":makeQuery(id+"F7.opPattern","COPY",BODY,{"derivedFrom":makeQuery(id+"F3.opPattern","COPY",BODY,{"derivedFrom":makeQuery(id+"F2.opPattern","COPY",BODY,{"derivedFrom":makeQuery(id+"F1.opExtrude","SWEPT_BODY",BODY,{"disambiguationData":[OSD([sQuery(id+"F0.wireOp",EDGE,"E0.bottom"),sQuery(id+"F0.wireOp",EDGE,"E0.top"),sQuery(id+"F0.wireOp",EDGE,"E0.left"),sQuery(id+"F0.wireOp",EDGE,"E0.right")])]}),"instanceName":"1"}),"instanceName":"1"}),"instanceName":"1"}),"instanceName":"1"}),"instanceName":"1"});
            var Q348;
            Q348=makeQuery(id+"F11.opPattern","COPY",BODY,{"derivedFrom":makeQuery(id+"F8.opPattern","COPY",BODY,{"derivedFrom":makeQuery(id+"F7.opPattern","COPY",BODY,{"derivedFrom":makeQuery(id+"F3.opPattern","COPY",BODY,{"derivedFrom":makeQuery(id+"F2.opPattern","COPY",BODY,{"derivedFrom":makeQuery(id+"F1.opExtrude","SWEPT_BODY",BODY,{"disambiguationData":[OSD([sQuery(id+"F0.wireOp",EDGE,"E1.bottom"),sQuery(id+"F0.wireOp",EDGE,"E1.top"),sQuery(id+"F0.wireOp",EDGE,"E1.left"),sQuery(id+"F0.wireOp",EDGE,"E1.right")])]}),"instanceName":"1"}),"instanceName":"1"}),"instanceName":"1"}),"instanceName":"1"}),"instanceName":"1"});
            var Q349;
            Q349=makeQuery(id+"F11.opPattern","COPY",BODY,{"derivedFrom":makeQuery(id+"F8.opPattern","COPY",BODY,{"derivedFrom":makeQuery(id+"F7.opPattern","COPY",BODY,{"derivedFrom":makeQuery(id+"F3.opPattern","COPY",BODY,{"derivedFrom":makeQuery(id+"F2.opPattern","COPY",BODY,{"derivedFrom":makeQuery(id+"F1.opExtrude","SWEPT_BODY",BODY,{"disambiguationData":[OSD([sQuery(id+"F0.wireOp",EDGE,"E2.bottom"),sQuery(id+"F0.wireOp",EDGE,"E2.top"),sQuery(id+"F0.wireOp",EDGE,"E2.left"),sQuery(id+"F0.wireOp",EDGE,"E2.right")])]}),"instanceName":"1"}),"instanceName":"1"}),"instanceName":"1"}),"instanceName":"1"}),"instanceName":"1"});
            var Q350;
            Q350=makeQuery(id+"F11.opPattern","COPY",BODY,{"derivedFrom":makeQuery(id+"F8.opPattern","COPY",BODY,{"derivedFrom":makeQuery(id+"F7.opPattern","COPY",BODY,{"derivedFrom":makeQuery(id+"F4.opPattern","COPY",BODY,{"derivedFrom":makeQuery(id+"F3.opPattern","COPY",BODY,{"derivedFrom":makeQuery(id+"F2.opPattern","COPY",BODY,{"derivedFrom":makeQuery(id+"F1.opExtrude","SWEPT_BODY",BODY,{"disambiguationData":[OSD([sQuery(id+"F0.wireOp",EDGE,"E0.bottom"),sQuery(id+"F0.wireOp",EDGE,"E0.top"),sQuery(id+"F0.wireOp",EDGE,"E0.left"),sQuery(id+"F0.wireOp",EDGE,"E0.right")])]}),"instanceName":"1"}),"instanceName":"1"}),"instanceName":"1"}),"instanceName":"1"}),"instanceName":"1"}),"instanceName":"1"});
            var Q351;
            Q351=makeQuery(id+"F11.opPattern","COPY",BODY,{"derivedFrom":makeQuery(id+"F8.opPattern","COPY",BODY,{"derivedFrom":makeQuery(id+"F7.opPattern","COPY",BODY,{"derivedFrom":makeQuery(id+"F4.opPattern","COPY",BODY,{"derivedFrom":makeQuery(id+"F3.opPattern","COPY",BODY,{"derivedFrom":makeQuery(id+"F2.opPattern","COPY",BODY,{"derivedFrom":makeQuery(id+"F1.opExtrude","SWEPT_BODY",BODY,{"disambiguationData":[OSD([sQuery(id+"F0.wireOp",EDGE,"E1.bottom"),sQuery(id+"F0.wireOp",EDGE,"E1.top"),sQuery(id+"F0.wireOp",EDGE,"E1.left"),sQuery(id+"F0.wireOp",EDGE,"E1.right")])]}),"instanceName":"1"}),"instanceName":"1"}),"instanceName":"1"}),"instanceName":"1"}),"instanceName":"1"}),"instanceName":"1"});
            var Q352;
            Q352=makeQuery(id+"F11.opPattern","COPY",BODY,{"derivedFrom":makeQuery(id+"F8.opPattern","COPY",BODY,{"derivedFrom":makeQuery(id+"F7.opPattern","COPY",BODY,{"derivedFrom":makeQuery(id+"F4.opPattern","COPY",BODY,{"derivedFrom":makeQuery(id+"F3.opPattern","COPY",BODY,{"derivedFrom":makeQuery(id+"F2.opPattern","COPY",BODY,{"derivedFrom":makeQuery(id+"F1.opExtrude","SWEPT_BODY",BODY,{"disambiguationData":[OSD([sQuery(id+"F0.wireOp",EDGE,"E2.bottom"),sQuery(id+"F0.wireOp",EDGE,"E2.top"),sQuery(id+"F0.wireOp",EDGE,"E2.left"),sQuery(id+"F0.wireOp",EDGE,"E2.right")])]}),"instanceName":"1"}),"instanceName":"1"}),"instanceName":"1"}),"instanceName":"1"}),"instanceName":"1"}),"instanceName":"1"});
            var Q353;
            Q353=makeQuery(id+"F11.opPattern","COPY",BODY,{"derivedFrom":makeQuery(id+"F8.opPattern","COPY",BODY,{"derivedFrom":makeQuery(id+"F7.opPattern","COPY",BODY,{"derivedFrom":makeQuery(id+"F5.opPattern","COPY",BODY,{"derivedFrom":makeQuery(id+"F4.opPattern","COPY",BODY,{"derivedFrom":makeQuery(id+"F3.opPattern","COPY",BODY,{"derivedFrom":makeQuery(id+"F2.opPattern","COPY",BODY,{"derivedFrom":makeQuery(id+"F1.opExtrude","SWEPT_BODY",BODY,{"disambiguationData":[OSD([sQuery(id+"F0.wireOp",EDGE,"E0.bottom"),sQuery(id+"F0.wireOp",EDGE,"E0.top"),sQuery(id+"F0.wireOp",EDGE,"E0.left"),sQuery(id+"F0.wireOp",EDGE,"E0.right")])]}),"instanceName":"1"}),"instanceName":"1"}),"instanceName":"1"}),"instanceName":"1"}),"instanceName":"1"}),"instanceName":"1"}),"instanceName":"1"});
            var Q354;
            Q354=makeQuery(id+"F11.opPattern","COPY",BODY,{"derivedFrom":makeQuery(id+"F8.opPattern","COPY",BODY,{"derivedFrom":makeQuery(id+"F7.opPattern","COPY",BODY,{"derivedFrom":makeQuery(id+"F5.opPattern","COPY",BODY,{"derivedFrom":makeQuery(id+"F4.opPattern","COPY",BODY,{"derivedFrom":makeQuery(id+"F3.opPattern","COPY",BODY,{"derivedFrom":makeQuery(id+"F2.opPattern","COPY",BODY,{"derivedFrom":makeQuery(id+"F1.opExtrude","SWEPT_BODY",BODY,{"disambiguationData":[OSD([sQuery(id+"F0.wireOp",EDGE,"E1.bottom"),sQuery(id+"F0.wireOp",EDGE,"E1.top"),sQuery(id+"F0.wireOp",EDGE,"E1.left"),sQuery(id+"F0.wireOp",EDGE,"E1.right")])]}),"instanceName":"1"}),"instanceName":"1"}),"instanceName":"1"}),"instanceName":"1"}),"instanceName":"1"}),"instanceName":"1"}),"instanceName":"1"});
            var Q355;
            Q355=makeQuery(id+"F11.opPattern","COPY",BODY,{"derivedFrom":makeQuery(id+"F8.opPattern","COPY",BODY,{"derivedFrom":makeQuery(id+"F7.opPattern","COPY",BODY,{"derivedFrom":makeQuery(id+"F5.opPattern","COPY",BODY,{"derivedFrom":makeQuery(id+"F4.opPattern","COPY",BODY,{"derivedFrom":makeQuery(id+"F3.opPattern","COPY",BODY,{"derivedFrom":makeQuery(id+"F2.opPattern","COPY",BODY,{"derivedFrom":makeQuery(id+"F1.opExtrude","SWEPT_BODY",BODY,{"disambiguationData":[OSD([sQuery(id+"F0.wireOp",EDGE,"E2.bottom"),sQuery(id+"F0.wireOp",EDGE,"E2.top"),sQuery(id+"F0.wireOp",EDGE,"E2.left"),sQuery(id+"F0.wireOp",EDGE,"E2.right")])]}),"instanceName":"1"}),"instanceName":"1"}),"instanceName":"1"}),"instanceName":"1"}),"instanceName":"1"}),"instanceName":"1"}),"instanceName":"1"});
            var Q356;
            Q356=makeQuery(id+"F11.opPattern","COPY",BODY,{"derivedFrom":makeQuery(id+"F8.opPattern","COPY",BODY,{"derivedFrom":makeQuery(id+"F7.opPattern","COPY",BODY,{"derivedFrom":makeQuery(id+"F6.opPattern","COPY",BODY,{"derivedFrom":makeQuery(id+"F5.opPattern","COPY",BODY,{"derivedFrom":makeQuery(id+"F4.opPattern","COPY",BODY,{"derivedFrom":makeQuery(id+"F3.opPattern","COPY",BODY,{"derivedFrom":makeQuery(id+"F2.opPattern","COPY",BODY,{"derivedFrom":makeQuery(id+"F1.opExtrude","SWEPT_BODY",BODY,{"disambiguationData":[OSD([sQuery(id+"F0.wireOp",EDGE,"E0.bottom"),sQuery(id+"F0.wireOp",EDGE,"E0.top"),sQuery(id+"F0.wireOp",EDGE,"E0.left"),sQuery(id+"F0.wireOp",EDGE,"E0.right")])]}),"instanceName":"1"}),"instanceName":"1"}),"instanceName":"1"}),"instanceName":"1"}),"instanceName":"1"}),"instanceName":"1"}),"instanceName":"1"}),"instanceName":"1"});
            var Q357;
            Q357=makeQuery(id+"F11.opPattern","COPY",BODY,{"derivedFrom":makeQuery(id+"F8.opPattern","COPY",BODY,{"derivedFrom":makeQuery(id+"F7.opPattern","COPY",BODY,{"derivedFrom":makeQuery(id+"F6.opPattern","COPY",BODY,{"derivedFrom":makeQuery(id+"F5.opPattern","COPY",BODY,{"derivedFrom":makeQuery(id+"F4.opPattern","COPY",BODY,{"derivedFrom":makeQuery(id+"F3.opPattern","COPY",BODY,{"derivedFrom":makeQuery(id+"F2.opPattern","COPY",BODY,{"derivedFrom":makeQuery(id+"F1.opExtrude","SWEPT_BODY",BODY,{"disambiguationData":[OSD([sQuery(id+"F0.wireOp",EDGE,"E1.bottom"),sQuery(id+"F0.wireOp",EDGE,"E1.top"),sQuery(id+"F0.wireOp",EDGE,"E1.left"),sQuery(id+"F0.wireOp",EDGE,"E1.right")])]}),"instanceName":"1"}),"instanceName":"1"}),"instanceName":"1"}),"instanceName":"1"}),"instanceName":"1"}),"instanceName":"1"}),"instanceName":"1"}),"instanceName":"1"});
            var Q358;
            Q358=makeQuery(id+"F11.opPattern","COPY",BODY,{"derivedFrom":makeQuery(id+"F8.opPattern","COPY",BODY,{"derivedFrom":makeQuery(id+"F7.opPattern","COPY",BODY,{"derivedFrom":makeQuery(id+"F6.opPattern","COPY",BODY,{"derivedFrom":makeQuery(id+"F5.opPattern","COPY",BODY,{"derivedFrom":makeQuery(id+"F4.opPattern","COPY",BODY,{"derivedFrom":makeQuery(id+"F3.opPattern","COPY",BODY,{"derivedFrom":makeQuery(id+"F2.opPattern","COPY",BODY,{"derivedFrom":makeQuery(id+"F1.opExtrude","SWEPT_BODY",BODY,{"disambiguationData":[OSD([sQuery(id+"F0.wireOp",EDGE,"E2.bottom"),sQuery(id+"F0.wireOp",EDGE,"E2.top"),sQuery(id+"F0.wireOp",EDGE,"E2.left"),sQuery(id+"F0.wireOp",EDGE,"E2.right")])]}),"instanceName":"1"}),"instanceName":"1"}),"instanceName":"1"}),"instanceName":"1"}),"instanceName":"1"}),"instanceName":"1"}),"instanceName":"1"}),"instanceName":"1"});
            var Q359;
            Q359=makeQuery(id+"F11.opPattern","COPY",BODY,{"derivedFrom":makeQuery(id+"F9.opPattern","COPY",BODY,{"derivedFrom":makeQuery(id+"F1.opExtrude","SWEPT_BODY",BODY,{"disambiguationData":[OSD([sQuery(id+"F0.wireOp",EDGE,"E0.bottom"),sQuery(id+"F0.wireOp",EDGE,"E0.top"),sQuery(id+"F0.wireOp",EDGE,"E0.left"),sQuery(id+"F0.wireOp",EDGE,"E0.right")])]}),"instanceName":"1"}),"instanceName":"1"});
            var Q360;
            Q360=makeQuery(id+"F11.opPattern","COPY",BODY,{"derivedFrom":makeQuery(id+"F9.opPattern","COPY",BODY,{"derivedFrom":makeQuery(id+"F1.opExtrude","SWEPT_BODY",BODY,{"disambiguationData":[OSD([sQuery(id+"F0.wireOp",EDGE,"E1.bottom"),sQuery(id+"F0.wireOp",EDGE,"E1.top"),sQuery(id+"F0.wireOp",EDGE,"E1.left"),sQuery(id+"F0.wireOp",EDGE,"E1.right")])]}),"instanceName":"1"}),"instanceName":"1"});
            var Q361;
            Q361=makeQuery(id+"F11.opPattern","COPY",BODY,{"derivedFrom":makeQuery(id+"F9.opPattern","COPY",BODY,{"derivedFrom":makeQuery(id+"F1.opExtrude","SWEPT_BODY",BODY,{"disambiguationData":[OSD([sQuery(id+"F0.wireOp",EDGE,"E2.bottom"),sQuery(id+"F0.wireOp",EDGE,"E2.top"),sQuery(id+"F0.wireOp",EDGE,"E2.left"),sQuery(id+"F0.wireOp",EDGE,"E2.right")])]}),"instanceName":"1"}),"instanceName":"1"});
            var Q362;
            Q362=makeQuery(id+"F11.opPattern","COPY",BODY,{"derivedFrom":makeQuery(id+"F9.opPattern","COPY",BODY,{"derivedFrom":makeQuery(id+"F2.opPattern","COPY",BODY,{"derivedFrom":makeQuery(id+"F1.opExtrude","SWEPT_BODY",BODY,{"disambiguationData":[OSD([sQuery(id+"F0.wireOp",EDGE,"E0.bottom"),sQuery(id+"F0.wireOp",EDGE,"E0.top"),sQuery(id+"F0.wireOp",EDGE,"E0.left"),sQuery(id+"F0.wireOp",EDGE,"E0.right")])]}),"instanceName":"1"}),"instanceName":"1"}),"instanceName":"1"});
            var Q363;
            Q363=makeQuery(id+"F11.opPattern","COPY",BODY,{"derivedFrom":makeQuery(id+"F9.opPattern","COPY",BODY,{"derivedFrom":makeQuery(id+"F2.opPattern","COPY",BODY,{"derivedFrom":makeQuery(id+"F1.opExtrude","SWEPT_BODY",BODY,{"disambiguationData":[OSD([sQuery(id+"F0.wireOp",EDGE,"E1.bottom"),sQuery(id+"F0.wireOp",EDGE,"E1.top"),sQuery(id+"F0.wireOp",EDGE,"E1.left"),sQuery(id+"F0.wireOp",EDGE,"E1.right")])]}),"instanceName":"1"}),"instanceName":"1"}),"instanceName":"1"});
            var Q364;
            Q364=makeQuery(id+"F11.opPattern","COPY",BODY,{"derivedFrom":makeQuery(id+"F9.opPattern","COPY",BODY,{"derivedFrom":makeQuery(id+"F2.opPattern","COPY",BODY,{"derivedFrom":makeQuery(id+"F1.opExtrude","SWEPT_BODY",BODY,{"disambiguationData":[OSD([sQuery(id+"F0.wireOp",EDGE,"E2.bottom"),sQuery(id+"F0.wireOp",EDGE,"E2.top"),sQuery(id+"F0.wireOp",EDGE,"E2.left"),sQuery(id+"F0.wireOp",EDGE,"E2.right")])]}),"instanceName":"1"}),"instanceName":"1"}),"instanceName":"1"});
            var Q365;
            Q365=makeQuery(id+"F11.opPattern","COPY",BODY,{"derivedFrom":makeQuery(id+"F9.opPattern","COPY",BODY,{"derivedFrom":makeQuery(id+"F3.opPattern","COPY",BODY,{"derivedFrom":makeQuery(id+"F2.opPattern","COPY",BODY,{"derivedFrom":makeQuery(id+"F1.opExtrude","SWEPT_BODY",BODY,{"disambiguationData":[OSD([sQuery(id+"F0.wireOp",EDGE,"E0.bottom"),sQuery(id+"F0.wireOp",EDGE,"E0.top"),sQuery(id+"F0.wireOp",EDGE,"E0.left"),sQuery(id+"F0.wireOp",EDGE,"E0.right")])]}),"instanceName":"1"}),"instanceName":"1"}),"instanceName":"1"}),"instanceName":"1"});
            var Q366;
            Q366=makeQuery(id+"F11.opPattern","COPY",BODY,{"derivedFrom":makeQuery(id+"F9.opPattern","COPY",BODY,{"derivedFrom":makeQuery(id+"F3.opPattern","COPY",BODY,{"derivedFrom":makeQuery(id+"F2.opPattern","COPY",BODY,{"derivedFrom":makeQuery(id+"F1.opExtrude","SWEPT_BODY",BODY,{"disambiguationData":[OSD([sQuery(id+"F0.wireOp",EDGE,"E1.bottom"),sQuery(id+"F0.wireOp",EDGE,"E1.top"),sQuery(id+"F0.wireOp",EDGE,"E1.left"),sQuery(id+"F0.wireOp",EDGE,"E1.right")])]}),"instanceName":"1"}),"instanceName":"1"}),"instanceName":"1"}),"instanceName":"1"});
            var Q367;
            Q367=makeQuery(id+"F11.opPattern","COPY",BODY,{"derivedFrom":makeQuery(id+"F9.opPattern","COPY",BODY,{"derivedFrom":makeQuery(id+"F3.opPattern","COPY",BODY,{"derivedFrom":makeQuery(id+"F2.opPattern","COPY",BODY,{"derivedFrom":makeQuery(id+"F1.opExtrude","SWEPT_BODY",BODY,{"disambiguationData":[OSD([sQuery(id+"F0.wireOp",EDGE,"E2.bottom"),sQuery(id+"F0.wireOp",EDGE,"E2.top"),sQuery(id+"F0.wireOp",EDGE,"E2.left"),sQuery(id+"F0.wireOp",EDGE,"E2.right")])]}),"instanceName":"1"}),"instanceName":"1"}),"instanceName":"1"}),"instanceName":"1"});
            var Q368;
            Q368=makeQuery(id+"F11.opPattern","COPY",BODY,{"derivedFrom":makeQuery(id+"F9.opPattern","COPY",BODY,{"derivedFrom":makeQuery(id+"F4.opPattern","COPY",BODY,{"derivedFrom":makeQuery(id+"F3.opPattern","COPY",BODY,{"derivedFrom":makeQuery(id+"F2.opPattern","COPY",BODY,{"derivedFrom":makeQuery(id+"F1.opExtrude","SWEPT_BODY",BODY,{"disambiguationData":[OSD([sQuery(id+"F0.wireOp",EDGE,"E0.bottom"),sQuery(id+"F0.wireOp",EDGE,"E0.top"),sQuery(id+"F0.wireOp",EDGE,"E0.left"),sQuery(id+"F0.wireOp",EDGE,"E0.right")])]}),"instanceName":"1"}),"instanceName":"1"}),"instanceName":"1"}),"instanceName":"1"}),"instanceName":"1"});
            var Q369;
            Q369=makeQuery(id+"F11.opPattern","COPY",BODY,{"derivedFrom":makeQuery(id+"F9.opPattern","COPY",BODY,{"derivedFrom":makeQuery(id+"F4.opPattern","COPY",BODY,{"derivedFrom":makeQuery(id+"F3.opPattern","COPY",BODY,{"derivedFrom":makeQuery(id+"F2.opPattern","COPY",BODY,{"derivedFrom":makeQuery(id+"F1.opExtrude","SWEPT_BODY",BODY,{"disambiguationData":[OSD([sQuery(id+"F0.wireOp",EDGE,"E1.bottom"),sQuery(id+"F0.wireOp",EDGE,"E1.top"),sQuery(id+"F0.wireOp",EDGE,"E1.left"),sQuery(id+"F0.wireOp",EDGE,"E1.right")])]}),"instanceName":"1"}),"instanceName":"1"}),"instanceName":"1"}),"instanceName":"1"}),"instanceName":"1"});
            var Q370;
            Q370=makeQuery(id+"F11.opPattern","COPY",BODY,{"derivedFrom":makeQuery(id+"F9.opPattern","COPY",BODY,{"derivedFrom":makeQuery(id+"F4.opPattern","COPY",BODY,{"derivedFrom":makeQuery(id+"F3.opPattern","COPY",BODY,{"derivedFrom":makeQuery(id+"F2.opPattern","COPY",BODY,{"derivedFrom":makeQuery(id+"F1.opExtrude","SWEPT_BODY",BODY,{"disambiguationData":[OSD([sQuery(id+"F0.wireOp",EDGE,"E2.bottom"),sQuery(id+"F0.wireOp",EDGE,"E2.top"),sQuery(id+"F0.wireOp",EDGE,"E2.left"),sQuery(id+"F0.wireOp",EDGE,"E2.right")])]}),"instanceName":"1"}),"instanceName":"1"}),"instanceName":"1"}),"instanceName":"1"}),"instanceName":"1"});
            var Q371;
            Q371=makeQuery(id+"F11.opPattern","COPY",BODY,{"derivedFrom":makeQuery(id+"F9.opPattern","COPY",BODY,{"derivedFrom":makeQuery(id+"F5.opPattern","COPY",BODY,{"derivedFrom":makeQuery(id+"F4.opPattern","COPY",BODY,{"derivedFrom":makeQuery(id+"F3.opPattern","COPY",BODY,{"derivedFrom":makeQuery(id+"F2.opPattern","COPY",BODY,{"derivedFrom":makeQuery(id+"F1.opExtrude","SWEPT_BODY",BODY,{"disambiguationData":[OSD([sQuery(id+"F0.wireOp",EDGE,"E0.bottom"),sQuery(id+"F0.wireOp",EDGE,"E0.top"),sQuery(id+"F0.wireOp",EDGE,"E0.left"),sQuery(id+"F0.wireOp",EDGE,"E0.right")])]}),"instanceName":"1"}),"instanceName":"1"}),"instanceName":"1"}),"instanceName":"1"}),"instanceName":"1"}),"instanceName":"1"});
            var Q372;
            Q372=makeQuery(id+"F11.opPattern","COPY",BODY,{"derivedFrom":makeQuery(id+"F9.opPattern","COPY",BODY,{"derivedFrom":makeQuery(id+"F5.opPattern","COPY",BODY,{"derivedFrom":makeQuery(id+"F4.opPattern","COPY",BODY,{"derivedFrom":makeQuery(id+"F3.opPattern","COPY",BODY,{"derivedFrom":makeQuery(id+"F2.opPattern","COPY",BODY,{"derivedFrom":makeQuery(id+"F1.opExtrude","SWEPT_BODY",BODY,{"disambiguationData":[OSD([sQuery(id+"F0.wireOp",EDGE,"E1.bottom"),sQuery(id+"F0.wireOp",EDGE,"E1.top"),sQuery(id+"F0.wireOp",EDGE,"E1.left"),sQuery(id+"F0.wireOp",EDGE,"E1.right")])]}),"instanceName":"1"}),"instanceName":"1"}),"instanceName":"1"}),"instanceName":"1"}),"instanceName":"1"}),"instanceName":"1"});
            var Q373;
            Q373=makeQuery(id+"F11.opPattern","COPY",BODY,{"derivedFrom":makeQuery(id+"F9.opPattern","COPY",BODY,{"derivedFrom":makeQuery(id+"F5.opPattern","COPY",BODY,{"derivedFrom":makeQuery(id+"F4.opPattern","COPY",BODY,{"derivedFrom":makeQuery(id+"F3.opPattern","COPY",BODY,{"derivedFrom":makeQuery(id+"F2.opPattern","COPY",BODY,{"derivedFrom":makeQuery(id+"F1.opExtrude","SWEPT_BODY",BODY,{"disambiguationData":[OSD([sQuery(id+"F0.wireOp",EDGE,"E2.bottom"),sQuery(id+"F0.wireOp",EDGE,"E2.top"),sQuery(id+"F0.wireOp",EDGE,"E2.left"),sQuery(id+"F0.wireOp",EDGE,"E2.right")])]}),"instanceName":"1"}),"instanceName":"1"}),"instanceName":"1"}),"instanceName":"1"}),"instanceName":"1"}),"instanceName":"1"});
            var Q374;
            Q374=makeQuery(id+"F11.opPattern","COPY",BODY,{"derivedFrom":makeQuery(id+"F9.opPattern","COPY",BODY,{"derivedFrom":makeQuery(id+"F6.opPattern","COPY",BODY,{"derivedFrom":makeQuery(id+"F5.opPattern","COPY",BODY,{"derivedFrom":makeQuery(id+"F4.opPattern","COPY",BODY,{"derivedFrom":makeQuery(id+"F3.opPattern","COPY",BODY,{"derivedFrom":makeQuery(id+"F2.opPattern","COPY",BODY,{"derivedFrom":makeQuery(id+"F1.opExtrude","SWEPT_BODY",BODY,{"disambiguationData":[OSD([sQuery(id+"F0.wireOp",EDGE,"E0.bottom"),sQuery(id+"F0.wireOp",EDGE,"E0.top"),sQuery(id+"F0.wireOp",EDGE,"E0.left"),sQuery(id+"F0.wireOp",EDGE,"E0.right")])]}),"instanceName":"1"}),"instanceName":"1"}),"instanceName":"1"}),"instanceName":"1"}),"instanceName":"1"}),"instanceName":"1"}),"instanceName":"1"});
            var Q375;
            Q375=makeQuery(id+"F11.opPattern","COPY",BODY,{"derivedFrom":makeQuery(id+"F9.opPattern","COPY",BODY,{"derivedFrom":makeQuery(id+"F6.opPattern","COPY",BODY,{"derivedFrom":makeQuery(id+"F5.opPattern","COPY",BODY,{"derivedFrom":makeQuery(id+"F4.opPattern","COPY",BODY,{"derivedFrom":makeQuery(id+"F3.opPattern","COPY",BODY,{"derivedFrom":makeQuery(id+"F2.opPattern","COPY",BODY,{"derivedFrom":makeQuery(id+"F1.opExtrude","SWEPT_BODY",BODY,{"disambiguationData":[OSD([sQuery(id+"F0.wireOp",EDGE,"E1.bottom"),sQuery(id+"F0.wireOp",EDGE,"E1.top"),sQuery(id+"F0.wireOp",EDGE,"E1.left"),sQuery(id+"F0.wireOp",EDGE,"E1.right")])]}),"instanceName":"1"}),"instanceName":"1"}),"instanceName":"1"}),"instanceName":"1"}),"instanceName":"1"}),"instanceName":"1"}),"instanceName":"1"});
            var Q376;
            Q376=makeQuery(id+"F11.opPattern","COPY",BODY,{"derivedFrom":makeQuery(id+"F9.opPattern","COPY",BODY,{"derivedFrom":makeQuery(id+"F6.opPattern","COPY",BODY,{"derivedFrom":makeQuery(id+"F5.opPattern","COPY",BODY,{"derivedFrom":makeQuery(id+"F4.opPattern","COPY",BODY,{"derivedFrom":makeQuery(id+"F3.opPattern","COPY",BODY,{"derivedFrom":makeQuery(id+"F2.opPattern","COPY",BODY,{"derivedFrom":makeQuery(id+"F1.opExtrude","SWEPT_BODY",BODY,{"disambiguationData":[OSD([sQuery(id+"F0.wireOp",EDGE,"E2.bottom"),sQuery(id+"F0.wireOp",EDGE,"E2.top"),sQuery(id+"F0.wireOp",EDGE,"E2.left"),sQuery(id+"F0.wireOp",EDGE,"E2.right")])]}),"instanceName":"1"}),"instanceName":"1"}),"instanceName":"1"}),"instanceName":"1"}),"instanceName":"1"}),"instanceName":"1"}),"instanceName":"1"});
            var Q377;
            Q377=makeQuery(id+"F11.opPattern","COPY",BODY,{"derivedFrom":makeQuery(id+"F9.opPattern","COPY",BODY,{"derivedFrom":makeQuery(id+"F7.opPattern","COPY",BODY,{"derivedFrom":makeQuery(id+"F1.opExtrude","SWEPT_BODY",BODY,{"disambiguationData":[OSD([sQuery(id+"F0.wireOp",EDGE,"E0.bottom"),sQuery(id+"F0.wireOp",EDGE,"E0.top"),sQuery(id+"F0.wireOp",EDGE,"E0.left"),sQuery(id+"F0.wireOp",EDGE,"E0.right")])]}),"instanceName":"1"}),"instanceName":"1"}),"instanceName":"1"});
            var Q378;
            Q378=makeQuery(id+"F11.opPattern","COPY",BODY,{"derivedFrom":makeQuery(id+"F9.opPattern","COPY",BODY,{"derivedFrom":makeQuery(id+"F7.opPattern","COPY",BODY,{"derivedFrom":makeQuery(id+"F1.opExtrude","SWEPT_BODY",BODY,{"disambiguationData":[OSD([sQuery(id+"F0.wireOp",EDGE,"E1.bottom"),sQuery(id+"F0.wireOp",EDGE,"E1.top"),sQuery(id+"F0.wireOp",EDGE,"E1.left"),sQuery(id+"F0.wireOp",EDGE,"E1.right")])]}),"instanceName":"1"}),"instanceName":"1"}),"instanceName":"1"});
            var Q379;
            Q379=makeQuery(id+"F11.opPattern","COPY",BODY,{"derivedFrom":makeQuery(id+"F9.opPattern","COPY",BODY,{"derivedFrom":makeQuery(id+"F7.opPattern","COPY",BODY,{"derivedFrom":makeQuery(id+"F1.opExtrude","SWEPT_BODY",BODY,{"disambiguationData":[OSD([sQuery(id+"F0.wireOp",EDGE,"E2.bottom"),sQuery(id+"F0.wireOp",EDGE,"E2.top"),sQuery(id+"F0.wireOp",EDGE,"E2.left"),sQuery(id+"F0.wireOp",EDGE,"E2.right")])]}),"instanceName":"1"}),"instanceName":"1"}),"instanceName":"1"});
            var Q380;
            Q380=makeQuery(id+"F11.opPattern","COPY",BODY,{"derivedFrom":makeQuery(id+"F9.opPattern","COPY",BODY,{"derivedFrom":makeQuery(id+"F7.opPattern","COPY",BODY,{"derivedFrom":makeQuery(id+"F2.opPattern","COPY",BODY,{"derivedFrom":makeQuery(id+"F1.opExtrude","SWEPT_BODY",BODY,{"disambiguationData":[OSD([sQuery(id+"F0.wireOp",EDGE,"E0.bottom"),sQuery(id+"F0.wireOp",EDGE,"E0.top"),sQuery(id+"F0.wireOp",EDGE,"E0.left"),sQuery(id+"F0.wireOp",EDGE,"E0.right")])]}),"instanceName":"1"}),"instanceName":"1"}),"instanceName":"1"}),"instanceName":"1"});
            var Q381;
            Q381=makeQuery(id+"F11.opPattern","COPY",BODY,{"derivedFrom":makeQuery(id+"F9.opPattern","COPY",BODY,{"derivedFrom":makeQuery(id+"F7.opPattern","COPY",BODY,{"derivedFrom":makeQuery(id+"F2.opPattern","COPY",BODY,{"derivedFrom":makeQuery(id+"F1.opExtrude","SWEPT_BODY",BODY,{"disambiguationData":[OSD([sQuery(id+"F0.wireOp",EDGE,"E1.bottom"),sQuery(id+"F0.wireOp",EDGE,"E1.top"),sQuery(id+"F0.wireOp",EDGE,"E1.left"),sQuery(id+"F0.wireOp",EDGE,"E1.right")])]}),"instanceName":"1"}),"instanceName":"1"}),"instanceName":"1"}),"instanceName":"1"});
            var Q382;
            Q382=makeQuery(id+"F11.opPattern","COPY",BODY,{"derivedFrom":makeQuery(id+"F9.opPattern","COPY",BODY,{"derivedFrom":makeQuery(id+"F7.opPattern","COPY",BODY,{"derivedFrom":makeQuery(id+"F2.opPattern","COPY",BODY,{"derivedFrom":makeQuery(id+"F1.opExtrude","SWEPT_BODY",BODY,{"disambiguationData":[OSD([sQuery(id+"F0.wireOp",EDGE,"E2.bottom"),sQuery(id+"F0.wireOp",EDGE,"E2.top"),sQuery(id+"F0.wireOp",EDGE,"E2.left"),sQuery(id+"F0.wireOp",EDGE,"E2.right")])]}),"instanceName":"1"}),"instanceName":"1"}),"instanceName":"1"}),"instanceName":"1"});
            var Q383;
            Q383=makeQuery(id+"F11.opPattern","COPY",BODY,{"derivedFrom":makeQuery(id+"F9.opPattern","COPY",BODY,{"derivedFrom":makeQuery(id+"F7.opPattern","COPY",BODY,{"derivedFrom":makeQuery(id+"F3.opPattern","COPY",BODY,{"derivedFrom":makeQuery(id+"F2.opPattern","COPY",BODY,{"derivedFrom":makeQuery(id+"F1.opExtrude","SWEPT_BODY",BODY,{"disambiguationData":[OSD([sQuery(id+"F0.wireOp",EDGE,"E0.bottom"),sQuery(id+"F0.wireOp",EDGE,"E0.top"),sQuery(id+"F0.wireOp",EDGE,"E0.left"),sQuery(id+"F0.wireOp",EDGE,"E0.right")])]}),"instanceName":"1"}),"instanceName":"1"}),"instanceName":"1"}),"instanceName":"1"}),"instanceName":"1"});
            var Q384;
            Q384=makeQuery(id+"F11.opPattern","COPY",BODY,{"derivedFrom":makeQuery(id+"F9.opPattern","COPY",BODY,{"derivedFrom":makeQuery(id+"F7.opPattern","COPY",BODY,{"derivedFrom":makeQuery(id+"F3.opPattern","COPY",BODY,{"derivedFrom":makeQuery(id+"F2.opPattern","COPY",BODY,{"derivedFrom":makeQuery(id+"F1.opExtrude","SWEPT_BODY",BODY,{"disambiguationData":[OSD([sQuery(id+"F0.wireOp",EDGE,"E1.bottom"),sQuery(id+"F0.wireOp",EDGE,"E1.top"),sQuery(id+"F0.wireOp",EDGE,"E1.left"),sQuery(id+"F0.wireOp",EDGE,"E1.right")])]}),"instanceName":"1"}),"instanceName":"1"}),"instanceName":"1"}),"instanceName":"1"}),"instanceName":"1"});
            var Q385;
            Q385=makeQuery(id+"F11.opPattern","COPY",BODY,{"derivedFrom":makeQuery(id+"F9.opPattern","COPY",BODY,{"derivedFrom":makeQuery(id+"F7.opPattern","COPY",BODY,{"derivedFrom":makeQuery(id+"F3.opPattern","COPY",BODY,{"derivedFrom":makeQuery(id+"F2.opPattern","COPY",BODY,{"derivedFrom":makeQuery(id+"F1.opExtrude","SWEPT_BODY",BODY,{"disambiguationData":[OSD([sQuery(id+"F0.wireOp",EDGE,"E2.bottom"),sQuery(id+"F0.wireOp",EDGE,"E2.top"),sQuery(id+"F0.wireOp",EDGE,"E2.left"),sQuery(id+"F0.wireOp",EDGE,"E2.right")])]}),"instanceName":"1"}),"instanceName":"1"}),"instanceName":"1"}),"instanceName":"1"}),"instanceName":"1"});
            var Q386;
            Q386=makeQuery(id+"F11.opPattern","COPY",BODY,{"derivedFrom":makeQuery(id+"F9.opPattern","COPY",BODY,{"derivedFrom":makeQuery(id+"F7.opPattern","COPY",BODY,{"derivedFrom":makeQuery(id+"F4.opPattern","COPY",BODY,{"derivedFrom":makeQuery(id+"F3.opPattern","COPY",BODY,{"derivedFrom":makeQuery(id+"F2.opPattern","COPY",BODY,{"derivedFrom":makeQuery(id+"F1.opExtrude","SWEPT_BODY",BODY,{"disambiguationData":[OSD([sQuery(id+"F0.wireOp",EDGE,"E0.bottom"),sQuery(id+"F0.wireOp",EDGE,"E0.top"),sQuery(id+"F0.wireOp",EDGE,"E0.left"),sQuery(id+"F0.wireOp",EDGE,"E0.right")])]}),"instanceName":"1"}),"instanceName":"1"}),"instanceName":"1"}),"instanceName":"1"}),"instanceName":"1"}),"instanceName":"1"});
            var Q387;
            Q387=makeQuery(id+"F11.opPattern","COPY",BODY,{"derivedFrom":makeQuery(id+"F9.opPattern","COPY",BODY,{"derivedFrom":makeQuery(id+"F7.opPattern","COPY",BODY,{"derivedFrom":makeQuery(id+"F4.opPattern","COPY",BODY,{"derivedFrom":makeQuery(id+"F3.opPattern","COPY",BODY,{"derivedFrom":makeQuery(id+"F2.opPattern","COPY",BODY,{"derivedFrom":makeQuery(id+"F1.opExtrude","SWEPT_BODY",BODY,{"disambiguationData":[OSD([sQuery(id+"F0.wireOp",EDGE,"E1.bottom"),sQuery(id+"F0.wireOp",EDGE,"E1.top"),sQuery(id+"F0.wireOp",EDGE,"E1.left"),sQuery(id+"F0.wireOp",EDGE,"E1.right")])]}),"instanceName":"1"}),"instanceName":"1"}),"instanceName":"1"}),"instanceName":"1"}),"instanceName":"1"}),"instanceName":"1"});
            var Q388;
            Q388=makeQuery(id+"F11.opPattern","COPY",BODY,{"derivedFrom":makeQuery(id+"F9.opPattern","COPY",BODY,{"derivedFrom":makeQuery(id+"F7.opPattern","COPY",BODY,{"derivedFrom":makeQuery(id+"F4.opPattern","COPY",BODY,{"derivedFrom":makeQuery(id+"F3.opPattern","COPY",BODY,{"derivedFrom":makeQuery(id+"F2.opPattern","COPY",BODY,{"derivedFrom":makeQuery(id+"F1.opExtrude","SWEPT_BODY",BODY,{"disambiguationData":[OSD([sQuery(id+"F0.wireOp",EDGE,"E2.bottom"),sQuery(id+"F0.wireOp",EDGE,"E2.top"),sQuery(id+"F0.wireOp",EDGE,"E2.left"),sQuery(id+"F0.wireOp",EDGE,"E2.right")])]}),"instanceName":"1"}),"instanceName":"1"}),"instanceName":"1"}),"instanceName":"1"}),"instanceName":"1"}),"instanceName":"1"});
            var Q389;
            Q389=makeQuery(id+"F11.opPattern","COPY",BODY,{"derivedFrom":makeQuery(id+"F9.opPattern","COPY",BODY,{"derivedFrom":makeQuery(id+"F7.opPattern","COPY",BODY,{"derivedFrom":makeQuery(id+"F5.opPattern","COPY",BODY,{"derivedFrom":makeQuery(id+"F4.opPattern","COPY",BODY,{"derivedFrom":makeQuery(id+"F3.opPattern","COPY",BODY,{"derivedFrom":makeQuery(id+"F2.opPattern","COPY",BODY,{"derivedFrom":makeQuery(id+"F1.opExtrude","SWEPT_BODY",BODY,{"disambiguationData":[OSD([sQuery(id+"F0.wireOp",EDGE,"E0.bottom"),sQuery(id+"F0.wireOp",EDGE,"E0.top"),sQuery(id+"F0.wireOp",EDGE,"E0.left"),sQuery(id+"F0.wireOp",EDGE,"E0.right")])]}),"instanceName":"1"}),"instanceName":"1"}),"instanceName":"1"}),"instanceName":"1"}),"instanceName":"1"}),"instanceName":"1"}),"instanceName":"1"});
            var Q390;
            Q390=makeQuery(id+"F11.opPattern","COPY",BODY,{"derivedFrom":makeQuery(id+"F9.opPattern","COPY",BODY,{"derivedFrom":makeQuery(id+"F7.opPattern","COPY",BODY,{"derivedFrom":makeQuery(id+"F5.opPattern","COPY",BODY,{"derivedFrom":makeQuery(id+"F4.opPattern","COPY",BODY,{"derivedFrom":makeQuery(id+"F3.opPattern","COPY",BODY,{"derivedFrom":makeQuery(id+"F2.opPattern","COPY",BODY,{"derivedFrom":makeQuery(id+"F1.opExtrude","SWEPT_BODY",BODY,{"disambiguationData":[OSD([sQuery(id+"F0.wireOp",EDGE,"E1.bottom"),sQuery(id+"F0.wireOp",EDGE,"E1.top"),sQuery(id+"F0.wireOp",EDGE,"E1.left"),sQuery(id+"F0.wireOp",EDGE,"E1.right")])]}),"instanceName":"1"}),"instanceName":"1"}),"instanceName":"1"}),"instanceName":"1"}),"instanceName":"1"}),"instanceName":"1"}),"instanceName":"1"});
            var Q391;
            Q391=makeQuery(id+"F11.opPattern","COPY",BODY,{"derivedFrom":makeQuery(id+"F9.opPattern","COPY",BODY,{"derivedFrom":makeQuery(id+"F7.opPattern","COPY",BODY,{"derivedFrom":makeQuery(id+"F5.opPattern","COPY",BODY,{"derivedFrom":makeQuery(id+"F4.opPattern","COPY",BODY,{"derivedFrom":makeQuery(id+"F3.opPattern","COPY",BODY,{"derivedFrom":makeQuery(id+"F2.opPattern","COPY",BODY,{"derivedFrom":makeQuery(id+"F1.opExtrude","SWEPT_BODY",BODY,{"disambiguationData":[OSD([sQuery(id+"F0.wireOp",EDGE,"E2.bottom"),sQuery(id+"F0.wireOp",EDGE,"E2.top"),sQuery(id+"F0.wireOp",EDGE,"E2.left"),sQuery(id+"F0.wireOp",EDGE,"E2.right")])]}),"instanceName":"1"}),"instanceName":"1"}),"instanceName":"1"}),"instanceName":"1"}),"instanceName":"1"}),"instanceName":"1"}),"instanceName":"1"});
            var Q392;
            Q392=makeQuery(id+"F11.opPattern","COPY",BODY,{"derivedFrom":makeQuery(id+"F9.opPattern","COPY",BODY,{"derivedFrom":makeQuery(id+"F7.opPattern","COPY",BODY,{"derivedFrom":makeQuery(id+"F6.opPattern","COPY",BODY,{"derivedFrom":makeQuery(id+"F5.opPattern","COPY",BODY,{"derivedFrom":makeQuery(id+"F4.opPattern","COPY",BODY,{"derivedFrom":makeQuery(id+"F3.opPattern","COPY",BODY,{"derivedFrom":makeQuery(id+"F2.opPattern","COPY",BODY,{"derivedFrom":makeQuery(id+"F1.opExtrude","SWEPT_BODY",BODY,{"disambiguationData":[OSD([sQuery(id+"F0.wireOp",EDGE,"E0.bottom"),sQuery(id+"F0.wireOp",EDGE,"E0.top"),sQuery(id+"F0.wireOp",EDGE,"E0.left"),sQuery(id+"F0.wireOp",EDGE,"E0.right")])]}),"instanceName":"1"}),"instanceName":"1"}),"instanceName":"1"}),"instanceName":"1"}),"instanceName":"1"}),"instanceName":"1"}),"instanceName":"1"}),"instanceName":"1"});
            var Q393;
            Q393=makeQuery(id+"F11.opPattern","COPY",BODY,{"derivedFrom":makeQuery(id+"F9.opPattern","COPY",BODY,{"derivedFrom":makeQuery(id+"F7.opPattern","COPY",BODY,{"derivedFrom":makeQuery(id+"F6.opPattern","COPY",BODY,{"derivedFrom":makeQuery(id+"F5.opPattern","COPY",BODY,{"derivedFrom":makeQuery(id+"F4.opPattern","COPY",BODY,{"derivedFrom":makeQuery(id+"F3.opPattern","COPY",BODY,{"derivedFrom":makeQuery(id+"F2.opPattern","COPY",BODY,{"derivedFrom":makeQuery(id+"F1.opExtrude","SWEPT_BODY",BODY,{"disambiguationData":[OSD([sQuery(id+"F0.wireOp",EDGE,"E1.bottom"),sQuery(id+"F0.wireOp",EDGE,"E1.top"),sQuery(id+"F0.wireOp",EDGE,"E1.left"),sQuery(id+"F0.wireOp",EDGE,"E1.right")])]}),"instanceName":"1"}),"instanceName":"1"}),"instanceName":"1"}),"instanceName":"1"}),"instanceName":"1"}),"instanceName":"1"}),"instanceName":"1"}),"instanceName":"1"});
            var Q394;
            Q394=makeQuery(id+"F11.opPattern","COPY",BODY,{"derivedFrom":makeQuery(id+"F9.opPattern","COPY",BODY,{"derivedFrom":makeQuery(id+"F7.opPattern","COPY",BODY,{"derivedFrom":makeQuery(id+"F6.opPattern","COPY",BODY,{"derivedFrom":makeQuery(id+"F5.opPattern","COPY",BODY,{"derivedFrom":makeQuery(id+"F4.opPattern","COPY",BODY,{"derivedFrom":makeQuery(id+"F3.opPattern","COPY",BODY,{"derivedFrom":makeQuery(id+"F2.opPattern","COPY",BODY,{"derivedFrom":makeQuery(id+"F1.opExtrude","SWEPT_BODY",BODY,{"disambiguationData":[OSD([sQuery(id+"F0.wireOp",EDGE,"E2.bottom"),sQuery(id+"F0.wireOp",EDGE,"E2.top"),sQuery(id+"F0.wireOp",EDGE,"E2.left"),sQuery(id+"F0.wireOp",EDGE,"E2.right")])]}),"instanceName":"1"}),"instanceName":"1"}),"instanceName":"1"}),"instanceName":"1"}),"instanceName":"1"}),"instanceName":"1"}),"instanceName":"1"}),"instanceName":"1"});
            var Q395;
            Q395=makeQuery(id+"F11.opPattern","COPY",BODY,{"derivedFrom":makeQuery(id+"F9.opPattern","COPY",BODY,{"derivedFrom":makeQuery(id+"F8.opPattern","COPY",BODY,{"derivedFrom":makeQuery(id+"F1.opExtrude","SWEPT_BODY",BODY,{"disambiguationData":[OSD([sQuery(id+"F0.wireOp",EDGE,"E0.bottom"),sQuery(id+"F0.wireOp",EDGE,"E0.top"),sQuery(id+"F0.wireOp",EDGE,"E0.left"),sQuery(id+"F0.wireOp",EDGE,"E0.right")])]}),"instanceName":"1"}),"instanceName":"1"}),"instanceName":"1"});
            var Q396;
            Q396=makeQuery(id+"F11.opPattern","COPY",BODY,{"derivedFrom":makeQuery(id+"F9.opPattern","COPY",BODY,{"derivedFrom":makeQuery(id+"F8.opPattern","COPY",BODY,{"derivedFrom":makeQuery(id+"F1.opExtrude","SWEPT_BODY",BODY,{"disambiguationData":[OSD([sQuery(id+"F0.wireOp",EDGE,"E1.bottom"),sQuery(id+"F0.wireOp",EDGE,"E1.top"),sQuery(id+"F0.wireOp",EDGE,"E1.left"),sQuery(id+"F0.wireOp",EDGE,"E1.right")])]}),"instanceName":"1"}),"instanceName":"1"}),"instanceName":"1"});
            var Q397;
            Q397=makeQuery(id+"F11.opPattern","COPY",BODY,{"derivedFrom":makeQuery(id+"F9.opPattern","COPY",BODY,{"derivedFrom":makeQuery(id+"F8.opPattern","COPY",BODY,{"derivedFrom":makeQuery(id+"F1.opExtrude","SWEPT_BODY",BODY,{"disambiguationData":[OSD([sQuery(id+"F0.wireOp",EDGE,"E2.bottom"),sQuery(id+"F0.wireOp",EDGE,"E2.top"),sQuery(id+"F0.wireOp",EDGE,"E2.left"),sQuery(id+"F0.wireOp",EDGE,"E2.right")])]}),"instanceName":"1"}),"instanceName":"1"}),"instanceName":"1"});
            var Q398;
            Q398=makeQuery(id+"F11.opPattern","COPY",BODY,{"derivedFrom":makeQuery(id+"F9.opPattern","COPY",BODY,{"derivedFrom":makeQuery(id+"F8.opPattern","COPY",BODY,{"derivedFrom":makeQuery(id+"F2.opPattern","COPY",BODY,{"derivedFrom":makeQuery(id+"F1.opExtrude","SWEPT_BODY",BODY,{"disambiguationData":[OSD([sQuery(id+"F0.wireOp",EDGE,"E0.bottom"),sQuery(id+"F0.wireOp",EDGE,"E0.top"),sQuery(id+"F0.wireOp",EDGE,"E0.left"),sQuery(id+"F0.wireOp",EDGE,"E0.right")])]}),"instanceName":"1"}),"instanceName":"1"}),"instanceName":"1"}),"instanceName":"1"});
            var Q399;
            Q399=makeQuery(id+"F11.opPattern","COPY",BODY,{"derivedFrom":makeQuery(id+"F9.opPattern","COPY",BODY,{"derivedFrom":makeQuery(id+"F8.opPattern","COPY",BODY,{"derivedFrom":makeQuery(id+"F2.opPattern","COPY",BODY,{"derivedFrom":makeQuery(id+"F1.opExtrude","SWEPT_BODY",BODY,{"disambiguationData":[OSD([sQuery(id+"F0.wireOp",EDGE,"E1.bottom"),sQuery(id+"F0.wireOp",EDGE,"E1.top"),sQuery(id+"F0.wireOp",EDGE,"E1.left"),sQuery(id+"F0.wireOp",EDGE,"E1.right")])]}),"instanceName":"1"}),"instanceName":"1"}),"instanceName":"1"}),"instanceName":"1"});
            var Q400;
            Q400=makeQuery(id+"F11.opPattern","COPY",BODY,{"derivedFrom":makeQuery(id+"F9.opPattern","COPY",BODY,{"derivedFrom":makeQuery(id+"F8.opPattern","COPY",BODY,{"derivedFrom":makeQuery(id+"F2.opPattern","COPY",BODY,{"derivedFrom":makeQuery(id+"F1.opExtrude","SWEPT_BODY",BODY,{"disambiguationData":[OSD([sQuery(id+"F0.wireOp",EDGE,"E2.bottom"),sQuery(id+"F0.wireOp",EDGE,"E2.top"),sQuery(id+"F0.wireOp",EDGE,"E2.left"),sQuery(id+"F0.wireOp",EDGE,"E2.right")])]}),"instanceName":"1"}),"instanceName":"1"}),"instanceName":"1"}),"instanceName":"1"});
            var Q401;
            Q401=makeQuery(id+"F11.opPattern","COPY",BODY,{"derivedFrom":makeQuery(id+"F9.opPattern","COPY",BODY,{"derivedFrom":makeQuery(id+"F8.opPattern","COPY",BODY,{"derivedFrom":makeQuery(id+"F3.opPattern","COPY",BODY,{"derivedFrom":makeQuery(id+"F2.opPattern","COPY",BODY,{"derivedFrom":makeQuery(id+"F1.opExtrude","SWEPT_BODY",BODY,{"disambiguationData":[OSD([sQuery(id+"F0.wireOp",EDGE,"E0.bottom"),sQuery(id+"F0.wireOp",EDGE,"E0.top"),sQuery(id+"F0.wireOp",EDGE,"E0.left"),sQuery(id+"F0.wireOp",EDGE,"E0.right")])]}),"instanceName":"1"}),"instanceName":"1"}),"instanceName":"1"}),"instanceName":"1"}),"instanceName":"1"});
            var Q402;
            Q402=makeQuery(id+"F11.opPattern","COPY",BODY,{"derivedFrom":makeQuery(id+"F9.opPattern","COPY",BODY,{"derivedFrom":makeQuery(id+"F8.opPattern","COPY",BODY,{"derivedFrom":makeQuery(id+"F3.opPattern","COPY",BODY,{"derivedFrom":makeQuery(id+"F2.opPattern","COPY",BODY,{"derivedFrom":makeQuery(id+"F1.opExtrude","SWEPT_BODY",BODY,{"disambiguationData":[OSD([sQuery(id+"F0.wireOp",EDGE,"E1.bottom"),sQuery(id+"F0.wireOp",EDGE,"E1.top"),sQuery(id+"F0.wireOp",EDGE,"E1.left"),sQuery(id+"F0.wireOp",EDGE,"E1.right")])]}),"instanceName":"1"}),"instanceName":"1"}),"instanceName":"1"}),"instanceName":"1"}),"instanceName":"1"});
            var Q403;
            Q403=makeQuery(id+"F11.opPattern","COPY",BODY,{"derivedFrom":makeQuery(id+"F9.opPattern","COPY",BODY,{"derivedFrom":makeQuery(id+"F8.opPattern","COPY",BODY,{"derivedFrom":makeQuery(id+"F3.opPattern","COPY",BODY,{"derivedFrom":makeQuery(id+"F2.opPattern","COPY",BODY,{"derivedFrom":makeQuery(id+"F1.opExtrude","SWEPT_BODY",BODY,{"disambiguationData":[OSD([sQuery(id+"F0.wireOp",EDGE,"E2.bottom"),sQuery(id+"F0.wireOp",EDGE,"E2.top"),sQuery(id+"F0.wireOp",EDGE,"E2.left"),sQuery(id+"F0.wireOp",EDGE,"E2.right")])]}),"instanceName":"1"}),"instanceName":"1"}),"instanceName":"1"}),"instanceName":"1"}),"instanceName":"1"});
            var Q404;
            Q404=makeQuery(id+"F11.opPattern","COPY",BODY,{"derivedFrom":makeQuery(id+"F9.opPattern","COPY",BODY,{"derivedFrom":makeQuery(id+"F8.opPattern","COPY",BODY,{"derivedFrom":makeQuery(id+"F4.opPattern","COPY",BODY,{"derivedFrom":makeQuery(id+"F3.opPattern","COPY",BODY,{"derivedFrom":makeQuery(id+"F2.opPattern","COPY",BODY,{"derivedFrom":makeQuery(id+"F1.opExtrude","SWEPT_BODY",BODY,{"disambiguationData":[OSD([sQuery(id+"F0.wireOp",EDGE,"E0.bottom"),sQuery(id+"F0.wireOp",EDGE,"E0.top"),sQuery(id+"F0.wireOp",EDGE,"E0.left"),sQuery(id+"F0.wireOp",EDGE,"E0.right")])]}),"instanceName":"1"}),"instanceName":"1"}),"instanceName":"1"}),"instanceName":"1"}),"instanceName":"1"}),"instanceName":"1"});
            var Q405;
            Q405=makeQuery(id+"F11.opPattern","COPY",BODY,{"derivedFrom":makeQuery(id+"F9.opPattern","COPY",BODY,{"derivedFrom":makeQuery(id+"F8.opPattern","COPY",BODY,{"derivedFrom":makeQuery(id+"F4.opPattern","COPY",BODY,{"derivedFrom":makeQuery(id+"F3.opPattern","COPY",BODY,{"derivedFrom":makeQuery(id+"F2.opPattern","COPY",BODY,{"derivedFrom":makeQuery(id+"F1.opExtrude","SWEPT_BODY",BODY,{"disambiguationData":[OSD([sQuery(id+"F0.wireOp",EDGE,"E1.bottom"),sQuery(id+"F0.wireOp",EDGE,"E1.top"),sQuery(id+"F0.wireOp",EDGE,"E1.left"),sQuery(id+"F0.wireOp",EDGE,"E1.right")])]}),"instanceName":"1"}),"instanceName":"1"}),"instanceName":"1"}),"instanceName":"1"}),"instanceName":"1"}),"instanceName":"1"});
            var Q406;
            Q406=makeQuery(id+"F11.opPattern","COPY",BODY,{"derivedFrom":makeQuery(id+"F9.opPattern","COPY",BODY,{"derivedFrom":makeQuery(id+"F8.opPattern","COPY",BODY,{"derivedFrom":makeQuery(id+"F4.opPattern","COPY",BODY,{"derivedFrom":makeQuery(id+"F3.opPattern","COPY",BODY,{"derivedFrom":makeQuery(id+"F2.opPattern","COPY",BODY,{"derivedFrom":makeQuery(id+"F1.opExtrude","SWEPT_BODY",BODY,{"disambiguationData":[OSD([sQuery(id+"F0.wireOp",EDGE,"E2.bottom"),sQuery(id+"F0.wireOp",EDGE,"E2.top"),sQuery(id+"F0.wireOp",EDGE,"E2.left"),sQuery(id+"F0.wireOp",EDGE,"E2.right")])]}),"instanceName":"1"}),"instanceName":"1"}),"instanceName":"1"}),"instanceName":"1"}),"instanceName":"1"}),"instanceName":"1"});
            var Q407;
            Q407=makeQuery(id+"F11.opPattern","COPY",BODY,{"derivedFrom":makeQuery(id+"F9.opPattern","COPY",BODY,{"derivedFrom":makeQuery(id+"F8.opPattern","COPY",BODY,{"derivedFrom":makeQuery(id+"F5.opPattern","COPY",BODY,{"derivedFrom":makeQuery(id+"F4.opPattern","COPY",BODY,{"derivedFrom":makeQuery(id+"F3.opPattern","COPY",BODY,{"derivedFrom":makeQuery(id+"F2.opPattern","COPY",BODY,{"derivedFrom":makeQuery(id+"F1.opExtrude","SWEPT_BODY",BODY,{"disambiguationData":[OSD([sQuery(id+"F0.wireOp",EDGE,"E0.bottom"),sQuery(id+"F0.wireOp",EDGE,"E0.top"),sQuery(id+"F0.wireOp",EDGE,"E0.left"),sQuery(id+"F0.wireOp",EDGE,"E0.right")])]}),"instanceName":"1"}),"instanceName":"1"}),"instanceName":"1"}),"instanceName":"1"}),"instanceName":"1"}),"instanceName":"1"}),"instanceName":"1"});
            var Q408;
            Q408=makeQuery(id+"F11.opPattern","COPY",BODY,{"derivedFrom":makeQuery(id+"F9.opPattern","COPY",BODY,{"derivedFrom":makeQuery(id+"F8.opPattern","COPY",BODY,{"derivedFrom":makeQuery(id+"F5.opPattern","COPY",BODY,{"derivedFrom":makeQuery(id+"F4.opPattern","COPY",BODY,{"derivedFrom":makeQuery(id+"F3.opPattern","COPY",BODY,{"derivedFrom":makeQuery(id+"F2.opPattern","COPY",BODY,{"derivedFrom":makeQuery(id+"F1.opExtrude","SWEPT_BODY",BODY,{"disambiguationData":[OSD([sQuery(id+"F0.wireOp",EDGE,"E1.bottom"),sQuery(id+"F0.wireOp",EDGE,"E1.top"),sQuery(id+"F0.wireOp",EDGE,"E1.left"),sQuery(id+"F0.wireOp",EDGE,"E1.right")])]}),"instanceName":"1"}),"instanceName":"1"}),"instanceName":"1"}),"instanceName":"1"}),"instanceName":"1"}),"instanceName":"1"}),"instanceName":"1"});
            var Q409;
            Q409=makeQuery(id+"F11.opPattern","COPY",BODY,{"derivedFrom":makeQuery(id+"F9.opPattern","COPY",BODY,{"derivedFrom":makeQuery(id+"F8.opPattern","COPY",BODY,{"derivedFrom":makeQuery(id+"F5.opPattern","COPY",BODY,{"derivedFrom":makeQuery(id+"F4.opPattern","COPY",BODY,{"derivedFrom":makeQuery(id+"F3.opPattern","COPY",BODY,{"derivedFrom":makeQuery(id+"F2.opPattern","COPY",BODY,{"derivedFrom":makeQuery(id+"F1.opExtrude","SWEPT_BODY",BODY,{"disambiguationData":[OSD([sQuery(id+"F0.wireOp",EDGE,"E2.bottom"),sQuery(id+"F0.wireOp",EDGE,"E2.top"),sQuery(id+"F0.wireOp",EDGE,"E2.left"),sQuery(id+"F0.wireOp",EDGE,"E2.right")])]}),"instanceName":"1"}),"instanceName":"1"}),"instanceName":"1"}),"instanceName":"1"}),"instanceName":"1"}),"instanceName":"1"}),"instanceName":"1"});
            var Q410;
            Q410=makeQuery(id+"F11.opPattern","COPY",BODY,{"derivedFrom":makeQuery(id+"F9.opPattern","COPY",BODY,{"derivedFrom":makeQuery(id+"F8.opPattern","COPY",BODY,{"derivedFrom":makeQuery(id+"F6.opPattern","COPY",BODY,{"derivedFrom":makeQuery(id+"F5.opPattern","COPY",BODY,{"derivedFrom":makeQuery(id+"F4.opPattern","COPY",BODY,{"derivedFrom":makeQuery(id+"F3.opPattern","COPY",BODY,{"derivedFrom":makeQuery(id+"F2.opPattern","COPY",BODY,{"derivedFrom":makeQuery(id+"F1.opExtrude","SWEPT_BODY",BODY,{"disambiguationData":[OSD([sQuery(id+"F0.wireOp",EDGE,"E0.bottom"),sQuery(id+"F0.wireOp",EDGE,"E0.top"),sQuery(id+"F0.wireOp",EDGE,"E0.left"),sQuery(id+"F0.wireOp",EDGE,"E0.right")])]}),"instanceName":"1"}),"instanceName":"1"}),"instanceName":"1"}),"instanceName":"1"}),"instanceName":"1"}),"instanceName":"1"}),"instanceName":"1"}),"instanceName":"1"});
            var Q411;
            Q411=makeQuery(id+"F11.opPattern","COPY",BODY,{"derivedFrom":makeQuery(id+"F9.opPattern","COPY",BODY,{"derivedFrom":makeQuery(id+"F8.opPattern","COPY",BODY,{"derivedFrom":makeQuery(id+"F6.opPattern","COPY",BODY,{"derivedFrom":makeQuery(id+"F5.opPattern","COPY",BODY,{"derivedFrom":makeQuery(id+"F4.opPattern","COPY",BODY,{"derivedFrom":makeQuery(id+"F3.opPattern","COPY",BODY,{"derivedFrom":makeQuery(id+"F2.opPattern","COPY",BODY,{"derivedFrom":makeQuery(id+"F1.opExtrude","SWEPT_BODY",BODY,{"disambiguationData":[OSD([sQuery(id+"F0.wireOp",EDGE,"E1.bottom"),sQuery(id+"F0.wireOp",EDGE,"E1.top"),sQuery(id+"F0.wireOp",EDGE,"E1.left"),sQuery(id+"F0.wireOp",EDGE,"E1.right")])]}),"instanceName":"1"}),"instanceName":"1"}),"instanceName":"1"}),"instanceName":"1"}),"instanceName":"1"}),"instanceName":"1"}),"instanceName":"1"}),"instanceName":"1"});
            var Q412;
            Q412=makeQuery(id+"F11.opPattern","COPY",BODY,{"derivedFrom":makeQuery(id+"F9.opPattern","COPY",BODY,{"derivedFrom":makeQuery(id+"F8.opPattern","COPY",BODY,{"derivedFrom":makeQuery(id+"F6.opPattern","COPY",BODY,{"derivedFrom":makeQuery(id+"F5.opPattern","COPY",BODY,{"derivedFrom":makeQuery(id+"F4.opPattern","COPY",BODY,{"derivedFrom":makeQuery(id+"F3.opPattern","COPY",BODY,{"derivedFrom":makeQuery(id+"F2.opPattern","COPY",BODY,{"derivedFrom":makeQuery(id+"F1.opExtrude","SWEPT_BODY",BODY,{"disambiguationData":[OSD([sQuery(id+"F0.wireOp",EDGE,"E2.bottom"),sQuery(id+"F0.wireOp",EDGE,"E2.top"),sQuery(id+"F0.wireOp",EDGE,"E2.left"),sQuery(id+"F0.wireOp",EDGE,"E2.right")])]}),"instanceName":"1"}),"instanceName":"1"}),"instanceName":"1"}),"instanceName":"1"}),"instanceName":"1"}),"instanceName":"1"}),"instanceName":"1"}),"instanceName":"1"});
            var Q413;
            Q413=makeQuery(id+"F11.opPattern","COPY",BODY,{"derivedFrom":makeQuery(id+"F9.opPattern","COPY",BODY,{"derivedFrom":makeQuery(id+"F8.opPattern","COPY",BODY,{"derivedFrom":makeQuery(id+"F7.opPattern","COPY",BODY,{"derivedFrom":makeQuery(id+"F1.opExtrude","SWEPT_BODY",BODY,{"disambiguationData":[OSD([sQuery(id+"F0.wireOp",EDGE,"E0.bottom"),sQuery(id+"F0.wireOp",EDGE,"E0.top"),sQuery(id+"F0.wireOp",EDGE,"E0.left"),sQuery(id+"F0.wireOp",EDGE,"E0.right")])]}),"instanceName":"1"}),"instanceName":"1"}),"instanceName":"1"}),"instanceName":"1"});
            var Q414;
            Q414=makeQuery(id+"F11.opPattern","COPY",BODY,{"derivedFrom":makeQuery(id+"F9.opPattern","COPY",BODY,{"derivedFrom":makeQuery(id+"F8.opPattern","COPY",BODY,{"derivedFrom":makeQuery(id+"F7.opPattern","COPY",BODY,{"derivedFrom":makeQuery(id+"F1.opExtrude","SWEPT_BODY",BODY,{"disambiguationData":[OSD([sQuery(id+"F0.wireOp",EDGE,"E1.bottom"),sQuery(id+"F0.wireOp",EDGE,"E1.top"),sQuery(id+"F0.wireOp",EDGE,"E1.left"),sQuery(id+"F0.wireOp",EDGE,"E1.right")])]}),"instanceName":"1"}),"instanceName":"1"}),"instanceName":"1"}),"instanceName":"1"});
            var Q415;
            Q415=makeQuery(id+"F11.opPattern","COPY",BODY,{"derivedFrom":makeQuery(id+"F9.opPattern","COPY",BODY,{"derivedFrom":makeQuery(id+"F8.opPattern","COPY",BODY,{"derivedFrom":makeQuery(id+"F7.opPattern","COPY",BODY,{"derivedFrom":makeQuery(id+"F1.opExtrude","SWEPT_BODY",BODY,{"disambiguationData":[OSD([sQuery(id+"F0.wireOp",EDGE,"E2.bottom"),sQuery(id+"F0.wireOp",EDGE,"E2.top"),sQuery(id+"F0.wireOp",EDGE,"E2.left"),sQuery(id+"F0.wireOp",EDGE,"E2.right")])]}),"instanceName":"1"}),"instanceName":"1"}),"instanceName":"1"}),"instanceName":"1"});
            var Q416;
            Q416=makeQuery(id+"F11.opPattern","COPY",BODY,{"derivedFrom":makeQuery(id+"F9.opPattern","COPY",BODY,{"derivedFrom":makeQuery(id+"F8.opPattern","COPY",BODY,{"derivedFrom":makeQuery(id+"F7.opPattern","COPY",BODY,{"derivedFrom":makeQuery(id+"F2.opPattern","COPY",BODY,{"derivedFrom":makeQuery(id+"F1.opExtrude","SWEPT_BODY",BODY,{"disambiguationData":[OSD([sQuery(id+"F0.wireOp",EDGE,"E0.bottom"),sQuery(id+"F0.wireOp",EDGE,"E0.top"),sQuery(id+"F0.wireOp",EDGE,"E0.left"),sQuery(id+"F0.wireOp",EDGE,"E0.right")])]}),"instanceName":"1"}),"instanceName":"1"}),"instanceName":"1"}),"instanceName":"1"}),"instanceName":"1"});
            var Q417;
            Q417=makeQuery(id+"F11.opPattern","COPY",BODY,{"derivedFrom":makeQuery(id+"F9.opPattern","COPY",BODY,{"derivedFrom":makeQuery(id+"F8.opPattern","COPY",BODY,{"derivedFrom":makeQuery(id+"F7.opPattern","COPY",BODY,{"derivedFrom":makeQuery(id+"F2.opPattern","COPY",BODY,{"derivedFrom":makeQuery(id+"F1.opExtrude","SWEPT_BODY",BODY,{"disambiguationData":[OSD([sQuery(id+"F0.wireOp",EDGE,"E1.bottom"),sQuery(id+"F0.wireOp",EDGE,"E1.top"),sQuery(id+"F0.wireOp",EDGE,"E1.left"),sQuery(id+"F0.wireOp",EDGE,"E1.right")])]}),"instanceName":"1"}),"instanceName":"1"}),"instanceName":"1"}),"instanceName":"1"}),"instanceName":"1"});
            var Q418;
            Q418=makeQuery(id+"F11.opPattern","COPY",BODY,{"derivedFrom":makeQuery(id+"F9.opPattern","COPY",BODY,{"derivedFrom":makeQuery(id+"F8.opPattern","COPY",BODY,{"derivedFrom":makeQuery(id+"F7.opPattern","COPY",BODY,{"derivedFrom":makeQuery(id+"F2.opPattern","COPY",BODY,{"derivedFrom":makeQuery(id+"F1.opExtrude","SWEPT_BODY",BODY,{"disambiguationData":[OSD([sQuery(id+"F0.wireOp",EDGE,"E2.bottom"),sQuery(id+"F0.wireOp",EDGE,"E2.top"),sQuery(id+"F0.wireOp",EDGE,"E2.left"),sQuery(id+"F0.wireOp",EDGE,"E2.right")])]}),"instanceName":"1"}),"instanceName":"1"}),"instanceName":"1"}),"instanceName":"1"}),"instanceName":"1"});
            var Q419;
            Q419=makeQuery(id+"F11.opPattern","COPY",BODY,{"derivedFrom":makeQuery(id+"F9.opPattern","COPY",BODY,{"derivedFrom":makeQuery(id+"F8.opPattern","COPY",BODY,{"derivedFrom":makeQuery(id+"F7.opPattern","COPY",BODY,{"derivedFrom":makeQuery(id+"F3.opPattern","COPY",BODY,{"derivedFrom":makeQuery(id+"F2.opPattern","COPY",BODY,{"derivedFrom":makeQuery(id+"F1.opExtrude","SWEPT_BODY",BODY,{"disambiguationData":[OSD([sQuery(id+"F0.wireOp",EDGE,"E0.bottom"),sQuery(id+"F0.wireOp",EDGE,"E0.top"),sQuery(id+"F0.wireOp",EDGE,"E0.left"),sQuery(id+"F0.wireOp",EDGE,"E0.right")])]}),"instanceName":"1"}),"instanceName":"1"}),"instanceName":"1"}),"instanceName":"1"}),"instanceName":"1"}),"instanceName":"1"});
            var Q420;
            Q420=makeQuery(id+"F11.opPattern","COPY",BODY,{"derivedFrom":makeQuery(id+"F9.opPattern","COPY",BODY,{"derivedFrom":makeQuery(id+"F8.opPattern","COPY",BODY,{"derivedFrom":makeQuery(id+"F7.opPattern","COPY",BODY,{"derivedFrom":makeQuery(id+"F3.opPattern","COPY",BODY,{"derivedFrom":makeQuery(id+"F2.opPattern","COPY",BODY,{"derivedFrom":makeQuery(id+"F1.opExtrude","SWEPT_BODY",BODY,{"disambiguationData":[OSD([sQuery(id+"F0.wireOp",EDGE,"E1.bottom"),sQuery(id+"F0.wireOp",EDGE,"E1.top"),sQuery(id+"F0.wireOp",EDGE,"E1.left"),sQuery(id+"F0.wireOp",EDGE,"E1.right")])]}),"instanceName":"1"}),"instanceName":"1"}),"instanceName":"1"}),"instanceName":"1"}),"instanceName":"1"}),"instanceName":"1"});
            var Q421;
            Q421=makeQuery(id+"F11.opPattern","COPY",BODY,{"derivedFrom":makeQuery(id+"F9.opPattern","COPY",BODY,{"derivedFrom":makeQuery(id+"F8.opPattern","COPY",BODY,{"derivedFrom":makeQuery(id+"F7.opPattern","COPY",BODY,{"derivedFrom":makeQuery(id+"F3.opPattern","COPY",BODY,{"derivedFrom":makeQuery(id+"F2.opPattern","COPY",BODY,{"derivedFrom":makeQuery(id+"F1.opExtrude","SWEPT_BODY",BODY,{"disambiguationData":[OSD([sQuery(id+"F0.wireOp",EDGE,"E2.bottom"),sQuery(id+"F0.wireOp",EDGE,"E2.top"),sQuery(id+"F0.wireOp",EDGE,"E2.left"),sQuery(id+"F0.wireOp",EDGE,"E2.right")])]}),"instanceName":"1"}),"instanceName":"1"}),"instanceName":"1"}),"instanceName":"1"}),"instanceName":"1"}),"instanceName":"1"});
            var Q422;
            Q422=makeQuery(id+"F11.opPattern","COPY",BODY,{"derivedFrom":makeQuery(id+"F9.opPattern","COPY",BODY,{"derivedFrom":makeQuery(id+"F8.opPattern","COPY",BODY,{"derivedFrom":makeQuery(id+"F7.opPattern","COPY",BODY,{"derivedFrom":makeQuery(id+"F4.opPattern","COPY",BODY,{"derivedFrom":makeQuery(id+"F3.opPattern","COPY",BODY,{"derivedFrom":makeQuery(id+"F2.opPattern","COPY",BODY,{"derivedFrom":makeQuery(id+"F1.opExtrude","SWEPT_BODY",BODY,{"disambiguationData":[OSD([sQuery(id+"F0.wireOp",EDGE,"E0.bottom"),sQuery(id+"F0.wireOp",EDGE,"E0.top"),sQuery(id+"F0.wireOp",EDGE,"E0.left"),sQuery(id+"F0.wireOp",EDGE,"E0.right")])]}),"instanceName":"1"}),"instanceName":"1"}),"instanceName":"1"}),"instanceName":"1"}),"instanceName":"1"}),"instanceName":"1"}),"instanceName":"1"});
            var Q423;
            Q423=makeQuery(id+"F11.opPattern","COPY",BODY,{"derivedFrom":makeQuery(id+"F9.opPattern","COPY",BODY,{"derivedFrom":makeQuery(id+"F8.opPattern","COPY",BODY,{"derivedFrom":makeQuery(id+"F7.opPattern","COPY",BODY,{"derivedFrom":makeQuery(id+"F4.opPattern","COPY",BODY,{"derivedFrom":makeQuery(id+"F3.opPattern","COPY",BODY,{"derivedFrom":makeQuery(id+"F2.opPattern","COPY",BODY,{"derivedFrom":makeQuery(id+"F1.opExtrude","SWEPT_BODY",BODY,{"disambiguationData":[OSD([sQuery(id+"F0.wireOp",EDGE,"E1.bottom"),sQuery(id+"F0.wireOp",EDGE,"E1.top"),sQuery(id+"F0.wireOp",EDGE,"E1.left"),sQuery(id+"F0.wireOp",EDGE,"E1.right")])]}),"instanceName":"1"}),"instanceName":"1"}),"instanceName":"1"}),"instanceName":"1"}),"instanceName":"1"}),"instanceName":"1"}),"instanceName":"1"});
            var Q424;
            Q424=makeQuery(id+"F11.opPattern","COPY",BODY,{"derivedFrom":makeQuery(id+"F9.opPattern","COPY",BODY,{"derivedFrom":makeQuery(id+"F8.opPattern","COPY",BODY,{"derivedFrom":makeQuery(id+"F7.opPattern","COPY",BODY,{"derivedFrom":makeQuery(id+"F4.opPattern","COPY",BODY,{"derivedFrom":makeQuery(id+"F3.opPattern","COPY",BODY,{"derivedFrom":makeQuery(id+"F2.opPattern","COPY",BODY,{"derivedFrom":makeQuery(id+"F1.opExtrude","SWEPT_BODY",BODY,{"disambiguationData":[OSD([sQuery(id+"F0.wireOp",EDGE,"E2.bottom"),sQuery(id+"F0.wireOp",EDGE,"E2.top"),sQuery(id+"F0.wireOp",EDGE,"E2.left"),sQuery(id+"F0.wireOp",EDGE,"E2.right")])]}),"instanceName":"1"}),"instanceName":"1"}),"instanceName":"1"}),"instanceName":"1"}),"instanceName":"1"}),"instanceName":"1"}),"instanceName":"1"});
            var Q425;
            Q425=makeQuery(id+"F11.opPattern","COPY",BODY,{"derivedFrom":makeQuery(id+"F9.opPattern","COPY",BODY,{"derivedFrom":makeQuery(id+"F8.opPattern","COPY",BODY,{"derivedFrom":makeQuery(id+"F7.opPattern","COPY",BODY,{"derivedFrom":makeQuery(id+"F5.opPattern","COPY",BODY,{"derivedFrom":makeQuery(id+"F4.opPattern","COPY",BODY,{"derivedFrom":makeQuery(id+"F3.opPattern","COPY",BODY,{"derivedFrom":makeQuery(id+"F2.opPattern","COPY",BODY,{"derivedFrom":makeQuery(id+"F1.opExtrude","SWEPT_BODY",BODY,{"disambiguationData":[OSD([sQuery(id+"F0.wireOp",EDGE,"E0.bottom"),sQuery(id+"F0.wireOp",EDGE,"E0.top"),sQuery(id+"F0.wireOp",EDGE,"E0.left"),sQuery(id+"F0.wireOp",EDGE,"E0.right")])]}),"instanceName":"1"}),"instanceName":"1"}),"instanceName":"1"}),"instanceName":"1"}),"instanceName":"1"}),"instanceName":"1"}),"instanceName":"1"}),"instanceName":"1"});
            var Q426;
            Q426=makeQuery(id+"F11.opPattern","COPY",BODY,{"derivedFrom":makeQuery(id+"F9.opPattern","COPY",BODY,{"derivedFrom":makeQuery(id+"F8.opPattern","COPY",BODY,{"derivedFrom":makeQuery(id+"F7.opPattern","COPY",BODY,{"derivedFrom":makeQuery(id+"F5.opPattern","COPY",BODY,{"derivedFrom":makeQuery(id+"F4.opPattern","COPY",BODY,{"derivedFrom":makeQuery(id+"F3.opPattern","COPY",BODY,{"derivedFrom":makeQuery(id+"F2.opPattern","COPY",BODY,{"derivedFrom":makeQuery(id+"F1.opExtrude","SWEPT_BODY",BODY,{"disambiguationData":[OSD([sQuery(id+"F0.wireOp",EDGE,"E1.bottom"),sQuery(id+"F0.wireOp",EDGE,"E1.top"),sQuery(id+"F0.wireOp",EDGE,"E1.left"),sQuery(id+"F0.wireOp",EDGE,"E1.right")])]}),"instanceName":"1"}),"instanceName":"1"}),"instanceName":"1"}),"instanceName":"1"}),"instanceName":"1"}),"instanceName":"1"}),"instanceName":"1"}),"instanceName":"1"});
            var Q427;
            Q427=makeQuery(id+"F11.opPattern","COPY",BODY,{"derivedFrom":makeQuery(id+"F9.opPattern","COPY",BODY,{"derivedFrom":makeQuery(id+"F8.opPattern","COPY",BODY,{"derivedFrom":makeQuery(id+"F7.opPattern","COPY",BODY,{"derivedFrom":makeQuery(id+"F5.opPattern","COPY",BODY,{"derivedFrom":makeQuery(id+"F4.opPattern","COPY",BODY,{"derivedFrom":makeQuery(id+"F3.opPattern","COPY",BODY,{"derivedFrom":makeQuery(id+"F2.opPattern","COPY",BODY,{"derivedFrom":makeQuery(id+"F1.opExtrude","SWEPT_BODY",BODY,{"disambiguationData":[OSD([sQuery(id+"F0.wireOp",EDGE,"E2.bottom"),sQuery(id+"F0.wireOp",EDGE,"E2.top"),sQuery(id+"F0.wireOp",EDGE,"E2.left"),sQuery(id+"F0.wireOp",EDGE,"E2.right")])]}),"instanceName":"1"}),"instanceName":"1"}),"instanceName":"1"}),"instanceName":"1"}),"instanceName":"1"}),"instanceName":"1"}),"instanceName":"1"}),"instanceName":"1"});
            var Q428;
            Q428=makeQuery(id+"F11.opPattern","COPY",BODY,{"derivedFrom":makeQuery(id+"F9.opPattern","COPY",BODY,{"derivedFrom":makeQuery(id+"F8.opPattern","COPY",BODY,{"derivedFrom":makeQuery(id+"F7.opPattern","COPY",BODY,{"derivedFrom":makeQuery(id+"F6.opPattern","COPY",BODY,{"derivedFrom":makeQuery(id+"F5.opPattern","COPY",BODY,{"derivedFrom":makeQuery(id+"F4.opPattern","COPY",BODY,{"derivedFrom":makeQuery(id+"F3.opPattern","COPY",BODY,{"derivedFrom":makeQuery(id+"F2.opPattern","COPY",BODY,{"derivedFrom":makeQuery(id+"F1.opExtrude","SWEPT_BODY",BODY,{"disambiguationData":[OSD([sQuery(id+"F0.wireOp",EDGE,"E0.bottom"),sQuery(id+"F0.wireOp",EDGE,"E0.top"),sQuery(id+"F0.wireOp",EDGE,"E0.left"),sQuery(id+"F0.wireOp",EDGE,"E0.right")])]}),"instanceName":"1"}),"instanceName":"1"}),"instanceName":"1"}),"instanceName":"1"}),"instanceName":"1"}),"instanceName":"1"}),"instanceName":"1"}),"instanceName":"1"}),"instanceName":"1"});
            var Q429;
            Q429=makeQuery(id+"F11.opPattern","COPY",BODY,{"derivedFrom":makeQuery(id+"F9.opPattern","COPY",BODY,{"derivedFrom":makeQuery(id+"F8.opPattern","COPY",BODY,{"derivedFrom":makeQuery(id+"F7.opPattern","COPY",BODY,{"derivedFrom":makeQuery(id+"F6.opPattern","COPY",BODY,{"derivedFrom":makeQuery(id+"F5.opPattern","COPY",BODY,{"derivedFrom":makeQuery(id+"F4.opPattern","COPY",BODY,{"derivedFrom":makeQuery(id+"F3.opPattern","COPY",BODY,{"derivedFrom":makeQuery(id+"F2.opPattern","COPY",BODY,{"derivedFrom":makeQuery(id+"F1.opExtrude","SWEPT_BODY",BODY,{"disambiguationData":[OSD([sQuery(id+"F0.wireOp",EDGE,"E1.bottom"),sQuery(id+"F0.wireOp",EDGE,"E1.top"),sQuery(id+"F0.wireOp",EDGE,"E1.left"),sQuery(id+"F0.wireOp",EDGE,"E1.right")])]}),"instanceName":"1"}),"instanceName":"1"}),"instanceName":"1"}),"instanceName":"1"}),"instanceName":"1"}),"instanceName":"1"}),"instanceName":"1"}),"instanceName":"1"}),"instanceName":"1"});
            var Q430;
            Q430=makeQuery(id+"F11.opPattern","COPY",BODY,{"derivedFrom":makeQuery(id+"F9.opPattern","COPY",BODY,{"derivedFrom":makeQuery(id+"F8.opPattern","COPY",BODY,{"derivedFrom":makeQuery(id+"F7.opPattern","COPY",BODY,{"derivedFrom":makeQuery(id+"F6.opPattern","COPY",BODY,{"derivedFrom":makeQuery(id+"F5.opPattern","COPY",BODY,{"derivedFrom":makeQuery(id+"F4.opPattern","COPY",BODY,{"derivedFrom":makeQuery(id+"F3.opPattern","COPY",BODY,{"derivedFrom":makeQuery(id+"F2.opPattern","COPY",BODY,{"derivedFrom":makeQuery(id+"F1.opExtrude","SWEPT_BODY",BODY,{"disambiguationData":[OSD([sQuery(id+"F0.wireOp",EDGE,"E2.bottom"),sQuery(id+"F0.wireOp",EDGE,"E2.top"),sQuery(id+"F0.wireOp",EDGE,"E2.left"),sQuery(id+"F0.wireOp",EDGE,"E2.right")])]}),"instanceName":"1"}),"instanceName":"1"}),"instanceName":"1"}),"instanceName":"1"}),"instanceName":"1"}),"instanceName":"1"}),"instanceName":"1"}),"instanceName":"1"}),"instanceName":"1"});
            var Q431;
            Q431=makeQuery(id+"F11.opPattern","COPY",BODY,{"derivedFrom":makeQuery(id+"F10.opPattern","COPY",BODY,{"derivedFrom":makeQuery(id+"F1.opExtrude","SWEPT_BODY",BODY,{"disambiguationData":[OSD([sQuery(id+"F0.wireOp",EDGE,"E0.bottom"),sQuery(id+"F0.wireOp",EDGE,"E0.top"),sQuery(id+"F0.wireOp",EDGE,"E0.left"),sQuery(id+"F0.wireOp",EDGE,"E0.right")])]}),"instanceName":"1"}),"instanceName":"1"});
            var Q432;
            Q432=makeQuery(id+"F11.opPattern","COPY",BODY,{"derivedFrom":makeQuery(id+"F10.opPattern","COPY",BODY,{"derivedFrom":makeQuery(id+"F1.opExtrude","SWEPT_BODY",BODY,{"disambiguationData":[OSD([sQuery(id+"F0.wireOp",EDGE,"E1.bottom"),sQuery(id+"F0.wireOp",EDGE,"E1.top"),sQuery(id+"F0.wireOp",EDGE,"E1.left"),sQuery(id+"F0.wireOp",EDGE,"E1.right")])]}),"instanceName":"1"}),"instanceName":"1"});
            var Q433;
            Q433=makeQuery(id+"F11.opPattern","COPY",BODY,{"derivedFrom":makeQuery(id+"F10.opPattern","COPY",BODY,{"derivedFrom":makeQuery(id+"F1.opExtrude","SWEPT_BODY",BODY,{"disambiguationData":[OSD([sQuery(id+"F0.wireOp",EDGE,"E2.bottom"),sQuery(id+"F0.wireOp",EDGE,"E2.top"),sQuery(id+"F0.wireOp",EDGE,"E2.left"),sQuery(id+"F0.wireOp",EDGE,"E2.right")])]}),"instanceName":"1"}),"instanceName":"1"});
            var Q434;
            Q434=makeQuery(id+"F11.opPattern","COPY",BODY,{"derivedFrom":makeQuery(id+"F10.opPattern","COPY",BODY,{"derivedFrom":makeQuery(id+"F2.opPattern","COPY",BODY,{"derivedFrom":makeQuery(id+"F1.opExtrude","SWEPT_BODY",BODY,{"disambiguationData":[OSD([sQuery(id+"F0.wireOp",EDGE,"E0.bottom"),sQuery(id+"F0.wireOp",EDGE,"E0.top"),sQuery(id+"F0.wireOp",EDGE,"E0.left"),sQuery(id+"F0.wireOp",EDGE,"E0.right")])]}),"instanceName":"1"}),"instanceName":"1"}),"instanceName":"1"});
            var Q435;
            Q435=makeQuery(id+"F11.opPattern","COPY",BODY,{"derivedFrom":makeQuery(id+"F10.opPattern","COPY",BODY,{"derivedFrom":makeQuery(id+"F2.opPattern","COPY",BODY,{"derivedFrom":makeQuery(id+"F1.opExtrude","SWEPT_BODY",BODY,{"disambiguationData":[OSD([sQuery(id+"F0.wireOp",EDGE,"E1.bottom"),sQuery(id+"F0.wireOp",EDGE,"E1.top"),sQuery(id+"F0.wireOp",EDGE,"E1.left"),sQuery(id+"F0.wireOp",EDGE,"E1.right")])]}),"instanceName":"1"}),"instanceName":"1"}),"instanceName":"1"});
            var Q436;
            Q436=makeQuery(id+"F11.opPattern","COPY",BODY,{"derivedFrom":makeQuery(id+"F10.opPattern","COPY",BODY,{"derivedFrom":makeQuery(id+"F2.opPattern","COPY",BODY,{"derivedFrom":makeQuery(id+"F1.opExtrude","SWEPT_BODY",BODY,{"disambiguationData":[OSD([sQuery(id+"F0.wireOp",EDGE,"E2.bottom"),sQuery(id+"F0.wireOp",EDGE,"E2.top"),sQuery(id+"F0.wireOp",EDGE,"E2.left"),sQuery(id+"F0.wireOp",EDGE,"E2.right")])]}),"instanceName":"1"}),"instanceName":"1"}),"instanceName":"1"});
            var Q437;
            Q437=makeQuery(id+"F11.opPattern","COPY",BODY,{"derivedFrom":makeQuery(id+"F10.opPattern","COPY",BODY,{"derivedFrom":makeQuery(id+"F3.opPattern","COPY",BODY,{"derivedFrom":makeQuery(id+"F2.opPattern","COPY",BODY,{"derivedFrom":makeQuery(id+"F1.opExtrude","SWEPT_BODY",BODY,{"disambiguationData":[OSD([sQuery(id+"F0.wireOp",EDGE,"E0.bottom"),sQuery(id+"F0.wireOp",EDGE,"E0.top"),sQuery(id+"F0.wireOp",EDGE,"E0.left"),sQuery(id+"F0.wireOp",EDGE,"E0.right")])]}),"instanceName":"1"}),"instanceName":"1"}),"instanceName":"1"}),"instanceName":"1"});
            var Q438;
            Q438=makeQuery(id+"F11.opPattern","COPY",BODY,{"derivedFrom":makeQuery(id+"F10.opPattern","COPY",BODY,{"derivedFrom":makeQuery(id+"F3.opPattern","COPY",BODY,{"derivedFrom":makeQuery(id+"F2.opPattern","COPY",BODY,{"derivedFrom":makeQuery(id+"F1.opExtrude","SWEPT_BODY",BODY,{"disambiguationData":[OSD([sQuery(id+"F0.wireOp",EDGE,"E1.bottom"),sQuery(id+"F0.wireOp",EDGE,"E1.top"),sQuery(id+"F0.wireOp",EDGE,"E1.left"),sQuery(id+"F0.wireOp",EDGE,"E1.right")])]}),"instanceName":"1"}),"instanceName":"1"}),"instanceName":"1"}),"instanceName":"1"});
            var Q439;
            Q439=makeQuery(id+"F11.opPattern","COPY",BODY,{"derivedFrom":makeQuery(id+"F10.opPattern","COPY",BODY,{"derivedFrom":makeQuery(id+"F3.opPattern","COPY",BODY,{"derivedFrom":makeQuery(id+"F2.opPattern","COPY",BODY,{"derivedFrom":makeQuery(id+"F1.opExtrude","SWEPT_BODY",BODY,{"disambiguationData":[OSD([sQuery(id+"F0.wireOp",EDGE,"E2.bottom"),sQuery(id+"F0.wireOp",EDGE,"E2.top"),sQuery(id+"F0.wireOp",EDGE,"E2.left"),sQuery(id+"F0.wireOp",EDGE,"E2.right")])]}),"instanceName":"1"}),"instanceName":"1"}),"instanceName":"1"}),"instanceName":"1"});
            var Q440;
            Q440=makeQuery(id+"F11.opPattern","COPY",BODY,{"derivedFrom":makeQuery(id+"F10.opPattern","COPY",BODY,{"derivedFrom":makeQuery(id+"F4.opPattern","COPY",BODY,{"derivedFrom":makeQuery(id+"F3.opPattern","COPY",BODY,{"derivedFrom":makeQuery(id+"F2.opPattern","COPY",BODY,{"derivedFrom":makeQuery(id+"F1.opExtrude","SWEPT_BODY",BODY,{"disambiguationData":[OSD([sQuery(id+"F0.wireOp",EDGE,"E0.bottom"),sQuery(id+"F0.wireOp",EDGE,"E0.top"),sQuery(id+"F0.wireOp",EDGE,"E0.left"),sQuery(id+"F0.wireOp",EDGE,"E0.right")])]}),"instanceName":"1"}),"instanceName":"1"}),"instanceName":"1"}),"instanceName":"1"}),"instanceName":"1"});
            var Q441;
            Q441=makeQuery(id+"F11.opPattern","COPY",BODY,{"derivedFrom":makeQuery(id+"F10.opPattern","COPY",BODY,{"derivedFrom":makeQuery(id+"F4.opPattern","COPY",BODY,{"derivedFrom":makeQuery(id+"F3.opPattern","COPY",BODY,{"derivedFrom":makeQuery(id+"F2.opPattern","COPY",BODY,{"derivedFrom":makeQuery(id+"F1.opExtrude","SWEPT_BODY",BODY,{"disambiguationData":[OSD([sQuery(id+"F0.wireOp",EDGE,"E1.bottom"),sQuery(id+"F0.wireOp",EDGE,"E1.top"),sQuery(id+"F0.wireOp",EDGE,"E1.left"),sQuery(id+"F0.wireOp",EDGE,"E1.right")])]}),"instanceName":"1"}),"instanceName":"1"}),"instanceName":"1"}),"instanceName":"1"}),"instanceName":"1"});
            var Q442;
            Q442=makeQuery(id+"F11.opPattern","COPY",BODY,{"derivedFrom":makeQuery(id+"F10.opPattern","COPY",BODY,{"derivedFrom":makeQuery(id+"F4.opPattern","COPY",BODY,{"derivedFrom":makeQuery(id+"F3.opPattern","COPY",BODY,{"derivedFrom":makeQuery(id+"F2.opPattern","COPY",BODY,{"derivedFrom":makeQuery(id+"F1.opExtrude","SWEPT_BODY",BODY,{"disambiguationData":[OSD([sQuery(id+"F0.wireOp",EDGE,"E2.bottom"),sQuery(id+"F0.wireOp",EDGE,"E2.top"),sQuery(id+"F0.wireOp",EDGE,"E2.left"),sQuery(id+"F0.wireOp",EDGE,"E2.right")])]}),"instanceName":"1"}),"instanceName":"1"}),"instanceName":"1"}),"instanceName":"1"}),"instanceName":"1"});
            var Q443;
            Q443=makeQuery(id+"F11.opPattern","COPY",BODY,{"derivedFrom":makeQuery(id+"F10.opPattern","COPY",BODY,{"derivedFrom":makeQuery(id+"F5.opPattern","COPY",BODY,{"derivedFrom":makeQuery(id+"F4.opPattern","COPY",BODY,{"derivedFrom":makeQuery(id+"F3.opPattern","COPY",BODY,{"derivedFrom":makeQuery(id+"F2.opPattern","COPY",BODY,{"derivedFrom":makeQuery(id+"F1.opExtrude","SWEPT_BODY",BODY,{"disambiguationData":[OSD([sQuery(id+"F0.wireOp",EDGE,"E0.bottom"),sQuery(id+"F0.wireOp",EDGE,"E0.top"),sQuery(id+"F0.wireOp",EDGE,"E0.left"),sQuery(id+"F0.wireOp",EDGE,"E0.right")])]}),"instanceName":"1"}),"instanceName":"1"}),"instanceName":"1"}),"instanceName":"1"}),"instanceName":"1"}),"instanceName":"1"});
            var Q444;
            Q444=makeQuery(id+"F11.opPattern","COPY",BODY,{"derivedFrom":makeQuery(id+"F10.opPattern","COPY",BODY,{"derivedFrom":makeQuery(id+"F5.opPattern","COPY",BODY,{"derivedFrom":makeQuery(id+"F4.opPattern","COPY",BODY,{"derivedFrom":makeQuery(id+"F3.opPattern","COPY",BODY,{"derivedFrom":makeQuery(id+"F2.opPattern","COPY",BODY,{"derivedFrom":makeQuery(id+"F1.opExtrude","SWEPT_BODY",BODY,{"disambiguationData":[OSD([sQuery(id+"F0.wireOp",EDGE,"E1.bottom"),sQuery(id+"F0.wireOp",EDGE,"E1.top"),sQuery(id+"F0.wireOp",EDGE,"E1.left"),sQuery(id+"F0.wireOp",EDGE,"E1.right")])]}),"instanceName":"1"}),"instanceName":"1"}),"instanceName":"1"}),"instanceName":"1"}),"instanceName":"1"}),"instanceName":"1"});
            var Q445;
            Q445=makeQuery(id+"F11.opPattern","COPY",BODY,{"derivedFrom":makeQuery(id+"F10.opPattern","COPY",BODY,{"derivedFrom":makeQuery(id+"F5.opPattern","COPY",BODY,{"derivedFrom":makeQuery(id+"F4.opPattern","COPY",BODY,{"derivedFrom":makeQuery(id+"F3.opPattern","COPY",BODY,{"derivedFrom":makeQuery(id+"F2.opPattern","COPY",BODY,{"derivedFrom":makeQuery(id+"F1.opExtrude","SWEPT_BODY",BODY,{"disambiguationData":[OSD([sQuery(id+"F0.wireOp",EDGE,"E2.bottom"),sQuery(id+"F0.wireOp",EDGE,"E2.top"),sQuery(id+"F0.wireOp",EDGE,"E2.left"),sQuery(id+"F0.wireOp",EDGE,"E2.right")])]}),"instanceName":"1"}),"instanceName":"1"}),"instanceName":"1"}),"instanceName":"1"}),"instanceName":"1"}),"instanceName":"1"});
            var Q446;
            Q446=makeQuery(id+"F11.opPattern","COPY",BODY,{"derivedFrom":makeQuery(id+"F10.opPattern","COPY",BODY,{"derivedFrom":makeQuery(id+"F6.opPattern","COPY",BODY,{"derivedFrom":makeQuery(id+"F5.opPattern","COPY",BODY,{"derivedFrom":makeQuery(id+"F4.opPattern","COPY",BODY,{"derivedFrom":makeQuery(id+"F3.opPattern","COPY",BODY,{"derivedFrom":makeQuery(id+"F2.opPattern","COPY",BODY,{"derivedFrom":makeQuery(id+"F1.opExtrude","SWEPT_BODY",BODY,{"disambiguationData":[OSD([sQuery(id+"F0.wireOp",EDGE,"E0.bottom"),sQuery(id+"F0.wireOp",EDGE,"E0.top"),sQuery(id+"F0.wireOp",EDGE,"E0.left"),sQuery(id+"F0.wireOp",EDGE,"E0.right")])]}),"instanceName":"1"}),"instanceName":"1"}),"instanceName":"1"}),"instanceName":"1"}),"instanceName":"1"}),"instanceName":"1"}),"instanceName":"1"});
            var Q447;
            Q447=makeQuery(id+"F11.opPattern","COPY",BODY,{"derivedFrom":makeQuery(id+"F10.opPattern","COPY",BODY,{"derivedFrom":makeQuery(id+"F6.opPattern","COPY",BODY,{"derivedFrom":makeQuery(id+"F5.opPattern","COPY",BODY,{"derivedFrom":makeQuery(id+"F4.opPattern","COPY",BODY,{"derivedFrom":makeQuery(id+"F3.opPattern","COPY",BODY,{"derivedFrom":makeQuery(id+"F2.opPattern","COPY",BODY,{"derivedFrom":makeQuery(id+"F1.opExtrude","SWEPT_BODY",BODY,{"disambiguationData":[OSD([sQuery(id+"F0.wireOp",EDGE,"E1.bottom"),sQuery(id+"F0.wireOp",EDGE,"E1.top"),sQuery(id+"F0.wireOp",EDGE,"E1.left"),sQuery(id+"F0.wireOp",EDGE,"E1.right")])]}),"instanceName":"1"}),"instanceName":"1"}),"instanceName":"1"}),"instanceName":"1"}),"instanceName":"1"}),"instanceName":"1"}),"instanceName":"1"});
            var Q448;
            Q448=makeQuery(id+"F11.opPattern","COPY",BODY,{"derivedFrom":makeQuery(id+"F10.opPattern","COPY",BODY,{"derivedFrom":makeQuery(id+"F6.opPattern","COPY",BODY,{"derivedFrom":makeQuery(id+"F5.opPattern","COPY",BODY,{"derivedFrom":makeQuery(id+"F4.opPattern","COPY",BODY,{"derivedFrom":makeQuery(id+"F3.opPattern","COPY",BODY,{"derivedFrom":makeQuery(id+"F2.opPattern","COPY",BODY,{"derivedFrom":makeQuery(id+"F1.opExtrude","SWEPT_BODY",BODY,{"disambiguationData":[OSD([sQuery(id+"F0.wireOp",EDGE,"E2.bottom"),sQuery(id+"F0.wireOp",EDGE,"E2.top"),sQuery(id+"F0.wireOp",EDGE,"E2.left"),sQuery(id+"F0.wireOp",EDGE,"E2.right")])]}),"instanceName":"1"}),"instanceName":"1"}),"instanceName":"1"}),"instanceName":"1"}),"instanceName":"1"}),"instanceName":"1"}),"instanceName":"1"});
            var Q449;
            Q449=makeQuery(id+"F11.opPattern","COPY",BODY,{"derivedFrom":makeQuery(id+"F10.opPattern","COPY",BODY,{"derivedFrom":makeQuery(id+"F7.opPattern","COPY",BODY,{"derivedFrom":makeQuery(id+"F1.opExtrude","SWEPT_BODY",BODY,{"disambiguationData":[OSD([sQuery(id+"F0.wireOp",EDGE,"E0.bottom"),sQuery(id+"F0.wireOp",EDGE,"E0.top"),sQuery(id+"F0.wireOp",EDGE,"E0.left"),sQuery(id+"F0.wireOp",EDGE,"E0.right")])]}),"instanceName":"1"}),"instanceName":"1"}),"instanceName":"1"});
            var Q450;
            Q450=makeQuery(id+"F11.opPattern","COPY",BODY,{"derivedFrom":makeQuery(id+"F10.opPattern","COPY",BODY,{"derivedFrom":makeQuery(id+"F7.opPattern","COPY",BODY,{"derivedFrom":makeQuery(id+"F1.opExtrude","SWEPT_BODY",BODY,{"disambiguationData":[OSD([sQuery(id+"F0.wireOp",EDGE,"E1.bottom"),sQuery(id+"F0.wireOp",EDGE,"E1.top"),sQuery(id+"F0.wireOp",EDGE,"E1.left"),sQuery(id+"F0.wireOp",EDGE,"E1.right")])]}),"instanceName":"1"}),"instanceName":"1"}),"instanceName":"1"});
            var Q451;
            Q451=makeQuery(id+"F11.opPattern","COPY",BODY,{"derivedFrom":makeQuery(id+"F10.opPattern","COPY",BODY,{"derivedFrom":makeQuery(id+"F7.opPattern","COPY",BODY,{"derivedFrom":makeQuery(id+"F1.opExtrude","SWEPT_BODY",BODY,{"disambiguationData":[OSD([sQuery(id+"F0.wireOp",EDGE,"E2.bottom"),sQuery(id+"F0.wireOp",EDGE,"E2.top"),sQuery(id+"F0.wireOp",EDGE,"E2.left"),sQuery(id+"F0.wireOp",EDGE,"E2.right")])]}),"instanceName":"1"}),"instanceName":"1"}),"instanceName":"1"});
            var Q452;
            Q452=makeQuery(id+"F11.opPattern","COPY",BODY,{"derivedFrom":makeQuery(id+"F10.opPattern","COPY",BODY,{"derivedFrom":makeQuery(id+"F7.opPattern","COPY",BODY,{"derivedFrom":makeQuery(id+"F2.opPattern","COPY",BODY,{"derivedFrom":makeQuery(id+"F1.opExtrude","SWEPT_BODY",BODY,{"disambiguationData":[OSD([sQuery(id+"F0.wireOp",EDGE,"E0.bottom"),sQuery(id+"F0.wireOp",EDGE,"E0.top"),sQuery(id+"F0.wireOp",EDGE,"E0.left"),sQuery(id+"F0.wireOp",EDGE,"E0.right")])]}),"instanceName":"1"}),"instanceName":"1"}),"instanceName":"1"}),"instanceName":"1"});
            var Q453;
            Q453=makeQuery(id+"F11.opPattern","COPY",BODY,{"derivedFrom":makeQuery(id+"F10.opPattern","COPY",BODY,{"derivedFrom":makeQuery(id+"F7.opPattern","COPY",BODY,{"derivedFrom":makeQuery(id+"F2.opPattern","COPY",BODY,{"derivedFrom":makeQuery(id+"F1.opExtrude","SWEPT_BODY",BODY,{"disambiguationData":[OSD([sQuery(id+"F0.wireOp",EDGE,"E1.bottom"),sQuery(id+"F0.wireOp",EDGE,"E1.top"),sQuery(id+"F0.wireOp",EDGE,"E1.left"),sQuery(id+"F0.wireOp",EDGE,"E1.right")])]}),"instanceName":"1"}),"instanceName":"1"}),"instanceName":"1"}),"instanceName":"1"});
            var Q454;
            Q454=makeQuery(id+"F11.opPattern","COPY",BODY,{"derivedFrom":makeQuery(id+"F10.opPattern","COPY",BODY,{"derivedFrom":makeQuery(id+"F7.opPattern","COPY",BODY,{"derivedFrom":makeQuery(id+"F2.opPattern","COPY",BODY,{"derivedFrom":makeQuery(id+"F1.opExtrude","SWEPT_BODY",BODY,{"disambiguationData":[OSD([sQuery(id+"F0.wireOp",EDGE,"E2.bottom"),sQuery(id+"F0.wireOp",EDGE,"E2.top"),sQuery(id+"F0.wireOp",EDGE,"E2.left"),sQuery(id+"F0.wireOp",EDGE,"E2.right")])]}),"instanceName":"1"}),"instanceName":"1"}),"instanceName":"1"}),"instanceName":"1"});
            var Q455;
            Q455=makeQuery(id+"F11.opPattern","COPY",BODY,{"derivedFrom":makeQuery(id+"F10.opPattern","COPY",BODY,{"derivedFrom":makeQuery(id+"F7.opPattern","COPY",BODY,{"derivedFrom":makeQuery(id+"F3.opPattern","COPY",BODY,{"derivedFrom":makeQuery(id+"F2.opPattern","COPY",BODY,{"derivedFrom":makeQuery(id+"F1.opExtrude","SWEPT_BODY",BODY,{"disambiguationData":[OSD([sQuery(id+"F0.wireOp",EDGE,"E0.bottom"),sQuery(id+"F0.wireOp",EDGE,"E0.top"),sQuery(id+"F0.wireOp",EDGE,"E0.left"),sQuery(id+"F0.wireOp",EDGE,"E0.right")])]}),"instanceName":"1"}),"instanceName":"1"}),"instanceName":"1"}),"instanceName":"1"}),"instanceName":"1"});
            var Q456;
            Q456=makeQuery(id+"F11.opPattern","COPY",BODY,{"derivedFrom":makeQuery(id+"F10.opPattern","COPY",BODY,{"derivedFrom":makeQuery(id+"F7.opPattern","COPY",BODY,{"derivedFrom":makeQuery(id+"F3.opPattern","COPY",BODY,{"derivedFrom":makeQuery(id+"F2.opPattern","COPY",BODY,{"derivedFrom":makeQuery(id+"F1.opExtrude","SWEPT_BODY",BODY,{"disambiguationData":[OSD([sQuery(id+"F0.wireOp",EDGE,"E1.bottom"),sQuery(id+"F0.wireOp",EDGE,"E1.top"),sQuery(id+"F0.wireOp",EDGE,"E1.left"),sQuery(id+"F0.wireOp",EDGE,"E1.right")])]}),"instanceName":"1"}),"instanceName":"1"}),"instanceName":"1"}),"instanceName":"1"}),"instanceName":"1"});
            var Q457;
            Q457=makeQuery(id+"F11.opPattern","COPY",BODY,{"derivedFrom":makeQuery(id+"F10.opPattern","COPY",BODY,{"derivedFrom":makeQuery(id+"F7.opPattern","COPY",BODY,{"derivedFrom":makeQuery(id+"F3.opPattern","COPY",BODY,{"derivedFrom":makeQuery(id+"F2.opPattern","COPY",BODY,{"derivedFrom":makeQuery(id+"F1.opExtrude","SWEPT_BODY",BODY,{"disambiguationData":[OSD([sQuery(id+"F0.wireOp",EDGE,"E2.bottom"),sQuery(id+"F0.wireOp",EDGE,"E2.top"),sQuery(id+"F0.wireOp",EDGE,"E2.left"),sQuery(id+"F0.wireOp",EDGE,"E2.right")])]}),"instanceName":"1"}),"instanceName":"1"}),"instanceName":"1"}),"instanceName":"1"}),"instanceName":"1"});
            var Q458;
            Q458=makeQuery(id+"F11.opPattern","COPY",BODY,{"derivedFrom":makeQuery(id+"F10.opPattern","COPY",BODY,{"derivedFrom":makeQuery(id+"F7.opPattern","COPY",BODY,{"derivedFrom":makeQuery(id+"F4.opPattern","COPY",BODY,{"derivedFrom":makeQuery(id+"F3.opPattern","COPY",BODY,{"derivedFrom":makeQuery(id+"F2.opPattern","COPY",BODY,{"derivedFrom":makeQuery(id+"F1.opExtrude","SWEPT_BODY",BODY,{"disambiguationData":[OSD([sQuery(id+"F0.wireOp",EDGE,"E0.bottom"),sQuery(id+"F0.wireOp",EDGE,"E0.top"),sQuery(id+"F0.wireOp",EDGE,"E0.left"),sQuery(id+"F0.wireOp",EDGE,"E0.right")])]}),"instanceName":"1"}),"instanceName":"1"}),"instanceName":"1"}),"instanceName":"1"}),"instanceName":"1"}),"instanceName":"1"});
            var Q459;
            Q459=makeQuery(id+"F11.opPattern","COPY",BODY,{"derivedFrom":makeQuery(id+"F10.opPattern","COPY",BODY,{"derivedFrom":makeQuery(id+"F7.opPattern","COPY",BODY,{"derivedFrom":makeQuery(id+"F4.opPattern","COPY",BODY,{"derivedFrom":makeQuery(id+"F3.opPattern","COPY",BODY,{"derivedFrom":makeQuery(id+"F2.opPattern","COPY",BODY,{"derivedFrom":makeQuery(id+"F1.opExtrude","SWEPT_BODY",BODY,{"disambiguationData":[OSD([sQuery(id+"F0.wireOp",EDGE,"E1.bottom"),sQuery(id+"F0.wireOp",EDGE,"E1.top"),sQuery(id+"F0.wireOp",EDGE,"E1.left"),sQuery(id+"F0.wireOp",EDGE,"E1.right")])]}),"instanceName":"1"}),"instanceName":"1"}),"instanceName":"1"}),"instanceName":"1"}),"instanceName":"1"}),"instanceName":"1"});
            var Q460;
            Q460=makeQuery(id+"F11.opPattern","COPY",BODY,{"derivedFrom":makeQuery(id+"F10.opPattern","COPY",BODY,{"derivedFrom":makeQuery(id+"F7.opPattern","COPY",BODY,{"derivedFrom":makeQuery(id+"F4.opPattern","COPY",BODY,{"derivedFrom":makeQuery(id+"F3.opPattern","COPY",BODY,{"derivedFrom":makeQuery(id+"F2.opPattern","COPY",BODY,{"derivedFrom":makeQuery(id+"F1.opExtrude","SWEPT_BODY",BODY,{"disambiguationData":[OSD([sQuery(id+"F0.wireOp",EDGE,"E2.bottom"),sQuery(id+"F0.wireOp",EDGE,"E2.top"),sQuery(id+"F0.wireOp",EDGE,"E2.left"),sQuery(id+"F0.wireOp",EDGE,"E2.right")])]}),"instanceName":"1"}),"instanceName":"1"}),"instanceName":"1"}),"instanceName":"1"}),"instanceName":"1"}),"instanceName":"1"});
            var Q461;
            Q461=makeQuery(id+"F11.opPattern","COPY",BODY,{"derivedFrom":makeQuery(id+"F10.opPattern","COPY",BODY,{"derivedFrom":makeQuery(id+"F7.opPattern","COPY",BODY,{"derivedFrom":makeQuery(id+"F5.opPattern","COPY",BODY,{"derivedFrom":makeQuery(id+"F4.opPattern","COPY",BODY,{"derivedFrom":makeQuery(id+"F3.opPattern","COPY",BODY,{"derivedFrom":makeQuery(id+"F2.opPattern","COPY",BODY,{"derivedFrom":makeQuery(id+"F1.opExtrude","SWEPT_BODY",BODY,{"disambiguationData":[OSD([sQuery(id+"F0.wireOp",EDGE,"E0.bottom"),sQuery(id+"F0.wireOp",EDGE,"E0.top"),sQuery(id+"F0.wireOp",EDGE,"E0.left"),sQuery(id+"F0.wireOp",EDGE,"E0.right")])]}),"instanceName":"1"}),"instanceName":"1"}),"instanceName":"1"}),"instanceName":"1"}),"instanceName":"1"}),"instanceName":"1"}),"instanceName":"1"});
            var Q462;
            Q462=makeQuery(id+"F11.opPattern","COPY",BODY,{"derivedFrom":makeQuery(id+"F10.opPattern","COPY",BODY,{"derivedFrom":makeQuery(id+"F7.opPattern","COPY",BODY,{"derivedFrom":makeQuery(id+"F5.opPattern","COPY",BODY,{"derivedFrom":makeQuery(id+"F4.opPattern","COPY",BODY,{"derivedFrom":makeQuery(id+"F3.opPattern","COPY",BODY,{"derivedFrom":makeQuery(id+"F2.opPattern","COPY",BODY,{"derivedFrom":makeQuery(id+"F1.opExtrude","SWEPT_BODY",BODY,{"disambiguationData":[OSD([sQuery(id+"F0.wireOp",EDGE,"E1.bottom"),sQuery(id+"F0.wireOp",EDGE,"E1.top"),sQuery(id+"F0.wireOp",EDGE,"E1.left"),sQuery(id+"F0.wireOp",EDGE,"E1.right")])]}),"instanceName":"1"}),"instanceName":"1"}),"instanceName":"1"}),"instanceName":"1"}),"instanceName":"1"}),"instanceName":"1"}),"instanceName":"1"});
            var Q463;
            Q463=makeQuery(id+"F11.opPattern","COPY",BODY,{"derivedFrom":makeQuery(id+"F10.opPattern","COPY",BODY,{"derivedFrom":makeQuery(id+"F7.opPattern","COPY",BODY,{"derivedFrom":makeQuery(id+"F5.opPattern","COPY",BODY,{"derivedFrom":makeQuery(id+"F4.opPattern","COPY",BODY,{"derivedFrom":makeQuery(id+"F3.opPattern","COPY",BODY,{"derivedFrom":makeQuery(id+"F2.opPattern","COPY",BODY,{"derivedFrom":makeQuery(id+"F1.opExtrude","SWEPT_BODY",BODY,{"disambiguationData":[OSD([sQuery(id+"F0.wireOp",EDGE,"E2.bottom"),sQuery(id+"F0.wireOp",EDGE,"E2.top"),sQuery(id+"F0.wireOp",EDGE,"E2.left"),sQuery(id+"F0.wireOp",EDGE,"E2.right")])]}),"instanceName":"1"}),"instanceName":"1"}),"instanceName":"1"}),"instanceName":"1"}),"instanceName":"1"}),"instanceName":"1"}),"instanceName":"1"});
            var Q464;
            Q464=makeQuery(id+"F11.opPattern","COPY",BODY,{"derivedFrom":makeQuery(id+"F10.opPattern","COPY",BODY,{"derivedFrom":makeQuery(id+"F7.opPattern","COPY",BODY,{"derivedFrom":makeQuery(id+"F6.opPattern","COPY",BODY,{"derivedFrom":makeQuery(id+"F5.opPattern","COPY",BODY,{"derivedFrom":makeQuery(id+"F4.opPattern","COPY",BODY,{"derivedFrom":makeQuery(id+"F3.opPattern","COPY",BODY,{"derivedFrom":makeQuery(id+"F2.opPattern","COPY",BODY,{"derivedFrom":makeQuery(id+"F1.opExtrude","SWEPT_BODY",BODY,{"disambiguationData":[OSD([sQuery(id+"F0.wireOp",EDGE,"E0.bottom"),sQuery(id+"F0.wireOp",EDGE,"E0.top"),sQuery(id+"F0.wireOp",EDGE,"E0.left"),sQuery(id+"F0.wireOp",EDGE,"E0.right")])]}),"instanceName":"1"}),"instanceName":"1"}),"instanceName":"1"}),"instanceName":"1"}),"instanceName":"1"}),"instanceName":"1"}),"instanceName":"1"}),"instanceName":"1"});
            var Q465;
            Q465=makeQuery(id+"F11.opPattern","COPY",BODY,{"derivedFrom":makeQuery(id+"F10.opPattern","COPY",BODY,{"derivedFrom":makeQuery(id+"F7.opPattern","COPY",BODY,{"derivedFrom":makeQuery(id+"F6.opPattern","COPY",BODY,{"derivedFrom":makeQuery(id+"F5.opPattern","COPY",BODY,{"derivedFrom":makeQuery(id+"F4.opPattern","COPY",BODY,{"derivedFrom":makeQuery(id+"F3.opPattern","COPY",BODY,{"derivedFrom":makeQuery(id+"F2.opPattern","COPY",BODY,{"derivedFrom":makeQuery(id+"F1.opExtrude","SWEPT_BODY",BODY,{"disambiguationData":[OSD([sQuery(id+"F0.wireOp",EDGE,"E1.bottom"),sQuery(id+"F0.wireOp",EDGE,"E1.top"),sQuery(id+"F0.wireOp",EDGE,"E1.left"),sQuery(id+"F0.wireOp",EDGE,"E1.right")])]}),"instanceName":"1"}),"instanceName":"1"}),"instanceName":"1"}),"instanceName":"1"}),"instanceName":"1"}),"instanceName":"1"}),"instanceName":"1"}),"instanceName":"1"});
            var Q466;
            Q466=makeQuery(id+"F11.opPattern","COPY",BODY,{"derivedFrom":makeQuery(id+"F10.opPattern","COPY",BODY,{"derivedFrom":makeQuery(id+"F7.opPattern","COPY",BODY,{"derivedFrom":makeQuery(id+"F6.opPattern","COPY",BODY,{"derivedFrom":makeQuery(id+"F5.opPattern","COPY",BODY,{"derivedFrom":makeQuery(id+"F4.opPattern","COPY",BODY,{"derivedFrom":makeQuery(id+"F3.opPattern","COPY",BODY,{"derivedFrom":makeQuery(id+"F2.opPattern","COPY",BODY,{"derivedFrom":makeQuery(id+"F1.opExtrude","SWEPT_BODY",BODY,{"disambiguationData":[OSD([sQuery(id+"F0.wireOp",EDGE,"E2.bottom"),sQuery(id+"F0.wireOp",EDGE,"E2.top"),sQuery(id+"F0.wireOp",EDGE,"E2.left"),sQuery(id+"F0.wireOp",EDGE,"E2.right")])]}),"instanceName":"1"}),"instanceName":"1"}),"instanceName":"1"}),"instanceName":"1"}),"instanceName":"1"}),"instanceName":"1"}),"instanceName":"1"}),"instanceName":"1"});
            var Q467;
            Q467=makeQuery(id+"F11.opPattern","COPY",BODY,{"derivedFrom":makeQuery(id+"F10.opPattern","COPY",BODY,{"derivedFrom":makeQuery(id+"F8.opPattern","COPY",BODY,{"derivedFrom":makeQuery(id+"F1.opExtrude","SWEPT_BODY",BODY,{"disambiguationData":[OSD([sQuery(id+"F0.wireOp",EDGE,"E0.bottom"),sQuery(id+"F0.wireOp",EDGE,"E0.top"),sQuery(id+"F0.wireOp",EDGE,"E0.left"),sQuery(id+"F0.wireOp",EDGE,"E0.right")])]}),"instanceName":"1"}),"instanceName":"1"}),"instanceName":"1"});
            var Q468;
            Q468=makeQuery(id+"F11.opPattern","COPY",BODY,{"derivedFrom":makeQuery(id+"F10.opPattern","COPY",BODY,{"derivedFrom":makeQuery(id+"F8.opPattern","COPY",BODY,{"derivedFrom":makeQuery(id+"F1.opExtrude","SWEPT_BODY",BODY,{"disambiguationData":[OSD([sQuery(id+"F0.wireOp",EDGE,"E1.bottom"),sQuery(id+"F0.wireOp",EDGE,"E1.top"),sQuery(id+"F0.wireOp",EDGE,"E1.left"),sQuery(id+"F0.wireOp",EDGE,"E1.right")])]}),"instanceName":"1"}),"instanceName":"1"}),"instanceName":"1"});
            var Q469;
            Q469=makeQuery(id+"F11.opPattern","COPY",BODY,{"derivedFrom":makeQuery(id+"F10.opPattern","COPY",BODY,{"derivedFrom":makeQuery(id+"F8.opPattern","COPY",BODY,{"derivedFrom":makeQuery(id+"F1.opExtrude","SWEPT_BODY",BODY,{"disambiguationData":[OSD([sQuery(id+"F0.wireOp",EDGE,"E2.bottom"),sQuery(id+"F0.wireOp",EDGE,"E2.top"),sQuery(id+"F0.wireOp",EDGE,"E2.left"),sQuery(id+"F0.wireOp",EDGE,"E2.right")])]}),"instanceName":"1"}),"instanceName":"1"}),"instanceName":"1"});
            var Q470;
            Q470=makeQuery(id+"F11.opPattern","COPY",BODY,{"derivedFrom":makeQuery(id+"F10.opPattern","COPY",BODY,{"derivedFrom":makeQuery(id+"F8.opPattern","COPY",BODY,{"derivedFrom":makeQuery(id+"F2.opPattern","COPY",BODY,{"derivedFrom":makeQuery(id+"F1.opExtrude","SWEPT_BODY",BODY,{"disambiguationData":[OSD([sQuery(id+"F0.wireOp",EDGE,"E0.bottom"),sQuery(id+"F0.wireOp",EDGE,"E0.top"),sQuery(id+"F0.wireOp",EDGE,"E0.left"),sQuery(id+"F0.wireOp",EDGE,"E0.right")])]}),"instanceName":"1"}),"instanceName":"1"}),"instanceName":"1"}),"instanceName":"1"});
            var Q471;
            Q471=makeQuery(id+"F11.opPattern","COPY",BODY,{"derivedFrom":makeQuery(id+"F10.opPattern","COPY",BODY,{"derivedFrom":makeQuery(id+"F8.opPattern","COPY",BODY,{"derivedFrom":makeQuery(id+"F2.opPattern","COPY",BODY,{"derivedFrom":makeQuery(id+"F1.opExtrude","SWEPT_BODY",BODY,{"disambiguationData":[OSD([sQuery(id+"F0.wireOp",EDGE,"E1.bottom"),sQuery(id+"F0.wireOp",EDGE,"E1.top"),sQuery(id+"F0.wireOp",EDGE,"E1.left"),sQuery(id+"F0.wireOp",EDGE,"E1.right")])]}),"instanceName":"1"}),"instanceName":"1"}),"instanceName":"1"}),"instanceName":"1"});
            var Q472;
            Q472=makeQuery(id+"F11.opPattern","COPY",BODY,{"derivedFrom":makeQuery(id+"F10.opPattern","COPY",BODY,{"derivedFrom":makeQuery(id+"F8.opPattern","COPY",BODY,{"derivedFrom":makeQuery(id+"F2.opPattern","COPY",BODY,{"derivedFrom":makeQuery(id+"F1.opExtrude","SWEPT_BODY",BODY,{"disambiguationData":[OSD([sQuery(id+"F0.wireOp",EDGE,"E2.bottom"),sQuery(id+"F0.wireOp",EDGE,"E2.top"),sQuery(id+"F0.wireOp",EDGE,"E2.left"),sQuery(id+"F0.wireOp",EDGE,"E2.right")])]}),"instanceName":"1"}),"instanceName":"1"}),"instanceName":"1"}),"instanceName":"1"});
            var Q473;
            Q473=makeQuery(id+"F11.opPattern","COPY",BODY,{"derivedFrom":makeQuery(id+"F10.opPattern","COPY",BODY,{"derivedFrom":makeQuery(id+"F8.opPattern","COPY",BODY,{"derivedFrom":makeQuery(id+"F3.opPattern","COPY",BODY,{"derivedFrom":makeQuery(id+"F2.opPattern","COPY",BODY,{"derivedFrom":makeQuery(id+"F1.opExtrude","SWEPT_BODY",BODY,{"disambiguationData":[OSD([sQuery(id+"F0.wireOp",EDGE,"E0.bottom"),sQuery(id+"F0.wireOp",EDGE,"E0.top"),sQuery(id+"F0.wireOp",EDGE,"E0.left"),sQuery(id+"F0.wireOp",EDGE,"E0.right")])]}),"instanceName":"1"}),"instanceName":"1"}),"instanceName":"1"}),"instanceName":"1"}),"instanceName":"1"});
            var Q474;
            Q474=makeQuery(id+"F11.opPattern","COPY",BODY,{"derivedFrom":makeQuery(id+"F10.opPattern","COPY",BODY,{"derivedFrom":makeQuery(id+"F8.opPattern","COPY",BODY,{"derivedFrom":makeQuery(id+"F3.opPattern","COPY",BODY,{"derivedFrom":makeQuery(id+"F2.opPattern","COPY",BODY,{"derivedFrom":makeQuery(id+"F1.opExtrude","SWEPT_BODY",BODY,{"disambiguationData":[OSD([sQuery(id+"F0.wireOp",EDGE,"E1.bottom"),sQuery(id+"F0.wireOp",EDGE,"E1.top"),sQuery(id+"F0.wireOp",EDGE,"E1.left"),sQuery(id+"F0.wireOp",EDGE,"E1.right")])]}),"instanceName":"1"}),"instanceName":"1"}),"instanceName":"1"}),"instanceName":"1"}),"instanceName":"1"});
            var Q475;
            Q475=makeQuery(id+"F11.opPattern","COPY",BODY,{"derivedFrom":makeQuery(id+"F10.opPattern","COPY",BODY,{"derivedFrom":makeQuery(id+"F8.opPattern","COPY",BODY,{"derivedFrom":makeQuery(id+"F3.opPattern","COPY",BODY,{"derivedFrom":makeQuery(id+"F2.opPattern","COPY",BODY,{"derivedFrom":makeQuery(id+"F1.opExtrude","SWEPT_BODY",BODY,{"disambiguationData":[OSD([sQuery(id+"F0.wireOp",EDGE,"E2.bottom"),sQuery(id+"F0.wireOp",EDGE,"E2.top"),sQuery(id+"F0.wireOp",EDGE,"E2.left"),sQuery(id+"F0.wireOp",EDGE,"E2.right")])]}),"instanceName":"1"}),"instanceName":"1"}),"instanceName":"1"}),"instanceName":"1"}),"instanceName":"1"});
            var Q476;
            Q476=makeQuery(id+"F11.opPattern","COPY",BODY,{"derivedFrom":makeQuery(id+"F10.opPattern","COPY",BODY,{"derivedFrom":makeQuery(id+"F8.opPattern","COPY",BODY,{"derivedFrom":makeQuery(id+"F4.opPattern","COPY",BODY,{"derivedFrom":makeQuery(id+"F3.opPattern","COPY",BODY,{"derivedFrom":makeQuery(id+"F2.opPattern","COPY",BODY,{"derivedFrom":makeQuery(id+"F1.opExtrude","SWEPT_BODY",BODY,{"disambiguationData":[OSD([sQuery(id+"F0.wireOp",EDGE,"E0.bottom"),sQuery(id+"F0.wireOp",EDGE,"E0.top"),sQuery(id+"F0.wireOp",EDGE,"E0.left"),sQuery(id+"F0.wireOp",EDGE,"E0.right")])]}),"instanceName":"1"}),"instanceName":"1"}),"instanceName":"1"}),"instanceName":"1"}),"instanceName":"1"}),"instanceName":"1"});
            var Q477;
            Q477=makeQuery(id+"F11.opPattern","COPY",BODY,{"derivedFrom":makeQuery(id+"F10.opPattern","COPY",BODY,{"derivedFrom":makeQuery(id+"F8.opPattern","COPY",BODY,{"derivedFrom":makeQuery(id+"F4.opPattern","COPY",BODY,{"derivedFrom":makeQuery(id+"F3.opPattern","COPY",BODY,{"derivedFrom":makeQuery(id+"F2.opPattern","COPY",BODY,{"derivedFrom":makeQuery(id+"F1.opExtrude","SWEPT_BODY",BODY,{"disambiguationData":[OSD([sQuery(id+"F0.wireOp",EDGE,"E1.bottom"),sQuery(id+"F0.wireOp",EDGE,"E1.top"),sQuery(id+"F0.wireOp",EDGE,"E1.left"),sQuery(id+"F0.wireOp",EDGE,"E1.right")])]}),"instanceName":"1"}),"instanceName":"1"}),"instanceName":"1"}),"instanceName":"1"}),"instanceName":"1"}),"instanceName":"1"});
            var Q478;
            Q478=makeQuery(id+"F11.opPattern","COPY",BODY,{"derivedFrom":makeQuery(id+"F10.opPattern","COPY",BODY,{"derivedFrom":makeQuery(id+"F8.opPattern","COPY",BODY,{"derivedFrom":makeQuery(id+"F4.opPattern","COPY",BODY,{"derivedFrom":makeQuery(id+"F3.opPattern","COPY",BODY,{"derivedFrom":makeQuery(id+"F2.opPattern","COPY",BODY,{"derivedFrom":makeQuery(id+"F1.opExtrude","SWEPT_BODY",BODY,{"disambiguationData":[OSD([sQuery(id+"F0.wireOp",EDGE,"E2.bottom"),sQuery(id+"F0.wireOp",EDGE,"E2.top"),sQuery(id+"F0.wireOp",EDGE,"E2.left"),sQuery(id+"F0.wireOp",EDGE,"E2.right")])]}),"instanceName":"1"}),"instanceName":"1"}),"instanceName":"1"}),"instanceName":"1"}),"instanceName":"1"}),"instanceName":"1"});
            var Q479;
            Q479=makeQuery(id+"F11.opPattern","COPY",BODY,{"derivedFrom":makeQuery(id+"F10.opPattern","COPY",BODY,{"derivedFrom":makeQuery(id+"F8.opPattern","COPY",BODY,{"derivedFrom":makeQuery(id+"F5.opPattern","COPY",BODY,{"derivedFrom":makeQuery(id+"F4.opPattern","COPY",BODY,{"derivedFrom":makeQuery(id+"F3.opPattern","COPY",BODY,{"derivedFrom":makeQuery(id+"F2.opPattern","COPY",BODY,{"derivedFrom":makeQuery(id+"F1.opExtrude","SWEPT_BODY",BODY,{"disambiguationData":[OSD([sQuery(id+"F0.wireOp",EDGE,"E0.bottom"),sQuery(id+"F0.wireOp",EDGE,"E0.top"),sQuery(id+"F0.wireOp",EDGE,"E0.left"),sQuery(id+"F0.wireOp",EDGE,"E0.right")])]}),"instanceName":"1"}),"instanceName":"1"}),"instanceName":"1"}),"instanceName":"1"}),"instanceName":"1"}),"instanceName":"1"}),"instanceName":"1"});
            var Q480;
            Q480=makeQuery(id+"F11.opPattern","COPY",BODY,{"derivedFrom":makeQuery(id+"F10.opPattern","COPY",BODY,{"derivedFrom":makeQuery(id+"F8.opPattern","COPY",BODY,{"derivedFrom":makeQuery(id+"F5.opPattern","COPY",BODY,{"derivedFrom":makeQuery(id+"F4.opPattern","COPY",BODY,{"derivedFrom":makeQuery(id+"F3.opPattern","COPY",BODY,{"derivedFrom":makeQuery(id+"F2.opPattern","COPY",BODY,{"derivedFrom":makeQuery(id+"F1.opExtrude","SWEPT_BODY",BODY,{"disambiguationData":[OSD([sQuery(id+"F0.wireOp",EDGE,"E1.bottom"),sQuery(id+"F0.wireOp",EDGE,"E1.top"),sQuery(id+"F0.wireOp",EDGE,"E1.left"),sQuery(id+"F0.wireOp",EDGE,"E1.right")])]}),"instanceName":"1"}),"instanceName":"1"}),"instanceName":"1"}),"instanceName":"1"}),"instanceName":"1"}),"instanceName":"1"}),"instanceName":"1"});
            var Q481;
            Q481=makeQuery(id+"F11.opPattern","COPY",BODY,{"derivedFrom":makeQuery(id+"F10.opPattern","COPY",BODY,{"derivedFrom":makeQuery(id+"F8.opPattern","COPY",BODY,{"derivedFrom":makeQuery(id+"F5.opPattern","COPY",BODY,{"derivedFrom":makeQuery(id+"F4.opPattern","COPY",BODY,{"derivedFrom":makeQuery(id+"F3.opPattern","COPY",BODY,{"derivedFrom":makeQuery(id+"F2.opPattern","COPY",BODY,{"derivedFrom":makeQuery(id+"F1.opExtrude","SWEPT_BODY",BODY,{"disambiguationData":[OSD([sQuery(id+"F0.wireOp",EDGE,"E2.bottom"),sQuery(id+"F0.wireOp",EDGE,"E2.top"),sQuery(id+"F0.wireOp",EDGE,"E2.left"),sQuery(id+"F0.wireOp",EDGE,"E2.right")])]}),"instanceName":"1"}),"instanceName":"1"}),"instanceName":"1"}),"instanceName":"1"}),"instanceName":"1"}),"instanceName":"1"}),"instanceName":"1"});
            var Q482;
            Q482=makeQuery(id+"F11.opPattern","COPY",BODY,{"derivedFrom":makeQuery(id+"F10.opPattern","COPY",BODY,{"derivedFrom":makeQuery(id+"F8.opPattern","COPY",BODY,{"derivedFrom":makeQuery(id+"F6.opPattern","COPY",BODY,{"derivedFrom":makeQuery(id+"F5.opPattern","COPY",BODY,{"derivedFrom":makeQuery(id+"F4.opPattern","COPY",BODY,{"derivedFrom":makeQuery(id+"F3.opPattern","COPY",BODY,{"derivedFrom":makeQuery(id+"F2.opPattern","COPY",BODY,{"derivedFrom":makeQuery(id+"F1.opExtrude","SWEPT_BODY",BODY,{"disambiguationData":[OSD([sQuery(id+"F0.wireOp",EDGE,"E0.bottom"),sQuery(id+"F0.wireOp",EDGE,"E0.top"),sQuery(id+"F0.wireOp",EDGE,"E0.left"),sQuery(id+"F0.wireOp",EDGE,"E0.right")])]}),"instanceName":"1"}),"instanceName":"1"}),"instanceName":"1"}),"instanceName":"1"}),"instanceName":"1"}),"instanceName":"1"}),"instanceName":"1"}),"instanceName":"1"});
            var Q483;
            Q483=makeQuery(id+"F11.opPattern","COPY",BODY,{"derivedFrom":makeQuery(id+"F10.opPattern","COPY",BODY,{"derivedFrom":makeQuery(id+"F8.opPattern","COPY",BODY,{"derivedFrom":makeQuery(id+"F6.opPattern","COPY",BODY,{"derivedFrom":makeQuery(id+"F5.opPattern","COPY",BODY,{"derivedFrom":makeQuery(id+"F4.opPattern","COPY",BODY,{"derivedFrom":makeQuery(id+"F3.opPattern","COPY",BODY,{"derivedFrom":makeQuery(id+"F2.opPattern","COPY",BODY,{"derivedFrom":makeQuery(id+"F1.opExtrude","SWEPT_BODY",BODY,{"disambiguationData":[OSD([sQuery(id+"F0.wireOp",EDGE,"E1.bottom"),sQuery(id+"F0.wireOp",EDGE,"E1.top"),sQuery(id+"F0.wireOp",EDGE,"E1.left"),sQuery(id+"F0.wireOp",EDGE,"E1.right")])]}),"instanceName":"1"}),"instanceName":"1"}),"instanceName":"1"}),"instanceName":"1"}),"instanceName":"1"}),"instanceName":"1"}),"instanceName":"1"}),"instanceName":"1"});
            var Q484;
            Q484=makeQuery(id+"F11.opPattern","COPY",BODY,{"derivedFrom":makeQuery(id+"F10.opPattern","COPY",BODY,{"derivedFrom":makeQuery(id+"F8.opPattern","COPY",BODY,{"derivedFrom":makeQuery(id+"F6.opPattern","COPY",BODY,{"derivedFrom":makeQuery(id+"F5.opPattern","COPY",BODY,{"derivedFrom":makeQuery(id+"F4.opPattern","COPY",BODY,{"derivedFrom":makeQuery(id+"F3.opPattern","COPY",BODY,{"derivedFrom":makeQuery(id+"F2.opPattern","COPY",BODY,{"derivedFrom":makeQuery(id+"F1.opExtrude","SWEPT_BODY",BODY,{"disambiguationData":[OSD([sQuery(id+"F0.wireOp",EDGE,"E2.bottom"),sQuery(id+"F0.wireOp",EDGE,"E2.top"),sQuery(id+"F0.wireOp",EDGE,"E2.left"),sQuery(id+"F0.wireOp",EDGE,"E2.right")])]}),"instanceName":"1"}),"instanceName":"1"}),"instanceName":"1"}),"instanceName":"1"}),"instanceName":"1"}),"instanceName":"1"}),"instanceName":"1"}),"instanceName":"1"});
            var Q485;
            Q485=makeQuery(id+"F11.opPattern","COPY",BODY,{"derivedFrom":makeQuery(id+"F10.opPattern","COPY",BODY,{"derivedFrom":makeQuery(id+"F8.opPattern","COPY",BODY,{"derivedFrom":makeQuery(id+"F7.opPattern","COPY",BODY,{"derivedFrom":makeQuery(id+"F1.opExtrude","SWEPT_BODY",BODY,{"disambiguationData":[OSD([sQuery(id+"F0.wireOp",EDGE,"E0.bottom"),sQuery(id+"F0.wireOp",EDGE,"E0.top"),sQuery(id+"F0.wireOp",EDGE,"E0.left"),sQuery(id+"F0.wireOp",EDGE,"E0.right")])]}),"instanceName":"1"}),"instanceName":"1"}),"instanceName":"1"}),"instanceName":"1"});
            var Q486;
            Q486=makeQuery(id+"F11.opPattern","COPY",BODY,{"derivedFrom":makeQuery(id+"F10.opPattern","COPY",BODY,{"derivedFrom":makeQuery(id+"F8.opPattern","COPY",BODY,{"derivedFrom":makeQuery(id+"F7.opPattern","COPY",BODY,{"derivedFrom":makeQuery(id+"F1.opExtrude","SWEPT_BODY",BODY,{"disambiguationData":[OSD([sQuery(id+"F0.wireOp",EDGE,"E1.bottom"),sQuery(id+"F0.wireOp",EDGE,"E1.top"),sQuery(id+"F0.wireOp",EDGE,"E1.left"),sQuery(id+"F0.wireOp",EDGE,"E1.right")])]}),"instanceName":"1"}),"instanceName":"1"}),"instanceName":"1"}),"instanceName":"1"});
            var Q487;
            Q487=makeQuery(id+"F11.opPattern","COPY",BODY,{"derivedFrom":makeQuery(id+"F10.opPattern","COPY",BODY,{"derivedFrom":makeQuery(id+"F8.opPattern","COPY",BODY,{"derivedFrom":makeQuery(id+"F7.opPattern","COPY",BODY,{"derivedFrom":makeQuery(id+"F1.opExtrude","SWEPT_BODY",BODY,{"disambiguationData":[OSD([sQuery(id+"F0.wireOp",EDGE,"E2.bottom"),sQuery(id+"F0.wireOp",EDGE,"E2.top"),sQuery(id+"F0.wireOp",EDGE,"E2.left"),sQuery(id+"F0.wireOp",EDGE,"E2.right")])]}),"instanceName":"1"}),"instanceName":"1"}),"instanceName":"1"}),"instanceName":"1"});
            var Q488;
            Q488=makeQuery(id+"F11.opPattern","COPY",BODY,{"derivedFrom":makeQuery(id+"F10.opPattern","COPY",BODY,{"derivedFrom":makeQuery(id+"F8.opPattern","COPY",BODY,{"derivedFrom":makeQuery(id+"F7.opPattern","COPY",BODY,{"derivedFrom":makeQuery(id+"F2.opPattern","COPY",BODY,{"derivedFrom":makeQuery(id+"F1.opExtrude","SWEPT_BODY",BODY,{"disambiguationData":[OSD([sQuery(id+"F0.wireOp",EDGE,"E0.bottom"),sQuery(id+"F0.wireOp",EDGE,"E0.top"),sQuery(id+"F0.wireOp",EDGE,"E0.left"),sQuery(id+"F0.wireOp",EDGE,"E0.right")])]}),"instanceName":"1"}),"instanceName":"1"}),"instanceName":"1"}),"instanceName":"1"}),"instanceName":"1"});
            var Q489;
            Q489=makeQuery(id+"F11.opPattern","COPY",BODY,{"derivedFrom":makeQuery(id+"F10.opPattern","COPY",BODY,{"derivedFrom":makeQuery(id+"F8.opPattern","COPY",BODY,{"derivedFrom":makeQuery(id+"F7.opPattern","COPY",BODY,{"derivedFrom":makeQuery(id+"F2.opPattern","COPY",BODY,{"derivedFrom":makeQuery(id+"F1.opExtrude","SWEPT_BODY",BODY,{"disambiguationData":[OSD([sQuery(id+"F0.wireOp",EDGE,"E1.bottom"),sQuery(id+"F0.wireOp",EDGE,"E1.top"),sQuery(id+"F0.wireOp",EDGE,"E1.left"),sQuery(id+"F0.wireOp",EDGE,"E1.right")])]}),"instanceName":"1"}),"instanceName":"1"}),"instanceName":"1"}),"instanceName":"1"}),"instanceName":"1"});
            var Q490;
            Q490=makeQuery(id+"F11.opPattern","COPY",BODY,{"derivedFrom":makeQuery(id+"F10.opPattern","COPY",BODY,{"derivedFrom":makeQuery(id+"F8.opPattern","COPY",BODY,{"derivedFrom":makeQuery(id+"F7.opPattern","COPY",BODY,{"derivedFrom":makeQuery(id+"F2.opPattern","COPY",BODY,{"derivedFrom":makeQuery(id+"F1.opExtrude","SWEPT_BODY",BODY,{"disambiguationData":[OSD([sQuery(id+"F0.wireOp",EDGE,"E2.bottom"),sQuery(id+"F0.wireOp",EDGE,"E2.top"),sQuery(id+"F0.wireOp",EDGE,"E2.left"),sQuery(id+"F0.wireOp",EDGE,"E2.right")])]}),"instanceName":"1"}),"instanceName":"1"}),"instanceName":"1"}),"instanceName":"1"}),"instanceName":"1"});
            var Q491;
            Q491=makeQuery(id+"F11.opPattern","COPY",BODY,{"derivedFrom":makeQuery(id+"F10.opPattern","COPY",BODY,{"derivedFrom":makeQuery(id+"F8.opPattern","COPY",BODY,{"derivedFrom":makeQuery(id+"F7.opPattern","COPY",BODY,{"derivedFrom":makeQuery(id+"F3.opPattern","COPY",BODY,{"derivedFrom":makeQuery(id+"F2.opPattern","COPY",BODY,{"derivedFrom":makeQuery(id+"F1.opExtrude","SWEPT_BODY",BODY,{"disambiguationData":[OSD([sQuery(id+"F0.wireOp",EDGE,"E0.bottom"),sQuery(id+"F0.wireOp",EDGE,"E0.top"),sQuery(id+"F0.wireOp",EDGE,"E0.left"),sQuery(id+"F0.wireOp",EDGE,"E0.right")])]}),"instanceName":"1"}),"instanceName":"1"}),"instanceName":"1"}),"instanceName":"1"}),"instanceName":"1"}),"instanceName":"1"});
            var Q492;
            Q492=makeQuery(id+"F11.opPattern","COPY",BODY,{"derivedFrom":makeQuery(id+"F10.opPattern","COPY",BODY,{"derivedFrom":makeQuery(id+"F8.opPattern","COPY",BODY,{"derivedFrom":makeQuery(id+"F7.opPattern","COPY",BODY,{"derivedFrom":makeQuery(id+"F3.opPattern","COPY",BODY,{"derivedFrom":makeQuery(id+"F2.opPattern","COPY",BODY,{"derivedFrom":makeQuery(id+"F1.opExtrude","SWEPT_BODY",BODY,{"disambiguationData":[OSD([sQuery(id+"F0.wireOp",EDGE,"E1.bottom"),sQuery(id+"F0.wireOp",EDGE,"E1.top"),sQuery(id+"F0.wireOp",EDGE,"E1.left"),sQuery(id+"F0.wireOp",EDGE,"E1.right")])]}),"instanceName":"1"}),"instanceName":"1"}),"instanceName":"1"}),"instanceName":"1"}),"instanceName":"1"}),"instanceName":"1"});
            var Q493;
            Q493=makeQuery(id+"F11.opPattern","COPY",BODY,{"derivedFrom":makeQuery(id+"F10.opPattern","COPY",BODY,{"derivedFrom":makeQuery(id+"F8.opPattern","COPY",BODY,{"derivedFrom":makeQuery(id+"F7.opPattern","COPY",BODY,{"derivedFrom":makeQuery(id+"F3.opPattern","COPY",BODY,{"derivedFrom":makeQuery(id+"F2.opPattern","COPY",BODY,{"derivedFrom":makeQuery(id+"F1.opExtrude","SWEPT_BODY",BODY,{"disambiguationData":[OSD([sQuery(id+"F0.wireOp",EDGE,"E2.bottom"),sQuery(id+"F0.wireOp",EDGE,"E2.top"),sQuery(id+"F0.wireOp",EDGE,"E2.left"),sQuery(id+"F0.wireOp",EDGE,"E2.right")])]}),"instanceName":"1"}),"instanceName":"1"}),"instanceName":"1"}),"instanceName":"1"}),"instanceName":"1"}),"instanceName":"1"});
            var Q494;
            Q494=makeQuery(id+"F11.opPattern","COPY",BODY,{"derivedFrom":makeQuery(id+"F10.opPattern","COPY",BODY,{"derivedFrom":makeQuery(id+"F8.opPattern","COPY",BODY,{"derivedFrom":makeQuery(id+"F7.opPattern","COPY",BODY,{"derivedFrom":makeQuery(id+"F4.opPattern","COPY",BODY,{"derivedFrom":makeQuery(id+"F3.opPattern","COPY",BODY,{"derivedFrom":makeQuery(id+"F2.opPattern","COPY",BODY,{"derivedFrom":makeQuery(id+"F1.opExtrude","SWEPT_BODY",BODY,{"disambiguationData":[OSD([sQuery(id+"F0.wireOp",EDGE,"E0.bottom"),sQuery(id+"F0.wireOp",EDGE,"E0.top"),sQuery(id+"F0.wireOp",EDGE,"E0.left"),sQuery(id+"F0.wireOp",EDGE,"E0.right")])]}),"instanceName":"1"}),"instanceName":"1"}),"instanceName":"1"}),"instanceName":"1"}),"instanceName":"1"}),"instanceName":"1"}),"instanceName":"1"});
            var Q495;
            Q495=makeQuery(id+"F11.opPattern","COPY",BODY,{"derivedFrom":makeQuery(id+"F10.opPattern","COPY",BODY,{"derivedFrom":makeQuery(id+"F8.opPattern","COPY",BODY,{"derivedFrom":makeQuery(id+"F7.opPattern","COPY",BODY,{"derivedFrom":makeQuery(id+"F4.opPattern","COPY",BODY,{"derivedFrom":makeQuery(id+"F3.opPattern","COPY",BODY,{"derivedFrom":makeQuery(id+"F2.opPattern","COPY",BODY,{"derivedFrom":makeQuery(id+"F1.opExtrude","SWEPT_BODY",BODY,{"disambiguationData":[OSD([sQuery(id+"F0.wireOp",EDGE,"E1.bottom"),sQuery(id+"F0.wireOp",EDGE,"E1.top"),sQuery(id+"F0.wireOp",EDGE,"E1.left"),sQuery(id+"F0.wireOp",EDGE,"E1.right")])]}),"instanceName":"1"}),"instanceName":"1"}),"instanceName":"1"}),"instanceName":"1"}),"instanceName":"1"}),"instanceName":"1"}),"instanceName":"1"});
            var Q496;
            Q496=makeQuery(id+"F11.opPattern","COPY",BODY,{"derivedFrom":makeQuery(id+"F10.opPattern","COPY",BODY,{"derivedFrom":makeQuery(id+"F8.opPattern","COPY",BODY,{"derivedFrom":makeQuery(id+"F7.opPattern","COPY",BODY,{"derivedFrom":makeQuery(id+"F4.opPattern","COPY",BODY,{"derivedFrom":makeQuery(id+"F3.opPattern","COPY",BODY,{"derivedFrom":makeQuery(id+"F2.opPattern","COPY",BODY,{"derivedFrom":makeQuery(id+"F1.opExtrude","SWEPT_BODY",BODY,{"disambiguationData":[OSD([sQuery(id+"F0.wireOp",EDGE,"E2.bottom"),sQuery(id+"F0.wireOp",EDGE,"E2.top"),sQuery(id+"F0.wireOp",EDGE,"E2.left"),sQuery(id+"F0.wireOp",EDGE,"E2.right")])]}),"instanceName":"1"}),"instanceName":"1"}),"instanceName":"1"}),"instanceName":"1"}),"instanceName":"1"}),"instanceName":"1"}),"instanceName":"1"});
            var Q497;
            Q497=makeQuery(id+"F11.opPattern","COPY",BODY,{"derivedFrom":makeQuery(id+"F10.opPattern","COPY",BODY,{"derivedFrom":makeQuery(id+"F8.opPattern","COPY",BODY,{"derivedFrom":makeQuery(id+"F7.opPattern","COPY",BODY,{"derivedFrom":makeQuery(id+"F5.opPattern","COPY",BODY,{"derivedFrom":makeQuery(id+"F4.opPattern","COPY",BODY,{"derivedFrom":makeQuery(id+"F3.opPattern","COPY",BODY,{"derivedFrom":makeQuery(id+"F2.opPattern","COPY",BODY,{"derivedFrom":makeQuery(id+"F1.opExtrude","SWEPT_BODY",BODY,{"disambiguationData":[OSD([sQuery(id+"F0.wireOp",EDGE,"E0.bottom"),sQuery(id+"F0.wireOp",EDGE,"E0.top"),sQuery(id+"F0.wireOp",EDGE,"E0.left"),sQuery(id+"F0.wireOp",EDGE,"E0.right")])]}),"instanceName":"1"}),"instanceName":"1"}),"instanceName":"1"}),"instanceName":"1"}),"instanceName":"1"}),"instanceName":"1"}),"instanceName":"1"}),"instanceName":"1"});
            var Q498;
            Q498=makeQuery(id+"F11.opPattern","COPY",BODY,{"derivedFrom":makeQuery(id+"F10.opPattern","COPY",BODY,{"derivedFrom":makeQuery(id+"F8.opPattern","COPY",BODY,{"derivedFrom":makeQuery(id+"F7.opPattern","COPY",BODY,{"derivedFrom":makeQuery(id+"F5.opPattern","COPY",BODY,{"derivedFrom":makeQuery(id+"F4.opPattern","COPY",BODY,{"derivedFrom":makeQuery(id+"F3.opPattern","COPY",BODY,{"derivedFrom":makeQuery(id+"F2.opPattern","COPY",BODY,{"derivedFrom":makeQuery(id+"F1.opExtrude","SWEPT_BODY",BODY,{"disambiguationData":[OSD([sQuery(id+"F0.wireOp",EDGE,"E1.bottom"),sQuery(id+"F0.wireOp",EDGE,"E1.top"),sQuery(id+"F0.wireOp",EDGE,"E1.left"),sQuery(id+"F0.wireOp",EDGE,"E1.right")])]}),"instanceName":"1"}),"instanceName":"1"}),"instanceName":"1"}),"instanceName":"1"}),"instanceName":"1"}),"instanceName":"1"}),"instanceName":"1"}),"instanceName":"1"});
            var Q499;
            Q499=makeQuery(id+"F11.opPattern","COPY",BODY,{"derivedFrom":makeQuery(id+"F10.opPattern","COPY",BODY,{"derivedFrom":makeQuery(id+"F8.opPattern","COPY",BODY,{"derivedFrom":makeQuery(id+"F7.opPattern","COPY",BODY,{"derivedFrom":makeQuery(id+"F5.opPattern","COPY",BODY,{"derivedFrom":makeQuery(id+"F4.opPattern","COPY",BODY,{"derivedFrom":makeQuery(id+"F3.opPattern","COPY",BODY,{"derivedFrom":makeQuery(id+"F2.opPattern","COPY",BODY,{"derivedFrom":makeQuery(id+"F1.opExtrude","SWEPT_BODY",BODY,{"disambiguationData":[OSD([sQuery(id+"F0.wireOp",EDGE,"E2.bottom"),sQuery(id+"F0.wireOp",EDGE,"E2.top"),sQuery(id+"F0.wireOp",EDGE,"E2.left"),sQuery(id+"F0.wireOp",EDGE,"E2.right")])]}),"instanceName":"1"}),"instanceName":"1"}),"instanceName":"1"}),"instanceName":"1"}),"instanceName":"1"}),"instanceName":"1"}),"instanceName":"1"}),"instanceName":"1"});
            var Q500;
            Q500=makeQuery(id+"F11.opPattern","COPY",BODY,{"derivedFrom":makeQuery(id+"F10.opPattern","COPY",BODY,{"derivedFrom":makeQuery(id+"F8.opPattern","COPY",BODY,{"derivedFrom":makeQuery(id+"F7.opPattern","COPY",BODY,{"derivedFrom":makeQuery(id+"F6.opPattern","COPY",BODY,{"derivedFrom":makeQuery(id+"F5.opPattern","COPY",BODY,{"derivedFrom":makeQuery(id+"F4.opPattern","COPY",BODY,{"derivedFrom":makeQuery(id+"F3.opPattern","COPY",BODY,{"derivedFrom":makeQuery(id+"F2.opPattern","COPY",BODY,{"derivedFrom":makeQuery(id+"F1.opExtrude","SWEPT_BODY",BODY,{"disambiguationData":[OSD([sQuery(id+"F0.wireOp",EDGE,"E0.bottom"),sQuery(id+"F0.wireOp",EDGE,"E0.top"),sQuery(id+"F0.wireOp",EDGE,"E0.left"),sQuery(id+"F0.wireOp",EDGE,"E0.right")])]}),"instanceName":"1"}),"instanceName":"1"}),"instanceName":"1"}),"instanceName":"1"}),"instanceName":"1"}),"instanceName":"1"}),"instanceName":"1"}),"instanceName":"1"}),"instanceName":"1"});
            var Q501;
            Q501=makeQuery(id+"F11.opPattern","COPY",BODY,{"derivedFrom":makeQuery(id+"F10.opPattern","COPY",BODY,{"derivedFrom":makeQuery(id+"F8.opPattern","COPY",BODY,{"derivedFrom":makeQuery(id+"F7.opPattern","COPY",BODY,{"derivedFrom":makeQuery(id+"F6.opPattern","COPY",BODY,{"derivedFrom":makeQuery(id+"F5.opPattern","COPY",BODY,{"derivedFrom":makeQuery(id+"F4.opPattern","COPY",BODY,{"derivedFrom":makeQuery(id+"F3.opPattern","COPY",BODY,{"derivedFrom":makeQuery(id+"F2.opPattern","COPY",BODY,{"derivedFrom":makeQuery(id+"F1.opExtrude","SWEPT_BODY",BODY,{"disambiguationData":[OSD([sQuery(id+"F0.wireOp",EDGE,"E1.bottom"),sQuery(id+"F0.wireOp",EDGE,"E1.top"),sQuery(id+"F0.wireOp",EDGE,"E1.left"),sQuery(id+"F0.wireOp",EDGE,"E1.right")])]}),"instanceName":"1"}),"instanceName":"1"}),"instanceName":"1"}),"instanceName":"1"}),"instanceName":"1"}),"instanceName":"1"}),"instanceName":"1"}),"instanceName":"1"}),"instanceName":"1"});
            var Q502;
            Q502=makeQuery(id+"F11.opPattern","COPY",BODY,{"derivedFrom":makeQuery(id+"F10.opPattern","COPY",BODY,{"derivedFrom":makeQuery(id+"F8.opPattern","COPY",BODY,{"derivedFrom":makeQuery(id+"F7.opPattern","COPY",BODY,{"derivedFrom":makeQuery(id+"F6.opPattern","COPY",BODY,{"derivedFrom":makeQuery(id+"F5.opPattern","COPY",BODY,{"derivedFrom":makeQuery(id+"F4.opPattern","COPY",BODY,{"derivedFrom":makeQuery(id+"F3.opPattern","COPY",BODY,{"derivedFrom":makeQuery(id+"F2.opPattern","COPY",BODY,{"derivedFrom":makeQuery(id+"F1.opExtrude","SWEPT_BODY",BODY,{"disambiguationData":[OSD([sQuery(id+"F0.wireOp",EDGE,"E2.bottom"),sQuery(id+"F0.wireOp",EDGE,"E2.top"),sQuery(id+"F0.wireOp",EDGE,"E2.left"),sQuery(id+"F0.wireOp",EDGE,"E2.right")])]}),"instanceName":"1"}),"instanceName":"1"}),"instanceName":"1"}),"instanceName":"1"}),"instanceName":"1"}),"instanceName":"1"}),"instanceName":"1"}),"instanceName":"1"}),"instanceName":"1"});
            var Q503;
            Q503=makeQuery(id+"F11.opPattern","COPY",BODY,{"derivedFrom":makeQuery(id+"F10.opPattern","COPY",BODY,{"derivedFrom":makeQuery(id+"F9.opPattern","COPY",BODY,{"derivedFrom":makeQuery(id+"F1.opExtrude","SWEPT_BODY",BODY,{"disambiguationData":[OSD([sQuery(id+"F0.wireOp",EDGE,"E0.bottom"),sQuery(id+"F0.wireOp",EDGE,"E0.top"),sQuery(id+"F0.wireOp",EDGE,"E0.left"),sQuery(id+"F0.wireOp",EDGE,"E0.right")])]}),"instanceName":"1"}),"instanceName":"1"}),"instanceName":"1"});
            var Q504;
            Q504=makeQuery(id+"F11.opPattern","COPY",BODY,{"derivedFrom":makeQuery(id+"F10.opPattern","COPY",BODY,{"derivedFrom":makeQuery(id+"F9.opPattern","COPY",BODY,{"derivedFrom":makeQuery(id+"F1.opExtrude","SWEPT_BODY",BODY,{"disambiguationData":[OSD([sQuery(id+"F0.wireOp",EDGE,"E1.bottom"),sQuery(id+"F0.wireOp",EDGE,"E1.top"),sQuery(id+"F0.wireOp",EDGE,"E1.left"),sQuery(id+"F0.wireOp",EDGE,"E1.right")])]}),"instanceName":"1"}),"instanceName":"1"}),"instanceName":"1"});
            var Q505;
            Q505=makeQuery(id+"F11.opPattern","COPY",BODY,{"derivedFrom":makeQuery(id+"F10.opPattern","COPY",BODY,{"derivedFrom":makeQuery(id+"F9.opPattern","COPY",BODY,{"derivedFrom":makeQuery(id+"F1.opExtrude","SWEPT_BODY",BODY,{"disambiguationData":[OSD([sQuery(id+"F0.wireOp",EDGE,"E2.bottom"),sQuery(id+"F0.wireOp",EDGE,"E2.top"),sQuery(id+"F0.wireOp",EDGE,"E2.left"),sQuery(id+"F0.wireOp",EDGE,"E2.right")])]}),"instanceName":"1"}),"instanceName":"1"}),"instanceName":"1"});
            var Q506;
            Q506=makeQuery(id+"F11.opPattern","COPY",BODY,{"derivedFrom":makeQuery(id+"F10.opPattern","COPY",BODY,{"derivedFrom":makeQuery(id+"F9.opPattern","COPY",BODY,{"derivedFrom":makeQuery(id+"F2.opPattern","COPY",BODY,{"derivedFrom":makeQuery(id+"F1.opExtrude","SWEPT_BODY",BODY,{"disambiguationData":[OSD([sQuery(id+"F0.wireOp",EDGE,"E0.bottom"),sQuery(id+"F0.wireOp",EDGE,"E0.top"),sQuery(id+"F0.wireOp",EDGE,"E0.left"),sQuery(id+"F0.wireOp",EDGE,"E0.right")])]}),"instanceName":"1"}),"instanceName":"1"}),"instanceName":"1"}),"instanceName":"1"});
            var Q507;
            Q507=makeQuery(id+"F11.opPattern","COPY",BODY,{"derivedFrom":makeQuery(id+"F10.opPattern","COPY",BODY,{"derivedFrom":makeQuery(id+"F9.opPattern","COPY",BODY,{"derivedFrom":makeQuery(id+"F2.opPattern","COPY",BODY,{"derivedFrom":makeQuery(id+"F1.opExtrude","SWEPT_BODY",BODY,{"disambiguationData":[OSD([sQuery(id+"F0.wireOp",EDGE,"E1.bottom"),sQuery(id+"F0.wireOp",EDGE,"E1.top"),sQuery(id+"F0.wireOp",EDGE,"E1.left"),sQuery(id+"F0.wireOp",EDGE,"E1.right")])]}),"instanceName":"1"}),"instanceName":"1"}),"instanceName":"1"}),"instanceName":"1"});
            var Q508;
            Q508=makeQuery(id+"F11.opPattern","COPY",BODY,{"derivedFrom":makeQuery(id+"F10.opPattern","COPY",BODY,{"derivedFrom":makeQuery(id+"F9.opPattern","COPY",BODY,{"derivedFrom":makeQuery(id+"F2.opPattern","COPY",BODY,{"derivedFrom":makeQuery(id+"F1.opExtrude","SWEPT_BODY",BODY,{"disambiguationData":[OSD([sQuery(id+"F0.wireOp",EDGE,"E2.bottom"),sQuery(id+"F0.wireOp",EDGE,"E2.top"),sQuery(id+"F0.wireOp",EDGE,"E2.left"),sQuery(id+"F0.wireOp",EDGE,"E2.right")])]}),"instanceName":"1"}),"instanceName":"1"}),"instanceName":"1"}),"instanceName":"1"});
            var Q509;
            Q509=makeQuery(id+"F11.opPattern","COPY",BODY,{"derivedFrom":makeQuery(id+"F10.opPattern","COPY",BODY,{"derivedFrom":makeQuery(id+"F9.opPattern","COPY",BODY,{"derivedFrom":makeQuery(id+"F3.opPattern","COPY",BODY,{"derivedFrom":makeQuery(id+"F2.opPattern","COPY",BODY,{"derivedFrom":makeQuery(id+"F1.opExtrude","SWEPT_BODY",BODY,{"disambiguationData":[OSD([sQuery(id+"F0.wireOp",EDGE,"E0.bottom"),sQuery(id+"F0.wireOp",EDGE,"E0.top"),sQuery(id+"F0.wireOp",EDGE,"E0.left"),sQuery(id+"F0.wireOp",EDGE,"E0.right")])]}),"instanceName":"1"}),"instanceName":"1"}),"instanceName":"1"}),"instanceName":"1"}),"instanceName":"1"});
            var Q510;
            Q510=makeQuery(id+"F11.opPattern","COPY",BODY,{"derivedFrom":makeQuery(id+"F10.opPattern","COPY",BODY,{"derivedFrom":makeQuery(id+"F9.opPattern","COPY",BODY,{"derivedFrom":makeQuery(id+"F3.opPattern","COPY",BODY,{"derivedFrom":makeQuery(id+"F2.opPattern","COPY",BODY,{"derivedFrom":makeQuery(id+"F1.opExtrude","SWEPT_BODY",BODY,{"disambiguationData":[OSD([sQuery(id+"F0.wireOp",EDGE,"E1.bottom"),sQuery(id+"F0.wireOp",EDGE,"E1.top"),sQuery(id+"F0.wireOp",EDGE,"E1.left"),sQuery(id+"F0.wireOp",EDGE,"E1.right")])]}),"instanceName":"1"}),"instanceName":"1"}),"instanceName":"1"}),"instanceName":"1"}),"instanceName":"1"});
            var Q511;
            Q511=makeQuery(id+"F11.opPattern","COPY",BODY,{"derivedFrom":makeQuery(id+"F10.opPattern","COPY",BODY,{"derivedFrom":makeQuery(id+"F9.opPattern","COPY",BODY,{"derivedFrom":makeQuery(id+"F3.opPattern","COPY",BODY,{"derivedFrom":makeQuery(id+"F2.opPattern","COPY",BODY,{"derivedFrom":makeQuery(id+"F1.opExtrude","SWEPT_BODY",BODY,{"disambiguationData":[OSD([sQuery(id+"F0.wireOp",EDGE,"E2.bottom"),sQuery(id+"F0.wireOp",EDGE,"E2.top"),sQuery(id+"F0.wireOp",EDGE,"E2.left"),sQuery(id+"F0.wireOp",EDGE,"E2.right")])]}),"instanceName":"1"}),"instanceName":"1"}),"instanceName":"1"}),"instanceName":"1"}),"instanceName":"1"});
            var Q512;
            Q512=makeQuery(id+"F11.opPattern","COPY",BODY,{"derivedFrom":makeQuery(id+"F10.opPattern","COPY",BODY,{"derivedFrom":makeQuery(id+"F9.opPattern","COPY",BODY,{"derivedFrom":makeQuery(id+"F4.opPattern","COPY",BODY,{"derivedFrom":makeQuery(id+"F3.opPattern","COPY",BODY,{"derivedFrom":makeQuery(id+"F2.opPattern","COPY",BODY,{"derivedFrom":makeQuery(id+"F1.opExtrude","SWEPT_BODY",BODY,{"disambiguationData":[OSD([sQuery(id+"F0.wireOp",EDGE,"E0.bottom"),sQuery(id+"F0.wireOp",EDGE,"E0.top"),sQuery(id+"F0.wireOp",EDGE,"E0.left"),sQuery(id+"F0.wireOp",EDGE,"E0.right")])]}),"instanceName":"1"}),"instanceName":"1"}),"instanceName":"1"}),"instanceName":"1"}),"instanceName":"1"}),"instanceName":"1"});
            var Q513;
            Q513=makeQuery(id+"F11.opPattern","COPY",BODY,{"derivedFrom":makeQuery(id+"F10.opPattern","COPY",BODY,{"derivedFrom":makeQuery(id+"F9.opPattern","COPY",BODY,{"derivedFrom":makeQuery(id+"F4.opPattern","COPY",BODY,{"derivedFrom":makeQuery(id+"F3.opPattern","COPY",BODY,{"derivedFrom":makeQuery(id+"F2.opPattern","COPY",BODY,{"derivedFrom":makeQuery(id+"F1.opExtrude","SWEPT_BODY",BODY,{"disambiguationData":[OSD([sQuery(id+"F0.wireOp",EDGE,"E1.bottom"),sQuery(id+"F0.wireOp",EDGE,"E1.top"),sQuery(id+"F0.wireOp",EDGE,"E1.left"),sQuery(id+"F0.wireOp",EDGE,"E1.right")])]}),"instanceName":"1"}),"instanceName":"1"}),"instanceName":"1"}),"instanceName":"1"}),"instanceName":"1"}),"instanceName":"1"});
            var Q514;
            Q514=makeQuery(id+"F11.opPattern","COPY",BODY,{"derivedFrom":makeQuery(id+"F10.opPattern","COPY",BODY,{"derivedFrom":makeQuery(id+"F9.opPattern","COPY",BODY,{"derivedFrom":makeQuery(id+"F4.opPattern","COPY",BODY,{"derivedFrom":makeQuery(id+"F3.opPattern","COPY",BODY,{"derivedFrom":makeQuery(id+"F2.opPattern","COPY",BODY,{"derivedFrom":makeQuery(id+"F1.opExtrude","SWEPT_BODY",BODY,{"disambiguationData":[OSD([sQuery(id+"F0.wireOp",EDGE,"E2.bottom"),sQuery(id+"F0.wireOp",EDGE,"E2.top"),sQuery(id+"F0.wireOp",EDGE,"E2.left"),sQuery(id+"F0.wireOp",EDGE,"E2.right")])]}),"instanceName":"1"}),"instanceName":"1"}),"instanceName":"1"}),"instanceName":"1"}),"instanceName":"1"}),"instanceName":"1"});
            var Q515;
            Q515=makeQuery(id+"F11.opPattern","COPY",BODY,{"derivedFrom":makeQuery(id+"F10.opPattern","COPY",BODY,{"derivedFrom":makeQuery(id+"F9.opPattern","COPY",BODY,{"derivedFrom":makeQuery(id+"F5.opPattern","COPY",BODY,{"derivedFrom":makeQuery(id+"F4.opPattern","COPY",BODY,{"derivedFrom":makeQuery(id+"F3.opPattern","COPY",BODY,{"derivedFrom":makeQuery(id+"F2.opPattern","COPY",BODY,{"derivedFrom":makeQuery(id+"F1.opExtrude","SWEPT_BODY",BODY,{"disambiguationData":[OSD([sQuery(id+"F0.wireOp",EDGE,"E0.bottom"),sQuery(id+"F0.wireOp",EDGE,"E0.top"),sQuery(id+"F0.wireOp",EDGE,"E0.left"),sQuery(id+"F0.wireOp",EDGE,"E0.right")])]}),"instanceName":"1"}),"instanceName":"1"}),"instanceName":"1"}),"instanceName":"1"}),"instanceName":"1"}),"instanceName":"1"}),"instanceName":"1"});
            var Q516;
            Q516=makeQuery(id+"F11.opPattern","COPY",BODY,{"derivedFrom":makeQuery(id+"F10.opPattern","COPY",BODY,{"derivedFrom":makeQuery(id+"F9.opPattern","COPY",BODY,{"derivedFrom":makeQuery(id+"F5.opPattern","COPY",BODY,{"derivedFrom":makeQuery(id+"F4.opPattern","COPY",BODY,{"derivedFrom":makeQuery(id+"F3.opPattern","COPY",BODY,{"derivedFrom":makeQuery(id+"F2.opPattern","COPY",BODY,{"derivedFrom":makeQuery(id+"F1.opExtrude","SWEPT_BODY",BODY,{"disambiguationData":[OSD([sQuery(id+"F0.wireOp",EDGE,"E1.bottom"),sQuery(id+"F0.wireOp",EDGE,"E1.top"),sQuery(id+"F0.wireOp",EDGE,"E1.left"),sQuery(id+"F0.wireOp",EDGE,"E1.right")])]}),"instanceName":"1"}),"instanceName":"1"}),"instanceName":"1"}),"instanceName":"1"}),"instanceName":"1"}),"instanceName":"1"}),"instanceName":"1"});
            var Q517;
            Q517=makeQuery(id+"F11.opPattern","COPY",BODY,{"derivedFrom":makeQuery(id+"F10.opPattern","COPY",BODY,{"derivedFrom":makeQuery(id+"F9.opPattern","COPY",BODY,{"derivedFrom":makeQuery(id+"F5.opPattern","COPY",BODY,{"derivedFrom":makeQuery(id+"F4.opPattern","COPY",BODY,{"derivedFrom":makeQuery(id+"F3.opPattern","COPY",BODY,{"derivedFrom":makeQuery(id+"F2.opPattern","COPY",BODY,{"derivedFrom":makeQuery(id+"F1.opExtrude","SWEPT_BODY",BODY,{"disambiguationData":[OSD([sQuery(id+"F0.wireOp",EDGE,"E2.bottom"),sQuery(id+"F0.wireOp",EDGE,"E2.top"),sQuery(id+"F0.wireOp",EDGE,"E2.left"),sQuery(id+"F0.wireOp",EDGE,"E2.right")])]}),"instanceName":"1"}),"instanceName":"1"}),"instanceName":"1"}),"instanceName":"1"}),"instanceName":"1"}),"instanceName":"1"}),"instanceName":"1"});
            var Q518;
            Q518=makeQuery(id+"F11.opPattern","COPY",BODY,{"derivedFrom":makeQuery(id+"F10.opPattern","COPY",BODY,{"derivedFrom":makeQuery(id+"F9.opPattern","COPY",BODY,{"derivedFrom":makeQuery(id+"F6.opPattern","COPY",BODY,{"derivedFrom":makeQuery(id+"F5.opPattern","COPY",BODY,{"derivedFrom":makeQuery(id+"F4.opPattern","COPY",BODY,{"derivedFrom":makeQuery(id+"F3.opPattern","COPY",BODY,{"derivedFrom":makeQuery(id+"F2.opPattern","COPY",BODY,{"derivedFrom":makeQuery(id+"F1.opExtrude","SWEPT_BODY",BODY,{"disambiguationData":[OSD([sQuery(id+"F0.wireOp",EDGE,"E0.bottom"),sQuery(id+"F0.wireOp",EDGE,"E0.top"),sQuery(id+"F0.wireOp",EDGE,"E0.left"),sQuery(id+"F0.wireOp",EDGE,"E0.right")])]}),"instanceName":"1"}),"instanceName":"1"}),"instanceName":"1"}),"instanceName":"1"}),"instanceName":"1"}),"instanceName":"1"}),"instanceName":"1"}),"instanceName":"1"});
            var Q519;
            Q519=makeQuery(id+"F11.opPattern","COPY",BODY,{"derivedFrom":makeQuery(id+"F10.opPattern","COPY",BODY,{"derivedFrom":makeQuery(id+"F9.opPattern","COPY",BODY,{"derivedFrom":makeQuery(id+"F6.opPattern","COPY",BODY,{"derivedFrom":makeQuery(id+"F5.opPattern","COPY",BODY,{"derivedFrom":makeQuery(id+"F4.opPattern","COPY",BODY,{"derivedFrom":makeQuery(id+"F3.opPattern","COPY",BODY,{"derivedFrom":makeQuery(id+"F2.opPattern","COPY",BODY,{"derivedFrom":makeQuery(id+"F1.opExtrude","SWEPT_BODY",BODY,{"disambiguationData":[OSD([sQuery(id+"F0.wireOp",EDGE,"E1.bottom"),sQuery(id+"F0.wireOp",EDGE,"E1.top"),sQuery(id+"F0.wireOp",EDGE,"E1.left"),sQuery(id+"F0.wireOp",EDGE,"E1.right")])]}),"instanceName":"1"}),"instanceName":"1"}),"instanceName":"1"}),"instanceName":"1"}),"instanceName":"1"}),"instanceName":"1"}),"instanceName":"1"}),"instanceName":"1"});
            var Q520;
            Q520=makeQuery(id+"F11.opPattern","COPY",BODY,{"derivedFrom":makeQuery(id+"F10.opPattern","COPY",BODY,{"derivedFrom":makeQuery(id+"F9.opPattern","COPY",BODY,{"derivedFrom":makeQuery(id+"F6.opPattern","COPY",BODY,{"derivedFrom":makeQuery(id+"F5.opPattern","COPY",BODY,{"derivedFrom":makeQuery(id+"F4.opPattern","COPY",BODY,{"derivedFrom":makeQuery(id+"F3.opPattern","COPY",BODY,{"derivedFrom":makeQuery(id+"F2.opPattern","COPY",BODY,{"derivedFrom":makeQuery(id+"F1.opExtrude","SWEPT_BODY",BODY,{"disambiguationData":[OSD([sQuery(id+"F0.wireOp",EDGE,"E2.bottom"),sQuery(id+"F0.wireOp",EDGE,"E2.top"),sQuery(id+"F0.wireOp",EDGE,"E2.left"),sQuery(id+"F0.wireOp",EDGE,"E2.right")])]}),"instanceName":"1"}),"instanceName":"1"}),"instanceName":"1"}),"instanceName":"1"}),"instanceName":"1"}),"instanceName":"1"}),"instanceName":"1"}),"instanceName":"1"});
            var Q521;
            Q521=makeQuery(id+"F11.opPattern","COPY",BODY,{"derivedFrom":makeQuery(id+"F10.opPattern","COPY",BODY,{"derivedFrom":makeQuery(id+"F9.opPattern","COPY",BODY,{"derivedFrom":makeQuery(id+"F7.opPattern","COPY",BODY,{"derivedFrom":makeQuery(id+"F1.opExtrude","SWEPT_BODY",BODY,{"disambiguationData":[OSD([sQuery(id+"F0.wireOp",EDGE,"E0.bottom"),sQuery(id+"F0.wireOp",EDGE,"E0.top"),sQuery(id+"F0.wireOp",EDGE,"E0.left"),sQuery(id+"F0.wireOp",EDGE,"E0.right")])]}),"instanceName":"1"}),"instanceName":"1"}),"instanceName":"1"}),"instanceName":"1"});
            var Q522;
            Q522=makeQuery(id+"F11.opPattern","COPY",BODY,{"derivedFrom":makeQuery(id+"F10.opPattern","COPY",BODY,{"derivedFrom":makeQuery(id+"F9.opPattern","COPY",BODY,{"derivedFrom":makeQuery(id+"F7.opPattern","COPY",BODY,{"derivedFrom":makeQuery(id+"F1.opExtrude","SWEPT_BODY",BODY,{"disambiguationData":[OSD([sQuery(id+"F0.wireOp",EDGE,"E1.bottom"),sQuery(id+"F0.wireOp",EDGE,"E1.top"),sQuery(id+"F0.wireOp",EDGE,"E1.left"),sQuery(id+"F0.wireOp",EDGE,"E1.right")])]}),"instanceName":"1"}),"instanceName":"1"}),"instanceName":"1"}),"instanceName":"1"});
            var Q523;
            Q523=makeQuery(id+"F11.opPattern","COPY",BODY,{"derivedFrom":makeQuery(id+"F10.opPattern","COPY",BODY,{"derivedFrom":makeQuery(id+"F9.opPattern","COPY",BODY,{"derivedFrom":makeQuery(id+"F7.opPattern","COPY",BODY,{"derivedFrom":makeQuery(id+"F1.opExtrude","SWEPT_BODY",BODY,{"disambiguationData":[OSD([sQuery(id+"F0.wireOp",EDGE,"E2.bottom"),sQuery(id+"F0.wireOp",EDGE,"E2.top"),sQuery(id+"F0.wireOp",EDGE,"E2.left"),sQuery(id+"F0.wireOp",EDGE,"E2.right")])]}),"instanceName":"1"}),"instanceName":"1"}),"instanceName":"1"}),"instanceName":"1"});
            var Q524;
            Q524=makeQuery(id+"F11.opPattern","COPY",BODY,{"derivedFrom":makeQuery(id+"F10.opPattern","COPY",BODY,{"derivedFrom":makeQuery(id+"F9.opPattern","COPY",BODY,{"derivedFrom":makeQuery(id+"F7.opPattern","COPY",BODY,{"derivedFrom":makeQuery(id+"F2.opPattern","COPY",BODY,{"derivedFrom":makeQuery(id+"F1.opExtrude","SWEPT_BODY",BODY,{"disambiguationData":[OSD([sQuery(id+"F0.wireOp",EDGE,"E0.bottom"),sQuery(id+"F0.wireOp",EDGE,"E0.top"),sQuery(id+"F0.wireOp",EDGE,"E0.left"),sQuery(id+"F0.wireOp",EDGE,"E0.right")])]}),"instanceName":"1"}),"instanceName":"1"}),"instanceName":"1"}),"instanceName":"1"}),"instanceName":"1"});
            var Q525;
            Q525=makeQuery(id+"F11.opPattern","COPY",BODY,{"derivedFrom":makeQuery(id+"F10.opPattern","COPY",BODY,{"derivedFrom":makeQuery(id+"F9.opPattern","COPY",BODY,{"derivedFrom":makeQuery(id+"F7.opPattern","COPY",BODY,{"derivedFrom":makeQuery(id+"F2.opPattern","COPY",BODY,{"derivedFrom":makeQuery(id+"F1.opExtrude","SWEPT_BODY",BODY,{"disambiguationData":[OSD([sQuery(id+"F0.wireOp",EDGE,"E1.bottom"),sQuery(id+"F0.wireOp",EDGE,"E1.top"),sQuery(id+"F0.wireOp",EDGE,"E1.left"),sQuery(id+"F0.wireOp",EDGE,"E1.right")])]}),"instanceName":"1"}),"instanceName":"1"}),"instanceName":"1"}),"instanceName":"1"}),"instanceName":"1"});
            var Q526;
            Q526=makeQuery(id+"F11.opPattern","COPY",BODY,{"derivedFrom":makeQuery(id+"F10.opPattern","COPY",BODY,{"derivedFrom":makeQuery(id+"F9.opPattern","COPY",BODY,{"derivedFrom":makeQuery(id+"F7.opPattern","COPY",BODY,{"derivedFrom":makeQuery(id+"F2.opPattern","COPY",BODY,{"derivedFrom":makeQuery(id+"F1.opExtrude","SWEPT_BODY",BODY,{"disambiguationData":[OSD([sQuery(id+"F0.wireOp",EDGE,"E2.bottom"),sQuery(id+"F0.wireOp",EDGE,"E2.top"),sQuery(id+"F0.wireOp",EDGE,"E2.left"),sQuery(id+"F0.wireOp",EDGE,"E2.right")])]}),"instanceName":"1"}),"instanceName":"1"}),"instanceName":"1"}),"instanceName":"1"}),"instanceName":"1"});
            var Q527;
            Q527=makeQuery(id+"F11.opPattern","COPY",BODY,{"derivedFrom":makeQuery(id+"F10.opPattern","COPY",BODY,{"derivedFrom":makeQuery(id+"F9.opPattern","COPY",BODY,{"derivedFrom":makeQuery(id+"F7.opPattern","COPY",BODY,{"derivedFrom":makeQuery(id+"F3.opPattern","COPY",BODY,{"derivedFrom":makeQuery(id+"F2.opPattern","COPY",BODY,{"derivedFrom":makeQuery(id+"F1.opExtrude","SWEPT_BODY",BODY,{"disambiguationData":[OSD([sQuery(id+"F0.wireOp",EDGE,"E0.bottom"),sQuery(id+"F0.wireOp",EDGE,"E0.top"),sQuery(id+"F0.wireOp",EDGE,"E0.left"),sQuery(id+"F0.wireOp",EDGE,"E0.right")])]}),"instanceName":"1"}),"instanceName":"1"}),"instanceName":"1"}),"instanceName":"1"}),"instanceName":"1"}),"instanceName":"1"});
            var Q528;
            Q528=makeQuery(id+"F11.opPattern","COPY",BODY,{"derivedFrom":makeQuery(id+"F10.opPattern","COPY",BODY,{"derivedFrom":makeQuery(id+"F9.opPattern","COPY",BODY,{"derivedFrom":makeQuery(id+"F7.opPattern","COPY",BODY,{"derivedFrom":makeQuery(id+"F3.opPattern","COPY",BODY,{"derivedFrom":makeQuery(id+"F2.opPattern","COPY",BODY,{"derivedFrom":makeQuery(id+"F1.opExtrude","SWEPT_BODY",BODY,{"disambiguationData":[OSD([sQuery(id+"F0.wireOp",EDGE,"E1.bottom"),sQuery(id+"F0.wireOp",EDGE,"E1.top"),sQuery(id+"F0.wireOp",EDGE,"E1.left"),sQuery(id+"F0.wireOp",EDGE,"E1.right")])]}),"instanceName":"1"}),"instanceName":"1"}),"instanceName":"1"}),"instanceName":"1"}),"instanceName":"1"}),"instanceName":"1"});
            var Q529;
            Q529=makeQuery(id+"F11.opPattern","COPY",BODY,{"derivedFrom":makeQuery(id+"F10.opPattern","COPY",BODY,{"derivedFrom":makeQuery(id+"F9.opPattern","COPY",BODY,{"derivedFrom":makeQuery(id+"F7.opPattern","COPY",BODY,{"derivedFrom":makeQuery(id+"F3.opPattern","COPY",BODY,{"derivedFrom":makeQuery(id+"F2.opPattern","COPY",BODY,{"derivedFrom":makeQuery(id+"F1.opExtrude","SWEPT_BODY",BODY,{"disambiguationData":[OSD([sQuery(id+"F0.wireOp",EDGE,"E2.bottom"),sQuery(id+"F0.wireOp",EDGE,"E2.top"),sQuery(id+"F0.wireOp",EDGE,"E2.left"),sQuery(id+"F0.wireOp",EDGE,"E2.right")])]}),"instanceName":"1"}),"instanceName":"1"}),"instanceName":"1"}),"instanceName":"1"}),"instanceName":"1"}),"instanceName":"1"});
            var Q530;
            Q530=makeQuery(id+"F11.opPattern","COPY",BODY,{"derivedFrom":makeQuery(id+"F10.opPattern","COPY",BODY,{"derivedFrom":makeQuery(id+"F9.opPattern","COPY",BODY,{"derivedFrom":makeQuery(id+"F7.opPattern","COPY",BODY,{"derivedFrom":makeQuery(id+"F4.opPattern","COPY",BODY,{"derivedFrom":makeQuery(id+"F3.opPattern","COPY",BODY,{"derivedFrom":makeQuery(id+"F2.opPattern","COPY",BODY,{"derivedFrom":makeQuery(id+"F1.opExtrude","SWEPT_BODY",BODY,{"disambiguationData":[OSD([sQuery(id+"F0.wireOp",EDGE,"E0.bottom"),sQuery(id+"F0.wireOp",EDGE,"E0.top"),sQuery(id+"F0.wireOp",EDGE,"E0.left"),sQuery(id+"F0.wireOp",EDGE,"E0.right")])]}),"instanceName":"1"}),"instanceName":"1"}),"instanceName":"1"}),"instanceName":"1"}),"instanceName":"1"}),"instanceName":"1"}),"instanceName":"1"});
            var Q531;
            Q531=makeQuery(id+"F11.opPattern","COPY",BODY,{"derivedFrom":makeQuery(id+"F10.opPattern","COPY",BODY,{"derivedFrom":makeQuery(id+"F9.opPattern","COPY",BODY,{"derivedFrom":makeQuery(id+"F7.opPattern","COPY",BODY,{"derivedFrom":makeQuery(id+"F4.opPattern","COPY",BODY,{"derivedFrom":makeQuery(id+"F3.opPattern","COPY",BODY,{"derivedFrom":makeQuery(id+"F2.opPattern","COPY",BODY,{"derivedFrom":makeQuery(id+"F1.opExtrude","SWEPT_BODY",BODY,{"disambiguationData":[OSD([sQuery(id+"F0.wireOp",EDGE,"E1.bottom"),sQuery(id+"F0.wireOp",EDGE,"E1.top"),sQuery(id+"F0.wireOp",EDGE,"E1.left"),sQuery(id+"F0.wireOp",EDGE,"E1.right")])]}),"instanceName":"1"}),"instanceName":"1"}),"instanceName":"1"}),"instanceName":"1"}),"instanceName":"1"}),"instanceName":"1"}),"instanceName":"1"});
            var Q532;
            Q532=makeQuery(id+"F11.opPattern","COPY",BODY,{"derivedFrom":makeQuery(id+"F10.opPattern","COPY",BODY,{"derivedFrom":makeQuery(id+"F9.opPattern","COPY",BODY,{"derivedFrom":makeQuery(id+"F7.opPattern","COPY",BODY,{"derivedFrom":makeQuery(id+"F4.opPattern","COPY",BODY,{"derivedFrom":makeQuery(id+"F3.opPattern","COPY",BODY,{"derivedFrom":makeQuery(id+"F2.opPattern","COPY",BODY,{"derivedFrom":makeQuery(id+"F1.opExtrude","SWEPT_BODY",BODY,{"disambiguationData":[OSD([sQuery(id+"F0.wireOp",EDGE,"E2.bottom"),sQuery(id+"F0.wireOp",EDGE,"E2.top"),sQuery(id+"F0.wireOp",EDGE,"E2.left"),sQuery(id+"F0.wireOp",EDGE,"E2.right")])]}),"instanceName":"1"}),"instanceName":"1"}),"instanceName":"1"}),"instanceName":"1"}),"instanceName":"1"}),"instanceName":"1"}),"instanceName":"1"});
            var Q533;
            Q533=makeQuery(id+"F11.opPattern","COPY",BODY,{"derivedFrom":makeQuery(id+"F10.opPattern","COPY",BODY,{"derivedFrom":makeQuery(id+"F9.opPattern","COPY",BODY,{"derivedFrom":makeQuery(id+"F7.opPattern","COPY",BODY,{"derivedFrom":makeQuery(id+"F5.opPattern","COPY",BODY,{"derivedFrom":makeQuery(id+"F4.opPattern","COPY",BODY,{"derivedFrom":makeQuery(id+"F3.opPattern","COPY",BODY,{"derivedFrom":makeQuery(id+"F2.opPattern","COPY",BODY,{"derivedFrom":makeQuery(id+"F1.opExtrude","SWEPT_BODY",BODY,{"disambiguationData":[OSD([sQuery(id+"F0.wireOp",EDGE,"E0.bottom"),sQuery(id+"F0.wireOp",EDGE,"E0.top"),sQuery(id+"F0.wireOp",EDGE,"E0.left"),sQuery(id+"F0.wireOp",EDGE,"E0.right")])]}),"instanceName":"1"}),"instanceName":"1"}),"instanceName":"1"}),"instanceName":"1"}),"instanceName":"1"}),"instanceName":"1"}),"instanceName":"1"}),"instanceName":"1"});
            var Q534;
            Q534=makeQuery(id+"F11.opPattern","COPY",BODY,{"derivedFrom":makeQuery(id+"F10.opPattern","COPY",BODY,{"derivedFrom":makeQuery(id+"F9.opPattern","COPY",BODY,{"derivedFrom":makeQuery(id+"F7.opPattern","COPY",BODY,{"derivedFrom":makeQuery(id+"F5.opPattern","COPY",BODY,{"derivedFrom":makeQuery(id+"F4.opPattern","COPY",BODY,{"derivedFrom":makeQuery(id+"F3.opPattern","COPY",BODY,{"derivedFrom":makeQuery(id+"F2.opPattern","COPY",BODY,{"derivedFrom":makeQuery(id+"F1.opExtrude","SWEPT_BODY",BODY,{"disambiguationData":[OSD([sQuery(id+"F0.wireOp",EDGE,"E1.bottom"),sQuery(id+"F0.wireOp",EDGE,"E1.top"),sQuery(id+"F0.wireOp",EDGE,"E1.left"),sQuery(id+"F0.wireOp",EDGE,"E1.right")])]}),"instanceName":"1"}),"instanceName":"1"}),"instanceName":"1"}),"instanceName":"1"}),"instanceName":"1"}),"instanceName":"1"}),"instanceName":"1"}),"instanceName":"1"});
            var Q535;
            Q535=makeQuery(id+"F11.opPattern","COPY",BODY,{"derivedFrom":makeQuery(id+"F10.opPattern","COPY",BODY,{"derivedFrom":makeQuery(id+"F9.opPattern","COPY",BODY,{"derivedFrom":makeQuery(id+"F7.opPattern","COPY",BODY,{"derivedFrom":makeQuery(id+"F5.opPattern","COPY",BODY,{"derivedFrom":makeQuery(id+"F4.opPattern","COPY",BODY,{"derivedFrom":makeQuery(id+"F3.opPattern","COPY",BODY,{"derivedFrom":makeQuery(id+"F2.opPattern","COPY",BODY,{"derivedFrom":makeQuery(id+"F1.opExtrude","SWEPT_BODY",BODY,{"disambiguationData":[OSD([sQuery(id+"F0.wireOp",EDGE,"E2.bottom"),sQuery(id+"F0.wireOp",EDGE,"E2.top"),sQuery(id+"F0.wireOp",EDGE,"E2.left"),sQuery(id+"F0.wireOp",EDGE,"E2.right")])]}),"instanceName":"1"}),"instanceName":"1"}),"instanceName":"1"}),"instanceName":"1"}),"instanceName":"1"}),"instanceName":"1"}),"instanceName":"1"}),"instanceName":"1"});
            var Q536;
            Q536=makeQuery(id+"F11.opPattern","COPY",BODY,{"derivedFrom":makeQuery(id+"F10.opPattern","COPY",BODY,{"derivedFrom":makeQuery(id+"F9.opPattern","COPY",BODY,{"derivedFrom":makeQuery(id+"F7.opPattern","COPY",BODY,{"derivedFrom":makeQuery(id+"F6.opPattern","COPY",BODY,{"derivedFrom":makeQuery(id+"F5.opPattern","COPY",BODY,{"derivedFrom":makeQuery(id+"F4.opPattern","COPY",BODY,{"derivedFrom":makeQuery(id+"F3.opPattern","COPY",BODY,{"derivedFrom":makeQuery(id+"F2.opPattern","COPY",BODY,{"derivedFrom":makeQuery(id+"F1.opExtrude","SWEPT_BODY",BODY,{"disambiguationData":[OSD([sQuery(id+"F0.wireOp",EDGE,"E0.bottom"),sQuery(id+"F0.wireOp",EDGE,"E0.top"),sQuery(id+"F0.wireOp",EDGE,"E0.left"),sQuery(id+"F0.wireOp",EDGE,"E0.right")])]}),"instanceName":"1"}),"instanceName":"1"}),"instanceName":"1"}),"instanceName":"1"}),"instanceName":"1"}),"instanceName":"1"}),"instanceName":"1"}),"instanceName":"1"}),"instanceName":"1"});
            var Q537;
            Q537=makeQuery(id+"F11.opPattern","COPY",BODY,{"derivedFrom":makeQuery(id+"F10.opPattern","COPY",BODY,{"derivedFrom":makeQuery(id+"F9.opPattern","COPY",BODY,{"derivedFrom":makeQuery(id+"F7.opPattern","COPY",BODY,{"derivedFrom":makeQuery(id+"F6.opPattern","COPY",BODY,{"derivedFrom":makeQuery(id+"F5.opPattern","COPY",BODY,{"derivedFrom":makeQuery(id+"F4.opPattern","COPY",BODY,{"derivedFrom":makeQuery(id+"F3.opPattern","COPY",BODY,{"derivedFrom":makeQuery(id+"F2.opPattern","COPY",BODY,{"derivedFrom":makeQuery(id+"F1.opExtrude","SWEPT_BODY",BODY,{"disambiguationData":[OSD([sQuery(id+"F0.wireOp",EDGE,"E1.bottom"),sQuery(id+"F0.wireOp",EDGE,"E1.top"),sQuery(id+"F0.wireOp",EDGE,"E1.left"),sQuery(id+"F0.wireOp",EDGE,"E1.right")])]}),"instanceName":"1"}),"instanceName":"1"}),"instanceName":"1"}),"instanceName":"1"}),"instanceName":"1"}),"instanceName":"1"}),"instanceName":"1"}),"instanceName":"1"}),"instanceName":"1"});
            var Q538;
            Q538=makeQuery(id+"F11.opPattern","COPY",BODY,{"derivedFrom":makeQuery(id+"F10.opPattern","COPY",BODY,{"derivedFrom":makeQuery(id+"F9.opPattern","COPY",BODY,{"derivedFrom":makeQuery(id+"F7.opPattern","COPY",BODY,{"derivedFrom":makeQuery(id+"F6.opPattern","COPY",BODY,{"derivedFrom":makeQuery(id+"F5.opPattern","COPY",BODY,{"derivedFrom":makeQuery(id+"F4.opPattern","COPY",BODY,{"derivedFrom":makeQuery(id+"F3.opPattern","COPY",BODY,{"derivedFrom":makeQuery(id+"F2.opPattern","COPY",BODY,{"derivedFrom":makeQuery(id+"F1.opExtrude","SWEPT_BODY",BODY,{"disambiguationData":[OSD([sQuery(id+"F0.wireOp",EDGE,"E2.bottom"),sQuery(id+"F0.wireOp",EDGE,"E2.top"),sQuery(id+"F0.wireOp",EDGE,"E2.left"),sQuery(id+"F0.wireOp",EDGE,"E2.right")])]}),"instanceName":"1"}),"instanceName":"1"}),"instanceName":"1"}),"instanceName":"1"}),"instanceName":"1"}),"instanceName":"1"}),"instanceName":"1"}),"instanceName":"1"}),"instanceName":"1"});
            var Q539;
            Q539=makeQuery(id+"F11.opPattern","COPY",BODY,{"derivedFrom":makeQuery(id+"F10.opPattern","COPY",BODY,{"derivedFrom":makeQuery(id+"F9.opPattern","COPY",BODY,{"derivedFrom":makeQuery(id+"F8.opPattern","COPY",BODY,{"derivedFrom":makeQuery(id+"F1.opExtrude","SWEPT_BODY",BODY,{"disambiguationData":[OSD([sQuery(id+"F0.wireOp",EDGE,"E0.bottom"),sQuery(id+"F0.wireOp",EDGE,"E0.top"),sQuery(id+"F0.wireOp",EDGE,"E0.left"),sQuery(id+"F0.wireOp",EDGE,"E0.right")])]}),"instanceName":"1"}),"instanceName":"1"}),"instanceName":"1"}),"instanceName":"1"});
            var Q540;
            Q540=makeQuery(id+"F11.opPattern","COPY",BODY,{"derivedFrom":makeQuery(id+"F10.opPattern","COPY",BODY,{"derivedFrom":makeQuery(id+"F9.opPattern","COPY",BODY,{"derivedFrom":makeQuery(id+"F8.opPattern","COPY",BODY,{"derivedFrom":makeQuery(id+"F1.opExtrude","SWEPT_BODY",BODY,{"disambiguationData":[OSD([sQuery(id+"F0.wireOp",EDGE,"E1.bottom"),sQuery(id+"F0.wireOp",EDGE,"E1.top"),sQuery(id+"F0.wireOp",EDGE,"E1.left"),sQuery(id+"F0.wireOp",EDGE,"E1.right")])]}),"instanceName":"1"}),"instanceName":"1"}),"instanceName":"1"}),"instanceName":"1"});
            var Q541;
            Q541=makeQuery(id+"F11.opPattern","COPY",BODY,{"derivedFrom":makeQuery(id+"F10.opPattern","COPY",BODY,{"derivedFrom":makeQuery(id+"F9.opPattern","COPY",BODY,{"derivedFrom":makeQuery(id+"F8.opPattern","COPY",BODY,{"derivedFrom":makeQuery(id+"F1.opExtrude","SWEPT_BODY",BODY,{"disambiguationData":[OSD([sQuery(id+"F0.wireOp",EDGE,"E2.bottom"),sQuery(id+"F0.wireOp",EDGE,"E2.top"),sQuery(id+"F0.wireOp",EDGE,"E2.left"),sQuery(id+"F0.wireOp",EDGE,"E2.right")])]}),"instanceName":"1"}),"instanceName":"1"}),"instanceName":"1"}),"instanceName":"1"});
            var Q542;
            Q542=makeQuery(id+"F11.opPattern","COPY",BODY,{"derivedFrom":makeQuery(id+"F10.opPattern","COPY",BODY,{"derivedFrom":makeQuery(id+"F9.opPattern","COPY",BODY,{"derivedFrom":makeQuery(id+"F8.opPattern","COPY",BODY,{"derivedFrom":makeQuery(id+"F2.opPattern","COPY",BODY,{"derivedFrom":makeQuery(id+"F1.opExtrude","SWEPT_BODY",BODY,{"disambiguationData":[OSD([sQuery(id+"F0.wireOp",EDGE,"E0.bottom"),sQuery(id+"F0.wireOp",EDGE,"E0.top"),sQuery(id+"F0.wireOp",EDGE,"E0.left"),sQuery(id+"F0.wireOp",EDGE,"E0.right")])]}),"instanceName":"1"}),"instanceName":"1"}),"instanceName":"1"}),"instanceName":"1"}),"instanceName":"1"});
            var Q543;
            Q543=makeQuery(id+"F11.opPattern","COPY",BODY,{"derivedFrom":makeQuery(id+"F10.opPattern","COPY",BODY,{"derivedFrom":makeQuery(id+"F9.opPattern","COPY",BODY,{"derivedFrom":makeQuery(id+"F8.opPattern","COPY",BODY,{"derivedFrom":makeQuery(id+"F2.opPattern","COPY",BODY,{"derivedFrom":makeQuery(id+"F1.opExtrude","SWEPT_BODY",BODY,{"disambiguationData":[OSD([sQuery(id+"F0.wireOp",EDGE,"E1.bottom"),sQuery(id+"F0.wireOp",EDGE,"E1.top"),sQuery(id+"F0.wireOp",EDGE,"E1.left"),sQuery(id+"F0.wireOp",EDGE,"E1.right")])]}),"instanceName":"1"}),"instanceName":"1"}),"instanceName":"1"}),"instanceName":"1"}),"instanceName":"1"});
            var Q544;
            Q544=makeQuery(id+"F11.opPattern","COPY",BODY,{"derivedFrom":makeQuery(id+"F10.opPattern","COPY",BODY,{"derivedFrom":makeQuery(id+"F9.opPattern","COPY",BODY,{"derivedFrom":makeQuery(id+"F8.opPattern","COPY",BODY,{"derivedFrom":makeQuery(id+"F2.opPattern","COPY",BODY,{"derivedFrom":makeQuery(id+"F1.opExtrude","SWEPT_BODY",BODY,{"disambiguationData":[OSD([sQuery(id+"F0.wireOp",EDGE,"E2.bottom"),sQuery(id+"F0.wireOp",EDGE,"E2.top"),sQuery(id+"F0.wireOp",EDGE,"E2.left"),sQuery(id+"F0.wireOp",EDGE,"E2.right")])]}),"instanceName":"1"}),"instanceName":"1"}),"instanceName":"1"}),"instanceName":"1"}),"instanceName":"1"});
            var Q545;
            Q545=makeQuery(id+"F11.opPattern","COPY",BODY,{"derivedFrom":makeQuery(id+"F10.opPattern","COPY",BODY,{"derivedFrom":makeQuery(id+"F9.opPattern","COPY",BODY,{"derivedFrom":makeQuery(id+"F8.opPattern","COPY",BODY,{"derivedFrom":makeQuery(id+"F3.opPattern","COPY",BODY,{"derivedFrom":makeQuery(id+"F2.opPattern","COPY",BODY,{"derivedFrom":makeQuery(id+"F1.opExtrude","SWEPT_BODY",BODY,{"disambiguationData":[OSD([sQuery(id+"F0.wireOp",EDGE,"E0.bottom"),sQuery(id+"F0.wireOp",EDGE,"E0.top"),sQuery(id+"F0.wireOp",EDGE,"E0.left"),sQuery(id+"F0.wireOp",EDGE,"E0.right")])]}),"instanceName":"1"}),"instanceName":"1"}),"instanceName":"1"}),"instanceName":"1"}),"instanceName":"1"}),"instanceName":"1"});
            var Q546;
            Q546=makeQuery(id+"F11.opPattern","COPY",BODY,{"derivedFrom":makeQuery(id+"F10.opPattern","COPY",BODY,{"derivedFrom":makeQuery(id+"F9.opPattern","COPY",BODY,{"derivedFrom":makeQuery(id+"F8.opPattern","COPY",BODY,{"derivedFrom":makeQuery(id+"F3.opPattern","COPY",BODY,{"derivedFrom":makeQuery(id+"F2.opPattern","COPY",BODY,{"derivedFrom":makeQuery(id+"F1.opExtrude","SWEPT_BODY",BODY,{"disambiguationData":[OSD([sQuery(id+"F0.wireOp",EDGE,"E1.bottom"),sQuery(id+"F0.wireOp",EDGE,"E1.top"),sQuery(id+"F0.wireOp",EDGE,"E1.left"),sQuery(id+"F0.wireOp",EDGE,"E1.right")])]}),"instanceName":"1"}),"instanceName":"1"}),"instanceName":"1"}),"instanceName":"1"}),"instanceName":"1"}),"instanceName":"1"});
            var Q547;
            Q547=makeQuery(id+"F11.opPattern","COPY",BODY,{"derivedFrom":makeQuery(id+"F10.opPattern","COPY",BODY,{"derivedFrom":makeQuery(id+"F9.opPattern","COPY",BODY,{"derivedFrom":makeQuery(id+"F8.opPattern","COPY",BODY,{"derivedFrom":makeQuery(id+"F3.opPattern","COPY",BODY,{"derivedFrom":makeQuery(id+"F2.opPattern","COPY",BODY,{"derivedFrom":makeQuery(id+"F1.opExtrude","SWEPT_BODY",BODY,{"disambiguationData":[OSD([sQuery(id+"F0.wireOp",EDGE,"E2.bottom"),sQuery(id+"F0.wireOp",EDGE,"E2.top"),sQuery(id+"F0.wireOp",EDGE,"E2.left"),sQuery(id+"F0.wireOp",EDGE,"E2.right")])]}),"instanceName":"1"}),"instanceName":"1"}),"instanceName":"1"}),"instanceName":"1"}),"instanceName":"1"}),"instanceName":"1"});
            var Q548;
            Q548=makeQuery(id+"F11.opPattern","COPY",BODY,{"derivedFrom":makeQuery(id+"F10.opPattern","COPY",BODY,{"derivedFrom":makeQuery(id+"F9.opPattern","COPY",BODY,{"derivedFrom":makeQuery(id+"F8.opPattern","COPY",BODY,{"derivedFrom":makeQuery(id+"F4.opPattern","COPY",BODY,{"derivedFrom":makeQuery(id+"F3.opPattern","COPY",BODY,{"derivedFrom":makeQuery(id+"F2.opPattern","COPY",BODY,{"derivedFrom":makeQuery(id+"F1.opExtrude","SWEPT_BODY",BODY,{"disambiguationData":[OSD([sQuery(id+"F0.wireOp",EDGE,"E0.bottom"),sQuery(id+"F0.wireOp",EDGE,"E0.top"),sQuery(id+"F0.wireOp",EDGE,"E0.left"),sQuery(id+"F0.wireOp",EDGE,"E0.right")])]}),"instanceName":"1"}),"instanceName":"1"}),"instanceName":"1"}),"instanceName":"1"}),"instanceName":"1"}),"instanceName":"1"}),"instanceName":"1"});
            var Q549;
            Q549=makeQuery(id+"F11.opPattern","COPY",BODY,{"derivedFrom":makeQuery(id+"F10.opPattern","COPY",BODY,{"derivedFrom":makeQuery(id+"F9.opPattern","COPY",BODY,{"derivedFrom":makeQuery(id+"F8.opPattern","COPY",BODY,{"derivedFrom":makeQuery(id+"F4.opPattern","COPY",BODY,{"derivedFrom":makeQuery(id+"F3.opPattern","COPY",BODY,{"derivedFrom":makeQuery(id+"F2.opPattern","COPY",BODY,{"derivedFrom":makeQuery(id+"F1.opExtrude","SWEPT_BODY",BODY,{"disambiguationData":[OSD([sQuery(id+"F0.wireOp",EDGE,"E1.bottom"),sQuery(id+"F0.wireOp",EDGE,"E1.top"),sQuery(id+"F0.wireOp",EDGE,"E1.left"),sQuery(id+"F0.wireOp",EDGE,"E1.right")])]}),"instanceName":"1"}),"instanceName":"1"}),"instanceName":"1"}),"instanceName":"1"}),"instanceName":"1"}),"instanceName":"1"}),"instanceName":"1"});
            var Q550;
            Q550=makeQuery(id+"F11.opPattern","COPY",BODY,{"derivedFrom":makeQuery(id+"F10.opPattern","COPY",BODY,{"derivedFrom":makeQuery(id+"F9.opPattern","COPY",BODY,{"derivedFrom":makeQuery(id+"F8.opPattern","COPY",BODY,{"derivedFrom":makeQuery(id+"F4.opPattern","COPY",BODY,{"derivedFrom":makeQuery(id+"F3.opPattern","COPY",BODY,{"derivedFrom":makeQuery(id+"F2.opPattern","COPY",BODY,{"derivedFrom":makeQuery(id+"F1.opExtrude","SWEPT_BODY",BODY,{"disambiguationData":[OSD([sQuery(id+"F0.wireOp",EDGE,"E2.bottom"),sQuery(id+"F0.wireOp",EDGE,"E2.top"),sQuery(id+"F0.wireOp",EDGE,"E2.left"),sQuery(id+"F0.wireOp",EDGE,"E2.right")])]}),"instanceName":"1"}),"instanceName":"1"}),"instanceName":"1"}),"instanceName":"1"}),"instanceName":"1"}),"instanceName":"1"}),"instanceName":"1"});
            var Q551;
            Q551=makeQuery(id+"F11.opPattern","COPY",BODY,{"derivedFrom":makeQuery(id+"F10.opPattern","COPY",BODY,{"derivedFrom":makeQuery(id+"F9.opPattern","COPY",BODY,{"derivedFrom":makeQuery(id+"F8.opPattern","COPY",BODY,{"derivedFrom":makeQuery(id+"F5.opPattern","COPY",BODY,{"derivedFrom":makeQuery(id+"F4.opPattern","COPY",BODY,{"derivedFrom":makeQuery(id+"F3.opPattern","COPY",BODY,{"derivedFrom":makeQuery(id+"F2.opPattern","COPY",BODY,{"derivedFrom":makeQuery(id+"F1.opExtrude","SWEPT_BODY",BODY,{"disambiguationData":[OSD([sQuery(id+"F0.wireOp",EDGE,"E0.bottom"),sQuery(id+"F0.wireOp",EDGE,"E0.top"),sQuery(id+"F0.wireOp",EDGE,"E0.left"),sQuery(id+"F0.wireOp",EDGE,"E0.right")])]}),"instanceName":"1"}),"instanceName":"1"}),"instanceName":"1"}),"instanceName":"1"}),"instanceName":"1"}),"instanceName":"1"}),"instanceName":"1"}),"instanceName":"1"});
            var Q552;
            Q552=makeQuery(id+"F11.opPattern","COPY",BODY,{"derivedFrom":makeQuery(id+"F10.opPattern","COPY",BODY,{"derivedFrom":makeQuery(id+"F9.opPattern","COPY",BODY,{"derivedFrom":makeQuery(id+"F8.opPattern","COPY",BODY,{"derivedFrom":makeQuery(id+"F5.opPattern","COPY",BODY,{"derivedFrom":makeQuery(id+"F4.opPattern","COPY",BODY,{"derivedFrom":makeQuery(id+"F3.opPattern","COPY",BODY,{"derivedFrom":makeQuery(id+"F2.opPattern","COPY",BODY,{"derivedFrom":makeQuery(id+"F1.opExtrude","SWEPT_BODY",BODY,{"disambiguationData":[OSD([sQuery(id+"F0.wireOp",EDGE,"E1.bottom"),sQuery(id+"F0.wireOp",EDGE,"E1.top"),sQuery(id+"F0.wireOp",EDGE,"E1.left"),sQuery(id+"F0.wireOp",EDGE,"E1.right")])]}),"instanceName":"1"}),"instanceName":"1"}),"instanceName":"1"}),"instanceName":"1"}),"instanceName":"1"}),"instanceName":"1"}),"instanceName":"1"}),"instanceName":"1"});
            var Q553;
            Q553=makeQuery(id+"F11.opPattern","COPY",BODY,{"derivedFrom":makeQuery(id+"F10.opPattern","COPY",BODY,{"derivedFrom":makeQuery(id+"F9.opPattern","COPY",BODY,{"derivedFrom":makeQuery(id+"F8.opPattern","COPY",BODY,{"derivedFrom":makeQuery(id+"F5.opPattern","COPY",BODY,{"derivedFrom":makeQuery(id+"F4.opPattern","COPY",BODY,{"derivedFrom":makeQuery(id+"F3.opPattern","COPY",BODY,{"derivedFrom":makeQuery(id+"F2.opPattern","COPY",BODY,{"derivedFrom":makeQuery(id+"F1.opExtrude","SWEPT_BODY",BODY,{"disambiguationData":[OSD([sQuery(id+"F0.wireOp",EDGE,"E2.bottom"),sQuery(id+"F0.wireOp",EDGE,"E2.top"),sQuery(id+"F0.wireOp",EDGE,"E2.left"),sQuery(id+"F0.wireOp",EDGE,"E2.right")])]}),"instanceName":"1"}),"instanceName":"1"}),"instanceName":"1"}),"instanceName":"1"}),"instanceName":"1"}),"instanceName":"1"}),"instanceName":"1"}),"instanceName":"1"});
            var Q554;
            Q554=makeQuery(id+"F11.opPattern","COPY",BODY,{"derivedFrom":makeQuery(id+"F10.opPattern","COPY",BODY,{"derivedFrom":makeQuery(id+"F9.opPattern","COPY",BODY,{"derivedFrom":makeQuery(id+"F8.opPattern","COPY",BODY,{"derivedFrom":makeQuery(id+"F6.opPattern","COPY",BODY,{"derivedFrom":makeQuery(id+"F5.opPattern","COPY",BODY,{"derivedFrom":makeQuery(id+"F4.opPattern","COPY",BODY,{"derivedFrom":makeQuery(id+"F3.opPattern","COPY",BODY,{"derivedFrom":makeQuery(id+"F2.opPattern","COPY",BODY,{"derivedFrom":makeQuery(id+"F1.opExtrude","SWEPT_BODY",BODY,{"disambiguationData":[OSD([sQuery(id+"F0.wireOp",EDGE,"E0.bottom"),sQuery(id+"F0.wireOp",EDGE,"E0.top"),sQuery(id+"F0.wireOp",EDGE,"E0.left"),sQuery(id+"F0.wireOp",EDGE,"E0.right")])]}),"instanceName":"1"}),"instanceName":"1"}),"instanceName":"1"}),"instanceName":"1"}),"instanceName":"1"}),"instanceName":"1"}),"instanceName":"1"}),"instanceName":"1"}),"instanceName":"1"});
            var Q555;
            Q555=makeQuery(id+"F11.opPattern","COPY",BODY,{"derivedFrom":makeQuery(id+"F10.opPattern","COPY",BODY,{"derivedFrom":makeQuery(id+"F9.opPattern","COPY",BODY,{"derivedFrom":makeQuery(id+"F8.opPattern","COPY",BODY,{"derivedFrom":makeQuery(id+"F6.opPattern","COPY",BODY,{"derivedFrom":makeQuery(id+"F5.opPattern","COPY",BODY,{"derivedFrom":makeQuery(id+"F4.opPattern","COPY",BODY,{"derivedFrom":makeQuery(id+"F3.opPattern","COPY",BODY,{"derivedFrom":makeQuery(id+"F2.opPattern","COPY",BODY,{"derivedFrom":makeQuery(id+"F1.opExtrude","SWEPT_BODY",BODY,{"disambiguationData":[OSD([sQuery(id+"F0.wireOp",EDGE,"E1.bottom"),sQuery(id+"F0.wireOp",EDGE,"E1.top"),sQuery(id+"F0.wireOp",EDGE,"E1.left"),sQuery(id+"F0.wireOp",EDGE,"E1.right")])]}),"instanceName":"1"}),"instanceName":"1"}),"instanceName":"1"}),"instanceName":"1"}),"instanceName":"1"}),"instanceName":"1"}),"instanceName":"1"}),"instanceName":"1"}),"instanceName":"1"});
            var Q556;
            Q556=makeQuery(id+"F11.opPattern","COPY",BODY,{"derivedFrom":makeQuery(id+"F10.opPattern","COPY",BODY,{"derivedFrom":makeQuery(id+"F9.opPattern","COPY",BODY,{"derivedFrom":makeQuery(id+"F8.opPattern","COPY",BODY,{"derivedFrom":makeQuery(id+"F6.opPattern","COPY",BODY,{"derivedFrom":makeQuery(id+"F5.opPattern","COPY",BODY,{"derivedFrom":makeQuery(id+"F4.opPattern","COPY",BODY,{"derivedFrom":makeQuery(id+"F3.opPattern","COPY",BODY,{"derivedFrom":makeQuery(id+"F2.opPattern","COPY",BODY,{"derivedFrom":makeQuery(id+"F1.opExtrude","SWEPT_BODY",BODY,{"disambiguationData":[OSD([sQuery(id+"F0.wireOp",EDGE,"E2.bottom"),sQuery(id+"F0.wireOp",EDGE,"E2.top"),sQuery(id+"F0.wireOp",EDGE,"E2.left"),sQuery(id+"F0.wireOp",EDGE,"E2.right")])]}),"instanceName":"1"}),"instanceName":"1"}),"instanceName":"1"}),"instanceName":"1"}),"instanceName":"1"}),"instanceName":"1"}),"instanceName":"1"}),"instanceName":"1"}),"instanceName":"1"});
            var Q557;
            Q557=makeQuery(id+"F11.opPattern","COPY",BODY,{"derivedFrom":makeQuery(id+"F10.opPattern","COPY",BODY,{"derivedFrom":makeQuery(id+"F9.opPattern","COPY",BODY,{"derivedFrom":makeQuery(id+"F8.opPattern","COPY",BODY,{"derivedFrom":makeQuery(id+"F7.opPattern","COPY",BODY,{"derivedFrom":makeQuery(id+"F1.opExtrude","SWEPT_BODY",BODY,{"disambiguationData":[OSD([sQuery(id+"F0.wireOp",EDGE,"E0.bottom"),sQuery(id+"F0.wireOp",EDGE,"E0.top"),sQuery(id+"F0.wireOp",EDGE,"E0.left"),sQuery(id+"F0.wireOp",EDGE,"E0.right")])]}),"instanceName":"1"}),"instanceName":"1"}),"instanceName":"1"}),"instanceName":"1"}),"instanceName":"1"});
            var Q558;
            Q558=makeQuery(id+"F11.opPattern","COPY",BODY,{"derivedFrom":makeQuery(id+"F10.opPattern","COPY",BODY,{"derivedFrom":makeQuery(id+"F9.opPattern","COPY",BODY,{"derivedFrom":makeQuery(id+"F8.opPattern","COPY",BODY,{"derivedFrom":makeQuery(id+"F7.opPattern","COPY",BODY,{"derivedFrom":makeQuery(id+"F1.opExtrude","SWEPT_BODY",BODY,{"disambiguationData":[OSD([sQuery(id+"F0.wireOp",EDGE,"E1.bottom"),sQuery(id+"F0.wireOp",EDGE,"E1.top"),sQuery(id+"F0.wireOp",EDGE,"E1.left"),sQuery(id+"F0.wireOp",EDGE,"E1.right")])]}),"instanceName":"1"}),"instanceName":"1"}),"instanceName":"1"}),"instanceName":"1"}),"instanceName":"1"});
            var Q559;
            Q559=makeQuery(id+"F11.opPattern","COPY",BODY,{"derivedFrom":makeQuery(id+"F10.opPattern","COPY",BODY,{"derivedFrom":makeQuery(id+"F9.opPattern","COPY",BODY,{"derivedFrom":makeQuery(id+"F8.opPattern","COPY",BODY,{"derivedFrom":makeQuery(id+"F7.opPattern","COPY",BODY,{"derivedFrom":makeQuery(id+"F1.opExtrude","SWEPT_BODY",BODY,{"disambiguationData":[OSD([sQuery(id+"F0.wireOp",EDGE,"E2.bottom"),sQuery(id+"F0.wireOp",EDGE,"E2.top"),sQuery(id+"F0.wireOp",EDGE,"E2.left"),sQuery(id+"F0.wireOp",EDGE,"E2.right")])]}),"instanceName":"1"}),"instanceName":"1"}),"instanceName":"1"}),"instanceName":"1"}),"instanceName":"1"});
            var Q560;
            Q560=makeQuery(id+"F11.opPattern","COPY",BODY,{"derivedFrom":makeQuery(id+"F10.opPattern","COPY",BODY,{"derivedFrom":makeQuery(id+"F9.opPattern","COPY",BODY,{"derivedFrom":makeQuery(id+"F8.opPattern","COPY",BODY,{"derivedFrom":makeQuery(id+"F7.opPattern","COPY",BODY,{"derivedFrom":makeQuery(id+"F2.opPattern","COPY",BODY,{"derivedFrom":makeQuery(id+"F1.opExtrude","SWEPT_BODY",BODY,{"disambiguationData":[OSD([sQuery(id+"F0.wireOp",EDGE,"E0.bottom"),sQuery(id+"F0.wireOp",EDGE,"E0.top"),sQuery(id+"F0.wireOp",EDGE,"E0.left"),sQuery(id+"F0.wireOp",EDGE,"E0.right")])]}),"instanceName":"1"}),"instanceName":"1"}),"instanceName":"1"}),"instanceName":"1"}),"instanceName":"1"}),"instanceName":"1"});
            var Q561;
            Q561=makeQuery(id+"F11.opPattern","COPY",BODY,{"derivedFrom":makeQuery(id+"F10.opPattern","COPY",BODY,{"derivedFrom":makeQuery(id+"F9.opPattern","COPY",BODY,{"derivedFrom":makeQuery(id+"F8.opPattern","COPY",BODY,{"derivedFrom":makeQuery(id+"F7.opPattern","COPY",BODY,{"derivedFrom":makeQuery(id+"F2.opPattern","COPY",BODY,{"derivedFrom":makeQuery(id+"F1.opExtrude","SWEPT_BODY",BODY,{"disambiguationData":[OSD([sQuery(id+"F0.wireOp",EDGE,"E1.bottom"),sQuery(id+"F0.wireOp",EDGE,"E1.top"),sQuery(id+"F0.wireOp",EDGE,"E1.left"),sQuery(id+"F0.wireOp",EDGE,"E1.right")])]}),"instanceName":"1"}),"instanceName":"1"}),"instanceName":"1"}),"instanceName":"1"}),"instanceName":"1"}),"instanceName":"1"});
            var Q562;
            Q562=makeQuery(id+"F11.opPattern","COPY",BODY,{"derivedFrom":makeQuery(id+"F10.opPattern","COPY",BODY,{"derivedFrom":makeQuery(id+"F9.opPattern","COPY",BODY,{"derivedFrom":makeQuery(id+"F8.opPattern","COPY",BODY,{"derivedFrom":makeQuery(id+"F7.opPattern","COPY",BODY,{"derivedFrom":makeQuery(id+"F2.opPattern","COPY",BODY,{"derivedFrom":makeQuery(id+"F1.opExtrude","SWEPT_BODY",BODY,{"disambiguationData":[OSD([sQuery(id+"F0.wireOp",EDGE,"E2.bottom"),sQuery(id+"F0.wireOp",EDGE,"E2.top"),sQuery(id+"F0.wireOp",EDGE,"E2.left"),sQuery(id+"F0.wireOp",EDGE,"E2.right")])]}),"instanceName":"1"}),"instanceName":"1"}),"instanceName":"1"}),"instanceName":"1"}),"instanceName":"1"}),"instanceName":"1"});
            var Q563;
            Q563=makeQuery(id+"F11.opPattern","COPY",BODY,{"derivedFrom":makeQuery(id+"F10.opPattern","COPY",BODY,{"derivedFrom":makeQuery(id+"F9.opPattern","COPY",BODY,{"derivedFrom":makeQuery(id+"F8.opPattern","COPY",BODY,{"derivedFrom":makeQuery(id+"F7.opPattern","COPY",BODY,{"derivedFrom":makeQuery(id+"F3.opPattern","COPY",BODY,{"derivedFrom":makeQuery(id+"F2.opPattern","COPY",BODY,{"derivedFrom":makeQuery(id+"F1.opExtrude","SWEPT_BODY",BODY,{"disambiguationData":[OSD([sQuery(id+"F0.wireOp",EDGE,"E0.bottom"),sQuery(id+"F0.wireOp",EDGE,"E0.top"),sQuery(id+"F0.wireOp",EDGE,"E0.left"),sQuery(id+"F0.wireOp",EDGE,"E0.right")])]}),"instanceName":"1"}),"instanceName":"1"}),"instanceName":"1"}),"instanceName":"1"}),"instanceName":"1"}),"instanceName":"1"}),"instanceName":"1"});
            var Q564;
            Q564=makeQuery(id+"F11.opPattern","COPY",BODY,{"derivedFrom":makeQuery(id+"F10.opPattern","COPY",BODY,{"derivedFrom":makeQuery(id+"F9.opPattern","COPY",BODY,{"derivedFrom":makeQuery(id+"F8.opPattern","COPY",BODY,{"derivedFrom":makeQuery(id+"F7.opPattern","COPY",BODY,{"derivedFrom":makeQuery(id+"F3.opPattern","COPY",BODY,{"derivedFrom":makeQuery(id+"F2.opPattern","COPY",BODY,{"derivedFrom":makeQuery(id+"F1.opExtrude","SWEPT_BODY",BODY,{"disambiguationData":[OSD([sQuery(id+"F0.wireOp",EDGE,"E1.bottom"),sQuery(id+"F0.wireOp",EDGE,"E1.top"),sQuery(id+"F0.wireOp",EDGE,"E1.left"),sQuery(id+"F0.wireOp",EDGE,"E1.right")])]}),"instanceName":"1"}),"instanceName":"1"}),"instanceName":"1"}),"instanceName":"1"}),"instanceName":"1"}),"instanceName":"1"}),"instanceName":"1"});
            var Q565;
            Q565=makeQuery(id+"F11.opPattern","COPY",BODY,{"derivedFrom":makeQuery(id+"F10.opPattern","COPY",BODY,{"derivedFrom":makeQuery(id+"F9.opPattern","COPY",BODY,{"derivedFrom":makeQuery(id+"F8.opPattern","COPY",BODY,{"derivedFrom":makeQuery(id+"F7.opPattern","COPY",BODY,{"derivedFrom":makeQuery(id+"F3.opPattern","COPY",BODY,{"derivedFrom":makeQuery(id+"F2.opPattern","COPY",BODY,{"derivedFrom":makeQuery(id+"F1.opExtrude","SWEPT_BODY",BODY,{"disambiguationData":[OSD([sQuery(id+"F0.wireOp",EDGE,"E2.bottom"),sQuery(id+"F0.wireOp",EDGE,"E2.top"),sQuery(id+"F0.wireOp",EDGE,"E2.left"),sQuery(id+"F0.wireOp",EDGE,"E2.right")])]}),"instanceName":"1"}),"instanceName":"1"}),"instanceName":"1"}),"instanceName":"1"}),"instanceName":"1"}),"instanceName":"1"}),"instanceName":"1"});
            var Q566;
            Q566=makeQuery(id+"F11.opPattern","COPY",BODY,{"derivedFrom":makeQuery(id+"F10.opPattern","COPY",BODY,{"derivedFrom":makeQuery(id+"F9.opPattern","COPY",BODY,{"derivedFrom":makeQuery(id+"F8.opPattern","COPY",BODY,{"derivedFrom":makeQuery(id+"F7.opPattern","COPY",BODY,{"derivedFrom":makeQuery(id+"F4.opPattern","COPY",BODY,{"derivedFrom":makeQuery(id+"F3.opPattern","COPY",BODY,{"derivedFrom":makeQuery(id+"F2.opPattern","COPY",BODY,{"derivedFrom":makeQuery(id+"F1.opExtrude","SWEPT_BODY",BODY,{"disambiguationData":[OSD([sQuery(id+"F0.wireOp",EDGE,"E0.bottom"),sQuery(id+"F0.wireOp",EDGE,"E0.top"),sQuery(id+"F0.wireOp",EDGE,"E0.left"),sQuery(id+"F0.wireOp",EDGE,"E0.right")])]}),"instanceName":"1"}),"instanceName":"1"}),"instanceName":"1"}),"instanceName":"1"}),"instanceName":"1"}),"instanceName":"1"}),"instanceName":"1"}),"instanceName":"1"});
            var Q567;
            Q567=makeQuery(id+"F11.opPattern","COPY",BODY,{"derivedFrom":makeQuery(id+"F10.opPattern","COPY",BODY,{"derivedFrom":makeQuery(id+"F9.opPattern","COPY",BODY,{"derivedFrom":makeQuery(id+"F8.opPattern","COPY",BODY,{"derivedFrom":makeQuery(id+"F7.opPattern","COPY",BODY,{"derivedFrom":makeQuery(id+"F4.opPattern","COPY",BODY,{"derivedFrom":makeQuery(id+"F3.opPattern","COPY",BODY,{"derivedFrom":makeQuery(id+"F2.opPattern","COPY",BODY,{"derivedFrom":makeQuery(id+"F1.opExtrude","SWEPT_BODY",BODY,{"disambiguationData":[OSD([sQuery(id+"F0.wireOp",EDGE,"E1.bottom"),sQuery(id+"F0.wireOp",EDGE,"E1.top"),sQuery(id+"F0.wireOp",EDGE,"E1.left"),sQuery(id+"F0.wireOp",EDGE,"E1.right")])]}),"instanceName":"1"}),"instanceName":"1"}),"instanceName":"1"}),"instanceName":"1"}),"instanceName":"1"}),"instanceName":"1"}),"instanceName":"1"}),"instanceName":"1"});
            var Q568;
            Q568=makeQuery(id+"F11.opPattern","COPY",BODY,{"derivedFrom":makeQuery(id+"F10.opPattern","COPY",BODY,{"derivedFrom":makeQuery(id+"F9.opPattern","COPY",BODY,{"derivedFrom":makeQuery(id+"F8.opPattern","COPY",BODY,{"derivedFrom":makeQuery(id+"F7.opPattern","COPY",BODY,{"derivedFrom":makeQuery(id+"F4.opPattern","COPY",BODY,{"derivedFrom":makeQuery(id+"F3.opPattern","COPY",BODY,{"derivedFrom":makeQuery(id+"F2.opPattern","COPY",BODY,{"derivedFrom":makeQuery(id+"F1.opExtrude","SWEPT_BODY",BODY,{"disambiguationData":[OSD([sQuery(id+"F0.wireOp",EDGE,"E2.bottom"),sQuery(id+"F0.wireOp",EDGE,"E2.top"),sQuery(id+"F0.wireOp",EDGE,"E2.left"),sQuery(id+"F0.wireOp",EDGE,"E2.right")])]}),"instanceName":"1"}),"instanceName":"1"}),"instanceName":"1"}),"instanceName":"1"}),"instanceName":"1"}),"instanceName":"1"}),"instanceName":"1"}),"instanceName":"1"});
            var Q569;
            Q569=makeQuery(id+"F11.opPattern","COPY",BODY,{"derivedFrom":makeQuery(id+"F10.opPattern","COPY",BODY,{"derivedFrom":makeQuery(id+"F9.opPattern","COPY",BODY,{"derivedFrom":makeQuery(id+"F8.opPattern","COPY",BODY,{"derivedFrom":makeQuery(id+"F7.opPattern","COPY",BODY,{"derivedFrom":makeQuery(id+"F5.opPattern","COPY",BODY,{"derivedFrom":makeQuery(id+"F4.opPattern","COPY",BODY,{"derivedFrom":makeQuery(id+"F3.opPattern","COPY",BODY,{"derivedFrom":makeQuery(id+"F2.opPattern","COPY",BODY,{"derivedFrom":makeQuery(id+"F1.opExtrude","SWEPT_BODY",BODY,{"disambiguationData":[OSD([sQuery(id+"F0.wireOp",EDGE,"E0.bottom"),sQuery(id+"F0.wireOp",EDGE,"E0.top"),sQuery(id+"F0.wireOp",EDGE,"E0.left"),sQuery(id+"F0.wireOp",EDGE,"E0.right")])]}),"instanceName":"1"}),"instanceName":"1"}),"instanceName":"1"}),"instanceName":"1"}),"instanceName":"1"}),"instanceName":"1"}),"instanceName":"1"}),"instanceName":"1"}),"instanceName":"1"});
            var Q570;
            Q570=makeQuery(id+"F11.opPattern","COPY",BODY,{"derivedFrom":makeQuery(id+"F10.opPattern","COPY",BODY,{"derivedFrom":makeQuery(id+"F9.opPattern","COPY",BODY,{"derivedFrom":makeQuery(id+"F8.opPattern","COPY",BODY,{"derivedFrom":makeQuery(id+"F7.opPattern","COPY",BODY,{"derivedFrom":makeQuery(id+"F5.opPattern","COPY",BODY,{"derivedFrom":makeQuery(id+"F4.opPattern","COPY",BODY,{"derivedFrom":makeQuery(id+"F3.opPattern","COPY",BODY,{"derivedFrom":makeQuery(id+"F2.opPattern","COPY",BODY,{"derivedFrom":makeQuery(id+"F1.opExtrude","SWEPT_BODY",BODY,{"disambiguationData":[OSD([sQuery(id+"F0.wireOp",EDGE,"E1.bottom"),sQuery(id+"F0.wireOp",EDGE,"E1.top"),sQuery(id+"F0.wireOp",EDGE,"E1.left"),sQuery(id+"F0.wireOp",EDGE,"E1.right")])]}),"instanceName":"1"}),"instanceName":"1"}),"instanceName":"1"}),"instanceName":"1"}),"instanceName":"1"}),"instanceName":"1"}),"instanceName":"1"}),"instanceName":"1"}),"instanceName":"1"});
            var Q571;
            Q571=makeQuery(id+"F11.opPattern","COPY",BODY,{"derivedFrom":makeQuery(id+"F10.opPattern","COPY",BODY,{"derivedFrom":makeQuery(id+"F9.opPattern","COPY",BODY,{"derivedFrom":makeQuery(id+"F8.opPattern","COPY",BODY,{"derivedFrom":makeQuery(id+"F7.opPattern","COPY",BODY,{"derivedFrom":makeQuery(id+"F5.opPattern","COPY",BODY,{"derivedFrom":makeQuery(id+"F4.opPattern","COPY",BODY,{"derivedFrom":makeQuery(id+"F3.opPattern","COPY",BODY,{"derivedFrom":makeQuery(id+"F2.opPattern","COPY",BODY,{"derivedFrom":makeQuery(id+"F1.opExtrude","SWEPT_BODY",BODY,{"disambiguationData":[OSD([sQuery(id+"F0.wireOp",EDGE,"E2.bottom"),sQuery(id+"F0.wireOp",EDGE,"E2.top"),sQuery(id+"F0.wireOp",EDGE,"E2.left"),sQuery(id+"F0.wireOp",EDGE,"E2.right")])]}),"instanceName":"1"}),"instanceName":"1"}),"instanceName":"1"}),"instanceName":"1"}),"instanceName":"1"}),"instanceName":"1"}),"instanceName":"1"}),"instanceName":"1"}),"instanceName":"1"});
            var Q572;
            Q572=makeQuery(id+"F11.opPattern","COPY",BODY,{"derivedFrom":makeQuery(id+"F10.opPattern","COPY",BODY,{"derivedFrom":makeQuery(id+"F9.opPattern","COPY",BODY,{"derivedFrom":makeQuery(id+"F8.opPattern","COPY",BODY,{"derivedFrom":makeQuery(id+"F7.opPattern","COPY",BODY,{"derivedFrom":makeQuery(id+"F6.opPattern","COPY",BODY,{"derivedFrom":makeQuery(id+"F5.opPattern","COPY",BODY,{"derivedFrom":makeQuery(id+"F4.opPattern","COPY",BODY,{"derivedFrom":makeQuery(id+"F3.opPattern","COPY",BODY,{"derivedFrom":makeQuery(id+"F2.opPattern","COPY",BODY,{"derivedFrom":makeQuery(id+"F1.opExtrude","SWEPT_BODY",BODY,{"disambiguationData":[OSD([sQuery(id+"F0.wireOp",EDGE,"E0.bottom"),sQuery(id+"F0.wireOp",EDGE,"E0.top"),sQuery(id+"F0.wireOp",EDGE,"E0.left"),sQuery(id+"F0.wireOp",EDGE,"E0.right")])]}),"instanceName":"1"}),"instanceName":"1"}),"instanceName":"1"}),"instanceName":"1"}),"instanceName":"1"}),"instanceName":"1"}),"instanceName":"1"}),"instanceName":"1"}),"instanceName":"1"}),"instanceName":"1"});
            var Q573;
            Q573=makeQuery(id+"F11.opPattern","COPY",BODY,{"derivedFrom":makeQuery(id+"F10.opPattern","COPY",BODY,{"derivedFrom":makeQuery(id+"F9.opPattern","COPY",BODY,{"derivedFrom":makeQuery(id+"F8.opPattern","COPY",BODY,{"derivedFrom":makeQuery(id+"F7.opPattern","COPY",BODY,{"derivedFrom":makeQuery(id+"F6.opPattern","COPY",BODY,{"derivedFrom":makeQuery(id+"F5.opPattern","COPY",BODY,{"derivedFrom":makeQuery(id+"F4.opPattern","COPY",BODY,{"derivedFrom":makeQuery(id+"F3.opPattern","COPY",BODY,{"derivedFrom":makeQuery(id+"F2.opPattern","COPY",BODY,{"derivedFrom":makeQuery(id+"F1.opExtrude","SWEPT_BODY",BODY,{"disambiguationData":[OSD([sQuery(id+"F0.wireOp",EDGE,"E1.bottom"),sQuery(id+"F0.wireOp",EDGE,"E1.top"),sQuery(id+"F0.wireOp",EDGE,"E1.left"),sQuery(id+"F0.wireOp",EDGE,"E1.right")])]}),"instanceName":"1"}),"instanceName":"1"}),"instanceName":"1"}),"instanceName":"1"}),"instanceName":"1"}),"instanceName":"1"}),"instanceName":"1"}),"instanceName":"1"}),"instanceName":"1"}),"instanceName":"1"});
            var Q574;
            Q574=makeQuery(id+"F11.opPattern","COPY",BODY,{"derivedFrom":makeQuery(id+"F10.opPattern","COPY",BODY,{"derivedFrom":makeQuery(id+"F9.opPattern","COPY",BODY,{"derivedFrom":makeQuery(id+"F8.opPattern","COPY",BODY,{"derivedFrom":makeQuery(id+"F7.opPattern","COPY",BODY,{"derivedFrom":makeQuery(id+"F6.opPattern","COPY",BODY,{"derivedFrom":makeQuery(id+"F5.opPattern","COPY",BODY,{"derivedFrom":makeQuery(id+"F4.opPattern","COPY",BODY,{"derivedFrom":makeQuery(id+"F3.opPattern","COPY",BODY,{"derivedFrom":makeQuery(id+"F2.opPattern","COPY",BODY,{"derivedFrom":makeQuery(id+"F1.opExtrude","SWEPT_BODY",BODY,{"disambiguationData":[OSD([sQuery(id+"F0.wireOp",EDGE,"E2.bottom"),sQuery(id+"F0.wireOp",EDGE,"E2.top"),sQuery(id+"F0.wireOp",EDGE,"E2.left"),sQuery(id+"F0.wireOp",EDGE,"E2.right")])]}),"instanceName":"1"}),"instanceName":"1"}),"instanceName":"1"}),"instanceName":"1"}),"instanceName":"1"}),"instanceName":"1"}),"instanceName":"1"}),"instanceName":"1"}),"instanceName":"1"}),"instanceName":"1"});
            var Q575;
            Q575=makeQuery(id+"F1.opExtrude","SWEPT_BODY",BODY,{"disambiguationData":[OSD([sQuery(id+"F0.wireOp",EDGE,"E2.bottom"),sQuery(id+"F0.wireOp",EDGE,"E2.top"),sQuery(id+"F0.wireOp",EDGE,"E2.left"),sQuery(id+"F0.wireOp",EDGE,"E2.right")])]});
            transform(context, id + "F12", {"entities" : qUnion([Q0, Q1, Q2, Q3, Q4, Q5, Q6, Q7, Q8, Q9, Q10, Q11, Q12, Q13, Q14, Q15, Q16, Q17, Q18, Q19, Q20, Q21, Q22, Q23, Q24, Q25, Q26, Q27, Q28, Q29, Q30, Q31, Q32, Q33, Q34, Q35, Q36, Q37, Q38, Q39, Q40, Q41, Q42, Q43, Q44, Q45, Q46, Q47, Q48, Q49, Q50, Q51, Q52, Q53, Q54, Q55, Q56, Q57, Q58, Q59, Q60, Q61, Q62, Q63, Q64, Q65, Q66, Q67, Q68, Q69, Q70, Q71, Q72, Q73, Q74, Q75, Q76, Q77, Q78, Q79, Q80, Q81, Q82, Q83, Q84, Q85, Q86, Q87, Q88, Q89, Q90, Q91, Q92, Q93, Q94, Q95, Q96, Q97, Q98, Q99, Q100, Q101, Q102, Q103, Q104, Q105, Q106, Q107, Q108, Q109, Q110, Q111, Q112, Q113, Q114, Q115, Q116, Q117, Q118, Q119, Q120, Q121, Q122, Q123, Q124, Q125, Q126, Q127, Q128, Q129, Q130, Q131, Q132, Q133, Q134, Q135, Q136, Q137, Q138, Q139, Q140, Q141, Q142, Q143, Q144, Q145, Q146, Q147, Q148, Q149, Q150, Q151, Q152, Q153, Q154, Q155, Q156, Q157, Q158, Q159, Q160, Q161, Q162, Q163, Q164, Q165, Q166, Q167, Q168, Q169, Q170, Q171, Q172, Q173, Q174, Q175, Q176, Q177, Q178, Q179, Q180, Q181, Q182, Q183, Q184, Q185, Q186, Q187, Q188, Q189, Q190, Q191, Q192, Q193, Q194, Q195, Q196, Q197, Q198, Q199, Q200, Q201, Q202, Q203, Q204, Q205, Q206, Q207, Q208, Q209, Q210, Q211, Q212, Q213, Q214, Q215, Q216, Q217, Q218, Q219, Q220, Q221, Q222, Q223, Q224, Q225, Q226, Q227, Q228, Q229, Q230, Q231, Q232, Q233, Q234, Q235, Q236, Q237, Q238, Q239, Q240, Q241, Q242, Q243, Q244, Q245, Q246, Q247, Q248, Q249, Q250, Q251, Q252, Q253, Q254, Q255, Q256, Q257, Q258, Q259, Q260, Q261, Q262, Q263, Q264, Q265, Q266, Q267, Q268, Q269, Q270, Q271, Q272, Q273, Q274, Q275, Q276, Q277, Q278, Q279, Q280, Q281, Q282, Q283, Q284, Q285, Q286, Q287, Q288, Q289, Q290, Q291, Q292, Q293, Q294, Q295, Q296, Q297, Q298, Q299, Q300, Q301, Q302, Q303, Q304, Q305, Q306, Q307, Q308, Q309, Q310, Q311, Q312, Q313, Q314, Q315, Q316, Q317, Q318, Q319, Q320, Q321, Q322, Q323, Q324, Q325, Q326, Q327, Q328, Q329, Q330, Q331, Q332, Q333, Q334, Q335, Q336, Q337, Q338, Q339, Q340, Q341, Q342, Q343, Q344, Q345, Q346, Q347, Q348, Q349, Q350, Q351, Q352, Q353, Q354, Q355, Q356, Q357, Q358, Q359, Q360, Q361, Q362, Q363, Q364, Q365, Q366, Q367, Q368, Q369, Q370, Q371, Q372, Q373, Q374, Q375, Q376, Q377, Q378, Q379, Q380, Q381, Q382, Q383, Q384, Q385, Q386, Q387, Q388, Q389, Q390, Q391, Q392, Q393, Q394, Q395, Q396, Q397, Q398, Q399, Q400, Q401, Q402, Q403, Q404, Q405, Q406, Q407, Q408, Q409, Q410, Q411, Q412, Q413, Q414, Q415, Q416, Q417, Q418, Q419, Q420, Q421, Q422, Q423, Q424, Q425, Q426, Q427, Q428, Q429, Q430, Q431, Q432, Q433, Q434, Q435, Q436, Q437, Q438, Q439, Q440, Q441, Q442, Q443, Q444, Q445, Q446, Q447, Q448, Q449, Q450, Q451, Q452, Q453, Q454, Q455, Q456, Q457, Q458, Q459, Q460, Q461, Q462, Q463, Q464, Q465, Q466, Q467, Q468, Q469, Q470, Q471, Q472, Q473, Q474, Q475, Q476, Q477, Q478, Q479, Q480, Q481, Q482, Q483, Q484, Q485, Q486, Q487, Q488, Q489, Q490, Q491, Q492, Q493, Q494, Q495, Q496, Q497, Q498, Q499, Q500, Q501, Q502, Q503, Q504, Q505, Q506, Q507, Q508, Q509, Q510, Q511, Q512, Q513, Q514, Q515, Q516, Q517, Q518, Q519, Q520, Q521, Q522, Q523, Q524, Q525, Q526, Q527, Q528, Q529, Q530, Q531, Q532, Q533, Q534, Q535, Q536, Q537, Q538, Q539, Q540, Q541, Q542, Q543, Q544, Q545, Q546, Q547, Q548, Q549, Q550, Q551, Q552, Q553, Q554, Q555, Q556, Q557, Q558, Q559, Q560, Q561, Q562, Q563, Q564, Q565, Q566, Q567, Q568, Q569, Q570, Q571, Q572, Q573, Q574, Q575]), "transformType" : TransformType.TRANSLATION_3D, "dx" : 7236 * mm, "dy" : 3618 * mm, "dz" : 0 * mm, "makeCopy" : true});
        }
    });
